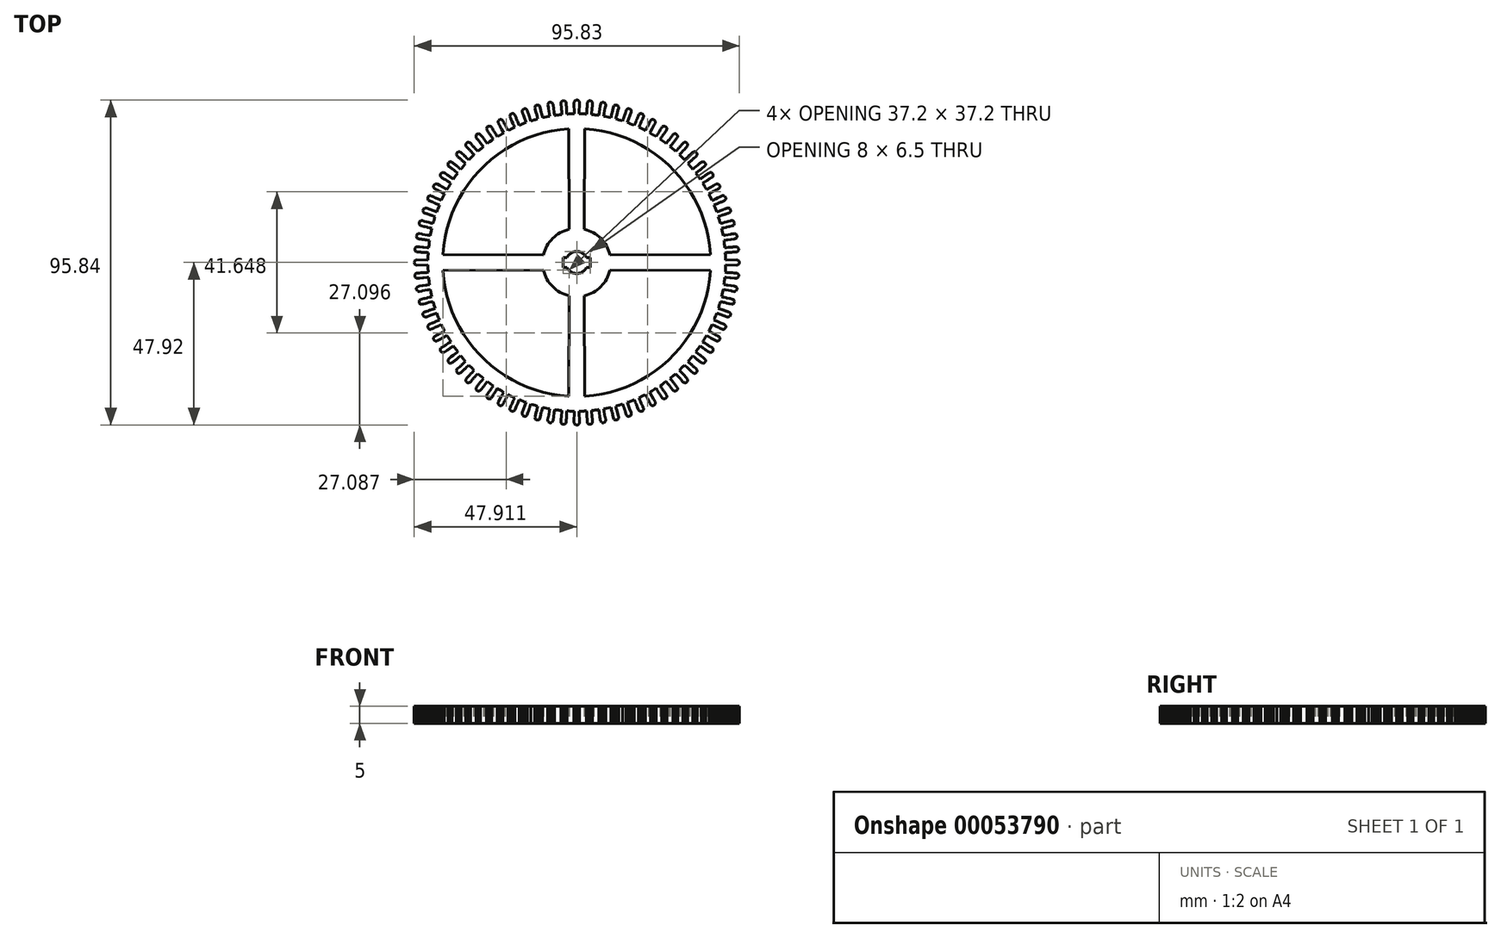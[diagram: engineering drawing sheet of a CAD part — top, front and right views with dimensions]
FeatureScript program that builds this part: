
annotation { "Feature Type Name" : "Feature", "Feature Type Description" : "" }
export const myFeature = defineFeature(function(context is Context, id is Id, definition is map)
    precondition{}
    {
        {
            var Q0;
            Q0=qCreatedBy(makeId("Top.planeOp"),FACE);
            var sketch = newSketch(context, id + "F0", { "sketchPlane" : qUnion([Q0])});
            skLineSegment(sketch, "E0", {"start": v(42.95, -0.72) * mm, "end": v(43.17, -0.73) * mm});
            skLineSegment(sketch, "E1", {"start": v(43.17, -0.73) * mm, "end": v(43.39, -0.73) * mm});
            skLineSegment(sketch, "E2", {"start": v(43.39, -0.73) * mm, "end": v(43.6, -0.73) * mm});
            skLineSegment(sketch, "E3", {"start": v(43.6, -0.73) * mm, "end": v(43.82, -0.74) * mm});
            skLineSegment(sketch, "E4", {"start": v(43.82, -0.74) * mm, "end": v(44.04, -0.74) * mm});
            skLineSegment(sketch, "E5", {"start": v(44.04, -0.74) * mm, "end": v(44.26, -0.74) * mm});
            skLineSegment(sketch, "E6", {"start": v(44.26, -0.74) * mm, "end": v(44.47, -0.75) * mm});
            skLineSegment(sketch, "E7", {"start": v(44.47, -0.75) * mm, "end": v(44.69, -0.75) * mm});
            skLineSegment(sketch, "E8", {"start": v(44.69, -0.75) * mm, "end": v(44.9, -0.75) * mm});
            skLineSegment(sketch, "E9", {"start": v(44.9, -0.75) * mm, "end": v(45.12, -0.76) * mm});
            skLineSegment(sketch, "E10", {"start": v(45.12, -0.76) * mm, "end": v(45.34, -0.76) * mm});
            skLineSegment(sketch, "E11", {"start": v(45.34, -0.76) * mm, "end": v(45.56, -0.76) * mm});
            skLineSegment(sketch, "E12", {"start": v(45.56, -0.76) * mm, "end": v(45.77, -0.77) * mm});
            skLineSegment(sketch, "E13", {"start": v(45.77, -0.77) * mm, "end": v(45.99, -0.77) * mm});
            skLineSegment(sketch, "E14", {"start": v(45.99, -0.77) * mm, "end": v(46.2, -0.78) * mm});
            skLineSegment(sketch, "E15", {"start": v(46.2, -0.78) * mm, "end": v(46.4, -0.75) * mm});
            skLineSegment(sketch, "E16", {"start": v(46.4, -0.75) * mm, "end": v(46.6, -0.67) * mm});
            skLineSegment(sketch, "E17", {"start": v(46.6, -0.67) * mm, "end": v(46.76, -0.55) * mm});
            skLineSegment(sketch, "E18", {"start": v(46.76, -0.55) * mm, "end": v(46.88, -0.39) * mm});
            skLineSegment(sketch, "E19", {"start": v(46.88, -0.39) * mm, "end": v(46.96, -0.2) * mm});
            skLineSegment(sketch, "E20", {"start": v(46.96, -0.2) * mm, "end": v(46.99, 0) * mm});
            skLineSegment(sketch, "E21", {"start": v(46.99, 0) * mm, "end": v(46.96, 0.2) * mm});
            skLineSegment(sketch, "E22", {"start": v(46.96, 0.2) * mm, "end": v(46.88, 0.39) * mm});
            skLineSegment(sketch, "E23", {"start": v(46.88, 0.39) * mm, "end": v(46.76, 0.55) * mm});
            skLineSegment(sketch, "E24", {"start": v(46.76, 0.55) * mm, "end": v(46.6, 0.67) * mm});
            skLineSegment(sketch, "E25", {"start": v(46.6, 0.67) * mm, "end": v(46.4, 0.75) * mm});
            skLineSegment(sketch, "E26", {"start": v(46.4, 0.75) * mm, "end": v(46.2, 0.78) * mm});
            skLineSegment(sketch, "E27", {"start": v(46.2, 0.78) * mm, "end": v(45.99, 0.77) * mm});
            skLineSegment(sketch, "E28", {"start": v(45.99, 0.77) * mm, "end": v(45.77, 0.77) * mm});
            skLineSegment(sketch, "E29", {"start": v(45.77, 0.77) * mm, "end": v(45.56, 0.76) * mm});
            skLineSegment(sketch, "E30", {"start": v(45.56, 0.76) * mm, "end": v(45.34, 0.76) * mm});
            skLineSegment(sketch, "E31", {"start": v(45.34, 0.76) * mm, "end": v(45.12, 0.76) * mm});
            skLineSegment(sketch, "E32", {"start": v(45.12, 0.76) * mm, "end": v(44.9, 0.75) * mm});
            skLineSegment(sketch, "E33", {"start": v(44.9, 0.75) * mm, "end": v(44.69, 0.75) * mm});
            skLineSegment(sketch, "E34", {"start": v(44.69, 0.75) * mm, "end": v(44.47, 0.75) * mm});
            skLineSegment(sketch, "E35", {"start": v(44.47, 0.75) * mm, "end": v(44.26, 0.74) * mm});
            skLineSegment(sketch, "E36", {"start": v(44.26, 0.74) * mm, "end": v(44.04, 0.74) * mm});
            skLineSegment(sketch, "E37", {"start": v(44.04, 0.74) * mm, "end": v(43.82, 0.74) * mm});
            skLineSegment(sketch, "E38", {"start": v(43.82, 0.74) * mm, "end": v(43.6, 0.73) * mm});
            skLineSegment(sketch, "E39", {"start": v(43.6, 0.73) * mm, "end": v(43.39, 0.73) * mm});
            skLineSegment(sketch, "E40", {"start": v(43.39, 0.73) * mm, "end": v(43.17, 0.73) * mm});
            skLineSegment(sketch, "E41", {"start": v(43.17, 0.73) * mm, "end": v(42.95, 0.72) * mm});
            skLineSegment(sketch, "E42", {"start": v(42.95, 0.72) * mm, "end": v(42.95, 0.94) * mm});
            skLineSegment(sketch, "E43", {"start": v(42.95, 0.94) * mm, "end": v(42.94, 1.17) * mm});
            skLineSegment(sketch, "E44", {"start": v(42.94, 1.17) * mm, "end": v(42.93, 1.39) * mm});
            skLineSegment(sketch, "E45", {"start": v(42.93, 1.39) * mm, "end": v(42.92, 1.61) * mm});
            skLineSegment(sketch, "E46", {"start": v(42.92, 1.61) * mm, "end": v(42.9, 1.83) * mm});
            skLineSegment(sketch, "E47", {"start": v(42.9, 1.83) * mm, "end": v(42.9, 2.06) * mm});
            skLineSegment(sketch, "E48", {"start": v(42.9, 2.06) * mm, "end": v(42.9, 2.28) * mm});
            skLineSegment(sketch, "E49", {"start": v(42.9, 2.28) * mm, "end": v(42.88, 2.5) * mm});
            skLineSegment(sketch, "E50", {"start": v(42.88, 2.5) * mm, "end": v(42.87, 2.72) * mm});
            skLineSegment(sketch, "E51", {"start": v(42.87, 2.72) * mm, "end": v(42.86, 2.9) * mm});
            skLineSegment(sketch, "E52", {"start": v(42.86, 2.9) * mm, "end": v(43.08, 2.92) * mm});
            skLineSegment(sketch, "E53", {"start": v(43.08, 2.92) * mm, "end": v(43.3, 2.93) * mm});
            skLineSegment(sketch, "E54", {"start": v(43.3, 2.93) * mm, "end": v(43.51, 2.95) * mm});
            skLineSegment(sketch, "E55", {"start": v(43.51, 2.95) * mm, "end": v(43.73, 2.96) * mm});
            skLineSegment(sketch, "E56", {"start": v(43.73, 2.96) * mm, "end": v(43.95, 2.98) * mm});
            skLineSegment(sketch, "E57", {"start": v(43.95, 2.98) * mm, "end": v(44.16, 3) * mm});
            skLineSegment(sketch, "E58", {"start": v(44.16, 3) * mm, "end": v(44.38, 3) * mm});
            skLineSegment(sketch, "E59", {"start": v(44.38, 3) * mm, "end": v(44.6, 3.02) * mm});
            skLineSegment(sketch, "E60", {"start": v(44.6, 3.02) * mm, "end": v(44.81, 3.03) * mm});
            skLineSegment(sketch, "E61", {"start": v(44.81, 3.03) * mm, "end": v(45.03, 3.05) * mm});
            skLineSegment(sketch, "E62", {"start": v(45.03, 3.05) * mm, "end": v(45.24, 3.06) * mm});
            skLineSegment(sketch, "E63", {"start": v(45.24, 3.06) * mm, "end": v(45.46, 3.08) * mm});
            skLineSegment(sketch, "E64", {"start": v(45.46, 3.08) * mm, "end": v(45.68, 3.1) * mm});
            skLineSegment(sketch, "E65", {"start": v(45.68, 3.1) * mm, "end": v(45.9, 3.1) * mm});
            skLineSegment(sketch, "E66", {"start": v(45.9, 3.1) * mm, "end": v(46.1, 3.12) * mm});
            skLineSegment(sketch, "E67", {"start": v(46.1, 3.12) * mm, "end": v(46.3, 3.16) * mm});
            skLineSegment(sketch, "E68", {"start": v(46.3, 3.16) * mm, "end": v(46.49, 3.25) * mm});
            skLineSegment(sketch, "E69", {"start": v(46.49, 3.25) * mm, "end": v(46.64, 3.39) * mm});
            skLineSegment(sketch, "E70", {"start": v(46.64, 3.39) * mm, "end": v(46.75, 3.56) * mm});
            skLineSegment(sketch, "E71", {"start": v(46.75, 3.56) * mm, "end": v(46.81, 3.75) * mm});
            skLineSegment(sketch, "E72", {"start": v(46.81, 3.75) * mm, "end": v(46.82, 3.96) * mm});
            skLineSegment(sketch, "E73", {"start": v(46.82, 3.96) * mm, "end": v(46.78, 4.16) * mm});
            skLineSegment(sketch, "E74", {"start": v(46.78, 4.16) * mm, "end": v(46.69, 4.34) * mm});
            skLineSegment(sketch, "E75", {"start": v(46.69, 4.34) * mm, "end": v(46.55, 4.49) * mm});
            skLineSegment(sketch, "E76", {"start": v(46.55, 4.49) * mm, "end": v(46.38, 4.6) * mm});
            skLineSegment(sketch, "E77", {"start": v(46.38, 4.6) * mm, "end": v(46.18, 4.66) * mm});
            skLineSegment(sketch, "E78", {"start": v(46.18, 4.66) * mm, "end": v(46.06, 4.67) * mm});
            skLineSegment(sketch, "E79", {"start": v(46.06, 4.67) * mm, "end": v(45.84, 4.65) * mm});
            skLineSegment(sketch, "E80", {"start": v(45.84, 4.65) * mm, "end": v(45.62, 4.63) * mm});
            skLineSegment(sketch, "E81", {"start": v(45.62, 4.63) * mm, "end": v(45.4, 4.6) * mm});
            skLineSegment(sketch, "E82", {"start": v(45.4, 4.6) * mm, "end": v(45.17, 4.59) * mm});
            skLineSegment(sketch, "E83", {"start": v(45.17, 4.59) * mm, "end": v(44.95, 4.56) * mm});
            skLineSegment(sketch, "E84", {"start": v(44.95, 4.56) * mm, "end": v(44.73, 4.54) * mm});
            skLineSegment(sketch, "E85", {"start": v(44.73, 4.54) * mm, "end": v(44.51, 4.52) * mm});
            skLineSegment(sketch, "E86", {"start": v(44.51, 4.52) * mm, "end": v(44.29, 4.5) * mm});
            skLineSegment(sketch, "E87", {"start": v(44.29, 4.5) * mm, "end": v(44.07, 4.48) * mm});
            skLineSegment(sketch, "E88", {"start": v(44.07, 4.48) * mm, "end": v(43.82, 4.45) * mm});
            skLineSegment(sketch, "E89", {"start": v(43.82, 4.45) * mm, "end": v(43.6, 4.43) * mm});
            skLineSegment(sketch, "E90", {"start": v(43.6, 4.43) * mm, "end": v(43.4, 4.4) * mm});
            skLineSegment(sketch, "E91", {"start": v(43.4, 4.4) * mm, "end": v(43.18, 4.39) * mm});
            skLineSegment(sketch, "E92", {"start": v(43.18, 4.39) * mm, "end": v(42.96, 4.37) * mm});
            skLineSegment(sketch, "E93", {"start": v(42.96, 4.37) * mm, "end": v(42.75, 4.34) * mm});
            skLineSegment(sketch, "E94", {"start": v(42.75, 4.34) * mm, "end": v(42.72, 4.56) * mm});
            skLineSegment(sketch, "E95", {"start": v(42.72, 4.56) * mm, "end": v(42.7, 4.79) * mm});
            skLineSegment(sketch, "E96", {"start": v(42.7, 4.79) * mm, "end": v(42.66, 5) * mm});
            skLineSegment(sketch, "E97", {"start": v(42.66, 5) * mm, "end": v(42.64, 5.23) * mm});
            skLineSegment(sketch, "E98", {"start": v(42.64, 5.23) * mm, "end": v(42.6, 5.45) * mm});
            skLineSegment(sketch, "E99", {"start": v(42.6, 5.45) * mm, "end": v(42.58, 5.67) * mm});
            skLineSegment(sketch, "E100", {"start": v(42.58, 5.67) * mm, "end": v(42.55, 5.9) * mm});
            skLineSegment(sketch, "E101", {"start": v(42.55, 5.9) * mm, "end": v(42.53, 6.11) * mm});
            skLineSegment(sketch, "E102", {"start": v(42.53, 6.11) * mm, "end": v(42.5, 6.33) * mm});
            skLineSegment(sketch, "E103", {"start": v(42.5, 6.33) * mm, "end": v(42.48, 6.51) * mm});
            skLineSegment(sketch, "E104", {"start": v(42.48, 6.51) * mm, "end": v(42.69, 6.54) * mm});
            skLineSegment(sketch, "E105", {"start": v(42.69, 6.54) * mm, "end": v(42.9, 6.57) * mm});
            skLineSegment(sketch, "E106", {"start": v(42.9, 6.57) * mm, "end": v(43.12, 6.6) * mm});
            skLineSegment(sketch, "E107", {"start": v(43.12, 6.6) * mm, "end": v(43.33, 6.64) * mm});
            skLineSegment(sketch, "E108", {"start": v(43.33, 6.64) * mm, "end": v(43.55, 6.67) * mm});
            skLineSegment(sketch, "E109", {"start": v(43.55, 6.67) * mm, "end": v(43.76, 6.7) * mm});
            skLineSegment(sketch, "E110", {"start": v(43.76, 6.7) * mm, "end": v(43.98, 6.74) * mm});
            skLineSegment(sketch, "E111", {"start": v(43.98, 6.74) * mm, "end": v(44.19, 6.77) * mm});
            skLineSegment(sketch, "E112", {"start": v(44.19, 6.77) * mm, "end": v(44.4, 6.8) * mm});
            skLineSegment(sketch, "E113", {"start": v(44.4, 6.8) * mm, "end": v(44.62, 6.83) * mm});
            skLineSegment(sketch, "E114", {"start": v(44.62, 6.83) * mm, "end": v(44.83, 6.86) * mm});
            skLineSegment(sketch, "E115", {"start": v(44.83, 6.86) * mm, "end": v(45.05, 6.9) * mm});
            skLineSegment(sketch, "E116", {"start": v(45.05, 6.9) * mm, "end": v(45.26, 6.93) * mm});
            skLineSegment(sketch, "E117", {"start": v(45.26, 6.93) * mm, "end": v(45.48, 6.96) * mm});
            skLineSegment(sketch, "E118", {"start": v(45.48, 6.96) * mm, "end": v(45.69, 7) * mm});
            skLineSegment(sketch, "E119", {"start": v(45.69, 7) * mm, "end": v(45.89, 7.05) * mm});
            skLineSegment(sketch, "E120", {"start": v(45.89, 7.05) * mm, "end": v(46.06, 7.16) * mm});
            skLineSegment(sketch, "E121", {"start": v(46.06, 7.16) * mm, "end": v(46.2, 7.3) * mm});
            skLineSegment(sketch, "E122", {"start": v(46.2, 7.3) * mm, "end": v(46.3, 7.49) * mm});
            skLineSegment(sketch, "E123", {"start": v(46.3, 7.49) * mm, "end": v(46.34, 7.68) * mm});
            skLineSegment(sketch, "E124", {"start": v(46.34, 7.68) * mm, "end": v(46.33, 7.89) * mm});
            skLineSegment(sketch, "E125", {"start": v(46.33, 7.89) * mm, "end": v(46.27, 8.08) * mm});
            skLineSegment(sketch, "E126", {"start": v(46.27, 8.08) * mm, "end": v(46.17, 8.25) * mm});
            skLineSegment(sketch, "E127", {"start": v(46.17, 8.25) * mm, "end": v(46.02, 8.4) * mm});
            skLineSegment(sketch, "E128", {"start": v(46.02, 8.4) * mm, "end": v(45.84, 8.49) * mm});
            skLineSegment(sketch, "E129", {"start": v(45.84, 8.49) * mm, "end": v(45.64, 8.53) * mm});
            skLineSegment(sketch, "E130", {"start": v(45.64, 8.53) * mm, "end": v(45.56, 8.53) * mm});
            skLineSegment(sketch, "E131", {"start": v(45.56, 8.53) * mm, "end": v(45.33, 8.5) * mm});
            skLineSegment(sketch, "E132", {"start": v(45.33, 8.5) * mm, "end": v(45.11, 8.46) * mm});
            skLineSegment(sketch, "E133", {"start": v(45.11, 8.46) * mm, "end": v(44.9, 8.43) * mm});
            skLineSegment(sketch, "E134", {"start": v(44.9, 8.43) * mm, "end": v(44.69, 8.39) * mm});
            skLineSegment(sketch, "E135", {"start": v(44.69, 8.39) * mm, "end": v(44.48, 8.35) * mm});
            skLineSegment(sketch, "E136", {"start": v(44.48, 8.35) * mm, "end": v(44.26, 8.3) * mm});
            skLineSegment(sketch, "E137", {"start": v(44.26, 8.3) * mm, "end": v(44.05, 8.27) * mm});
            skLineSegment(sketch, "E138", {"start": v(44.05, 8.27) * mm, "end": v(43.84, 8.23) * mm});
            skLineSegment(sketch, "E139", {"start": v(43.84, 8.23) * mm, "end": v(43.62, 8.2) * mm});
            skLineSegment(sketch, "E140", {"start": v(43.62, 8.2) * mm, "end": v(43.4, 8.15) * mm});
            skLineSegment(sketch, "E141", {"start": v(43.4, 8.15) * mm, "end": v(43.2, 8.11) * mm});
            skLineSegment(sketch, "E142", {"start": v(43.2, 8.11) * mm, "end": v(42.98, 8.07) * mm});
            skLineSegment(sketch, "E143", {"start": v(42.98, 8.07) * mm, "end": v(42.77, 8.03) * mm});
            skLineSegment(sketch, "E144", {"start": v(42.77, 8.03) * mm, "end": v(42.56, 8) * mm});
            skLineSegment(sketch, "E145", {"start": v(42.56, 8) * mm, "end": v(42.34, 7.95) * mm});
            skLineSegment(sketch, "E146", {"start": v(42.34, 7.95) * mm, "end": v(42.24, 7.94) * mm});
            skLineSegment(sketch, "E147", {"start": v(42.24, 7.94) * mm, "end": v(42.2, 8.15) * mm});
            skLineSegment(sketch, "E148", {"start": v(42.2, 8.15) * mm, "end": v(42.15, 8.37) * mm});
            skLineSegment(sketch, "E149", {"start": v(42.15, 8.37) * mm, "end": v(42.1, 8.59) * mm});
            skLineSegment(sketch, "E150", {"start": v(42.1, 8.59) * mm, "end": v(42.05, 8.8) * mm});
            skLineSegment(sketch, "E151", {"start": v(42.05, 8.8) * mm, "end": v(42, 9.03) * mm});
            skLineSegment(sketch, "E152", {"start": v(42, 9.03) * mm, "end": v(41.96, 9.24) * mm});
            skLineSegment(sketch, "E153", {"start": v(41.96, 9.24) * mm, "end": v(41.92, 9.46) * mm});
            skLineSegment(sketch, "E154", {"start": v(41.92, 9.46) * mm, "end": v(41.87, 9.68) * mm});
            skLineSegment(sketch, "E155", {"start": v(41.87, 9.68) * mm, "end": v(41.83, 9.9) * mm});
            skLineSegment(sketch, "E156", {"start": v(41.83, 9.9) * mm, "end": v(41.79, 10.07) * mm});
            skLineSegment(sketch, "E157", {"start": v(41.79, 10.07) * mm, "end": v(42, 10.12) * mm});
            skLineSegment(sketch, "E158", {"start": v(42, 10.12) * mm, "end": v(42.21, 10.17) * mm});
            skLineSegment(sketch, "E159", {"start": v(42.21, 10.17) * mm, "end": v(42.42, 10.22) * mm});
            skLineSegment(sketch, "E160", {"start": v(42.42, 10.22) * mm, "end": v(42.63, 10.27) * mm});
            skLineSegment(sketch, "E161", {"start": v(42.63, 10.27) * mm, "end": v(42.84, 10.32) * mm});
            skLineSegment(sketch, "E162", {"start": v(42.84, 10.32) * mm, "end": v(43.05, 10.37) * mm});
            skLineSegment(sketch, "E163", {"start": v(43.05, 10.37) * mm, "end": v(43.27, 10.42) * mm});
            skLineSegment(sketch, "E164", {"start": v(43.27, 10.42) * mm, "end": v(43.48, 10.47) * mm});
            skLineSegment(sketch, "E165", {"start": v(43.48, 10.47) * mm, "end": v(43.69, 10.52) * mm});
            skLineSegment(sketch, "E166", {"start": v(43.69, 10.52) * mm, "end": v(43.9, 10.57) * mm});
            skLineSegment(sketch, "E167", {"start": v(43.9, 10.57) * mm, "end": v(44.1, 10.62) * mm});
            skLineSegment(sketch, "E168", {"start": v(44.1, 10.62) * mm, "end": v(44.32, 10.67) * mm});
            skLineSegment(sketch, "E169", {"start": v(44.32, 10.67) * mm, "end": v(44.53, 10.72) * mm});
            skLineSegment(sketch, "E170", {"start": v(44.53, 10.72) * mm, "end": v(44.74, 10.77) * mm});
            skLineSegment(sketch, "E171", {"start": v(44.74, 10.77) * mm, "end": v(44.95, 10.82) * mm});
            skLineSegment(sketch, "E172", {"start": v(44.95, 10.82) * mm, "end": v(45.14, 10.9) * mm});
            skLineSegment(sketch, "E173", {"start": v(45.14, 10.9) * mm, "end": v(45.3, 11.01) * mm});
            skLineSegment(sketch, "E174", {"start": v(45.3, 11.01) * mm, "end": v(45.43, 11.17) * mm});
            skLineSegment(sketch, "E175", {"start": v(45.43, 11.17) * mm, "end": v(45.51, 11.36) * mm});
            skLineSegment(sketch, "E176", {"start": v(45.51, 11.36) * mm, "end": v(45.54, 11.56) * mm});
            skLineSegment(sketch, "E177", {"start": v(45.54, 11.56) * mm, "end": v(45.52, 11.76) * mm});
            skLineSegment(sketch, "E178", {"start": v(45.52, 11.76) * mm, "end": v(45.45, 11.95) * mm});
            skLineSegment(sketch, "E179", {"start": v(45.45, 11.95) * mm, "end": v(45.32, 12.11) * mm});
            skLineSegment(sketch, "E180", {"start": v(45.32, 12.11) * mm, "end": v(45.16, 12.24) * mm});
            skLineSegment(sketch, "E181", {"start": v(45.16, 12.24) * mm, "end": v(44.98, 12.32) * mm});
            skLineSegment(sketch, "E182", {"start": v(44.98, 12.32) * mm, "end": v(44.77, 12.35) * mm});
            skLineSegment(sketch, "E183", {"start": v(44.77, 12.35) * mm, "end": v(44.57, 12.32) * mm});
            skLineSegment(sketch, "E184", {"start": v(44.57, 12.32) * mm, "end": v(44.36, 12.27) * mm});
            skLineSegment(sketch, "E185", {"start": v(44.36, 12.27) * mm, "end": v(44.15, 12.2) * mm});
            skLineSegment(sketch, "E186", {"start": v(44.15, 12.2) * mm, "end": v(43.94, 12.15) * mm});
            skLineSegment(sketch, "E187", {"start": v(43.94, 12.15) * mm, "end": v(43.74, 12.1) * mm});
            skLineSegment(sketch, "E188", {"start": v(43.74, 12.1) * mm, "end": v(43.53, 12.04) * mm});
            skLineSegment(sketch, "E189", {"start": v(43.53, 12.04) * mm, "end": v(43.32, 11.98) * mm});
            skLineSegment(sketch, "E190", {"start": v(43.32, 11.98) * mm, "end": v(43.1, 11.93) * mm});
            skLineSegment(sketch, "E191", {"start": v(43.1, 11.93) * mm, "end": v(42.9, 11.87) * mm});
            skLineSegment(sketch, "E192", {"start": v(42.9, 11.87) * mm, "end": v(42.69, 11.81) * mm});
            skLineSegment(sketch, "E193", {"start": v(42.69, 11.81) * mm, "end": v(42.48, 11.76) * mm});
            skLineSegment(sketch, "E194", {"start": v(42.48, 11.76) * mm, "end": v(42.27, 11.7) * mm});
            skLineSegment(sketch, "E195", {"start": v(42.27, 11.7) * mm, "end": v(42.06, 11.64) * mm});
            skLineSegment(sketch, "E196", {"start": v(42.06, 11.64) * mm, "end": v(41.85, 11.59) * mm});
            skLineSegment(sketch, "E197", {"start": v(41.85, 11.59) * mm, "end": v(41.64, 11.53) * mm});
            skLineSegment(sketch, "E198", {"start": v(41.64, 11.53) * mm, "end": v(41.43, 11.47) * mm});
            skLineSegment(sketch, "E199", {"start": v(41.43, 11.47) * mm, "end": v(41.37, 11.69) * mm});
            skLineSegment(sketch, "E200", {"start": v(41.37, 11.69) * mm, "end": v(41.3, 11.9) * mm});
            skLineSegment(sketch, "E201", {"start": v(41.3, 11.9) * mm, "end": v(41.24, 12.11) * mm});
            skLineSegment(sketch, "E202", {"start": v(41.24, 12.11) * mm, "end": v(41.18, 12.33) * mm});
            skLineSegment(sketch, "E203", {"start": v(41.18, 12.33) * mm, "end": v(41.12, 12.54) * mm});
            skLineSegment(sketch, "E204", {"start": v(41.12, 12.54) * mm, "end": v(41.05, 12.75) * mm});
            skLineSegment(sketch, "E205", {"start": v(41.05, 12.75) * mm, "end": v(41, 12.97) * mm});
            skLineSegment(sketch, "E206", {"start": v(41, 12.97) * mm, "end": v(40.93, 13.18) * mm});
            skLineSegment(sketch, "E207", {"start": v(40.93, 13.18) * mm, "end": v(40.86, 13.4) * mm});
            skLineSegment(sketch, "E208", {"start": v(40.86, 13.4) * mm, "end": v(40.81, 13.57) * mm});
            skLineSegment(sketch, "E209", {"start": v(40.81, 13.57) * mm, "end": v(41.02, 13.63) * mm});
            skLineSegment(sketch, "E210", {"start": v(41.02, 13.63) * mm, "end": v(41.22, 13.7) * mm});
            skLineSegment(sketch, "E211", {"start": v(41.22, 13.7) * mm, "end": v(41.43, 13.77) * mm});
            skLineSegment(sketch, "E212", {"start": v(41.43, 13.77) * mm, "end": v(41.64, 13.83) * mm});
            skLineSegment(sketch, "E213", {"start": v(41.64, 13.83) * mm, "end": v(41.84, 13.9) * mm});
            skLineSegment(sketch, "E214", {"start": v(41.84, 13.9) * mm, "end": v(42.05, 13.97) * mm});
            skLineSegment(sketch, "E215", {"start": v(42.05, 13.97) * mm, "end": v(42.25, 14.03) * mm});
            skLineSegment(sketch, "E216", {"start": v(42.25, 14.03) * mm, "end": v(42.46, 14.1) * mm});
            skLineSegment(sketch, "E217", {"start": v(42.46, 14.1) * mm, "end": v(42.67, 14.17) * mm});
            skLineSegment(sketch, "E218", {"start": v(42.67, 14.17) * mm, "end": v(42.87, 14.24) * mm});
            skLineSegment(sketch, "E219", {"start": v(42.87, 14.24) * mm, "end": v(43.08, 14.3) * mm});
            skLineSegment(sketch, "E220", {"start": v(43.08, 14.3) * mm, "end": v(43.28, 14.37) * mm});
            skLineSegment(sketch, "E221", {"start": v(43.28, 14.37) * mm, "end": v(43.5, 14.44) * mm});
            skLineSegment(sketch, "E222", {"start": v(43.5, 14.44) * mm, "end": v(43.7, 14.5) * mm});
            skLineSegment(sketch, "E223", {"start": v(43.7, 14.5) * mm, "end": v(43.9, 14.57) * mm});
            skLineSegment(sketch, "E224", {"start": v(43.9, 14.57) * mm, "end": v(44.09, 14.66) * mm});
            skLineSegment(sketch, "E225", {"start": v(44.09, 14.66) * mm, "end": v(44.24, 14.8) * mm});
            skLineSegment(sketch, "E226", {"start": v(44.24, 14.8) * mm, "end": v(44.35, 14.96) * mm});
            skLineSegment(sketch, "E227", {"start": v(44.35, 14.96) * mm, "end": v(44.42, 15.16) * mm});
            skLineSegment(sketch, "E228", {"start": v(44.42, 15.16) * mm, "end": v(44.43, 15.36) * mm});
            skLineSegment(sketch, "E229", {"start": v(44.43, 15.36) * mm, "end": v(44.4, 15.56) * mm});
            skLineSegment(sketch, "E230", {"start": v(44.4, 15.56) * mm, "end": v(44.3, 15.74) * mm});
            skLineSegment(sketch, "E231", {"start": v(44.3, 15.74) * mm, "end": v(44.16, 15.9) * mm});
            skLineSegment(sketch, "E232", {"start": v(44.16, 15.9) * mm, "end": v(44, 16) * mm});
            skLineSegment(sketch, "E233", {"start": v(44, 16) * mm, "end": v(43.8, 16.07) * mm});
            skLineSegment(sketch, "E234", {"start": v(43.8, 16.07) * mm, "end": v(43.64, 16.08) * mm});
            skLineSegment(sketch, "E235", {"start": v(43.64, 16.08) * mm, "end": v(43.44, 16.05) * mm});
            skLineSegment(sketch, "E236", {"start": v(43.44, 16.05) * mm, "end": v(43.23, 15.98) * mm});
            skLineSegment(sketch, "E237", {"start": v(43.23, 15.98) * mm, "end": v(43.02, 15.9) * mm});
            skLineSegment(sketch, "E238", {"start": v(43.02, 15.9) * mm, "end": v(42.8, 15.82) * mm});
            skLineSegment(sketch, "E239", {"start": v(42.8, 15.82) * mm, "end": v(42.58, 15.74) * mm});
            skLineSegment(sketch, "E240", {"start": v(42.58, 15.74) * mm, "end": v(42.38, 15.67) * mm});
            skLineSegment(sketch, "E241", {"start": v(42.38, 15.67) * mm, "end": v(42.18, 15.6) * mm});
            skLineSegment(sketch, "E242", {"start": v(42.18, 15.6) * mm, "end": v(41.97, 15.52) * mm});
            skLineSegment(sketch, "E243", {"start": v(41.97, 15.52) * mm, "end": v(41.77, 15.45) * mm});
            skLineSegment(sketch, "E244", {"start": v(41.77, 15.45) * mm, "end": v(41.57, 15.37) * mm});
            skLineSegment(sketch, "E245", {"start": v(41.57, 15.37) * mm, "end": v(41.36, 15.3) * mm});
            skLineSegment(sketch, "E246", {"start": v(41.36, 15.3) * mm, "end": v(41.16, 15.23) * mm});
            skLineSegment(sketch, "E247", {"start": v(41.16, 15.23) * mm, "end": v(40.95, 15.15) * mm});
            skLineSegment(sketch, "E248", {"start": v(40.95, 15.15) * mm, "end": v(40.75, 15.08) * mm});
            skLineSegment(sketch, "E249", {"start": v(40.75, 15.08) * mm, "end": v(40.55, 15) * mm});
            skLineSegment(sketch, "E250", {"start": v(40.55, 15) * mm, "end": v(40.34, 14.93) * mm});
            skLineSegment(sketch, "E251", {"start": v(40.34, 14.93) * mm, "end": v(40.26, 15.14) * mm});
            skLineSegment(sketch, "E252", {"start": v(40.26, 15.14) * mm, "end": v(40.18, 15.35) * mm});
            skLineSegment(sketch, "E253", {"start": v(40.18, 15.35) * mm, "end": v(40.1, 15.55) * mm});
            skLineSegment(sketch, "E254", {"start": v(40.1, 15.55) * mm, "end": v(40.02, 15.76) * mm});
            skLineSegment(sketch, "E255", {"start": v(40.02, 15.76) * mm, "end": v(39.94, 15.97) * mm});
            skLineSegment(sketch, "E256", {"start": v(39.94, 15.97) * mm, "end": v(39.86, 16.18) * mm});
            skLineSegment(sketch, "E257", {"start": v(39.86, 16.18) * mm, "end": v(39.78, 16.38) * mm});
            skLineSegment(sketch, "E258", {"start": v(39.78, 16.38) * mm, "end": v(39.7, 16.6) * mm});
            skLineSegment(sketch, "E259", {"start": v(39.7, 16.6) * mm, "end": v(39.61, 16.8) * mm});
            skLineSegment(sketch, "E260", {"start": v(39.61, 16.8) * mm, "end": v(39.55, 16.97) * mm});
            skLineSegment(sketch, "E261", {"start": v(39.55, 16.97) * mm, "end": v(39.75, 17.05) * mm});
            skLineSegment(sketch, "E262", {"start": v(39.75, 17.05) * mm, "end": v(39.95, 17.13) * mm});
            skLineSegment(sketch, "E263", {"start": v(39.95, 17.13) * mm, "end": v(40.15, 17.22) * mm});
            skLineSegment(sketch, "E264", {"start": v(40.15, 17.22) * mm, "end": v(40.35, 17.3) * mm});
            skLineSegment(sketch, "E265", {"start": v(40.35, 17.3) * mm, "end": v(40.55, 17.39) * mm});
            skLineSegment(sketch, "E266", {"start": v(40.55, 17.39) * mm, "end": v(40.75, 17.47) * mm});
            skLineSegment(sketch, "E267", {"start": v(40.75, 17.47) * mm, "end": v(40.95, 17.55) * mm});
            skLineSegment(sketch, "E268", {"start": v(40.95, 17.55) * mm, "end": v(41.15, 17.64) * mm});
            skLineSegment(sketch, "E269", {"start": v(41.15, 17.64) * mm, "end": v(41.35, 17.72) * mm});
            skLineSegment(sketch, "E270", {"start": v(41.35, 17.72) * mm, "end": v(41.55, 17.8) * mm});
            skLineSegment(sketch, "E271", {"start": v(41.55, 17.8) * mm, "end": v(41.75, 17.89) * mm});
            skLineSegment(sketch, "E272", {"start": v(41.75, 17.89) * mm, "end": v(41.95, 17.97) * mm});
            skLineSegment(sketch, "E273", {"start": v(41.95, 17.97) * mm, "end": v(42.15, 18.06) * mm});
            skLineSegment(sketch, "E274", {"start": v(42.15, 18.06) * mm, "end": v(42.35, 18.14) * mm});
            skLineSegment(sketch, "E275", {"start": v(42.35, 18.14) * mm, "end": v(42.55, 18.22) * mm});
            skLineSegment(sketch, "E276", {"start": v(42.55, 18.22) * mm, "end": v(42.72, 18.33) * mm});
            skLineSegment(sketch, "E277", {"start": v(42.72, 18.33) * mm, "end": v(42.86, 18.47) * mm});
            skLineSegment(sketch, "E278", {"start": v(42.86, 18.47) * mm, "end": v(42.96, 18.65) * mm});
            skLineSegment(sketch, "E279", {"start": v(42.96, 18.65) * mm, "end": v(43.01, 18.85) * mm});
            skLineSegment(sketch, "E280", {"start": v(43.01, 18.85) * mm, "end": v(43, 19.05) * mm});
            skLineSegment(sketch, "E281", {"start": v(43, 19.05) * mm, "end": v(42.95, 19.25) * mm});
            skLineSegment(sketch, "E282", {"start": v(42.95, 19.25) * mm, "end": v(42.85, 19.42) * mm});
            skLineSegment(sketch, "E283", {"start": v(42.85, 19.42) * mm, "end": v(42.7, 19.56) * mm});
            skLineSegment(sketch, "E284", {"start": v(42.7, 19.56) * mm, "end": v(42.52, 19.66) * mm});
            skLineSegment(sketch, "E285", {"start": v(42.52, 19.66) * mm, "end": v(42.32, 19.7) * mm});
            skLineSegment(sketch, "E286", {"start": v(42.32, 19.7) * mm, "end": v(42.24, 19.71) * mm});
            skLineSegment(sketch, "E287", {"start": v(42.24, 19.71) * mm, "end": v(42.04, 19.69) * mm});
            skLineSegment(sketch, "E288", {"start": v(42.04, 19.69) * mm, "end": v(41.83, 19.6) * mm});
            skLineSegment(sketch, "E289", {"start": v(41.83, 19.6) * mm, "end": v(41.63, 19.5) * mm});
            skLineSegment(sketch, "E290", {"start": v(41.63, 19.5) * mm, "end": v(41.43, 19.42) * mm});
            skLineSegment(sketch, "E291", {"start": v(41.43, 19.42) * mm, "end": v(41.23, 19.33) * mm});
            skLineSegment(sketch, "E292", {"start": v(41.23, 19.33) * mm, "end": v(41.04, 19.24) * mm});
            skLineSegment(sketch, "E293", {"start": v(41.04, 19.24) * mm, "end": v(40.84, 19.15) * mm});
            skLineSegment(sketch, "E294", {"start": v(40.84, 19.15) * mm, "end": v(40.64, 19.06) * mm});
            skLineSegment(sketch, "E295", {"start": v(40.64, 19.06) * mm, "end": v(40.45, 18.97) * mm});
            skLineSegment(sketch, "E296", {"start": v(40.45, 18.97) * mm, "end": v(40.25, 18.88) * mm});
            skLineSegment(sketch, "E297", {"start": v(40.25, 18.88) * mm, "end": v(40.05, 18.79) * mm});
            skLineSegment(sketch, "E298", {"start": v(40.05, 18.79) * mm, "end": v(39.86, 18.7) * mm});
            skLineSegment(sketch, "E299", {"start": v(39.86, 18.7) * mm, "end": v(39.66, 18.6) * mm});
            skLineSegment(sketch, "E300", {"start": v(39.66, 18.6) * mm, "end": v(39.46, 18.52) * mm});
            skLineSegment(sketch, "E301", {"start": v(39.46, 18.52) * mm, "end": v(39.26, 18.42) * mm});
            skLineSegment(sketch, "E302", {"start": v(39.26, 18.42) * mm, "end": v(39.07, 18.33) * mm});
            skLineSegment(sketch, "E303", {"start": v(39.07, 18.33) * mm, "end": v(38.97, 18.29) * mm});
            skLineSegment(sketch, "E304", {"start": v(38.97, 18.29) * mm, "end": v(38.87, 18.49) * mm});
            skLineSegment(sketch, "E305", {"start": v(38.87, 18.49) * mm, "end": v(38.77, 18.69) * mm});
            skLineSegment(sketch, "E306", {"start": v(38.77, 18.69) * mm, "end": v(38.68, 18.89) * mm});
            skLineSegment(sketch, "E307", {"start": v(38.68, 18.89) * mm, "end": v(38.58, 19.09) * mm});
            skLineSegment(sketch, "E308", {"start": v(38.58, 19.09) * mm, "end": v(38.48, 19.29) * mm});
            skLineSegment(sketch, "E309", {"start": v(38.48, 19.29) * mm, "end": v(38.38, 19.49) * mm});
            skLineSegment(sketch, "E310", {"start": v(38.38, 19.49) * mm, "end": v(38.28, 19.69) * mm});
            skLineSegment(sketch, "E311", {"start": v(38.28, 19.69) * mm, "end": v(38.19, 19.89) * mm});
            skLineSegment(sketch, "E312", {"start": v(38.19, 19.89) * mm, "end": v(38.09, 20.09) * mm});
            skLineSegment(sketch, "E313", {"start": v(38.09, 20.09) * mm, "end": v(38, 20.25) * mm});
            skLineSegment(sketch, "E314", {"start": v(38, 20.25) * mm, "end": v(38.2, 20.35) * mm});
            skLineSegment(sketch, "E315", {"start": v(38.2, 20.35) * mm, "end": v(38.4, 20.45) * mm});
            skLineSegment(sketch, "E316", {"start": v(38.4, 20.45) * mm, "end": v(38.59, 20.55) * mm});
            skLineSegment(sketch, "E317", {"start": v(38.59, 20.55) * mm, "end": v(38.78, 20.65) * mm});
            skLineSegment(sketch, "E318", {"start": v(38.78, 20.65) * mm, "end": v(38.97, 20.75) * mm});
            skLineSegment(sketch, "E319", {"start": v(38.97, 20.75) * mm, "end": v(39.16, 20.85) * mm});
            skLineSegment(sketch, "E320", {"start": v(39.16, 20.85) * mm, "end": v(39.36, 20.95) * mm});
            skLineSegment(sketch, "E321", {"start": v(39.36, 20.95) * mm, "end": v(39.55, 21.05) * mm});
            skLineSegment(sketch, "E322", {"start": v(39.55, 21.05) * mm, "end": v(39.74, 21.15) * mm});
            skLineSegment(sketch, "E323", {"start": v(39.74, 21.15) * mm, "end": v(39.93, 21.25) * mm});
            skLineSegment(sketch, "E324", {"start": v(39.93, 21.25) * mm, "end": v(40.12, 21.35) * mm});
            skLineSegment(sketch, "E325", {"start": v(40.12, 21.35) * mm, "end": v(40.32, 21.45) * mm});
            skLineSegment(sketch, "E326", {"start": v(40.32, 21.45) * mm, "end": v(40.5, 21.55) * mm});
            skLineSegment(sketch, "E327", {"start": v(40.5, 21.55) * mm, "end": v(40.7, 21.65) * mm});
            skLineSegment(sketch, "E328", {"start": v(40.7, 21.65) * mm, "end": v(40.9, 21.75) * mm});
            skLineSegment(sketch, "E329", {"start": v(40.9, 21.75) * mm, "end": v(41.06, 21.87) * mm});
            skLineSegment(sketch, "E330", {"start": v(41.06, 21.87) * mm, "end": v(41.19, 22.03) * mm});
            skLineSegment(sketch, "E331", {"start": v(41.19, 22.03) * mm, "end": v(41.27, 22.21) * mm});
            skLineSegment(sketch, "E332", {"start": v(41.27, 22.21) * mm, "end": v(41.3, 22.41) * mm});
            skLineSegment(sketch, "E333", {"start": v(41.3, 22.41) * mm, "end": v(41.28, 22.62) * mm});
            skLineSegment(sketch, "E334", {"start": v(41.28, 22.62) * mm, "end": v(41.21, 22.8) * mm});
            skLineSegment(sketch, "E335", {"start": v(41.21, 22.8) * mm, "end": v(41.1, 22.97) * mm});
            skLineSegment(sketch, "E336", {"start": v(41.1, 22.97) * mm, "end": v(40.93, 23.1) * mm});
            skLineSegment(sketch, "E337", {"start": v(40.93, 23.1) * mm, "end": v(40.75, 23.18) * mm});
            skLineSegment(sketch, "E338", {"start": v(40.75, 23.18) * mm, "end": v(40.55, 23.21) * mm});
            skLineSegment(sketch, "E339", {"start": v(40.55, 23.21) * mm, "end": v(40.34, 23.19) * mm});
            skLineSegment(sketch, "E340", {"start": v(40.34, 23.19) * mm, "end": v(40.16, 23.12) * mm});
            skLineSegment(sketch, "E341", {"start": v(40.16, 23.12) * mm, "end": v(39.97, 23) * mm});
            skLineSegment(sketch, "E342", {"start": v(39.97, 23) * mm, "end": v(39.78, 22.9) * mm});
            skLineSegment(sketch, "E343", {"start": v(39.78, 22.9) * mm, "end": v(39.59, 22.8) * mm});
            skLineSegment(sketch, "E344", {"start": v(39.59, 22.8) * mm, "end": v(39.4, 22.7) * mm});
            skLineSegment(sketch, "E345", {"start": v(39.4, 22.7) * mm, "end": v(39.21, 22.58) * mm});
            skLineSegment(sketch, "E346", {"start": v(39.21, 22.58) * mm, "end": v(39.02, 22.48) * mm});
            skLineSegment(sketch, "E347", {"start": v(39.02, 22.48) * mm, "end": v(38.83, 22.37) * mm});
            skLineSegment(sketch, "E348", {"start": v(38.83, 22.37) * mm, "end": v(38.64, 22.27) * mm});
            skLineSegment(sketch, "E349", {"start": v(38.64, 22.27) * mm, "end": v(38.46, 22.16) * mm});
            skLineSegment(sketch, "E350", {"start": v(38.46, 22.16) * mm, "end": v(38.27, 22.05) * mm});
            skLineSegment(sketch, "E351", {"start": v(38.27, 22.05) * mm, "end": v(38.08, 21.95) * mm});
            skLineSegment(sketch, "E352", {"start": v(38.08, 21.95) * mm, "end": v(37.89, 21.84) * mm});
            skLineSegment(sketch, "E353", {"start": v(37.89, 21.84) * mm, "end": v(37.7, 21.73) * mm});
            skLineSegment(sketch, "E354", {"start": v(37.7, 21.73) * mm, "end": v(37.51, 21.63) * mm});
            skLineSegment(sketch, "E355", {"start": v(37.51, 21.63) * mm, "end": v(37.32, 21.52) * mm});
            skLineSegment(sketch, "E356", {"start": v(37.32, 21.52) * mm, "end": v(37.2, 21.71) * mm});
            skLineSegment(sketch, "E357", {"start": v(37.2, 21.71) * mm, "end": v(37.1, 21.9) * mm});
            skLineSegment(sketch, "E358", {"start": v(37.1, 21.9) * mm, "end": v(36.98, 22.1) * mm});
            skLineSegment(sketch, "E359", {"start": v(36.98, 22.1) * mm, "end": v(36.87, 22.29) * mm});
            skLineSegment(sketch, "E360", {"start": v(36.87, 22.29) * mm, "end": v(36.75, 22.48) * mm});
            skLineSegment(sketch, "E361", {"start": v(36.75, 22.48) * mm, "end": v(36.64, 22.67) * mm});
            skLineSegment(sketch, "E362", {"start": v(36.64, 22.67) * mm, "end": v(36.52, 22.86) * mm});
            skLineSegment(sketch, "E363", {"start": v(36.52, 22.86) * mm, "end": v(36.41, 23.05) * mm});
            skLineSegment(sketch, "E364", {"start": v(36.41, 23.05) * mm, "end": v(36.3, 23.24) * mm});
            skLineSegment(sketch, "E365", {"start": v(36.3, 23.24) * mm, "end": v(36.2, 23.4) * mm});
            skLineSegment(sketch, "E366", {"start": v(36.2, 23.4) * mm, "end": v(36.39, 23.51) * mm});
            skLineSegment(sketch, "E367", {"start": v(36.39, 23.51) * mm, "end": v(36.57, 23.63) * mm});
            skLineSegment(sketch, "E368", {"start": v(36.57, 23.63) * mm, "end": v(36.75, 23.74) * mm});
            skLineSegment(sketch, "E369", {"start": v(36.75, 23.74) * mm, "end": v(36.94, 23.86) * mm});
            skLineSegment(sketch, "E370", {"start": v(36.94, 23.86) * mm, "end": v(37.12, 23.98) * mm});
            skLineSegment(sketch, "E371", {"start": v(37.12, 23.98) * mm, "end": v(37.3, 24.1) * mm});
            skLineSegment(sketch, "E372", {"start": v(37.3, 24.1) * mm, "end": v(37.49, 24.2) * mm});
            skLineSegment(sketch, "E373", {"start": v(37.49, 24.2) * mm, "end": v(37.67, 24.32) * mm});
            skLineSegment(sketch, "E374", {"start": v(37.67, 24.32) * mm, "end": v(37.85, 24.44) * mm});
            skLineSegment(sketch, "E375", {"start": v(37.85, 24.44) * mm, "end": v(38.04, 24.55) * mm});
            skLineSegment(sketch, "E376", {"start": v(38.04, 24.55) * mm, "end": v(38.22, 24.67) * mm});
            skLineSegment(sketch, "E377", {"start": v(38.22, 24.67) * mm, "end": v(38.4, 24.78) * mm});
            skLineSegment(sketch, "E378", {"start": v(38.4, 24.78) * mm, "end": v(38.59, 24.9) * mm});
            skLineSegment(sketch, "E379", {"start": v(38.59, 24.9) * mm, "end": v(38.77, 25.01) * mm});
            skLineSegment(sketch, "E380", {"start": v(38.77, 25.01) * mm, "end": v(38.95, 25.13) * mm});
            skLineSegment(sketch, "E381", {"start": v(38.95, 25.13) * mm, "end": v(39.1, 25.26) * mm});
            skLineSegment(sketch, "E382", {"start": v(39.1, 25.26) * mm, "end": v(39.23, 25.43) * mm});
            skLineSegment(sketch, "E383", {"start": v(39.23, 25.43) * mm, "end": v(39.3, 25.62) * mm});
            skLineSegment(sketch, "E384", {"start": v(39.3, 25.62) * mm, "end": v(39.3, 25.82) * mm});
            skLineSegment(sketch, "E385", {"start": v(39.3, 25.82) * mm, "end": v(39.27, 26.02) * mm});
            skLineSegment(sketch, "E386", {"start": v(39.27, 26.02) * mm, "end": v(39.18, 26.2) * mm});
            skLineSegment(sketch, "E387", {"start": v(39.18, 26.2) * mm, "end": v(39.05, 26.36) * mm});
            skLineSegment(sketch, "E388", {"start": v(39.05, 26.36) * mm, "end": v(38.88, 26.48) * mm});
            skLineSegment(sketch, "E389", {"start": v(38.88, 26.48) * mm, "end": v(38.7, 26.54) * mm});
            skLineSegment(sketch, "E390", {"start": v(38.7, 26.54) * mm, "end": v(38.53, 26.56) * mm});
            skLineSegment(sketch, "E391", {"start": v(38.53, 26.56) * mm, "end": v(38.33, 26.53) * mm});
            skLineSegment(sketch, "E392", {"start": v(38.33, 26.53) * mm, "end": v(38.14, 26.45) * mm});
            skLineSegment(sketch, "E393", {"start": v(38.14, 26.45) * mm, "end": v(37.96, 26.33) * mm});
            skLineSegment(sketch, "E394", {"start": v(37.96, 26.33) * mm, "end": v(37.77, 26.2) * mm});
            skLineSegment(sketch, "E395", {"start": v(37.77, 26.2) * mm, "end": v(37.59, 26.08) * mm});
            skLineSegment(sketch, "E396", {"start": v(37.59, 26.08) * mm, "end": v(37.39, 25.94) * mm});
            skLineSegment(sketch, "E397", {"start": v(37.39, 25.94) * mm, "end": v(37.2, 25.82) * mm});
            skLineSegment(sketch, "E398", {"start": v(37.2, 25.82) * mm, "end": v(37.03, 25.7) * mm});
            skLineSegment(sketch, "E399", {"start": v(37.03, 25.7) * mm, "end": v(36.85, 25.58) * mm});
            skLineSegment(sketch, "E400", {"start": v(36.85, 25.58) * mm, "end": v(36.67, 25.46) * mm});
            skLineSegment(sketch, "E401", {"start": v(36.67, 25.46) * mm, "end": v(36.5, 25.34) * mm});
            skLineSegment(sketch, "E402", {"start": v(36.5, 25.34) * mm, "end": v(36.31, 25.21) * mm});
            skLineSegment(sketch, "E403", {"start": v(36.31, 25.21) * mm, "end": v(36.13, 25.1) * mm});
            skLineSegment(sketch, "E404", {"start": v(36.13, 25.1) * mm, "end": v(35.95, 24.97) * mm});
            skLineSegment(sketch, "E405", {"start": v(35.95, 24.97) * mm, "end": v(35.77, 24.85) * mm});
            skLineSegment(sketch, "E406", {"start": v(35.77, 24.85) * mm, "end": v(35.6, 24.73) * mm});
            skLineSegment(sketch, "E407", {"start": v(35.6, 24.73) * mm, "end": v(35.41, 24.6) * mm});
            skLineSegment(sketch, "E408", {"start": v(35.41, 24.6) * mm, "end": v(35.28, 24.79) * mm});
            skLineSegment(sketch, "E409", {"start": v(35.28, 24.79) * mm, "end": v(35.16, 24.97) * mm});
            skLineSegment(sketch, "E410", {"start": v(35.16, 24.97) * mm, "end": v(35.03, 25.15) * mm});
            skLineSegment(sketch, "E411", {"start": v(35.03, 25.15) * mm, "end": v(34.9, 25.33) * mm});
            skLineSegment(sketch, "E412", {"start": v(34.9, 25.33) * mm, "end": v(34.77, 25.51) * mm});
            skLineSegment(sketch, "E413", {"start": v(34.77, 25.51) * mm, "end": v(34.64, 25.7) * mm});
            skLineSegment(sketch, "E414", {"start": v(34.64, 25.7) * mm, "end": v(34.5, 25.88) * mm});
            skLineSegment(sketch, "E415", {"start": v(34.5, 25.88) * mm, "end": v(34.38, 26.06) * mm});
            skLineSegment(sketch, "E416", {"start": v(34.38, 26.06) * mm, "end": v(34.25, 26.24) * mm});
            skLineSegment(sketch, "E417", {"start": v(34.25, 26.24) * mm, "end": v(34.15, 26.38) * mm});
            skLineSegment(sketch, "E418", {"start": v(34.15, 26.38) * mm, "end": v(34.32, 26.51) * mm});
            skLineSegment(sketch, "E419", {"start": v(34.32, 26.51) * mm, "end": v(34.5, 26.64) * mm});
            skLineSegment(sketch, "E420", {"start": v(34.5, 26.64) * mm, "end": v(34.66, 26.77) * mm});
            skLineSegment(sketch, "E421", {"start": v(34.66, 26.77) * mm, "end": v(34.84, 26.9) * mm});
            skLineSegment(sketch, "E422", {"start": v(34.84, 26.9) * mm, "end": v(35.01, 27.04) * mm});
            skLineSegment(sketch, "E423", {"start": v(35.01, 27.04) * mm, "end": v(35.18, 27.17) * mm});
            skLineSegment(sketch, "E424", {"start": v(35.18, 27.17) * mm, "end": v(35.36, 27.3) * mm});
            skLineSegment(sketch, "E425", {"start": v(35.36, 27.3) * mm, "end": v(35.53, 27.43) * mm});
            skLineSegment(sketch, "E426", {"start": v(35.53, 27.43) * mm, "end": v(35.7, 27.56) * mm});
            skLineSegment(sketch, "E427", {"start": v(35.7, 27.56) * mm, "end": v(35.88, 27.69) * mm});
            skLineSegment(sketch, "E428", {"start": v(35.88, 27.69) * mm, "end": v(36.05, 27.82) * mm});
            skLineSegment(sketch, "E429", {"start": v(36.05, 27.82) * mm, "end": v(36.22, 27.95) * mm});
            skLineSegment(sketch, "E430", {"start": v(36.22, 27.95) * mm, "end": v(36.4, 28.08) * mm});
            skLineSegment(sketch, "E431", {"start": v(36.4, 28.08) * mm, "end": v(36.57, 28.2) * mm});
            skLineSegment(sketch, "E432", {"start": v(36.57, 28.2) * mm, "end": v(36.74, 28.34) * mm});
            skLineSegment(sketch, "E433", {"start": v(36.74, 28.34) * mm, "end": v(36.89, 28.48) * mm});
            skLineSegment(sketch, "E434", {"start": v(36.89, 28.48) * mm, "end": v(36.99, 28.66) * mm});
            skLineSegment(sketch, "E435", {"start": v(36.99, 28.66) * mm, "end": v(37.04, 28.86) * mm});
            skLineSegment(sketch, "E436", {"start": v(37.04, 28.86) * mm, "end": v(37.04, 29.06) * mm});
            skLineSegment(sketch, "E437", {"start": v(37.04, 29.06) * mm, "end": v(36.99, 29.25) * mm});
            skLineSegment(sketch, "E438", {"start": v(36.99, 29.25) * mm, "end": v(36.88, 29.43) * mm});
            skLineSegment(sketch, "E439", {"start": v(36.88, 29.43) * mm, "end": v(36.74, 29.57) * mm});
            skLineSegment(sketch, "E440", {"start": v(36.74, 29.57) * mm, "end": v(36.56, 29.67) * mm});
            skLineSegment(sketch, "E441", {"start": v(36.56, 29.67) * mm, "end": v(36.36, 29.72) * mm});
            skLineSegment(sketch, "E442", {"start": v(36.36, 29.72) * mm, "end": v(36.28, 29.73) * mm});
            skLineSegment(sketch, "E443", {"start": v(36.28, 29.73) * mm, "end": v(36.08, 29.7) * mm});
            skLineSegment(sketch, "E444", {"start": v(36.08, 29.7) * mm, "end": v(35.9, 29.63) * mm});
            skLineSegment(sketch, "E445", {"start": v(35.9, 29.63) * mm, "end": v(35.7, 29.5) * mm});
            skLineSegment(sketch, "E446", {"start": v(35.7, 29.5) * mm, "end": v(35.54, 29.36) * mm});
            skLineSegment(sketch, "E447", {"start": v(35.54, 29.36) * mm, "end": v(35.37, 29.22) * mm});
            skLineSegment(sketch, "E448", {"start": v(35.37, 29.22) * mm, "end": v(35.2, 29.09) * mm});
            skLineSegment(sketch, "E449", {"start": v(35.2, 29.09) * mm, "end": v(35.03, 28.95) * mm});
            skLineSegment(sketch, "E450", {"start": v(35.03, 28.95) * mm, "end": v(34.86, 28.82) * mm});
            skLineSegment(sketch, "E451", {"start": v(34.86, 28.82) * mm, "end": v(34.7, 28.68) * mm});
            skLineSegment(sketch, "E452", {"start": v(34.7, 28.68) * mm, "end": v(34.52, 28.54) * mm});
            skLineSegment(sketch, "E453", {"start": v(34.52, 28.54) * mm, "end": v(34.36, 28.4) * mm});
            skLineSegment(sketch, "E454", {"start": v(34.36, 28.4) * mm, "end": v(34.19, 28.27) * mm});
            skLineSegment(sketch, "E455", {"start": v(34.19, 28.27) * mm, "end": v(34.02, 28.14) * mm});
            skLineSegment(sketch, "E456", {"start": v(34.02, 28.14) * mm, "end": v(33.85, 28) * mm});
            skLineSegment(sketch, "E457", {"start": v(33.85, 28) * mm, "end": v(33.68, 27.86) * mm});
            skLineSegment(sketch, "E458", {"start": v(33.68, 27.86) * mm, "end": v(33.51, 27.73) * mm});
            skLineSegment(sketch, "E459", {"start": v(33.51, 27.73) * mm, "end": v(33.34, 27.6) * mm});
            skLineSegment(sketch, "E460", {"start": v(33.34, 27.6) * mm, "end": v(33.26, 27.52) * mm});
            skLineSegment(sketch, "E461", {"start": v(33.26, 27.52) * mm, "end": v(33.11, 27.7) * mm});
            skLineSegment(sketch, "E462", {"start": v(33.11, 27.7) * mm, "end": v(32.97, 27.86) * mm});
            skLineSegment(sketch, "E463", {"start": v(32.97, 27.86) * mm, "end": v(32.83, 28.03) * mm});
            skLineSegment(sketch, "E464", {"start": v(32.83, 28.03) * mm, "end": v(32.68, 28.2) * mm});
            skLineSegment(sketch, "E465", {"start": v(32.68, 28.2) * mm, "end": v(32.54, 28.37) * mm});
            skLineSegment(sketch, "E466", {"start": v(32.54, 28.37) * mm, "end": v(32.4, 28.54) * mm});
            skLineSegment(sketch, "E467", {"start": v(32.4, 28.54) * mm, "end": v(32.25, 28.71) * mm});
            skLineSegment(sketch, "E468", {"start": v(32.25, 28.71) * mm, "end": v(32.1, 28.88) * mm});
            skLineSegment(sketch, "E469", {"start": v(32.1, 28.88) * mm, "end": v(31.96, 29.05) * mm});
            skLineSegment(sketch, "E470", {"start": v(31.96, 29.05) * mm, "end": v(31.85, 29.2) * mm});
            skLineSegment(sketch, "E471", {"start": v(31.85, 29.2) * mm, "end": v(32, 29.33) * mm});
            skLineSegment(sketch, "E472", {"start": v(32, 29.33) * mm, "end": v(32.17, 29.48) * mm});
            skLineSegment(sketch, "E473", {"start": v(32.17, 29.48) * mm, "end": v(32.33, 29.62) * mm});
            skLineSegment(sketch, "E474", {"start": v(32.33, 29.62) * mm, "end": v(32.5, 29.77) * mm});
            skLineSegment(sketch, "E475", {"start": v(32.5, 29.77) * mm, "end": v(32.66, 29.91) * mm});
            skLineSegment(sketch, "E476", {"start": v(32.66, 29.91) * mm, "end": v(32.82, 30.06) * mm});
            skLineSegment(sketch, "E477", {"start": v(32.82, 30.06) * mm, "end": v(32.98, 30.2) * mm});
            skLineSegment(sketch, "E478", {"start": v(32.98, 30.2) * mm, "end": v(33.14, 30.34) * mm});
            skLineSegment(sketch, "E479", {"start": v(33.14, 30.34) * mm, "end": v(33.3, 30.49) * mm});
            skLineSegment(sketch, "E480", {"start": v(33.3, 30.49) * mm, "end": v(33.46, 30.63) * mm});
            skLineSegment(sketch, "E481", {"start": v(33.46, 30.63) * mm, "end": v(33.63, 30.78) * mm});
            skLineSegment(sketch, "E482", {"start": v(33.63, 30.78) * mm, "end": v(33.79, 30.92) * mm});
            skLineSegment(sketch, "E483", {"start": v(33.79, 30.92) * mm, "end": v(33.95, 31.06) * mm});
            skLineSegment(sketch, "E484", {"start": v(33.95, 31.06) * mm, "end": v(34.11, 31.2) * mm});
            skLineSegment(sketch, "E485", {"start": v(34.11, 31.2) * mm, "end": v(34.27, 31.35) * mm});
            skLineSegment(sketch, "E486", {"start": v(34.27, 31.35) * mm, "end": v(34.4, 31.5) * mm});
            skLineSegment(sketch, "E487", {"start": v(34.4, 31.5) * mm, "end": v(34.5, 31.7) * mm});
            skLineSegment(sketch, "E488", {"start": v(34.5, 31.7) * mm, "end": v(34.53, 31.9) * mm});
            skLineSegment(sketch, "E489", {"start": v(34.53, 31.9) * mm, "end": v(34.51, 32.1) * mm});
            skLineSegment(sketch, "E490", {"start": v(34.51, 32.1) * mm, "end": v(34.44, 32.29) * mm});
            skLineSegment(sketch, "E491", {"start": v(34.44, 32.29) * mm, "end": v(34.32, 32.45) * mm});
            skLineSegment(sketch, "E492", {"start": v(34.32, 32.45) * mm, "end": v(34.17, 32.58) * mm});
            skLineSegment(sketch, "E493", {"start": v(34.17, 32.58) * mm, "end": v(33.98, 32.67) * mm});
            skLineSegment(sketch, "E494", {"start": v(33.98, 32.67) * mm, "end": v(33.78, 32.7) * mm});
            skLineSegment(sketch, "E495", {"start": v(33.78, 32.7) * mm, "end": v(33.74, 32.7) * mm});
            skLineSegment(sketch, "E496", {"start": v(33.74, 32.7) * mm, "end": v(33.54, 32.67) * mm});
            skLineSegment(sketch, "E497", {"start": v(33.54, 32.67) * mm, "end": v(33.35, 32.6) * mm});
            skLineSegment(sketch, "E498", {"start": v(33.35, 32.6) * mm, "end": v(33.18, 32.45) * mm});
            skLineSegment(sketch, "E499", {"start": v(33.18, 32.45) * mm, "end": v(33.02, 32.3) * mm});
            skLineSegment(sketch, "E500", {"start": v(33.02, 32.3) * mm, "end": v(32.86, 32.15) * mm});
            skLineSegment(sketch, "E501", {"start": v(32.86, 32.15) * mm, "end": v(32.7, 32) * mm});
            skLineSegment(sketch, "E502", {"start": v(32.7, 32) * mm, "end": v(32.53, 31.84) * mm});
            skLineSegment(sketch, "E503", {"start": v(32.53, 31.84) * mm, "end": v(32.36, 31.67) * mm});
            skLineSegment(sketch, "E504", {"start": v(32.36, 31.67) * mm, "end": v(32.2, 31.52) * mm});
            skLineSegment(sketch, "E505", {"start": v(32.2, 31.52) * mm, "end": v(32.05, 31.37) * mm});
            skLineSegment(sketch, "E506", {"start": v(32.05, 31.37) * mm, "end": v(31.89, 31.22) * mm});
            skLineSegment(sketch, "E507", {"start": v(31.89, 31.22) * mm, "end": v(31.73, 31.07) * mm});
            skLineSegment(sketch, "E508", {"start": v(31.73, 31.07) * mm, "end": v(31.57, 30.93) * mm});
            skLineSegment(sketch, "E509", {"start": v(31.57, 30.93) * mm, "end": v(31.42, 30.78) * mm});
            skLineSegment(sketch, "E510", {"start": v(31.42, 30.78) * mm, "end": v(31.26, 30.63) * mm});
            skLineSegment(sketch, "E511", {"start": v(31.26, 30.63) * mm, "end": v(31.1, 30.48) * mm});
            skLineSegment(sketch, "E512", {"start": v(31.1, 30.48) * mm, "end": v(30.95, 30.33) * mm});
            skLineSegment(sketch, "E513", {"start": v(30.95, 30.33) * mm, "end": v(30.87, 30.25) * mm});
            skLineSegment(sketch, "E514", {"start": v(30.87, 30.25) * mm, "end": v(30.71, 30.41) * mm});
            skLineSegment(sketch, "E515", {"start": v(30.71, 30.41) * mm, "end": v(30.55, 30.57) * mm});
            skLineSegment(sketch, "E516", {"start": v(30.55, 30.57) * mm, "end": v(30.4, 30.73) * mm});
            skLineSegment(sketch, "E517", {"start": v(30.4, 30.73) * mm, "end": v(30.24, 30.88) * mm});
            skLineSegment(sketch, "E518", {"start": v(30.24, 30.88) * mm, "end": v(30.08, 31.04) * mm});
            skLineSegment(sketch, "E519", {"start": v(30.08, 31.04) * mm, "end": v(29.92, 31.2) * mm});
            skLineSegment(sketch, "E520", {"start": v(29.92, 31.2) * mm, "end": v(29.77, 31.36) * mm});
            skLineSegment(sketch, "E521", {"start": v(29.77, 31.36) * mm, "end": v(29.6, 31.51) * mm});
            skLineSegment(sketch, "E522", {"start": v(29.6, 31.51) * mm, "end": v(29.45, 31.67) * mm});
            skLineSegment(sketch, "E523", {"start": v(29.45, 31.67) * mm, "end": v(29.32, 31.8) * mm});
            skLineSegment(sketch, "E524", {"start": v(29.32, 31.8) * mm, "end": v(29.47, 31.95) * mm});
            skLineSegment(sketch, "E525", {"start": v(29.47, 31.95) * mm, "end": v(29.62, 32.11) * mm});
            skLineSegment(sketch, "E526", {"start": v(29.62, 32.11) * mm, "end": v(29.77, 32.27) * mm});
            skLineSegment(sketch, "E527", {"start": v(29.77, 32.27) * mm, "end": v(29.92, 32.43) * mm});
            skLineSegment(sketch, "E528", {"start": v(29.92, 32.43) * mm, "end": v(30.07, 32.58) * mm});
            skLineSegment(sketch, "E529", {"start": v(30.07, 32.58) * mm, "end": v(30.22, 32.74) * mm});
            skLineSegment(sketch, "E530", {"start": v(30.22, 32.74) * mm, "end": v(30.37, 32.9) * mm});
            skLineSegment(sketch, "E531", {"start": v(30.37, 32.9) * mm, "end": v(30.52, 33.05) * mm});
            skLineSegment(sketch, "E532", {"start": v(30.52, 33.05) * mm, "end": v(30.67, 33.21) * mm});
            skLineSegment(sketch, "E533", {"start": v(30.67, 33.21) * mm, "end": v(30.82, 33.37) * mm});
            skLineSegment(sketch, "E534", {"start": v(30.82, 33.37) * mm, "end": v(30.97, 33.52) * mm});
            skLineSegment(sketch, "E535", {"start": v(30.97, 33.52) * mm, "end": v(31.12, 33.68) * mm});
            skLineSegment(sketch, "E536", {"start": v(31.12, 33.68) * mm, "end": v(31.27, 33.84) * mm});
            skLineSegment(sketch, "E537", {"start": v(31.27, 33.84) * mm, "end": v(31.42, 34) * mm});
            skLineSegment(sketch, "E538", {"start": v(31.42, 34) * mm, "end": v(31.56, 34.15) * mm});
            skLineSegment(sketch, "E539", {"start": v(31.56, 34.15) * mm, "end": v(31.68, 34.32) * mm});
            skLineSegment(sketch, "E540", {"start": v(31.68, 34.32) * mm, "end": v(31.75, 34.5) * mm});
            skLineSegment(sketch, "E541", {"start": v(31.75, 34.5) * mm, "end": v(31.77, 34.71) * mm});
            skLineSegment(sketch, "E542", {"start": v(31.77, 34.71) * mm, "end": v(31.74, 34.91) * mm});
            skLineSegment(sketch, "E543", {"start": v(31.74, 34.91) * mm, "end": v(31.65, 35.1) * mm});
            skLineSegment(sketch, "E544", {"start": v(31.65, 35.1) * mm, "end": v(31.52, 35.25) * mm});
            skLineSegment(sketch, "E545", {"start": v(31.52, 35.25) * mm, "end": v(31.36, 35.37) * mm});
            skLineSegment(sketch, "E546", {"start": v(31.36, 35.37) * mm, "end": v(31.17, 35.44) * mm});
            skLineSegment(sketch, "E547", {"start": v(31.17, 35.44) * mm, "end": v(31, 35.46) * mm});
            skLineSegment(sketch, "E548", {"start": v(31, 35.46) * mm, "end": v(30.8, 35.43) * mm});
            skLineSegment(sketch, "E549", {"start": v(30.8, 35.43) * mm, "end": v(30.61, 35.36) * mm});
            skLineSegment(sketch, "E550", {"start": v(30.61, 35.36) * mm, "end": v(30.45, 35.23) * mm});
            skLineSegment(sketch, "E551", {"start": v(30.45, 35.23) * mm, "end": v(30.3, 35.07) * mm});
            skLineSegment(sketch, "E552", {"start": v(30.3, 35.07) * mm, "end": v(30.15, 34.9) * mm});
            skLineSegment(sketch, "E553", {"start": v(30.15, 34.9) * mm, "end": v(30, 34.73) * mm});
            skLineSegment(sketch, "E554", {"start": v(30, 34.73) * mm, "end": v(29.85, 34.56) * mm});
            skLineSegment(sketch, "E555", {"start": v(29.85, 34.56) * mm, "end": v(29.7, 34.4) * mm});
            skLineSegment(sketch, "E556", {"start": v(29.7, 34.4) * mm, "end": v(29.56, 34.23) * mm});
            skLineSegment(sketch, "E557", {"start": v(29.56, 34.23) * mm, "end": v(29.41, 34.07) * mm});
            skLineSegment(sketch, "E558", {"start": v(29.41, 34.07) * mm, "end": v(29.27, 33.9) * mm});
            skLineSegment(sketch, "E559", {"start": v(29.27, 33.9) * mm, "end": v(29.13, 33.75) * mm});
            skLineSegment(sketch, "E560", {"start": v(29.13, 33.75) * mm, "end": v(28.98, 33.58) * mm});
            skLineSegment(sketch, "E561", {"start": v(28.98, 33.58) * mm, "end": v(28.84, 33.42) * mm});
            skLineSegment(sketch, "E562", {"start": v(28.84, 33.42) * mm, "end": v(28.7, 33.26) * mm});
            skLineSegment(sketch, "E563", {"start": v(28.7, 33.26) * mm, "end": v(28.55, 33.1) * mm});
            skLineSegment(sketch, "E564", {"start": v(28.55, 33.1) * mm, "end": v(28.4, 32.94) * mm});
            skLineSegment(sketch, "E565", {"start": v(28.4, 32.94) * mm, "end": v(28.26, 32.78) * mm});
            skLineSegment(sketch, "E566", {"start": v(28.26, 32.78) * mm, "end": v(28.1, 32.92) * mm});
            skLineSegment(sketch, "E567", {"start": v(28.1, 32.92) * mm, "end": v(27.92, 33.06) * mm});
            skLineSegment(sketch, "E568", {"start": v(27.92, 33.06) * mm, "end": v(27.75, 33.2) * mm});
            skLineSegment(sketch, "E569", {"start": v(27.75, 33.2) * mm, "end": v(27.58, 33.35) * mm});
            skLineSegment(sketch, "E570", {"start": v(27.58, 33.35) * mm, "end": v(27.41, 33.5) * mm});
            skLineSegment(sketch, "E571", {"start": v(27.41, 33.5) * mm, "end": v(27.24, 33.64) * mm});
            skLineSegment(sketch, "E572", {"start": v(27.24, 33.64) * mm, "end": v(27.07, 33.78) * mm});
            skLineSegment(sketch, "E573", {"start": v(27.07, 33.78) * mm, "end": v(26.9, 33.93) * mm});
            skLineSegment(sketch, "E574", {"start": v(26.9, 33.93) * mm, "end": v(26.73, 34.07) * mm});
            skLineSegment(sketch, "E575", {"start": v(26.73, 34.07) * mm, "end": v(26.6, 34.19) * mm});
            skLineSegment(sketch, "E576", {"start": v(26.6, 34.19) * mm, "end": v(26.73, 34.36) * mm});
            skLineSegment(sketch, "E577", {"start": v(26.73, 34.36) * mm, "end": v(26.87, 34.52) * mm});
            skLineSegment(sketch, "E578", {"start": v(26.87, 34.52) * mm, "end": v(27, 34.7) * mm});
            skLineSegment(sketch, "E579", {"start": v(27, 34.7) * mm, "end": v(27.14, 34.86) * mm});
            skLineSegment(sketch, "E580", {"start": v(27.14, 34.86) * mm, "end": v(27.27, 35.03) * mm});
            skLineSegment(sketch, "E581", {"start": v(27.27, 35.03) * mm, "end": v(27.41, 35.2) * mm});
            skLineSegment(sketch, "E582", {"start": v(27.41, 35.2) * mm, "end": v(27.55, 35.37) * mm});
            skLineSegment(sketch, "E583", {"start": v(27.55, 35.37) * mm, "end": v(27.68, 35.54) * mm});
            skLineSegment(sketch, "E584", {"start": v(27.68, 35.54) * mm, "end": v(27.82, 35.7) * mm});
            skLineSegment(sketch, "E585", {"start": v(27.82, 35.7) * mm, "end": v(27.95, 35.87) * mm});
            skLineSegment(sketch, "E586", {"start": v(27.95, 35.87) * mm, "end": v(28.09, 36.04) * mm});
            skLineSegment(sketch, "E587", {"start": v(28.09, 36.04) * mm, "end": v(28.23, 36.21) * mm});
            skLineSegment(sketch, "E588", {"start": v(28.23, 36.21) * mm, "end": v(28.36, 36.38) * mm});
            skLineSegment(sketch, "E589", {"start": v(28.36, 36.38) * mm, "end": v(28.5, 36.55) * mm});
            skLineSegment(sketch, "E590", {"start": v(28.5, 36.55) * mm, "end": v(28.63, 36.72) * mm});
            skLineSegment(sketch, "E591", {"start": v(28.63, 36.72) * mm, "end": v(28.74, 36.9) * mm});
            skLineSegment(sketch, "E592", {"start": v(28.74, 36.9) * mm, "end": v(28.8, 37.09) * mm});
            skLineSegment(sketch, "E593", {"start": v(28.8, 37.09) * mm, "end": v(28.8, 37.3) * mm});
            skLineSegment(sketch, "E594", {"start": v(28.8, 37.3) * mm, "end": v(28.74, 37.5) * mm});
            skLineSegment(sketch, "E595", {"start": v(28.74, 37.5) * mm, "end": v(28.64, 37.67) * mm});
            skLineSegment(sketch, "E596", {"start": v(28.64, 37.67) * mm, "end": v(28.5, 37.81) * mm});
            skLineSegment(sketch, "E597", {"start": v(28.5, 37.81) * mm, "end": v(28.33, 37.92) * mm});
            skLineSegment(sketch, "E598", {"start": v(28.33, 37.92) * mm, "end": v(28.13, 37.97) * mm});
            skLineSegment(sketch, "E599", {"start": v(28.13, 37.97) * mm, "end": v(28, 37.98) * mm});
            skLineSegment(sketch, "E600", {"start": v(28, 37.98) * mm, "end": v(27.8, 37.94) * mm});
            skLineSegment(sketch, "E601", {"start": v(27.8, 37.94) * mm, "end": v(27.62, 37.86) * mm});
            skLineSegment(sketch, "E602", {"start": v(27.62, 37.86) * mm, "end": v(27.46, 37.73) * mm});
            skLineSegment(sketch, "E603", {"start": v(27.46, 37.73) * mm, "end": v(27.33, 37.56) * mm});
            skLineSegment(sketch, "E604", {"start": v(27.33, 37.56) * mm, "end": v(27.2, 37.38) * mm});
            skLineSegment(sketch, "E605", {"start": v(27.2, 37.38) * mm, "end": v(27.06, 37.2) * mm});
            skLineSegment(sketch, "E606", {"start": v(27.06, 37.2) * mm, "end": v(26.92, 37.03) * mm});
            skLineSegment(sketch, "E607", {"start": v(26.92, 37.03) * mm, "end": v(26.79, 36.85) * mm});
            skLineSegment(sketch, "E608", {"start": v(26.79, 36.85) * mm, "end": v(26.66, 36.67) * mm});
            skLineSegment(sketch, "E609", {"start": v(26.66, 36.67) * mm, "end": v(26.52, 36.5) * mm});
            skLineSegment(sketch, "E610", {"start": v(26.52, 36.5) * mm, "end": v(26.39, 36.31) * mm});
            skLineSegment(sketch, "E611", {"start": v(26.39, 36.31) * mm, "end": v(26.25, 36.14) * mm});
            skLineSegment(sketch, "E612", {"start": v(26.25, 36.14) * mm, "end": v(26.1, 35.94) * mm});
            skLineSegment(sketch, "E613", {"start": v(26.1, 35.94) * mm, "end": v(25.98, 35.77) * mm});
            skLineSegment(sketch, "E614", {"start": v(25.98, 35.77) * mm, "end": v(25.85, 35.6) * mm});
            skLineSegment(sketch, "E615", {"start": v(25.85, 35.6) * mm, "end": v(25.72, 35.42) * mm});
            skLineSegment(sketch, "E616", {"start": v(25.72, 35.42) * mm, "end": v(25.59, 35.25) * mm});
            skLineSegment(sketch, "E617", {"start": v(25.59, 35.25) * mm, "end": v(25.46, 35.07) * mm});
            skLineSegment(sketch, "E618", {"start": v(25.46, 35.07) * mm, "end": v(25.27, 35.2) * mm});
            skLineSegment(sketch, "E619", {"start": v(25.27, 35.2) * mm, "end": v(25.1, 35.33) * mm});
            skLineSegment(sketch, "E620", {"start": v(25.1, 35.33) * mm, "end": v(24.91, 35.46) * mm});
            skLineSegment(sketch, "E621", {"start": v(24.91, 35.46) * mm, "end": v(24.73, 35.6) * mm});
            skLineSegment(sketch, "E622", {"start": v(24.73, 35.6) * mm, "end": v(24.55, 35.72) * mm});
            skLineSegment(sketch, "E623", {"start": v(24.55, 35.72) * mm, "end": v(24.37, 35.85) * mm});
            skLineSegment(sketch, "E624", {"start": v(24.37, 35.85) * mm, "end": v(24.19, 35.98) * mm});
            skLineSegment(sketch, "E625", {"start": v(24.19, 35.98) * mm, "end": v(24, 36.1) * mm});
            skLineSegment(sketch, "E626", {"start": v(24, 36.1) * mm, "end": v(23.82, 36.24) * mm});
            skLineSegment(sketch, "E627", {"start": v(23.82, 36.24) * mm, "end": v(23.68, 36.34) * mm});
            skLineSegment(sketch, "E628", {"start": v(23.68, 36.34) * mm, "end": v(23.8, 36.52) * mm});
            skLineSegment(sketch, "E629", {"start": v(23.8, 36.52) * mm, "end": v(23.92, 36.7) * mm});
            skLineSegment(sketch, "E630", {"start": v(23.92, 36.7) * mm, "end": v(24.04, 36.88) * mm});
            skLineSegment(sketch, "E631", {"start": v(24.04, 36.88) * mm, "end": v(24.16, 37.06) * mm});
            skLineSegment(sketch, "E632", {"start": v(24.16, 37.06) * mm, "end": v(24.29, 37.24) * mm});
            skLineSegment(sketch, "E633", {"start": v(24.29, 37.24) * mm, "end": v(24.4, 37.42) * mm});
            skLineSegment(sketch, "E634", {"start": v(24.4, 37.42) * mm, "end": v(24.53, 37.6) * mm});
            skLineSegment(sketch, "E635", {"start": v(24.53, 37.6) * mm, "end": v(24.65, 37.78) * mm});
            skLineSegment(sketch, "E636", {"start": v(24.65, 37.78) * mm, "end": v(24.77, 37.96) * mm});
            skLineSegment(sketch, "E637", {"start": v(24.77, 37.96) * mm, "end": v(24.9, 38.14) * mm});
            skLineSegment(sketch, "E638", {"start": v(24.9, 38.14) * mm, "end": v(25.01, 38.32) * mm});
            skLineSegment(sketch, "E639", {"start": v(25.01, 38.32) * mm, "end": v(25.14, 38.5) * mm});
            skLineSegment(sketch, "E640", {"start": v(25.14, 38.5) * mm, "end": v(25.26, 38.68) * mm});
            skLineSegment(sketch, "E641", {"start": v(25.26, 38.68) * mm, "end": v(25.38, 38.86) * mm});
            skLineSegment(sketch, "E642", {"start": v(25.38, 38.86) * mm, "end": v(25.5, 39.03) * mm});
            skLineSegment(sketch, "E643", {"start": v(25.5, 39.03) * mm, "end": v(25.59, 39.22) * mm});
            skLineSegment(sketch, "E644", {"start": v(25.59, 39.22) * mm, "end": v(25.63, 39.42) * mm});
            skLineSegment(sketch, "E645", {"start": v(25.63, 39.42) * mm, "end": v(25.61, 39.62) * mm});
            skLineSegment(sketch, "E646", {"start": v(25.61, 39.62) * mm, "end": v(25.55, 39.81) * mm});
            skLineSegment(sketch, "E647", {"start": v(25.55, 39.81) * mm, "end": v(25.43, 39.98) * mm});
            skLineSegment(sketch, "E648", {"start": v(25.43, 39.98) * mm, "end": v(25.28, 40.11) * mm});
            skLineSegment(sketch, "E649", {"start": v(25.28, 40.11) * mm, "end": v(25.1, 40.2) * mm});
            skLineSegment(sketch, "E650", {"start": v(25.1, 40.2) * mm, "end": v(24.9, 40.24) * mm});
            skLineSegment(sketch, "E651", {"start": v(24.9, 40.24) * mm, "end": v(24.85, 40.24) * mm});
            skLineSegment(sketch, "E652", {"start": v(24.85, 40.24) * mm, "end": v(24.65, 40.21) * mm});
            skLineSegment(sketch, "E653", {"start": v(24.65, 40.21) * mm, "end": v(24.46, 40.13) * mm});
            skLineSegment(sketch, "E654", {"start": v(24.46, 40.13) * mm, "end": v(24.3, 40.01) * mm});
            skLineSegment(sketch, "E655", {"start": v(24.3, 40.01) * mm, "end": v(24.17, 39.83) * mm});
            skLineSegment(sketch, "E656", {"start": v(24.17, 39.83) * mm, "end": v(24.05, 39.64) * mm});
            skLineSegment(sketch, "E657", {"start": v(24.05, 39.64) * mm, "end": v(23.93, 39.46) * mm});
            skLineSegment(sketch, "E658", {"start": v(23.93, 39.46) * mm, "end": v(23.81, 39.27) * mm});
            skLineSegment(sketch, "E659", {"start": v(23.81, 39.27) * mm, "end": v(23.7, 39.08) * mm});
            skLineSegment(sketch, "E660", {"start": v(23.7, 39.08) * mm, "end": v(23.57, 38.87) * mm});
            skLineSegment(sketch, "E661", {"start": v(23.57, 38.87) * mm, "end": v(23.45, 38.7) * mm});
            skLineSegment(sketch, "E662", {"start": v(23.45, 38.7) * mm, "end": v(23.34, 38.5) * mm});
            skLineSegment(sketch, "E663", {"start": v(23.34, 38.5) * mm, "end": v(23.22, 38.32) * mm});
            skLineSegment(sketch, "E664", {"start": v(23.22, 38.32) * mm, "end": v(23.1, 38.14) * mm});
            skLineSegment(sketch, "E665", {"start": v(23.1, 38.14) * mm, "end": v(22.99, 37.96) * mm});
            skLineSegment(sketch, "E666", {"start": v(22.99, 37.96) * mm, "end": v(22.87, 37.77) * mm});
            skLineSegment(sketch, "E667", {"start": v(22.87, 37.77) * mm, "end": v(22.76, 37.6) * mm});
            skLineSegment(sketch, "E668", {"start": v(22.76, 37.6) * mm, "end": v(22.64, 37.4) * mm});
            skLineSegment(sketch, "E669", {"start": v(22.64, 37.4) * mm, "end": v(22.53, 37.22) * mm});
            skLineSegment(sketch, "E670", {"start": v(22.53, 37.22) * mm, "end": v(22.47, 37.13) * mm});
            skLineSegment(sketch, "E671", {"start": v(22.47, 37.13) * mm, "end": v(22.28, 37.25) * mm});
            skLineSegment(sketch, "E672", {"start": v(22.28, 37.25) * mm, "end": v(22.09, 37.36) * mm});
            skLineSegment(sketch, "E673", {"start": v(22.09, 37.36) * mm, "end": v(21.9, 37.48) * mm});
            skLineSegment(sketch, "E674", {"start": v(21.9, 37.48) * mm, "end": v(21.7, 37.59) * mm});
            skLineSegment(sketch, "E675", {"start": v(21.7, 37.59) * mm, "end": v(21.51, 37.7) * mm});
            skLineSegment(sketch, "E676", {"start": v(21.51, 37.7) * mm, "end": v(21.32, 37.82) * mm});
            skLineSegment(sketch, "E677", {"start": v(21.32, 37.82) * mm, "end": v(21.13, 37.93) * mm});
            skLineSegment(sketch, "E678", {"start": v(21.13, 37.93) * mm, "end": v(20.94, 38.05) * mm});
            skLineSegment(sketch, "E679", {"start": v(20.94, 38.05) * mm, "end": v(20.75, 38.16) * mm});
            skLineSegment(sketch, "E680", {"start": v(20.75, 38.16) * mm, "end": v(20.6, 38.25) * mm});
            skLineSegment(sketch, "E681", {"start": v(20.6, 38.25) * mm, "end": v(20.7, 38.44) * mm});
            skLineSegment(sketch, "E682", {"start": v(20.7, 38.44) * mm, "end": v(20.8, 38.63) * mm});
            skLineSegment(sketch, "E683", {"start": v(20.8, 38.63) * mm, "end": v(20.91, 38.82) * mm});
            skLineSegment(sketch, "E684", {"start": v(20.91, 38.82) * mm, "end": v(21.02, 39) * mm});
            skLineSegment(sketch, "E685", {"start": v(21.02, 39) * mm, "end": v(21.12, 39.2) * mm});
            skLineSegment(sketch, "E686", {"start": v(21.12, 39.2) * mm, "end": v(21.23, 39.38) * mm});
            skLineSegment(sketch, "E687", {"start": v(21.23, 39.38) * mm, "end": v(21.34, 39.57) * mm});
            skLineSegment(sketch, "E688", {"start": v(21.34, 39.57) * mm, "end": v(21.44, 39.76) * mm});
            skLineSegment(sketch, "E689", {"start": v(21.44, 39.76) * mm, "end": v(21.55, 39.95) * mm});
            skLineSegment(sketch, "E690", {"start": v(21.55, 39.95) * mm, "end": v(21.66, 40.14) * mm});
            skLineSegment(sketch, "E691", {"start": v(21.66, 40.14) * mm, "end": v(21.76, 40.33) * mm});
            skLineSegment(sketch, "E692", {"start": v(21.76, 40.33) * mm, "end": v(21.87, 40.52) * mm});
            skLineSegment(sketch, "E693", {"start": v(21.87, 40.52) * mm, "end": v(21.97, 40.7) * mm});
            skLineSegment(sketch, "E694", {"start": v(21.97, 40.7) * mm, "end": v(22.08, 40.9) * mm});
            skLineSegment(sketch, "E695", {"start": v(22.08, 40.9) * mm, "end": v(22.19, 41.08) * mm});
            skLineSegment(sketch, "E696", {"start": v(22.19, 41.08) * mm, "end": v(22.26, 41.27) * mm});
            skLineSegment(sketch, "E697", {"start": v(22.26, 41.27) * mm, "end": v(22.28, 41.48) * mm});
            skLineSegment(sketch, "E698", {"start": v(22.28, 41.48) * mm, "end": v(22.25, 41.68) * mm});
            skLineSegment(sketch, "E699", {"start": v(22.25, 41.68) * mm, "end": v(22.17, 41.86) * mm});
            skLineSegment(sketch, "E700", {"start": v(22.17, 41.86) * mm, "end": v(22.04, 42.02) * mm});
            skLineSegment(sketch, "E701", {"start": v(22.04, 42.02) * mm, "end": v(21.88, 42.14) * mm});
            skLineSegment(sketch, "E702", {"start": v(21.88, 42.14) * mm, "end": v(21.69, 42.21) * mm});
            skLineSegment(sketch, "E703", {"start": v(21.69, 42.21) * mm, "end": v(21.52, 42.23) * mm});
            skLineSegment(sketch, "E704", {"start": v(21.52, 42.23) * mm, "end": v(21.32, 42.21) * mm});
            skLineSegment(sketch, "E705", {"start": v(21.32, 42.21) * mm, "end": v(21.13, 42.14) * mm});
            skLineSegment(sketch, "E706", {"start": v(21.13, 42.14) * mm, "end": v(20.97, 42.02) * mm});
            skLineSegment(sketch, "E707", {"start": v(20.97, 42.02) * mm, "end": v(20.84, 41.86) * mm});
            skLineSegment(sketch, "E708", {"start": v(20.84, 41.86) * mm, "end": v(20.74, 41.66) * mm});
            skLineSegment(sketch, "E709", {"start": v(20.74, 41.66) * mm, "end": v(20.64, 41.46) * mm});
            skLineSegment(sketch, "E710", {"start": v(20.64, 41.46) * mm, "end": v(20.53, 41.27) * mm});
            skLineSegment(sketch, "E711", {"start": v(20.53, 41.27) * mm, "end": v(20.42, 41.05) * mm});
            skLineSegment(sketch, "E712", {"start": v(20.42, 41.05) * mm, "end": v(20.32, 40.86) * mm});
            skLineSegment(sketch, "E713", {"start": v(20.32, 40.86) * mm, "end": v(20.22, 40.67) * mm});
            skLineSegment(sketch, "E714", {"start": v(20.22, 40.67) * mm, "end": v(20.12, 40.48) * mm});
            skLineSegment(sketch, "E715", {"start": v(20.12, 40.48) * mm, "end": v(20.02, 40.28) * mm});
            skLineSegment(sketch, "E716", {"start": v(20.02, 40.28) * mm, "end": v(19.92, 40.1) * mm});
            skLineSegment(sketch, "E717", {"start": v(19.92, 40.1) * mm, "end": v(19.82, 39.9) * mm});
            skLineSegment(sketch, "E718", {"start": v(19.82, 39.9) * mm, "end": v(19.72, 39.7) * mm});
            skLineSegment(sketch, "E719", {"start": v(19.72, 39.7) * mm, "end": v(19.62, 39.52) * mm});
            skLineSegment(sketch, "E720", {"start": v(19.62, 39.52) * mm, "end": v(19.52, 39.32) * mm});
            skLineSegment(sketch, "E721", {"start": v(19.52, 39.32) * mm, "end": v(19.42, 39.13) * mm});
            skLineSegment(sketch, "E722", {"start": v(19.42, 39.13) * mm, "end": v(19.32, 38.94) * mm});
            skLineSegment(sketch, "E723", {"start": v(19.32, 38.94) * mm, "end": v(19.12, 39.04) * mm});
            skLineSegment(sketch, "E724", {"start": v(19.12, 39.04) * mm, "end": v(18.92, 39.13) * mm});
            skLineSegment(sketch, "E725", {"start": v(18.92, 39.13) * mm, "end": v(18.72, 39.23) * mm});
            skLineSegment(sketch, "E726", {"start": v(18.72, 39.23) * mm, "end": v(18.52, 39.33) * mm});
            skLineSegment(sketch, "E727", {"start": v(18.52, 39.33) * mm, "end": v(18.32, 39.43) * mm});
            skLineSegment(sketch, "E728", {"start": v(18.32, 39.43) * mm, "end": v(18.12, 39.53) * mm});
            skLineSegment(sketch, "E729", {"start": v(18.12, 39.53) * mm, "end": v(17.92, 39.62) * mm});
            skLineSegment(sketch, "E730", {"start": v(17.92, 39.62) * mm, "end": v(17.72, 39.72) * mm});
            skLineSegment(sketch, "E731", {"start": v(17.72, 39.72) * mm, "end": v(17.52, 39.82) * mm});
            skLineSegment(sketch, "E732", {"start": v(17.52, 39.82) * mm, "end": v(17.36, 39.9) * mm});
            skLineSegment(sketch, "E733", {"start": v(17.36, 39.9) * mm, "end": v(17.45, 40.1) * mm});
            skLineSegment(sketch, "E734", {"start": v(17.45, 40.1) * mm, "end": v(17.54, 40.3) * mm});
            skLineSegment(sketch, "E735", {"start": v(17.54, 40.3) * mm, "end": v(17.63, 40.49) * mm});
            skLineSegment(sketch, "E736", {"start": v(17.63, 40.49) * mm, "end": v(17.72, 40.69) * mm});
            skLineSegment(sketch, "E737", {"start": v(17.72, 40.69) * mm, "end": v(17.81, 40.88) * mm});
            skLineSegment(sketch, "E738", {"start": v(17.81, 40.88) * mm, "end": v(17.9, 41.08) * mm});
            skLineSegment(sketch, "E739", {"start": v(17.9, 41.08) * mm, "end": v(18, 41.28) * mm});
            skLineSegment(sketch, "E740", {"start": v(18, 41.28) * mm, "end": v(18.08, 41.47) * mm});
            skLineSegment(sketch, "E741", {"start": v(18.08, 41.47) * mm, "end": v(18.17, 41.67) * mm});
            skLineSegment(sketch, "E742", {"start": v(18.17, 41.67) * mm, "end": v(18.26, 41.87) * mm});
            skLineSegment(sketch, "E743", {"start": v(18.26, 41.87) * mm, "end": v(18.35, 42.06) * mm});
            skLineSegment(sketch, "E744", {"start": v(18.35, 42.06) * mm, "end": v(18.44, 42.26) * mm});
            skLineSegment(sketch, "E745", {"start": v(18.44, 42.26) * mm, "end": v(18.53, 42.46) * mm});
            skLineSegment(sketch, "E746", {"start": v(18.53, 42.46) * mm, "end": v(18.62, 42.66) * mm});
            skLineSegment(sketch, "E747", {"start": v(18.62, 42.66) * mm, "end": v(18.71, 42.85) * mm});
            skLineSegment(sketch, "E748", {"start": v(18.71, 42.85) * mm, "end": v(18.77, 43.05) * mm});
            skLineSegment(sketch, "E749", {"start": v(18.77, 43.05) * mm, "end": v(18.78, 43.25) * mm});
            skLineSegment(sketch, "E750", {"start": v(18.78, 43.25) * mm, "end": v(18.73, 43.45) * mm});
            skLineSegment(sketch, "E751", {"start": v(18.73, 43.45) * mm, "end": v(18.63, 43.63) * mm});
            skLineSegment(sketch, "E752", {"start": v(18.63, 43.63) * mm, "end": v(18.5, 43.77) * mm});
            skLineSegment(sketch, "E753", {"start": v(18.5, 43.77) * mm, "end": v(18.32, 43.88) * mm});
            skLineSegment(sketch, "E754", {"start": v(18.32, 43.88) * mm, "end": v(18.12, 43.94) * mm});
            skLineSegment(sketch, "E755", {"start": v(18.12, 43.94) * mm, "end": v(18, 43.95) * mm});
            skLineSegment(sketch, "E756", {"start": v(18, 43.95) * mm, "end": v(17.8, 43.92) * mm});
            skLineSegment(sketch, "E757", {"start": v(17.8, 43.92) * mm, "end": v(17.61, 43.84) * mm});
            skLineSegment(sketch, "E758", {"start": v(17.61, 43.84) * mm, "end": v(17.45, 43.71) * mm});
            skLineSegment(sketch, "E759", {"start": v(17.45, 43.71) * mm, "end": v(17.33, 43.55) * mm});
            skLineSegment(sketch, "E760", {"start": v(17.33, 43.55) * mm, "end": v(17.24, 43.35) * mm});
            skLineSegment(sketch, "E761", {"start": v(17.24, 43.35) * mm, "end": v(17.15, 43.14) * mm});
            skLineSegment(sketch, "E762", {"start": v(17.15, 43.14) * mm, "end": v(17.07, 42.93) * mm});
            skLineSegment(sketch, "E763", {"start": v(17.07, 42.93) * mm, "end": v(16.98, 42.73) * mm});
            skLineSegment(sketch, "E764", {"start": v(16.98, 42.73) * mm, "end": v(16.9, 42.52) * mm});
            skLineSegment(sketch, "E765", {"start": v(16.9, 42.52) * mm, "end": v(16.8, 42.32) * mm});
            skLineSegment(sketch, "E766", {"start": v(16.8, 42.32) * mm, "end": v(16.72, 42.11) * mm});
            skLineSegment(sketch, "E767", {"start": v(16.72, 42.11) * mm, "end": v(16.64, 41.9) * mm});
            skLineSegment(sketch, "E768", {"start": v(16.64, 41.9) * mm, "end": v(16.55, 41.7) * mm});
            skLineSegment(sketch, "E769", {"start": v(16.55, 41.7) * mm, "end": v(16.46, 41.48) * mm});
            skLineSegment(sketch, "E770", {"start": v(16.46, 41.48) * mm, "end": v(16.37, 41.28) * mm});
            skLineSegment(sketch, "E771", {"start": v(16.37, 41.28) * mm, "end": v(16.29, 41.08) * mm});
            skLineSegment(sketch, "E772", {"start": v(16.29, 41.08) * mm, "end": v(16.2, 40.88) * mm});
            skLineSegment(sketch, "E773", {"start": v(16.2, 40.88) * mm, "end": v(16.12, 40.68) * mm});
            skLineSegment(sketch, "E774", {"start": v(16.12, 40.68) * mm, "end": v(16.04, 40.48) * mm});
            skLineSegment(sketch, "E775", {"start": v(16.04, 40.48) * mm, "end": v(15.83, 40.56) * mm});
            skLineSegment(sketch, "E776", {"start": v(15.83, 40.56) * mm, "end": v(15.62, 40.64) * mm});
            skLineSegment(sketch, "E777", {"start": v(15.62, 40.64) * mm, "end": v(15.42, 40.72) * mm});
            skLineSegment(sketch, "E778", {"start": v(15.42, 40.72) * mm, "end": v(15.2, 40.8) * mm});
            skLineSegment(sketch, "E779", {"start": v(15.2, 40.8) * mm, "end": v(15, 40.88) * mm});
            skLineSegment(sketch, "E780", {"start": v(15, 40.88) * mm, "end": v(14.8, 40.96) * mm});
            skLineSegment(sketch, "E781", {"start": v(14.8, 40.96) * mm, "end": v(14.59, 41.04) * mm});
            skLineSegment(sketch, "E782", {"start": v(14.59, 41.04) * mm, "end": v(14.38, 41.13) * mm});
            skLineSegment(sketch, "E783", {"start": v(14.38, 41.13) * mm, "end": v(14.17, 41.2) * mm});
            skLineSegment(sketch, "E784", {"start": v(14.17, 41.2) * mm, "end": v(14, 41.27) * mm});
            skLineSegment(sketch, "E785", {"start": v(14, 41.27) * mm, "end": v(14.08, 41.48) * mm});
            skLineSegment(sketch, "E786", {"start": v(14.08, 41.48) * mm, "end": v(14.15, 41.68) * mm});
            skLineSegment(sketch, "E787", {"start": v(14.15, 41.68) * mm, "end": v(14.22, 41.88) * mm});
            skLineSegment(sketch, "E788", {"start": v(14.22, 41.88) * mm, "end": v(14.3, 42.09) * mm});
            skLineSegment(sketch, "E789", {"start": v(14.3, 42.09) * mm, "end": v(14.37, 42.3) * mm});
            skLineSegment(sketch, "E790", {"start": v(14.37, 42.3) * mm, "end": v(14.45, 42.5) * mm});
            skLineSegment(sketch, "E791", {"start": v(14.45, 42.5) * mm, "end": v(14.52, 42.7) * mm});
            skLineSegment(sketch, "E792", {"start": v(14.52, 42.7) * mm, "end": v(14.6, 42.9) * mm});
            skLineSegment(sketch, "E793", {"start": v(14.6, 42.9) * mm, "end": v(14.67, 43.1) * mm});
            skLineSegment(sketch, "E794", {"start": v(14.67, 43.1) * mm, "end": v(14.74, 43.3) * mm});
            skLineSegment(sketch, "E795", {"start": v(14.74, 43.3) * mm, "end": v(14.81, 43.51) * mm});
            skLineSegment(sketch, "E796", {"start": v(14.81, 43.51) * mm, "end": v(14.89, 43.72) * mm});
            skLineSegment(sketch, "E797", {"start": v(14.89, 43.72) * mm, "end": v(14.96, 43.92) * mm});
            skLineSegment(sketch, "E798", {"start": v(14.96, 43.92) * mm, "end": v(15.04, 44.12) * mm});
            skLineSegment(sketch, "E799", {"start": v(15.04, 44.12) * mm, "end": v(15.1, 44.33) * mm});
            skLineSegment(sketch, "E800", {"start": v(15.1, 44.33) * mm, "end": v(15.15, 44.53) * mm});
            skLineSegment(sketch, "E801", {"start": v(15.15, 44.53) * mm, "end": v(15.14, 44.73) * mm});
            skLineSegment(sketch, "E802", {"start": v(15.14, 44.73) * mm, "end": v(15.08, 44.92) * mm});
            skLineSegment(sketch, "E803", {"start": v(15.08, 44.92) * mm, "end": v(14.96, 45.1) * mm});
            skLineSegment(sketch, "E804", {"start": v(14.96, 45.1) * mm, "end": v(14.81, 45.23) * mm});
            skLineSegment(sketch, "E805", {"start": v(14.81, 45.23) * mm, "end": v(14.63, 45.32) * mm});
            skLineSegment(sketch, "E806", {"start": v(14.63, 45.32) * mm, "end": v(14.43, 45.36) * mm});
            skLineSegment(sketch, "E807", {"start": v(14.43, 45.36) * mm, "end": v(14.39, 45.36) * mm});
            skLineSegment(sketch, "E808", {"start": v(14.39, 45.36) * mm, "end": v(14.19, 45.34) * mm});
            skLineSegment(sketch, "E809", {"start": v(14.19, 45.34) * mm, "end": v(14, 45.26) * mm});
            skLineSegment(sketch, "E810", {"start": v(14, 45.26) * mm, "end": v(13.83, 45.14) * mm});
            skLineSegment(sketch, "E811", {"start": v(13.83, 45.14) * mm, "end": v(13.7, 44.98) * mm});
            skLineSegment(sketch, "E812", {"start": v(13.7, 44.98) * mm, "end": v(13.63, 44.77) * mm});
            skLineSegment(sketch, "E813", {"start": v(13.63, 44.77) * mm, "end": v(13.55, 44.56) * mm});
            skLineSegment(sketch, "E814", {"start": v(13.55, 44.56) * mm, "end": v(13.49, 44.35) * mm});
            skLineSegment(sketch, "E815", {"start": v(13.49, 44.35) * mm, "end": v(13.42, 44.14) * mm});
            skLineSegment(sketch, "E816", {"start": v(13.42, 44.14) * mm, "end": v(13.35, 43.93) * mm});
            skLineSegment(sketch, "E817", {"start": v(13.35, 43.93) * mm, "end": v(13.27, 43.7) * mm});
            skLineSegment(sketch, "E818", {"start": v(13.27, 43.7) * mm, "end": v(13.2, 43.5) * mm});
            skLineSegment(sketch, "E819", {"start": v(13.2, 43.5) * mm, "end": v(13.14, 43.29) * mm});
            skLineSegment(sketch, "E820", {"start": v(13.14, 43.29) * mm, "end": v(13.07, 43.08) * mm});
            skLineSegment(sketch, "E821", {"start": v(13.07, 43.08) * mm, "end": v(13, 42.87) * mm});
            skLineSegment(sketch, "E822", {"start": v(13, 42.87) * mm, "end": v(12.94, 42.67) * mm});
            skLineSegment(sketch, "E823", {"start": v(12.94, 42.67) * mm, "end": v(12.87, 42.46) * mm});
            skLineSegment(sketch, "E824", {"start": v(12.87, 42.46) * mm, "end": v(12.8, 42.26) * mm});
            skLineSegment(sketch, "E825", {"start": v(12.8, 42.26) * mm, "end": v(12.74, 42.05) * mm});
            skLineSegment(sketch, "E826", {"start": v(12.74, 42.05) * mm, "end": v(12.67, 41.84) * mm});
            skLineSegment(sketch, "E827", {"start": v(12.67, 41.84) * mm, "end": v(12.64, 41.74) * mm});
            skLineSegment(sketch, "E828", {"start": v(12.64, 41.74) * mm, "end": v(12.42, 41.8) * mm});
            skLineSegment(sketch, "E829", {"start": v(12.42, 41.8) * mm, "end": v(12.21, 41.87) * mm});
            skLineSegment(sketch, "E830", {"start": v(12.21, 41.87) * mm, "end": v(12, 41.93) * mm});
            skLineSegment(sketch, "E831", {"start": v(12, 41.93) * mm, "end": v(11.78, 42) * mm});
            skLineSegment(sketch, "E832", {"start": v(11.78, 42) * mm, "end": v(11.57, 42.06) * mm});
            skLineSegment(sketch, "E833", {"start": v(11.57, 42.06) * mm, "end": v(11.36, 42.12) * mm});
            skLineSegment(sketch, "E834", {"start": v(11.36, 42.12) * mm, "end": v(11.14, 42.19) * mm});
            skLineSegment(sketch, "E835", {"start": v(11.14, 42.19) * mm, "end": v(10.93, 42.25) * mm});
            skLineSegment(sketch, "E836", {"start": v(10.93, 42.25) * mm, "end": v(10.72, 42.31) * mm});
            skLineSegment(sketch, "E837", {"start": v(10.72, 42.31) * mm, "end": v(10.54, 42.36) * mm});
            skLineSegment(sketch, "E838", {"start": v(10.54, 42.36) * mm, "end": v(10.6, 42.57) * mm});
            skLineSegment(sketch, "E839", {"start": v(10.6, 42.57) * mm, "end": v(10.66, 42.78) * mm});
            skLineSegment(sketch, "E840", {"start": v(10.66, 42.78) * mm, "end": v(10.71, 43) * mm});
            skLineSegment(sketch, "E841", {"start": v(10.71, 43) * mm, "end": v(10.77, 43.2) * mm});
            skLineSegment(sketch, "E842", {"start": v(10.77, 43.2) * mm, "end": v(10.83, 43.4) * mm});
            skLineSegment(sketch, "E843", {"start": v(10.83, 43.4) * mm, "end": v(10.88, 43.62) * mm});
            skLineSegment(sketch, "E844", {"start": v(10.88, 43.62) * mm, "end": v(10.94, 43.83) * mm});
            skLineSegment(sketch, "E845", {"start": v(10.94, 43.83) * mm, "end": v(11, 44.04) * mm});
            skLineSegment(sketch, "E846", {"start": v(11, 44.04) * mm, "end": v(11.05, 44.25) * mm});
            skLineSegment(sketch, "E847", {"start": v(11.05, 44.25) * mm, "end": v(11.11, 44.46) * mm});
            skLineSegment(sketch, "E848", {"start": v(11.11, 44.46) * mm, "end": v(11.17, 44.66) * mm});
            skLineSegment(sketch, "E849", {"start": v(11.17, 44.66) * mm, "end": v(11.22, 44.87) * mm});
            skLineSegment(sketch, "E850", {"start": v(11.22, 44.87) * mm, "end": v(11.28, 45.08) * mm});
            skLineSegment(sketch, "E851", {"start": v(11.28, 45.08) * mm, "end": v(11.34, 45.3) * mm});
            skLineSegment(sketch, "E852", {"start": v(11.34, 45.3) * mm, "end": v(11.4, 45.5) * mm});
            skLineSegment(sketch, "E853", {"start": v(11.4, 45.5) * mm, "end": v(11.42, 45.7) * mm});
            skLineSegment(sketch, "E854", {"start": v(11.42, 45.7) * mm, "end": v(11.4, 45.9) * mm});
            skLineSegment(sketch, "E855", {"start": v(11.4, 45.9) * mm, "end": v(11.31, 46.1) * mm});
            skLineSegment(sketch, "E856", {"start": v(11.31, 46.1) * mm, "end": v(11.19, 46.25) * mm});
            skLineSegment(sketch, "E857", {"start": v(11.19, 46.25) * mm, "end": v(11.02, 46.37) * mm});
            skLineSegment(sketch, "E858", {"start": v(11.02, 46.37) * mm, "end": v(10.83, 46.45) * mm});
            skLineSegment(sketch, "E859", {"start": v(10.83, 46.45) * mm, "end": v(10.63, 46.47) * mm});
            skLineSegment(sketch, "E860", {"start": v(10.63, 46.47) * mm, "end": v(10.43, 46.44) * mm});
            skLineSegment(sketch, "E861", {"start": v(10.43, 46.44) * mm, "end": v(10.24, 46.36) * mm});
            skLineSegment(sketch, "E862", {"start": v(10.24, 46.36) * mm, "end": v(10.08, 46.24) * mm});
            skLineSegment(sketch, "E863", {"start": v(10.08, 46.24) * mm, "end": v(9.96, 46.07) * mm});
            skLineSegment(sketch, "E864", {"start": v(9.96, 46.07) * mm, "end": v(9.89, 45.88) * mm});
            skLineSegment(sketch, "E865", {"start": v(9.89, 45.88) * mm, "end": v(9.84, 45.67) * mm});
            skLineSegment(sketch, "E866", {"start": v(9.84, 45.67) * mm, "end": v(9.8, 45.46) * mm});
            skLineSegment(sketch, "E867", {"start": v(9.8, 45.46) * mm, "end": v(9.74, 45.25) * mm});
            skLineSegment(sketch, "E868", {"start": v(9.74, 45.25) * mm, "end": v(9.7, 45.04) * mm});
            skLineSegment(sketch, "E869", {"start": v(9.7, 45.04) * mm, "end": v(9.64, 44.83) * mm});
            skLineSegment(sketch, "E870", {"start": v(9.64, 44.83) * mm, "end": v(9.6, 44.62) * mm});
            skLineSegment(sketch, "E871", {"start": v(9.6, 44.62) * mm, "end": v(9.54, 44.4) * mm});
            skLineSegment(sketch, "E872", {"start": v(9.54, 44.4) * mm, "end": v(9.5, 44.2) * mm});
            skLineSegment(sketch, "E873", {"start": v(9.5, 44.2) * mm, "end": v(9.44, 43.98) * mm});
            skLineSegment(sketch, "E874", {"start": v(9.44, 43.98) * mm, "end": v(9.4, 43.77) * mm});
            skLineSegment(sketch, "E875", {"start": v(9.4, 43.77) * mm, "end": v(9.34, 43.56) * mm});
            skLineSegment(sketch, "E876", {"start": v(9.34, 43.56) * mm, "end": v(9.3, 43.35) * mm});
            skLineSegment(sketch, "E877", {"start": v(9.3, 43.35) * mm, "end": v(9.24, 43.14) * mm});
            skLineSegment(sketch, "E878", {"start": v(9.24, 43.14) * mm, "end": v(9.2, 42.93) * mm});
            skLineSegment(sketch, "E879", {"start": v(9.2, 42.93) * mm, "end": v(9.14, 42.72) * mm});
            skLineSegment(sketch, "E880", {"start": v(9.14, 42.72) * mm, "end": v(8.93, 42.76) * mm});
            skLineSegment(sketch, "E881", {"start": v(8.93, 42.76) * mm, "end": v(8.7, 42.8) * mm});
            skLineSegment(sketch, "E882", {"start": v(8.7, 42.8) * mm, "end": v(8.49, 42.86) * mm});
            skLineSegment(sketch, "E883", {"start": v(8.49, 42.86) * mm, "end": v(8.27, 42.9) * mm});
            skLineSegment(sketch, "E884", {"start": v(8.27, 42.9) * mm, "end": v(8.05, 42.95) * mm});
            skLineSegment(sketch, "E885", {"start": v(8.05, 42.95) * mm, "end": v(7.84, 43) * mm});
            skLineSegment(sketch, "E886", {"start": v(7.84, 43) * mm, "end": v(7.62, 43.04) * mm});
            skLineSegment(sketch, "E887", {"start": v(7.62, 43.04) * mm, "end": v(7.4, 43.08) * mm});
            skLineSegment(sketch, "E888", {"start": v(7.4, 43.08) * mm, "end": v(7.18, 43.13) * mm});
            skLineSegment(sketch, "E889", {"start": v(7.18, 43.13) * mm, "end": v(7, 43.17) * mm});
            skLineSegment(sketch, "E890", {"start": v(7, 43.17) * mm, "end": v(7.05, 43.38) * mm});
            skLineSegment(sketch, "E891", {"start": v(7.05, 43.38) * mm, "end": v(7.08, 43.6) * mm});
            skLineSegment(sketch, "E892", {"start": v(7.08, 43.6) * mm, "end": v(7.12, 43.8) * mm});
            skLineSegment(sketch, "E893", {"start": v(7.12, 43.8) * mm, "end": v(7.16, 44.02) * mm});
            skLineSegment(sketch, "E894", {"start": v(7.16, 44.02) * mm, "end": v(7.2, 44.23) * mm});
            skLineSegment(sketch, "E895", {"start": v(7.2, 44.23) * mm, "end": v(7.24, 44.45) * mm});
            skLineSegment(sketch, "E896", {"start": v(7.24, 44.45) * mm, "end": v(7.28, 44.66) * mm});
            skLineSegment(sketch, "E897", {"start": v(7.28, 44.66) * mm, "end": v(7.32, 44.87) * mm});
            skLineSegment(sketch, "E898", {"start": v(7.32, 44.87) * mm, "end": v(7.36, 45.08) * mm});
            skLineSegment(sketch, "E899", {"start": v(7.36, 45.08) * mm, "end": v(7.4, 45.3) * mm});
            skLineSegment(sketch, "E900", {"start": v(7.4, 45.3) * mm, "end": v(7.44, 45.51) * mm});
            skLineSegment(sketch, "E901", {"start": v(7.44, 45.51) * mm, "end": v(7.48, 45.72) * mm});
            skLineSegment(sketch, "E902", {"start": v(7.48, 45.72) * mm, "end": v(7.52, 45.94) * mm});
            skLineSegment(sketch, "E903", {"start": v(7.52, 45.94) * mm, "end": v(7.56, 46.15) * mm});
            skLineSegment(sketch, "E904", {"start": v(7.56, 46.15) * mm, "end": v(7.6, 46.36) * mm});
            skLineSegment(sketch, "E905", {"start": v(7.6, 46.36) * mm, "end": v(7.6, 46.57) * mm});
            skLineSegment(sketch, "E906", {"start": v(7.6, 46.57) * mm, "end": v(7.56, 46.77) * mm});
            skLineSegment(sketch, "E907", {"start": v(7.56, 46.77) * mm, "end": v(7.46, 46.95) * mm});
            skLineSegment(sketch, "E908", {"start": v(7.46, 46.95) * mm, "end": v(7.32, 47.1) * mm});
            skLineSegment(sketch, "E909", {"start": v(7.32, 47.1) * mm, "end": v(7.15, 47.2) * mm});
            skLineSegment(sketch, "E910", {"start": v(7.15, 47.2) * mm, "end": v(6.96, 47.26) * mm});
            skLineSegment(sketch, "E911", {"start": v(6.96, 47.26) * mm, "end": v(6.84, 47.27) * mm});
            skLineSegment(sketch, "E912", {"start": v(6.84, 47.27) * mm, "end": v(6.63, 47.25) * mm});
            skLineSegment(sketch, "E913", {"start": v(6.63, 47.25) * mm, "end": v(6.45, 47.17) * mm});
            skLineSegment(sketch, "E914", {"start": v(6.45, 47.17) * mm, "end": v(6.28, 47.05) * mm});
            skLineSegment(sketch, "E915", {"start": v(6.28, 47.05) * mm, "end": v(6.16, 46.89) * mm});
            skLineSegment(sketch, "E916", {"start": v(6.16, 46.89) * mm, "end": v(6.08, 46.7) * mm});
            skLineSegment(sketch, "E917", {"start": v(6.08, 46.7) * mm, "end": v(6.04, 46.48) * mm});
            skLineSegment(sketch, "E918", {"start": v(6.04, 46.48) * mm, "end": v(6.01, 46.26) * mm});
            skLineSegment(sketch, "E919", {"start": v(6.01, 46.26) * mm, "end": v(5.98, 46.04) * mm});
            skLineSegment(sketch, "E920", {"start": v(5.98, 46.04) * mm, "end": v(5.94, 45.82) * mm});
            skLineSegment(sketch, "E921", {"start": v(5.94, 45.82) * mm, "end": v(5.91, 45.6) * mm});
            skLineSegment(sketch, "E922", {"start": v(5.91, 45.6) * mm, "end": v(5.88, 45.38) * mm});
            skLineSegment(sketch, "E923", {"start": v(5.88, 45.38) * mm, "end": v(5.84, 45.16) * mm});
            skLineSegment(sketch, "E924", {"start": v(5.84, 45.16) * mm, "end": v(5.81, 44.94) * mm});
            skLineSegment(sketch, "E925", {"start": v(5.81, 44.94) * mm, "end": v(5.78, 44.72) * mm});
            skLineSegment(sketch, "E926", {"start": v(5.78, 44.72) * mm, "end": v(5.74, 44.48) * mm});
            skLineSegment(sketch, "E927", {"start": v(5.74, 44.48) * mm, "end": v(5.71, 44.26) * mm});
            skLineSegment(sketch, "E928", {"start": v(5.71, 44.26) * mm, "end": v(5.68, 44.05) * mm});
            skLineSegment(sketch, "E929", {"start": v(5.68, 44.05) * mm, "end": v(5.65, 43.83) * mm});
            skLineSegment(sketch, "E930", {"start": v(5.65, 43.83) * mm, "end": v(5.61, 43.62) * mm});
            skLineSegment(sketch, "E931", {"start": v(5.61, 43.62) * mm, "end": v(5.58, 43.4) * mm});
            skLineSegment(sketch, "E932", {"start": v(5.58, 43.4) * mm, "end": v(5.36, 43.43) * mm});
            skLineSegment(sketch, "E933", {"start": v(5.36, 43.43) * mm, "end": v(5.14, 43.46) * mm});
            skLineSegment(sketch, "E934", {"start": v(5.14, 43.46) * mm, "end": v(4.92, 43.49) * mm});
            skLineSegment(sketch, "E935", {"start": v(4.92, 43.49) * mm, "end": v(4.7, 43.51) * mm});
            skLineSegment(sketch, "E936", {"start": v(4.7, 43.51) * mm, "end": v(4.48, 43.54) * mm});
            skLineSegment(sketch, "E937", {"start": v(4.48, 43.54) * mm, "end": v(4.26, 43.57) * mm});
            skLineSegment(sketch, "E938", {"start": v(4.26, 43.57) * mm, "end": v(4.03, 43.6) * mm});
            skLineSegment(sketch, "E939", {"start": v(4.03, 43.6) * mm, "end": v(3.81, 43.62) * mm});
            skLineSegment(sketch, "E940", {"start": v(3.81, 43.62) * mm, "end": v(3.6, 43.65) * mm});
            skLineSegment(sketch, "E941", {"start": v(3.6, 43.65) * mm, "end": v(3.41, 43.67) * mm});
            skLineSegment(sketch, "E942", {"start": v(3.41, 43.67) * mm, "end": v(3.44, 43.89) * mm});
            skLineSegment(sketch, "E943", {"start": v(3.44, 43.89) * mm, "end": v(3.46, 44.1) * mm});
            skLineSegment(sketch, "E944", {"start": v(3.46, 44.1) * mm, "end": v(3.48, 44.32) * mm});
            skLineSegment(sketch, "E945", {"start": v(3.48, 44.32) * mm, "end": v(3.5, 44.54) * mm});
            skLineSegment(sketch, "E946", {"start": v(3.5, 44.54) * mm, "end": v(3.52, 44.75) * mm});
            skLineSegment(sketch, "E947", {"start": v(3.52, 44.75) * mm, "end": v(3.54, 44.97) * mm});
            skLineSegment(sketch, "E948", {"start": v(3.54, 44.97) * mm, "end": v(3.56, 45.18) * mm});
            skLineSegment(sketch, "E949", {"start": v(3.56, 45.18) * mm, "end": v(3.59, 45.4) * mm});
            skLineSegment(sketch, "E950", {"start": v(3.59, 45.4) * mm, "end": v(3.6, 45.62) * mm});
            skLineSegment(sketch, "E951", {"start": v(3.6, 45.62) * mm, "end": v(3.63, 45.83) * mm});
            skLineSegment(sketch, "E952", {"start": v(3.63, 45.83) * mm, "end": v(3.65, 46.05) * mm});
            skLineSegment(sketch, "E953", {"start": v(3.65, 46.05) * mm, "end": v(3.67, 46.26) * mm});
            skLineSegment(sketch, "E954", {"start": v(3.67, 46.26) * mm, "end": v(3.7, 46.48) * mm});
            skLineSegment(sketch, "E955", {"start": v(3.7, 46.48) * mm, "end": v(3.71, 46.7) * mm});
            skLineSegment(sketch, "E956", {"start": v(3.71, 46.7) * mm, "end": v(3.74, 46.9) * mm});
            skLineSegment(sketch, "E957", {"start": v(3.74, 46.9) * mm, "end": v(3.73, 47.11) * mm});
            skLineSegment(sketch, "E958", {"start": v(3.73, 47.11) * mm, "end": v(3.67, 47.3) * mm});
            skLineSegment(sketch, "E959", {"start": v(3.67, 47.3) * mm, "end": v(3.56, 47.48) * mm});
            skLineSegment(sketch, "E960", {"start": v(3.56, 47.48) * mm, "end": v(3.4, 47.62) * mm});
            skLineSegment(sketch, "E961", {"start": v(3.4, 47.62) * mm, "end": v(3.23, 47.7) * mm});
            skLineSegment(sketch, "E962", {"start": v(3.23, 47.7) * mm, "end": v(3.03, 47.75) * mm});
            skLineSegment(sketch, "E963", {"start": v(3.03, 47.75) * mm, "end": v(2.95, 47.75) * mm});
            skLineSegment(sketch, "E964", {"start": v(2.95, 47.75) * mm, "end": v(2.75, 47.72) * mm});
            skLineSegment(sketch, "E965", {"start": v(2.75, 47.72) * mm, "end": v(2.56, 47.64) * mm});
            skLineSegment(sketch, "E966", {"start": v(2.56, 47.64) * mm, "end": v(2.4, 47.51) * mm});
            skLineSegment(sketch, "E967", {"start": v(2.4, 47.51) * mm, "end": v(2.28, 47.35) * mm});
            skLineSegment(sketch, "E968", {"start": v(2.28, 47.35) * mm, "end": v(2.2, 47.16) * mm});
            skLineSegment(sketch, "E969", {"start": v(2.2, 47.16) * mm, "end": v(2.18, 46.93) * mm});
            skLineSegment(sketch, "E970", {"start": v(2.18, 46.93) * mm, "end": v(2.17, 46.71) * mm});
            skLineSegment(sketch, "E971", {"start": v(2.17, 46.71) * mm, "end": v(2.15, 46.5) * mm});
            skLineSegment(sketch, "E972", {"start": v(2.15, 46.5) * mm, "end": v(2.14, 46.28) * mm});
            skLineSegment(sketch, "E973", {"start": v(2.14, 46.28) * mm, "end": v(2.13, 46.06) * mm});
            skLineSegment(sketch, "E974", {"start": v(2.13, 46.06) * mm, "end": v(2.11, 45.85) * mm});
            skLineSegment(sketch, "E975", {"start": v(2.11, 45.85) * mm, "end": v(2.1, 45.63) * mm});
            skLineSegment(sketch, "E976", {"start": v(2.1, 45.63) * mm, "end": v(2.08, 45.42) * mm});
            skLineSegment(sketch, "E977", {"start": v(2.08, 45.42) * mm, "end": v(2.07, 45.2) * mm});
            skLineSegment(sketch, "E978", {"start": v(2.07, 45.2) * mm, "end": v(2.05, 44.98) * mm});
            skLineSegment(sketch, "E979", {"start": v(2.05, 44.98) * mm, "end": v(2.04, 44.77) * mm});
            skLineSegment(sketch, "E980", {"start": v(2.04, 44.77) * mm, "end": v(2.03, 44.55) * mm});
            skLineSegment(sketch, "E981", {"start": v(2.03, 44.55) * mm, "end": v(2.01, 44.33) * mm});
            skLineSegment(sketch, "E982", {"start": v(2.01, 44.33) * mm, "end": v(2, 44.12) * mm});
            skLineSegment(sketch, "E983", {"start": v(2, 44.12) * mm, "end": v(1.98, 43.9) * mm});
            skLineSegment(sketch, "E984", {"start": v(1.98, 43.9) * mm, "end": v(1.98, 43.8) * mm});
            skLineSegment(sketch, "E985", {"start": v(1.98, 43.8) * mm, "end": v(1.75, 43.8) * mm});
            skLineSegment(sketch, "E986", {"start": v(1.75, 43.8) * mm, "end": v(1.53, 43.81) * mm});
            skLineSegment(sketch, "E987", {"start": v(1.53, 43.81) * mm, "end": v(1.3, 43.82) * mm});
            skLineSegment(sketch, "E988", {"start": v(1.3, 43.82) * mm, "end": v(1.09, 43.83) * mm});
            skLineSegment(sketch, "E989", {"start": v(1.09, 43.83) * mm, "end": v(0.86, 43.84) * mm});
            skLineSegment(sketch, "E990", {"start": v(0.86, 43.84) * mm, "end": v(0.64, 43.85) * mm});
            skLineSegment(sketch, "E991", {"start": v(0.64, 43.85) * mm, "end": v(0.42, 43.86) * mm});
            skLineSegment(sketch, "E992", {"start": v(0.42, 43.86) * mm, "end": v(0.2, 43.87) * mm});
            skLineSegment(sketch, "E993", {"start": v(0.2, 43.87) * mm, "end": v(-0.03, 43.88) * mm});
            skLineSegment(sketch, "E994", {"start": v(-0.03, 43.88) * mm, "end": v(-0.2, 43.88) * mm});
            skLineSegment(sketch, "E995", {"start": v(-0.2, 43.88) * mm, "end": v(-0.2, 44.1) * mm});
            skLineSegment(sketch, "E996", {"start": v(-0.2, 44.1) * mm, "end": v(-0.2, 44.32) * mm});
            skLineSegment(sketch, "E997", {"start": v(-0.2, 44.32) * mm, "end": v(-0.2, 44.53) * mm});
            skLineSegment(sketch, "E998", {"start": v(-0.2, 44.53) * mm, "end": v(-0.2, 44.75) * mm});
            skLineSegment(sketch, "E999", {"start": v(-0.2, 44.75) * mm, "end": v(-0.19, 44.97) * mm});
            skLineSegment(sketch, "E1000", {"start": v(-0.19, 44.97) * mm, "end": v(-0.19, 45.18) * mm});
            skLineSegment(sketch, "E1001", {"start": v(-0.19, 45.18) * mm, "end": v(-0.18, 45.4) * mm});
            skLineSegment(sketch, "E1002", {"start": v(-0.18, 45.4) * mm, "end": v(-0.18, 45.62) * mm});
            skLineSegment(sketch, "E1003", {"start": v(-0.18, 45.62) * mm, "end": v(-0.17, 45.83) * mm});
            skLineSegment(sketch, "E1004", {"start": v(-0.17, 45.83) * mm, "end": v(-0.17, 46.05) * mm});
            skLineSegment(sketch, "E1005", {"start": v(-0.17, 46.05) * mm, "end": v(-0.17, 46.27) * mm});
            skLineSegment(sketch, "E1006", {"start": v(-0.17, 46.27) * mm, "end": v(-0.16, 46.48) * mm});
            skLineSegment(sketch, "E1007", {"start": v(-0.16, 46.48) * mm, "end": v(-0.16, 46.7) * mm});
            skLineSegment(sketch, "E1008", {"start": v(-0.16, 46.7) * mm, "end": v(-0.16, 46.92) * mm});
            skLineSegment(sketch, "E1009", {"start": v(-0.16, 46.92) * mm, "end": v(-0.15, 47.13) * mm});
            skLineSegment(sketch, "E1010", {"start": v(-0.15, 47.13) * mm, "end": v(-0.18, 47.34) * mm});
            skLineSegment(sketch, "E1011", {"start": v(-0.18, 47.34) * mm, "end": v(-0.26, 47.52) * mm});
            skLineSegment(sketch, "E1012", {"start": v(-0.26, 47.52) * mm, "end": v(-0.38, 47.69) * mm});
            skLineSegment(sketch, "E1013", {"start": v(-0.38, 47.69) * mm, "end": v(-0.54, 47.81) * mm});
            skLineSegment(sketch, "E1014", {"start": v(-0.54, 47.81) * mm, "end": v(-0.73, 47.89) * mm});
            skLineSegment(sketch, "E1015", {"start": v(-0.73, 47.89) * mm, "end": v(-0.93, 47.92) * mm});
            skLineSegment(sketch, "E1016", {"start": v(-0.93, 47.92) * mm, "end": v(-1.13, 47.89) * mm});
            skLineSegment(sketch, "E1017", {"start": v(-1.13, 47.89) * mm, "end": v(-1.32, 47.81) * mm});
            skLineSegment(sketch, "E1018", {"start": v(-1.32, 47.81) * mm, "end": v(-1.48, 47.69) * mm});
            skLineSegment(sketch, "E1019", {"start": v(-1.48, 47.69) * mm, "end": v(-1.6, 47.52) * mm});
            skLineSegment(sketch, "E1020", {"start": v(-1.6, 47.52) * mm, "end": v(-1.68, 47.34) * mm});
            skLineSegment(sketch, "E1021", {"start": v(-1.68, 47.34) * mm, "end": v(-1.7, 47.13) * mm});
            skLineSegment(sketch, "E1022", {"start": v(-1.7, 47.13) * mm, "end": v(-1.7, 46.92) * mm});
            skLineSegment(sketch, "E1023", {"start": v(-1.7, 46.92) * mm, "end": v(-1.7, 46.7) * mm});
            skLineSegment(sketch, "E1024", {"start": v(-1.7, 46.7) * mm, "end": v(-1.7, 46.48) * mm});
            skLineSegment(sketch, "E1025", {"start": v(-1.7, 46.48) * mm, "end": v(-1.7, 46.27) * mm});
            skLineSegment(sketch, "E1026", {"start": v(-1.7, 46.27) * mm, "end": v(-1.69, 46.05) * mm});
            skLineSegment(sketch, "E1027", {"start": v(-1.69, 46.05) * mm, "end": v(-1.68, 45.83) * mm});
            skLineSegment(sketch, "E1028", {"start": v(-1.68, 45.83) * mm, "end": v(-1.68, 45.62) * mm});
            skLineSegment(sketch, "E1029", {"start": v(-1.68, 45.62) * mm, "end": v(-1.68, 45.4) * mm});
            skLineSegment(sketch, "E1030", {"start": v(-1.68, 45.4) * mm, "end": v(-1.67, 45.18) * mm});
            skLineSegment(sketch, "E1031", {"start": v(-1.67, 45.18) * mm, "end": v(-1.67, 44.97) * mm});
            skLineSegment(sketch, "E1032", {"start": v(-1.67, 44.97) * mm, "end": v(-1.67, 44.75) * mm});
            skLineSegment(sketch, "E1033", {"start": v(-1.67, 44.75) * mm, "end": v(-1.66, 44.53) * mm});
            skLineSegment(sketch, "E1034", {"start": v(-1.66, 44.53) * mm, "end": v(-1.66, 44.32) * mm});
            skLineSegment(sketch, "E1035", {"start": v(-1.66, 44.32) * mm, "end": v(-1.65, 44.1) * mm});
            skLineSegment(sketch, "E1036", {"start": v(-1.65, 44.1) * mm, "end": v(-1.65, 43.88) * mm});
            skLineSegment(sketch, "E1037", {"start": v(-1.65, 43.88) * mm, "end": v(-1.87, 43.87) * mm});
            skLineSegment(sketch, "E1038", {"start": v(-1.87, 43.87) * mm, "end": v(-2.1, 43.87) * mm});
            skLineSegment(sketch, "E1039", {"start": v(-2.1, 43.87) * mm, "end": v(-2.32, 43.86) * mm});
            skLineSegment(sketch, "E1040", {"start": v(-2.32, 43.86) * mm, "end": v(-2.54, 43.85) * mm});
            skLineSegment(sketch, "E1041", {"start": v(-2.54, 43.85) * mm, "end": v(-2.76, 43.84) * mm});
            skLineSegment(sketch, "E1042", {"start": v(-2.76, 43.84) * mm, "end": v(-2.99, 43.83) * mm});
            skLineSegment(sketch, "E1043", {"start": v(-2.99, 43.83) * mm, "end": v(-3.2, 43.82) * mm});
            skLineSegment(sketch, "E1044", {"start": v(-3.2, 43.82) * mm, "end": v(-3.43, 43.81) * mm});
            skLineSegment(sketch, "E1045", {"start": v(-3.43, 43.81) * mm, "end": v(-3.65, 43.8) * mm});
            skLineSegment(sketch, "E1046", {"start": v(-3.65, 43.8) * mm, "end": v(-3.83, 43.8) * mm});
            skLineSegment(sketch, "E1047", {"start": v(-3.83, 43.8) * mm, "end": v(-3.85, 44) * mm});
            skLineSegment(sketch, "E1048", {"start": v(-3.85, 44) * mm, "end": v(-3.86, 44.23) * mm});
            skLineSegment(sketch, "E1049", {"start": v(-3.86, 44.23) * mm, "end": v(-3.88, 44.44) * mm});
            skLineSegment(sketch, "E1050", {"start": v(-3.88, 44.44) * mm, "end": v(-3.9, 44.66) * mm});
            skLineSegment(sketch, "E1051", {"start": v(-3.9, 44.66) * mm, "end": v(-3.9, 44.87) * mm});
            skLineSegment(sketch, "E1052", {"start": v(-3.9, 44.87) * mm, "end": v(-3.92, 45.1) * mm});
            skLineSegment(sketch, "E1053", {"start": v(-3.92, 45.1) * mm, "end": v(-3.93, 45.3) * mm});
            skLineSegment(sketch, "E1054", {"start": v(-3.93, 45.3) * mm, "end": v(-3.95, 45.52) * mm});
            skLineSegment(sketch, "E1055", {"start": v(-3.95, 45.52) * mm, "end": v(-3.96, 45.74) * mm});
            skLineSegment(sketch, "E1056", {"start": v(-3.96, 45.74) * mm, "end": v(-3.98, 45.96) * mm});
            skLineSegment(sketch, "E1057", {"start": v(-3.98, 45.96) * mm, "end": v(-4, 46.17) * mm});
            skLineSegment(sketch, "E1058", {"start": v(-4, 46.17) * mm, "end": v(-4, 46.39) * mm});
            skLineSegment(sketch, "E1059", {"start": v(-4, 46.39) * mm, "end": v(-4.02, 46.6) * mm});
            skLineSegment(sketch, "E1060", {"start": v(-4.02, 46.6) * mm, "end": v(-4.03, 46.82) * mm});
            skLineSegment(sketch, "E1061", {"start": v(-4.03, 46.82) * mm, "end": v(-4.05, 47.04) * mm});
            skLineSegment(sketch, "E1062", {"start": v(-4.05, 47.04) * mm, "end": v(-4.09, 47.24) * mm});
            skLineSegment(sketch, "E1063", {"start": v(-4.09, 47.24) * mm, "end": v(-4.18, 47.42) * mm});
            skLineSegment(sketch, "E1064", {"start": v(-4.18, 47.42) * mm, "end": v(-4.32, 47.57) * mm});
            skLineSegment(sketch, "E1065", {"start": v(-4.32, 47.57) * mm, "end": v(-4.49, 47.68) * mm});
            skLineSegment(sketch, "E1066", {"start": v(-4.49, 47.68) * mm, "end": v(-4.68, 47.74) * mm});
            skLineSegment(sketch, "E1067", {"start": v(-4.68, 47.74) * mm, "end": v(-4.8, 47.75) * mm});
            skLineSegment(sketch, "E1068", {"start": v(-4.8, 47.75) * mm, "end": v(-5, 47.73) * mm});
            skLineSegment(sketch, "E1069", {"start": v(-5, 47.73) * mm, "end": v(-5.2, 47.66) * mm});
            skLineSegment(sketch, "E1070", {"start": v(-5.2, 47.66) * mm, "end": v(-5.36, 47.54) * mm});
            skLineSegment(sketch, "E1071", {"start": v(-5.36, 47.54) * mm, "end": v(-5.49, 47.38) * mm});
            skLineSegment(sketch, "E1072", {"start": v(-5.49, 47.38) * mm, "end": v(-5.57, 47.2) * mm});
            skLineSegment(sketch, "E1073", {"start": v(-5.57, 47.2) * mm, "end": v(-5.6, 47) * mm});
            skLineSegment(sketch, "E1074", {"start": v(-5.6, 47) * mm, "end": v(-5.58, 46.77) * mm});
            skLineSegment(sketch, "E1075", {"start": v(-5.58, 46.77) * mm, "end": v(-5.56, 46.55) * mm});
            skLineSegment(sketch, "E1076", {"start": v(-5.56, 46.55) * mm, "end": v(-5.54, 46.33) * mm});
            skLineSegment(sketch, "E1077", {"start": v(-5.54, 46.33) * mm, "end": v(-5.51, 46.1) * mm});
            skLineSegment(sketch, "E1078", {"start": v(-5.51, 46.1) * mm, "end": v(-5.5, 45.88) * mm});
            skLineSegment(sketch, "E1079", {"start": v(-5.5, 45.88) * mm, "end": v(-5.47, 45.66) * mm});
            skLineSegment(sketch, "E1080", {"start": v(-5.47, 45.66) * mm, "end": v(-5.45, 45.44) * mm});
            skLineSegment(sketch, "E1081", {"start": v(-5.45, 45.44) * mm, "end": v(-5.43, 45.22) * mm});
            skLineSegment(sketch, "E1082", {"start": v(-5.43, 45.22) * mm, "end": v(-5.4, 45) * mm});
            skLineSegment(sketch, "E1083", {"start": v(-5.4, 45) * mm, "end": v(-5.38, 44.75) * mm});
            skLineSegment(sketch, "E1084", {"start": v(-5.38, 44.75) * mm, "end": v(-5.36, 44.54) * mm});
            skLineSegment(sketch, "E1085", {"start": v(-5.36, 44.54) * mm, "end": v(-5.34, 44.32) * mm});
            skLineSegment(sketch, "E1086", {"start": v(-5.34, 44.32) * mm, "end": v(-5.32, 44.1) * mm});
            skLineSegment(sketch, "E1087", {"start": v(-5.32, 44.1) * mm, "end": v(-5.3, 43.89) * mm});
            skLineSegment(sketch, "E1088", {"start": v(-5.3, 43.89) * mm, "end": v(-5.27, 43.67) * mm});
            skLineSegment(sketch, "E1089", {"start": v(-5.27, 43.67) * mm, "end": v(-5.5, 43.65) * mm});
            skLineSegment(sketch, "E1090", {"start": v(-5.5, 43.65) * mm, "end": v(-5.71, 43.62) * mm});
            skLineSegment(sketch, "E1091", {"start": v(-5.71, 43.62) * mm, "end": v(-5.94, 43.6) * mm});
            skLineSegment(sketch, "E1092", {"start": v(-5.94, 43.6) * mm, "end": v(-6.16, 43.56) * mm});
            skLineSegment(sketch, "E1093", {"start": v(-6.16, 43.56) * mm, "end": v(-6.38, 43.54) * mm});
            skLineSegment(sketch, "E1094", {"start": v(-6.38, 43.54) * mm, "end": v(-6.6, 43.5) * mm});
            skLineSegment(sketch, "E1095", {"start": v(-6.6, 43.5) * mm, "end": v(-6.82, 43.48) * mm});
            skLineSegment(sketch, "E1096", {"start": v(-6.82, 43.48) * mm, "end": v(-7.04, 43.45) * mm});
            skLineSegment(sketch, "E1097", {"start": v(-7.04, 43.45) * mm, "end": v(-7.26, 43.43) * mm});
            skLineSegment(sketch, "E1098", {"start": v(-7.26, 43.43) * mm, "end": v(-7.44, 43.4) * mm});
            skLineSegment(sketch, "E1099", {"start": v(-7.44, 43.4) * mm, "end": v(-7.47, 43.62) * mm});
            skLineSegment(sketch, "E1100", {"start": v(-7.47, 43.62) * mm, "end": v(-7.5, 43.83) * mm});
            skLineSegment(sketch, "E1101", {"start": v(-7.5, 43.83) * mm, "end": v(-7.54, 44.05) * mm});
            skLineSegment(sketch, "E1102", {"start": v(-7.54, 44.05) * mm, "end": v(-7.57, 44.26) * mm});
            skLineSegment(sketch, "E1103", {"start": v(-7.57, 44.26) * mm, "end": v(-7.6, 44.48) * mm});
            skLineSegment(sketch, "E1104", {"start": v(-7.6, 44.48) * mm, "end": v(-7.63, 44.7) * mm});
            skLineSegment(sketch, "E1105", {"start": v(-7.63, 44.7) * mm, "end": v(-7.66, 44.9) * mm});
            skLineSegment(sketch, "E1106", {"start": v(-7.66, 44.9) * mm, "end": v(-7.7, 45.12) * mm});
            skLineSegment(sketch, "E1107", {"start": v(-7.7, 45.12) * mm, "end": v(-7.73, 45.33) * mm});
            skLineSegment(sketch, "E1108", {"start": v(-7.73, 45.33) * mm, "end": v(-7.76, 45.55) * mm});
            skLineSegment(sketch, "E1109", {"start": v(-7.76, 45.55) * mm, "end": v(-7.8, 45.76) * mm});
            skLineSegment(sketch, "E1110", {"start": v(-7.8, 45.76) * mm, "end": v(-7.83, 45.98) * mm});
            skLineSegment(sketch, "E1111", {"start": v(-7.83, 45.98) * mm, "end": v(-7.86, 46.2) * mm});
            skLineSegment(sketch, "E1112", {"start": v(-7.86, 46.2) * mm, "end": v(-7.89, 46.4) * mm});
            skLineSegment(sketch, "E1113", {"start": v(-7.89, 46.4) * mm, "end": v(-7.92, 46.62) * mm});
            skLineSegment(sketch, "E1114", {"start": v(-7.92, 46.62) * mm, "end": v(-7.98, 46.81) * mm});
            skLineSegment(sketch, "E1115", {"start": v(-7.98, 46.81) * mm, "end": v(-8.09, 46.99) * mm});
            skLineSegment(sketch, "E1116", {"start": v(-8.09, 46.99) * mm, "end": v(-8.23, 47.13) * mm});
            skLineSegment(sketch, "E1117", {"start": v(-8.23, 47.13) * mm, "end": v(-8.41, 47.22) * mm});
            skLineSegment(sketch, "E1118", {"start": v(-8.41, 47.22) * mm, "end": v(-8.61, 47.27) * mm});
            skLineSegment(sketch, "E1119", {"start": v(-8.61, 47.27) * mm, "end": v(-8.7, 47.27) * mm});
            skLineSegment(sketch, "E1120", {"start": v(-8.7, 47.27) * mm, "end": v(-8.9, 47.24) * mm});
            skLineSegment(sketch, "E1121", {"start": v(-8.9, 47.24) * mm, "end": v(-9.08, 47.17) * mm});
            skLineSegment(sketch, "E1122", {"start": v(-9.08, 47.17) * mm, "end": v(-9.24, 47.04) * mm});
            skLineSegment(sketch, "E1123", {"start": v(-9.24, 47.04) * mm, "end": v(-9.36, 46.88) * mm});
            skLineSegment(sketch, "E1124", {"start": v(-9.36, 46.88) * mm, "end": v(-9.44, 46.69) * mm});
            skLineSegment(sketch, "E1125", {"start": v(-9.44, 46.69) * mm, "end": v(-9.46, 46.49) * mm});
            skLineSegment(sketch, "E1126", {"start": v(-9.46, 46.49) * mm, "end": v(-9.43, 46.26) * mm});
            skLineSegment(sketch, "E1127", {"start": v(-9.43, 46.26) * mm, "end": v(-9.4, 46.04) * mm});
            skLineSegment(sketch, "E1128", {"start": v(-9.4, 46.04) * mm, "end": v(-9.35, 45.83) * mm});
            skLineSegment(sketch, "E1129", {"start": v(-9.35, 45.83) * mm, "end": v(-9.31, 45.62) * mm});
            skLineSegment(sketch, "E1130", {"start": v(-9.31, 45.62) * mm, "end": v(-9.28, 45.4) * mm});
            skLineSegment(sketch, "E1131", {"start": v(-9.28, 45.4) * mm, "end": v(-9.24, 45.2) * mm});
            skLineSegment(sketch, "E1132", {"start": v(-9.24, 45.2) * mm, "end": v(-9.2, 44.98) * mm});
            skLineSegment(sketch, "E1133", {"start": v(-9.2, 44.98) * mm, "end": v(-9.16, 44.77) * mm});
            skLineSegment(sketch, "E1134", {"start": v(-9.16, 44.77) * mm, "end": v(-9.12, 44.55) * mm});
            skLineSegment(sketch, "E1135", {"start": v(-9.12, 44.55) * mm, "end": v(-9.08, 44.34) * mm});
            skLineSegment(sketch, "E1136", {"start": v(-9.08, 44.34) * mm, "end": v(-9.04, 44.13) * mm});
            skLineSegment(sketch, "E1137", {"start": v(-9.04, 44.13) * mm, "end": v(-9, 43.91) * mm});
            skLineSegment(sketch, "E1138", {"start": v(-9, 43.91) * mm, "end": v(-8.96, 43.7) * mm});
            skLineSegment(sketch, "E1139", {"start": v(-8.96, 43.7) * mm, "end": v(-8.92, 43.49) * mm});
            skLineSegment(sketch, "E1140", {"start": v(-8.92, 43.49) * mm, "end": v(-8.88, 43.27) * mm});
            skLineSegment(sketch, "E1141", {"start": v(-8.88, 43.27) * mm, "end": v(-8.86, 43.17) * mm});
            skLineSegment(sketch, "E1142", {"start": v(-8.86, 43.17) * mm, "end": v(-9.08, 43.12) * mm});
            skLineSegment(sketch, "E1143", {"start": v(-9.08, 43.12) * mm, "end": v(-9.3, 43.08) * mm});
            skLineSegment(sketch, "E1144", {"start": v(-9.3, 43.08) * mm, "end": v(-9.52, 43.03) * mm});
            skLineSegment(sketch, "E1145", {"start": v(-9.52, 43.03) * mm, "end": v(-9.74, 42.98) * mm});
            skLineSegment(sketch, "E1146", {"start": v(-9.74, 42.98) * mm, "end": v(-9.95, 42.94) * mm});
            skLineSegment(sketch, "E1147", {"start": v(-9.95, 42.94) * mm, "end": v(-10.17, 42.9) * mm});
            skLineSegment(sketch, "E1148", {"start": v(-10.17, 42.9) * mm, "end": v(-10.39, 42.85) * mm});
            skLineSegment(sketch, "E1149", {"start": v(-10.39, 42.85) * mm, "end": v(-10.6, 42.8) * mm});
            skLineSegment(sketch, "E1150", {"start": v(-10.6, 42.8) * mm, "end": v(-10.83, 42.76) * mm});
            skLineSegment(sketch, "E1151", {"start": v(-10.83, 42.76) * mm, "end": v(-11, 42.72) * mm});
            skLineSegment(sketch, "E1152", {"start": v(-11, 42.72) * mm, "end": v(-11.05, 42.93) * mm});
            skLineSegment(sketch, "E1153", {"start": v(-11.05, 42.93) * mm, "end": v(-11.1, 43.14) * mm});
            skLineSegment(sketch, "E1154", {"start": v(-11.1, 43.14) * mm, "end": v(-11.15, 43.35) * mm});
            skLineSegment(sketch, "E1155", {"start": v(-11.15, 43.35) * mm, "end": v(-11.2, 43.56) * mm});
            skLineSegment(sketch, "E1156", {"start": v(-11.2, 43.56) * mm, "end": v(-11.25, 43.77) * mm});
            skLineSegment(sketch, "E1157", {"start": v(-11.25, 43.77) * mm, "end": v(-11.3, 43.98) * mm});
            skLineSegment(sketch, "E1158", {"start": v(-11.3, 43.98) * mm, "end": v(-11.35, 44.2) * mm});
            skLineSegment(sketch, "E1159", {"start": v(-11.35, 44.2) * mm, "end": v(-11.4, 44.4) * mm});
            skLineSegment(sketch, "E1160", {"start": v(-11.4, 44.4) * mm, "end": v(-11.45, 44.62) * mm});
            skLineSegment(sketch, "E1161", {"start": v(-11.45, 44.62) * mm, "end": v(-11.5, 44.83) * mm});
            skLineSegment(sketch, "E1162", {"start": v(-11.5, 44.83) * mm, "end": v(-11.55, 45.04) * mm});
            skLineSegment(sketch, "E1163", {"start": v(-11.55, 45.04) * mm, "end": v(-11.6, 45.25) * mm});
            skLineSegment(sketch, "E1164", {"start": v(-11.6, 45.25) * mm, "end": v(-11.65, 45.46) * mm});
            skLineSegment(sketch, "E1165", {"start": v(-11.65, 45.46) * mm, "end": v(-11.7, 45.67) * mm});
            skLineSegment(sketch, "E1166", {"start": v(-11.7, 45.67) * mm, "end": v(-11.75, 45.88) * mm});
            skLineSegment(sketch, "E1167", {"start": v(-11.75, 45.88) * mm, "end": v(-11.82, 46.07) * mm});
            skLineSegment(sketch, "E1168", {"start": v(-11.82, 46.07) * mm, "end": v(-11.94, 46.24) * mm});
            skLineSegment(sketch, "E1169", {"start": v(-11.94, 46.24) * mm, "end": v(-12.1, 46.36) * mm});
            skLineSegment(sketch, "E1170", {"start": v(-12.1, 46.36) * mm, "end": v(-12.29, 46.44) * mm});
            skLineSegment(sketch, "E1171", {"start": v(-12.29, 46.44) * mm, "end": v(-12.49, 46.47) * mm});
            skLineSegment(sketch, "E1172", {"start": v(-12.49, 46.47) * mm, "end": v(-12.7, 46.45) * mm});
            skLineSegment(sketch, "E1173", {"start": v(-12.7, 46.45) * mm, "end": v(-12.88, 46.37) * mm});
            skLineSegment(sketch, "E1174", {"start": v(-12.88, 46.37) * mm, "end": v(-13.04, 46.25) * mm});
            skLineSegment(sketch, "E1175", {"start": v(-13.04, 46.25) * mm, "end": v(-13.17, 46.1) * mm});
            skLineSegment(sketch, "E1176", {"start": v(-13.17, 46.1) * mm, "end": v(-13.25, 45.9) * mm});
            skLineSegment(sketch, "E1177", {"start": v(-13.25, 45.9) * mm, "end": v(-13.28, 45.7) * mm});
            skLineSegment(sketch, "E1178", {"start": v(-13.28, 45.7) * mm, "end": v(-13.25, 45.5) * mm});
            skLineSegment(sketch, "E1179", {"start": v(-13.25, 45.5) * mm, "end": v(-13.2, 45.3) * mm});
            skLineSegment(sketch, "E1180", {"start": v(-13.2, 45.3) * mm, "end": v(-13.14, 45.08) * mm});
            skLineSegment(sketch, "E1181", {"start": v(-13.14, 45.08) * mm, "end": v(-13.08, 44.87) * mm});
            skLineSegment(sketch, "E1182", {"start": v(-13.08, 44.87) * mm, "end": v(-13.03, 44.66) * mm});
            skLineSegment(sketch, "E1183", {"start": v(-13.03, 44.66) * mm, "end": v(-12.97, 44.46) * mm});
            skLineSegment(sketch, "E1184", {"start": v(-12.97, 44.46) * mm, "end": v(-12.91, 44.25) * mm});
            skLineSegment(sketch, "E1185", {"start": v(-12.91, 44.25) * mm, "end": v(-12.86, 44.04) * mm});
            skLineSegment(sketch, "E1186", {"start": v(-12.86, 44.04) * mm, "end": v(-12.8, 43.83) * mm});
            skLineSegment(sketch, "E1187", {"start": v(-12.8, 43.83) * mm, "end": v(-12.74, 43.62) * mm});
            skLineSegment(sketch, "E1188", {"start": v(-12.74, 43.62) * mm, "end": v(-12.69, 43.4) * mm});
            skLineSegment(sketch, "E1189", {"start": v(-12.69, 43.4) * mm, "end": v(-12.63, 43.2) * mm});
            skLineSegment(sketch, "E1190", {"start": v(-12.63, 43.2) * mm, "end": v(-12.57, 43) * mm});
            skLineSegment(sketch, "E1191", {"start": v(-12.57, 43) * mm, "end": v(-12.52, 42.78) * mm});
            skLineSegment(sketch, "E1192", {"start": v(-12.52, 42.78) * mm, "end": v(-12.46, 42.57) * mm});
            skLineSegment(sketch, "E1193", {"start": v(-12.46, 42.57) * mm, "end": v(-12.4, 42.36) * mm});
            skLineSegment(sketch, "E1194", {"start": v(-12.4, 42.36) * mm, "end": v(-12.62, 42.3) * mm});
            skLineSegment(sketch, "E1195", {"start": v(-12.62, 42.3) * mm, "end": v(-12.83, 42.24) * mm});
            skLineSegment(sketch, "E1196", {"start": v(-12.83, 42.24) * mm, "end": v(-13.04, 42.17) * mm});
            skLineSegment(sketch, "E1197", {"start": v(-13.04, 42.17) * mm, "end": v(-13.26, 42.1) * mm});
            skLineSegment(sketch, "E1198", {"start": v(-13.26, 42.1) * mm, "end": v(-13.47, 42.05) * mm});
            skLineSegment(sketch, "E1199", {"start": v(-13.47, 42.05) * mm, "end": v(-13.68, 41.98) * mm});
            skLineSegment(sketch, "E1200", {"start": v(-13.68, 41.98) * mm, "end": v(-13.9, 41.92) * mm});
            skLineSegment(sketch, "E1201", {"start": v(-13.9, 41.92) * mm, "end": v(-14.1, 41.86) * mm});
            skLineSegment(sketch, "E1202", {"start": v(-14.1, 41.86) * mm, "end": v(-14.32, 41.8) * mm});
            skLineSegment(sketch, "E1203", {"start": v(-14.32, 41.8) * mm, "end": v(-14.5, 41.74) * mm});
            skLineSegment(sketch, "E1204", {"start": v(-14.5, 41.74) * mm, "end": v(-14.56, 41.95) * mm});
            skLineSegment(sketch, "E1205", {"start": v(-14.56, 41.95) * mm, "end": v(-14.63, 42.15) * mm});
            skLineSegment(sketch, "E1206", {"start": v(-14.63, 42.15) * mm, "end": v(-14.7, 42.36) * mm});
            skLineSegment(sketch, "E1207", {"start": v(-14.7, 42.36) * mm, "end": v(-14.76, 42.56) * mm});
            skLineSegment(sketch, "E1208", {"start": v(-14.76, 42.56) * mm, "end": v(-14.83, 42.77) * mm});
            skLineSegment(sketch, "E1209", {"start": v(-14.83, 42.77) * mm, "end": v(-14.9, 42.98) * mm});
            skLineSegment(sketch, "E1210", {"start": v(-14.9, 42.98) * mm, "end": v(-14.96, 43.18) * mm});
            skLineSegment(sketch, "E1211", {"start": v(-14.96, 43.18) * mm, "end": v(-15.03, 43.39) * mm});
            skLineSegment(sketch, "E1212", {"start": v(-15.03, 43.39) * mm, "end": v(-15.1, 43.6) * mm});
            skLineSegment(sketch, "E1213", {"start": v(-15.1, 43.6) * mm, "end": v(-15.16, 43.8) * mm});
            skLineSegment(sketch, "E1214", {"start": v(-15.16, 43.8) * mm, "end": v(-15.23, 44) * mm});
            skLineSegment(sketch, "E1215", {"start": v(-15.23, 44) * mm, "end": v(-15.3, 44.21) * mm});
            skLineSegment(sketch, "E1216", {"start": v(-15.3, 44.21) * mm, "end": v(-15.37, 44.42) * mm});
            skLineSegment(sketch, "E1217", {"start": v(-15.37, 44.42) * mm, "end": v(-15.43, 44.63) * mm});
            skLineSegment(sketch, "E1218", {"start": v(-15.43, 44.63) * mm, "end": v(-15.5, 44.83) * mm});
            skLineSegment(sketch, "E1219", {"start": v(-15.5, 44.83) * mm, "end": v(-15.59, 45.01) * mm});
            skLineSegment(sketch, "E1220", {"start": v(-15.59, 45.01) * mm, "end": v(-15.72, 45.17) * mm});
            skLineSegment(sketch, "E1221", {"start": v(-15.72, 45.17) * mm, "end": v(-15.9, 45.28) * mm});
            skLineSegment(sketch, "E1222", {"start": v(-15.9, 45.28) * mm, "end": v(-16.08, 45.35) * mm});
            skLineSegment(sketch, "E1223", {"start": v(-16.08, 45.35) * mm, "end": v(-16.25, 45.36) * mm});
            skLineSegment(sketch, "E1224", {"start": v(-16.25, 45.36) * mm, "end": v(-16.45, 45.33) * mm});
            skLineSegment(sketch, "E1225", {"start": v(-16.45, 45.33) * mm, "end": v(-16.63, 45.25) * mm});
            skLineSegment(sketch, "E1226", {"start": v(-16.63, 45.25) * mm, "end": v(-16.8, 45.12) * mm});
            skLineSegment(sketch, "E1227", {"start": v(-16.8, 45.12) * mm, "end": v(-16.91, 44.96) * mm});
            skLineSegment(sketch, "E1228", {"start": v(-16.91, 44.96) * mm, "end": v(-16.99, 44.77) * mm});
            skLineSegment(sketch, "E1229", {"start": v(-16.99, 44.77) * mm, "end": v(-17.01, 44.57) * mm});
            skLineSegment(sketch, "E1230", {"start": v(-17.01, 44.57) * mm, "end": v(-16.98, 44.37) * mm});
            skLineSegment(sketch, "E1231", {"start": v(-16.98, 44.37) * mm, "end": v(-16.9, 44.16) * mm});
            skLineSegment(sketch, "E1232", {"start": v(-16.9, 44.16) * mm, "end": v(-16.83, 43.95) * mm});
            skLineSegment(sketch, "E1233", {"start": v(-16.83, 43.95) * mm, "end": v(-16.75, 43.74) * mm});
            skLineSegment(sketch, "E1234", {"start": v(-16.75, 43.74) * mm, "end": v(-16.67, 43.51) * mm});
            skLineSegment(sketch, "E1235", {"start": v(-16.67, 43.51) * mm, "end": v(-16.6, 43.3) * mm});
            skLineSegment(sketch, "E1236", {"start": v(-16.6, 43.3) * mm, "end": v(-16.52, 43.1) * mm});
            skLineSegment(sketch, "E1237", {"start": v(-16.52, 43.1) * mm, "end": v(-16.45, 42.9) * mm});
            skLineSegment(sketch, "E1238", {"start": v(-16.45, 42.9) * mm, "end": v(-16.38, 42.7) * mm});
            skLineSegment(sketch, "E1239", {"start": v(-16.38, 42.7) * mm, "end": v(-16.3, 42.5) * mm});
            skLineSegment(sketch, "E1240", {"start": v(-16.3, 42.5) * mm, "end": v(-16.23, 42.3) * mm});
            skLineSegment(sketch, "E1241", {"start": v(-16.23, 42.3) * mm, "end": v(-16.16, 42.09) * mm});
            skLineSegment(sketch, "E1242", {"start": v(-16.16, 42.09) * mm, "end": v(-16.08, 41.88) * mm});
            skLineSegment(sketch, "E1243", {"start": v(-16.08, 41.88) * mm, "end": v(-16, 41.68) * mm});
            skLineSegment(sketch, "E1244", {"start": v(-16, 41.68) * mm, "end": v(-15.93, 41.48) * mm});
            skLineSegment(sketch, "E1245", {"start": v(-15.93, 41.48) * mm, "end": v(-15.86, 41.27) * mm});
            skLineSegment(sketch, "E1246", {"start": v(-15.86, 41.27) * mm, "end": v(-16.07, 41.2) * mm});
            skLineSegment(sketch, "E1247", {"start": v(-16.07, 41.2) * mm, "end": v(-16.28, 41.1) * mm});
            skLineSegment(sketch, "E1248", {"start": v(-16.28, 41.1) * mm, "end": v(-16.48, 41.03) * mm});
            skLineSegment(sketch, "E1249", {"start": v(-16.48, 41.03) * mm, "end": v(-16.7, 40.95) * mm});
            skLineSegment(sketch, "E1250", {"start": v(-16.7, 40.95) * mm, "end": v(-16.9, 40.87) * mm});
            skLineSegment(sketch, "E1251", {"start": v(-16.9, 40.87) * mm, "end": v(-17.1, 40.79) * mm});
            skLineSegment(sketch, "E1252", {"start": v(-17.1, 40.79) * mm, "end": v(-17.31, 40.7) * mm});
            skLineSegment(sketch, "E1253", {"start": v(-17.31, 40.7) * mm, "end": v(-17.52, 40.62) * mm});
            skLineSegment(sketch, "E1254", {"start": v(-17.52, 40.62) * mm, "end": v(-17.73, 40.54) * mm});
            skLineSegment(sketch, "E1255", {"start": v(-17.73, 40.54) * mm, "end": v(-17.9, 40.48) * mm});
            skLineSegment(sketch, "E1256", {"start": v(-17.9, 40.48) * mm, "end": v(-17.98, 40.68) * mm});
            skLineSegment(sketch, "E1257", {"start": v(-17.98, 40.68) * mm, "end": v(-18.06, 40.88) * mm});
            skLineSegment(sketch, "E1258", {"start": v(-18.06, 40.88) * mm, "end": v(-18.15, 41.08) * mm});
            skLineSegment(sketch, "E1259", {"start": v(-18.15, 41.08) * mm, "end": v(-18.23, 41.28) * mm});
            skLineSegment(sketch, "E1260", {"start": v(-18.23, 41.28) * mm, "end": v(-18.31, 41.48) * mm});
            skLineSegment(sketch, "E1261", {"start": v(-18.31, 41.48) * mm, "end": v(-18.4, 41.68) * mm});
            skLineSegment(sketch, "E1262", {"start": v(-18.4, 41.68) * mm, "end": v(-18.48, 41.88) * mm});
            skLineSegment(sketch, "E1263", {"start": v(-18.48, 41.88) * mm, "end": v(-18.57, 42.08) * mm});
            skLineSegment(sketch, "E1264", {"start": v(-18.57, 42.08) * mm, "end": v(-18.65, 42.28) * mm});
            skLineSegment(sketch, "E1265", {"start": v(-18.65, 42.28) * mm, "end": v(-18.73, 42.48) * mm});
            skLineSegment(sketch, "E1266", {"start": v(-18.73, 42.48) * mm, "end": v(-18.82, 42.68) * mm});
            skLineSegment(sketch, "E1267", {"start": v(-18.82, 42.68) * mm, "end": v(-18.9, 42.88) * mm});
            skLineSegment(sketch, "E1268", {"start": v(-18.9, 42.88) * mm, "end": v(-18.98, 43.08) * mm});
            skLineSegment(sketch, "E1269", {"start": v(-18.98, 43.08) * mm, "end": v(-19.07, 43.28) * mm});
            skLineSegment(sketch, "E1270", {"start": v(-19.07, 43.28) * mm, "end": v(-19.15, 43.48) * mm});
            skLineSegment(sketch, "E1271", {"start": v(-19.15, 43.48) * mm, "end": v(-19.26, 43.65) * mm});
            skLineSegment(sketch, "E1272", {"start": v(-19.26, 43.65) * mm, "end": v(-19.4, 43.8) * mm});
            skLineSegment(sketch, "E1273", {"start": v(-19.4, 43.8) * mm, "end": v(-19.58, 43.9) * mm});
            skLineSegment(sketch, "E1274", {"start": v(-19.58, 43.9) * mm, "end": v(-19.78, 43.94) * mm});
            skLineSegment(sketch, "E1275", {"start": v(-19.78, 43.94) * mm, "end": v(-19.86, 43.95) * mm});
            skLineSegment(sketch, "E1276", {"start": v(-19.86, 43.95) * mm, "end": v(-20.06, 43.92) * mm});
            skLineSegment(sketch, "E1277", {"start": v(-20.06, 43.92) * mm, "end": v(-20.25, 43.84) * mm});
            skLineSegment(sketch, "E1278", {"start": v(-20.25, 43.84) * mm, "end": v(-20.41, 43.72) * mm});
            skLineSegment(sketch, "E1279", {"start": v(-20.41, 43.72) * mm, "end": v(-20.54, 43.56) * mm});
            skLineSegment(sketch, "E1280", {"start": v(-20.54, 43.56) * mm, "end": v(-20.61, 43.37) * mm});
            skLineSegment(sketch, "E1281", {"start": v(-20.61, 43.37) * mm, "end": v(-20.64, 43.17) * mm});
            skLineSegment(sketch, "E1282", {"start": v(-20.64, 43.17) * mm, "end": v(-20.61, 42.97) * mm});
            skLineSegment(sketch, "E1283", {"start": v(-20.61, 42.97) * mm, "end": v(-20.53, 42.75) * mm});
            skLineSegment(sketch, "E1284", {"start": v(-20.53, 42.75) * mm, "end": v(-20.44, 42.56) * mm});
            skLineSegment(sketch, "E1285", {"start": v(-20.44, 42.56) * mm, "end": v(-20.35, 42.36) * mm});
            skLineSegment(sketch, "E1286", {"start": v(-20.35, 42.36) * mm, "end": v(-20.26, 42.16) * mm});
            skLineSegment(sketch, "E1287", {"start": v(-20.26, 42.16) * mm, "end": v(-20.17, 41.97) * mm});
            skLineSegment(sketch, "E1288", {"start": v(-20.17, 41.97) * mm, "end": v(-20.08, 41.77) * mm});
            skLineSegment(sketch, "E1289", {"start": v(-20.08, 41.77) * mm, "end": v(-19.99, 41.57) * mm});
            skLineSegment(sketch, "E1290", {"start": v(-19.99, 41.57) * mm, "end": v(-19.9, 41.38) * mm});
            skLineSegment(sketch, "E1291", {"start": v(-19.9, 41.38) * mm, "end": v(-19.8, 41.18) * mm});
            skLineSegment(sketch, "E1292", {"start": v(-19.8, 41.18) * mm, "end": v(-19.71, 40.98) * mm});
            skLineSegment(sketch, "E1293", {"start": v(-19.71, 40.98) * mm, "end": v(-19.62, 40.78) * mm});
            skLineSegment(sketch, "E1294", {"start": v(-19.62, 40.78) * mm, "end": v(-19.53, 40.59) * mm});
            skLineSegment(sketch, "E1295", {"start": v(-19.53, 40.59) * mm, "end": v(-19.44, 40.4) * mm});
            skLineSegment(sketch, "E1296", {"start": v(-19.44, 40.4) * mm, "end": v(-19.35, 40.2) * mm});
            skLineSegment(sketch, "E1297", {"start": v(-19.35, 40.2) * mm, "end": v(-19.26, 40) * mm});
            skLineSegment(sketch, "E1298", {"start": v(-19.26, 40) * mm, "end": v(-19.22, 39.9) * mm});
            skLineSegment(sketch, "E1299", {"start": v(-19.22, 39.9) * mm, "end": v(-19.42, 39.8) * mm});
            skLineSegment(sketch, "E1300", {"start": v(-19.42, 39.8) * mm, "end": v(-19.62, 39.7) * mm});
            skLineSegment(sketch, "E1301", {"start": v(-19.62, 39.7) * mm, "end": v(-19.82, 39.6) * mm});
            skLineSegment(sketch, "E1302", {"start": v(-19.82, 39.6) * mm, "end": v(-20.02, 39.5) * mm});
            skLineSegment(sketch, "E1303", {"start": v(-20.02, 39.5) * mm, "end": v(-20.22, 39.4) * mm});
            skLineSegment(sketch, "E1304", {"start": v(-20.22, 39.4) * mm, "end": v(-20.42, 39.31) * mm});
            skLineSegment(sketch, "E1305", {"start": v(-20.42, 39.31) * mm, "end": v(-20.62, 39.21) * mm});
            skLineSegment(sketch, "E1306", {"start": v(-20.62, 39.21) * mm, "end": v(-20.82, 39.12) * mm});
            skLineSegment(sketch, "E1307", {"start": v(-20.82, 39.12) * mm, "end": v(-21.02, 39.02) * mm});
            skLineSegment(sketch, "E1308", {"start": v(-21.02, 39.02) * mm, "end": v(-21.18, 38.94) * mm});
            skLineSegment(sketch, "E1309", {"start": v(-21.18, 38.94) * mm, "end": v(-21.28, 39.13) * mm});
            skLineSegment(sketch, "E1310", {"start": v(-21.28, 39.13) * mm, "end": v(-21.38, 39.32) * mm});
            skLineSegment(sketch, "E1311", {"start": v(-21.38, 39.32) * mm, "end": v(-21.48, 39.52) * mm});
            skLineSegment(sketch, "E1312", {"start": v(-21.48, 39.52) * mm, "end": v(-21.58, 39.7) * mm});
            skLineSegment(sketch, "E1313", {"start": v(-21.58, 39.7) * mm, "end": v(-21.68, 39.9) * mm});
            skLineSegment(sketch, "E1314", {"start": v(-21.68, 39.9) * mm, "end": v(-21.78, 40.1) * mm});
            skLineSegment(sketch, "E1315", {"start": v(-21.78, 40.1) * mm, "end": v(-21.88, 40.28) * mm});
            skLineSegment(sketch, "E1316", {"start": v(-21.88, 40.28) * mm, "end": v(-21.98, 40.48) * mm});
            skLineSegment(sketch, "E1317", {"start": v(-21.98, 40.48) * mm, "end": v(-22.08, 40.67) * mm});
            skLineSegment(sketch, "E1318", {"start": v(-22.08, 40.67) * mm, "end": v(-22.18, 40.86) * mm});
            skLineSegment(sketch, "E1319", {"start": v(-22.18, 40.86) * mm, "end": v(-22.28, 41.05) * mm});
            skLineSegment(sketch, "E1320", {"start": v(-22.28, 41.05) * mm, "end": v(-22.38, 41.25) * mm});
            skLineSegment(sketch, "E1321", {"start": v(-22.38, 41.25) * mm, "end": v(-22.48, 41.44) * mm});
            skLineSegment(sketch, "E1322", {"start": v(-22.48, 41.44) * mm, "end": v(-22.58, 41.63) * mm});
            skLineSegment(sketch, "E1323", {"start": v(-22.58, 41.63) * mm, "end": v(-22.68, 41.82) * mm});
            skLineSegment(sketch, "E1324", {"start": v(-22.68, 41.82) * mm, "end": v(-22.8, 41.99) * mm});
            skLineSegment(sketch, "E1325", {"start": v(-22.8, 41.99) * mm, "end": v(-22.96, 42.12) * mm});
            skLineSegment(sketch, "E1326", {"start": v(-22.96, 42.12) * mm, "end": v(-23.14, 42.2) * mm});
            skLineSegment(sketch, "E1327", {"start": v(-23.14, 42.2) * mm, "end": v(-23.34, 42.23) * mm});
            skLineSegment(sketch, "E1328", {"start": v(-23.34, 42.23) * mm, "end": v(-23.38, 42.23) * mm});
            skLineSegment(sketch, "E1329", {"start": v(-23.38, 42.23) * mm, "end": v(-23.58, 42.2) * mm});
            skLineSegment(sketch, "E1330", {"start": v(-23.58, 42.2) * mm, "end": v(-23.77, 42.12) * mm});
            skLineSegment(sketch, "E1331", {"start": v(-23.77, 42.12) * mm, "end": v(-23.93, 42) * mm});
            skLineSegment(sketch, "E1332", {"start": v(-23.93, 42) * mm, "end": v(-24.05, 41.83) * mm});
            skLineSegment(sketch, "E1333", {"start": v(-24.05, 41.83) * mm, "end": v(-24.12, 41.64) * mm});
            skLineSegment(sketch, "E1334", {"start": v(-24.12, 41.64) * mm, "end": v(-24.14, 41.44) * mm});
            skLineSegment(sketch, "E1335", {"start": v(-24.14, 41.44) * mm, "end": v(-24.1, 41.23) * mm});
            skLineSegment(sketch, "E1336", {"start": v(-24.1, 41.23) * mm, "end": v(-24.01, 41.03) * mm});
            skLineSegment(sketch, "E1337", {"start": v(-24.01, 41.03) * mm, "end": v(-23.9, 40.84) * mm});
            skLineSegment(sketch, "E1338", {"start": v(-23.9, 40.84) * mm, "end": v(-23.8, 40.64) * mm});
            skLineSegment(sketch, "E1339", {"start": v(-23.8, 40.64) * mm, "end": v(-23.69, 40.45) * mm});
            skLineSegment(sketch, "E1340", {"start": v(-23.69, 40.45) * mm, "end": v(-23.58, 40.26) * mm});
            skLineSegment(sketch, "E1341", {"start": v(-23.58, 40.26) * mm, "end": v(-23.46, 40.05) * mm});
            skLineSegment(sketch, "E1342", {"start": v(-23.46, 40.05) * mm, "end": v(-23.35, 39.86) * mm});
            skLineSegment(sketch, "E1343", {"start": v(-23.35, 39.86) * mm, "end": v(-23.25, 39.67) * mm});
            skLineSegment(sketch, "E1344", {"start": v(-23.25, 39.67) * mm, "end": v(-23.14, 39.48) * mm});
            skLineSegment(sketch, "E1345", {"start": v(-23.14, 39.48) * mm, "end": v(-23.03, 39.29) * mm});
            skLineSegment(sketch, "E1346", {"start": v(-23.03, 39.29) * mm, "end": v(-22.93, 39.1) * mm});
            skLineSegment(sketch, "E1347", {"start": v(-22.93, 39.1) * mm, "end": v(-22.82, 38.91) * mm});
            skLineSegment(sketch, "E1348", {"start": v(-22.82, 38.91) * mm, "end": v(-22.72, 38.72) * mm});
            skLineSegment(sketch, "E1349", {"start": v(-22.72, 38.72) * mm, "end": v(-22.6, 38.53) * mm});
            skLineSegment(sketch, "E1350", {"start": v(-22.6, 38.53) * mm, "end": v(-22.5, 38.35) * mm});
            skLineSegment(sketch, "E1351", {"start": v(-22.5, 38.35) * mm, "end": v(-22.45, 38.25) * mm});
            skLineSegment(sketch, "E1352", {"start": v(-22.45, 38.25) * mm, "end": v(-22.64, 38.14) * mm});
            skLineSegment(sketch, "E1353", {"start": v(-22.64, 38.14) * mm, "end": v(-22.83, 38.02) * mm});
            skLineSegment(sketch, "E1354", {"start": v(-22.83, 38.02) * mm, "end": v(-23.02, 37.9) * mm});
            skLineSegment(sketch, "E1355", {"start": v(-23.02, 37.9) * mm, "end": v(-23.22, 37.8) * mm});
            skLineSegment(sketch, "E1356", {"start": v(-23.22, 37.8) * mm, "end": v(-23.4, 37.68) * mm});
            skLineSegment(sketch, "E1357", {"start": v(-23.4, 37.68) * mm, "end": v(-23.6, 37.57) * mm});
            skLineSegment(sketch, "E1358", {"start": v(-23.6, 37.57) * mm, "end": v(-23.79, 37.45) * mm});
            skLineSegment(sketch, "E1359", {"start": v(-23.79, 37.45) * mm, "end": v(-23.98, 37.34) * mm});
            skLineSegment(sketch, "E1360", {"start": v(-23.98, 37.34) * mm, "end": v(-24.17, 37.23) * mm});
            skLineSegment(sketch, "E1361", {"start": v(-24.17, 37.23) * mm, "end": v(-24.33, 37.13) * mm});
            skLineSegment(sketch, "E1362", {"start": v(-24.33, 37.13) * mm, "end": v(-24.44, 37.32) * mm});
            skLineSegment(sketch, "E1363", {"start": v(-24.44, 37.32) * mm, "end": v(-24.56, 37.5) * mm});
            skLineSegment(sketch, "E1364", {"start": v(-24.56, 37.5) * mm, "end": v(-24.67, 37.68) * mm});
            skLineSegment(sketch, "E1365", {"start": v(-24.67, 37.68) * mm, "end": v(-24.79, 37.87) * mm});
            skLineSegment(sketch, "E1366", {"start": v(-24.79, 37.87) * mm, "end": v(-24.9, 38.05) * mm});
            skLineSegment(sketch, "E1367", {"start": v(-24.9, 38.05) * mm, "end": v(-25.02, 38.23) * mm});
            skLineSegment(sketch, "E1368", {"start": v(-25.02, 38.23) * mm, "end": v(-25.14, 38.42) * mm});
            skLineSegment(sketch, "E1369", {"start": v(-25.14, 38.42) * mm, "end": v(-25.25, 38.6) * mm});
            skLineSegment(sketch, "E1370", {"start": v(-25.25, 38.6) * mm, "end": v(-25.37, 38.78) * mm});
            skLineSegment(sketch, "E1371", {"start": v(-25.37, 38.78) * mm, "end": v(-25.48, 38.97) * mm});
            skLineSegment(sketch, "E1372", {"start": v(-25.48, 38.97) * mm, "end": v(-25.6, 39.15) * mm});
            skLineSegment(sketch, "E1373", {"start": v(-25.6, 39.15) * mm, "end": v(-25.71, 39.33) * mm});
            skLineSegment(sketch, "E1374", {"start": v(-25.71, 39.33) * mm, "end": v(-25.83, 39.52) * mm});
            skLineSegment(sketch, "E1375", {"start": v(-25.83, 39.52) * mm, "end": v(-25.94, 39.7) * mm});
            skLineSegment(sketch, "E1376", {"start": v(-25.94, 39.7) * mm, "end": v(-26.06, 39.88) * mm});
            skLineSegment(sketch, "E1377", {"start": v(-26.06, 39.88) * mm, "end": v(-26.2, 40.04) * mm});
            skLineSegment(sketch, "E1378", {"start": v(-26.2, 40.04) * mm, "end": v(-26.36, 40.15) * mm});
            skLineSegment(sketch, "E1379", {"start": v(-26.36, 40.15) * mm, "end": v(-26.55, 40.22) * mm});
            skLineSegment(sketch, "E1380", {"start": v(-26.55, 40.22) * mm, "end": v(-26.71, 40.24) * mm});
            skLineSegment(sketch, "E1381", {"start": v(-26.71, 40.24) * mm, "end": v(-26.91, 40.21) * mm});
            skLineSegment(sketch, "E1382", {"start": v(-26.91, 40.21) * mm, "end": v(-27.1, 40.13) * mm});
            skLineSegment(sketch, "E1383", {"start": v(-27.1, 40.13) * mm, "end": v(-27.26, 40.01) * mm});
            skLineSegment(sketch, "E1384", {"start": v(-27.26, 40.01) * mm, "end": v(-27.39, 39.85) * mm});
            skLineSegment(sketch, "E1385", {"start": v(-27.39, 39.85) * mm, "end": v(-27.46, 39.66) * mm});
            skLineSegment(sketch, "E1386", {"start": v(-27.46, 39.66) * mm, "end": v(-27.49, 39.46) * mm});
            skLineSegment(sketch, "E1387", {"start": v(-27.49, 39.46) * mm, "end": v(-27.46, 39.26) * mm});
            skLineSegment(sketch, "E1388", {"start": v(-27.46, 39.26) * mm, "end": v(-27.38, 39.07) * mm});
            skLineSegment(sketch, "E1389", {"start": v(-27.38, 39.07) * mm, "end": v(-27.26, 38.88) * mm});
            skLineSegment(sketch, "E1390", {"start": v(-27.26, 38.88) * mm, "end": v(-27.13, 38.7) * mm});
            skLineSegment(sketch, "E1391", {"start": v(-27.13, 38.7) * mm, "end": v(-27, 38.52) * mm});
            skLineSegment(sketch, "E1392", {"start": v(-27, 38.52) * mm, "end": v(-26.87, 38.32) * mm});
            skLineSegment(sketch, "E1393", {"start": v(-26.87, 38.32) * mm, "end": v(-26.75, 38.14) * mm});
            skLineSegment(sketch, "E1394", {"start": v(-26.75, 38.14) * mm, "end": v(-26.63, 37.96) * mm});
            skLineSegment(sketch, "E1395", {"start": v(-26.63, 37.96) * mm, "end": v(-26.5, 37.78) * mm});
            skLineSegment(sketch, "E1396", {"start": v(-26.5, 37.78) * mm, "end": v(-26.39, 37.6) * mm});
            skLineSegment(sketch, "E1397", {"start": v(-26.39, 37.6) * mm, "end": v(-26.26, 37.42) * mm});
            skLineSegment(sketch, "E1398", {"start": v(-26.26, 37.42) * mm, "end": v(-26.14, 37.24) * mm});
            skLineSegment(sketch, "E1399", {"start": v(-26.14, 37.24) * mm, "end": v(-26.02, 37.06) * mm});
            skLineSegment(sketch, "E1400", {"start": v(-26.02, 37.06) * mm, "end": v(-25.9, 36.88) * mm});
            skLineSegment(sketch, "E1401", {"start": v(-25.9, 36.88) * mm, "end": v(-25.78, 36.7) * mm});
            skLineSegment(sketch, "E1402", {"start": v(-25.78, 36.7) * mm, "end": v(-25.66, 36.52) * mm});
            skLineSegment(sketch, "E1403", {"start": v(-25.66, 36.52) * mm, "end": v(-25.54, 36.34) * mm});
            skLineSegment(sketch, "E1404", {"start": v(-25.54, 36.34) * mm, "end": v(-25.72, 36.21) * mm});
            skLineSegment(sketch, "E1405", {"start": v(-25.72, 36.21) * mm, "end": v(-25.9, 36.08) * mm});
            skLineSegment(sketch, "E1406", {"start": v(-25.9, 36.08) * mm, "end": v(-26.08, 35.95) * mm});
            skLineSegment(sketch, "E1407", {"start": v(-26.08, 35.95) * mm, "end": v(-26.26, 35.83) * mm});
            skLineSegment(sketch, "E1408", {"start": v(-26.26, 35.83) * mm, "end": v(-26.44, 35.7) * mm});
            skLineSegment(sketch, "E1409", {"start": v(-26.44, 35.7) * mm, "end": v(-26.62, 35.57) * mm});
            skLineSegment(sketch, "E1410", {"start": v(-26.62, 35.57) * mm, "end": v(-26.8, 35.44) * mm});
            skLineSegment(sketch, "E1411", {"start": v(-26.8, 35.44) * mm, "end": v(-26.99, 35.3) * mm});
            skLineSegment(sketch, "E1412", {"start": v(-26.99, 35.3) * mm, "end": v(-27.17, 35.18) * mm});
            skLineSegment(sketch, "E1413", {"start": v(-27.17, 35.18) * mm, "end": v(-27.31, 35.07) * mm});
            skLineSegment(sketch, "E1414", {"start": v(-27.31, 35.07) * mm, "end": v(-27.44, 35.25) * mm});
            skLineSegment(sketch, "E1415", {"start": v(-27.44, 35.25) * mm, "end": v(-27.57, 35.42) * mm});
            skLineSegment(sketch, "E1416", {"start": v(-27.57, 35.42) * mm, "end": v(-27.7, 35.6) * mm});
            skLineSegment(sketch, "E1417", {"start": v(-27.7, 35.6) * mm, "end": v(-27.83, 35.77) * mm});
            skLineSegment(sketch, "E1418", {"start": v(-27.83, 35.77) * mm, "end": v(-27.96, 35.94) * mm});
            skLineSegment(sketch, "E1419", {"start": v(-27.96, 35.94) * mm, "end": v(-28.1, 36.11) * mm});
            skLineSegment(sketch, "E1420", {"start": v(-28.1, 36.11) * mm, "end": v(-28.22, 36.29) * mm});
            skLineSegment(sketch, "E1421", {"start": v(-28.22, 36.29) * mm, "end": v(-28.36, 36.46) * mm});
            skLineSegment(sketch, "E1422", {"start": v(-28.36, 36.46) * mm, "end": v(-28.49, 36.63) * mm});
            skLineSegment(sketch, "E1423", {"start": v(-28.49, 36.63) * mm, "end": v(-28.62, 36.8) * mm});
            skLineSegment(sketch, "E1424", {"start": v(-28.62, 36.8) * mm, "end": v(-28.75, 36.98) * mm});
            skLineSegment(sketch, "E1425", {"start": v(-28.75, 36.98) * mm, "end": v(-28.88, 37.15) * mm});
            skLineSegment(sketch, "E1426", {"start": v(-28.88, 37.15) * mm, "end": v(-29, 37.33) * mm});
            skLineSegment(sketch, "E1427", {"start": v(-29, 37.33) * mm, "end": v(-29.14, 37.5) * mm});
            skLineSegment(sketch, "E1428", {"start": v(-29.14, 37.5) * mm, "end": v(-29.27, 37.67) * mm});
            skLineSegment(sketch, "E1429", {"start": v(-29.27, 37.67) * mm, "end": v(-29.41, 37.82) * mm});
            skLineSegment(sketch, "E1430", {"start": v(-29.41, 37.82) * mm, "end": v(-29.59, 37.92) * mm});
            skLineSegment(sketch, "E1431", {"start": v(-29.59, 37.92) * mm, "end": v(-29.78, 37.97) * mm});
            skLineSegment(sketch, "E1432", {"start": v(-29.78, 37.97) * mm, "end": v(-29.87, 37.98) * mm});
            skLineSegment(sketch, "E1433", {"start": v(-29.87, 37.98) * mm, "end": v(-30.07, 37.95) * mm});
            skLineSegment(sketch, "E1434", {"start": v(-30.07, 37.95) * mm, "end": v(-30.26, 37.88) * mm});
            skLineSegment(sketch, "E1435", {"start": v(-30.26, 37.88) * mm, "end": v(-30.42, 37.76) * mm});
            skLineSegment(sketch, "E1436", {"start": v(-30.42, 37.76) * mm, "end": v(-30.55, 37.6) * mm});
            skLineSegment(sketch, "E1437", {"start": v(-30.55, 37.6) * mm, "end": v(-30.63, 37.41) * mm});
            skLineSegment(sketch, "E1438", {"start": v(-30.63, 37.41) * mm, "end": v(-30.66, 37.21) * mm});
            skLineSegment(sketch, "E1439", {"start": v(-30.66, 37.21) * mm, "end": v(-30.64, 37) * mm});
            skLineSegment(sketch, "E1440", {"start": v(-30.64, 37) * mm, "end": v(-30.56, 36.82) * mm});
            skLineSegment(sketch, "E1441", {"start": v(-30.56, 36.82) * mm, "end": v(-30.42, 36.63) * mm});
            skLineSegment(sketch, "E1442", {"start": v(-30.42, 36.63) * mm, "end": v(-30.29, 36.47) * mm});
            skLineSegment(sketch, "E1443", {"start": v(-30.29, 36.47) * mm, "end": v(-30.15, 36.3) * mm});
            skLineSegment(sketch, "E1444", {"start": v(-30.15, 36.3) * mm, "end": v(-30.02, 36.13) * mm});
            skLineSegment(sketch, "E1445", {"start": v(-30.02, 36.13) * mm, "end": v(-29.88, 35.96) * mm});
            skLineSegment(sketch, "E1446", {"start": v(-29.88, 35.96) * mm, "end": v(-29.74, 35.8) * mm});
            skLineSegment(sketch, "E1447", {"start": v(-29.74, 35.8) * mm, "end": v(-29.6, 35.62) * mm});
            skLineSegment(sketch, "E1448", {"start": v(-29.6, 35.62) * mm, "end": v(-29.47, 35.45) * mm});
            skLineSegment(sketch, "E1449", {"start": v(-29.47, 35.45) * mm, "end": v(-29.34, 35.28) * mm});
            skLineSegment(sketch, "E1450", {"start": v(-29.34, 35.28) * mm, "end": v(-29.2, 35.12) * mm});
            skLineSegment(sketch, "E1451", {"start": v(-29.2, 35.12) * mm, "end": v(-29.06, 34.95) * mm});
            skLineSegment(sketch, "E1452", {"start": v(-29.06, 34.95) * mm, "end": v(-28.93, 34.78) * mm});
            skLineSegment(sketch, "E1453", {"start": v(-28.93, 34.78) * mm, "end": v(-28.8, 34.6) * mm});
            skLineSegment(sketch, "E1454", {"start": v(-28.8, 34.6) * mm, "end": v(-28.66, 34.44) * mm});
            skLineSegment(sketch, "E1455", {"start": v(-28.66, 34.44) * mm, "end": v(-28.52, 34.27) * mm});
            skLineSegment(sketch, "E1456", {"start": v(-28.52, 34.27) * mm, "end": v(-28.45, 34.19) * mm});
            skLineSegment(sketch, "E1457", {"start": v(-28.45, 34.19) * mm, "end": v(-28.62, 34.04) * mm});
            skLineSegment(sketch, "E1458", {"start": v(-28.62, 34.04) * mm, "end": v(-28.8, 33.9) * mm});
            skLineSegment(sketch, "E1459", {"start": v(-28.8, 33.9) * mm, "end": v(-28.96, 33.76) * mm});
            skLineSegment(sketch, "E1460", {"start": v(-28.96, 33.76) * mm, "end": v(-29.13, 33.61) * mm});
            skLineSegment(sketch, "E1461", {"start": v(-29.13, 33.61) * mm, "end": v(-29.3, 33.47) * mm});
            skLineSegment(sketch, "E1462", {"start": v(-29.3, 33.47) * mm, "end": v(-29.47, 33.32) * mm});
            skLineSegment(sketch, "E1463", {"start": v(-29.47, 33.32) * mm, "end": v(-29.64, 33.18) * mm});
            skLineSegment(sketch, "E1464", {"start": v(-29.64, 33.18) * mm, "end": v(-29.81, 33.04) * mm});
            skLineSegment(sketch, "E1465", {"start": v(-29.81, 33.04) * mm, "end": v(-29.98, 32.9) * mm});
            skLineSegment(sketch, "E1466", {"start": v(-29.98, 32.9) * mm, "end": v(-30.12, 32.78) * mm});
            skLineSegment(sketch, "E1467", {"start": v(-30.12, 32.78) * mm, "end": v(-30.26, 32.94) * mm});
            skLineSegment(sketch, "E1468", {"start": v(-30.26, 32.94) * mm, "end": v(-30.4, 33.1) * mm});
            skLineSegment(sketch, "E1469", {"start": v(-30.4, 33.1) * mm, "end": v(-30.55, 33.26) * mm});
            skLineSegment(sketch, "E1470", {"start": v(-30.55, 33.26) * mm, "end": v(-30.7, 33.42) * mm});
            skLineSegment(sketch, "E1471", {"start": v(-30.7, 33.42) * mm, "end": v(-30.84, 33.58) * mm});
            skLineSegment(sketch, "E1472", {"start": v(-30.84, 33.58) * mm, "end": v(-30.98, 33.75) * mm});
            skLineSegment(sketch, "E1473", {"start": v(-30.98, 33.75) * mm, "end": v(-31.13, 33.9) * mm});
            skLineSegment(sketch, "E1474", {"start": v(-31.13, 33.9) * mm, "end": v(-31.27, 34.07) * mm});
            skLineSegment(sketch, "E1475", {"start": v(-31.27, 34.07) * mm, "end": v(-31.42, 34.23) * mm});
            skLineSegment(sketch, "E1476", {"start": v(-31.42, 34.23) * mm, "end": v(-31.56, 34.4) * mm});
            skLineSegment(sketch, "E1477", {"start": v(-31.56, 34.4) * mm, "end": v(-31.7, 34.56) * mm});
            skLineSegment(sketch, "E1478", {"start": v(-31.7, 34.56) * mm, "end": v(-31.85, 34.72) * mm});
            skLineSegment(sketch, "E1479", {"start": v(-31.85, 34.72) * mm, "end": v(-32, 34.88) * mm});
            skLineSegment(sketch, "E1480", {"start": v(-32, 34.88) * mm, "end": v(-32.14, 35.04) * mm});
            skLineSegment(sketch, "E1481", {"start": v(-32.14, 35.04) * mm, "end": v(-32.28, 35.2) * mm});
            skLineSegment(sketch, "E1482", {"start": v(-32.28, 35.2) * mm, "end": v(-32.44, 35.33) * mm});
            skLineSegment(sketch, "E1483", {"start": v(-32.44, 35.33) * mm, "end": v(-32.62, 35.42) * mm});
            skLineSegment(sketch, "E1484", {"start": v(-32.62, 35.42) * mm, "end": v(-32.82, 35.46) * mm});
            skLineSegment(sketch, "E1485", {"start": v(-32.82, 35.46) * mm, "end": v(-32.86, 35.46) * mm});
            skLineSegment(sketch, "E1486", {"start": v(-32.86, 35.46) * mm, "end": v(-33.06, 35.43) * mm});
            skLineSegment(sketch, "E1487", {"start": v(-33.06, 35.43) * mm, "end": v(-33.25, 35.35) * mm});
            skLineSegment(sketch, "E1488", {"start": v(-33.25, 35.35) * mm, "end": v(-33.41, 35.22) * mm});
            skLineSegment(sketch, "E1489", {"start": v(-33.41, 35.22) * mm, "end": v(-33.53, 35.06) * mm});
            skLineSegment(sketch, "E1490", {"start": v(-33.53, 35.06) * mm, "end": v(-33.6, 34.87) * mm});
            skLineSegment(sketch, "E1491", {"start": v(-33.6, 34.87) * mm, "end": v(-33.63, 34.67) * mm});
            skLineSegment(sketch, "E1492", {"start": v(-33.63, 34.67) * mm, "end": v(-33.6, 34.47) * mm});
            skLineSegment(sketch, "E1493", {"start": v(-33.6, 34.47) * mm, "end": v(-33.52, 34.28) * mm});
            skLineSegment(sketch, "E1494", {"start": v(-33.52, 34.28) * mm, "end": v(-33.38, 34.11) * mm});
            skLineSegment(sketch, "E1495", {"start": v(-33.38, 34.11) * mm, "end": v(-33.23, 33.95) * mm});
            skLineSegment(sketch, "E1496", {"start": v(-33.23, 33.95) * mm, "end": v(-33.07, 33.79) * mm});
            skLineSegment(sketch, "E1497", {"start": v(-33.07, 33.79) * mm, "end": v(-32.92, 33.62) * mm});
            skLineSegment(sketch, "E1498", {"start": v(-32.92, 33.62) * mm, "end": v(-32.77, 33.46) * mm});
            skLineSegment(sketch, "E1499", {"start": v(-32.77, 33.46) * mm, "end": v(-32.6, 33.29) * mm});
            skLineSegment(sketch, "E1500", {"start": v(-32.6, 33.29) * mm, "end": v(-32.45, 33.13) * mm});
            skLineSegment(sketch, "E1501", {"start": v(-32.45, 33.13) * mm, "end": v(-32.3, 32.97) * mm});
            skLineSegment(sketch, "E1502", {"start": v(-32.3, 32.97) * mm, "end": v(-32.15, 32.82) * mm});
            skLineSegment(sketch, "E1503", {"start": v(-32.15, 32.82) * mm, "end": v(-32, 32.66) * mm});
            skLineSegment(sketch, "E1504", {"start": v(-32, 32.66) * mm, "end": v(-31.85, 32.5) * mm});
            skLineSegment(sketch, "E1505", {"start": v(-31.85, 32.5) * mm, "end": v(-31.7, 32.35) * mm});
            skLineSegment(sketch, "E1506", {"start": v(-31.7, 32.35) * mm, "end": v(-31.56, 32.19) * mm});
            skLineSegment(sketch, "E1507", {"start": v(-31.56, 32.19) * mm, "end": v(-31.4, 32.03) * mm});
            skLineSegment(sketch, "E1508", {"start": v(-31.4, 32.03) * mm, "end": v(-31.26, 31.88) * mm});
            skLineSegment(sketch, "E1509", {"start": v(-31.26, 31.88) * mm, "end": v(-31.18, 31.8) * mm});
            skLineSegment(sketch, "E1510", {"start": v(-31.18, 31.8) * mm, "end": v(-31.34, 31.64) * mm});
            skLineSegment(sketch, "E1511", {"start": v(-31.34, 31.64) * mm, "end": v(-31.5, 31.48) * mm});
            skLineSegment(sketch, "E1512", {"start": v(-31.5, 31.48) * mm, "end": v(-31.65, 31.32) * mm});
            skLineSegment(sketch, "E1513", {"start": v(-31.65, 31.32) * mm, "end": v(-31.81, 31.17) * mm});
            skLineSegment(sketch, "E1514", {"start": v(-31.81, 31.17) * mm, "end": v(-31.97, 31) * mm});
            skLineSegment(sketch, "E1515", {"start": v(-31.97, 31) * mm, "end": v(-32.13, 30.85) * mm});
            skLineSegment(sketch, "E1516", {"start": v(-32.13, 30.85) * mm, "end": v(-32.28, 30.7) * mm});
            skLineSegment(sketch, "E1517", {"start": v(-32.28, 30.7) * mm, "end": v(-32.44, 30.54) * mm});
            skLineSegment(sketch, "E1518", {"start": v(-32.44, 30.54) * mm, "end": v(-32.6, 30.38) * mm});
            skLineSegment(sketch, "E1519", {"start": v(-32.6, 30.38) * mm, "end": v(-32.73, 30.25) * mm});
            skLineSegment(sketch, "E1520", {"start": v(-32.73, 30.25) * mm, "end": v(-32.88, 30.4) * mm});
            skLineSegment(sketch, "E1521", {"start": v(-32.88, 30.4) * mm, "end": v(-33.04, 30.55) * mm});
            skLineSegment(sketch, "E1522", {"start": v(-33.04, 30.55) * mm, "end": v(-33.2, 30.7) * mm});
            skLineSegment(sketch, "E1523", {"start": v(-33.2, 30.7) * mm, "end": v(-33.35, 30.85) * mm});
            skLineSegment(sketch, "E1524", {"start": v(-33.35, 30.85) * mm, "end": v(-33.51, 31) * mm});
            skLineSegment(sketch, "E1525", {"start": v(-33.51, 31) * mm, "end": v(-33.67, 31.15) * mm});
            skLineSegment(sketch, "E1526", {"start": v(-33.67, 31.15) * mm, "end": v(-33.83, 31.3) * mm});
            skLineSegment(sketch, "E1527", {"start": v(-33.83, 31.3) * mm, "end": v(-33.98, 31.45) * mm});
            skLineSegment(sketch, "E1528", {"start": v(-33.98, 31.45) * mm, "end": v(-34.14, 31.6) * mm});
            skLineSegment(sketch, "E1529", {"start": v(-34.14, 31.6) * mm, "end": v(-34.3, 31.75) * mm});
            skLineSegment(sketch, "E1530", {"start": v(-34.3, 31.75) * mm, "end": v(-34.45, 31.9) * mm});
            skLineSegment(sketch, "E1531", {"start": v(-34.45, 31.9) * mm, "end": v(-34.61, 32.05) * mm});
            skLineSegment(sketch, "E1532", {"start": v(-34.61, 32.05) * mm, "end": v(-34.77, 32.2) * mm});
            skLineSegment(sketch, "E1533", {"start": v(-34.77, 32.2) * mm, "end": v(-34.92, 32.34) * mm});
            skLineSegment(sketch, "E1534", {"start": v(-34.92, 32.34) * mm, "end": v(-35.08, 32.5) * mm});
            skLineSegment(sketch, "E1535", {"start": v(-35.08, 32.5) * mm, "end": v(-35.25, 32.61) * mm});
            skLineSegment(sketch, "E1536", {"start": v(-35.25, 32.61) * mm, "end": v(-35.44, 32.68) * mm});
            skLineSegment(sketch, "E1537", {"start": v(-35.44, 32.68) * mm, "end": v(-35.6, 32.7) * mm});
            skLineSegment(sketch, "E1538", {"start": v(-35.6, 32.7) * mm, "end": v(-35.8, 32.68) * mm});
            skLineSegment(sketch, "E1539", {"start": v(-35.8, 32.68) * mm, "end": v(-36, 32.6) * mm});
            skLineSegment(sketch, "E1540", {"start": v(-36, 32.6) * mm, "end": v(-36.15, 32.48) * mm});
            skLineSegment(sketch, "E1541", {"start": v(-36.15, 32.48) * mm, "end": v(-36.28, 32.32) * mm});
            skLineSegment(sketch, "E1542", {"start": v(-36.28, 32.32) * mm, "end": v(-36.36, 32.13) * mm});
            skLineSegment(sketch, "E1543", {"start": v(-36.36, 32.13) * mm, "end": v(-36.39, 31.93) * mm});
            skLineSegment(sketch, "E1544", {"start": v(-36.39, 31.93) * mm, "end": v(-36.36, 31.73) * mm});
            skLineSegment(sketch, "E1545", {"start": v(-36.36, 31.73) * mm, "end": v(-36.28, 31.54) * mm});
            skLineSegment(sketch, "E1546", {"start": v(-36.28, 31.54) * mm, "end": v(-36.16, 31.38) * mm});
            skLineSegment(sketch, "E1547", {"start": v(-36.16, 31.38) * mm, "end": v(-36, 31.23) * mm});
            skLineSegment(sketch, "E1548", {"start": v(-36, 31.23) * mm, "end": v(-35.83, 31.08) * mm});
            skLineSegment(sketch, "E1549", {"start": v(-35.83, 31.08) * mm, "end": v(-35.66, 30.94) * mm});
            skLineSegment(sketch, "E1550", {"start": v(-35.66, 30.94) * mm, "end": v(-35.48, 30.78) * mm});
            skLineSegment(sketch, "E1551", {"start": v(-35.48, 30.78) * mm, "end": v(-35.32, 30.63) * mm});
            skLineSegment(sketch, "E1552", {"start": v(-35.32, 30.63) * mm, "end": v(-35.16, 30.49) * mm});
            skLineSegment(sketch, "E1553", {"start": v(-35.16, 30.49) * mm, "end": v(-35, 30.34) * mm});
            skLineSegment(sketch, "E1554", {"start": v(-35, 30.34) * mm, "end": v(-34.84, 30.2) * mm});
            skLineSegment(sketch, "E1555", {"start": v(-34.84, 30.2) * mm, "end": v(-34.68, 30.06) * mm});
            skLineSegment(sketch, "E1556", {"start": v(-34.68, 30.06) * mm, "end": v(-34.51, 29.91) * mm});
            skLineSegment(sketch, "E1557", {"start": v(-34.51, 29.91) * mm, "end": v(-34.35, 29.77) * mm});
            skLineSegment(sketch, "E1558", {"start": v(-34.35, 29.77) * mm, "end": v(-34.19, 29.62) * mm});
            skLineSegment(sketch, "E1559", {"start": v(-34.19, 29.62) * mm, "end": v(-34.03, 29.48) * mm});
            skLineSegment(sketch, "E1560", {"start": v(-34.03, 29.48) * mm, "end": v(-33.87, 29.33) * mm});
            skLineSegment(sketch, "E1561", {"start": v(-33.87, 29.33) * mm, "end": v(-33.7, 29.2) * mm});
            skLineSegment(sketch, "E1562", {"start": v(-33.7, 29.2) * mm, "end": v(-33.85, 29.02) * mm});
            skLineSegment(sketch, "E1563", {"start": v(-33.85, 29.02) * mm, "end": v(-34, 28.85) * mm});
            skLineSegment(sketch, "E1564", {"start": v(-34, 28.85) * mm, "end": v(-34.14, 28.68) * mm});
            skLineSegment(sketch, "E1565", {"start": v(-34.14, 28.68) * mm, "end": v(-34.28, 28.51) * mm});
            skLineSegment(sketch, "E1566", {"start": v(-34.28, 28.51) * mm, "end": v(-34.42, 28.34) * mm});
            skLineSegment(sketch, "E1567", {"start": v(-34.42, 28.34) * mm, "end": v(-34.57, 28.17) * mm});
            skLineSegment(sketch, "E1568", {"start": v(-34.57, 28.17) * mm, "end": v(-34.71, 28) * mm});
            skLineSegment(sketch, "E1569", {"start": v(-34.71, 28) * mm, "end": v(-34.86, 27.83) * mm});
            skLineSegment(sketch, "E1570", {"start": v(-34.86, 27.83) * mm, "end": v(-35, 27.66) * mm});
            skLineSegment(sketch, "E1571", {"start": v(-35, 27.66) * mm, "end": v(-35.12, 27.52) * mm});
            skLineSegment(sketch, "E1572", {"start": v(-35.12, 27.52) * mm, "end": v(-35.28, 27.66) * mm});
            skLineSegment(sketch, "E1573", {"start": v(-35.28, 27.66) * mm, "end": v(-35.45, 27.8) * mm});
            skLineSegment(sketch, "E1574", {"start": v(-35.45, 27.8) * mm, "end": v(-35.62, 27.93) * mm});
            skLineSegment(sketch, "E1575", {"start": v(-35.62, 27.93) * mm, "end": v(-35.8, 28.07) * mm});
            skLineSegment(sketch, "E1576", {"start": v(-35.8, 28.07) * mm, "end": v(-35.96, 28.2) * mm});
            skLineSegment(sketch, "E1577", {"start": v(-35.96, 28.2) * mm, "end": v(-36.13, 28.34) * mm});
            skLineSegment(sketch, "E1578", {"start": v(-36.13, 28.34) * mm, "end": v(-36.3, 28.48) * mm});
            skLineSegment(sketch, "E1579", {"start": v(-36.3, 28.48) * mm, "end": v(-36.47, 28.61) * mm});
            skLineSegment(sketch, "E1580", {"start": v(-36.47, 28.61) * mm, "end": v(-36.64, 28.75) * mm});
            skLineSegment(sketch, "E1581", {"start": v(-36.64, 28.75) * mm, "end": v(-36.8, 28.88) * mm});
            skLineSegment(sketch, "E1582", {"start": v(-36.8, 28.88) * mm, "end": v(-36.97, 29.02) * mm});
            skLineSegment(sketch, "E1583", {"start": v(-36.97, 29.02) * mm, "end": v(-37.14, 29.15) * mm});
            skLineSegment(sketch, "E1584", {"start": v(-37.14, 29.15) * mm, "end": v(-37.31, 29.3) * mm});
            skLineSegment(sketch, "E1585", {"start": v(-37.31, 29.3) * mm, "end": v(-37.48, 29.43) * mm});
            skLineSegment(sketch, "E1586", {"start": v(-37.48, 29.43) * mm, "end": v(-37.65, 29.56) * mm});
            skLineSegment(sketch, "E1587", {"start": v(-37.65, 29.56) * mm, "end": v(-37.82, 29.67) * mm});
            skLineSegment(sketch, "E1588", {"start": v(-37.82, 29.67) * mm, "end": v(-38.02, 29.72) * mm});
            skLineSegment(sketch, "E1589", {"start": v(-38.02, 29.72) * mm, "end": v(-38.14, 29.73) * mm});
            skLineSegment(sketch, "E1590", {"start": v(-38.14, 29.73) * mm, "end": v(-38.34, 29.7) * mm});
            skLineSegment(sketch, "E1591", {"start": v(-38.34, 29.7) * mm, "end": v(-38.53, 29.62) * mm});
            skLineSegment(sketch, "E1592", {"start": v(-38.53, 29.62) * mm, "end": v(-38.69, 29.5) * mm});
            skLineSegment(sketch, "E1593", {"start": v(-38.69, 29.5) * mm, "end": v(-38.8, 29.33) * mm});
            skLineSegment(sketch, "E1594", {"start": v(-38.8, 29.33) * mm, "end": v(-38.88, 29.14) * mm});
            skLineSegment(sketch, "E1595", {"start": v(-38.88, 29.14) * mm, "end": v(-38.9, 28.94) * mm});
            skLineSegment(sketch, "E1596", {"start": v(-38.9, 28.94) * mm, "end": v(-38.87, 28.74) * mm});
            skLineSegment(sketch, "E1597", {"start": v(-38.87, 28.74) * mm, "end": v(-38.8, 28.55) * mm});
            skLineSegment(sketch, "E1598", {"start": v(-38.8, 28.55) * mm, "end": v(-38.66, 28.4) * mm});
            skLineSegment(sketch, "E1599", {"start": v(-38.66, 28.4) * mm, "end": v(-38.49, 28.25) * mm});
            skLineSegment(sketch, "E1600", {"start": v(-38.49, 28.25) * mm, "end": v(-38.3, 28.12) * mm});
            skLineSegment(sketch, "E1601", {"start": v(-38.3, 28.12) * mm, "end": v(-38.13, 27.99) * mm});
            skLineSegment(sketch, "E1602", {"start": v(-38.13, 27.99) * mm, "end": v(-37.95, 27.85) * mm});
            skLineSegment(sketch, "E1603", {"start": v(-37.95, 27.85) * mm, "end": v(-37.78, 27.72) * mm});
            skLineSegment(sketch, "E1604", {"start": v(-37.78, 27.72) * mm, "end": v(-37.6, 27.58) * mm});
            skLineSegment(sketch, "E1605", {"start": v(-37.6, 27.58) * mm, "end": v(-37.42, 27.45) * mm});
            skLineSegment(sketch, "E1606", {"start": v(-37.42, 27.45) * mm, "end": v(-37.24, 27.32) * mm});
            skLineSegment(sketch, "E1607", {"start": v(-37.24, 27.32) * mm, "end": v(-37.06, 27.18) * mm});
            skLineSegment(sketch, "E1608", {"start": v(-37.06, 27.18) * mm, "end": v(-36.87, 27.04) * mm});
            skLineSegment(sketch, "E1609", {"start": v(-36.87, 27.04) * mm, "end": v(-36.7, 26.9) * mm});
            skLineSegment(sketch, "E1610", {"start": v(-36.7, 26.9) * mm, "end": v(-36.52, 26.77) * mm});
            skLineSegment(sketch, "E1611", {"start": v(-36.52, 26.77) * mm, "end": v(-36.35, 26.64) * mm});
            skLineSegment(sketch, "E1612", {"start": v(-36.35, 26.64) * mm, "end": v(-36.18, 26.51) * mm});
            skLineSegment(sketch, "E1613", {"start": v(-36.18, 26.51) * mm, "end": v(-36, 26.38) * mm});
            skLineSegment(sketch, "E1614", {"start": v(-36, 26.38) * mm, "end": v(-36.13, 26.2) * mm});
            skLineSegment(sketch, "E1615", {"start": v(-36.13, 26.2) * mm, "end": v(-36.26, 26.02) * mm});
            skLineSegment(sketch, "E1616", {"start": v(-36.26, 26.02) * mm, "end": v(-36.4, 25.84) * mm});
            skLineSegment(sketch, "E1617", {"start": v(-36.4, 25.84) * mm, "end": v(-36.52, 25.66) * mm});
            skLineSegment(sketch, "E1618", {"start": v(-36.52, 25.66) * mm, "end": v(-36.65, 25.48) * mm});
            skLineSegment(sketch, "E1619", {"start": v(-36.65, 25.48) * mm, "end": v(-36.78, 25.3) * mm});
            skLineSegment(sketch, "E1620", {"start": v(-36.78, 25.3) * mm, "end": v(-36.9, 25.12) * mm});
            skLineSegment(sketch, "E1621", {"start": v(-36.9, 25.12) * mm, "end": v(-37.04, 24.93) * mm});
            skLineSegment(sketch, "E1622", {"start": v(-37.04, 24.93) * mm, "end": v(-37.17, 24.75) * mm});
            skLineSegment(sketch, "E1623", {"start": v(-37.17, 24.75) * mm, "end": v(-37.27, 24.6) * mm});
            skLineSegment(sketch, "E1624", {"start": v(-37.27, 24.6) * mm, "end": v(-37.45, 24.73) * mm});
            skLineSegment(sketch, "E1625", {"start": v(-37.45, 24.73) * mm, "end": v(-37.63, 24.85) * mm});
            skLineSegment(sketch, "E1626", {"start": v(-37.63, 24.85) * mm, "end": v(-37.81, 24.97) * mm});
            skLineSegment(sketch, "E1627", {"start": v(-37.81, 24.97) * mm, "end": v(-37.99, 25.1) * mm});
            skLineSegment(sketch, "E1628", {"start": v(-37.99, 25.1) * mm, "end": v(-38.17, 25.21) * mm});
            skLineSegment(sketch, "E1629", {"start": v(-38.17, 25.21) * mm, "end": v(-38.35, 25.34) * mm});
            skLineSegment(sketch, "E1630", {"start": v(-38.35, 25.34) * mm, "end": v(-38.53, 25.46) * mm});
            skLineSegment(sketch, "E1631", {"start": v(-38.53, 25.46) * mm, "end": v(-38.7, 25.58) * mm});
            skLineSegment(sketch, "E1632", {"start": v(-38.7, 25.58) * mm, "end": v(-38.89, 25.7) * mm});
            skLineSegment(sketch, "E1633", {"start": v(-38.89, 25.7) * mm, "end": v(-39.07, 25.82) * mm});
            skLineSegment(sketch, "E1634", {"start": v(-39.07, 25.82) * mm, "end": v(-39.25, 25.94) * mm});
            skLineSegment(sketch, "E1635", {"start": v(-39.25, 25.94) * mm, "end": v(-39.43, 26.06) * mm});
            skLineSegment(sketch, "E1636", {"start": v(-39.43, 26.06) * mm, "end": v(-39.6, 26.19) * mm});
            skLineSegment(sketch, "E1637", {"start": v(-39.6, 26.19) * mm, "end": v(-39.78, 26.3) * mm});
            skLineSegment(sketch, "E1638", {"start": v(-39.78, 26.3) * mm, "end": v(-39.96, 26.43) * mm});
            skLineSegment(sketch, "E1639", {"start": v(-39.96, 26.43) * mm, "end": v(-40.15, 26.52) * mm});
            skLineSegment(sketch, "E1640", {"start": v(-40.15, 26.52) * mm, "end": v(-40.35, 26.56) * mm});
            skLineSegment(sketch, "E1641", {"start": v(-40.35, 26.56) * mm, "end": v(-40.39, 26.56) * mm});
            skLineSegment(sketch, "E1642", {"start": v(-40.39, 26.56) * mm, "end": v(-40.59, 26.53) * mm});
            skLineSegment(sketch, "E1643", {"start": v(-40.59, 26.53) * mm, "end": v(-40.78, 26.46) * mm});
            skLineSegment(sketch, "E1644", {"start": v(-40.78, 26.46) * mm, "end": v(-40.94, 26.33) * mm});
            skLineSegment(sketch, "E1645", {"start": v(-40.94, 26.33) * mm, "end": v(-41.06, 26.17) * mm});
            skLineSegment(sketch, "E1646", {"start": v(-41.06, 26.17) * mm, "end": v(-41.14, 25.98) * mm});
            skLineSegment(sketch, "E1647", {"start": v(-41.14, 25.98) * mm, "end": v(-41.17, 25.78) * mm});
            skLineSegment(sketch, "E1648", {"start": v(-41.17, 25.78) * mm, "end": v(-41.14, 25.58) * mm});
            skLineSegment(sketch, "E1649", {"start": v(-41.14, 25.58) * mm, "end": v(-41.06, 25.4) * mm});
            skLineSegment(sketch, "E1650", {"start": v(-41.06, 25.4) * mm, "end": v(-40.94, 25.23) * mm});
            skLineSegment(sketch, "E1651", {"start": v(-40.94, 25.23) * mm, "end": v(-40.76, 25.1) * mm});
            skLineSegment(sketch, "E1652", {"start": v(-40.76, 25.1) * mm, "end": v(-40.57, 24.98) * mm});
            skLineSegment(sketch, "E1653", {"start": v(-40.57, 24.98) * mm, "end": v(-40.38, 24.86) * mm});
            skLineSegment(sketch, "E1654", {"start": v(-40.38, 24.86) * mm, "end": v(-40.2, 24.74) * mm});
            skLineSegment(sketch, "E1655", {"start": v(-40.2, 24.74) * mm, "end": v(-40, 24.62) * mm});
            skLineSegment(sketch, "E1656", {"start": v(-40, 24.62) * mm, "end": v(-39.8, 24.5) * mm});
            skLineSegment(sketch, "E1657", {"start": v(-39.8, 24.5) * mm, "end": v(-39.62, 24.38) * mm});
            skLineSegment(sketch, "E1658", {"start": v(-39.62, 24.38) * mm, "end": v(-39.44, 24.26) * mm});
            skLineSegment(sketch, "E1659", {"start": v(-39.44, 24.26) * mm, "end": v(-39.25, 24.15) * mm});
            skLineSegment(sketch, "E1660", {"start": v(-39.25, 24.15) * mm, "end": v(-39.07, 24.03) * mm});
            skLineSegment(sketch, "E1661", {"start": v(-39.07, 24.03) * mm, "end": v(-38.89, 23.92) * mm});
            skLineSegment(sketch, "E1662", {"start": v(-38.89, 23.92) * mm, "end": v(-38.7, 23.8) * mm});
            skLineSegment(sketch, "E1663", {"start": v(-38.7, 23.8) * mm, "end": v(-38.52, 23.69) * mm});
            skLineSegment(sketch, "E1664", {"start": v(-38.52, 23.69) * mm, "end": v(-38.34, 23.57) * mm});
            skLineSegment(sketch, "E1665", {"start": v(-38.34, 23.57) * mm, "end": v(-38.15, 23.46) * mm});
            skLineSegment(sketch, "E1666", {"start": v(-38.15, 23.46) * mm, "end": v(-38.06, 23.4) * mm});
            skLineSegment(sketch, "E1667", {"start": v(-38.06, 23.4) * mm, "end": v(-38.18, 23.2) * mm});
            skLineSegment(sketch, "E1668", {"start": v(-38.18, 23.2) * mm, "end": v(-38.3, 23.01) * mm});
            skLineSegment(sketch, "E1669", {"start": v(-38.3, 23.01) * mm, "end": v(-38.4, 22.82) * mm});
            skLineSegment(sketch, "E1670", {"start": v(-38.4, 22.82) * mm, "end": v(-38.52, 22.63) * mm});
            skLineSegment(sketch, "E1671", {"start": v(-38.52, 22.63) * mm, "end": v(-38.63, 22.44) * mm});
            skLineSegment(sketch, "E1672", {"start": v(-38.63, 22.44) * mm, "end": v(-38.75, 22.25) * mm});
            skLineSegment(sketch, "E1673", {"start": v(-38.75, 22.25) * mm, "end": v(-38.86, 22.06) * mm});
            skLineSegment(sketch, "E1674", {"start": v(-38.86, 22.06) * mm, "end": v(-38.97, 21.87) * mm});
            skLineSegment(sketch, "E1675", {"start": v(-38.97, 21.87) * mm, "end": v(-39.09, 21.68) * mm});
            skLineSegment(sketch, "E1676", {"start": v(-39.09, 21.68) * mm, "end": v(-39.18, 21.52) * mm});
            skLineSegment(sketch, "E1677", {"start": v(-39.18, 21.52) * mm, "end": v(-39.37, 21.63) * mm});
            skLineSegment(sketch, "E1678", {"start": v(-39.37, 21.63) * mm, "end": v(-39.56, 21.73) * mm});
            skLineSegment(sketch, "E1679", {"start": v(-39.56, 21.73) * mm, "end": v(-39.75, 21.84) * mm});
            skLineSegment(sketch, "E1680", {"start": v(-39.75, 21.84) * mm, "end": v(-39.94, 21.95) * mm});
            skLineSegment(sketch, "E1681", {"start": v(-39.94, 21.95) * mm, "end": v(-40.12, 22.05) * mm});
            skLineSegment(sketch, "E1682", {"start": v(-40.12, 22.05) * mm, "end": v(-40.31, 22.16) * mm});
            skLineSegment(sketch, "E1683", {"start": v(-40.31, 22.16) * mm, "end": v(-40.5, 22.27) * mm});
            skLineSegment(sketch, "E1684", {"start": v(-40.5, 22.27) * mm, "end": v(-40.7, 22.37) * mm});
            skLineSegment(sketch, "E1685", {"start": v(-40.7, 22.37) * mm, "end": v(-40.88, 22.48) * mm});
            skLineSegment(sketch, "E1686", {"start": v(-40.88, 22.48) * mm, "end": v(-41.07, 22.58) * mm});
            skLineSegment(sketch, "E1687", {"start": v(-41.07, 22.58) * mm, "end": v(-41.26, 22.7) * mm});
            skLineSegment(sketch, "E1688", {"start": v(-41.26, 22.7) * mm, "end": v(-41.45, 22.8) * mm});
            skLineSegment(sketch, "E1689", {"start": v(-41.45, 22.8) * mm, "end": v(-41.64, 22.9) * mm});
            skLineSegment(sketch, "E1690", {"start": v(-41.64, 22.9) * mm, "end": v(-41.82, 23) * mm});
            skLineSegment(sketch, "E1691", {"start": v(-41.82, 23) * mm, "end": v(-42.01, 23.12) * mm});
            skLineSegment(sketch, "E1692", {"start": v(-42.01, 23.12) * mm, "end": v(-42.2, 23.19) * mm});
            skLineSegment(sketch, "E1693", {"start": v(-42.2, 23.19) * mm, "end": v(-42.4, 23.21) * mm});
            skLineSegment(sketch, "E1694", {"start": v(-42.4, 23.21) * mm, "end": v(-42.6, 23.18) * mm});
            skLineSegment(sketch, "E1695", {"start": v(-42.6, 23.18) * mm, "end": v(-42.8, 23.1) * mm});
            skLineSegment(sketch, "E1696", {"start": v(-42.8, 23.1) * mm, "end": v(-42.95, 22.97) * mm});
            skLineSegment(sketch, "E1697", {"start": v(-42.95, 22.97) * mm, "end": v(-43.07, 22.8) * mm});
            skLineSegment(sketch, "E1698", {"start": v(-43.07, 22.8) * mm, "end": v(-43.14, 22.62) * mm});
            skLineSegment(sketch, "E1699", {"start": v(-43.14, 22.62) * mm, "end": v(-43.16, 22.41) * mm});
            skLineSegment(sketch, "E1700", {"start": v(-43.16, 22.41) * mm, "end": v(-43.13, 22.21) * mm});
            skLineSegment(sketch, "E1701", {"start": v(-43.13, 22.21) * mm, "end": v(-43.05, 22.03) * mm});
            skLineSegment(sketch, "E1702", {"start": v(-43.05, 22.03) * mm, "end": v(-42.92, 21.87) * mm});
            skLineSegment(sketch, "E1703", {"start": v(-42.92, 21.87) * mm, "end": v(-42.75, 21.75) * mm});
            skLineSegment(sketch, "E1704", {"start": v(-42.75, 21.75) * mm, "end": v(-42.56, 21.65) * mm});
            skLineSegment(sketch, "E1705", {"start": v(-42.56, 21.65) * mm, "end": v(-42.37, 21.55) * mm});
            skLineSegment(sketch, "E1706", {"start": v(-42.37, 21.55) * mm, "end": v(-42.17, 21.45) * mm});
            skLineSegment(sketch, "E1707", {"start": v(-42.17, 21.45) * mm, "end": v(-41.98, 21.35) * mm});
            skLineSegment(sketch, "E1708", {"start": v(-41.98, 21.35) * mm, "end": v(-41.79, 21.25) * mm});
            skLineSegment(sketch, "E1709", {"start": v(-41.79, 21.25) * mm, "end": v(-41.6, 21.15) * mm});
            skLineSegment(sketch, "E1710", {"start": v(-41.6, 21.15) * mm, "end": v(-41.4, 21.05) * mm});
            skLineSegment(sketch, "E1711", {"start": v(-41.4, 21.05) * mm, "end": v(-41.21, 20.95) * mm});
            skLineSegment(sketch, "E1712", {"start": v(-41.21, 20.95) * mm, "end": v(-41.02, 20.85) * mm});
            skLineSegment(sketch, "E1713", {"start": v(-41.02, 20.85) * mm, "end": v(-40.83, 20.75) * mm});
            skLineSegment(sketch, "E1714", {"start": v(-40.83, 20.75) * mm, "end": v(-40.64, 20.65) * mm});
            skLineSegment(sketch, "E1715", {"start": v(-40.64, 20.65) * mm, "end": v(-40.44, 20.55) * mm});
            skLineSegment(sketch, "E1716", {"start": v(-40.44, 20.55) * mm, "end": v(-40.25, 20.45) * mm});
            skLineSegment(sketch, "E1717", {"start": v(-40.25, 20.45) * mm, "end": v(-40.06, 20.35) * mm});
            skLineSegment(sketch, "E1718", {"start": v(-40.06, 20.35) * mm, "end": v(-39.87, 20.25) * mm});
            skLineSegment(sketch, "E1719", {"start": v(-39.87, 20.25) * mm, "end": v(-39.97, 20.05) * mm});
            skLineSegment(sketch, "E1720", {"start": v(-39.97, 20.05) * mm, "end": v(-40.06, 19.85) * mm});
            skLineSegment(sketch, "E1721", {"start": v(-40.06, 19.85) * mm, "end": v(-40.16, 19.65) * mm});
            skLineSegment(sketch, "E1722", {"start": v(-40.16, 19.65) * mm, "end": v(-40.26, 19.45) * mm});
            skLineSegment(sketch, "E1723", {"start": v(-40.26, 19.45) * mm, "end": v(-40.36, 19.25) * mm});
            skLineSegment(sketch, "E1724", {"start": v(-40.36, 19.25) * mm, "end": v(-40.45, 19.05) * mm});
            skLineSegment(sketch, "E1725", {"start": v(-40.45, 19.05) * mm, "end": v(-40.55, 18.85) * mm});
            skLineSegment(sketch, "E1726", {"start": v(-40.55, 18.85) * mm, "end": v(-40.65, 18.65) * mm});
            skLineSegment(sketch, "E1727", {"start": v(-40.65, 18.65) * mm, "end": v(-40.75, 18.45) * mm});
            skLineSegment(sketch, "E1728", {"start": v(-40.75, 18.45) * mm, "end": v(-40.83, 18.29) * mm});
            skLineSegment(sketch, "E1729", {"start": v(-40.83, 18.29) * mm, "end": v(-41.02, 18.38) * mm});
            skLineSegment(sketch, "E1730", {"start": v(-41.02, 18.38) * mm, "end": v(-41.22, 18.47) * mm});
            skLineSegment(sketch, "E1731", {"start": v(-41.22, 18.47) * mm, "end": v(-41.42, 18.56) * mm});
            skLineSegment(sketch, "E1732", {"start": v(-41.42, 18.56) * mm, "end": v(-41.61, 18.65) * mm});
            skLineSegment(sketch, "E1733", {"start": v(-41.61, 18.65) * mm, "end": v(-41.81, 18.74) * mm});
            skLineSegment(sketch, "E1734", {"start": v(-41.81, 18.74) * mm, "end": v(-42, 18.83) * mm});
            skLineSegment(sketch, "E1735", {"start": v(-42, 18.83) * mm, "end": v(-42.2, 18.92) * mm});
            skLineSegment(sketch, "E1736", {"start": v(-42.2, 18.92) * mm, "end": v(-42.4, 19.01) * mm});
            skLineSegment(sketch, "E1737", {"start": v(-42.4, 19.01) * mm, "end": v(-42.6, 19.1) * mm});
            skLineSegment(sketch, "E1738", {"start": v(-42.6, 19.1) * mm, "end": v(-42.8, 19.2) * mm});
            skLineSegment(sketch, "E1739", {"start": v(-42.8, 19.2) * mm, "end": v(-43, 19.28) * mm});
            skLineSegment(sketch, "E1740", {"start": v(-43, 19.28) * mm, "end": v(-43.2, 19.37) * mm});
            skLineSegment(sketch, "E1741", {"start": v(-43.2, 19.37) * mm, "end": v(-43.39, 19.46) * mm});
            skLineSegment(sketch, "E1742", {"start": v(-43.39, 19.46) * mm, "end": v(-43.58, 19.55) * mm});
            skLineSegment(sketch, "E1743", {"start": v(-43.58, 19.55) * mm, "end": v(-43.78, 19.64) * mm});
            skLineSegment(sketch, "E1744", {"start": v(-43.78, 19.64) * mm, "end": v(-43.98, 19.7) * mm});
            skLineSegment(sketch, "E1745", {"start": v(-43.98, 19.7) * mm, "end": v(-44.1, 19.71) * mm});
            skLineSegment(sketch, "E1746", {"start": v(-44.1, 19.71) * mm, "end": v(-44.3, 19.69) * mm});
            skLineSegment(sketch, "E1747", {"start": v(-44.3, 19.69) * mm, "end": v(-44.49, 19.6) * mm});
            skLineSegment(sketch, "E1748", {"start": v(-44.49, 19.6) * mm, "end": v(-44.65, 19.48) * mm});
            skLineSegment(sketch, "E1749", {"start": v(-44.65, 19.48) * mm, "end": v(-44.77, 19.32) * mm});
            skLineSegment(sketch, "E1750", {"start": v(-44.77, 19.32) * mm, "end": v(-44.85, 19.13) * mm});
            skLineSegment(sketch, "E1751", {"start": v(-44.85, 19.13) * mm, "end": v(-44.87, 18.93) * mm});
            skLineSegment(sketch, "E1752", {"start": v(-44.87, 18.93) * mm, "end": v(-44.85, 18.73) * mm});
            skLineSegment(sketch, "E1753", {"start": v(-44.85, 18.73) * mm, "end": v(-44.77, 18.54) * mm});
            skLineSegment(sketch, "E1754", {"start": v(-44.77, 18.54) * mm, "end": v(-44.64, 18.38) * mm});
            skLineSegment(sketch, "E1755", {"start": v(-44.64, 18.38) * mm, "end": v(-44.48, 18.26) * mm});
            skLineSegment(sketch, "E1756", {"start": v(-44.48, 18.26) * mm, "end": v(-44.27, 18.17) * mm});
            skLineSegment(sketch, "E1757", {"start": v(-44.27, 18.17) * mm, "end": v(-44.07, 18.08) * mm});
            skLineSegment(sketch, "E1758", {"start": v(-44.07, 18.08) * mm, "end": v(-43.86, 18) * mm});
            skLineSegment(sketch, "E1759", {"start": v(-43.86, 18) * mm, "end": v(-43.66, 17.91) * mm});
            skLineSegment(sketch, "E1760", {"start": v(-43.66, 17.91) * mm, "end": v(-43.45, 17.82) * mm});
            skLineSegment(sketch, "E1761", {"start": v(-43.45, 17.82) * mm, "end": v(-43.25, 17.74) * mm});
            skLineSegment(sketch, "E1762", {"start": v(-43.25, 17.74) * mm, "end": v(-43.04, 17.65) * mm});
            skLineSegment(sketch, "E1763", {"start": v(-43.04, 17.65) * mm, "end": v(-42.84, 17.57) * mm});
            skLineSegment(sketch, "E1764", {"start": v(-42.84, 17.57) * mm, "end": v(-42.63, 17.48) * mm});
            skLineSegment(sketch, "E1765", {"start": v(-42.63, 17.48) * mm, "end": v(-42.4, 17.39) * mm});
            skLineSegment(sketch, "E1766", {"start": v(-42.4, 17.39) * mm, "end": v(-42.2, 17.3) * mm});
            skLineSegment(sketch, "E1767", {"start": v(-42.2, 17.3) * mm, "end": v(-42, 17.22) * mm});
            skLineSegment(sketch, "E1768", {"start": v(-42, 17.22) * mm, "end": v(-41.8, 17.13) * mm});
            skLineSegment(sketch, "E1769", {"start": v(-41.8, 17.13) * mm, "end": v(-41.6, 17.05) * mm});
            skLineSegment(sketch, "E1770", {"start": v(-41.6, 17.05) * mm, "end": v(-41.4, 16.97) * mm});
            skLineSegment(sketch, "E1771", {"start": v(-41.4, 16.97) * mm, "end": v(-41.49, 16.76) * mm});
            skLineSegment(sketch, "E1772", {"start": v(-41.49, 16.76) * mm, "end": v(-41.57, 16.55) * mm});
            skLineSegment(sketch, "E1773", {"start": v(-41.57, 16.55) * mm, "end": v(-41.65, 16.34) * mm});
            skLineSegment(sketch, "E1774", {"start": v(-41.65, 16.34) * mm, "end": v(-41.73, 16.14) * mm});
            skLineSegment(sketch, "E1775", {"start": v(-41.73, 16.14) * mm, "end": v(-41.81, 15.93) * mm});
            skLineSegment(sketch, "E1776", {"start": v(-41.81, 15.93) * mm, "end": v(-41.9, 15.72) * mm});
            skLineSegment(sketch, "E1777", {"start": v(-41.9, 15.72) * mm, "end": v(-41.97, 15.51) * mm});
            skLineSegment(sketch, "E1778", {"start": v(-41.97, 15.51) * mm, "end": v(-42.05, 15.3) * mm});
            skLineSegment(sketch, "E1779", {"start": v(-42.05, 15.3) * mm, "end": v(-42.14, 15.1) * mm});
            skLineSegment(sketch, "E1780", {"start": v(-42.14, 15.1) * mm, "end": v(-42.2, 14.93) * mm});
            skLineSegment(sketch, "E1781", {"start": v(-42.2, 14.93) * mm, "end": v(-42.4, 15) * mm});
            skLineSegment(sketch, "E1782", {"start": v(-42.4, 15) * mm, "end": v(-42.6, 15.08) * mm});
            skLineSegment(sketch, "E1783", {"start": v(-42.6, 15.08) * mm, "end": v(-42.81, 15.15) * mm});
            skLineSegment(sketch, "E1784", {"start": v(-42.81, 15.15) * mm, "end": v(-43.02, 15.23) * mm});
            skLineSegment(sketch, "E1785", {"start": v(-43.02, 15.23) * mm, "end": v(-43.22, 15.3) * mm});
            skLineSegment(sketch, "E1786", {"start": v(-43.22, 15.3) * mm, "end": v(-43.42, 15.37) * mm});
            skLineSegment(sketch, "E1787", {"start": v(-43.42, 15.37) * mm, "end": v(-43.63, 15.45) * mm});
            skLineSegment(sketch, "E1788", {"start": v(-43.63, 15.45) * mm, "end": v(-43.83, 15.52) * mm});
            skLineSegment(sketch, "E1789", {"start": v(-43.83, 15.52) * mm, "end": v(-44.03, 15.6) * mm});
            skLineSegment(sketch, "E1790", {"start": v(-44.03, 15.6) * mm, "end": v(-44.24, 15.67) * mm});
            skLineSegment(sketch, "E1791", {"start": v(-44.24, 15.67) * mm, "end": v(-44.44, 15.74) * mm});
            skLineSegment(sketch, "E1792", {"start": v(-44.44, 15.74) * mm, "end": v(-44.65, 15.82) * mm});
            skLineSegment(sketch, "E1793", {"start": v(-44.65, 15.82) * mm, "end": v(-44.85, 15.9) * mm});
            skLineSegment(sketch, "E1794", {"start": v(-44.85, 15.9) * mm, "end": v(-45.05, 15.96) * mm});
            skLineSegment(sketch, "E1795", {"start": v(-45.05, 15.96) * mm, "end": v(-45.26, 16.04) * mm});
            skLineSegment(sketch, "E1796", {"start": v(-45.26, 16.04) * mm, "end": v(-45.46, 16.08) * mm});
            skLineSegment(sketch, "E1797", {"start": v(-45.46, 16.08) * mm, "end": v(-45.5, 16.08) * mm});
            skLineSegment(sketch, "E1798", {"start": v(-45.5, 16.08) * mm, "end": v(-45.7, 16.06) * mm});
            skLineSegment(sketch, "E1799", {"start": v(-45.7, 16.06) * mm, "end": v(-45.89, 15.99) * mm});
            skLineSegment(sketch, "E1800", {"start": v(-45.89, 15.99) * mm, "end": v(-46.05, 15.87) * mm});
            skLineSegment(sketch, "E1801", {"start": v(-46.05, 15.87) * mm, "end": v(-46.18, 15.7) * mm});
            skLineSegment(sketch, "E1802", {"start": v(-46.18, 15.7) * mm, "end": v(-46.26, 15.52) * mm});
            skLineSegment(sketch, "E1803", {"start": v(-46.26, 15.52) * mm, "end": v(-46.3, 15.32) * mm});
            skLineSegment(sketch, "E1804", {"start": v(-46.3, 15.32) * mm, "end": v(-46.27, 15.12) * mm});
            skLineSegment(sketch, "E1805", {"start": v(-46.27, 15.12) * mm, "end": v(-46.2, 14.93) * mm});
            skLineSegment(sketch, "E1806", {"start": v(-46.2, 14.93) * mm, "end": v(-46.07, 14.76) * mm});
            skLineSegment(sketch, "E1807", {"start": v(-46.07, 14.76) * mm, "end": v(-45.9, 14.64) * mm});
            skLineSegment(sketch, "E1808", {"start": v(-45.9, 14.64) * mm, "end": v(-45.7, 14.56) * mm});
            skLineSegment(sketch, "E1809", {"start": v(-45.7, 14.56) * mm, "end": v(-45.5, 14.48) * mm});
            skLineSegment(sketch, "E1810", {"start": v(-45.5, 14.48) * mm, "end": v(-45.28, 14.41) * mm});
            skLineSegment(sketch, "E1811", {"start": v(-45.28, 14.41) * mm, "end": v(-45.07, 14.35) * mm});
            skLineSegment(sketch, "E1812", {"start": v(-45.07, 14.35) * mm, "end": v(-44.86, 14.28) * mm});
            skLineSegment(sketch, "E1813", {"start": v(-44.86, 14.28) * mm, "end": v(-44.63, 14.2) * mm});
            skLineSegment(sketch, "E1814", {"start": v(-44.63, 14.2) * mm, "end": v(-44.42, 14.14) * mm});
            skLineSegment(sketch, "E1815", {"start": v(-44.42, 14.14) * mm, "end": v(-44.22, 14.07) * mm});
            skLineSegment(sketch, "E1816", {"start": v(-44.22, 14.07) * mm, "end": v(-44, 14) * mm});
            skLineSegment(sketch, "E1817", {"start": v(-44, 14) * mm, "end": v(-43.8, 13.93) * mm});
            skLineSegment(sketch, "E1818", {"start": v(-43.8, 13.93) * mm, "end": v(-43.6, 13.87) * mm});
            skLineSegment(sketch, "E1819", {"start": v(-43.6, 13.87) * mm, "end": v(-43.4, 13.8) * mm});
            skLineSegment(sketch, "E1820", {"start": v(-43.4, 13.8) * mm, "end": v(-43.18, 13.73) * mm});
            skLineSegment(sketch, "E1821", {"start": v(-43.18, 13.73) * mm, "end": v(-42.98, 13.67) * mm});
            skLineSegment(sketch, "E1822", {"start": v(-42.98, 13.67) * mm, "end": v(-42.77, 13.6) * mm});
            skLineSegment(sketch, "E1823", {"start": v(-42.77, 13.6) * mm, "end": v(-42.67, 13.57) * mm});
            skLineSegment(sketch, "E1824", {"start": v(-42.67, 13.57) * mm, "end": v(-42.73, 13.35) * mm});
            skLineSegment(sketch, "E1825", {"start": v(-42.73, 13.35) * mm, "end": v(-42.8, 13.14) * mm});
            skLineSegment(sketch, "E1826", {"start": v(-42.8, 13.14) * mm, "end": v(-42.86, 12.93) * mm});
            skLineSegment(sketch, "E1827", {"start": v(-42.86, 12.93) * mm, "end": v(-42.92, 12.71) * mm});
            skLineSegment(sketch, "E1828", {"start": v(-42.92, 12.71) * mm, "end": v(-42.99, 12.5) * mm});
            skLineSegment(sketch, "E1829", {"start": v(-42.99, 12.5) * mm, "end": v(-43.05, 12.29) * mm});
            skLineSegment(sketch, "E1830", {"start": v(-43.05, 12.29) * mm, "end": v(-43.11, 12.07) * mm});
            skLineSegment(sketch, "E1831", {"start": v(-43.11, 12.07) * mm, "end": v(-43.18, 11.86) * mm});
            skLineSegment(sketch, "E1832", {"start": v(-43.18, 11.86) * mm, "end": v(-43.24, 11.65) * mm});
            skLineSegment(sketch, "E1833", {"start": v(-43.24, 11.65) * mm, "end": v(-43.3, 11.47) * mm});
            skLineSegment(sketch, "E1834", {"start": v(-43.3, 11.47) * mm, "end": v(-43.5, 11.53) * mm});
            skLineSegment(sketch, "E1835", {"start": v(-43.5, 11.53) * mm, "end": v(-43.71, 11.59) * mm});
            skLineSegment(sketch, "E1836", {"start": v(-43.71, 11.59) * mm, "end": v(-43.92, 11.64) * mm});
            skLineSegment(sketch, "E1837", {"start": v(-43.92, 11.64) * mm, "end": v(-44.13, 11.7) * mm});
            skLineSegment(sketch, "E1838", {"start": v(-44.13, 11.7) * mm, "end": v(-44.34, 11.76) * mm});
            skLineSegment(sketch, "E1839", {"start": v(-44.34, 11.76) * mm, "end": v(-44.55, 11.81) * mm});
            skLineSegment(sketch, "E1840", {"start": v(-44.55, 11.81) * mm, "end": v(-44.76, 11.87) * mm});
            skLineSegment(sketch, "E1841", {"start": v(-44.76, 11.87) * mm, "end": v(-44.97, 11.93) * mm});
            skLineSegment(sketch, "E1842", {"start": v(-44.97, 11.93) * mm, "end": v(-45.18, 11.98) * mm});
            skLineSegment(sketch, "E1843", {"start": v(-45.18, 11.98) * mm, "end": v(-45.38, 12.04) * mm});
            skLineSegment(sketch, "E1844", {"start": v(-45.38, 12.04) * mm, "end": v(-45.6, 12.1) * mm});
            skLineSegment(sketch, "E1845", {"start": v(-45.6, 12.1) * mm, "end": v(-45.8, 12.15) * mm});
            skLineSegment(sketch, "E1846", {"start": v(-45.8, 12.15) * mm, "end": v(-46.01, 12.2) * mm});
            skLineSegment(sketch, "E1847", {"start": v(-46.01, 12.2) * mm, "end": v(-46.22, 12.27) * mm});
            skLineSegment(sketch, "E1848", {"start": v(-46.22, 12.27) * mm, "end": v(-46.43, 12.32) * mm});
            skLineSegment(sketch, "E1849", {"start": v(-46.43, 12.32) * mm, "end": v(-46.63, 12.35) * mm});
            skLineSegment(sketch, "E1850", {"start": v(-46.63, 12.35) * mm, "end": v(-46.83, 12.32) * mm});
            skLineSegment(sketch, "E1851", {"start": v(-46.83, 12.32) * mm, "end": v(-47.02, 12.24) * mm});
            skLineSegment(sketch, "E1852", {"start": v(-47.02, 12.24) * mm, "end": v(-47.18, 12.11) * mm});
            skLineSegment(sketch, "E1853", {"start": v(-47.18, 12.11) * mm, "end": v(-47.3, 11.95) * mm});
            skLineSegment(sketch, "E1854", {"start": v(-47.3, 11.95) * mm, "end": v(-47.38, 11.76) * mm});
            skLineSegment(sketch, "E1855", {"start": v(-47.38, 11.76) * mm, "end": v(-47.4, 11.56) * mm});
            skLineSegment(sketch, "E1856", {"start": v(-47.4, 11.56) * mm, "end": v(-47.37, 11.36) * mm});
            skLineSegment(sketch, "E1857", {"start": v(-47.37, 11.36) * mm, "end": v(-47.3, 11.17) * mm});
            skLineSegment(sketch, "E1858", {"start": v(-47.3, 11.17) * mm, "end": v(-47.16, 11.01) * mm});
            skLineSegment(sketch, "E1859", {"start": v(-47.16, 11.01) * mm, "end": v(-47, 10.9) * mm});
            skLineSegment(sketch, "E1860", {"start": v(-47, 10.9) * mm, "end": v(-46.81, 10.82) * mm});
            skLineSegment(sketch, "E1861", {"start": v(-46.81, 10.82) * mm, "end": v(-46.6, 10.77) * mm});
            skLineSegment(sketch, "E1862", {"start": v(-46.6, 10.77) * mm, "end": v(-46.39, 10.72) * mm});
            skLineSegment(sketch, "E1863", {"start": v(-46.39, 10.72) * mm, "end": v(-46.18, 10.67) * mm});
            skLineSegment(sketch, "E1864", {"start": v(-46.18, 10.67) * mm, "end": v(-45.97, 10.62) * mm});
            skLineSegment(sketch, "E1865", {"start": v(-45.97, 10.62) * mm, "end": v(-45.76, 10.57) * mm});
            skLineSegment(sketch, "E1866", {"start": v(-45.76, 10.57) * mm, "end": v(-45.55, 10.52) * mm});
            skLineSegment(sketch, "E1867", {"start": v(-45.55, 10.52) * mm, "end": v(-45.33, 10.47) * mm});
            skLineSegment(sketch, "E1868", {"start": v(-45.33, 10.47) * mm, "end": v(-45.12, 10.42) * mm});
            skLineSegment(sketch, "E1869", {"start": v(-45.12, 10.42) * mm, "end": v(-44.91, 10.37) * mm});
            skLineSegment(sketch, "E1870", {"start": v(-44.91, 10.37) * mm, "end": v(-44.7, 10.32) * mm});
            skLineSegment(sketch, "E1871", {"start": v(-44.7, 10.32) * mm, "end": v(-44.5, 10.27) * mm});
            skLineSegment(sketch, "E1872", {"start": v(-44.5, 10.27) * mm, "end": v(-44.28, 10.22) * mm});
            skLineSegment(sketch, "E1873", {"start": v(-44.28, 10.22) * mm, "end": v(-44.07, 10.17) * mm});
            skLineSegment(sketch, "E1874", {"start": v(-44.07, 10.17) * mm, "end": v(-43.86, 10.12) * mm});
            skLineSegment(sketch, "E1875", {"start": v(-43.86, 10.12) * mm, "end": v(-43.65, 10.07) * mm});
            skLineSegment(sketch, "E1876", {"start": v(-43.65, 10.07) * mm, "end": v(-43.7, 9.85) * mm});
            skLineSegment(sketch, "E1877", {"start": v(-43.7, 9.85) * mm, "end": v(-43.74, 9.64) * mm});
            skLineSegment(sketch, "E1878", {"start": v(-43.74, 9.64) * mm, "end": v(-43.78, 9.42) * mm});
            skLineSegment(sketch, "E1879", {"start": v(-43.78, 9.42) * mm, "end": v(-43.83, 9.2) * mm});
            skLineSegment(sketch, "E1880", {"start": v(-43.83, 9.2) * mm, "end": v(-43.88, 8.98) * mm});
            skLineSegment(sketch, "E1881", {"start": v(-43.88, 8.98) * mm, "end": v(-43.92, 8.77) * mm});
            skLineSegment(sketch, "E1882", {"start": v(-43.92, 8.77) * mm, "end": v(-43.97, 8.55) * mm});
            skLineSegment(sketch, "E1883", {"start": v(-43.97, 8.55) * mm, "end": v(-44.01, 8.33) * mm});
            skLineSegment(sketch, "E1884", {"start": v(-44.01, 8.33) * mm, "end": v(-44.06, 8.11) * mm});
            skLineSegment(sketch, "E1885", {"start": v(-44.06, 8.11) * mm, "end": v(-44.1, 7.94) * mm});
            skLineSegment(sketch, "E1886", {"start": v(-44.1, 7.94) * mm, "end": v(-44.3, 7.97) * mm});
            skLineSegment(sketch, "E1887", {"start": v(-44.3, 7.97) * mm, "end": v(-44.52, 8.01) * mm});
            skLineSegment(sketch, "E1888", {"start": v(-44.52, 8.01) * mm, "end": v(-44.73, 8.05) * mm});
            skLineSegment(sketch, "E1889", {"start": v(-44.73, 8.05) * mm, "end": v(-44.95, 8.1) * mm});
            skLineSegment(sketch, "E1890", {"start": v(-44.95, 8.1) * mm, "end": v(-45.16, 8.13) * mm});
            skLineSegment(sketch, "E1891", {"start": v(-45.16, 8.13) * mm, "end": v(-45.37, 8.17) * mm});
            skLineSegment(sketch, "E1892", {"start": v(-45.37, 8.17) * mm, "end": v(-45.59, 8.2) * mm});
            skLineSegment(sketch, "E1893", {"start": v(-45.59, 8.2) * mm, "end": v(-45.8, 8.25) * mm});
            skLineSegment(sketch, "E1894", {"start": v(-45.8, 8.25) * mm, "end": v(-46.01, 8.29) * mm});
            skLineSegment(sketch, "E1895", {"start": v(-46.01, 8.29) * mm, "end": v(-46.23, 8.33) * mm});
            skLineSegment(sketch, "E1896", {"start": v(-46.23, 8.33) * mm, "end": v(-46.44, 8.37) * mm});
            skLineSegment(sketch, "E1897", {"start": v(-46.44, 8.37) * mm, "end": v(-46.65, 8.4) * mm});
            skLineSegment(sketch, "E1898", {"start": v(-46.65, 8.4) * mm, "end": v(-46.87, 8.44) * mm});
            skLineSegment(sketch, "E1899", {"start": v(-46.87, 8.44) * mm, "end": v(-47.08, 8.48) * mm});
            skLineSegment(sketch, "E1900", {"start": v(-47.08, 8.48) * mm, "end": v(-47.3, 8.52) * mm});
            skLineSegment(sketch, "E1901", {"start": v(-47.3, 8.52) * mm, "end": v(-47.41, 8.53) * mm});
            skLineSegment(sketch, "E1902", {"start": v(-47.41, 8.53) * mm, "end": v(-47.62, 8.51) * mm});
            skLineSegment(sketch, "E1903", {"start": v(-47.62, 8.51) * mm, "end": v(-47.8, 8.44) * mm});
            skLineSegment(sketch, "E1904", {"start": v(-47.8, 8.44) * mm, "end": v(-47.97, 8.31) * mm});
            skLineSegment(sketch, "E1905", {"start": v(-47.97, 8.31) * mm, "end": v(-48.1, 8.15) * mm});
            skLineSegment(sketch, "E1906", {"start": v(-48.1, 8.15) * mm, "end": v(-48.17, 7.97) * mm});
            skLineSegment(sketch, "E1907", {"start": v(-48.17, 7.97) * mm, "end": v(-48.2, 7.76) * mm});
            skLineSegment(sketch, "E1908", {"start": v(-48.2, 7.76) * mm, "end": v(-48.18, 7.56) * mm});
            skLineSegment(sketch, "E1909", {"start": v(-48.18, 7.56) * mm, "end": v(-48.1, 7.37) * mm});
            skLineSegment(sketch, "E1910", {"start": v(-48.1, 7.37) * mm, "end": v(-47.98, 7.21) * mm});
            skLineSegment(sketch, "E1911", {"start": v(-47.98, 7.21) * mm, "end": v(-47.82, 7.09) * mm});
            skLineSegment(sketch, "E1912", {"start": v(-47.82, 7.09) * mm, "end": v(-47.63, 7) * mm});
            skLineSegment(sketch, "E1913", {"start": v(-47.63, 7) * mm, "end": v(-47.4, 6.97) * mm});
            skLineSegment(sketch, "E1914", {"start": v(-47.4, 6.97) * mm, "end": v(-47.19, 6.94) * mm});
            skLineSegment(sketch, "E1915", {"start": v(-47.19, 6.94) * mm, "end": v(-46.97, 6.9) * mm});
            skLineSegment(sketch, "E1916", {"start": v(-46.97, 6.9) * mm, "end": v(-46.75, 6.87) * mm});
            skLineSegment(sketch, "E1917", {"start": v(-46.75, 6.87) * mm, "end": v(-46.53, 6.84) * mm});
            skLineSegment(sketch, "E1918", {"start": v(-46.53, 6.84) * mm, "end": v(-46.3, 6.8) * mm});
            skLineSegment(sketch, "E1919", {"start": v(-46.3, 6.8) * mm, "end": v(-46.09, 6.77) * mm});
            skLineSegment(sketch, "E1920", {"start": v(-46.09, 6.77) * mm, "end": v(-45.87, 6.74) * mm});
            skLineSegment(sketch, "E1921", {"start": v(-45.87, 6.74) * mm, "end": v(-45.65, 6.7) * mm});
            skLineSegment(sketch, "E1922", {"start": v(-45.65, 6.7) * mm, "end": v(-45.4, 6.67) * mm});
            skLineSegment(sketch, "E1923", {"start": v(-45.4, 6.67) * mm, "end": v(-45.2, 6.64) * mm});
            skLineSegment(sketch, "E1924", {"start": v(-45.2, 6.64) * mm, "end": v(-44.98, 6.6) * mm});
            skLineSegment(sketch, "E1925", {"start": v(-44.98, 6.6) * mm, "end": v(-44.76, 6.57) * mm});
            skLineSegment(sketch, "E1926", {"start": v(-44.76, 6.57) * mm, "end": v(-44.55, 6.54) * mm});
            skLineSegment(sketch, "E1927", {"start": v(-44.55, 6.54) * mm, "end": v(-44.33, 6.51) * mm});
            skLineSegment(sketch, "E1928", {"start": v(-44.33, 6.51) * mm, "end": v(-44.36, 6.29) * mm});
            skLineSegment(sketch, "E1929", {"start": v(-44.36, 6.29) * mm, "end": v(-44.39, 6.07) * mm});
            skLineSegment(sketch, "E1930", {"start": v(-44.39, 6.07) * mm, "end": v(-44.42, 5.85) * mm});
            skLineSegment(sketch, "E1931", {"start": v(-44.42, 5.85) * mm, "end": v(-44.44, 5.63) * mm});
            skLineSegment(sketch, "E1932", {"start": v(-44.44, 5.63) * mm, "end": v(-44.47, 5.4) * mm});
            skLineSegment(sketch, "E1933", {"start": v(-44.47, 5.4) * mm, "end": v(-44.5, 5.18) * mm});
            skLineSegment(sketch, "E1934", {"start": v(-44.5, 5.18) * mm, "end": v(-44.53, 4.96) * mm});
            skLineSegment(sketch, "E1935", {"start": v(-44.53, 4.96) * mm, "end": v(-44.55, 4.74) * mm});
            skLineSegment(sketch, "E1936", {"start": v(-44.55, 4.74) * mm, "end": v(-44.58, 4.52) * mm});
            skLineSegment(sketch, "E1937", {"start": v(-44.58, 4.52) * mm, "end": v(-44.6, 4.34) * mm});
            skLineSegment(sketch, "E1938", {"start": v(-44.6, 4.34) * mm, "end": v(-44.82, 4.37) * mm});
            skLineSegment(sketch, "E1939", {"start": v(-44.82, 4.37) * mm, "end": v(-45.03, 4.39) * mm});
            skLineSegment(sketch, "E1940", {"start": v(-45.03, 4.39) * mm, "end": v(-45.25, 4.4) * mm});
            skLineSegment(sketch, "E1941", {"start": v(-45.25, 4.4) * mm, "end": v(-45.47, 4.43) * mm});
            skLineSegment(sketch, "E1942", {"start": v(-45.47, 4.43) * mm, "end": v(-45.68, 4.45) * mm});
            skLineSegment(sketch, "E1943", {"start": v(-45.68, 4.45) * mm, "end": v(-45.9, 4.47) * mm});
            skLineSegment(sketch, "E1944", {"start": v(-45.9, 4.47) * mm, "end": v(-46.11, 4.5) * mm});
            skLineSegment(sketch, "E1945", {"start": v(-46.11, 4.5) * mm, "end": v(-46.33, 4.52) * mm});
            skLineSegment(sketch, "E1946", {"start": v(-46.33, 4.52) * mm, "end": v(-46.54, 4.54) * mm});
            skLineSegment(sketch, "E1947", {"start": v(-46.54, 4.54) * mm, "end": v(-46.76, 4.56) * mm});
            skLineSegment(sketch, "E1948", {"start": v(-46.76, 4.56) * mm, "end": v(-46.98, 4.58) * mm});
            skLineSegment(sketch, "E1949", {"start": v(-46.98, 4.58) * mm, "end": v(-47.2, 4.6) * mm});
            skLineSegment(sketch, "E1950", {"start": v(-47.2, 4.6) * mm, "end": v(-47.4, 4.62) * mm});
            skLineSegment(sketch, "E1951", {"start": v(-47.4, 4.62) * mm, "end": v(-47.62, 4.64) * mm});
            skLineSegment(sketch, "E1952", {"start": v(-47.62, 4.64) * mm, "end": v(-47.84, 4.67) * mm});
            skLineSegment(sketch, "E1953", {"start": v(-47.84, 4.67) * mm, "end": v(-47.92, 4.67) * mm});
            skLineSegment(sketch, "E1954", {"start": v(-47.92, 4.67) * mm, "end": v(-48.12, 4.64) * mm});
            skLineSegment(sketch, "E1955", {"start": v(-48.12, 4.64) * mm, "end": v(-48.3, 4.56) * mm});
            skLineSegment(sketch, "E1956", {"start": v(-48.3, 4.56) * mm, "end": v(-48.47, 4.43) * mm});
            skLineSegment(sketch, "E1957", {"start": v(-48.47, 4.43) * mm, "end": v(-48.59, 4.27) * mm});
            skLineSegment(sketch, "E1958", {"start": v(-48.59, 4.27) * mm, "end": v(-48.66, 4.08) * mm});
            skLineSegment(sketch, "E1959", {"start": v(-48.66, 4.08) * mm, "end": v(-48.68, 3.88) * mm});
            skLineSegment(sketch, "E1960", {"start": v(-48.68, 3.88) * mm, "end": v(-48.65, 3.67) * mm});
            skLineSegment(sketch, "E1961", {"start": v(-48.65, 3.67) * mm, "end": v(-48.57, 3.49) * mm});
            skLineSegment(sketch, "E1962", {"start": v(-48.57, 3.49) * mm, "end": v(-48.44, 3.33) * mm});
            skLineSegment(sketch, "E1963", {"start": v(-48.44, 3.33) * mm, "end": v(-48.28, 3.21) * mm});
            skLineSegment(sketch, "E1964", {"start": v(-48.28, 3.21) * mm, "end": v(-48.09, 3.14) * mm});
            skLineSegment(sketch, "E1965", {"start": v(-48.09, 3.14) * mm, "end": v(-47.86, 3.11) * mm});
            skLineSegment(sketch, "E1966", {"start": v(-47.86, 3.11) * mm, "end": v(-47.64, 3.1) * mm});
            skLineSegment(sketch, "E1967", {"start": v(-47.64, 3.1) * mm, "end": v(-47.43, 3.08) * mm});
            skLineSegment(sketch, "E1968", {"start": v(-47.43, 3.08) * mm, "end": v(-47.2, 3.07) * mm});
            skLineSegment(sketch, "E1969", {"start": v(-47.2, 3.07) * mm, "end": v(-47, 3.05) * mm});
            skLineSegment(sketch, "E1970", {"start": v(-47, 3.05) * mm, "end": v(-46.78, 3.04) * mm});
            skLineSegment(sketch, "E1971", {"start": v(-46.78, 3.04) * mm, "end": v(-46.56, 3.03) * mm});
            skLineSegment(sketch, "E1972", {"start": v(-46.56, 3.03) * mm, "end": v(-46.34, 3.01) * mm});
            skLineSegment(sketch, "E1973", {"start": v(-46.34, 3.01) * mm, "end": v(-46.13, 3) * mm});
            skLineSegment(sketch, "E1974", {"start": v(-46.13, 3) * mm, "end": v(-45.91, 2.98) * mm});
            skLineSegment(sketch, "E1975", {"start": v(-45.91, 2.98) * mm, "end": v(-45.7, 2.97) * mm});
            skLineSegment(sketch, "E1976", {"start": v(-45.7, 2.97) * mm, "end": v(-45.48, 2.95) * mm});
            skLineSegment(sketch, "E1977", {"start": v(-45.48, 2.95) * mm, "end": v(-45.26, 2.94) * mm});
            skLineSegment(sketch, "E1978", {"start": v(-45.26, 2.94) * mm, "end": v(-45.05, 2.93) * mm});
            skLineSegment(sketch, "E1979", {"start": v(-45.05, 2.93) * mm, "end": v(-44.83, 2.91) * mm});
            skLineSegment(sketch, "E1980", {"start": v(-44.83, 2.91) * mm, "end": v(-44.72, 2.9) * mm});
            skLineSegment(sketch, "E1981", {"start": v(-44.72, 2.9) * mm, "end": v(-44.73, 2.68) * mm});
            skLineSegment(sketch, "E1982", {"start": v(-44.73, 2.68) * mm, "end": v(-44.74, 2.46) * mm});
            skLineSegment(sketch, "E1983", {"start": v(-44.74, 2.46) * mm, "end": v(-44.75, 2.24) * mm});
            skLineSegment(sketch, "E1984", {"start": v(-44.75, 2.24) * mm, "end": v(-44.76, 2.01) * mm});
            skLineSegment(sketch, "E1985", {"start": v(-44.76, 2.01) * mm, "end": v(-44.77, 1.8) * mm});
            skLineSegment(sketch, "E1986", {"start": v(-44.77, 1.8) * mm, "end": v(-44.78, 1.57) * mm});
            skLineSegment(sketch, "E1987", {"start": v(-44.78, 1.57) * mm, "end": v(-44.79, 1.35) * mm});
            skLineSegment(sketch, "E1988", {"start": v(-44.79, 1.35) * mm, "end": v(-44.8, 1.12) * mm});
            skLineSegment(sketch, "E1989", {"start": v(-44.8, 1.12) * mm, "end": v(-44.8, 0.9) * mm});
            skLineSegment(sketch, "E1990", {"start": v(-44.8, 0.9) * mm, "end": v(-44.81, 0.72) * mm});
            skLineSegment(sketch, "E1991", {"start": v(-44.81, 0.72) * mm, "end": v(-45.03, 0.73) * mm});
            skLineSegment(sketch, "E1992", {"start": v(-45.03, 0.73) * mm, "end": v(-45.25, 0.73) * mm});
            skLineSegment(sketch, "E1993", {"start": v(-45.25, 0.73) * mm, "end": v(-45.46, 0.73) * mm});
            skLineSegment(sketch, "E1994", {"start": v(-45.46, 0.73) * mm, "end": v(-45.68, 0.74) * mm});
            skLineSegment(sketch, "E1995", {"start": v(-45.68, 0.74) * mm, "end": v(-45.9, 0.74) * mm});
            skLineSegment(sketch, "E1996", {"start": v(-45.9, 0.74) * mm, "end": v(-46.11, 0.74) * mm});
            skLineSegment(sketch, "E1997", {"start": v(-46.11, 0.74) * mm, "end": v(-46.33, 0.75) * mm});
            skLineSegment(sketch, "E1998", {"start": v(-46.33, 0.75) * mm, "end": v(-46.55, 0.75) * mm});
            skLineSegment(sketch, "E1999", {"start": v(-46.55, 0.75) * mm, "end": v(-46.76, 0.75) * mm});
            skLineSegment(sketch, "E2000", {"start": v(-46.76, 0.75) * mm, "end": v(-46.98, 0.76) * mm});
            skLineSegment(sketch, "E2001", {"start": v(-46.98, 0.76) * mm, "end": v(-47.2, 0.76) * mm});
            skLineSegment(sketch, "E2002", {"start": v(-47.2, 0.76) * mm, "end": v(-47.41, 0.76) * mm});
            skLineSegment(sketch, "E2003", {"start": v(-47.41, 0.76) * mm, "end": v(-47.63, 0.77) * mm});
            skLineSegment(sketch, "E2004", {"start": v(-47.63, 0.77) * mm, "end": v(-47.85, 0.77) * mm});
            skLineSegment(sketch, "E2005", {"start": v(-47.85, 0.77) * mm, "end": v(-48.06, 0.78) * mm});
            skLineSegment(sketch, "E2006", {"start": v(-48.06, 0.78) * mm, "end": v(-48.26, 0.75) * mm});
            skLineSegment(sketch, "E2007", {"start": v(-48.26, 0.75) * mm, "end": v(-48.45, 0.67) * mm});
            skLineSegment(sketch, "E2008", {"start": v(-48.45, 0.67) * mm, "end": v(-48.62, 0.55) * mm});
            skLineSegment(sketch, "E2009", {"start": v(-48.62, 0.55) * mm, "end": v(-48.74, 0.39) * mm});
            skLineSegment(sketch, "E2010", {"start": v(-48.74, 0.39) * mm, "end": v(-48.82, 0.2) * mm});
            skLineSegment(sketch, "E2011", {"start": v(-48.82, 0.2) * mm, "end": v(-48.84, 0) * mm});
            skLineSegment(sketch, "E2012", {"start": v(-48.84, 0) * mm, "end": v(-48.82, -0.2) * mm});
            skLineSegment(sketch, "E2013", {"start": v(-48.82, -0.2) * mm, "end": v(-48.74, -0.39) * mm});
            skLineSegment(sketch, "E2014", {"start": v(-48.74, -0.39) * mm, "end": v(-48.62, -0.55) * mm});
            skLineSegment(sketch, "E2015", {"start": v(-48.62, -0.55) * mm, "end": v(-48.45, -0.67) * mm});
            skLineSegment(sketch, "E2016", {"start": v(-48.45, -0.67) * mm, "end": v(-48.26, -0.75) * mm});
            skLineSegment(sketch, "E2017", {"start": v(-48.26, -0.75) * mm, "end": v(-48.06, -0.78) * mm});
            skLineSegment(sketch, "E2018", {"start": v(-48.06, -0.78) * mm, "end": v(-47.85, -0.77) * mm});
            skLineSegment(sketch, "E2019", {"start": v(-47.85, -0.77) * mm, "end": v(-47.63, -0.77) * mm});
            skLineSegment(sketch, "E2020", {"start": v(-47.63, -0.77) * mm, "end": v(-47.41, -0.76) * mm});
            skLineSegment(sketch, "E2021", {"start": v(-47.41, -0.76) * mm, "end": v(-47.2, -0.76) * mm});
            skLineSegment(sketch, "E2022", {"start": v(-47.2, -0.76) * mm, "end": v(-46.98, -0.76) * mm});
            skLineSegment(sketch, "E2023", {"start": v(-46.98, -0.76) * mm, "end": v(-46.76, -0.75) * mm});
            skLineSegment(sketch, "E2024", {"start": v(-46.76, -0.75) * mm, "end": v(-46.55, -0.75) * mm});
            skLineSegment(sketch, "E2025", {"start": v(-46.55, -0.75) * mm, "end": v(-46.33, -0.75) * mm});
            skLineSegment(sketch, "E2026", {"start": v(-46.33, -0.75) * mm, "end": v(-46.11, -0.74) * mm});
            skLineSegment(sketch, "E2027", {"start": v(-46.11, -0.74) * mm, "end": v(-45.9, -0.74) * mm});
            skLineSegment(sketch, "E2028", {"start": v(-45.9, -0.74) * mm, "end": v(-45.68, -0.74) * mm});
            skLineSegment(sketch, "E2029", {"start": v(-45.68, -0.74) * mm, "end": v(-45.46, -0.73) * mm});
            skLineSegment(sketch, "E2030", {"start": v(-45.46, -0.73) * mm, "end": v(-45.25, -0.73) * mm});
            skLineSegment(sketch, "E2031", {"start": v(-45.25, -0.73) * mm, "end": v(-45.03, -0.73) * mm});
            skLineSegment(sketch, "E2032", {"start": v(-45.03, -0.73) * mm, "end": v(-44.81, -0.72) * mm});
            skLineSegment(sketch, "E2033", {"start": v(-44.81, -0.72) * mm, "end": v(-44.8, -0.94) * mm});
            skLineSegment(sketch, "E2034", {"start": v(-44.8, -0.94) * mm, "end": v(-44.8, -1.17) * mm});
            skLineSegment(sketch, "E2035", {"start": v(-44.8, -1.17) * mm, "end": v(-44.79, -1.39) * mm});
            skLineSegment(sketch, "E2036", {"start": v(-44.79, -1.39) * mm, "end": v(-44.78, -1.61) * mm});
            skLineSegment(sketch, "E2037", {"start": v(-44.78, -1.61) * mm, "end": v(-44.77, -1.83) * mm});
            skLineSegment(sketch, "E2038", {"start": v(-44.77, -1.83) * mm, "end": v(-44.76, -2.06) * mm});
            skLineSegment(sketch, "E2039", {"start": v(-44.76, -2.06) * mm, "end": v(-44.75, -2.28) * mm});
            skLineSegment(sketch, "E2040", {"start": v(-44.75, -2.28) * mm, "end": v(-44.74, -2.5) * mm});
            skLineSegment(sketch, "E2041", {"start": v(-44.74, -2.5) * mm, "end": v(-44.73, -2.72) * mm});
            skLineSegment(sketch, "E2042", {"start": v(-44.73, -2.72) * mm, "end": v(-44.72, -2.9) * mm});
            skLineSegment(sketch, "E2043", {"start": v(-44.72, -2.9) * mm, "end": v(-44.94, -2.92) * mm});
            skLineSegment(sketch, "E2044", {"start": v(-44.94, -2.92) * mm, "end": v(-45.16, -2.93) * mm});
            skLineSegment(sketch, "E2045", {"start": v(-45.16, -2.93) * mm, "end": v(-45.37, -2.95) * mm});
            skLineSegment(sketch, "E2046", {"start": v(-45.37, -2.95) * mm, "end": v(-45.59, -2.96) * mm});
            skLineSegment(sketch, "E2047", {"start": v(-45.59, -2.96) * mm, "end": v(-45.8, -2.98) * mm});
            skLineSegment(sketch, "E2048", {"start": v(-45.8, -2.98) * mm, "end": v(-46.02, -3) * mm});
            skLineSegment(sketch, "E2049", {"start": v(-46.02, -3) * mm, "end": v(-46.24, -3) * mm});
            skLineSegment(sketch, "E2050", {"start": v(-46.24, -3) * mm, "end": v(-46.45, -3.02) * mm});
            skLineSegment(sketch, "E2051", {"start": v(-46.45, -3.02) * mm, "end": v(-46.67, -3.03) * mm});
            skLineSegment(sketch, "E2052", {"start": v(-46.67, -3.03) * mm, "end": v(-46.88, -3.05) * mm});
            skLineSegment(sketch, "E2053", {"start": v(-46.88, -3.05) * mm, "end": v(-47.1, -3.06) * mm});
            skLineSegment(sketch, "E2054", {"start": v(-47.1, -3.06) * mm, "end": v(-47.32, -3.08) * mm});
            skLineSegment(sketch, "E2055", {"start": v(-47.32, -3.08) * mm, "end": v(-47.53, -3.1) * mm});
            skLineSegment(sketch, "E2056", {"start": v(-47.53, -3.1) * mm, "end": v(-47.75, -3.1) * mm});
            skLineSegment(sketch, "E2057", {"start": v(-47.75, -3.1) * mm, "end": v(-47.97, -3.12) * mm});
            skLineSegment(sketch, "E2058", {"start": v(-47.97, -3.12) * mm, "end": v(-48.17, -3.16) * mm});
            skLineSegment(sketch, "E2059", {"start": v(-48.17, -3.16) * mm, "end": v(-48.35, -3.25) * mm});
            skLineSegment(sketch, "E2060", {"start": v(-48.35, -3.25) * mm, "end": v(-48.5, -3.39) * mm});
            skLineSegment(sketch, "E2061", {"start": v(-48.5, -3.39) * mm, "end": v(-48.6, -3.56) * mm});
            skLineSegment(sketch, "E2062", {"start": v(-48.6, -3.56) * mm, "end": v(-48.67, -3.75) * mm});
            skLineSegment(sketch, "E2063", {"start": v(-48.67, -3.75) * mm, "end": v(-48.68, -3.96) * mm});
            skLineSegment(sketch, "E2064", {"start": v(-48.68, -3.96) * mm, "end": v(-48.64, -4.16) * mm});
            skLineSegment(sketch, "E2065", {"start": v(-48.64, -4.16) * mm, "end": v(-48.54, -4.34) * mm});
            skLineSegment(sketch, "E2066", {"start": v(-48.54, -4.34) * mm, "end": v(-48.4, -4.49) * mm});
            skLineSegment(sketch, "E2067", {"start": v(-48.4, -4.49) * mm, "end": v(-48.24, -4.6) * mm});
            skLineSegment(sketch, "E2068", {"start": v(-48.24, -4.6) * mm, "end": v(-48.04, -4.66) * mm});
            skLineSegment(sketch, "E2069", {"start": v(-48.04, -4.66) * mm, "end": v(-47.84, -4.67) * mm});
            skLineSegment(sketch, "E2070", {"start": v(-47.84, -4.67) * mm, "end": v(-47.62, -4.64) * mm});
            skLineSegment(sketch, "E2071", {"start": v(-47.62, -4.64) * mm, "end": v(-47.4, -4.62) * mm});
            skLineSegment(sketch, "E2072", {"start": v(-47.4, -4.62) * mm, "end": v(-47.2, -4.6) * mm});
            skLineSegment(sketch, "E2073", {"start": v(-47.2, -4.6) * mm, "end": v(-46.98, -4.58) * mm});
            skLineSegment(sketch, "E2074", {"start": v(-46.98, -4.58) * mm, "end": v(-46.76, -4.56) * mm});
            skLineSegment(sketch, "E2075", {"start": v(-46.76, -4.56) * mm, "end": v(-46.54, -4.54) * mm});
            skLineSegment(sketch, "E2076", {"start": v(-46.54, -4.54) * mm, "end": v(-46.33, -4.52) * mm});
            skLineSegment(sketch, "E2077", {"start": v(-46.33, -4.52) * mm, "end": v(-46.11, -4.5) * mm});
            skLineSegment(sketch, "E2078", {"start": v(-46.11, -4.5) * mm, "end": v(-45.9, -4.47) * mm});
            skLineSegment(sketch, "E2079", {"start": v(-45.9, -4.47) * mm, "end": v(-45.68, -4.45) * mm});
            skLineSegment(sketch, "E2080", {"start": v(-45.68, -4.45) * mm, "end": v(-45.47, -4.43) * mm});
            skLineSegment(sketch, "E2081", {"start": v(-45.47, -4.43) * mm, "end": v(-45.25, -4.4) * mm});
            skLineSegment(sketch, "E2082", {"start": v(-45.25, -4.4) * mm, "end": v(-45.03, -4.39) * mm});
            skLineSegment(sketch, "E2083", {"start": v(-45.03, -4.39) * mm, "end": v(-44.82, -4.37) * mm});
            skLineSegment(sketch, "E2084", {"start": v(-44.82, -4.37) * mm, "end": v(-44.6, -4.34) * mm});
            skLineSegment(sketch, "E2085", {"start": v(-44.6, -4.34) * mm, "end": v(-44.58, -4.56) * mm});
            skLineSegment(sketch, "E2086", {"start": v(-44.58, -4.56) * mm, "end": v(-44.55, -4.79) * mm});
            skLineSegment(sketch, "E2087", {"start": v(-44.55, -4.79) * mm, "end": v(-44.52, -5) * mm});
            skLineSegment(sketch, "E2088", {"start": v(-44.52, -5) * mm, "end": v(-44.5, -5.23) * mm});
            skLineSegment(sketch, "E2089", {"start": v(-44.5, -5.23) * mm, "end": v(-44.47, -5.45) * mm});
            skLineSegment(sketch, "E2090", {"start": v(-44.47, -5.45) * mm, "end": v(-44.44, -5.67) * mm});
            skLineSegment(sketch, "E2091", {"start": v(-44.44, -5.67) * mm, "end": v(-44.41, -5.9) * mm});
            skLineSegment(sketch, "E2092", {"start": v(-44.41, -5.9) * mm, "end": v(-44.38, -6.11) * mm});
            skLineSegment(sketch, "E2093", {"start": v(-44.38, -6.11) * mm, "end": v(-44.36, -6.33) * mm});
            skLineSegment(sketch, "E2094", {"start": v(-44.36, -6.33) * mm, "end": v(-44.33, -6.51) * mm});
            skLineSegment(sketch, "E2095", {"start": v(-44.33, -6.51) * mm, "end": v(-44.55, -6.54) * mm});
            skLineSegment(sketch, "E2096", {"start": v(-44.55, -6.54) * mm, "end": v(-44.76, -6.57) * mm});
            skLineSegment(sketch, "E2097", {"start": v(-44.76, -6.57) * mm, "end": v(-44.98, -6.6) * mm});
            skLineSegment(sketch, "E2098", {"start": v(-44.98, -6.6) * mm, "end": v(-45.2, -6.64) * mm});
            skLineSegment(sketch, "E2099", {"start": v(-45.2, -6.64) * mm, "end": v(-45.4, -6.67) * mm});
            skLineSegment(sketch, "E2100", {"start": v(-45.4, -6.67) * mm, "end": v(-45.62, -6.7) * mm});
            skLineSegment(sketch, "E2101", {"start": v(-45.62, -6.7) * mm, "end": v(-45.83, -6.74) * mm});
            skLineSegment(sketch, "E2102", {"start": v(-45.83, -6.74) * mm, "end": v(-46.05, -6.77) * mm});
            skLineSegment(sketch, "E2103", {"start": v(-46.05, -6.77) * mm, "end": v(-46.26, -6.8) * mm});
            skLineSegment(sketch, "E2104", {"start": v(-46.26, -6.8) * mm, "end": v(-46.48, -6.83) * mm});
            skLineSegment(sketch, "E2105", {"start": v(-46.48, -6.83) * mm, "end": v(-46.7, -6.86) * mm});
            skLineSegment(sketch, "E2106", {"start": v(-46.7, -6.86) * mm, "end": v(-46.9, -6.9) * mm});
            skLineSegment(sketch, "E2107", {"start": v(-46.9, -6.9) * mm, "end": v(-47.12, -6.93) * mm});
            skLineSegment(sketch, "E2108", {"start": v(-47.12, -6.93) * mm, "end": v(-47.33, -6.96) * mm});
            skLineSegment(sketch, "E2109", {"start": v(-47.33, -6.96) * mm, "end": v(-47.55, -7) * mm});
            skLineSegment(sketch, "E2110", {"start": v(-47.55, -7) * mm, "end": v(-47.74, -7.05) * mm});
            skLineSegment(sketch, "E2111", {"start": v(-47.74, -7.05) * mm, "end": v(-47.92, -7.16) * mm});
            skLineSegment(sketch, "E2112", {"start": v(-47.92, -7.16) * mm, "end": v(-48.06, -7.3) * mm});
            skLineSegment(sketch, "E2113", {"start": v(-48.06, -7.3) * mm, "end": v(-48.15, -7.49) * mm});
            skLineSegment(sketch, "E2114", {"start": v(-48.15, -7.49) * mm, "end": v(-48.2, -7.68) * mm});
            skLineSegment(sketch, "E2115", {"start": v(-48.2, -7.68) * mm, "end": v(-48.2, -7.89) * mm});
            skLineSegment(sketch, "E2116", {"start": v(-48.2, -7.89) * mm, "end": v(-48.13, -8.08) * mm});
            skLineSegment(sketch, "E2117", {"start": v(-48.13, -8.08) * mm, "end": v(-48.02, -8.25) * mm});
            skLineSegment(sketch, "E2118", {"start": v(-48.02, -8.25) * mm, "end": v(-47.87, -8.4) * mm});
            skLineSegment(sketch, "E2119", {"start": v(-47.87, -8.4) * mm, "end": v(-47.7, -8.49) * mm});
            skLineSegment(sketch, "E2120", {"start": v(-47.7, -8.49) * mm, "end": v(-47.5, -8.53) * mm});
            skLineSegment(sketch, "E2121", {"start": v(-47.5, -8.53) * mm, "end": v(-47.3, -8.52) * mm});
            skLineSegment(sketch, "E2122", {"start": v(-47.3, -8.52) * mm, "end": v(-47.08, -8.48) * mm});
            skLineSegment(sketch, "E2123", {"start": v(-47.08, -8.48) * mm, "end": v(-46.87, -8.44) * mm});
            skLineSegment(sketch, "E2124", {"start": v(-46.87, -8.44) * mm, "end": v(-46.65, -8.4) * mm});
            skLineSegment(sketch, "E2125", {"start": v(-46.65, -8.4) * mm, "end": v(-46.44, -8.37) * mm});
            skLineSegment(sketch, "E2126", {"start": v(-46.44, -8.37) * mm, "end": v(-46.23, -8.33) * mm});
            skLineSegment(sketch, "E2127", {"start": v(-46.23, -8.33) * mm, "end": v(-46.01, -8.29) * mm});
            skLineSegment(sketch, "E2128", {"start": v(-46.01, -8.29) * mm, "end": v(-45.8, -8.25) * mm});
            skLineSegment(sketch, "E2129", {"start": v(-45.8, -8.25) * mm, "end": v(-45.59, -8.2) * mm});
            skLineSegment(sketch, "E2130", {"start": v(-45.59, -8.2) * mm, "end": v(-45.37, -8.17) * mm});
            skLineSegment(sketch, "E2131", {"start": v(-45.37, -8.17) * mm, "end": v(-45.16, -8.13) * mm});
            skLineSegment(sketch, "E2132", {"start": v(-45.16, -8.13) * mm, "end": v(-44.95, -8.1) * mm});
            skLineSegment(sketch, "E2133", {"start": v(-44.95, -8.1) * mm, "end": v(-44.73, -8.05) * mm});
            skLineSegment(sketch, "E2134", {"start": v(-44.73, -8.05) * mm, "end": v(-44.52, -8.01) * mm});
            skLineSegment(sketch, "E2135", {"start": v(-44.52, -8.01) * mm, "end": v(-44.3, -7.97) * mm});
            skLineSegment(sketch, "E2136", {"start": v(-44.3, -7.97) * mm, "end": v(-44.1, -7.94) * mm});
            skLineSegment(sketch, "E2137", {"start": v(-44.1, -7.94) * mm, "end": v(-44.05, -8.15) * mm});
            skLineSegment(sketch, "E2138", {"start": v(-44.05, -8.15) * mm, "end": v(-44, -8.37) * mm});
            skLineSegment(sketch, "E2139", {"start": v(-44, -8.37) * mm, "end": v(-43.96, -8.59) * mm});
            skLineSegment(sketch, "E2140", {"start": v(-43.96, -8.59) * mm, "end": v(-43.91, -8.8) * mm});
            skLineSegment(sketch, "E2141", {"start": v(-43.91, -8.8) * mm, "end": v(-43.87, -9.03) * mm});
            skLineSegment(sketch, "E2142", {"start": v(-43.87, -9.03) * mm, "end": v(-43.82, -9.24) * mm});
            skLineSegment(sketch, "E2143", {"start": v(-43.82, -9.24) * mm, "end": v(-43.78, -9.46) * mm});
            skLineSegment(sketch, "E2144", {"start": v(-43.78, -9.46) * mm, "end": v(-43.73, -9.68) * mm});
            skLineSegment(sketch, "E2145", {"start": v(-43.73, -9.68) * mm, "end": v(-43.68, -9.9) * mm});
            skLineSegment(sketch, "E2146", {"start": v(-43.68, -9.9) * mm, "end": v(-43.65, -10.07) * mm});
            skLineSegment(sketch, "E2147", {"start": v(-43.65, -10.07) * mm, "end": v(-43.86, -10.12) * mm});
            skLineSegment(sketch, "E2148", {"start": v(-43.86, -10.12) * mm, "end": v(-44.07, -10.17) * mm});
            skLineSegment(sketch, "E2149", {"start": v(-44.07, -10.17) * mm, "end": v(-44.28, -10.22) * mm});
            skLineSegment(sketch, "E2150", {"start": v(-44.28, -10.22) * mm, "end": v(-44.5, -10.27) * mm});
            skLineSegment(sketch, "E2151", {"start": v(-44.5, -10.27) * mm, "end": v(-44.7, -10.32) * mm});
            skLineSegment(sketch, "E2152", {"start": v(-44.7, -10.32) * mm, "end": v(-44.91, -10.37) * mm});
            skLineSegment(sketch, "E2153", {"start": v(-44.91, -10.37) * mm, "end": v(-45.12, -10.42) * mm});
            skLineSegment(sketch, "E2154", {"start": v(-45.12, -10.42) * mm, "end": v(-45.33, -10.47) * mm});
            skLineSegment(sketch, "E2155", {"start": v(-45.33, -10.47) * mm, "end": v(-45.55, -10.52) * mm});
            skLineSegment(sketch, "E2156", {"start": v(-45.55, -10.52) * mm, "end": v(-45.76, -10.57) * mm});
            skLineSegment(sketch, "E2157", {"start": v(-45.76, -10.57) * mm, "end": v(-45.97, -10.62) * mm});
            skLineSegment(sketch, "E2158", {"start": v(-45.97, -10.62) * mm, "end": v(-46.18, -10.67) * mm});
            skLineSegment(sketch, "E2159", {"start": v(-46.18, -10.67) * mm, "end": v(-46.39, -10.72) * mm});
            skLineSegment(sketch, "E2160", {"start": v(-46.39, -10.72) * mm, "end": v(-46.6, -10.77) * mm});
            skLineSegment(sketch, "E2161", {"start": v(-46.6, -10.77) * mm, "end": v(-46.81, -10.82) * mm});
            skLineSegment(sketch, "E2162", {"start": v(-46.81, -10.82) * mm, "end": v(-47, -10.9) * mm});
            skLineSegment(sketch, "E2163", {"start": v(-47, -10.9) * mm, "end": v(-47.16, -11.01) * mm});
            skLineSegment(sketch, "E2164", {"start": v(-47.16, -11.01) * mm, "end": v(-47.3, -11.17) * mm});
            skLineSegment(sketch, "E2165", {"start": v(-47.3, -11.17) * mm, "end": v(-47.37, -11.36) * mm});
            skLineSegment(sketch, "E2166", {"start": v(-47.37, -11.36) * mm, "end": v(-47.4, -11.56) * mm});
            skLineSegment(sketch, "E2167", {"start": v(-47.4, -11.56) * mm, "end": v(-47.38, -11.76) * mm});
            skLineSegment(sketch, "E2168", {"start": v(-47.38, -11.76) * mm, "end": v(-47.3, -11.95) * mm});
            skLineSegment(sketch, "E2169", {"start": v(-47.3, -11.95) * mm, "end": v(-47.18, -12.11) * mm});
            skLineSegment(sketch, "E2170", {"start": v(-47.18, -12.11) * mm, "end": v(-47.02, -12.24) * mm});
            skLineSegment(sketch, "E2171", {"start": v(-47.02, -12.24) * mm, "end": v(-46.83, -12.32) * mm});
            skLineSegment(sketch, "E2172", {"start": v(-46.83, -12.32) * mm, "end": v(-46.63, -12.35) * mm});
            skLineSegment(sketch, "E2173", {"start": v(-46.63, -12.35) * mm, "end": v(-46.43, -12.32) * mm});
            skLineSegment(sketch, "E2174", {"start": v(-46.43, -12.32) * mm, "end": v(-46.22, -12.27) * mm});
            skLineSegment(sketch, "E2175", {"start": v(-46.22, -12.27) * mm, "end": v(-46.01, -12.2) * mm});
            skLineSegment(sketch, "E2176", {"start": v(-46.01, -12.2) * mm, "end": v(-45.8, -12.15) * mm});
            skLineSegment(sketch, "E2177", {"start": v(-45.8, -12.15) * mm, "end": v(-45.6, -12.1) * mm});
            skLineSegment(sketch, "E2178", {"start": v(-45.6, -12.1) * mm, "end": v(-45.38, -12.04) * mm});
            skLineSegment(sketch, "E2179", {"start": v(-45.38, -12.04) * mm, "end": v(-45.18, -11.98) * mm});
            skLineSegment(sketch, "E2180", {"start": v(-45.18, -11.98) * mm, "end": v(-44.97, -11.93) * mm});
            skLineSegment(sketch, "E2181", {"start": v(-44.97, -11.93) * mm, "end": v(-44.76, -11.87) * mm});
            skLineSegment(sketch, "E2182", {"start": v(-44.76, -11.87) * mm, "end": v(-44.55, -11.81) * mm});
            skLineSegment(sketch, "E2183", {"start": v(-44.55, -11.81) * mm, "end": v(-44.34, -11.76) * mm});
            skLineSegment(sketch, "E2184", {"start": v(-44.34, -11.76) * mm, "end": v(-44.13, -11.7) * mm});
            skLineSegment(sketch, "E2185", {"start": v(-44.13, -11.7) * mm, "end": v(-43.92, -11.64) * mm});
            skLineSegment(sketch, "E2186", {"start": v(-43.92, -11.64) * mm, "end": v(-43.71, -11.59) * mm});
            skLineSegment(sketch, "E2187", {"start": v(-43.71, -11.59) * mm, "end": v(-43.5, -11.53) * mm});
            skLineSegment(sketch, "E2188", {"start": v(-43.5, -11.53) * mm, "end": v(-43.3, -11.47) * mm});
            skLineSegment(sketch, "E2189", {"start": v(-43.3, -11.47) * mm, "end": v(-43.23, -11.69) * mm});
            skLineSegment(sketch, "E2190", {"start": v(-43.23, -11.69) * mm, "end": v(-43.17, -11.9) * mm});
            skLineSegment(sketch, "E2191", {"start": v(-43.17, -11.9) * mm, "end": v(-43.1, -12.11) * mm});
            skLineSegment(sketch, "E2192", {"start": v(-43.1, -12.11) * mm, "end": v(-43.04, -12.33) * mm});
            skLineSegment(sketch, "E2193", {"start": v(-43.04, -12.33) * mm, "end": v(-42.97, -12.54) * mm});
            skLineSegment(sketch, "E2194", {"start": v(-42.97, -12.54) * mm, "end": v(-42.91, -12.75) * mm});
            skLineSegment(sketch, "E2195", {"start": v(-42.91, -12.75) * mm, "end": v(-42.85, -12.97) * mm});
            skLineSegment(sketch, "E2196", {"start": v(-42.85, -12.97) * mm, "end": v(-42.78, -13.18) * mm});
            skLineSegment(sketch, "E2197", {"start": v(-42.78, -13.18) * mm, "end": v(-42.72, -13.4) * mm});
            skLineSegment(sketch, "E2198", {"start": v(-42.72, -13.4) * mm, "end": v(-42.67, -13.57) * mm});
            skLineSegment(sketch, "E2199", {"start": v(-42.67, -13.57) * mm, "end": v(-42.88, -13.63) * mm});
            skLineSegment(sketch, "E2200", {"start": v(-42.88, -13.63) * mm, "end": v(-43.08, -13.7) * mm});
            skLineSegment(sketch, "E2201", {"start": v(-43.08, -13.7) * mm, "end": v(-43.29, -13.77) * mm});
            skLineSegment(sketch, "E2202", {"start": v(-43.29, -13.77) * mm, "end": v(-43.5, -13.83) * mm});
            skLineSegment(sketch, "E2203", {"start": v(-43.5, -13.83) * mm, "end": v(-43.7, -13.9) * mm});
            skLineSegment(sketch, "E2204", {"start": v(-43.7, -13.9) * mm, "end": v(-43.9, -13.97) * mm});
            skLineSegment(sketch, "E2205", {"start": v(-43.9, -13.97) * mm, "end": v(-44.11, -14.03) * mm});
            skLineSegment(sketch, "E2206", {"start": v(-44.11, -14.03) * mm, "end": v(-44.32, -14.1) * mm});
            skLineSegment(sketch, "E2207", {"start": v(-44.32, -14.1) * mm, "end": v(-44.52, -14.17) * mm});
            skLineSegment(sketch, "E2208", {"start": v(-44.52, -14.17) * mm, "end": v(-44.73, -14.24) * mm});
            skLineSegment(sketch, "E2209", {"start": v(-44.73, -14.24) * mm, "end": v(-44.94, -14.3) * mm});
            skLineSegment(sketch, "E2210", {"start": v(-44.94, -14.3) * mm, "end": v(-45.14, -14.37) * mm});
            skLineSegment(sketch, "E2211", {"start": v(-45.14, -14.37) * mm, "end": v(-45.35, -14.44) * mm});
            skLineSegment(sketch, "E2212", {"start": v(-45.35, -14.44) * mm, "end": v(-45.55, -14.5) * mm});
            skLineSegment(sketch, "E2213", {"start": v(-45.55, -14.5) * mm, "end": v(-45.76, -14.57) * mm});
            skLineSegment(sketch, "E2214", {"start": v(-45.76, -14.57) * mm, "end": v(-45.94, -14.66) * mm});
            skLineSegment(sketch, "E2215", {"start": v(-45.94, -14.66) * mm, "end": v(-46.1, -14.8) * mm});
            skLineSegment(sketch, "E2216", {"start": v(-46.1, -14.8) * mm, "end": v(-46.21, -14.96) * mm});
            skLineSegment(sketch, "E2217", {"start": v(-46.21, -14.96) * mm, "end": v(-46.28, -15.16) * mm});
            skLineSegment(sketch, "E2218", {"start": v(-46.28, -15.16) * mm, "end": v(-46.29, -15.36) * mm});
            skLineSegment(sketch, "E2219", {"start": v(-46.29, -15.36) * mm, "end": v(-46.25, -15.56) * mm});
            skLineSegment(sketch, "E2220", {"start": v(-46.25, -15.56) * mm, "end": v(-46.16, -15.74) * mm});
            skLineSegment(sketch, "E2221", {"start": v(-46.16, -15.74) * mm, "end": v(-46.02, -15.9) * mm});
            skLineSegment(sketch, "E2222", {"start": v(-46.02, -15.9) * mm, "end": v(-45.85, -16) * mm});
            skLineSegment(sketch, "E2223", {"start": v(-45.85, -16) * mm, "end": v(-45.66, -16.07) * mm});
            skLineSegment(sketch, "E2224", {"start": v(-45.66, -16.07) * mm, "end": v(-45.46, -16.08) * mm});
            skLineSegment(sketch, "E2225", {"start": v(-45.46, -16.08) * mm, "end": v(-45.26, -16.04) * mm});
            skLineSegment(sketch, "E2226", {"start": v(-45.26, -16.04) * mm, "end": v(-45.05, -15.96) * mm});
            skLineSegment(sketch, "E2227", {"start": v(-45.05, -15.96) * mm, "end": v(-44.85, -15.9) * mm});
            skLineSegment(sketch, "E2228", {"start": v(-44.85, -15.9) * mm, "end": v(-44.65, -15.82) * mm});
            skLineSegment(sketch, "E2229", {"start": v(-44.65, -15.82) * mm, "end": v(-44.44, -15.74) * mm});
            skLineSegment(sketch, "E2230", {"start": v(-44.44, -15.74) * mm, "end": v(-44.24, -15.67) * mm});
            skLineSegment(sketch, "E2231", {"start": v(-44.24, -15.67) * mm, "end": v(-44.03, -15.6) * mm});
            skLineSegment(sketch, "E2232", {"start": v(-44.03, -15.6) * mm, "end": v(-43.83, -15.52) * mm});
            skLineSegment(sketch, "E2233", {"start": v(-43.83, -15.52) * mm, "end": v(-43.63, -15.45) * mm});
            skLineSegment(sketch, "E2234", {"start": v(-43.63, -15.45) * mm, "end": v(-43.42, -15.37) * mm});
            skLineSegment(sketch, "E2235", {"start": v(-43.42, -15.37) * mm, "end": v(-43.22, -15.3) * mm});
            skLineSegment(sketch, "E2236", {"start": v(-43.22, -15.3) * mm, "end": v(-43.02, -15.23) * mm});
            skLineSegment(sketch, "E2237", {"start": v(-43.02, -15.23) * mm, "end": v(-42.81, -15.15) * mm});
            skLineSegment(sketch, "E2238", {"start": v(-42.81, -15.15) * mm, "end": v(-42.6, -15.08) * mm});
            skLineSegment(sketch, "E2239", {"start": v(-42.6, -15.08) * mm, "end": v(-42.4, -15) * mm});
            skLineSegment(sketch, "E2240", {"start": v(-42.4, -15) * mm, "end": v(-42.2, -14.93) * mm});
            skLineSegment(sketch, "E2241", {"start": v(-42.2, -14.93) * mm, "end": v(-42.12, -15.14) * mm});
            skLineSegment(sketch, "E2242", {"start": v(-42.12, -15.14) * mm, "end": v(-42.04, -15.35) * mm});
            skLineSegment(sketch, "E2243", {"start": v(-42.04, -15.35) * mm, "end": v(-41.96, -15.55) * mm});
            skLineSegment(sketch, "E2244", {"start": v(-41.96, -15.55) * mm, "end": v(-41.88, -15.76) * mm});
            skLineSegment(sketch, "E2245", {"start": v(-41.88, -15.76) * mm, "end": v(-41.8, -15.97) * mm});
            skLineSegment(sketch, "E2246", {"start": v(-41.8, -15.97) * mm, "end": v(-41.71, -16.18) * mm});
            skLineSegment(sketch, "E2247", {"start": v(-41.71, -16.18) * mm, "end": v(-41.63, -16.38) * mm});
            skLineSegment(sketch, "E2248", {"start": v(-41.63, -16.38) * mm, "end": v(-41.55, -16.6) * mm});
            skLineSegment(sketch, "E2249", {"start": v(-41.55, -16.6) * mm, "end": v(-41.47, -16.8) * mm});
            skLineSegment(sketch, "E2250", {"start": v(-41.47, -16.8) * mm, "end": v(-41.4, -16.97) * mm});
            skLineSegment(sketch, "E2251", {"start": v(-41.4, -16.97) * mm, "end": v(-41.6, -17.05) * mm});
            skLineSegment(sketch, "E2252", {"start": v(-41.6, -17.05) * mm, "end": v(-41.8, -17.13) * mm});
            skLineSegment(sketch, "E2253", {"start": v(-41.8, -17.13) * mm, "end": v(-42, -17.22) * mm});
            skLineSegment(sketch, "E2254", {"start": v(-42, -17.22) * mm, "end": v(-42.2, -17.3) * mm});
            skLineSegment(sketch, "E2255", {"start": v(-42.2, -17.3) * mm, "end": v(-42.4, -17.39) * mm});
            skLineSegment(sketch, "E2256", {"start": v(-42.4, -17.39) * mm, "end": v(-42.6, -17.47) * mm});
            skLineSegment(sketch, "E2257", {"start": v(-42.6, -17.47) * mm, "end": v(-42.8, -17.55) * mm});
            skLineSegment(sketch, "E2258", {"start": v(-42.8, -17.55) * mm, "end": v(-43, -17.64) * mm});
            skLineSegment(sketch, "E2259", {"start": v(-43, -17.64) * mm, "end": v(-43.2, -17.72) * mm});
            skLineSegment(sketch, "E2260", {"start": v(-43.2, -17.72) * mm, "end": v(-43.4, -17.8) * mm});
            skLineSegment(sketch, "E2261", {"start": v(-43.4, -17.8) * mm, "end": v(-43.6, -17.89) * mm});
            skLineSegment(sketch, "E2262", {"start": v(-43.6, -17.89) * mm, "end": v(-43.8, -17.97) * mm});
            skLineSegment(sketch, "E2263", {"start": v(-43.8, -17.97) * mm, "end": v(-44, -18.06) * mm});
            skLineSegment(sketch, "E2264", {"start": v(-44, -18.06) * mm, "end": v(-44.2, -18.14) * mm});
            skLineSegment(sketch, "E2265", {"start": v(-44.2, -18.14) * mm, "end": v(-44.4, -18.22) * mm});
            skLineSegment(sketch, "E2266", {"start": v(-44.4, -18.22) * mm, "end": v(-44.58, -18.33) * mm});
            skLineSegment(sketch, "E2267", {"start": v(-44.58, -18.33) * mm, "end": v(-44.72, -18.47) * mm});
            skLineSegment(sketch, "E2268", {"start": v(-44.72, -18.47) * mm, "end": v(-44.82, -18.65) * mm});
            skLineSegment(sketch, "E2269", {"start": v(-44.82, -18.65) * mm, "end": v(-44.87, -18.85) * mm});
            skLineSegment(sketch, "E2270", {"start": v(-44.87, -18.85) * mm, "end": v(-44.87, -19.05) * mm});
            skLineSegment(sketch, "E2271", {"start": v(-44.87, -19.05) * mm, "end": v(-44.8, -19.25) * mm});
            skLineSegment(sketch, "E2272", {"start": v(-44.8, -19.25) * mm, "end": v(-44.7, -19.42) * mm});
            skLineSegment(sketch, "E2273", {"start": v(-44.7, -19.42) * mm, "end": v(-44.56, -19.56) * mm});
            skLineSegment(sketch, "E2274", {"start": v(-44.56, -19.56) * mm, "end": v(-44.38, -19.66) * mm});
            skLineSegment(sketch, "E2275", {"start": v(-44.38, -19.66) * mm, "end": v(-44.18, -19.7) * mm});
            skLineSegment(sketch, "E2276", {"start": v(-44.18, -19.7) * mm, "end": v(-43.98, -19.7) * mm});
            skLineSegment(sketch, "E2277", {"start": v(-43.98, -19.7) * mm, "end": v(-43.78, -19.64) * mm});
            skLineSegment(sketch, "E2278", {"start": v(-43.78, -19.64) * mm, "end": v(-43.58, -19.55) * mm});
            skLineSegment(sketch, "E2279", {"start": v(-43.58, -19.55) * mm, "end": v(-43.39, -19.46) * mm});
            skLineSegment(sketch, "E2280", {"start": v(-43.39, -19.46) * mm, "end": v(-43.2, -19.37) * mm});
            skLineSegment(sketch, "E2281", {"start": v(-43.2, -19.37) * mm, "end": v(-43, -19.28) * mm});
            skLineSegment(sketch, "E2282", {"start": v(-43, -19.28) * mm, "end": v(-42.8, -19.2) * mm});
            skLineSegment(sketch, "E2283", {"start": v(-42.8, -19.2) * mm, "end": v(-42.6, -19.1) * mm});
            skLineSegment(sketch, "E2284", {"start": v(-42.6, -19.1) * mm, "end": v(-42.4, -19.01) * mm});
            skLineSegment(sketch, "E2285", {"start": v(-42.4, -19.01) * mm, "end": v(-42.2, -18.92) * mm});
            skLineSegment(sketch, "E2286", {"start": v(-42.2, -18.92) * mm, "end": v(-42, -18.83) * mm});
            skLineSegment(sketch, "E2287", {"start": v(-42, -18.83) * mm, "end": v(-41.81, -18.74) * mm});
            skLineSegment(sketch, "E2288", {"start": v(-41.81, -18.74) * mm, "end": v(-41.61, -18.65) * mm});
            skLineSegment(sketch, "E2289", {"start": v(-41.61, -18.65) * mm, "end": v(-41.42, -18.56) * mm});
            skLineSegment(sketch, "E2290", {"start": v(-41.42, -18.56) * mm, "end": v(-41.22, -18.47) * mm});
            skLineSegment(sketch, "E2291", {"start": v(-41.22, -18.47) * mm, "end": v(-41.02, -18.38) * mm});
            skLineSegment(sketch, "E2292", {"start": v(-41.02, -18.38) * mm, "end": v(-40.83, -18.29) * mm});
            skLineSegment(sketch, "E2293", {"start": v(-40.83, -18.29) * mm, "end": v(-40.73, -18.49) * mm});
            skLineSegment(sketch, "E2294", {"start": v(-40.73, -18.49) * mm, "end": v(-40.63, -18.69) * mm});
            skLineSegment(sketch, "E2295", {"start": v(-40.63, -18.69) * mm, "end": v(-40.53, -18.89) * mm});
            skLineSegment(sketch, "E2296", {"start": v(-40.53, -18.89) * mm, "end": v(-40.44, -19.09) * mm});
            skLineSegment(sketch, "E2297", {"start": v(-40.44, -19.09) * mm, "end": v(-40.34, -19.29) * mm});
            skLineSegment(sketch, "E2298", {"start": v(-40.34, -19.29) * mm, "end": v(-40.24, -19.49) * mm});
            skLineSegment(sketch, "E2299", {"start": v(-40.24, -19.49) * mm, "end": v(-40.14, -19.69) * mm});
            skLineSegment(sketch, "E2300", {"start": v(-40.14, -19.69) * mm, "end": v(-40.04, -19.89) * mm});
            skLineSegment(sketch, "E2301", {"start": v(-40.04, -19.89) * mm, "end": v(-39.95, -20.09) * mm});
            skLineSegment(sketch, "E2302", {"start": v(-39.95, -20.09) * mm, "end": v(-39.87, -20.25) * mm});
            skLineSegment(sketch, "E2303", {"start": v(-39.87, -20.25) * mm, "end": v(-40.06, -20.35) * mm});
            skLineSegment(sketch, "E2304", {"start": v(-40.06, -20.35) * mm, "end": v(-40.25, -20.45) * mm});
            skLineSegment(sketch, "E2305", {"start": v(-40.25, -20.45) * mm, "end": v(-40.44, -20.55) * mm});
            skLineSegment(sketch, "E2306", {"start": v(-40.44, -20.55) * mm, "end": v(-40.64, -20.65) * mm});
            skLineSegment(sketch, "E2307", {"start": v(-40.64, -20.65) * mm, "end": v(-40.83, -20.75) * mm});
            skLineSegment(sketch, "E2308", {"start": v(-40.83, -20.75) * mm, "end": v(-41.02, -20.85) * mm});
            skLineSegment(sketch, "E2309", {"start": v(-41.02, -20.85) * mm, "end": v(-41.21, -20.95) * mm});
            skLineSegment(sketch, "E2310", {"start": v(-41.21, -20.95) * mm, "end": v(-41.4, -21.05) * mm});
            skLineSegment(sketch, "E2311", {"start": v(-41.4, -21.05) * mm, "end": v(-41.6, -21.15) * mm});
            skLineSegment(sketch, "E2312", {"start": v(-41.6, -21.15) * mm, "end": v(-41.79, -21.25) * mm});
            skLineSegment(sketch, "E2313", {"start": v(-41.79, -21.25) * mm, "end": v(-41.98, -21.35) * mm});
            skLineSegment(sketch, "E2314", {"start": v(-41.98, -21.35) * mm, "end": v(-42.17, -21.45) * mm});
            skLineSegment(sketch, "E2315", {"start": v(-42.17, -21.45) * mm, "end": v(-42.37, -21.55) * mm});
            skLineSegment(sketch, "E2316", {"start": v(-42.37, -21.55) * mm, "end": v(-42.56, -21.65) * mm});
            skLineSegment(sketch, "E2317", {"start": v(-42.56, -21.65) * mm, "end": v(-42.75, -21.75) * mm});
            skLineSegment(sketch, "E2318", {"start": v(-42.75, -21.75) * mm, "end": v(-42.92, -21.87) * mm});
            skLineSegment(sketch, "E2319", {"start": v(-42.92, -21.87) * mm, "end": v(-43.05, -22.03) * mm});
            skLineSegment(sketch, "E2320", {"start": v(-43.05, -22.03) * mm, "end": v(-43.13, -22.21) * mm});
            skLineSegment(sketch, "E2321", {"start": v(-43.13, -22.21) * mm, "end": v(-43.16, -22.41) * mm});
            skLineSegment(sketch, "E2322", {"start": v(-43.16, -22.41) * mm, "end": v(-43.14, -22.62) * mm});
            skLineSegment(sketch, "E2323", {"start": v(-43.14, -22.62) * mm, "end": v(-43.07, -22.8) * mm});
            skLineSegment(sketch, "E2324", {"start": v(-43.07, -22.8) * mm, "end": v(-42.95, -22.97) * mm});
            skLineSegment(sketch, "E2325", {"start": v(-42.95, -22.97) * mm, "end": v(-42.8, -23.1) * mm});
            skLineSegment(sketch, "E2326", {"start": v(-42.8, -23.1) * mm, "end": v(-42.6, -23.18) * mm});
            skLineSegment(sketch, "E2327", {"start": v(-42.6, -23.18) * mm, "end": v(-42.4, -23.21) * mm});
            skLineSegment(sketch, "E2328", {"start": v(-42.4, -23.21) * mm, "end": v(-42.2, -23.19) * mm});
            skLineSegment(sketch, "E2329", {"start": v(-42.2, -23.19) * mm, "end": v(-42.01, -23.12) * mm});
            skLineSegment(sketch, "E2330", {"start": v(-42.01, -23.12) * mm, "end": v(-41.82, -23) * mm});
            skLineSegment(sketch, "E2331", {"start": v(-41.82, -23) * mm, "end": v(-41.64, -22.9) * mm});
            skLineSegment(sketch, "E2332", {"start": v(-41.64, -22.9) * mm, "end": v(-41.45, -22.8) * mm});
            skLineSegment(sketch, "E2333", {"start": v(-41.45, -22.8) * mm, "end": v(-41.26, -22.7) * mm});
            skLineSegment(sketch, "E2334", {"start": v(-41.26, -22.7) * mm, "end": v(-41.07, -22.58) * mm});
            skLineSegment(sketch, "E2335", {"start": v(-41.07, -22.58) * mm, "end": v(-40.88, -22.48) * mm});
            skLineSegment(sketch, "E2336", {"start": v(-40.88, -22.48) * mm, "end": v(-40.7, -22.37) * mm});
            skLineSegment(sketch, "E2337", {"start": v(-40.7, -22.37) * mm, "end": v(-40.5, -22.27) * mm});
            skLineSegment(sketch, "E2338", {"start": v(-40.5, -22.27) * mm, "end": v(-40.31, -22.16) * mm});
            skLineSegment(sketch, "E2339", {"start": v(-40.31, -22.16) * mm, "end": v(-40.12, -22.05) * mm});
            skLineSegment(sketch, "E2340", {"start": v(-40.12, -22.05) * mm, "end": v(-39.94, -21.95) * mm});
            skLineSegment(sketch, "E2341", {"start": v(-39.94, -21.95) * mm, "end": v(-39.75, -21.84) * mm});
            skLineSegment(sketch, "E2342", {"start": v(-39.75, -21.84) * mm, "end": v(-39.56, -21.73) * mm});
            skLineSegment(sketch, "E2343", {"start": v(-39.56, -21.73) * mm, "end": v(-39.37, -21.63) * mm});
            skLineSegment(sketch, "E2344", {"start": v(-39.37, -21.63) * mm, "end": v(-39.18, -21.52) * mm});
            skLineSegment(sketch, "E2345", {"start": v(-39.18, -21.52) * mm, "end": v(-39.07, -21.71) * mm});
            skLineSegment(sketch, "E2346", {"start": v(-39.07, -21.71) * mm, "end": v(-38.95, -21.9) * mm});
            skLineSegment(sketch, "E2347", {"start": v(-38.95, -21.9) * mm, "end": v(-38.84, -22.1) * mm});
            skLineSegment(sketch, "E2348", {"start": v(-38.84, -22.1) * mm, "end": v(-38.72, -22.29) * mm});
            skLineSegment(sketch, "E2349", {"start": v(-38.72, -22.29) * mm, "end": v(-38.6, -22.48) * mm});
            skLineSegment(sketch, "E2350", {"start": v(-38.6, -22.48) * mm, "end": v(-38.5, -22.67) * mm});
            skLineSegment(sketch, "E2351", {"start": v(-38.5, -22.67) * mm, "end": v(-38.38, -22.86) * mm});
            skLineSegment(sketch, "E2352", {"start": v(-38.38, -22.86) * mm, "end": v(-38.27, -23.05) * mm});
            skLineSegment(sketch, "E2353", {"start": v(-38.27, -23.05) * mm, "end": v(-38.15, -23.24) * mm});
            skLineSegment(sketch, "E2354", {"start": v(-38.15, -23.24) * mm, "end": v(-38.06, -23.4) * mm});
            skLineSegment(sketch, "E2355", {"start": v(-38.06, -23.4) * mm, "end": v(-38.25, -23.51) * mm});
            skLineSegment(sketch, "E2356", {"start": v(-38.25, -23.51) * mm, "end": v(-38.43, -23.63) * mm});
            skLineSegment(sketch, "E2357", {"start": v(-38.43, -23.63) * mm, "end": v(-38.61, -23.74) * mm});
            skLineSegment(sketch, "E2358", {"start": v(-38.61, -23.74) * mm, "end": v(-38.8, -23.86) * mm});
            skLineSegment(sketch, "E2359", {"start": v(-38.8, -23.86) * mm, "end": v(-38.98, -23.98) * mm});
            skLineSegment(sketch, "E2360", {"start": v(-38.98, -23.98) * mm, "end": v(-39.16, -24.1) * mm});
            skLineSegment(sketch, "E2361", {"start": v(-39.16, -24.1) * mm, "end": v(-39.35, -24.2) * mm});
            skLineSegment(sketch, "E2362", {"start": v(-39.35, -24.2) * mm, "end": v(-39.53, -24.32) * mm});
            skLineSegment(sketch, "E2363", {"start": v(-39.53, -24.32) * mm, "end": v(-39.71, -24.44) * mm});
            skLineSegment(sketch, "E2364", {"start": v(-39.71, -24.44) * mm, "end": v(-39.9, -24.55) * mm});
            skLineSegment(sketch, "E2365", {"start": v(-39.9, -24.55) * mm, "end": v(-40.08, -24.67) * mm});
            skLineSegment(sketch, "E2366", {"start": v(-40.08, -24.67) * mm, "end": v(-40.26, -24.78) * mm});
            skLineSegment(sketch, "E2367", {"start": v(-40.26, -24.78) * mm, "end": v(-40.45, -24.9) * mm});
            skLineSegment(sketch, "E2368", {"start": v(-40.45, -24.9) * mm, "end": v(-40.63, -25.01) * mm});
            skLineSegment(sketch, "E2369", {"start": v(-40.63, -25.01) * mm, "end": v(-40.81, -25.13) * mm});
            skLineSegment(sketch, "E2370", {"start": v(-40.81, -25.13) * mm, "end": v(-40.97, -25.26) * mm});
            skLineSegment(sketch, "E2371", {"start": v(-40.97, -25.26) * mm, "end": v(-41.08, -25.43) * mm});
            skLineSegment(sketch, "E2372", {"start": v(-41.08, -25.43) * mm, "end": v(-41.15, -25.62) * mm});
            skLineSegment(sketch, "E2373", {"start": v(-41.15, -25.62) * mm, "end": v(-41.17, -25.82) * mm});
            skLineSegment(sketch, "E2374", {"start": v(-41.17, -25.82) * mm, "end": v(-41.13, -26.02) * mm});
            skLineSegment(sketch, "E2375", {"start": v(-41.13, -26.02) * mm, "end": v(-41.04, -26.2) * mm});
            skLineSegment(sketch, "E2376", {"start": v(-41.04, -26.2) * mm, "end": v(-40.9, -26.36) * mm});
            skLineSegment(sketch, "E2377", {"start": v(-40.9, -26.36) * mm, "end": v(-40.74, -26.48) * mm});
            skLineSegment(sketch, "E2378", {"start": v(-40.74, -26.48) * mm, "end": v(-40.55, -26.54) * mm});
            skLineSegment(sketch, "E2379", {"start": v(-40.55, -26.54) * mm, "end": v(-40.35, -26.56) * mm});
            skLineSegment(sketch, "E2380", {"start": v(-40.35, -26.56) * mm, "end": v(-40.15, -26.52) * mm});
            skLineSegment(sketch, "E2381", {"start": v(-40.15, -26.52) * mm, "end": v(-39.96, -26.43) * mm});
            skLineSegment(sketch, "E2382", {"start": v(-39.96, -26.43) * mm, "end": v(-39.78, -26.3) * mm});
            skLineSegment(sketch, "E2383", {"start": v(-39.78, -26.3) * mm, "end": v(-39.6, -26.19) * mm});
            skLineSegment(sketch, "E2384", {"start": v(-39.6, -26.19) * mm, "end": v(-39.43, -26.06) * mm});
            skLineSegment(sketch, "E2385", {"start": v(-39.43, -26.06) * mm, "end": v(-39.25, -25.94) * mm});
            skLineSegment(sketch, "E2386", {"start": v(-39.25, -25.94) * mm, "end": v(-39.07, -25.82) * mm});
            skLineSegment(sketch, "E2387", {"start": v(-39.07, -25.82) * mm, "end": v(-38.89, -25.7) * mm});
            skLineSegment(sketch, "E2388", {"start": v(-38.89, -25.7) * mm, "end": v(-38.7, -25.58) * mm});
            skLineSegment(sketch, "E2389", {"start": v(-38.7, -25.58) * mm, "end": v(-38.53, -25.46) * mm});
            skLineSegment(sketch, "E2390", {"start": v(-38.53, -25.46) * mm, "end": v(-38.35, -25.34) * mm});
            skLineSegment(sketch, "E2391", {"start": v(-38.35, -25.34) * mm, "end": v(-38.17, -25.21) * mm});
            skLineSegment(sketch, "E2392", {"start": v(-38.17, -25.21) * mm, "end": v(-37.99, -25.1) * mm});
            skLineSegment(sketch, "E2393", {"start": v(-37.99, -25.1) * mm, "end": v(-37.81, -24.97) * mm});
            skLineSegment(sketch, "E2394", {"start": v(-37.81, -24.97) * mm, "end": v(-37.63, -24.85) * mm});
            skLineSegment(sketch, "E2395", {"start": v(-37.63, -24.85) * mm, "end": v(-37.45, -24.73) * mm});
            skLineSegment(sketch, "E2396", {"start": v(-37.45, -24.73) * mm, "end": v(-37.27, -24.6) * mm});
            skLineSegment(sketch, "E2397", {"start": v(-37.27, -24.6) * mm, "end": v(-37.14, -24.79) * mm});
            skLineSegment(sketch, "E2398", {"start": v(-37.14, -24.79) * mm, "end": v(-37.01, -24.97) * mm});
            skLineSegment(sketch, "E2399", {"start": v(-37.01, -24.97) * mm, "end": v(-36.88, -25.15) * mm});
            skLineSegment(sketch, "E2400", {"start": v(-36.88, -25.15) * mm, "end": v(-36.75, -25.33) * mm});
            skLineSegment(sketch, "E2401", {"start": v(-36.75, -25.33) * mm, "end": v(-36.63, -25.51) * mm});
            skLineSegment(sketch, "E2402", {"start": v(-36.63, -25.51) * mm, "end": v(-36.5, -25.7) * mm});
            skLineSegment(sketch, "E2403", {"start": v(-36.5, -25.7) * mm, "end": v(-36.37, -25.88) * mm});
            skLineSegment(sketch, "E2404", {"start": v(-36.37, -25.88) * mm, "end": v(-36.24, -26.06) * mm});
            skLineSegment(sketch, "E2405", {"start": v(-36.24, -26.06) * mm, "end": v(-36.1, -26.24) * mm});
            skLineSegment(sketch, "E2406", {"start": v(-36.1, -26.24) * mm, "end": v(-36, -26.38) * mm});
            skLineSegment(sketch, "E2407", {"start": v(-36, -26.38) * mm, "end": v(-36.18, -26.51) * mm});
            skLineSegment(sketch, "E2408", {"start": v(-36.18, -26.51) * mm, "end": v(-36.35, -26.64) * mm});
            skLineSegment(sketch, "E2409", {"start": v(-36.35, -26.64) * mm, "end": v(-36.52, -26.77) * mm});
            skLineSegment(sketch, "E2410", {"start": v(-36.52, -26.77) * mm, "end": v(-36.7, -26.9) * mm});
            skLineSegment(sketch, "E2411", {"start": v(-36.7, -26.9) * mm, "end": v(-36.87, -27.04) * mm});
            skLineSegment(sketch, "E2412", {"start": v(-36.87, -27.04) * mm, "end": v(-37.04, -27.17) * mm});
            skLineSegment(sketch, "E2413", {"start": v(-37.04, -27.17) * mm, "end": v(-37.22, -27.3) * mm});
            skLineSegment(sketch, "E2414", {"start": v(-37.22, -27.3) * mm, "end": v(-37.39, -27.43) * mm});
            skLineSegment(sketch, "E2415", {"start": v(-37.39, -27.43) * mm, "end": v(-37.56, -27.56) * mm});
            skLineSegment(sketch, "E2416", {"start": v(-37.56, -27.56) * mm, "end": v(-37.73, -27.69) * mm});
            skLineSegment(sketch, "E2417", {"start": v(-37.73, -27.69) * mm, "end": v(-37.9, -27.82) * mm});
            skLineSegment(sketch, "E2418", {"start": v(-37.9, -27.82) * mm, "end": v(-38.08, -27.95) * mm});
            skLineSegment(sketch, "E2419", {"start": v(-38.08, -27.95) * mm, "end": v(-38.25, -28.08) * mm});
            skLineSegment(sketch, "E2420", {"start": v(-38.25, -28.08) * mm, "end": v(-38.43, -28.2) * mm});
            skLineSegment(sketch, "E2421", {"start": v(-38.43, -28.2) * mm, "end": v(-38.6, -28.34) * mm});
            skLineSegment(sketch, "E2422", {"start": v(-38.6, -28.34) * mm, "end": v(-38.74, -28.48) * mm});
            skLineSegment(sketch, "E2423", {"start": v(-38.74, -28.48) * mm, "end": v(-38.85, -28.66) * mm});
            skLineSegment(sketch, "E2424", {"start": v(-38.85, -28.66) * mm, "end": v(-38.9, -28.86) * mm});
            skLineSegment(sketch, "E2425", {"start": v(-38.9, -28.86) * mm, "end": v(-38.9, -29.06) * mm});
            skLineSegment(sketch, "E2426", {"start": v(-38.9, -29.06) * mm, "end": v(-38.84, -29.25) * mm});
            skLineSegment(sketch, "E2427", {"start": v(-38.84, -29.25) * mm, "end": v(-38.74, -29.43) * mm});
            skLineSegment(sketch, "E2428", {"start": v(-38.74, -29.43) * mm, "end": v(-38.6, -29.57) * mm});
            skLineSegment(sketch, "E2429", {"start": v(-38.6, -29.57) * mm, "end": v(-38.42, -29.67) * mm});
            skLineSegment(sketch, "E2430", {"start": v(-38.42, -29.67) * mm, "end": v(-38.22, -29.72) * mm});
            skLineSegment(sketch, "E2431", {"start": v(-38.22, -29.72) * mm, "end": v(-38.02, -29.72) * mm});
            skLineSegment(sketch, "E2432", {"start": v(-38.02, -29.72) * mm, "end": v(-37.82, -29.67) * mm});
            skLineSegment(sketch, "E2433", {"start": v(-37.82, -29.67) * mm, "end": v(-37.65, -29.56) * mm});
            skLineSegment(sketch, "E2434", {"start": v(-37.65, -29.56) * mm, "end": v(-37.48, -29.43) * mm});
            skLineSegment(sketch, "E2435", {"start": v(-37.48, -29.43) * mm, "end": v(-37.31, -29.3) * mm});
            skLineSegment(sketch, "E2436", {"start": v(-37.31, -29.3) * mm, "end": v(-37.14, -29.15) * mm});
            skLineSegment(sketch, "E2437", {"start": v(-37.14, -29.15) * mm, "end": v(-36.97, -29.02) * mm});
            skLineSegment(sketch, "E2438", {"start": v(-36.97, -29.02) * mm, "end": v(-36.8, -28.88) * mm});
            skLineSegment(sketch, "E2439", {"start": v(-36.8, -28.88) * mm, "end": v(-36.64, -28.75) * mm});
            skLineSegment(sketch, "E2440", {"start": v(-36.64, -28.75) * mm, "end": v(-36.47, -28.61) * mm});
            skLineSegment(sketch, "E2441", {"start": v(-36.47, -28.61) * mm, "end": v(-36.3, -28.48) * mm});
            skLineSegment(sketch, "E2442", {"start": v(-36.3, -28.48) * mm, "end": v(-36.13, -28.34) * mm});
            skLineSegment(sketch, "E2443", {"start": v(-36.13, -28.34) * mm, "end": v(-35.96, -28.2) * mm});
            skLineSegment(sketch, "E2444", {"start": v(-35.96, -28.2) * mm, "end": v(-35.8, -28.07) * mm});
            skLineSegment(sketch, "E2445", {"start": v(-35.8, -28.07) * mm, "end": v(-35.62, -27.93) * mm});
            skLineSegment(sketch, "E2446", {"start": v(-35.62, -27.93) * mm, "end": v(-35.45, -27.8) * mm});
            skLineSegment(sketch, "E2447", {"start": v(-35.45, -27.8) * mm, "end": v(-35.28, -27.66) * mm});
            skLineSegment(sketch, "E2448", {"start": v(-35.28, -27.66) * mm, "end": v(-35.12, -27.52) * mm});
            skLineSegment(sketch, "E2449", {"start": v(-35.12, -27.52) * mm, "end": v(-34.97, -27.7) * mm});
            skLineSegment(sketch, "E2450", {"start": v(-34.97, -27.7) * mm, "end": v(-34.83, -27.86) * mm});
            skLineSegment(sketch, "E2451", {"start": v(-34.83, -27.86) * mm, "end": v(-34.68, -28.03) * mm});
            skLineSegment(sketch, "E2452", {"start": v(-34.68, -28.03) * mm, "end": v(-34.54, -28.2) * mm});
            skLineSegment(sketch, "E2453", {"start": v(-34.54, -28.2) * mm, "end": v(-34.4, -28.37) * mm});
            skLineSegment(sketch, "E2454", {"start": v(-34.4, -28.37) * mm, "end": v(-34.25, -28.54) * mm});
            skLineSegment(sketch, "E2455", {"start": v(-34.25, -28.54) * mm, "end": v(-34.1, -28.71) * mm});
            skLineSegment(sketch, "E2456", {"start": v(-34.1, -28.71) * mm, "end": v(-33.96, -28.88) * mm});
            skLineSegment(sketch, "E2457", {"start": v(-33.96, -28.88) * mm, "end": v(-33.82, -29.05) * mm});
            skLineSegment(sketch, "E2458", {"start": v(-33.82, -29.05) * mm, "end": v(-33.7, -29.2) * mm});
            skLineSegment(sketch, "E2459", {"start": v(-33.7, -29.2) * mm, "end": v(-33.87, -29.33) * mm});
            skLineSegment(sketch, "E2460", {"start": v(-33.87, -29.33) * mm, "end": v(-34.03, -29.48) * mm});
            skLineSegment(sketch, "E2461", {"start": v(-34.03, -29.48) * mm, "end": v(-34.19, -29.62) * mm});
            skLineSegment(sketch, "E2462", {"start": v(-34.19, -29.62) * mm, "end": v(-34.35, -29.77) * mm});
            skLineSegment(sketch, "E2463", {"start": v(-34.35, -29.77) * mm, "end": v(-34.51, -29.91) * mm});
            skLineSegment(sketch, "E2464", {"start": v(-34.51, -29.91) * mm, "end": v(-34.68, -30.06) * mm});
            skLineSegment(sketch, "E2465", {"start": v(-34.68, -30.06) * mm, "end": v(-34.84, -30.2) * mm});
            skLineSegment(sketch, "E2466", {"start": v(-34.84, -30.2) * mm, "end": v(-35, -30.34) * mm});
            skLineSegment(sketch, "E2467", {"start": v(-35, -30.34) * mm, "end": v(-35.16, -30.49) * mm});
            skLineSegment(sketch, "E2468", {"start": v(-35.16, -30.49) * mm, "end": v(-35.32, -30.63) * mm});
            skLineSegment(sketch, "E2469", {"start": v(-35.32, -30.63) * mm, "end": v(-35.48, -30.78) * mm});
            skLineSegment(sketch, "E2470", {"start": v(-35.48, -30.78) * mm, "end": v(-35.65, -30.92) * mm});
            skLineSegment(sketch, "E2471", {"start": v(-35.65, -30.92) * mm, "end": v(-35.8, -31.06) * mm});
            skLineSegment(sketch, "E2472", {"start": v(-35.8, -31.06) * mm, "end": v(-35.97, -31.2) * mm});
            skLineSegment(sketch, "E2473", {"start": v(-35.97, -31.2) * mm, "end": v(-36.13, -31.35) * mm});
            skLineSegment(sketch, "E2474", {"start": v(-36.13, -31.35) * mm, "end": v(-36.26, -31.5) * mm});
            skLineSegment(sketch, "E2475", {"start": v(-36.26, -31.5) * mm, "end": v(-36.35, -31.7) * mm});
            skLineSegment(sketch, "E2476", {"start": v(-36.35, -31.7) * mm, "end": v(-36.39, -31.9) * mm});
            skLineSegment(sketch, "E2477", {"start": v(-36.39, -31.9) * mm, "end": v(-36.37, -32.1) * mm});
            skLineSegment(sketch, "E2478", {"start": v(-36.37, -32.1) * mm, "end": v(-36.3, -32.29) * mm});
            skLineSegment(sketch, "E2479", {"start": v(-36.3, -32.29) * mm, "end": v(-36.18, -32.45) * mm});
            skLineSegment(sketch, "E2480", {"start": v(-36.18, -32.45) * mm, "end": v(-36.03, -32.58) * mm});
            skLineSegment(sketch, "E2481", {"start": v(-36.03, -32.58) * mm, "end": v(-35.84, -32.67) * mm});
            skLineSegment(sketch, "E2482", {"start": v(-35.84, -32.67) * mm, "end": v(-35.64, -32.7) * mm});
            skLineSegment(sketch, "E2483", {"start": v(-35.64, -32.7) * mm, "end": v(-35.44, -32.68) * mm});
            skLineSegment(sketch, "E2484", {"start": v(-35.44, -32.68) * mm, "end": v(-35.25, -32.61) * mm});
            skLineSegment(sketch, "E2485", {"start": v(-35.25, -32.61) * mm, "end": v(-35.08, -32.5) * mm});
            skLineSegment(sketch, "E2486", {"start": v(-35.08, -32.5) * mm, "end": v(-34.92, -32.34) * mm});
            skLineSegment(sketch, "E2487", {"start": v(-34.92, -32.34) * mm, "end": v(-34.77, -32.2) * mm});
            skLineSegment(sketch, "E2488", {"start": v(-34.77, -32.2) * mm, "end": v(-34.61, -32.05) * mm});
            skLineSegment(sketch, "E2489", {"start": v(-34.61, -32.05) * mm, "end": v(-34.45, -31.9) * mm});
            skLineSegment(sketch, "E2490", {"start": v(-34.45, -31.9) * mm, "end": v(-34.3, -31.75) * mm});
            skLineSegment(sketch, "E2491", {"start": v(-34.3, -31.75) * mm, "end": v(-34.14, -31.6) * mm});
            skLineSegment(sketch, "E2492", {"start": v(-34.14, -31.6) * mm, "end": v(-33.98, -31.45) * mm});
            skLineSegment(sketch, "E2493", {"start": v(-33.98, -31.45) * mm, "end": v(-33.83, -31.3) * mm});
            skLineSegment(sketch, "E2494", {"start": v(-33.83, -31.3) * mm, "end": v(-33.67, -31.15) * mm});
            skLineSegment(sketch, "E2495", {"start": v(-33.67, -31.15) * mm, "end": v(-33.51, -31) * mm});
            skLineSegment(sketch, "E2496", {"start": v(-33.51, -31) * mm, "end": v(-33.35, -30.85) * mm});
            skLineSegment(sketch, "E2497", {"start": v(-33.35, -30.85) * mm, "end": v(-33.2, -30.7) * mm});
            skLineSegment(sketch, "E2498", {"start": v(-33.2, -30.7) * mm, "end": v(-33.04, -30.55) * mm});
            skLineSegment(sketch, "E2499", {"start": v(-33.04, -30.55) * mm, "end": v(-32.88, -30.4) * mm});
            skLineSegment(sketch, "E2500", {"start": v(-32.88, -30.4) * mm, "end": v(-32.73, -30.25) * mm});
            skLineSegment(sketch, "E2501", {"start": v(-32.73, -30.25) * mm, "end": v(-32.57, -30.41) * mm});
            skLineSegment(sketch, "E2502", {"start": v(-32.57, -30.41) * mm, "end": v(-32.41, -30.57) * mm});
            skLineSegment(sketch, "E2503", {"start": v(-32.41, -30.57) * mm, "end": v(-32.25, -30.73) * mm});
            skLineSegment(sketch, "E2504", {"start": v(-32.25, -30.73) * mm, "end": v(-32.1, -30.88) * mm});
            skLineSegment(sketch, "E2505", {"start": v(-32.1, -30.88) * mm, "end": v(-31.94, -31.04) * mm});
            skLineSegment(sketch, "E2506", {"start": v(-31.94, -31.04) * mm, "end": v(-31.78, -31.2) * mm});
            skLineSegment(sketch, "E2507", {"start": v(-31.78, -31.2) * mm, "end": v(-31.62, -31.36) * mm});
            skLineSegment(sketch, "E2508", {"start": v(-31.62, -31.36) * mm, "end": v(-31.47, -31.51) * mm});
            skLineSegment(sketch, "E2509", {"start": v(-31.47, -31.51) * mm, "end": v(-31.3, -31.67) * mm});
            skLineSegment(sketch, "E2510", {"start": v(-31.3, -31.67) * mm, "end": v(-31.18, -31.8) * mm});
            skLineSegment(sketch, "E2511", {"start": v(-31.18, -31.8) * mm, "end": v(-31.33, -31.95) * mm});
            skLineSegment(sketch, "E2512", {"start": v(-31.33, -31.95) * mm, "end": v(-31.48, -32.11) * mm});
            skLineSegment(sketch, "E2513", {"start": v(-31.48, -32.11) * mm, "end": v(-31.63, -32.27) * mm});
            skLineSegment(sketch, "E2514", {"start": v(-31.63, -32.27) * mm, "end": v(-31.78, -32.43) * mm});
            skLineSegment(sketch, "E2515", {"start": v(-31.78, -32.43) * mm, "end": v(-31.93, -32.58) * mm});
            skLineSegment(sketch, "E2516", {"start": v(-31.93, -32.58) * mm, "end": v(-32.08, -32.74) * mm});
            skLineSegment(sketch, "E2517", {"start": v(-32.08, -32.74) * mm, "end": v(-32.23, -32.9) * mm});
            skLineSegment(sketch, "E2518", {"start": v(-32.23, -32.9) * mm, "end": v(-32.38, -33.05) * mm});
            skLineSegment(sketch, "E2519", {"start": v(-32.38, -33.05) * mm, "end": v(-32.53, -33.21) * mm});
            skLineSegment(sketch, "E2520", {"start": v(-32.53, -33.21) * mm, "end": v(-32.68, -33.37) * mm});
            skLineSegment(sketch, "E2521", {"start": v(-32.68, -33.37) * mm, "end": v(-32.83, -33.52) * mm});
            skLineSegment(sketch, "E2522", {"start": v(-32.83, -33.52) * mm, "end": v(-32.97, -33.68) * mm});
            skLineSegment(sketch, "E2523", {"start": v(-32.97, -33.68) * mm, "end": v(-33.12, -33.84) * mm});
            skLineSegment(sketch, "E2524", {"start": v(-33.12, -33.84) * mm, "end": v(-33.27, -34) * mm});
            skLineSegment(sketch, "E2525", {"start": v(-33.27, -34) * mm, "end": v(-33.42, -34.15) * mm});
            skLineSegment(sketch, "E2526", {"start": v(-33.42, -34.15) * mm, "end": v(-33.54, -34.32) * mm});
            skLineSegment(sketch, "E2527", {"start": v(-33.54, -34.32) * mm, "end": v(-33.61, -34.5) * mm});
            skLineSegment(sketch, "E2528", {"start": v(-33.61, -34.5) * mm, "end": v(-33.63, -34.71) * mm});
            skLineSegment(sketch, "E2529", {"start": v(-33.63, -34.71) * mm, "end": v(-33.6, -34.91) * mm});
            skLineSegment(sketch, "E2530", {"start": v(-33.6, -34.91) * mm, "end": v(-33.51, -35.1) * mm});
            skLineSegment(sketch, "E2531", {"start": v(-33.51, -35.1) * mm, "end": v(-33.38, -35.25) * mm});
            skLineSegment(sketch, "E2532", {"start": v(-33.38, -35.25) * mm, "end": v(-33.21, -35.37) * mm});
            skLineSegment(sketch, "E2533", {"start": v(-33.21, -35.37) * mm, "end": v(-33.02, -35.44) * mm});
            skLineSegment(sketch, "E2534", {"start": v(-33.02, -35.44) * mm, "end": v(-32.82, -35.46) * mm});
            skLineSegment(sketch, "E2535", {"start": v(-32.82, -35.46) * mm, "end": v(-32.62, -35.42) * mm});
            skLineSegment(sketch, "E2536", {"start": v(-32.62, -35.42) * mm, "end": v(-32.44, -35.33) * mm});
            skLineSegment(sketch, "E2537", {"start": v(-32.44, -35.33) * mm, "end": v(-32.28, -35.2) * mm});
            skLineSegment(sketch, "E2538", {"start": v(-32.28, -35.2) * mm, "end": v(-32.14, -35.04) * mm});
            skLineSegment(sketch, "E2539", {"start": v(-32.14, -35.04) * mm, "end": v(-32, -34.88) * mm});
            skLineSegment(sketch, "E2540", {"start": v(-32, -34.88) * mm, "end": v(-31.85, -34.72) * mm});
            skLineSegment(sketch, "E2541", {"start": v(-31.85, -34.72) * mm, "end": v(-31.7, -34.56) * mm});
            skLineSegment(sketch, "E2542", {"start": v(-31.7, -34.56) * mm, "end": v(-31.56, -34.4) * mm});
            skLineSegment(sketch, "E2543", {"start": v(-31.56, -34.4) * mm, "end": v(-31.42, -34.23) * mm});
            skLineSegment(sketch, "E2544", {"start": v(-31.42, -34.23) * mm, "end": v(-31.27, -34.07) * mm});
            skLineSegment(sketch, "E2545", {"start": v(-31.27, -34.07) * mm, "end": v(-31.13, -33.9) * mm});
            skLineSegment(sketch, "E2546", {"start": v(-31.13, -33.9) * mm, "end": v(-30.98, -33.75) * mm});
            skLineSegment(sketch, "E2547", {"start": v(-30.98, -33.75) * mm, "end": v(-30.84, -33.58) * mm});
            skLineSegment(sketch, "E2548", {"start": v(-30.84, -33.58) * mm, "end": v(-30.7, -33.42) * mm});
            skLineSegment(sketch, "E2549", {"start": v(-30.7, -33.42) * mm, "end": v(-30.55, -33.26) * mm});
            skLineSegment(sketch, "E2550", {"start": v(-30.55, -33.26) * mm, "end": v(-30.4, -33.1) * mm});
            skLineSegment(sketch, "E2551", {"start": v(-30.4, -33.1) * mm, "end": v(-30.26, -32.94) * mm});
            skLineSegment(sketch, "E2552", {"start": v(-30.26, -32.94) * mm, "end": v(-30.12, -32.78) * mm});
            skLineSegment(sketch, "E2553", {"start": v(-30.12, -32.78) * mm, "end": v(-29.95, -32.92) * mm});
            skLineSegment(sketch, "E2554", {"start": v(-29.95, -32.92) * mm, "end": v(-29.78, -33.06) * mm});
            skLineSegment(sketch, "E2555", {"start": v(-29.78, -33.06) * mm, "end": v(-29.6, -33.2) * mm});
            skLineSegment(sketch, "E2556", {"start": v(-29.6, -33.2) * mm, "end": v(-29.44, -33.35) * mm});
            skLineSegment(sketch, "E2557", {"start": v(-29.44, -33.35) * mm, "end": v(-29.27, -33.5) * mm});
            skLineSegment(sketch, "E2558", {"start": v(-29.27, -33.5) * mm, "end": v(-29.1, -33.64) * mm});
            skLineSegment(sketch, "E2559", {"start": v(-29.1, -33.64) * mm, "end": v(-28.93, -33.78) * mm});
            skLineSegment(sketch, "E2560", {"start": v(-28.93, -33.78) * mm, "end": v(-28.76, -33.93) * mm});
            skLineSegment(sketch, "E2561", {"start": v(-28.76, -33.93) * mm, "end": v(-28.59, -34.07) * mm});
            skLineSegment(sketch, "E2562", {"start": v(-28.59, -34.07) * mm, "end": v(-28.45, -34.19) * mm});
            skLineSegment(sketch, "E2563", {"start": v(-28.45, -34.19) * mm, "end": v(-28.59, -34.36) * mm});
            skLineSegment(sketch, "E2564", {"start": v(-28.59, -34.36) * mm, "end": v(-28.72, -34.52) * mm});
            skLineSegment(sketch, "E2565", {"start": v(-28.72, -34.52) * mm, "end": v(-28.86, -34.7) * mm});
            skLineSegment(sketch, "E2566", {"start": v(-28.86, -34.7) * mm, "end": v(-29, -34.86) * mm});
            skLineSegment(sketch, "E2567", {"start": v(-29, -34.86) * mm, "end": v(-29.13, -35.03) * mm});
            skLineSegment(sketch, "E2568", {"start": v(-29.13, -35.03) * mm, "end": v(-29.27, -35.2) * mm});
            skLineSegment(sketch, "E2569", {"start": v(-29.27, -35.2) * mm, "end": v(-29.4, -35.37) * mm});
            skLineSegment(sketch, "E2570", {"start": v(-29.4, -35.37) * mm, "end": v(-29.54, -35.54) * mm});
            skLineSegment(sketch, "E2571", {"start": v(-29.54, -35.54) * mm, "end": v(-29.68, -35.7) * mm});
            skLineSegment(sketch, "E2572", {"start": v(-29.68, -35.7) * mm, "end": v(-29.81, -35.87) * mm});
            skLineSegment(sketch, "E2573", {"start": v(-29.81, -35.87) * mm, "end": v(-29.95, -36.04) * mm});
            skLineSegment(sketch, "E2574", {"start": v(-29.95, -36.04) * mm, "end": v(-30.08, -36.21) * mm});
            skLineSegment(sketch, "E2575", {"start": v(-30.08, -36.21) * mm, "end": v(-30.22, -36.38) * mm});
            skLineSegment(sketch, "E2576", {"start": v(-30.22, -36.38) * mm, "end": v(-30.36, -36.55) * mm});
            skLineSegment(sketch, "E2577", {"start": v(-30.36, -36.55) * mm, "end": v(-30.5, -36.72) * mm});
            skLineSegment(sketch, "E2578", {"start": v(-30.5, -36.72) * mm, "end": v(-30.6, -36.9) * mm});
            skLineSegment(sketch, "E2579", {"start": v(-30.6, -36.9) * mm, "end": v(-30.65, -37.09) * mm});
            skLineSegment(sketch, "E2580", {"start": v(-30.65, -37.09) * mm, "end": v(-30.65, -37.3) * mm});
            skLineSegment(sketch, "E2581", {"start": v(-30.65, -37.3) * mm, "end": v(-30.6, -37.5) * mm});
            skLineSegment(sketch, "E2582", {"start": v(-30.6, -37.5) * mm, "end": v(-30.5, -37.67) * mm});
            skLineSegment(sketch, "E2583", {"start": v(-30.5, -37.67) * mm, "end": v(-30.36, -37.81) * mm});
            skLineSegment(sketch, "E2584", {"start": v(-30.36, -37.81) * mm, "end": v(-30.18, -37.92) * mm});
            skLineSegment(sketch, "E2585", {"start": v(-30.18, -37.92) * mm, "end": v(-29.99, -37.97) * mm});
            skLineSegment(sketch, "E2586", {"start": v(-29.99, -37.97) * mm, "end": v(-29.78, -37.97) * mm});
            skLineSegment(sketch, "E2587", {"start": v(-29.78, -37.97) * mm, "end": v(-29.59, -37.92) * mm});
            skLineSegment(sketch, "E2588", {"start": v(-29.59, -37.92) * mm, "end": v(-29.41, -37.82) * mm});
            skLineSegment(sketch, "E2589", {"start": v(-29.41, -37.82) * mm, "end": v(-29.27, -37.67) * mm});
            skLineSegment(sketch, "E2590", {"start": v(-29.27, -37.67) * mm, "end": v(-29.14, -37.5) * mm});
            skLineSegment(sketch, "E2591", {"start": v(-29.14, -37.5) * mm, "end": v(-29, -37.33) * mm});
            skLineSegment(sketch, "E2592", {"start": v(-29, -37.33) * mm, "end": v(-28.88, -37.15) * mm});
            skLineSegment(sketch, "E2593", {"start": v(-28.88, -37.15) * mm, "end": v(-28.75, -36.98) * mm});
            skLineSegment(sketch, "E2594", {"start": v(-28.75, -36.98) * mm, "end": v(-28.62, -36.8) * mm});
            skLineSegment(sketch, "E2595", {"start": v(-28.62, -36.8) * mm, "end": v(-28.49, -36.63) * mm});
            skLineSegment(sketch, "E2596", {"start": v(-28.49, -36.63) * mm, "end": v(-28.36, -36.46) * mm});
            skLineSegment(sketch, "E2597", {"start": v(-28.36, -36.46) * mm, "end": v(-28.22, -36.29) * mm});
            skLineSegment(sketch, "E2598", {"start": v(-28.22, -36.29) * mm, "end": v(-28.1, -36.11) * mm});
            skLineSegment(sketch, "E2599", {"start": v(-28.1, -36.11) * mm, "end": v(-27.96, -35.94) * mm});
            skLineSegment(sketch, "E2600", {"start": v(-27.96, -35.94) * mm, "end": v(-27.83, -35.77) * mm});
            skLineSegment(sketch, "E2601", {"start": v(-27.83, -35.77) * mm, "end": v(-27.7, -35.6) * mm});
            skLineSegment(sketch, "E2602", {"start": v(-27.7, -35.6) * mm, "end": v(-27.57, -35.42) * mm});
            skLineSegment(sketch, "E2603", {"start": v(-27.57, -35.42) * mm, "end": v(-27.44, -35.25) * mm});
            skLineSegment(sketch, "E2604", {"start": v(-27.44, -35.25) * mm, "end": v(-27.31, -35.07) * mm});
            skLineSegment(sketch, "E2605", {"start": v(-27.31, -35.07) * mm, "end": v(-27.13, -35.2) * mm});
            skLineSegment(sketch, "E2606", {"start": v(-27.13, -35.2) * mm, "end": v(-26.95, -35.33) * mm});
            skLineSegment(sketch, "E2607", {"start": v(-26.95, -35.33) * mm, "end": v(-26.77, -35.46) * mm});
            skLineSegment(sketch, "E2608", {"start": v(-26.77, -35.46) * mm, "end": v(-26.59, -35.6) * mm});
            skLineSegment(sketch, "E2609", {"start": v(-26.59, -35.6) * mm, "end": v(-26.4, -35.72) * mm});
            skLineSegment(sketch, "E2610", {"start": v(-26.4, -35.72) * mm, "end": v(-26.23, -35.85) * mm});
            skLineSegment(sketch, "E2611", {"start": v(-26.23, -35.85) * mm, "end": v(-26.04, -35.98) * mm});
            skLineSegment(sketch, "E2612", {"start": v(-26.04, -35.98) * mm, "end": v(-25.86, -36.1) * mm});
            skLineSegment(sketch, "E2613", {"start": v(-25.86, -36.1) * mm, "end": v(-25.68, -36.24) * mm});
            skLineSegment(sketch, "E2614", {"start": v(-25.68, -36.24) * mm, "end": v(-25.54, -36.34) * mm});
            skLineSegment(sketch, "E2615", {"start": v(-25.54, -36.34) * mm, "end": v(-25.66, -36.52) * mm});
            skLineSegment(sketch, "E2616", {"start": v(-25.66, -36.52) * mm, "end": v(-25.78, -36.7) * mm});
            skLineSegment(sketch, "E2617", {"start": v(-25.78, -36.7) * mm, "end": v(-25.9, -36.88) * mm});
            skLineSegment(sketch, "E2618", {"start": v(-25.9, -36.88) * mm, "end": v(-26.02, -37.06) * mm});
            skLineSegment(sketch, "E2619", {"start": v(-26.02, -37.06) * mm, "end": v(-26.14, -37.24) * mm});
            skLineSegment(sketch, "E2620", {"start": v(-26.14, -37.24) * mm, "end": v(-26.26, -37.42) * mm});
            skLineSegment(sketch, "E2621", {"start": v(-26.26, -37.42) * mm, "end": v(-26.39, -37.6) * mm});
            skLineSegment(sketch, "E2622", {"start": v(-26.39, -37.6) * mm, "end": v(-26.5, -37.78) * mm});
            skLineSegment(sketch, "E2623", {"start": v(-26.5, -37.78) * mm, "end": v(-26.63, -37.96) * mm});
            skLineSegment(sketch, "E2624", {"start": v(-26.63, -37.96) * mm, "end": v(-26.75, -38.14) * mm});
            skLineSegment(sketch, "E2625", {"start": v(-26.75, -38.14) * mm, "end": v(-26.87, -38.32) * mm});
            skLineSegment(sketch, "E2626", {"start": v(-26.87, -38.32) * mm, "end": v(-27, -38.5) * mm});
            skLineSegment(sketch, "E2627", {"start": v(-27, -38.5) * mm, "end": v(-27.12, -38.68) * mm});
            skLineSegment(sketch, "E2628", {"start": v(-27.12, -38.68) * mm, "end": v(-27.24, -38.86) * mm});
            skLineSegment(sketch, "E2629", {"start": v(-27.24, -38.86) * mm, "end": v(-27.36, -39.03) * mm});
            skLineSegment(sketch, "E2630", {"start": v(-27.36, -39.03) * mm, "end": v(-27.45, -39.22) * mm});
            skLineSegment(sketch, "E2631", {"start": v(-27.45, -39.22) * mm, "end": v(-27.49, -39.42) * mm});
            skLineSegment(sketch, "E2632", {"start": v(-27.49, -39.42) * mm, "end": v(-27.47, -39.62) * mm});
            skLineSegment(sketch, "E2633", {"start": v(-27.47, -39.62) * mm, "end": v(-27.4, -39.81) * mm});
            skLineSegment(sketch, "E2634", {"start": v(-27.4, -39.81) * mm, "end": v(-27.3, -39.98) * mm});
            skLineSegment(sketch, "E2635", {"start": v(-27.3, -39.98) * mm, "end": v(-27.14, -40.11) * mm});
            skLineSegment(sketch, "E2636", {"start": v(-27.14, -40.11) * mm, "end": v(-26.95, -40.2) * mm});
            skLineSegment(sketch, "E2637", {"start": v(-26.95, -40.2) * mm, "end": v(-26.75, -40.24) * mm});
            skLineSegment(sketch, "E2638", {"start": v(-26.75, -40.24) * mm, "end": v(-26.55, -40.22) * mm});
            skLineSegment(sketch, "E2639", {"start": v(-26.55, -40.22) * mm, "end": v(-26.36, -40.15) * mm});
            skLineSegment(sketch, "E2640", {"start": v(-26.36, -40.15) * mm, "end": v(-26.2, -40.04) * mm});
            skLineSegment(sketch, "E2641", {"start": v(-26.2, -40.04) * mm, "end": v(-26.06, -39.88) * mm});
            skLineSegment(sketch, "E2642", {"start": v(-26.06, -39.88) * mm, "end": v(-25.94, -39.7) * mm});
            skLineSegment(sketch, "E2643", {"start": v(-25.94, -39.7) * mm, "end": v(-25.83, -39.52) * mm});
            skLineSegment(sketch, "E2644", {"start": v(-25.83, -39.52) * mm, "end": v(-25.71, -39.33) * mm});
            skLineSegment(sketch, "E2645", {"start": v(-25.71, -39.33) * mm, "end": v(-25.6, -39.15) * mm});
            skLineSegment(sketch, "E2646", {"start": v(-25.6, -39.15) * mm, "end": v(-25.48, -38.97) * mm});
            skLineSegment(sketch, "E2647", {"start": v(-25.48, -38.97) * mm, "end": v(-25.37, -38.78) * mm});
            skLineSegment(sketch, "E2648", {"start": v(-25.37, -38.78) * mm, "end": v(-25.25, -38.6) * mm});
            skLineSegment(sketch, "E2649", {"start": v(-25.25, -38.6) * mm, "end": v(-25.14, -38.42) * mm});
            skLineSegment(sketch, "E2650", {"start": v(-25.14, -38.42) * mm, "end": v(-25.02, -38.23) * mm});
            skLineSegment(sketch, "E2651", {"start": v(-25.02, -38.23) * mm, "end": v(-24.9, -38.05) * mm});
            skLineSegment(sketch, "E2652", {"start": v(-24.9, -38.05) * mm, "end": v(-24.79, -37.87) * mm});
            skLineSegment(sketch, "E2653", {"start": v(-24.79, -37.87) * mm, "end": v(-24.67, -37.68) * mm});
            skLineSegment(sketch, "E2654", {"start": v(-24.67, -37.68) * mm, "end": v(-24.56, -37.5) * mm});
            skLineSegment(sketch, "E2655", {"start": v(-24.56, -37.5) * mm, "end": v(-24.44, -37.32) * mm});
            skLineSegment(sketch, "E2656", {"start": v(-24.44, -37.32) * mm, "end": v(-24.33, -37.13) * mm});
            skLineSegment(sketch, "E2657", {"start": v(-24.33, -37.13) * mm, "end": v(-24.14, -37.25) * mm});
            skLineSegment(sketch, "E2658", {"start": v(-24.14, -37.25) * mm, "end": v(-23.94, -37.36) * mm});
            skLineSegment(sketch, "E2659", {"start": v(-23.94, -37.36) * mm, "end": v(-23.75, -37.48) * mm});
            skLineSegment(sketch, "E2660", {"start": v(-23.75, -37.48) * mm, "end": v(-23.56, -37.59) * mm});
            skLineSegment(sketch, "E2661", {"start": v(-23.56, -37.59) * mm, "end": v(-23.37, -37.7) * mm});
            skLineSegment(sketch, "E2662", {"start": v(-23.37, -37.7) * mm, "end": v(-23.18, -37.82) * mm});
            skLineSegment(sketch, "E2663", {"start": v(-23.18, -37.82) * mm, "end": v(-22.99, -37.93) * mm});
            skLineSegment(sketch, "E2664", {"start": v(-22.99, -37.93) * mm, "end": v(-22.8, -38.05) * mm});
            skLineSegment(sketch, "E2665", {"start": v(-22.8, -38.05) * mm, "end": v(-22.6, -38.16) * mm});
            skLineSegment(sketch, "E2666", {"start": v(-22.6, -38.16) * mm, "end": v(-22.45, -38.25) * mm});
            skLineSegment(sketch, "E2667", {"start": v(-22.45, -38.25) * mm, "end": v(-22.56, -38.44) * mm});
            skLineSegment(sketch, "E2668", {"start": v(-22.56, -38.44) * mm, "end": v(-22.66, -38.63) * mm});
            skLineSegment(sketch, "E2669", {"start": v(-22.66, -38.63) * mm, "end": v(-22.77, -38.82) * mm});
            skLineSegment(sketch, "E2670", {"start": v(-22.77, -38.82) * mm, "end": v(-22.88, -39) * mm});
            skLineSegment(sketch, "E2671", {"start": v(-22.88, -39) * mm, "end": v(-22.98, -39.2) * mm});
            skLineSegment(sketch, "E2672", {"start": v(-22.98, -39.2) * mm, "end": v(-23.09, -39.38) * mm});
            skLineSegment(sketch, "E2673", {"start": v(-23.09, -39.38) * mm, "end": v(-23.2, -39.57) * mm});
            skLineSegment(sketch, "E2674", {"start": v(-23.2, -39.57) * mm, "end": v(-23.3, -39.76) * mm});
            skLineSegment(sketch, "E2675", {"start": v(-23.3, -39.76) * mm, "end": v(-23.4, -39.95) * mm});
            skLineSegment(sketch, "E2676", {"start": v(-23.4, -39.95) * mm, "end": v(-23.51, -40.14) * mm});
            skLineSegment(sketch, "E2677", {"start": v(-23.51, -40.14) * mm, "end": v(-23.62, -40.33) * mm});
            skLineSegment(sketch, "E2678", {"start": v(-23.62, -40.33) * mm, "end": v(-23.73, -40.52) * mm});
            skLineSegment(sketch, "E2679", {"start": v(-23.73, -40.52) * mm, "end": v(-23.83, -40.7) * mm});
            skLineSegment(sketch, "E2680", {"start": v(-23.83, -40.7) * mm, "end": v(-23.94, -40.9) * mm});
            skLineSegment(sketch, "E2681", {"start": v(-23.94, -40.9) * mm, "end": v(-24.04, -41.08) * mm});
            skLineSegment(sketch, "E2682", {"start": v(-24.04, -41.08) * mm, "end": v(-24.12, -41.27) * mm});
            skLineSegment(sketch, "E2683", {"start": v(-24.12, -41.27) * mm, "end": v(-24.14, -41.48) * mm});
            skLineSegment(sketch, "E2684", {"start": v(-24.14, -41.48) * mm, "end": v(-24.1, -41.68) * mm});
            skLineSegment(sketch, "E2685", {"start": v(-24.1, -41.68) * mm, "end": v(-24.03, -41.86) * mm});
            skLineSegment(sketch, "E2686", {"start": v(-24.03, -41.86) * mm, "end": v(-23.9, -42.02) * mm});
            skLineSegment(sketch, "E2687", {"start": v(-23.9, -42.02) * mm, "end": v(-23.73, -42.14) * mm});
            skLineSegment(sketch, "E2688", {"start": v(-23.73, -42.14) * mm, "end": v(-23.54, -42.21) * mm});
            skLineSegment(sketch, "E2689", {"start": v(-23.54, -42.21) * mm, "end": v(-23.34, -42.23) * mm});
            skLineSegment(sketch, "E2690", {"start": v(-23.34, -42.23) * mm, "end": v(-23.14, -42.2) * mm});
            skLineSegment(sketch, "E2691", {"start": v(-23.14, -42.2) * mm, "end": v(-22.96, -42.12) * mm});
            skLineSegment(sketch, "E2692", {"start": v(-22.96, -42.12) * mm, "end": v(-22.8, -41.99) * mm});
            skLineSegment(sketch, "E2693", {"start": v(-22.8, -41.99) * mm, "end": v(-22.68, -41.82) * mm});
            skLineSegment(sketch, "E2694", {"start": v(-22.68, -41.82) * mm, "end": v(-22.58, -41.63) * mm});
            skLineSegment(sketch, "E2695", {"start": v(-22.58, -41.63) * mm, "end": v(-22.48, -41.44) * mm});
            skLineSegment(sketch, "E2696", {"start": v(-22.48, -41.44) * mm, "end": v(-22.38, -41.25) * mm});
            skLineSegment(sketch, "E2697", {"start": v(-22.38, -41.25) * mm, "end": v(-22.28, -41.05) * mm});
            skLineSegment(sketch, "E2698", {"start": v(-22.28, -41.05) * mm, "end": v(-22.18, -40.86) * mm});
            skLineSegment(sketch, "E2699", {"start": v(-22.18, -40.86) * mm, "end": v(-22.08, -40.67) * mm});
            skLineSegment(sketch, "E2700", {"start": v(-22.08, -40.67) * mm, "end": v(-21.98, -40.48) * mm});
            skLineSegment(sketch, "E2701", {"start": v(-21.98, -40.48) * mm, "end": v(-21.88, -40.28) * mm});
            skLineSegment(sketch, "E2702", {"start": v(-21.88, -40.28) * mm, "end": v(-21.78, -40.1) * mm});
            skLineSegment(sketch, "E2703", {"start": v(-21.78, -40.1) * mm, "end": v(-21.68, -39.9) * mm});
            skLineSegment(sketch, "E2704", {"start": v(-21.68, -39.9) * mm, "end": v(-21.58, -39.7) * mm});
            skLineSegment(sketch, "E2705", {"start": v(-21.58, -39.7) * mm, "end": v(-21.48, -39.52) * mm});
            skLineSegment(sketch, "E2706", {"start": v(-21.48, -39.52) * mm, "end": v(-21.38, -39.32) * mm});
            skLineSegment(sketch, "E2707", {"start": v(-21.38, -39.32) * mm, "end": v(-21.28, -39.13) * mm});
            skLineSegment(sketch, "E2708", {"start": v(-21.28, -39.13) * mm, "end": v(-21.18, -38.94) * mm});
            skLineSegment(sketch, "E2709", {"start": v(-21.18, -38.94) * mm, "end": v(-20.98, -39.04) * mm});
            skLineSegment(sketch, "E2710", {"start": v(-20.98, -39.04) * mm, "end": v(-20.78, -39.13) * mm});
            skLineSegment(sketch, "E2711", {"start": v(-20.78, -39.13) * mm, "end": v(-20.58, -39.23) * mm});
            skLineSegment(sketch, "E2712", {"start": v(-20.58, -39.23) * mm, "end": v(-20.38, -39.33) * mm});
            skLineSegment(sketch, "E2713", {"start": v(-20.38, -39.33) * mm, "end": v(-20.18, -39.43) * mm});
            skLineSegment(sketch, "E2714", {"start": v(-20.18, -39.43) * mm, "end": v(-19.98, -39.53) * mm});
            skLineSegment(sketch, "E2715", {"start": v(-19.98, -39.53) * mm, "end": v(-19.78, -39.62) * mm});
            skLineSegment(sketch, "E2716", {"start": v(-19.78, -39.62) * mm, "end": v(-19.58, -39.72) * mm});
            skLineSegment(sketch, "E2717", {"start": v(-19.58, -39.72) * mm, "end": v(-19.38, -39.82) * mm});
            skLineSegment(sketch, "E2718", {"start": v(-19.38, -39.82) * mm, "end": v(-19.22, -39.9) * mm});
            skLineSegment(sketch, "E2719", {"start": v(-19.22, -39.9) * mm, "end": v(-19.3, -40.1) * mm});
            skLineSegment(sketch, "E2720", {"start": v(-19.3, -40.1) * mm, "end": v(-19.4, -40.3) * mm});
            skLineSegment(sketch, "E2721", {"start": v(-19.4, -40.3) * mm, "end": v(-19.49, -40.49) * mm});
            skLineSegment(sketch, "E2722", {"start": v(-19.49, -40.49) * mm, "end": v(-19.58, -40.69) * mm});
            skLineSegment(sketch, "E2723", {"start": v(-19.58, -40.69) * mm, "end": v(-19.67, -40.88) * mm});
            skLineSegment(sketch, "E2724", {"start": v(-19.67, -40.88) * mm, "end": v(-19.76, -41.08) * mm});
            skLineSegment(sketch, "E2725", {"start": v(-19.76, -41.08) * mm, "end": v(-19.85, -41.28) * mm});
            skLineSegment(sketch, "E2726", {"start": v(-19.85, -41.28) * mm, "end": v(-19.94, -41.47) * mm});
            skLineSegment(sketch, "E2727", {"start": v(-19.94, -41.47) * mm, "end": v(-20.03, -41.67) * mm});
            skLineSegment(sketch, "E2728", {"start": v(-20.03, -41.67) * mm, "end": v(-20.12, -41.87) * mm});
            skLineSegment(sketch, "E2729", {"start": v(-20.12, -41.87) * mm, "end": v(-20.21, -42.06) * mm});
            skLineSegment(sketch, "E2730", {"start": v(-20.21, -42.06) * mm, "end": v(-20.3, -42.26) * mm});
            skLineSegment(sketch, "E2731", {"start": v(-20.3, -42.26) * mm, "end": v(-20.4, -42.46) * mm});
            skLineSegment(sketch, "E2732", {"start": v(-20.4, -42.46) * mm, "end": v(-20.48, -42.66) * mm});
            skLineSegment(sketch, "E2733", {"start": v(-20.48, -42.66) * mm, "end": v(-20.57, -42.85) * mm});
            skLineSegment(sketch, "E2734", {"start": v(-20.57, -42.85) * mm, "end": v(-20.63, -43.05) * mm});
            skLineSegment(sketch, "E2735", {"start": v(-20.63, -43.05) * mm, "end": v(-20.64, -43.25) * mm});
            skLineSegment(sketch, "E2736", {"start": v(-20.64, -43.25) * mm, "end": v(-20.59, -43.45) * mm});
            skLineSegment(sketch, "E2737", {"start": v(-20.59, -43.45) * mm, "end": v(-20.5, -43.63) * mm});
            skLineSegment(sketch, "E2738", {"start": v(-20.5, -43.63) * mm, "end": v(-20.35, -43.77) * mm});
            skLineSegment(sketch, "E2739", {"start": v(-20.35, -43.77) * mm, "end": v(-20.18, -43.88) * mm});
            skLineSegment(sketch, "E2740", {"start": v(-20.18, -43.88) * mm, "end": v(-19.98, -43.94) * mm});
            skLineSegment(sketch, "E2741", {"start": v(-19.98, -43.94) * mm, "end": v(-19.78, -43.94) * mm});
            skLineSegment(sketch, "E2742", {"start": v(-19.78, -43.94) * mm, "end": v(-19.58, -43.9) * mm});
            skLineSegment(sketch, "E2743", {"start": v(-19.58, -43.9) * mm, "end": v(-19.4, -43.8) * mm});
            skLineSegment(sketch, "E2744", {"start": v(-19.4, -43.8) * mm, "end": v(-19.26, -43.65) * mm});
            skLineSegment(sketch, "E2745", {"start": v(-19.26, -43.65) * mm, "end": v(-19.15, -43.48) * mm});
            skLineSegment(sketch, "E2746", {"start": v(-19.15, -43.48) * mm, "end": v(-19.07, -43.28) * mm});
            skLineSegment(sketch, "E2747", {"start": v(-19.07, -43.28) * mm, "end": v(-18.98, -43.08) * mm});
            skLineSegment(sketch, "E2748", {"start": v(-18.98, -43.08) * mm, "end": v(-18.9, -42.88) * mm});
            skLineSegment(sketch, "E2749", {"start": v(-18.9, -42.88) * mm, "end": v(-18.82, -42.68) * mm});
            skLineSegment(sketch, "E2750", {"start": v(-18.82, -42.68) * mm, "end": v(-18.73, -42.48) * mm});
            skLineSegment(sketch, "E2751", {"start": v(-18.73, -42.48) * mm, "end": v(-18.65, -42.28) * mm});
            skLineSegment(sketch, "E2752", {"start": v(-18.65, -42.28) * mm, "end": v(-18.57, -42.08) * mm});
            skLineSegment(sketch, "E2753", {"start": v(-18.57, -42.08) * mm, "end": v(-18.48, -41.88) * mm});
            skLineSegment(sketch, "E2754", {"start": v(-18.48, -41.88) * mm, "end": v(-18.4, -41.68) * mm});
            skLineSegment(sketch, "E2755", {"start": v(-18.4, -41.68) * mm, "end": v(-18.31, -41.48) * mm});
            skLineSegment(sketch, "E2756", {"start": v(-18.31, -41.48) * mm, "end": v(-18.23, -41.28) * mm});
            skLineSegment(sketch, "E2757", {"start": v(-18.23, -41.28) * mm, "end": v(-18.15, -41.08) * mm});
            skLineSegment(sketch, "E2758", {"start": v(-18.15, -41.08) * mm, "end": v(-18.06, -40.88) * mm});
            skLineSegment(sketch, "E2759", {"start": v(-18.06, -40.88) * mm, "end": v(-17.98, -40.68) * mm});
            skLineSegment(sketch, "E2760", {"start": v(-17.98, -40.68) * mm, "end": v(-17.9, -40.48) * mm});
            skLineSegment(sketch, "E2761", {"start": v(-17.9, -40.48) * mm, "end": v(-17.69, -40.56) * mm});
            skLineSegment(sketch, "E2762", {"start": v(-17.69, -40.56) * mm, "end": v(-17.48, -40.64) * mm});
            skLineSegment(sketch, "E2763", {"start": v(-17.48, -40.64) * mm, "end": v(-17.27, -40.72) * mm});
            skLineSegment(sketch, "E2764", {"start": v(-17.27, -40.72) * mm, "end": v(-17.07, -40.8) * mm});
            skLineSegment(sketch, "E2765", {"start": v(-17.07, -40.8) * mm, "end": v(-16.86, -40.88) * mm});
            skLineSegment(sketch, "E2766", {"start": v(-16.86, -40.88) * mm, "end": v(-16.65, -40.96) * mm});
            skLineSegment(sketch, "E2767", {"start": v(-16.65, -40.96) * mm, "end": v(-16.44, -41.04) * mm});
            skLineSegment(sketch, "E2768", {"start": v(-16.44, -41.04) * mm, "end": v(-16.24, -41.13) * mm});
            skLineSegment(sketch, "E2769", {"start": v(-16.24, -41.13) * mm, "end": v(-16.03, -41.2) * mm});
            skLineSegment(sketch, "E2770", {"start": v(-16.03, -41.2) * mm, "end": v(-15.86, -41.27) * mm});
            skLineSegment(sketch, "E2771", {"start": v(-15.86, -41.27) * mm, "end": v(-15.93, -41.48) * mm});
            skLineSegment(sketch, "E2772", {"start": v(-15.93, -41.48) * mm, "end": v(-16, -41.68) * mm});
            skLineSegment(sketch, "E2773", {"start": v(-16, -41.68) * mm, "end": v(-16.08, -41.88) * mm});
            skLineSegment(sketch, "E2774", {"start": v(-16.08, -41.88) * mm, "end": v(-16.16, -42.09) * mm});
            skLineSegment(sketch, "E2775", {"start": v(-16.16, -42.09) * mm, "end": v(-16.23, -42.3) * mm});
            skLineSegment(sketch, "E2776", {"start": v(-16.23, -42.3) * mm, "end": v(-16.3, -42.5) * mm});
            skLineSegment(sketch, "E2777", {"start": v(-16.3, -42.5) * mm, "end": v(-16.38, -42.7) * mm});
            skLineSegment(sketch, "E2778", {"start": v(-16.38, -42.7) * mm, "end": v(-16.45, -42.9) * mm});
            skLineSegment(sketch, "E2779", {"start": v(-16.45, -42.9) * mm, "end": v(-16.52, -43.1) * mm});
            skLineSegment(sketch, "E2780", {"start": v(-16.52, -43.1) * mm, "end": v(-16.6, -43.3) * mm});
            skLineSegment(sketch, "E2781", {"start": v(-16.6, -43.3) * mm, "end": v(-16.67, -43.51) * mm});
            skLineSegment(sketch, "E2782", {"start": v(-16.67, -43.51) * mm, "end": v(-16.75, -43.72) * mm});
            skLineSegment(sketch, "E2783", {"start": v(-16.75, -43.72) * mm, "end": v(-16.82, -43.92) * mm});
            skLineSegment(sketch, "E2784", {"start": v(-16.82, -43.92) * mm, "end": v(-16.9, -44.12) * mm});
            skLineSegment(sketch, "E2785", {"start": v(-16.9, -44.12) * mm, "end": v(-16.97, -44.33) * mm});
            skLineSegment(sketch, "E2786", {"start": v(-16.97, -44.33) * mm, "end": v(-17, -44.53) * mm});
            skLineSegment(sketch, "E2787", {"start": v(-17, -44.53) * mm, "end": v(-17, -44.73) * mm});
            skLineSegment(sketch, "E2788", {"start": v(-17, -44.73) * mm, "end": v(-16.93, -44.92) * mm});
            skLineSegment(sketch, "E2789", {"start": v(-16.93, -44.92) * mm, "end": v(-16.82, -45.1) * mm});
            skLineSegment(sketch, "E2790", {"start": v(-16.82, -45.1) * mm, "end": v(-16.67, -45.23) * mm});
            skLineSegment(sketch, "E2791", {"start": v(-16.67, -45.23) * mm, "end": v(-16.49, -45.32) * mm});
            skLineSegment(sketch, "E2792", {"start": v(-16.49, -45.32) * mm, "end": v(-16.29, -45.36) * mm});
            skLineSegment(sketch, "E2793", {"start": v(-16.29, -45.36) * mm, "end": v(-16.08, -45.35) * mm});
            skLineSegment(sketch, "E2794", {"start": v(-16.08, -45.35) * mm, "end": v(-15.9, -45.28) * mm});
            skLineSegment(sketch, "E2795", {"start": v(-15.9, -45.28) * mm, "end": v(-15.72, -45.17) * mm});
            skLineSegment(sketch, "E2796", {"start": v(-15.72, -45.17) * mm, "end": v(-15.59, -45.01) * mm});
            skLineSegment(sketch, "E2797", {"start": v(-15.59, -45.01) * mm, "end": v(-15.5, -44.83) * mm});
            skLineSegment(sketch, "E2798", {"start": v(-15.5, -44.83) * mm, "end": v(-15.43, -44.63) * mm});
            skLineSegment(sketch, "E2799", {"start": v(-15.43, -44.63) * mm, "end": v(-15.37, -44.42) * mm});
            skLineSegment(sketch, "E2800", {"start": v(-15.37, -44.42) * mm, "end": v(-15.3, -44.21) * mm});
            skLineSegment(sketch, "E2801", {"start": v(-15.3, -44.21) * mm, "end": v(-15.23, -44) * mm});
            skLineSegment(sketch, "E2802", {"start": v(-15.23, -44) * mm, "end": v(-15.16, -43.8) * mm});
            skLineSegment(sketch, "E2803", {"start": v(-15.16, -43.8) * mm, "end": v(-15.1, -43.6) * mm});
            skLineSegment(sketch, "E2804", {"start": v(-15.1, -43.6) * mm, "end": v(-15.03, -43.39) * mm});
            skLineSegment(sketch, "E2805", {"start": v(-15.03, -43.39) * mm, "end": v(-14.96, -43.18) * mm});
            skLineSegment(sketch, "E2806", {"start": v(-14.96, -43.18) * mm, "end": v(-14.9, -42.98) * mm});
            skLineSegment(sketch, "E2807", {"start": v(-14.9, -42.98) * mm, "end": v(-14.83, -42.77) * mm});
            skLineSegment(sketch, "E2808", {"start": v(-14.83, -42.77) * mm, "end": v(-14.76, -42.56) * mm});
            skLineSegment(sketch, "E2809", {"start": v(-14.76, -42.56) * mm, "end": v(-14.7, -42.36) * mm});
            skLineSegment(sketch, "E2810", {"start": v(-14.7, -42.36) * mm, "end": v(-14.63, -42.15) * mm});
            skLineSegment(sketch, "E2811", {"start": v(-14.63, -42.15) * mm, "end": v(-14.56, -41.95) * mm});
            skLineSegment(sketch, "E2812", {"start": v(-14.56, -41.95) * mm, "end": v(-14.5, -41.74) * mm});
            skLineSegment(sketch, "E2813", {"start": v(-14.5, -41.74) * mm, "end": v(-14.28, -41.8) * mm});
            skLineSegment(sketch, "E2814", {"start": v(-14.28, -41.8) * mm, "end": v(-14.07, -41.87) * mm});
            skLineSegment(sketch, "E2815", {"start": v(-14.07, -41.87) * mm, "end": v(-13.85, -41.93) * mm});
            skLineSegment(sketch, "E2816", {"start": v(-13.85, -41.93) * mm, "end": v(-13.64, -42) * mm});
            skLineSegment(sketch, "E2817", {"start": v(-13.64, -42) * mm, "end": v(-13.43, -42.06) * mm});
            skLineSegment(sketch, "E2818", {"start": v(-13.43, -42.06) * mm, "end": v(-13.21, -42.12) * mm});
            skLineSegment(sketch, "E2819", {"start": v(-13.21, -42.12) * mm, "end": v(-13, -42.19) * mm});
            skLineSegment(sketch, "E2820", {"start": v(-13, -42.19) * mm, "end": v(-12.79, -42.25) * mm});
            skLineSegment(sketch, "E2821", {"start": v(-12.79, -42.25) * mm, "end": v(-12.57, -42.31) * mm});
            skLineSegment(sketch, "E2822", {"start": v(-12.57, -42.31) * mm, "end": v(-12.4, -42.36) * mm});
            skLineSegment(sketch, "E2823", {"start": v(-12.4, -42.36) * mm, "end": v(-12.46, -42.57) * mm});
            skLineSegment(sketch, "E2824", {"start": v(-12.46, -42.57) * mm, "end": v(-12.52, -42.78) * mm});
            skLineSegment(sketch, "E2825", {"start": v(-12.52, -42.78) * mm, "end": v(-12.57, -43) * mm});
            skLineSegment(sketch, "E2826", {"start": v(-12.57, -43) * mm, "end": v(-12.63, -43.2) * mm});
            skLineSegment(sketch, "E2827", {"start": v(-12.63, -43.2) * mm, "end": v(-12.69, -43.4) * mm});
            skLineSegment(sketch, "E2828", {"start": v(-12.69, -43.4) * mm, "end": v(-12.74, -43.62) * mm});
            skLineSegment(sketch, "E2829", {"start": v(-12.74, -43.62) * mm, "end": v(-12.8, -43.83) * mm});
            skLineSegment(sketch, "E2830", {"start": v(-12.8, -43.83) * mm, "end": v(-12.86, -44.04) * mm});
            skLineSegment(sketch, "E2831", {"start": v(-12.86, -44.04) * mm, "end": v(-12.91, -44.25) * mm});
            skLineSegment(sketch, "E2832", {"start": v(-12.91, -44.25) * mm, "end": v(-12.97, -44.46) * mm});
            skLineSegment(sketch, "E2833", {"start": v(-12.97, -44.46) * mm, "end": v(-13.03, -44.66) * mm});
            skLineSegment(sketch, "E2834", {"start": v(-13.03, -44.66) * mm, "end": v(-13.08, -44.87) * mm});
            skLineSegment(sketch, "E2835", {"start": v(-13.08, -44.87) * mm, "end": v(-13.14, -45.08) * mm});
            skLineSegment(sketch, "E2836", {"start": v(-13.14, -45.08) * mm, "end": v(-13.2, -45.3) * mm});
            skLineSegment(sketch, "E2837", {"start": v(-13.2, -45.3) * mm, "end": v(-13.25, -45.5) * mm});
            skLineSegment(sketch, "E2838", {"start": v(-13.25, -45.5) * mm, "end": v(-13.28, -45.7) * mm});
            skLineSegment(sketch, "E2839", {"start": v(-13.28, -45.7) * mm, "end": v(-13.25, -45.9) * mm});
            skLineSegment(sketch, "E2840", {"start": v(-13.25, -45.9) * mm, "end": v(-13.17, -46.1) * mm});
            skLineSegment(sketch, "E2841", {"start": v(-13.17, -46.1) * mm, "end": v(-13.04, -46.25) * mm});
            skLineSegment(sketch, "E2842", {"start": v(-13.04, -46.25) * mm, "end": v(-12.88, -46.37) * mm});
            skLineSegment(sketch, "E2843", {"start": v(-12.88, -46.37) * mm, "end": v(-12.7, -46.45) * mm});
            skLineSegment(sketch, "E2844", {"start": v(-12.7, -46.45) * mm, "end": v(-12.49, -46.47) * mm});
            skLineSegment(sketch, "E2845", {"start": v(-12.49, -46.47) * mm, "end": v(-12.29, -46.44) * mm});
            skLineSegment(sketch, "E2846", {"start": v(-12.29, -46.44) * mm, "end": v(-12.1, -46.36) * mm});
            skLineSegment(sketch, "E2847", {"start": v(-12.1, -46.36) * mm, "end": v(-11.94, -46.24) * mm});
            skLineSegment(sketch, "E2848", {"start": v(-11.94, -46.24) * mm, "end": v(-11.82, -46.07) * mm});
            skLineSegment(sketch, "E2849", {"start": v(-11.82, -46.07) * mm, "end": v(-11.75, -45.88) * mm});
            skLineSegment(sketch, "E2850", {"start": v(-11.75, -45.88) * mm, "end": v(-11.7, -45.67) * mm});
            skLineSegment(sketch, "E2851", {"start": v(-11.7, -45.67) * mm, "end": v(-11.65, -45.46) * mm});
            skLineSegment(sketch, "E2852", {"start": v(-11.65, -45.46) * mm, "end": v(-11.6, -45.25) * mm});
            skLineSegment(sketch, "E2853", {"start": v(-11.6, -45.25) * mm, "end": v(-11.55, -45.04) * mm});
            skLineSegment(sketch, "E2854", {"start": v(-11.55, -45.04) * mm, "end": v(-11.5, -44.83) * mm});
            skLineSegment(sketch, "E2855", {"start": v(-11.5, -44.83) * mm, "end": v(-11.45, -44.62) * mm});
            skLineSegment(sketch, "E2856", {"start": v(-11.45, -44.62) * mm, "end": v(-11.4, -44.4) * mm});
            skLineSegment(sketch, "E2857", {"start": v(-11.4, -44.4) * mm, "end": v(-11.35, -44.2) * mm});
            skLineSegment(sketch, "E2858", {"start": v(-11.35, -44.2) * mm, "end": v(-11.3, -43.98) * mm});
            skLineSegment(sketch, "E2859", {"start": v(-11.3, -43.98) * mm, "end": v(-11.25, -43.77) * mm});
            skLineSegment(sketch, "E2860", {"start": v(-11.25, -43.77) * mm, "end": v(-11.2, -43.56) * mm});
            skLineSegment(sketch, "E2861", {"start": v(-11.2, -43.56) * mm, "end": v(-11.15, -43.35) * mm});
            skLineSegment(sketch, "E2862", {"start": v(-11.15, -43.35) * mm, "end": v(-11.1, -43.14) * mm});
            skLineSegment(sketch, "E2863", {"start": v(-11.1, -43.14) * mm, "end": v(-11.05, -42.93) * mm});
            skLineSegment(sketch, "E2864", {"start": v(-11.05, -42.93) * mm, "end": v(-11, -42.72) * mm});
            skLineSegment(sketch, "E2865", {"start": v(-11, -42.72) * mm, "end": v(-10.78, -42.76) * mm});
            skLineSegment(sketch, "E2866", {"start": v(-10.78, -42.76) * mm, "end": v(-10.57, -42.8) * mm});
            skLineSegment(sketch, "E2867", {"start": v(-10.57, -42.8) * mm, "end": v(-10.35, -42.86) * mm});
            skLineSegment(sketch, "E2868", {"start": v(-10.35, -42.86) * mm, "end": v(-10.13, -42.9) * mm});
            skLineSegment(sketch, "E2869", {"start": v(-10.13, -42.9) * mm, "end": v(-9.91, -42.95) * mm});
            skLineSegment(sketch, "E2870", {"start": v(-9.91, -42.95) * mm, "end": v(-9.7, -43) * mm});
            skLineSegment(sketch, "E2871", {"start": v(-9.7, -43) * mm, "end": v(-9.48, -43.04) * mm});
            skLineSegment(sketch, "E2872", {"start": v(-9.48, -43.04) * mm, "end": v(-9.26, -43.08) * mm});
            skLineSegment(sketch, "E2873", {"start": v(-9.26, -43.08) * mm, "end": v(-9.04, -43.13) * mm});
            skLineSegment(sketch, "E2874", {"start": v(-9.04, -43.13) * mm, "end": v(-8.86, -43.17) * mm});
            skLineSegment(sketch, "E2875", {"start": v(-8.86, -43.17) * mm, "end": v(-8.9, -43.38) * mm});
            skLineSegment(sketch, "E2876", {"start": v(-8.9, -43.38) * mm, "end": v(-8.94, -43.6) * mm});
            skLineSegment(sketch, "E2877", {"start": v(-8.94, -43.6) * mm, "end": v(-8.98, -43.8) * mm});
            skLineSegment(sketch, "E2878", {"start": v(-8.98, -43.8) * mm, "end": v(-9.02, -44.02) * mm});
            skLineSegment(sketch, "E2879", {"start": v(-9.02, -44.02) * mm, "end": v(-9.06, -44.23) * mm});
            skLineSegment(sketch, "E2880", {"start": v(-9.06, -44.23) * mm, "end": v(-9.1, -44.45) * mm});
            skLineSegment(sketch, "E2881", {"start": v(-9.1, -44.45) * mm, "end": v(-9.14, -44.66) * mm});
            skLineSegment(sketch, "E2882", {"start": v(-9.14, -44.66) * mm, "end": v(-9.18, -44.87) * mm});
            skLineSegment(sketch, "E2883", {"start": v(-9.18, -44.87) * mm, "end": v(-9.22, -45.08) * mm});
            skLineSegment(sketch, "E2884", {"start": v(-9.22, -45.08) * mm, "end": v(-9.26, -45.3) * mm});
            skLineSegment(sketch, "E2885", {"start": v(-9.26, -45.3) * mm, "end": v(-9.3, -45.51) * mm});
            skLineSegment(sketch, "E2886", {"start": v(-9.3, -45.51) * mm, "end": v(-9.33, -45.72) * mm});
            skLineSegment(sketch, "E2887", {"start": v(-9.33, -45.72) * mm, "end": v(-9.37, -45.94) * mm});
            skLineSegment(sketch, "E2888", {"start": v(-9.37, -45.94) * mm, "end": v(-9.41, -46.15) * mm});
            skLineSegment(sketch, "E2889", {"start": v(-9.41, -46.15) * mm, "end": v(-9.45, -46.36) * mm});
            skLineSegment(sketch, "E2890", {"start": v(-9.45, -46.36) * mm, "end": v(-9.46, -46.57) * mm});
            skLineSegment(sketch, "E2891", {"start": v(-9.46, -46.57) * mm, "end": v(-9.42, -46.77) * mm});
            skLineSegment(sketch, "E2892", {"start": v(-9.42, -46.77) * mm, "end": v(-9.32, -46.95) * mm});
            skLineSegment(sketch, "E2893", {"start": v(-9.32, -46.95) * mm, "end": v(-9.18, -47.1) * mm});
            skLineSegment(sketch, "E2894", {"start": v(-9.18, -47.1) * mm, "end": v(-9.01, -47.2) * mm});
            skLineSegment(sketch, "E2895", {"start": v(-9.01, -47.2) * mm, "end": v(-8.82, -47.26) * mm});
            skLineSegment(sketch, "E2896", {"start": v(-8.82, -47.26) * mm, "end": v(-8.61, -47.27) * mm});
            skLineSegment(sketch, "E2897", {"start": v(-8.61, -47.27) * mm, "end": v(-8.41, -47.22) * mm});
            skLineSegment(sketch, "E2898", {"start": v(-8.41, -47.22) * mm, "end": v(-8.23, -47.13) * mm});
            skLineSegment(sketch, "E2899", {"start": v(-8.23, -47.13) * mm, "end": v(-8.09, -46.99) * mm});
            skLineSegment(sketch, "E2900", {"start": v(-8.09, -46.99) * mm, "end": v(-7.98, -46.81) * mm});
            skLineSegment(sketch, "E2901", {"start": v(-7.98, -46.81) * mm, "end": v(-7.92, -46.62) * mm});
            skLineSegment(sketch, "E2902", {"start": v(-7.92, -46.62) * mm, "end": v(-7.89, -46.4) * mm});
            skLineSegment(sketch, "E2903", {"start": v(-7.89, -46.4) * mm, "end": v(-7.86, -46.2) * mm});
            skLineSegment(sketch, "E2904", {"start": v(-7.86, -46.2) * mm, "end": v(-7.83, -45.98) * mm});
            skLineSegment(sketch, "E2905", {"start": v(-7.83, -45.98) * mm, "end": v(-7.8, -45.76) * mm});
            skLineSegment(sketch, "E2906", {"start": v(-7.8, -45.76) * mm, "end": v(-7.76, -45.55) * mm});
            skLineSegment(sketch, "E2907", {"start": v(-7.76, -45.55) * mm, "end": v(-7.73, -45.33) * mm});
            skLineSegment(sketch, "E2908", {"start": v(-7.73, -45.33) * mm, "end": v(-7.7, -45.12) * mm});
            skLineSegment(sketch, "E2909", {"start": v(-7.7, -45.12) * mm, "end": v(-7.66, -44.9) * mm});
            skLineSegment(sketch, "E2910", {"start": v(-7.66, -44.9) * mm, "end": v(-7.63, -44.7) * mm});
            skLineSegment(sketch, "E2911", {"start": v(-7.63, -44.7) * mm, "end": v(-7.6, -44.48) * mm});
            skLineSegment(sketch, "E2912", {"start": v(-7.6, -44.48) * mm, "end": v(-7.57, -44.26) * mm});
            skLineSegment(sketch, "E2913", {"start": v(-7.57, -44.26) * mm, "end": v(-7.54, -44.05) * mm});
            skLineSegment(sketch, "E2914", {"start": v(-7.54, -44.05) * mm, "end": v(-7.5, -43.83) * mm});
            skLineSegment(sketch, "E2915", {"start": v(-7.5, -43.83) * mm, "end": v(-7.47, -43.62) * mm});
            skLineSegment(sketch, "E2916", {"start": v(-7.47, -43.62) * mm, "end": v(-7.44, -43.4) * mm});
            skLineSegment(sketch, "E2917", {"start": v(-7.44, -43.4) * mm, "end": v(-7.22, -43.43) * mm});
            skLineSegment(sketch, "E2918", {"start": v(-7.22, -43.43) * mm, "end": v(-7, -43.46) * mm});
            skLineSegment(sketch, "E2919", {"start": v(-7, -43.46) * mm, "end": v(-6.78, -43.49) * mm});
            skLineSegment(sketch, "E2920", {"start": v(-6.78, -43.49) * mm, "end": v(-6.56, -43.51) * mm});
            skLineSegment(sketch, "E2921", {"start": v(-6.56, -43.51) * mm, "end": v(-6.33, -43.54) * mm});
            skLineSegment(sketch, "E2922", {"start": v(-6.33, -43.54) * mm, "end": v(-6.11, -43.57) * mm});
            skLineSegment(sketch, "E2923", {"start": v(-6.11, -43.57) * mm, "end": v(-5.9, -43.6) * mm});
            skLineSegment(sketch, "E2924", {"start": v(-5.9, -43.6) * mm, "end": v(-5.67, -43.62) * mm});
            skLineSegment(sketch, "E2925", {"start": v(-5.67, -43.62) * mm, "end": v(-5.45, -43.65) * mm});
            skLineSegment(sketch, "E2926", {"start": v(-5.45, -43.65) * mm, "end": v(-5.27, -43.67) * mm});
            skLineSegment(sketch, "E2927", {"start": v(-5.27, -43.67) * mm, "end": v(-5.3, -43.89) * mm});
            skLineSegment(sketch, "E2928", {"start": v(-5.3, -43.89) * mm, "end": v(-5.32, -44.1) * mm});
            skLineSegment(sketch, "E2929", {"start": v(-5.32, -44.1) * mm, "end": v(-5.34, -44.32) * mm});
            skLineSegment(sketch, "E2930", {"start": v(-5.34, -44.32) * mm, "end": v(-5.36, -44.54) * mm});
            skLineSegment(sketch, "E2931", {"start": v(-5.36, -44.54) * mm, "end": v(-5.38, -44.75) * mm});
            skLineSegment(sketch, "E2932", {"start": v(-5.38, -44.75) * mm, "end": v(-5.4, -44.97) * mm});
            skLineSegment(sketch, "E2933", {"start": v(-5.4, -44.97) * mm, "end": v(-5.42, -45.18) * mm});
            skLineSegment(sketch, "E2934", {"start": v(-5.42, -45.18) * mm, "end": v(-5.44, -45.4) * mm});
            skLineSegment(sketch, "E2935", {"start": v(-5.44, -45.4) * mm, "end": v(-5.47, -45.62) * mm});
            skLineSegment(sketch, "E2936", {"start": v(-5.47, -45.62) * mm, "end": v(-5.49, -45.83) * mm});
            skLineSegment(sketch, "E2937", {"start": v(-5.49, -45.83) * mm, "end": v(-5.5, -46.05) * mm});
            skLineSegment(sketch, "E2938", {"start": v(-5.5, -46.05) * mm, "end": v(-5.53, -46.26) * mm});
            skLineSegment(sketch, "E2939", {"start": v(-5.53, -46.26) * mm, "end": v(-5.55, -46.48) * mm});
            skLineSegment(sketch, "E2940", {"start": v(-5.55, -46.48) * mm, "end": v(-5.57, -46.7) * mm});
            skLineSegment(sketch, "E2941", {"start": v(-5.57, -46.7) * mm, "end": v(-5.6, -46.9) * mm});
            skLineSegment(sketch, "E2942", {"start": v(-5.6, -46.9) * mm, "end": v(-5.59, -47.11) * mm});
            skLineSegment(sketch, "E2943", {"start": v(-5.59, -47.11) * mm, "end": v(-5.53, -47.3) * mm});
            skLineSegment(sketch, "E2944", {"start": v(-5.53, -47.3) * mm, "end": v(-5.42, -47.48) * mm});
            skLineSegment(sketch, "E2945", {"start": v(-5.42, -47.48) * mm, "end": v(-5.27, -47.62) * mm});
            skLineSegment(sketch, "E2946", {"start": v(-5.27, -47.62) * mm, "end": v(-5.08, -47.7) * mm});
            skLineSegment(sketch, "E2947", {"start": v(-5.08, -47.7) * mm, "end": v(-4.89, -47.75) * mm});
            skLineSegment(sketch, "E2948", {"start": v(-4.89, -47.75) * mm, "end": v(-4.68, -47.74) * mm});
            skLineSegment(sketch, "E2949", {"start": v(-4.68, -47.74) * mm, "end": v(-4.49, -47.68) * mm});
            skLineSegment(sketch, "E2950", {"start": v(-4.49, -47.68) * mm, "end": v(-4.32, -47.57) * mm});
            skLineSegment(sketch, "E2951", {"start": v(-4.32, -47.57) * mm, "end": v(-4.18, -47.42) * mm});
            skLineSegment(sketch, "E2952", {"start": v(-4.18, -47.42) * mm, "end": v(-4.09, -47.24) * mm});
            skLineSegment(sketch, "E2953", {"start": v(-4.09, -47.24) * mm, "end": v(-4.05, -47.04) * mm});
            skLineSegment(sketch, "E2954", {"start": v(-4.05, -47.04) * mm, "end": v(-4.03, -46.82) * mm});
            skLineSegment(sketch, "E2955", {"start": v(-4.03, -46.82) * mm, "end": v(-4.02, -46.6) * mm});
            skLineSegment(sketch, "E2956", {"start": v(-4.02, -46.6) * mm, "end": v(-4, -46.39) * mm});
            skLineSegment(sketch, "E2957", {"start": v(-4, -46.39) * mm, "end": v(-4, -46.17) * mm});
            skLineSegment(sketch, "E2958", {"start": v(-4, -46.17) * mm, "end": v(-3.98, -45.96) * mm});
            skLineSegment(sketch, "E2959", {"start": v(-3.98, -45.96) * mm, "end": v(-3.96, -45.74) * mm});
            skLineSegment(sketch, "E2960", {"start": v(-3.96, -45.74) * mm, "end": v(-3.95, -45.52) * mm});
            skLineSegment(sketch, "E2961", {"start": v(-3.95, -45.52) * mm, "end": v(-3.93, -45.3) * mm});
            skLineSegment(sketch, "E2962", {"start": v(-3.93, -45.3) * mm, "end": v(-3.92, -45.1) * mm});
            skLineSegment(sketch, "E2963", {"start": v(-3.92, -45.1) * mm, "end": v(-3.9, -44.87) * mm});
            skLineSegment(sketch, "E2964", {"start": v(-3.9, -44.87) * mm, "end": v(-3.9, -44.66) * mm});
            skLineSegment(sketch, "E2965", {"start": v(-3.9, -44.66) * mm, "end": v(-3.88, -44.44) * mm});
            skLineSegment(sketch, "E2966", {"start": v(-3.88, -44.44) * mm, "end": v(-3.86, -44.23) * mm});
            skLineSegment(sketch, "E2967", {"start": v(-3.86, -44.23) * mm, "end": v(-3.85, -44) * mm});
            skLineSegment(sketch, "E2968", {"start": v(-3.85, -44) * mm, "end": v(-3.83, -43.8) * mm});
            skLineSegment(sketch, "E2969", {"start": v(-3.83, -43.8) * mm, "end": v(-3.61, -43.8) * mm});
            skLineSegment(sketch, "E2970", {"start": v(-3.61, -43.8) * mm, "end": v(-3.39, -43.81) * mm});
            skLineSegment(sketch, "E2971", {"start": v(-3.39, -43.81) * mm, "end": v(-3.17, -43.82) * mm});
            skLineSegment(sketch, "E2972", {"start": v(-3.17, -43.82) * mm, "end": v(-2.94, -43.83) * mm});
            skLineSegment(sketch, "E2973", {"start": v(-2.94, -43.83) * mm, "end": v(-2.72, -43.84) * mm});
            skLineSegment(sketch, "E2974", {"start": v(-2.72, -43.84) * mm, "end": v(-2.5, -43.85) * mm});
            skLineSegment(sketch, "E2975", {"start": v(-2.5, -43.85) * mm, "end": v(-2.28, -43.86) * mm});
            skLineSegment(sketch, "E2976", {"start": v(-2.28, -43.86) * mm, "end": v(-2.05, -43.87) * mm});
            skLineSegment(sketch, "E2977", {"start": v(-2.05, -43.87) * mm, "end": v(-1.83, -43.88) * mm});
            skLineSegment(sketch, "E2978", {"start": v(-1.83, -43.88) * mm, "end": v(-1.65, -43.88) * mm});
            skLineSegment(sketch, "E2979", {"start": v(-1.65, -43.88) * mm, "end": v(-1.65, -44.1) * mm});
            skLineSegment(sketch, "E2980", {"start": v(-1.65, -44.1) * mm, "end": v(-1.66, -44.32) * mm});
            skLineSegment(sketch, "E2981", {"start": v(-1.66, -44.32) * mm, "end": v(-1.66, -44.53) * mm});
            skLineSegment(sketch, "E2982", {"start": v(-1.66, -44.53) * mm, "end": v(-1.67, -44.75) * mm});
            skLineSegment(sketch, "E2983", {"start": v(-1.67, -44.75) * mm, "end": v(-1.67, -44.97) * mm});
            skLineSegment(sketch, "E2984", {"start": v(-1.67, -44.97) * mm, "end": v(-1.67, -45.18) * mm});
            skLineSegment(sketch, "E2985", {"start": v(-1.67, -45.18) * mm, "end": v(-1.68, -45.4) * mm});
            skLineSegment(sketch, "E2986", {"start": v(-1.68, -45.4) * mm, "end": v(-1.68, -45.62) * mm});
            skLineSegment(sketch, "E2987", {"start": v(-1.68, -45.62) * mm, "end": v(-1.68, -45.83) * mm});
            skLineSegment(sketch, "E2988", {"start": v(-1.68, -45.83) * mm, "end": v(-1.69, -46.05) * mm});
            skLineSegment(sketch, "E2989", {"start": v(-1.69, -46.05) * mm, "end": v(-1.7, -46.27) * mm});
            skLineSegment(sketch, "E2990", {"start": v(-1.7, -46.27) * mm, "end": v(-1.7, -46.48) * mm});
            skLineSegment(sketch, "E2991", {"start": v(-1.7, -46.48) * mm, "end": v(-1.7, -46.7) * mm});
            skLineSegment(sketch, "E2992", {"start": v(-1.7, -46.7) * mm, "end": v(-1.7, -46.92) * mm});
            skLineSegment(sketch, "E2993", {"start": v(-1.7, -46.92) * mm, "end": v(-1.7, -47.13) * mm});
            skLineSegment(sketch, "E2994", {"start": v(-1.7, -47.13) * mm, "end": v(-1.68, -47.34) * mm});
            skLineSegment(sketch, "E2995", {"start": v(-1.68, -47.34) * mm, "end": v(-1.6, -47.52) * mm});
            skLineSegment(sketch, "E2996", {"start": v(-1.6, -47.52) * mm, "end": v(-1.48, -47.69) * mm});
            skLineSegment(sketch, "E2997", {"start": v(-1.48, -47.69) * mm, "end": v(-1.32, -47.81) * mm});
            skLineSegment(sketch, "E2998", {"start": v(-1.32, -47.81) * mm, "end": v(-1.13, -47.89) * mm});
            skLineSegment(sketch, "E2999", {"start": v(-1.13, -47.89) * mm, "end": v(-0.93, -47.92) * mm});
            skLineSegment(sketch, "E3000", {"start": v(-0.93, -47.92) * mm, "end": v(-0.73, -47.89) * mm});
            skLineSegment(sketch, "E3001", {"start": v(-0.73, -47.89) * mm, "end": v(-0.54, -47.81) * mm});
            skLineSegment(sketch, "E3002", {"start": v(-0.54, -47.81) * mm, "end": v(-0.38, -47.69) * mm});
            skLineSegment(sketch, "E3003", {"start": v(-0.38, -47.69) * mm, "end": v(-0.26, -47.52) * mm});
            skLineSegment(sketch, "E3004", {"start": v(-0.26, -47.52) * mm, "end": v(-0.18, -47.34) * mm});
            skLineSegment(sketch, "E3005", {"start": v(-0.18, -47.34) * mm, "end": v(-0.15, -47.13) * mm});
            skLineSegment(sketch, "E3006", {"start": v(-0.15, -47.13) * mm, "end": v(-0.16, -46.92) * mm});
            skLineSegment(sketch, "E3007", {"start": v(-0.16, -46.92) * mm, "end": v(-0.16, -46.7) * mm});
            skLineSegment(sketch, "E3008", {"start": v(-0.16, -46.7) * mm, "end": v(-0.16, -46.48) * mm});
            skLineSegment(sketch, "E3009", {"start": v(-0.16, -46.48) * mm, "end": v(-0.17, -46.27) * mm});
            skLineSegment(sketch, "E3010", {"start": v(-0.17, -46.27) * mm, "end": v(-0.17, -46.05) * mm});
            skLineSegment(sketch, "E3011", {"start": v(-0.17, -46.05) * mm, "end": v(-0.17, -45.83) * mm});
            skLineSegment(sketch, "E3012", {"start": v(-0.17, -45.83) * mm, "end": v(-0.18, -45.62) * mm});
            skLineSegment(sketch, "E3013", {"start": v(-0.18, -45.62) * mm, "end": v(-0.18, -45.4) * mm});
            skLineSegment(sketch, "E3014", {"start": v(-0.18, -45.4) * mm, "end": v(-0.19, -45.18) * mm});
            skLineSegment(sketch, "E3015", {"start": v(-0.19, -45.18) * mm, "end": v(-0.19, -44.97) * mm});
            skLineSegment(sketch, "E3016", {"start": v(-0.19, -44.97) * mm, "end": v(-0.2, -44.75) * mm});
            skLineSegment(sketch, "E3017", {"start": v(-0.2, -44.75) * mm, "end": v(-0.2, -44.53) * mm});
            skLineSegment(sketch, "E3018", {"start": v(-0.2, -44.53) * mm, "end": v(-0.2, -44.32) * mm});
            skLineSegment(sketch, "E3019", {"start": v(-0.2, -44.32) * mm, "end": v(-0.2, -44.1) * mm});
            skLineSegment(sketch, "E3020", {"start": v(-0.2, -44.1) * mm, "end": v(-0.2, -43.88) * mm});
            skLineSegment(sketch, "E3021", {"start": v(-0.2, -43.88) * mm, "end": v(0.02, -43.87) * mm});
            skLineSegment(sketch, "E3022", {"start": v(0.02, -43.87) * mm, "end": v(0.24, -43.87) * mm});
            skLineSegment(sketch, "E3023", {"start": v(0.24, -43.87) * mm, "end": v(0.46, -43.86) * mm});
            skLineSegment(sketch, "E3024", {"start": v(0.46, -43.86) * mm, "end": v(0.68, -43.85) * mm});
            skLineSegment(sketch, "E3025", {"start": v(0.68, -43.85) * mm, "end": v(0.9, -43.84) * mm});
            skLineSegment(sketch, "E3026", {"start": v(0.9, -43.84) * mm, "end": v(1.13, -43.83) * mm});
            skLineSegment(sketch, "E3027", {"start": v(1.13, -43.83) * mm, "end": v(1.35, -43.82) * mm});
            skLineSegment(sketch, "E3028", {"start": v(1.35, -43.82) * mm, "end": v(1.57, -43.81) * mm});
            skLineSegment(sketch, "E3029", {"start": v(1.57, -43.81) * mm, "end": v(1.8, -43.8) * mm});
            skLineSegment(sketch, "E3030", {"start": v(1.8, -43.8) * mm, "end": v(1.98, -43.8) * mm});
            skLineSegment(sketch, "E3031", {"start": v(1.98, -43.8) * mm, "end": v(1.99, -44) * mm});
            skLineSegment(sketch, "E3032", {"start": v(1.99, -44) * mm, "end": v(2, -44.23) * mm});
            skLineSegment(sketch, "E3033", {"start": v(2, -44.23) * mm, "end": v(2.02, -44.44) * mm});
            skLineSegment(sketch, "E3034", {"start": v(2.02, -44.44) * mm, "end": v(2.03, -44.66) * mm});
            skLineSegment(sketch, "E3035", {"start": v(2.03, -44.66) * mm, "end": v(2.05, -44.87) * mm});
            skLineSegment(sketch, "E3036", {"start": v(2.05, -44.87) * mm, "end": v(2.06, -45.1) * mm});
            skLineSegment(sketch, "E3037", {"start": v(2.06, -45.1) * mm, "end": v(2.08, -45.3) * mm});
            skLineSegment(sketch, "E3038", {"start": v(2.08, -45.3) * mm, "end": v(2.09, -45.52) * mm});
            skLineSegment(sketch, "E3039", {"start": v(2.09, -45.52) * mm, "end": v(2.1, -45.74) * mm});
            skLineSegment(sketch, "E3040", {"start": v(2.1, -45.74) * mm, "end": v(2.12, -45.96) * mm});
            skLineSegment(sketch, "E3041", {"start": v(2.12, -45.96) * mm, "end": v(2.13, -46.17) * mm});
            skLineSegment(sketch, "E3042", {"start": v(2.13, -46.17) * mm, "end": v(2.15, -46.39) * mm});
            skLineSegment(sketch, "E3043", {"start": v(2.15, -46.39) * mm, "end": v(2.16, -46.6) * mm});
            skLineSegment(sketch, "E3044", {"start": v(2.16, -46.6) * mm, "end": v(2.18, -46.82) * mm});
            skLineSegment(sketch, "E3045", {"start": v(2.18, -46.82) * mm, "end": v(2.2, -47.04) * mm});
            skLineSegment(sketch, "E3046", {"start": v(2.2, -47.04) * mm, "end": v(2.23, -47.24) * mm});
            skLineSegment(sketch, "E3047", {"start": v(2.23, -47.24) * mm, "end": v(2.32, -47.42) * mm});
            skLineSegment(sketch, "E3048", {"start": v(2.32, -47.42) * mm, "end": v(2.46, -47.57) * mm});
            skLineSegment(sketch, "E3049", {"start": v(2.46, -47.57) * mm, "end": v(2.63, -47.68) * mm});
            skLineSegment(sketch, "E3050", {"start": v(2.63, -47.68) * mm, "end": v(2.82, -47.74) * mm});
            skLineSegment(sketch, "E3051", {"start": v(2.82, -47.74) * mm, "end": v(3.03, -47.75) * mm});
            skLineSegment(sketch, "E3052", {"start": v(3.03, -47.75) * mm, "end": v(3.23, -47.7) * mm});
            skLineSegment(sketch, "E3053", {"start": v(3.23, -47.7) * mm, "end": v(3.4, -47.62) * mm});
            skLineSegment(sketch, "E3054", {"start": v(3.4, -47.62) * mm, "end": v(3.56, -47.48) * mm});
            skLineSegment(sketch, "E3055", {"start": v(3.56, -47.48) * mm, "end": v(3.67, -47.3) * mm});
            skLineSegment(sketch, "E3056", {"start": v(3.67, -47.3) * mm, "end": v(3.73, -47.11) * mm});
            skLineSegment(sketch, "E3057", {"start": v(3.73, -47.11) * mm, "end": v(3.74, -46.9) * mm});
            skLineSegment(sketch, "E3058", {"start": v(3.74, -46.9) * mm, "end": v(3.71, -46.7) * mm});
            skLineSegment(sketch, "E3059", {"start": v(3.71, -46.7) * mm, "end": v(3.7, -46.48) * mm});
            skLineSegment(sketch, "E3060", {"start": v(3.7, -46.48) * mm, "end": v(3.67, -46.26) * mm});
            skLineSegment(sketch, "E3061", {"start": v(3.67, -46.26) * mm, "end": v(3.65, -46.05) * mm});
            skLineSegment(sketch, "E3062", {"start": v(3.65, -46.05) * mm, "end": v(3.63, -45.83) * mm});
            skLineSegment(sketch, "E3063", {"start": v(3.63, -45.83) * mm, "end": v(3.6, -45.62) * mm});
            skLineSegment(sketch, "E3064", {"start": v(3.6, -45.62) * mm, "end": v(3.59, -45.4) * mm});
            skLineSegment(sketch, "E3065", {"start": v(3.59, -45.4) * mm, "end": v(3.56, -45.18) * mm});
            skLineSegment(sketch, "E3066", {"start": v(3.56, -45.18) * mm, "end": v(3.54, -44.97) * mm});
            skLineSegment(sketch, "E3067", {"start": v(3.54, -44.97) * mm, "end": v(3.52, -44.75) * mm});
            skLineSegment(sketch, "E3068", {"start": v(3.52, -44.75) * mm, "end": v(3.5, -44.54) * mm});
            skLineSegment(sketch, "E3069", {"start": v(3.5, -44.54) * mm, "end": v(3.48, -44.32) * mm});
            skLineSegment(sketch, "E3070", {"start": v(3.48, -44.32) * mm, "end": v(3.46, -44.1) * mm});
            skLineSegment(sketch, "E3071", {"start": v(3.46, -44.1) * mm, "end": v(3.44, -43.89) * mm});
            skLineSegment(sketch, "E3072", {"start": v(3.44, -43.89) * mm, "end": v(3.41, -43.67) * mm});
            skLineSegment(sketch, "E3073", {"start": v(3.41, -43.67) * mm, "end": v(3.64, -43.65) * mm});
            skLineSegment(sketch, "E3074", {"start": v(3.64, -43.65) * mm, "end": v(3.86, -43.62) * mm});
            skLineSegment(sketch, "E3075", {"start": v(3.86, -43.62) * mm, "end": v(4.08, -43.6) * mm});
            skLineSegment(sketch, "E3076", {"start": v(4.08, -43.6) * mm, "end": v(4.3, -43.56) * mm});
            skLineSegment(sketch, "E3077", {"start": v(4.3, -43.56) * mm, "end": v(4.52, -43.54) * mm});
            skLineSegment(sketch, "E3078", {"start": v(4.52, -43.54) * mm, "end": v(4.74, -43.5) * mm});
            skLineSegment(sketch, "E3079", {"start": v(4.74, -43.5) * mm, "end": v(4.96, -43.48) * mm});
            skLineSegment(sketch, "E3080", {"start": v(4.96, -43.48) * mm, "end": v(5.18, -43.45) * mm});
            skLineSegment(sketch, "E3081", {"start": v(5.18, -43.45) * mm, "end": v(5.4, -43.43) * mm});
            skLineSegment(sketch, "E3082", {"start": v(5.4, -43.43) * mm, "end": v(5.58, -43.4) * mm});
            skLineSegment(sketch, "E3083", {"start": v(5.58, -43.4) * mm, "end": v(5.61, -43.62) * mm});
            skLineSegment(sketch, "E3084", {"start": v(5.61, -43.62) * mm, "end": v(5.65, -43.83) * mm});
            skLineSegment(sketch, "E3085", {"start": v(5.65, -43.83) * mm, "end": v(5.68, -44.05) * mm});
            skLineSegment(sketch, "E3086", {"start": v(5.68, -44.05) * mm, "end": v(5.71, -44.26) * mm});
            skLineSegment(sketch, "E3087", {"start": v(5.71, -44.26) * mm, "end": v(5.74, -44.48) * mm});
            skLineSegment(sketch, "E3088", {"start": v(5.74, -44.48) * mm, "end": v(5.77, -44.7) * mm});
            skLineSegment(sketch, "E3089", {"start": v(5.77, -44.7) * mm, "end": v(5.8, -44.9) * mm});
            skLineSegment(sketch, "E3090", {"start": v(5.8, -44.9) * mm, "end": v(5.84, -45.12) * mm});
            skLineSegment(sketch, "E3091", {"start": v(5.84, -45.12) * mm, "end": v(5.87, -45.33) * mm});
            skLineSegment(sketch, "E3092", {"start": v(5.87, -45.33) * mm, "end": v(5.9, -45.55) * mm});
            skLineSegment(sketch, "E3093", {"start": v(5.9, -45.55) * mm, "end": v(5.94, -45.76) * mm});
            skLineSegment(sketch, "E3094", {"start": v(5.94, -45.76) * mm, "end": v(5.97, -45.98) * mm});
            skLineSegment(sketch, "E3095", {"start": v(5.97, -45.98) * mm, "end": v(6, -46.2) * mm});
            skLineSegment(sketch, "E3096", {"start": v(6, -46.2) * mm, "end": v(6.03, -46.4) * mm});
            skLineSegment(sketch, "E3097", {"start": v(6.03, -46.4) * mm, "end": v(6.06, -46.62) * mm});
            skLineSegment(sketch, "E3098", {"start": v(6.06, -46.62) * mm, "end": v(6.12, -46.81) * mm});
            skLineSegment(sketch, "E3099", {"start": v(6.12, -46.81) * mm, "end": v(6.23, -46.99) * mm});
            skLineSegment(sketch, "E3100", {"start": v(6.23, -46.99) * mm, "end": v(6.38, -47.13) * mm});
            skLineSegment(sketch, "E3101", {"start": v(6.38, -47.13) * mm, "end": v(6.56, -47.22) * mm});
            skLineSegment(sketch, "E3102", {"start": v(6.56, -47.22) * mm, "end": v(6.75, -47.27) * mm});
            skLineSegment(sketch, "E3103", {"start": v(6.75, -47.27) * mm, "end": v(6.96, -47.26) * mm});
            skLineSegment(sketch, "E3104", {"start": v(6.96, -47.26) * mm, "end": v(7.15, -47.2) * mm});
            skLineSegment(sketch, "E3105", {"start": v(7.15, -47.2) * mm, "end": v(7.32, -47.1) * mm});
            skLineSegment(sketch, "E3106", {"start": v(7.32, -47.1) * mm, "end": v(7.46, -46.95) * mm});
            skLineSegment(sketch, "E3107", {"start": v(7.46, -46.95) * mm, "end": v(7.56, -46.77) * mm});
            skLineSegment(sketch, "E3108", {"start": v(7.56, -46.77) * mm, "end": v(7.6, -46.57) * mm});
            skLineSegment(sketch, "E3109", {"start": v(7.6, -46.57) * mm, "end": v(7.6, -46.36) * mm});
            skLineSegment(sketch, "E3110", {"start": v(7.6, -46.36) * mm, "end": v(7.56, -46.15) * mm});
            skLineSegment(sketch, "E3111", {"start": v(7.56, -46.15) * mm, "end": v(7.52, -45.94) * mm});
            skLineSegment(sketch, "E3112", {"start": v(7.52, -45.94) * mm, "end": v(7.48, -45.72) * mm});
            skLineSegment(sketch, "E3113", {"start": v(7.48, -45.72) * mm, "end": v(7.44, -45.51) * mm});
            skLineSegment(sketch, "E3114", {"start": v(7.44, -45.51) * mm, "end": v(7.4, -45.3) * mm});
            skLineSegment(sketch, "E3115", {"start": v(7.4, -45.3) * mm, "end": v(7.36, -45.08) * mm});
            skLineSegment(sketch, "E3116", {"start": v(7.36, -45.08) * mm, "end": v(7.32, -44.87) * mm});
            skLineSegment(sketch, "E3117", {"start": v(7.32, -44.87) * mm, "end": v(7.28, -44.66) * mm});
            skLineSegment(sketch, "E3118", {"start": v(7.28, -44.66) * mm, "end": v(7.24, -44.45) * mm});
            skLineSegment(sketch, "E3119", {"start": v(7.24, -44.45) * mm, "end": v(7.2, -44.23) * mm});
            skLineSegment(sketch, "E3120", {"start": v(7.2, -44.23) * mm, "end": v(7.16, -44.02) * mm});
            skLineSegment(sketch, "E3121", {"start": v(7.16, -44.02) * mm, "end": v(7.12, -43.8) * mm});
            skLineSegment(sketch, "E3122", {"start": v(7.12, -43.8) * mm, "end": v(7.08, -43.6) * mm});
            skLineSegment(sketch, "E3123", {"start": v(7.08, -43.6) * mm, "end": v(7.05, -43.38) * mm});
            skLineSegment(sketch, "E3124", {"start": v(7.05, -43.38) * mm, "end": v(7, -43.17) * mm});
            skLineSegment(sketch, "E3125", {"start": v(7, -43.17) * mm, "end": v(7.22, -43.12) * mm});
            skLineSegment(sketch, "E3126", {"start": v(7.22, -43.12) * mm, "end": v(7.44, -43.08) * mm});
            skLineSegment(sketch, "E3127", {"start": v(7.44, -43.08) * mm, "end": v(7.66, -43.03) * mm});
            skLineSegment(sketch, "E3128", {"start": v(7.66, -43.03) * mm, "end": v(7.88, -42.98) * mm});
            skLineSegment(sketch, "E3129", {"start": v(7.88, -42.98) * mm, "end": v(8.1, -42.94) * mm});
            skLineSegment(sketch, "E3130", {"start": v(8.1, -42.94) * mm, "end": v(8.31, -42.9) * mm});
            skLineSegment(sketch, "E3131", {"start": v(8.31, -42.9) * mm, "end": v(8.53, -42.85) * mm});
            skLineSegment(sketch, "E3132", {"start": v(8.53, -42.85) * mm, "end": v(8.75, -42.8) * mm});
            skLineSegment(sketch, "E3133", {"start": v(8.75, -42.8) * mm, "end": v(8.97, -42.76) * mm});
            skLineSegment(sketch, "E3134", {"start": v(8.97, -42.76) * mm, "end": v(9.14, -42.72) * mm});
            skLineSegment(sketch, "E3135", {"start": v(9.14, -42.72) * mm, "end": v(9.2, -42.93) * mm});
            skLineSegment(sketch, "E3136", {"start": v(9.2, -42.93) * mm, "end": v(9.24, -43.14) * mm});
            skLineSegment(sketch, "E3137", {"start": v(9.24, -43.14) * mm, "end": v(9.3, -43.35) * mm});
            skLineSegment(sketch, "E3138", {"start": v(9.3, -43.35) * mm, "end": v(9.34, -43.56) * mm});
            skLineSegment(sketch, "E3139", {"start": v(9.34, -43.56) * mm, "end": v(9.4, -43.77) * mm});
            skLineSegment(sketch, "E3140", {"start": v(9.4, -43.77) * mm, "end": v(9.44, -43.98) * mm});
            skLineSegment(sketch, "E3141", {"start": v(9.44, -43.98) * mm, "end": v(9.5, -44.2) * mm});
            skLineSegment(sketch, "E3142", {"start": v(9.5, -44.2) * mm, "end": v(9.54, -44.4) * mm});
            skLineSegment(sketch, "E3143", {"start": v(9.54, -44.4) * mm, "end": v(9.6, -44.62) * mm});
            skLineSegment(sketch, "E3144", {"start": v(9.6, -44.62) * mm, "end": v(9.64, -44.83) * mm});
            skLineSegment(sketch, "E3145", {"start": v(9.64, -44.83) * mm, "end": v(9.7, -45.04) * mm});
            skLineSegment(sketch, "E3146", {"start": v(9.7, -45.04) * mm, "end": v(9.74, -45.25) * mm});
            skLineSegment(sketch, "E3147", {"start": v(9.74, -45.25) * mm, "end": v(9.8, -45.46) * mm});
            skLineSegment(sketch, "E3148", {"start": v(9.8, -45.46) * mm, "end": v(9.84, -45.67) * mm});
            skLineSegment(sketch, "E3149", {"start": v(9.84, -45.67) * mm, "end": v(9.89, -45.88) * mm});
            skLineSegment(sketch, "E3150", {"start": v(9.89, -45.88) * mm, "end": v(9.96, -46.07) * mm});
            skLineSegment(sketch, "E3151", {"start": v(9.96, -46.07) * mm, "end": v(10.08, -46.24) * mm});
            skLineSegment(sketch, "E3152", {"start": v(10.08, -46.24) * mm, "end": v(10.24, -46.36) * mm});
            skLineSegment(sketch, "E3153", {"start": v(10.24, -46.36) * mm, "end": v(10.43, -46.44) * mm});
            skLineSegment(sketch, "E3154", {"start": v(10.43, -46.44) * mm, "end": v(10.63, -46.47) * mm});
            skLineSegment(sketch, "E3155", {"start": v(10.63, -46.47) * mm, "end": v(10.83, -46.45) * mm});
            skLineSegment(sketch, "E3156", {"start": v(10.83, -46.45) * mm, "end": v(11.02, -46.37) * mm});
            skLineSegment(sketch, "E3157", {"start": v(11.02, -46.37) * mm, "end": v(11.19, -46.25) * mm});
            skLineSegment(sketch, "E3158", {"start": v(11.19, -46.25) * mm, "end": v(11.31, -46.1) * mm});
            skLineSegment(sketch, "E3159", {"start": v(11.31, -46.1) * mm, "end": v(11.4, -45.9) * mm});
            skLineSegment(sketch, "E3160", {"start": v(11.4, -45.9) * mm, "end": v(11.42, -45.7) * mm});
            skLineSegment(sketch, "E3161", {"start": v(11.42, -45.7) * mm, "end": v(11.4, -45.5) * mm});
            skLineSegment(sketch, "E3162", {"start": v(11.4, -45.5) * mm, "end": v(11.34, -45.3) * mm});
            skLineSegment(sketch, "E3163", {"start": v(11.34, -45.3) * mm, "end": v(11.28, -45.08) * mm});
            skLineSegment(sketch, "E3164", {"start": v(11.28, -45.08) * mm, "end": v(11.22, -44.87) * mm});
            skLineSegment(sketch, "E3165", {"start": v(11.22, -44.87) * mm, "end": v(11.17, -44.66) * mm});
            skLineSegment(sketch, "E3166", {"start": v(11.17, -44.66) * mm, "end": v(11.11, -44.46) * mm});
            skLineSegment(sketch, "E3167", {"start": v(11.11, -44.46) * mm, "end": v(11.05, -44.25) * mm});
            skLineSegment(sketch, "E3168", {"start": v(11.05, -44.25) * mm, "end": v(11, -44.04) * mm});
            skLineSegment(sketch, "E3169", {"start": v(11, -44.04) * mm, "end": v(10.94, -43.83) * mm});
            skLineSegment(sketch, "E3170", {"start": v(10.94, -43.83) * mm, "end": v(10.88, -43.62) * mm});
            skLineSegment(sketch, "E3171", {"start": v(10.88, -43.62) * mm, "end": v(10.83, -43.4) * mm});
            skLineSegment(sketch, "E3172", {"start": v(10.83, -43.4) * mm, "end": v(10.77, -43.2) * mm});
            skLineSegment(sketch, "E3173", {"start": v(10.77, -43.2) * mm, "end": v(10.71, -43) * mm});
            skLineSegment(sketch, "E3174", {"start": v(10.71, -43) * mm, "end": v(10.66, -42.78) * mm});
            skLineSegment(sketch, "E3175", {"start": v(10.66, -42.78) * mm, "end": v(10.6, -42.57) * mm});
            skLineSegment(sketch, "E3176", {"start": v(10.6, -42.57) * mm, "end": v(10.54, -42.36) * mm});
            skLineSegment(sketch, "E3177", {"start": v(10.54, -42.36) * mm, "end": v(10.76, -42.3) * mm});
            skLineSegment(sketch, "E3178", {"start": v(10.76, -42.3) * mm, "end": v(10.97, -42.24) * mm});
            skLineSegment(sketch, "E3179", {"start": v(10.97, -42.24) * mm, "end": v(11.18, -42.17) * mm});
            skLineSegment(sketch, "E3180", {"start": v(11.18, -42.17) * mm, "end": v(11.4, -42.1) * mm});
            skLineSegment(sketch, "E3181", {"start": v(11.4, -42.1) * mm, "end": v(11.61, -42.05) * mm});
            skLineSegment(sketch, "E3182", {"start": v(11.61, -42.05) * mm, "end": v(11.82, -41.98) * mm});
            skLineSegment(sketch, "E3183", {"start": v(11.82, -41.98) * mm, "end": v(12.04, -41.92) * mm});
            skLineSegment(sketch, "E3184", {"start": v(12.04, -41.92) * mm, "end": v(12.25, -41.86) * mm});
            skLineSegment(sketch, "E3185", {"start": v(12.25, -41.86) * mm, "end": v(12.46, -41.8) * mm});
            skLineSegment(sketch, "E3186", {"start": v(12.46, -41.8) * mm, "end": v(12.64, -41.74) * mm});
            skLineSegment(sketch, "E3187", {"start": v(12.64, -41.74) * mm, "end": v(12.7, -41.95) * mm});
            skLineSegment(sketch, "E3188", {"start": v(12.7, -41.95) * mm, "end": v(12.77, -42.15) * mm});
            skLineSegment(sketch, "E3189", {"start": v(12.77, -42.15) * mm, "end": v(12.84, -42.36) * mm});
            skLineSegment(sketch, "E3190", {"start": v(12.84, -42.36) * mm, "end": v(12.9, -42.56) * mm});
            skLineSegment(sketch, "E3191", {"start": v(12.9, -42.56) * mm, "end": v(12.97, -42.77) * mm});
            skLineSegment(sketch, "E3192", {"start": v(12.97, -42.77) * mm, "end": v(13.04, -42.98) * mm});
            skLineSegment(sketch, "E3193", {"start": v(13.04, -42.98) * mm, "end": v(13.1, -43.18) * mm});
            skLineSegment(sketch, "E3194", {"start": v(13.1, -43.18) * mm, "end": v(13.17, -43.39) * mm});
            skLineSegment(sketch, "E3195", {"start": v(13.17, -43.39) * mm, "end": v(13.24, -43.6) * mm});
            skLineSegment(sketch, "E3196", {"start": v(13.24, -43.6) * mm, "end": v(13.3, -43.8) * mm});
            skLineSegment(sketch, "E3197", {"start": v(13.3, -43.8) * mm, "end": v(13.37, -44) * mm});
            skLineSegment(sketch, "E3198", {"start": v(13.37, -44) * mm, "end": v(13.44, -44.21) * mm});
            skLineSegment(sketch, "E3199", {"start": v(13.44, -44.21) * mm, "end": v(13.5, -44.42) * mm});
            skLineSegment(sketch, "E3200", {"start": v(13.5, -44.42) * mm, "end": v(13.57, -44.63) * mm});
            skLineSegment(sketch, "E3201", {"start": v(13.57, -44.63) * mm, "end": v(13.64, -44.83) * mm});
            skLineSegment(sketch, "E3202", {"start": v(13.64, -44.83) * mm, "end": v(13.73, -45.01) * mm});
            skLineSegment(sketch, "E3203", {"start": v(13.73, -45.01) * mm, "end": v(13.86, -45.17) * mm});
            skLineSegment(sketch, "E3204", {"start": v(13.86, -45.17) * mm, "end": v(14.03, -45.28) * mm});
            skLineSegment(sketch, "E3205", {"start": v(14.03, -45.28) * mm, "end": v(14.23, -45.35) * mm});
            skLineSegment(sketch, "E3206", {"start": v(14.23, -45.35) * mm, "end": v(14.43, -45.36) * mm});
            skLineSegment(sketch, "E3207", {"start": v(14.43, -45.36) * mm, "end": v(14.63, -45.32) * mm});
            skLineSegment(sketch, "E3208", {"start": v(14.63, -45.32) * mm, "end": v(14.81, -45.23) * mm});
            skLineSegment(sketch, "E3209", {"start": v(14.81, -45.23) * mm, "end": v(14.96, -45.1) * mm});
            skLineSegment(sketch, "E3210", {"start": v(14.96, -45.1) * mm, "end": v(15.08, -44.92) * mm});
            skLineSegment(sketch, "E3211", {"start": v(15.08, -44.92) * mm, "end": v(15.14, -44.73) * mm});
            skLineSegment(sketch, "E3212", {"start": v(15.14, -44.73) * mm, "end": v(15.15, -44.53) * mm});
            skLineSegment(sketch, "E3213", {"start": v(15.15, -44.53) * mm, "end": v(15.1, -44.33) * mm});
            skLineSegment(sketch, "E3214", {"start": v(15.1, -44.33) * mm, "end": v(15.04, -44.12) * mm});
            skLineSegment(sketch, "E3215", {"start": v(15.04, -44.12) * mm, "end": v(14.96, -43.92) * mm});
            skLineSegment(sketch, "E3216", {"start": v(14.96, -43.92) * mm, "end": v(14.89, -43.72) * mm});
            skLineSegment(sketch, "E3217", {"start": v(14.89, -43.72) * mm, "end": v(14.81, -43.51) * mm});
            skLineSegment(sketch, "E3218", {"start": v(14.81, -43.51) * mm, "end": v(14.74, -43.3) * mm});
            skLineSegment(sketch, "E3219", {"start": v(14.74, -43.3) * mm, "end": v(14.67, -43.1) * mm});
            skLineSegment(sketch, "E3220", {"start": v(14.67, -43.1) * mm, "end": v(14.6, -42.9) * mm});
            skLineSegment(sketch, "E3221", {"start": v(14.6, -42.9) * mm, "end": v(14.52, -42.7) * mm});
            skLineSegment(sketch, "E3222", {"start": v(14.52, -42.7) * mm, "end": v(14.45, -42.5) * mm});
            skLineSegment(sketch, "E3223", {"start": v(14.45, -42.5) * mm, "end": v(14.37, -42.3) * mm});
            skLineSegment(sketch, "E3224", {"start": v(14.37, -42.3) * mm, "end": v(14.3, -42.09) * mm});
            skLineSegment(sketch, "E3225", {"start": v(14.3, -42.09) * mm, "end": v(14.22, -41.88) * mm});
            skLineSegment(sketch, "E3226", {"start": v(14.22, -41.88) * mm, "end": v(14.15, -41.68) * mm});
            skLineSegment(sketch, "E3227", {"start": v(14.15, -41.68) * mm, "end": v(14.08, -41.48) * mm});
            skLineSegment(sketch, "E3228", {"start": v(14.08, -41.48) * mm, "end": v(14, -41.27) * mm});
            skLineSegment(sketch, "E3229", {"start": v(14, -41.27) * mm, "end": v(14.21, -41.2) * mm});
            skLineSegment(sketch, "E3230", {"start": v(14.21, -41.2) * mm, "end": v(14.42, -41.1) * mm});
            skLineSegment(sketch, "E3231", {"start": v(14.42, -41.1) * mm, "end": v(14.63, -41.03) * mm});
            skLineSegment(sketch, "E3232", {"start": v(14.63, -41.03) * mm, "end": v(14.83, -40.95) * mm});
            skLineSegment(sketch, "E3233", {"start": v(14.83, -40.95) * mm, "end": v(15.04, -40.87) * mm});
            skLineSegment(sketch, "E3234", {"start": v(15.04, -40.87) * mm, "end": v(15.25, -40.79) * mm});
            skLineSegment(sketch, "E3235", {"start": v(15.25, -40.79) * mm, "end": v(15.46, -40.7) * mm});
            skLineSegment(sketch, "E3236", {"start": v(15.46, -40.7) * mm, "end": v(15.66, -40.62) * mm});
            skLineSegment(sketch, "E3237", {"start": v(15.66, -40.62) * mm, "end": v(15.87, -40.54) * mm});
            skLineSegment(sketch, "E3238", {"start": v(15.87, -40.54) * mm, "end": v(16.04, -40.48) * mm});
            skLineSegment(sketch, "E3239", {"start": v(16.04, -40.48) * mm, "end": v(16.12, -40.68) * mm});
            skLineSegment(sketch, "E3240", {"start": v(16.12, -40.68) * mm, "end": v(16.2, -40.88) * mm});
            skLineSegment(sketch, "E3241", {"start": v(16.2, -40.88) * mm, "end": v(16.29, -41.08) * mm});
            skLineSegment(sketch, "E3242", {"start": v(16.29, -41.08) * mm, "end": v(16.37, -41.28) * mm});
            skLineSegment(sketch, "E3243", {"start": v(16.37, -41.28) * mm, "end": v(16.46, -41.48) * mm});
            skLineSegment(sketch, "E3244", {"start": v(16.46, -41.48) * mm, "end": v(16.54, -41.68) * mm});
            skLineSegment(sketch, "E3245", {"start": v(16.54, -41.68) * mm, "end": v(16.62, -41.88) * mm});
            skLineSegment(sketch, "E3246", {"start": v(16.62, -41.88) * mm, "end": v(16.7, -42.08) * mm});
            skLineSegment(sketch, "E3247", {"start": v(16.7, -42.08) * mm, "end": v(16.8, -42.28) * mm});
            skLineSegment(sketch, "E3248", {"start": v(16.8, -42.28) * mm, "end": v(16.88, -42.48) * mm});
            skLineSegment(sketch, "E3249", {"start": v(16.88, -42.48) * mm, "end": v(16.96, -42.68) * mm});
            skLineSegment(sketch, "E3250", {"start": v(16.96, -42.68) * mm, "end": v(17.04, -42.88) * mm});
            skLineSegment(sketch, "E3251", {"start": v(17.04, -42.88) * mm, "end": v(17.13, -43.08) * mm});
            skLineSegment(sketch, "E3252", {"start": v(17.13, -43.08) * mm, "end": v(17.21, -43.28) * mm});
            skLineSegment(sketch, "E3253", {"start": v(17.21, -43.28) * mm, "end": v(17.3, -43.48) * mm});
            skLineSegment(sketch, "E3254", {"start": v(17.3, -43.48) * mm, "end": v(17.4, -43.65) * mm});
            skLineSegment(sketch, "E3255", {"start": v(17.4, -43.65) * mm, "end": v(17.54, -43.8) * mm});
            skLineSegment(sketch, "E3256", {"start": v(17.54, -43.8) * mm, "end": v(17.72, -43.9) * mm});
            skLineSegment(sketch, "E3257", {"start": v(17.72, -43.9) * mm, "end": v(17.92, -43.94) * mm});
            skLineSegment(sketch, "E3258", {"start": v(17.92, -43.94) * mm, "end": v(18.12, -43.94) * mm});
            skLineSegment(sketch, "E3259", {"start": v(18.12, -43.94) * mm, "end": v(18.32, -43.88) * mm});
            skLineSegment(sketch, "E3260", {"start": v(18.32, -43.88) * mm, "end": v(18.5, -43.77) * mm});
            skLineSegment(sketch, "E3261", {"start": v(18.5, -43.77) * mm, "end": v(18.63, -43.63) * mm});
            skLineSegment(sketch, "E3262", {"start": v(18.63, -43.63) * mm, "end": v(18.73, -43.45) * mm});
            skLineSegment(sketch, "E3263", {"start": v(18.73, -43.45) * mm, "end": v(18.78, -43.25) * mm});
            skLineSegment(sketch, "E3264", {"start": v(18.78, -43.25) * mm, "end": v(18.77, -43.05) * mm});
            skLineSegment(sketch, "E3265", {"start": v(18.77, -43.05) * mm, "end": v(18.71, -42.85) * mm});
            skLineSegment(sketch, "E3266", {"start": v(18.71, -42.85) * mm, "end": v(18.62, -42.66) * mm});
            skLineSegment(sketch, "E3267", {"start": v(18.62, -42.66) * mm, "end": v(18.53, -42.46) * mm});
            skLineSegment(sketch, "E3268", {"start": v(18.53, -42.46) * mm, "end": v(18.44, -42.26) * mm});
            skLineSegment(sketch, "E3269", {"start": v(18.44, -42.26) * mm, "end": v(18.35, -42.06) * mm});
            skLineSegment(sketch, "E3270", {"start": v(18.35, -42.06) * mm, "end": v(18.26, -41.87) * mm});
            skLineSegment(sketch, "E3271", {"start": v(18.26, -41.87) * mm, "end": v(18.17, -41.67) * mm});
            skLineSegment(sketch, "E3272", {"start": v(18.17, -41.67) * mm, "end": v(18.08, -41.47) * mm});
            skLineSegment(sketch, "E3273", {"start": v(18.08, -41.47) * mm, "end": v(18, -41.28) * mm});
            skLineSegment(sketch, "E3274", {"start": v(18, -41.28) * mm, "end": v(17.9, -41.08) * mm});
            skLineSegment(sketch, "E3275", {"start": v(17.9, -41.08) * mm, "end": v(17.81, -40.88) * mm});
            skLineSegment(sketch, "E3276", {"start": v(17.81, -40.88) * mm, "end": v(17.72, -40.69) * mm});
            skLineSegment(sketch, "E3277", {"start": v(17.72, -40.69) * mm, "end": v(17.63, -40.49) * mm});
            skLineSegment(sketch, "E3278", {"start": v(17.63, -40.49) * mm, "end": v(17.54, -40.3) * mm});
            skLineSegment(sketch, "E3279", {"start": v(17.54, -40.3) * mm, "end": v(17.45, -40.1) * mm});
            skLineSegment(sketch, "E3280", {"start": v(17.45, -40.1) * mm, "end": v(17.36, -39.9) * mm});
            skLineSegment(sketch, "E3281", {"start": v(17.36, -39.9) * mm, "end": v(17.56, -39.8) * mm});
            skLineSegment(sketch, "E3282", {"start": v(17.56, -39.8) * mm, "end": v(17.76, -39.7) * mm});
            skLineSegment(sketch, "E3283", {"start": v(17.76, -39.7) * mm, "end": v(17.96, -39.6) * mm});
            skLineSegment(sketch, "E3284", {"start": v(17.96, -39.6) * mm, "end": v(18.16, -39.5) * mm});
            skLineSegment(sketch, "E3285", {"start": v(18.16, -39.5) * mm, "end": v(18.36, -39.4) * mm});
            skLineSegment(sketch, "E3286", {"start": v(18.36, -39.4) * mm, "end": v(18.56, -39.31) * mm});
            skLineSegment(sketch, "E3287", {"start": v(18.56, -39.31) * mm, "end": v(18.76, -39.21) * mm});
            skLineSegment(sketch, "E3288", {"start": v(18.76, -39.21) * mm, "end": v(18.96, -39.12) * mm});
            skLineSegment(sketch, "E3289", {"start": v(18.96, -39.12) * mm, "end": v(19.16, -39.02) * mm});
            skLineSegment(sketch, "E3290", {"start": v(19.16, -39.02) * mm, "end": v(19.32, -38.94) * mm});
            skLineSegment(sketch, "E3291", {"start": v(19.32, -38.94) * mm, "end": v(19.42, -39.13) * mm});
            skLineSegment(sketch, "E3292", {"start": v(19.42, -39.13) * mm, "end": v(19.52, -39.32) * mm});
            skLineSegment(sketch, "E3293", {"start": v(19.52, -39.32) * mm, "end": v(19.62, -39.52) * mm});
            skLineSegment(sketch, "E3294", {"start": v(19.62, -39.52) * mm, "end": v(19.72, -39.7) * mm});
            skLineSegment(sketch, "E3295", {"start": v(19.72, -39.7) * mm, "end": v(19.82, -39.9) * mm});
            skLineSegment(sketch, "E3296", {"start": v(19.82, -39.9) * mm, "end": v(19.92, -40.1) * mm});
            skLineSegment(sketch, "E3297", {"start": v(19.92, -40.1) * mm, "end": v(20.02, -40.28) * mm});
            skLineSegment(sketch, "E3298", {"start": v(20.02, -40.28) * mm, "end": v(20.12, -40.48) * mm});
            skLineSegment(sketch, "E3299", {"start": v(20.12, -40.48) * mm, "end": v(20.22, -40.67) * mm});
            skLineSegment(sketch, "E3300", {"start": v(20.22, -40.67) * mm, "end": v(20.32, -40.86) * mm});
            skLineSegment(sketch, "E3301", {"start": v(20.32, -40.86) * mm, "end": v(20.42, -41.05) * mm});
            skLineSegment(sketch, "E3302", {"start": v(20.42, -41.05) * mm, "end": v(20.52, -41.25) * mm});
            skLineSegment(sketch, "E3303", {"start": v(20.52, -41.25) * mm, "end": v(20.62, -41.44) * mm});
            skLineSegment(sketch, "E3304", {"start": v(20.62, -41.44) * mm, "end": v(20.72, -41.63) * mm});
            skLineSegment(sketch, "E3305", {"start": v(20.72, -41.63) * mm, "end": v(20.82, -41.82) * mm});
            skLineSegment(sketch, "E3306", {"start": v(20.82, -41.82) * mm, "end": v(20.94, -41.99) * mm});
            skLineSegment(sketch, "E3307", {"start": v(20.94, -41.99) * mm, "end": v(21.1, -42.12) * mm});
            skLineSegment(sketch, "E3308", {"start": v(21.1, -42.12) * mm, "end": v(21.28, -42.2) * mm});
            skLineSegment(sketch, "E3309", {"start": v(21.28, -42.2) * mm, "end": v(21.48, -42.23) * mm});
            skLineSegment(sketch, "E3310", {"start": v(21.48, -42.23) * mm, "end": v(21.69, -42.21) * mm});
            skLineSegment(sketch, "E3311", {"start": v(21.69, -42.21) * mm, "end": v(21.88, -42.14) * mm});
            skLineSegment(sketch, "E3312", {"start": v(21.88, -42.14) * mm, "end": v(22.04, -42.02) * mm});
            skLineSegment(sketch, "E3313", {"start": v(22.04, -42.02) * mm, "end": v(22.17, -41.86) * mm});
            skLineSegment(sketch, "E3314", {"start": v(22.17, -41.86) * mm, "end": v(22.25, -41.68) * mm});
            skLineSegment(sketch, "E3315", {"start": v(22.25, -41.68) * mm, "end": v(22.28, -41.48) * mm});
            skLineSegment(sketch, "E3316", {"start": v(22.28, -41.48) * mm, "end": v(22.26, -41.27) * mm});
            skLineSegment(sketch, "E3317", {"start": v(22.26, -41.27) * mm, "end": v(22.19, -41.08) * mm});
            skLineSegment(sketch, "E3318", {"start": v(22.19, -41.08) * mm, "end": v(22.08, -40.9) * mm});
            skLineSegment(sketch, "E3319", {"start": v(22.08, -40.9) * mm, "end": v(21.97, -40.7) * mm});
            skLineSegment(sketch, "E3320", {"start": v(21.97, -40.7) * mm, "end": v(21.87, -40.52) * mm});
            skLineSegment(sketch, "E3321", {"start": v(21.87, -40.52) * mm, "end": v(21.76, -40.33) * mm});
            skLineSegment(sketch, "E3322", {"start": v(21.76, -40.33) * mm, "end": v(21.66, -40.14) * mm});
            skLineSegment(sketch, "E3323", {"start": v(21.66, -40.14) * mm, "end": v(21.55, -39.95) * mm});
            skLineSegment(sketch, "E3324", {"start": v(21.55, -39.95) * mm, "end": v(21.44, -39.76) * mm});
            skLineSegment(sketch, "E3325", {"start": v(21.44, -39.76) * mm, "end": v(21.34, -39.57) * mm});
            skLineSegment(sketch, "E3326", {"start": v(21.34, -39.57) * mm, "end": v(21.23, -39.38) * mm});
            skLineSegment(sketch, "E3327", {"start": v(21.23, -39.38) * mm, "end": v(21.12, -39.2) * mm});
            skLineSegment(sketch, "E3328", {"start": v(21.12, -39.2) * mm, "end": v(21.02, -39) * mm});
            skLineSegment(sketch, "E3329", {"start": v(21.02, -39) * mm, "end": v(20.91, -38.82) * mm});
            skLineSegment(sketch, "E3330", {"start": v(20.91, -38.82) * mm, "end": v(20.8, -38.63) * mm});
            skLineSegment(sketch, "E3331", {"start": v(20.8, -38.63) * mm, "end": v(20.7, -38.44) * mm});
            skLineSegment(sketch, "E3332", {"start": v(20.7, -38.44) * mm, "end": v(20.6, -38.25) * mm});
            skLineSegment(sketch, "E3333", {"start": v(20.6, -38.25) * mm, "end": v(20.78, -38.14) * mm});
            skLineSegment(sketch, "E3334", {"start": v(20.78, -38.14) * mm, "end": v(20.98, -38.02) * mm});
            skLineSegment(sketch, "E3335", {"start": v(20.98, -38.02) * mm, "end": v(21.17, -37.9) * mm});
            skLineSegment(sketch, "E3336", {"start": v(21.17, -37.9) * mm, "end": v(21.36, -37.8) * mm});
            skLineSegment(sketch, "E3337", {"start": v(21.36, -37.8) * mm, "end": v(21.55, -37.68) * mm});
            skLineSegment(sketch, "E3338", {"start": v(21.55, -37.68) * mm, "end": v(21.74, -37.57) * mm});
            skLineSegment(sketch, "E3339", {"start": v(21.74, -37.57) * mm, "end": v(21.93, -37.45) * mm});
            skLineSegment(sketch, "E3340", {"start": v(21.93, -37.45) * mm, "end": v(22.12, -37.34) * mm});
            skLineSegment(sketch, "E3341", {"start": v(22.12, -37.34) * mm, "end": v(22.31, -37.23) * mm});
            skLineSegment(sketch, "E3342", {"start": v(22.31, -37.23) * mm, "end": v(22.47, -37.13) * mm});
            skLineSegment(sketch, "E3343", {"start": v(22.47, -37.13) * mm, "end": v(22.58, -37.32) * mm});
            skLineSegment(sketch, "E3344", {"start": v(22.58, -37.32) * mm, "end": v(22.7, -37.5) * mm});
            skLineSegment(sketch, "E3345", {"start": v(22.7, -37.5) * mm, "end": v(22.82, -37.68) * mm});
            skLineSegment(sketch, "E3346", {"start": v(22.82, -37.68) * mm, "end": v(22.93, -37.87) * mm});
            skLineSegment(sketch, "E3347", {"start": v(22.93, -37.87) * mm, "end": v(23.05, -38.05) * mm});
            skLineSegment(sketch, "E3348", {"start": v(23.05, -38.05) * mm, "end": v(23.16, -38.23) * mm});
            skLineSegment(sketch, "E3349", {"start": v(23.16, -38.23) * mm, "end": v(23.28, -38.42) * mm});
            skLineSegment(sketch, "E3350", {"start": v(23.28, -38.42) * mm, "end": v(23.4, -38.6) * mm});
            skLineSegment(sketch, "E3351", {"start": v(23.4, -38.6) * mm, "end": v(23.5, -38.78) * mm});
            skLineSegment(sketch, "E3352", {"start": v(23.5, -38.78) * mm, "end": v(23.62, -38.97) * mm});
            skLineSegment(sketch, "E3353", {"start": v(23.62, -38.97) * mm, "end": v(23.74, -39.15) * mm});
            skLineSegment(sketch, "E3354", {"start": v(23.74, -39.15) * mm, "end": v(23.85, -39.33) * mm});
            skLineSegment(sketch, "E3355", {"start": v(23.85, -39.33) * mm, "end": v(23.97, -39.52) * mm});
            skLineSegment(sketch, "E3356", {"start": v(23.97, -39.52) * mm, "end": v(24.09, -39.7) * mm});
            skLineSegment(sketch, "E3357", {"start": v(24.09, -39.7) * mm, "end": v(24.2, -39.88) * mm});
            skLineSegment(sketch, "E3358", {"start": v(24.2, -39.88) * mm, "end": v(24.33, -40.04) * mm});
            skLineSegment(sketch, "E3359", {"start": v(24.33, -40.04) * mm, "end": v(24.5, -40.15) * mm});
            skLineSegment(sketch, "E3360", {"start": v(24.5, -40.15) * mm, "end": v(24.7, -40.22) * mm});
            skLineSegment(sketch, "E3361", {"start": v(24.7, -40.22) * mm, "end": v(24.9, -40.24) * mm});
            skLineSegment(sketch, "E3362", {"start": v(24.9, -40.24) * mm, "end": v(25.1, -40.2) * mm});
            skLineSegment(sketch, "E3363", {"start": v(25.1, -40.2) * mm, "end": v(25.28, -40.11) * mm});
            skLineSegment(sketch, "E3364", {"start": v(25.28, -40.11) * mm, "end": v(25.43, -39.98) * mm});
            skLineSegment(sketch, "E3365", {"start": v(25.43, -39.98) * mm, "end": v(25.55, -39.81) * mm});
            skLineSegment(sketch, "E3366", {"start": v(25.55, -39.81) * mm, "end": v(25.61, -39.62) * mm});
            skLineSegment(sketch, "E3367", {"start": v(25.61, -39.62) * mm, "end": v(25.63, -39.42) * mm});
            skLineSegment(sketch, "E3368", {"start": v(25.63, -39.42) * mm, "end": v(25.59, -39.22) * mm});
            skLineSegment(sketch, "E3369", {"start": v(25.59, -39.22) * mm, "end": v(25.5, -39.03) * mm});
            skLineSegment(sketch, "E3370", {"start": v(25.5, -39.03) * mm, "end": v(25.38, -38.86) * mm});
            skLineSegment(sketch, "E3371", {"start": v(25.38, -38.86) * mm, "end": v(25.26, -38.68) * mm});
            skLineSegment(sketch, "E3372", {"start": v(25.26, -38.68) * mm, "end": v(25.14, -38.5) * mm});
            skLineSegment(sketch, "E3373", {"start": v(25.14, -38.5) * mm, "end": v(25.01, -38.32) * mm});
            skLineSegment(sketch, "E3374", {"start": v(25.01, -38.32) * mm, "end": v(24.9, -38.14) * mm});
            skLineSegment(sketch, "E3375", {"start": v(24.9, -38.14) * mm, "end": v(24.77, -37.96) * mm});
            skLineSegment(sketch, "E3376", {"start": v(24.77, -37.96) * mm, "end": v(24.65, -37.78) * mm});
            skLineSegment(sketch, "E3377", {"start": v(24.65, -37.78) * mm, "end": v(24.53, -37.6) * mm});
            skLineSegment(sketch, "E3378", {"start": v(24.53, -37.6) * mm, "end": v(24.4, -37.42) * mm});
            skLineSegment(sketch, "E3379", {"start": v(24.4, -37.42) * mm, "end": v(24.29, -37.24) * mm});
            skLineSegment(sketch, "E3380", {"start": v(24.29, -37.24) * mm, "end": v(24.16, -37.06) * mm});
            skLineSegment(sketch, "E3381", {"start": v(24.16, -37.06) * mm, "end": v(24.04, -36.88) * mm});
            skLineSegment(sketch, "E3382", {"start": v(24.04, -36.88) * mm, "end": v(23.92, -36.7) * mm});
            skLineSegment(sketch, "E3383", {"start": v(23.92, -36.7) * mm, "end": v(23.8, -36.52) * mm});
            skLineSegment(sketch, "E3384", {"start": v(23.8, -36.52) * mm, "end": v(23.68, -36.34) * mm});
            skLineSegment(sketch, "E3385", {"start": v(23.68, -36.34) * mm, "end": v(23.86, -36.21) * mm});
            skLineSegment(sketch, "E3386", {"start": v(23.86, -36.21) * mm, "end": v(24.04, -36.08) * mm});
            skLineSegment(sketch, "E3387", {"start": v(24.04, -36.08) * mm, "end": v(24.22, -35.95) * mm});
            skLineSegment(sketch, "E3388", {"start": v(24.22, -35.95) * mm, "end": v(24.4, -35.83) * mm});
            skLineSegment(sketch, "E3389", {"start": v(24.4, -35.83) * mm, "end": v(24.58, -35.7) * mm});
            skLineSegment(sketch, "E3390", {"start": v(24.58, -35.7) * mm, "end": v(24.77, -35.57) * mm});
            skLineSegment(sketch, "E3391", {"start": v(24.77, -35.57) * mm, "end": v(24.95, -35.44) * mm});
            skLineSegment(sketch, "E3392", {"start": v(24.95, -35.44) * mm, "end": v(25.13, -35.3) * mm});
            skLineSegment(sketch, "E3393", {"start": v(25.13, -35.3) * mm, "end": v(25.3, -35.18) * mm});
            skLineSegment(sketch, "E3394", {"start": v(25.3, -35.18) * mm, "end": v(25.46, -35.07) * mm});
            skLineSegment(sketch, "E3395", {"start": v(25.46, -35.07) * mm, "end": v(25.59, -35.25) * mm});
            skLineSegment(sketch, "E3396", {"start": v(25.59, -35.25) * mm, "end": v(25.72, -35.42) * mm});
            skLineSegment(sketch, "E3397", {"start": v(25.72, -35.42) * mm, "end": v(25.85, -35.6) * mm});
            skLineSegment(sketch, "E3398", {"start": v(25.85, -35.6) * mm, "end": v(25.98, -35.77) * mm});
            skLineSegment(sketch, "E3399", {"start": v(25.98, -35.77) * mm, "end": v(26.1, -35.94) * mm});
            skLineSegment(sketch, "E3400", {"start": v(26.1, -35.94) * mm, "end": v(26.24, -36.11) * mm});
            skLineSegment(sketch, "E3401", {"start": v(26.24, -36.11) * mm, "end": v(26.37, -36.29) * mm});
            skLineSegment(sketch, "E3402", {"start": v(26.37, -36.29) * mm, "end": v(26.5, -36.46) * mm});
            skLineSegment(sketch, "E3403", {"start": v(26.5, -36.46) * mm, "end": v(26.63, -36.63) * mm});
            skLineSegment(sketch, "E3404", {"start": v(26.63, -36.63) * mm, "end": v(26.76, -36.8) * mm});
            skLineSegment(sketch, "E3405", {"start": v(26.76, -36.8) * mm, "end": v(26.89, -36.98) * mm});
            skLineSegment(sketch, "E3406", {"start": v(26.89, -36.98) * mm, "end": v(27.02, -37.15) * mm});
            skLineSegment(sketch, "E3407", {"start": v(27.02, -37.15) * mm, "end": v(27.15, -37.33) * mm});
            skLineSegment(sketch, "E3408", {"start": v(27.15, -37.33) * mm, "end": v(27.28, -37.5) * mm});
            skLineSegment(sketch, "E3409", {"start": v(27.28, -37.5) * mm, "end": v(27.4, -37.67) * mm});
            skLineSegment(sketch, "E3410", {"start": v(27.4, -37.67) * mm, "end": v(27.55, -37.82) * mm});
            skLineSegment(sketch, "E3411", {"start": v(27.55, -37.82) * mm, "end": v(27.73, -37.92) * mm});
            skLineSegment(sketch, "E3412", {"start": v(27.73, -37.92) * mm, "end": v(27.93, -37.97) * mm});
            skLineSegment(sketch, "E3413", {"start": v(27.93, -37.97) * mm, "end": v(28.13, -37.97) * mm});
            skLineSegment(sketch, "E3414", {"start": v(28.13, -37.97) * mm, "end": v(28.33, -37.92) * mm});
            skLineSegment(sketch, "E3415", {"start": v(28.33, -37.92) * mm, "end": v(28.5, -37.81) * mm});
            skLineSegment(sketch, "E3416", {"start": v(28.5, -37.81) * mm, "end": v(28.64, -37.67) * mm});
            skLineSegment(sketch, "E3417", {"start": v(28.64, -37.67) * mm, "end": v(28.74, -37.5) * mm});
            skLineSegment(sketch, "E3418", {"start": v(28.74, -37.5) * mm, "end": v(28.8, -37.3) * mm});
            skLineSegment(sketch, "E3419", {"start": v(28.8, -37.3) * mm, "end": v(28.8, -37.09) * mm});
            skLineSegment(sketch, "E3420", {"start": v(28.8, -37.09) * mm, "end": v(28.74, -36.9) * mm});
            skLineSegment(sketch, "E3421", {"start": v(28.74, -36.9) * mm, "end": v(28.63, -36.72) * mm});
            skLineSegment(sketch, "E3422", {"start": v(28.63, -36.72) * mm, "end": v(28.5, -36.55) * mm});
            skLineSegment(sketch, "E3423", {"start": v(28.5, -36.55) * mm, "end": v(28.36, -36.38) * mm});
            skLineSegment(sketch, "E3424", {"start": v(28.36, -36.38) * mm, "end": v(28.23, -36.21) * mm});
            skLineSegment(sketch, "E3425", {"start": v(28.23, -36.21) * mm, "end": v(28.09, -36.04) * mm});
            skLineSegment(sketch, "E3426", {"start": v(28.09, -36.04) * mm, "end": v(27.95, -35.87) * mm});
            skLineSegment(sketch, "E3427", {"start": v(27.95, -35.87) * mm, "end": v(27.82, -35.7) * mm});
            skLineSegment(sketch, "E3428", {"start": v(27.82, -35.7) * mm, "end": v(27.68, -35.54) * mm});
            skLineSegment(sketch, "E3429", {"start": v(27.68, -35.54) * mm, "end": v(27.55, -35.37) * mm});
            skLineSegment(sketch, "E3430", {"start": v(27.55, -35.37) * mm, "end": v(27.41, -35.2) * mm});
            skLineSegment(sketch, "E3431", {"start": v(27.41, -35.2) * mm, "end": v(27.27, -35.03) * mm});
            skLineSegment(sketch, "E3432", {"start": v(27.27, -35.03) * mm, "end": v(27.14, -34.86) * mm});
            skLineSegment(sketch, "E3433", {"start": v(27.14, -34.86) * mm, "end": v(27, -34.7) * mm});
            skLineSegment(sketch, "E3434", {"start": v(27, -34.7) * mm, "end": v(26.87, -34.52) * mm});
            skLineSegment(sketch, "E3435", {"start": v(26.87, -34.52) * mm, "end": v(26.73, -34.36) * mm});
            skLineSegment(sketch, "E3436", {"start": v(26.73, -34.36) * mm, "end": v(26.6, -34.19) * mm});
            skLineSegment(sketch, "E3437", {"start": v(26.6, -34.19) * mm, "end": v(26.76, -34.04) * mm});
            skLineSegment(sketch, "E3438", {"start": v(26.76, -34.04) * mm, "end": v(26.93, -33.9) * mm});
            skLineSegment(sketch, "E3439", {"start": v(26.93, -33.9) * mm, "end": v(27.1, -33.76) * mm});
            skLineSegment(sketch, "E3440", {"start": v(27.1, -33.76) * mm, "end": v(27.27, -33.61) * mm});
            skLineSegment(sketch, "E3441", {"start": v(27.27, -33.61) * mm, "end": v(27.44, -33.47) * mm});
            skLineSegment(sketch, "E3442", {"start": v(27.44, -33.47) * mm, "end": v(27.61, -33.32) * mm});
            skLineSegment(sketch, "E3443", {"start": v(27.61, -33.32) * mm, "end": v(27.78, -33.18) * mm});
            skLineSegment(sketch, "E3444", {"start": v(27.78, -33.18) * mm, "end": v(27.95, -33.04) * mm});
            skLineSegment(sketch, "E3445", {"start": v(27.95, -33.04) * mm, "end": v(28.12, -32.9) * mm});
            skLineSegment(sketch, "E3446", {"start": v(28.12, -32.9) * mm, "end": v(28.26, -32.78) * mm});
            skLineSegment(sketch, "E3447", {"start": v(28.26, -32.78) * mm, "end": v(28.4, -32.94) * mm});
            skLineSegment(sketch, "E3448", {"start": v(28.4, -32.94) * mm, "end": v(28.55, -33.1) * mm});
            skLineSegment(sketch, "E3449", {"start": v(28.55, -33.1) * mm, "end": v(28.7, -33.26) * mm});
            skLineSegment(sketch, "E3450", {"start": v(28.7, -33.26) * mm, "end": v(28.84, -33.42) * mm});
            skLineSegment(sketch, "E3451", {"start": v(28.84, -33.42) * mm, "end": v(28.98, -33.58) * mm});
            skLineSegment(sketch, "E3452", {"start": v(28.98, -33.58) * mm, "end": v(29.13, -33.75) * mm});
            skLineSegment(sketch, "E3453", {"start": v(29.13, -33.75) * mm, "end": v(29.27, -33.9) * mm});
            skLineSegment(sketch, "E3454", {"start": v(29.27, -33.9) * mm, "end": v(29.41, -34.07) * mm});
            skLineSegment(sketch, "E3455", {"start": v(29.41, -34.07) * mm, "end": v(29.56, -34.23) * mm});
            skLineSegment(sketch, "E3456", {"start": v(29.56, -34.23) * mm, "end": v(29.7, -34.4) * mm});
            skLineSegment(sketch, "E3457", {"start": v(29.7, -34.4) * mm, "end": v(29.85, -34.56) * mm});
            skLineSegment(sketch, "E3458", {"start": v(29.85, -34.56) * mm, "end": v(30, -34.72) * mm});
            skLineSegment(sketch, "E3459", {"start": v(30, -34.72) * mm, "end": v(30.14, -34.88) * mm});
            skLineSegment(sketch, "E3460", {"start": v(30.14, -34.88) * mm, "end": v(30.28, -35.04) * mm});
            skLineSegment(sketch, "E3461", {"start": v(30.28, -35.04) * mm, "end": v(30.42, -35.2) * mm});
            skLineSegment(sketch, "E3462", {"start": v(30.42, -35.2) * mm, "end": v(30.58, -35.33) * mm});
            skLineSegment(sketch, "E3463", {"start": v(30.58, -35.33) * mm, "end": v(30.76, -35.42) * mm});
            skLineSegment(sketch, "E3464", {"start": v(30.76, -35.42) * mm, "end": v(30.96, -35.46) * mm});
            skLineSegment(sketch, "E3465", {"start": v(30.96, -35.46) * mm, "end": v(31.17, -35.44) * mm});
            skLineSegment(sketch, "E3466", {"start": v(31.17, -35.44) * mm, "end": v(31.36, -35.37) * mm});
            skLineSegment(sketch, "E3467", {"start": v(31.36, -35.37) * mm, "end": v(31.52, -35.25) * mm});
            skLineSegment(sketch, "E3468", {"start": v(31.52, -35.25) * mm, "end": v(31.65, -35.1) * mm});
            skLineSegment(sketch, "E3469", {"start": v(31.65, -35.1) * mm, "end": v(31.74, -34.91) * mm});
            skLineSegment(sketch, "E3470", {"start": v(31.74, -34.91) * mm, "end": v(31.77, -34.71) * mm});
            skLineSegment(sketch, "E3471", {"start": v(31.77, -34.71) * mm, "end": v(31.75, -34.5) * mm});
            skLineSegment(sketch, "E3472", {"start": v(31.75, -34.5) * mm, "end": v(31.68, -34.32) * mm});
            skLineSegment(sketch, "E3473", {"start": v(31.68, -34.32) * mm, "end": v(31.56, -34.15) * mm});
            skLineSegment(sketch, "E3474", {"start": v(31.56, -34.15) * mm, "end": v(31.42, -34) * mm});
            skLineSegment(sketch, "E3475", {"start": v(31.42, -34) * mm, "end": v(31.27, -33.84) * mm});
            skLineSegment(sketch, "E3476", {"start": v(31.27, -33.84) * mm, "end": v(31.12, -33.68) * mm});
            skLineSegment(sketch, "E3477", {"start": v(31.12, -33.68) * mm, "end": v(30.97, -33.52) * mm});
            skLineSegment(sketch, "E3478", {"start": v(30.97, -33.52) * mm, "end": v(30.82, -33.37) * mm});
            skLineSegment(sketch, "E3479", {"start": v(30.82, -33.37) * mm, "end": v(30.67, -33.21) * mm});
            skLineSegment(sketch, "E3480", {"start": v(30.67, -33.21) * mm, "end": v(30.52, -33.05) * mm});
            skLineSegment(sketch, "E3481", {"start": v(30.52, -33.05) * mm, "end": v(30.37, -32.9) * mm});
            skLineSegment(sketch, "E3482", {"start": v(30.37, -32.9) * mm, "end": v(30.22, -32.74) * mm});
            skLineSegment(sketch, "E3483", {"start": v(30.22, -32.74) * mm, "end": v(30.07, -32.58) * mm});
            skLineSegment(sketch, "E3484", {"start": v(30.07, -32.58) * mm, "end": v(29.92, -32.43) * mm});
            skLineSegment(sketch, "E3485", {"start": v(29.92, -32.43) * mm, "end": v(29.77, -32.27) * mm});
            skLineSegment(sketch, "E3486", {"start": v(29.77, -32.27) * mm, "end": v(29.62, -32.11) * mm});
            skLineSegment(sketch, "E3487", {"start": v(29.62, -32.11) * mm, "end": v(29.47, -31.95) * mm});
            skLineSegment(sketch, "E3488", {"start": v(29.47, -31.95) * mm, "end": v(29.32, -31.8) * mm});
            skLineSegment(sketch, "E3489", {"start": v(29.32, -31.8) * mm, "end": v(29.48, -31.64) * mm});
            skLineSegment(sketch, "E3490", {"start": v(29.48, -31.64) * mm, "end": v(29.64, -31.48) * mm});
            skLineSegment(sketch, "E3491", {"start": v(29.64, -31.48) * mm, "end": v(29.8, -31.32) * mm});
            skLineSegment(sketch, "E3492", {"start": v(29.8, -31.32) * mm, "end": v(29.95, -31.17) * mm});
            skLineSegment(sketch, "E3493", {"start": v(29.95, -31.17) * mm, "end": v(30.11, -31) * mm});
            skLineSegment(sketch, "E3494", {"start": v(30.11, -31) * mm, "end": v(30.27, -30.85) * mm});
            skLineSegment(sketch, "E3495", {"start": v(30.27, -30.85) * mm, "end": v(30.43, -30.7) * mm});
            skLineSegment(sketch, "E3496", {"start": v(30.43, -30.7) * mm, "end": v(30.58, -30.54) * mm});
            skLineSegment(sketch, "E3497", {"start": v(30.58, -30.54) * mm, "end": v(30.74, -30.38) * mm});
            skLineSegment(sketch, "E3498", {"start": v(30.74, -30.38) * mm, "end": v(30.87, -30.25) * mm});
            skLineSegment(sketch, "E3499", {"start": v(30.87, -30.25) * mm, "end": v(31.03, -30.4) * mm});
            skLineSegment(sketch, "E3500", {"start": v(31.03, -30.4) * mm, "end": v(31.18, -30.55) * mm});
            skLineSegment(sketch, "E3501", {"start": v(31.18, -30.55) * mm, "end": v(31.34, -30.7) * mm});
            skLineSegment(sketch, "E3502", {"start": v(31.34, -30.7) * mm, "end": v(31.5, -30.85) * mm});
            skLineSegment(sketch, "E3503", {"start": v(31.5, -30.85) * mm, "end": v(31.65, -31) * mm});
            skLineSegment(sketch, "E3504", {"start": v(31.65, -31) * mm, "end": v(31.81, -31.15) * mm});
            skLineSegment(sketch, "E3505", {"start": v(31.81, -31.15) * mm, "end": v(31.97, -31.3) * mm});
            skLineSegment(sketch, "E3506", {"start": v(31.97, -31.3) * mm, "end": v(32.12, -31.45) * mm});
            skLineSegment(sketch, "E3507", {"start": v(32.12, -31.45) * mm, "end": v(32.28, -31.6) * mm});
            skLineSegment(sketch, "E3508", {"start": v(32.28, -31.6) * mm, "end": v(32.44, -31.75) * mm});
            skLineSegment(sketch, "E3509", {"start": v(32.44, -31.75) * mm, "end": v(32.6, -31.9) * mm});
            skLineSegment(sketch, "E3510", {"start": v(32.6, -31.9) * mm, "end": v(32.75, -32.05) * mm});
            skLineSegment(sketch, "E3511", {"start": v(32.75, -32.05) * mm, "end": v(32.9, -32.2) * mm});
            skLineSegment(sketch, "E3512", {"start": v(32.9, -32.2) * mm, "end": v(33.07, -32.34) * mm});
            skLineSegment(sketch, "E3513", {"start": v(33.07, -32.34) * mm, "end": v(33.22, -32.5) * mm});
            skLineSegment(sketch, "E3514", {"start": v(33.22, -32.5) * mm, "end": v(33.39, -32.61) * mm});
            skLineSegment(sketch, "E3515", {"start": v(33.39, -32.61) * mm, "end": v(33.58, -32.68) * mm});
            skLineSegment(sketch, "E3516", {"start": v(33.58, -32.68) * mm, "end": v(33.78, -32.7) * mm});
            skLineSegment(sketch, "E3517", {"start": v(33.78, -32.7) * mm, "end": v(33.98, -32.67) * mm});
            skLineSegment(sketch, "E3518", {"start": v(33.98, -32.67) * mm, "end": v(34.17, -32.58) * mm});
            skLineSegment(sketch, "E3519", {"start": v(34.17, -32.58) * mm, "end": v(34.32, -32.45) * mm});
            skLineSegment(sketch, "E3520", {"start": v(34.32, -32.45) * mm, "end": v(34.44, -32.29) * mm});
            skLineSegment(sketch, "E3521", {"start": v(34.44, -32.29) * mm, "end": v(34.51, -32.1) * mm});
            skLineSegment(sketch, "E3522", {"start": v(34.51, -32.1) * mm, "end": v(34.53, -31.9) * mm});
            skLineSegment(sketch, "E3523", {"start": v(34.53, -31.9) * mm, "end": v(34.5, -31.7) * mm});
            skLineSegment(sketch, "E3524", {"start": v(34.5, -31.7) * mm, "end": v(34.4, -31.5) * mm});
            skLineSegment(sketch, "E3525", {"start": v(34.4, -31.5) * mm, "end": v(34.27, -31.35) * mm});
            skLineSegment(sketch, "E3526", {"start": v(34.27, -31.35) * mm, "end": v(34.11, -31.2) * mm});
            skLineSegment(sketch, "E3527", {"start": v(34.11, -31.2) * mm, "end": v(33.95, -31.06) * mm});
            skLineSegment(sketch, "E3528", {"start": v(33.95, -31.06) * mm, "end": v(33.79, -30.92) * mm});
            skLineSegment(sketch, "E3529", {"start": v(33.79, -30.92) * mm, "end": v(33.63, -30.78) * mm});
            skLineSegment(sketch, "E3530", {"start": v(33.63, -30.78) * mm, "end": v(33.46, -30.63) * mm});
            skLineSegment(sketch, "E3531", {"start": v(33.46, -30.63) * mm, "end": v(33.3, -30.49) * mm});
            skLineSegment(sketch, "E3532", {"start": v(33.3, -30.49) * mm, "end": v(33.14, -30.34) * mm});
            skLineSegment(sketch, "E3533", {"start": v(33.14, -30.34) * mm, "end": v(32.98, -30.2) * mm});
            skLineSegment(sketch, "E3534", {"start": v(32.98, -30.2) * mm, "end": v(32.82, -30.06) * mm});
            skLineSegment(sketch, "E3535", {"start": v(32.82, -30.06) * mm, "end": v(32.66, -29.91) * mm});
            skLineSegment(sketch, "E3536", {"start": v(32.66, -29.91) * mm, "end": v(32.5, -29.77) * mm});
            skLineSegment(sketch, "E3537", {"start": v(32.5, -29.77) * mm, "end": v(32.33, -29.62) * mm});
            skLineSegment(sketch, "E3538", {"start": v(32.33, -29.62) * mm, "end": v(32.17, -29.48) * mm});
            skLineSegment(sketch, "E3539", {"start": v(32.17, -29.48) * mm, "end": v(32, -29.33) * mm});
            skLineSegment(sketch, "E3540", {"start": v(32, -29.33) * mm, "end": v(31.85, -29.2) * mm});
            skLineSegment(sketch, "E3541", {"start": v(31.85, -29.2) * mm, "end": v(32, -29.02) * mm});
            skLineSegment(sketch, "E3542", {"start": v(32, -29.02) * mm, "end": v(32.13, -28.85) * mm});
            skLineSegment(sketch, "E3543", {"start": v(32.13, -28.85) * mm, "end": v(32.28, -28.68) * mm});
            skLineSegment(sketch, "E3544", {"start": v(32.28, -28.68) * mm, "end": v(32.42, -28.51) * mm});
            skLineSegment(sketch, "E3545", {"start": v(32.42, -28.51) * mm, "end": v(32.57, -28.34) * mm});
            skLineSegment(sketch, "E3546", {"start": v(32.57, -28.34) * mm, "end": v(32.71, -28.17) * mm});
            skLineSegment(sketch, "E3547", {"start": v(32.71, -28.17) * mm, "end": v(32.85, -28) * mm});
            skLineSegment(sketch, "E3548", {"start": v(32.85, -28) * mm, "end": v(33, -27.83) * mm});
            skLineSegment(sketch, "E3549", {"start": v(33, -27.83) * mm, "end": v(33.14, -27.66) * mm});
            skLineSegment(sketch, "E3550", {"start": v(33.14, -27.66) * mm, "end": v(33.26, -27.52) * mm});
            skLineSegment(sketch, "E3551", {"start": v(33.26, -27.52) * mm, "end": v(33.43, -27.66) * mm});
            skLineSegment(sketch, "E3552", {"start": v(33.43, -27.66) * mm, "end": v(33.6, -27.8) * mm});
            skLineSegment(sketch, "E3553", {"start": v(33.6, -27.8) * mm, "end": v(33.76, -27.93) * mm});
            skLineSegment(sketch, "E3554", {"start": v(33.76, -27.93) * mm, "end": v(33.93, -28.07) * mm});
            skLineSegment(sketch, "E3555", {"start": v(33.93, -28.07) * mm, "end": v(34.1, -28.2) * mm});
            skLineSegment(sketch, "E3556", {"start": v(34.1, -28.2) * mm, "end": v(34.27, -28.34) * mm});
            skLineSegment(sketch, "E3557", {"start": v(34.27, -28.34) * mm, "end": v(34.44, -28.48) * mm});
            skLineSegment(sketch, "E3558", {"start": v(34.44, -28.48) * mm, "end": v(34.6, -28.61) * mm});
            skLineSegment(sketch, "E3559", {"start": v(34.6, -28.61) * mm, "end": v(34.78, -28.75) * mm});
            skLineSegment(sketch, "E3560", {"start": v(34.78, -28.75) * mm, "end": v(34.95, -28.88) * mm});
            skLineSegment(sketch, "E3561", {"start": v(34.95, -28.88) * mm, "end": v(35.11, -29.02) * mm});
            skLineSegment(sketch, "E3562", {"start": v(35.11, -29.02) * mm, "end": v(35.28, -29.15) * mm});
            skLineSegment(sketch, "E3563", {"start": v(35.28, -29.15) * mm, "end": v(35.45, -29.3) * mm});
            skLineSegment(sketch, "E3564", {"start": v(35.45, -29.3) * mm, "end": v(35.62, -29.43) * mm});
            skLineSegment(sketch, "E3565", {"start": v(35.62, -29.43) * mm, "end": v(35.8, -29.56) * mm});
            skLineSegment(sketch, "E3566", {"start": v(35.8, -29.56) * mm, "end": v(35.96, -29.67) * mm});
            skLineSegment(sketch, "E3567", {"start": v(35.96, -29.67) * mm, "end": v(36.16, -29.72) * mm});
            skLineSegment(sketch, "E3568", {"start": v(36.16, -29.72) * mm, "end": v(36.36, -29.72) * mm});
            skLineSegment(sketch, "E3569", {"start": v(36.36, -29.72) * mm, "end": v(36.56, -29.67) * mm});
            skLineSegment(sketch, "E3570", {"start": v(36.56, -29.67) * mm, "end": v(36.74, -29.57) * mm});
            skLineSegment(sketch, "E3571", {"start": v(36.74, -29.57) * mm, "end": v(36.88, -29.43) * mm});
            skLineSegment(sketch, "E3572", {"start": v(36.88, -29.43) * mm, "end": v(36.99, -29.25) * mm});
            skLineSegment(sketch, "E3573", {"start": v(36.99, -29.25) * mm, "end": v(37.04, -29.06) * mm});
            skLineSegment(sketch, "E3574", {"start": v(37.04, -29.06) * mm, "end": v(37.04, -28.86) * mm});
            skLineSegment(sketch, "E3575", {"start": v(37.04, -28.86) * mm, "end": v(36.99, -28.66) * mm});
            skLineSegment(sketch, "E3576", {"start": v(36.99, -28.66) * mm, "end": v(36.89, -28.48) * mm});
            skLineSegment(sketch, "E3577", {"start": v(36.89, -28.48) * mm, "end": v(36.74, -28.34) * mm});
            skLineSegment(sketch, "E3578", {"start": v(36.74, -28.34) * mm, "end": v(36.57, -28.2) * mm});
            skLineSegment(sketch, "E3579", {"start": v(36.57, -28.2) * mm, "end": v(36.4, -28.08) * mm});
            skLineSegment(sketch, "E3580", {"start": v(36.4, -28.08) * mm, "end": v(36.22, -27.95) * mm});
            skLineSegment(sketch, "E3581", {"start": v(36.22, -27.95) * mm, "end": v(36.05, -27.82) * mm});
            skLineSegment(sketch, "E3582", {"start": v(36.05, -27.82) * mm, "end": v(35.88, -27.69) * mm});
            skLineSegment(sketch, "E3583", {"start": v(35.88, -27.69) * mm, "end": v(35.7, -27.56) * mm});
            skLineSegment(sketch, "E3584", {"start": v(35.7, -27.56) * mm, "end": v(35.53, -27.43) * mm});
            skLineSegment(sketch, "E3585", {"start": v(35.53, -27.43) * mm, "end": v(35.36, -27.3) * mm});
            skLineSegment(sketch, "E3586", {"start": v(35.36, -27.3) * mm, "end": v(35.18, -27.17) * mm});
            skLineSegment(sketch, "E3587", {"start": v(35.18, -27.17) * mm, "end": v(35.01, -27.04) * mm});
            skLineSegment(sketch, "E3588", {"start": v(35.01, -27.04) * mm, "end": v(34.84, -26.9) * mm});
            skLineSegment(sketch, "E3589", {"start": v(34.84, -26.9) * mm, "end": v(34.66, -26.77) * mm});
            skLineSegment(sketch, "E3590", {"start": v(34.66, -26.77) * mm, "end": v(34.5, -26.64) * mm});
            skLineSegment(sketch, "E3591", {"start": v(34.5, -26.64) * mm, "end": v(34.32, -26.51) * mm});
            skLineSegment(sketch, "E3592", {"start": v(34.32, -26.51) * mm, "end": v(34.15, -26.38) * mm});
            skLineSegment(sketch, "E3593", {"start": v(34.15, -26.38) * mm, "end": v(34.27, -26.2) * mm});
            skLineSegment(sketch, "E3594", {"start": v(34.27, -26.2) * mm, "end": v(34.4, -26.02) * mm});
            skLineSegment(sketch, "E3595", {"start": v(34.4, -26.02) * mm, "end": v(34.53, -25.84) * mm});
            skLineSegment(sketch, "E3596", {"start": v(34.53, -25.84) * mm, "end": v(34.66, -25.66) * mm});
            skLineSegment(sketch, "E3597", {"start": v(34.66, -25.66) * mm, "end": v(34.8, -25.48) * mm});
            skLineSegment(sketch, "E3598", {"start": v(34.8, -25.48) * mm, "end": v(34.92, -25.3) * mm});
            skLineSegment(sketch, "E3599", {"start": v(34.92, -25.3) * mm, "end": v(35.05, -25.12) * mm});
            skLineSegment(sketch, "E3600", {"start": v(35.05, -25.12) * mm, "end": v(35.18, -24.93) * mm});
            skLineSegment(sketch, "E3601", {"start": v(35.18, -24.93) * mm, "end": v(35.3, -24.75) * mm});
            skLineSegment(sketch, "E3602", {"start": v(35.3, -24.75) * mm, "end": v(35.41, -24.6) * mm});
            skLineSegment(sketch, "E3603", {"start": v(35.41, -24.6) * mm, "end": v(35.6, -24.73) * mm});
            skLineSegment(sketch, "E3604", {"start": v(35.6, -24.73) * mm, "end": v(35.77, -24.85) * mm});
            skLineSegment(sketch, "E3605", {"start": v(35.77, -24.85) * mm, "end": v(35.95, -24.97) * mm});
            skLineSegment(sketch, "E3606", {"start": v(35.95, -24.97) * mm, "end": v(36.13, -25.1) * mm});
            skLineSegment(sketch, "E3607", {"start": v(36.13, -25.1) * mm, "end": v(36.31, -25.21) * mm});
            skLineSegment(sketch, "E3608", {"start": v(36.31, -25.21) * mm, "end": v(36.5, -25.34) * mm});
            skLineSegment(sketch, "E3609", {"start": v(36.5, -25.34) * mm, "end": v(36.67, -25.46) * mm});
            skLineSegment(sketch, "E3610", {"start": v(36.67, -25.46) * mm, "end": v(36.85, -25.58) * mm});
            skLineSegment(sketch, "E3611", {"start": v(36.85, -25.58) * mm, "end": v(37.03, -25.7) * mm});
            skLineSegment(sketch, "E3612", {"start": v(37.03, -25.7) * mm, "end": v(37.2, -25.82) * mm});
            skLineSegment(sketch, "E3613", {"start": v(37.2, -25.82) * mm, "end": v(37.39, -25.94) * mm});
            skLineSegment(sketch, "E3614", {"start": v(37.39, -25.94) * mm, "end": v(37.57, -26.06) * mm});
            skLineSegment(sketch, "E3615", {"start": v(37.57, -26.06) * mm, "end": v(37.75, -26.19) * mm});
            skLineSegment(sketch, "E3616", {"start": v(37.75, -26.19) * mm, "end": v(37.93, -26.3) * mm});
            skLineSegment(sketch, "E3617", {"start": v(37.93, -26.3) * mm, "end": v(38.1, -26.43) * mm});
            skLineSegment(sketch, "E3618", {"start": v(38.1, -26.43) * mm, "end": v(38.29, -26.52) * mm});
            skLineSegment(sketch, "E3619", {"start": v(38.29, -26.52) * mm, "end": v(38.49, -26.56) * mm});
            skLineSegment(sketch, "E3620", {"start": v(38.49, -26.56) * mm, "end": v(38.7, -26.54) * mm});
            skLineSegment(sketch, "E3621", {"start": v(38.7, -26.54) * mm, "end": v(38.88, -26.48) * mm});
            skLineSegment(sketch, "E3622", {"start": v(38.88, -26.48) * mm, "end": v(39.05, -26.36) * mm});
            skLineSegment(sketch, "E3623", {"start": v(39.05, -26.36) * mm, "end": v(39.18, -26.2) * mm});
            skLineSegment(sketch, "E3624", {"start": v(39.18, -26.2) * mm, "end": v(39.27, -26.02) * mm});
            skLineSegment(sketch, "E3625", {"start": v(39.27, -26.02) * mm, "end": v(39.3, -25.82) * mm});
            skLineSegment(sketch, "E3626", {"start": v(39.3, -25.82) * mm, "end": v(39.3, -25.62) * mm});
            skLineSegment(sketch, "E3627", {"start": v(39.3, -25.62) * mm, "end": v(39.23, -25.43) * mm});
            skLineSegment(sketch, "E3628", {"start": v(39.23, -25.43) * mm, "end": v(39.1, -25.26) * mm});
            skLineSegment(sketch, "E3629", {"start": v(39.1, -25.26) * mm, "end": v(38.95, -25.13) * mm});
            skLineSegment(sketch, "E3630", {"start": v(38.95, -25.13) * mm, "end": v(38.77, -25.01) * mm});
            skLineSegment(sketch, "E3631", {"start": v(38.77, -25.01) * mm, "end": v(38.59, -24.9) * mm});
            skLineSegment(sketch, "E3632", {"start": v(38.59, -24.9) * mm, "end": v(38.4, -24.78) * mm});
            skLineSegment(sketch, "E3633", {"start": v(38.4, -24.78) * mm, "end": v(38.22, -24.67) * mm});
            skLineSegment(sketch, "E3634", {"start": v(38.22, -24.67) * mm, "end": v(38.04, -24.55) * mm});
            skLineSegment(sketch, "E3635", {"start": v(38.04, -24.55) * mm, "end": v(37.85, -24.44) * mm});
            skLineSegment(sketch, "E3636", {"start": v(37.85, -24.44) * mm, "end": v(37.67, -24.32) * mm});
            skLineSegment(sketch, "E3637", {"start": v(37.67, -24.32) * mm, "end": v(37.49, -24.2) * mm});
            skLineSegment(sketch, "E3638", {"start": v(37.49, -24.2) * mm, "end": v(37.3, -24.1) * mm});
            skLineSegment(sketch, "E3639", {"start": v(37.3, -24.1) * mm, "end": v(37.12, -23.98) * mm});
            skLineSegment(sketch, "E3640", {"start": v(37.12, -23.98) * mm, "end": v(36.94, -23.86) * mm});
            skLineSegment(sketch, "E3641", {"start": v(36.94, -23.86) * mm, "end": v(36.75, -23.74) * mm});
            skLineSegment(sketch, "E3642", {"start": v(36.75, -23.74) * mm, "end": v(36.57, -23.63) * mm});
            skLineSegment(sketch, "E3643", {"start": v(36.57, -23.63) * mm, "end": v(36.39, -23.51) * mm});
            skLineSegment(sketch, "E3644", {"start": v(36.39, -23.51) * mm, "end": v(36.2, -23.4) * mm});
            skLineSegment(sketch, "E3645", {"start": v(36.2, -23.4) * mm, "end": v(36.32, -23.2) * mm});
            skLineSegment(sketch, "E3646", {"start": v(36.32, -23.2) * mm, "end": v(36.43, -23.01) * mm});
            skLineSegment(sketch, "E3647", {"start": v(36.43, -23.01) * mm, "end": v(36.55, -22.82) * mm});
            skLineSegment(sketch, "E3648", {"start": v(36.55, -22.82) * mm, "end": v(36.66, -22.63) * mm});
            skLineSegment(sketch, "E3649", {"start": v(36.66, -22.63) * mm, "end": v(36.77, -22.44) * mm});
            skLineSegment(sketch, "E3650", {"start": v(36.77, -22.44) * mm, "end": v(36.89, -22.25) * mm});
            skLineSegment(sketch, "E3651", {"start": v(36.89, -22.25) * mm, "end": v(37, -22.06) * mm});
            skLineSegment(sketch, "E3652", {"start": v(37, -22.06) * mm, "end": v(37.12, -21.87) * mm});
            skLineSegment(sketch, "E3653", {"start": v(37.12, -21.87) * mm, "end": v(37.23, -21.68) * mm});
            skLineSegment(sketch, "E3654", {"start": v(37.23, -21.68) * mm, "end": v(37.32, -21.52) * mm});
            skLineSegment(sketch, "E3655", {"start": v(37.32, -21.52) * mm, "end": v(37.51, -21.63) * mm});
            skLineSegment(sketch, "E3656", {"start": v(37.51, -21.63) * mm, "end": v(37.7, -21.73) * mm});
            skLineSegment(sketch, "E3657", {"start": v(37.7, -21.73) * mm, "end": v(37.89, -21.84) * mm});
            skLineSegment(sketch, "E3658", {"start": v(37.89, -21.84) * mm, "end": v(38.08, -21.95) * mm});
            skLineSegment(sketch, "E3659", {"start": v(38.08, -21.95) * mm, "end": v(38.27, -22.05) * mm});
            skLineSegment(sketch, "E3660", {"start": v(38.27, -22.05) * mm, "end": v(38.46, -22.16) * mm});
            skLineSegment(sketch, "E3661", {"start": v(38.46, -22.16) * mm, "end": v(38.64, -22.27) * mm});
            skLineSegment(sketch, "E3662", {"start": v(38.64, -22.27) * mm, "end": v(38.83, -22.37) * mm});
            skLineSegment(sketch, "E3663", {"start": v(38.83, -22.37) * mm, "end": v(39.02, -22.48) * mm});
            skLineSegment(sketch, "E3664", {"start": v(39.02, -22.48) * mm, "end": v(39.21, -22.58) * mm});
            skLineSegment(sketch, "E3665", {"start": v(39.21, -22.58) * mm, "end": v(39.4, -22.7) * mm});
            skLineSegment(sketch, "E3666", {"start": v(39.4, -22.7) * mm, "end": v(39.59, -22.8) * mm});
            skLineSegment(sketch, "E3667", {"start": v(39.59, -22.8) * mm, "end": v(39.78, -22.9) * mm});
            skLineSegment(sketch, "E3668", {"start": v(39.78, -22.9) * mm, "end": v(39.97, -23) * mm});
            skLineSegment(sketch, "E3669", {"start": v(39.97, -23) * mm, "end": v(40.16, -23.12) * mm});
            skLineSegment(sketch, "E3670", {"start": v(40.16, -23.12) * mm, "end": v(40.34, -23.19) * mm});
            skLineSegment(sketch, "E3671", {"start": v(40.34, -23.19) * mm, "end": v(40.55, -23.21) * mm});
            skLineSegment(sketch, "E3672", {"start": v(40.55, -23.21) * mm, "end": v(40.75, -23.18) * mm});
            skLineSegment(sketch, "E3673", {"start": v(40.75, -23.18) * mm, "end": v(40.93, -23.1) * mm});
            skLineSegment(sketch, "E3674", {"start": v(40.93, -23.1) * mm, "end": v(41.1, -22.97) * mm});
            skLineSegment(sketch, "E3675", {"start": v(41.1, -22.97) * mm, "end": v(41.21, -22.8) * mm});
            skLineSegment(sketch, "E3676", {"start": v(41.21, -22.8) * mm, "end": v(41.28, -22.62) * mm});
            skLineSegment(sketch, "E3677", {"start": v(41.28, -22.62) * mm, "end": v(41.3, -22.41) * mm});
            skLineSegment(sketch, "E3678", {"start": v(41.3, -22.41) * mm, "end": v(41.27, -22.21) * mm});
            skLineSegment(sketch, "E3679", {"start": v(41.27, -22.21) * mm, "end": v(41.19, -22.03) * mm});
            skLineSegment(sketch, "E3680", {"start": v(41.19, -22.03) * mm, "end": v(41.06, -21.87) * mm});
            skLineSegment(sketch, "E3681", {"start": v(41.06, -21.87) * mm, "end": v(40.9, -21.75) * mm});
            skLineSegment(sketch, "E3682", {"start": v(40.9, -21.75) * mm, "end": v(40.7, -21.65) * mm});
            skLineSegment(sketch, "E3683", {"start": v(40.7, -21.65) * mm, "end": v(40.5, -21.55) * mm});
            skLineSegment(sketch, "E3684", {"start": v(40.5, -21.55) * mm, "end": v(40.32, -21.45) * mm});
            skLineSegment(sketch, "E3685", {"start": v(40.32, -21.45) * mm, "end": v(40.12, -21.35) * mm});
            skLineSegment(sketch, "E3686", {"start": v(40.12, -21.35) * mm, "end": v(39.93, -21.25) * mm});
            skLineSegment(sketch, "E3687", {"start": v(39.93, -21.25) * mm, "end": v(39.74, -21.15) * mm});
            skLineSegment(sketch, "E3688", {"start": v(39.74, -21.15) * mm, "end": v(39.55, -21.05) * mm});
            skLineSegment(sketch, "E3689", {"start": v(39.55, -21.05) * mm, "end": v(39.36, -20.95) * mm});
            skLineSegment(sketch, "E3690", {"start": v(39.36, -20.95) * mm, "end": v(39.16, -20.85) * mm});
            skLineSegment(sketch, "E3691", {"start": v(39.16, -20.85) * mm, "end": v(38.97, -20.75) * mm});
            skLineSegment(sketch, "E3692", {"start": v(38.97, -20.75) * mm, "end": v(38.78, -20.65) * mm});
            skLineSegment(sketch, "E3693", {"start": v(38.78, -20.65) * mm, "end": v(38.59, -20.55) * mm});
            skLineSegment(sketch, "E3694", {"start": v(38.59, -20.55) * mm, "end": v(38.4, -20.45) * mm});
            skLineSegment(sketch, "E3695", {"start": v(38.4, -20.45) * mm, "end": v(38.2, -20.35) * mm});
            skLineSegment(sketch, "E3696", {"start": v(38.2, -20.35) * mm, "end": v(38, -20.25) * mm});
            skLineSegment(sketch, "E3697", {"start": v(38, -20.25) * mm, "end": v(38.1, -20.05) * mm});
            skLineSegment(sketch, "E3698", {"start": v(38.1, -20.05) * mm, "end": v(38.2, -19.85) * mm});
            skLineSegment(sketch, "E3699", {"start": v(38.2, -19.85) * mm, "end": v(38.3, -19.65) * mm});
            skLineSegment(sketch, "E3700", {"start": v(38.3, -19.65) * mm, "end": v(38.4, -19.45) * mm});
            skLineSegment(sketch, "E3701", {"start": v(38.4, -19.45) * mm, "end": v(38.5, -19.25) * mm});
            skLineSegment(sketch, "E3702", {"start": v(38.5, -19.25) * mm, "end": v(38.6, -19.05) * mm});
            skLineSegment(sketch, "E3703", {"start": v(38.6, -19.05) * mm, "end": v(38.7, -18.85) * mm});
            skLineSegment(sketch, "E3704", {"start": v(38.7, -18.85) * mm, "end": v(38.8, -18.65) * mm});
            skLineSegment(sketch, "E3705", {"start": v(38.8, -18.65) * mm, "end": v(38.89, -18.45) * mm});
            skLineSegment(sketch, "E3706", {"start": v(38.89, -18.45) * mm, "end": v(38.97, -18.29) * mm});
            skLineSegment(sketch, "E3707", {"start": v(38.97, -18.29) * mm, "end": v(39.17, -18.38) * mm});
            skLineSegment(sketch, "E3708", {"start": v(39.17, -18.38) * mm, "end": v(39.36, -18.47) * mm});
            skLineSegment(sketch, "E3709", {"start": v(39.36, -18.47) * mm, "end": v(39.56, -18.56) * mm});
            skLineSegment(sketch, "E3710", {"start": v(39.56, -18.56) * mm, "end": v(39.76, -18.65) * mm});
            skLineSegment(sketch, "E3711", {"start": v(39.76, -18.65) * mm, "end": v(39.95, -18.74) * mm});
            skLineSegment(sketch, "E3712", {"start": v(39.95, -18.74) * mm, "end": v(40.15, -18.83) * mm});
            skLineSegment(sketch, "E3713", {"start": v(40.15, -18.83) * mm, "end": v(40.35, -18.92) * mm});
            skLineSegment(sketch, "E3714", {"start": v(40.35, -18.92) * mm, "end": v(40.54, -19.01) * mm});
            skLineSegment(sketch, "E3715", {"start": v(40.54, -19.01) * mm, "end": v(40.74, -19.1) * mm});
            skLineSegment(sketch, "E3716", {"start": v(40.74, -19.1) * mm, "end": v(40.94, -19.2) * mm});
            skLineSegment(sketch, "E3717", {"start": v(40.94, -19.2) * mm, "end": v(41.14, -19.28) * mm});
            skLineSegment(sketch, "E3718", {"start": v(41.14, -19.28) * mm, "end": v(41.33, -19.37) * mm});
            skLineSegment(sketch, "E3719", {"start": v(41.33, -19.37) * mm, "end": v(41.53, -19.46) * mm});
            skLineSegment(sketch, "E3720", {"start": v(41.53, -19.46) * mm, "end": v(41.73, -19.55) * mm});
            skLineSegment(sketch, "E3721", {"start": v(41.73, -19.55) * mm, "end": v(41.92, -19.64) * mm});
            skLineSegment(sketch, "E3722", {"start": v(41.92, -19.64) * mm, "end": v(42.12, -19.7) * mm});
            skLineSegment(sketch, "E3723", {"start": v(42.12, -19.7) * mm, "end": v(42.32, -19.7) * mm});
            skLineSegment(sketch, "E3724", {"start": v(42.32, -19.7) * mm, "end": v(42.52, -19.66) * mm});
            skLineSegment(sketch, "E3725", {"start": v(42.52, -19.66) * mm, "end": v(42.7, -19.56) * mm});
            skLineSegment(sketch, "E3726", {"start": v(42.7, -19.56) * mm, "end": v(42.85, -19.42) * mm});
            skLineSegment(sketch, "E3727", {"start": v(42.85, -19.42) * mm, "end": v(42.95, -19.25) * mm});
            skLineSegment(sketch, "E3728", {"start": v(42.95, -19.25) * mm, "end": v(43, -19.05) * mm});
            skLineSegment(sketch, "E3729", {"start": v(43, -19.05) * mm, "end": v(43.01, -18.85) * mm});
            skLineSegment(sketch, "E3730", {"start": v(43.01, -18.85) * mm, "end": v(42.96, -18.65) * mm});
            skLineSegment(sketch, "E3731", {"start": v(42.96, -18.65) * mm, "end": v(42.86, -18.47) * mm});
            skLineSegment(sketch, "E3732", {"start": v(42.86, -18.47) * mm, "end": v(42.72, -18.33) * mm});
            skLineSegment(sketch, "E3733", {"start": v(42.72, -18.33) * mm, "end": v(42.55, -18.22) * mm});
            skLineSegment(sketch, "E3734", {"start": v(42.55, -18.22) * mm, "end": v(42.35, -18.14) * mm});
            skLineSegment(sketch, "E3735", {"start": v(42.35, -18.14) * mm, "end": v(42.15, -18.06) * mm});
            skLineSegment(sketch, "E3736", {"start": v(42.15, -18.06) * mm, "end": v(41.95, -17.97) * mm});
            skLineSegment(sketch, "E3737", {"start": v(41.95, -17.97) * mm, "end": v(41.75, -17.89) * mm});
            skLineSegment(sketch, "E3738", {"start": v(41.75, -17.89) * mm, "end": v(41.55, -17.8) * mm});
            skLineSegment(sketch, "E3739", {"start": v(41.55, -17.8) * mm, "end": v(41.35, -17.72) * mm});
            skLineSegment(sketch, "E3740", {"start": v(41.35, -17.72) * mm, "end": v(41.15, -17.64) * mm});
            skLineSegment(sketch, "E3741", {"start": v(41.15, -17.64) * mm, "end": v(40.95, -17.55) * mm});
            skLineSegment(sketch, "E3742", {"start": v(40.95, -17.55) * mm, "end": v(40.75, -17.47) * mm});
            skLineSegment(sketch, "E3743", {"start": v(40.75, -17.47) * mm, "end": v(40.55, -17.39) * mm});
            skLineSegment(sketch, "E3744", {"start": v(40.55, -17.39) * mm, "end": v(40.35, -17.3) * mm});
            skLineSegment(sketch, "E3745", {"start": v(40.35, -17.3) * mm, "end": v(40.15, -17.22) * mm});
            skLineSegment(sketch, "E3746", {"start": v(40.15, -17.22) * mm, "end": v(39.95, -17.13) * mm});
            skLineSegment(sketch, "E3747", {"start": v(39.95, -17.13) * mm, "end": v(39.75, -17.05) * mm});
            skLineSegment(sketch, "E3748", {"start": v(39.75, -17.05) * mm, "end": v(39.55, -16.97) * mm});
            skLineSegment(sketch, "E3749", {"start": v(39.55, -16.97) * mm, "end": v(39.63, -16.76) * mm});
            skLineSegment(sketch, "E3750", {"start": v(39.63, -16.76) * mm, "end": v(39.71, -16.55) * mm});
            skLineSegment(sketch, "E3751", {"start": v(39.71, -16.55) * mm, "end": v(39.8, -16.34) * mm});
            skLineSegment(sketch, "E3752", {"start": v(39.8, -16.34) * mm, "end": v(39.87, -16.14) * mm});
            skLineSegment(sketch, "E3753", {"start": v(39.87, -16.14) * mm, "end": v(39.95, -15.93) * mm});
            skLineSegment(sketch, "E3754", {"start": v(39.95, -15.93) * mm, "end": v(40.03, -15.72) * mm});
            skLineSegment(sketch, "E3755", {"start": v(40.03, -15.72) * mm, "end": v(40.12, -15.51) * mm});
            skLineSegment(sketch, "E3756", {"start": v(40.12, -15.51) * mm, "end": v(40.2, -15.3) * mm});
            skLineSegment(sketch, "E3757", {"start": v(40.2, -15.3) * mm, "end": v(40.28, -15.1) * mm});
            skLineSegment(sketch, "E3758", {"start": v(40.28, -15.1) * mm, "end": v(40.34, -14.93) * mm});
            skLineSegment(sketch, "E3759", {"start": v(40.34, -14.93) * mm, "end": v(40.55, -15) * mm});
            skLineSegment(sketch, "E3760", {"start": v(40.55, -15) * mm, "end": v(40.75, -15.08) * mm});
            skLineSegment(sketch, "E3761", {"start": v(40.75, -15.08) * mm, "end": v(40.95, -15.15) * mm});
            skLineSegment(sketch, "E3762", {"start": v(40.95, -15.15) * mm, "end": v(41.16, -15.23) * mm});
            skLineSegment(sketch, "E3763", {"start": v(41.16, -15.23) * mm, "end": v(41.36, -15.3) * mm});
            skLineSegment(sketch, "E3764", {"start": v(41.36, -15.3) * mm, "end": v(41.57, -15.37) * mm});
            skLineSegment(sketch, "E3765", {"start": v(41.57, -15.37) * mm, "end": v(41.77, -15.45) * mm});
            skLineSegment(sketch, "E3766", {"start": v(41.77, -15.45) * mm, "end": v(41.97, -15.52) * mm});
            skLineSegment(sketch, "E3767", {"start": v(41.97, -15.52) * mm, "end": v(42.18, -15.6) * mm});
            skLineSegment(sketch, "E3768", {"start": v(42.18, -15.6) * mm, "end": v(42.38, -15.67) * mm});
            skLineSegment(sketch, "E3769", {"start": v(42.38, -15.67) * mm, "end": v(42.58, -15.74) * mm});
            skLineSegment(sketch, "E3770", {"start": v(42.58, -15.74) * mm, "end": v(42.79, -15.82) * mm});
            skLineSegment(sketch, "E3771", {"start": v(42.79, -15.82) * mm, "end": v(43, -15.9) * mm});
            skLineSegment(sketch, "E3772", {"start": v(43, -15.9) * mm, "end": v(43.2, -15.96) * mm});
            skLineSegment(sketch, "E3773", {"start": v(43.2, -15.96) * mm, "end": v(43.4, -16.04) * mm});
            skLineSegment(sketch, "E3774", {"start": v(43.4, -16.04) * mm, "end": v(43.6, -16.08) * mm});
            skLineSegment(sketch, "E3775", {"start": v(43.6, -16.08) * mm, "end": v(43.8, -16.07) * mm});
            skLineSegment(sketch, "E3776", {"start": v(43.8, -16.07) * mm, "end": v(44, -16) * mm});
            skLineSegment(sketch, "E3777", {"start": v(44, -16) * mm, "end": v(44.16, -15.9) * mm});
            skLineSegment(sketch, "E3778", {"start": v(44.16, -15.9) * mm, "end": v(44.3, -15.74) * mm});
            skLineSegment(sketch, "E3779", {"start": v(44.3, -15.74) * mm, "end": v(44.4, -15.56) * mm});
            skLineSegment(sketch, "E3780", {"start": v(44.4, -15.56) * mm, "end": v(44.43, -15.36) * mm});
            skLineSegment(sketch, "E3781", {"start": v(44.43, -15.36) * mm, "end": v(44.42, -15.16) * mm});
            skLineSegment(sketch, "E3782", {"start": v(44.42, -15.16) * mm, "end": v(44.35, -14.96) * mm});
            skLineSegment(sketch, "E3783", {"start": v(44.35, -14.96) * mm, "end": v(44.24, -14.8) * mm});
            skLineSegment(sketch, "E3784", {"start": v(44.24, -14.8) * mm, "end": v(44.09, -14.66) * mm});
            skLineSegment(sketch, "E3785", {"start": v(44.09, -14.66) * mm, "end": v(43.9, -14.57) * mm});
            skLineSegment(sketch, "E3786", {"start": v(43.9, -14.57) * mm, "end": v(43.7, -14.5) * mm});
            skLineSegment(sketch, "E3787", {"start": v(43.7, -14.5) * mm, "end": v(43.5, -14.44) * mm});
            skLineSegment(sketch, "E3788", {"start": v(43.5, -14.44) * mm, "end": v(43.28, -14.37) * mm});
            skLineSegment(sketch, "E3789", {"start": v(43.28, -14.37) * mm, "end": v(43.08, -14.3) * mm});
            skLineSegment(sketch, "E3790", {"start": v(43.08, -14.3) * mm, "end": v(42.87, -14.24) * mm});
            skLineSegment(sketch, "E3791", {"start": v(42.87, -14.24) * mm, "end": v(42.67, -14.17) * mm});
            skLineSegment(sketch, "E3792", {"start": v(42.67, -14.17) * mm, "end": v(42.46, -14.1) * mm});
            skLineSegment(sketch, "E3793", {"start": v(42.46, -14.1) * mm, "end": v(42.25, -14.03) * mm});
            skLineSegment(sketch, "E3794", {"start": v(42.25, -14.03) * mm, "end": v(42.05, -13.97) * mm});
            skLineSegment(sketch, "E3795", {"start": v(42.05, -13.97) * mm, "end": v(41.84, -13.9) * mm});
            skLineSegment(sketch, "E3796", {"start": v(41.84, -13.9) * mm, "end": v(41.64, -13.83) * mm});
            skLineSegment(sketch, "E3797", {"start": v(41.64, -13.83) * mm, "end": v(41.43, -13.77) * mm});
            skLineSegment(sketch, "E3798", {"start": v(41.43, -13.77) * mm, "end": v(41.22, -13.7) * mm});
            skLineSegment(sketch, "E3799", {"start": v(41.22, -13.7) * mm, "end": v(41.02, -13.63) * mm});
            skLineSegment(sketch, "E3800", {"start": v(41.02, -13.63) * mm, "end": v(40.81, -13.57) * mm});
            skLineSegment(sketch, "E3801", {"start": v(40.81, -13.57) * mm, "end": v(40.88, -13.35) * mm});
            skLineSegment(sketch, "E3802", {"start": v(40.88, -13.35) * mm, "end": v(40.94, -13.14) * mm});
            skLineSegment(sketch, "E3803", {"start": v(40.94, -13.14) * mm, "end": v(41, -12.93) * mm});
            skLineSegment(sketch, "E3804", {"start": v(41, -12.93) * mm, "end": v(41.07, -12.71) * mm});
            skLineSegment(sketch, "E3805", {"start": v(41.07, -12.71) * mm, "end": v(41.13, -12.5) * mm});
            skLineSegment(sketch, "E3806", {"start": v(41.13, -12.5) * mm, "end": v(41.2, -12.29) * mm});
            skLineSegment(sketch, "E3807", {"start": v(41.2, -12.29) * mm, "end": v(41.26, -12.07) * mm});
            skLineSegment(sketch, "E3808", {"start": v(41.26, -12.07) * mm, "end": v(41.32, -11.86) * mm});
            skLineSegment(sketch, "E3809", {"start": v(41.32, -11.86) * mm, "end": v(41.38, -11.65) * mm});
            skLineSegment(sketch, "E3810", {"start": v(41.38, -11.65) * mm, "end": v(41.43, -11.47) * mm});
            skLineSegment(sketch, "E3811", {"start": v(41.43, -11.47) * mm, "end": v(41.64, -11.53) * mm});
            skLineSegment(sketch, "E3812", {"start": v(41.64, -11.53) * mm, "end": v(41.85, -11.59) * mm});
            skLineSegment(sketch, "E3813", {"start": v(41.85, -11.59) * mm, "end": v(42.06, -11.64) * mm});
            skLineSegment(sketch, "E3814", {"start": v(42.06, -11.64) * mm, "end": v(42.27, -11.7) * mm});
            skLineSegment(sketch, "E3815", {"start": v(42.27, -11.7) * mm, "end": v(42.48, -11.76) * mm});
            skLineSegment(sketch, "E3816", {"start": v(42.48, -11.76) * mm, "end": v(42.69, -11.81) * mm});
            skLineSegment(sketch, "E3817", {"start": v(42.69, -11.81) * mm, "end": v(42.9, -11.87) * mm});
            skLineSegment(sketch, "E3818", {"start": v(42.9, -11.87) * mm, "end": v(43.1, -11.93) * mm});
            skLineSegment(sketch, "E3819", {"start": v(43.1, -11.93) * mm, "end": v(43.32, -11.98) * mm});
            skLineSegment(sketch, "E3820", {"start": v(43.32, -11.98) * mm, "end": v(43.53, -12.04) * mm});
            skLineSegment(sketch, "E3821", {"start": v(43.53, -12.04) * mm, "end": v(43.74, -12.1) * mm});
            skLineSegment(sketch, "E3822", {"start": v(43.74, -12.1) * mm, "end": v(43.94, -12.15) * mm});
            skLineSegment(sketch, "E3823", {"start": v(43.94, -12.15) * mm, "end": v(44.15, -12.2) * mm});
            skLineSegment(sketch, "E3824", {"start": v(44.15, -12.2) * mm, "end": v(44.36, -12.27) * mm});
            skLineSegment(sketch, "E3825", {"start": v(44.36, -12.27) * mm, "end": v(44.57, -12.32) * mm});
            skLineSegment(sketch, "E3826", {"start": v(44.57, -12.32) * mm, "end": v(44.77, -12.35) * mm});
            skLineSegment(sketch, "E3827", {"start": v(44.77, -12.35) * mm, "end": v(44.98, -12.32) * mm});
            skLineSegment(sketch, "E3828", {"start": v(44.98, -12.32) * mm, "end": v(45.16, -12.24) * mm});
            skLineSegment(sketch, "E3829", {"start": v(45.16, -12.24) * mm, "end": v(45.32, -12.11) * mm});
            skLineSegment(sketch, "E3830", {"start": v(45.32, -12.11) * mm, "end": v(45.45, -11.95) * mm});
            skLineSegment(sketch, "E3831", {"start": v(45.45, -11.95) * mm, "end": v(45.52, -11.76) * mm});
            skLineSegment(sketch, "E3832", {"start": v(45.52, -11.76) * mm, "end": v(45.54, -11.56) * mm});
            skLineSegment(sketch, "E3833", {"start": v(45.54, -11.56) * mm, "end": v(45.51, -11.36) * mm});
            skLineSegment(sketch, "E3834", {"start": v(45.51, -11.36) * mm, "end": v(45.43, -11.17) * mm});
            skLineSegment(sketch, "E3835", {"start": v(45.43, -11.17) * mm, "end": v(45.3, -11.01) * mm});
            skLineSegment(sketch, "E3836", {"start": v(45.3, -11.01) * mm, "end": v(45.14, -10.9) * mm});
            skLineSegment(sketch, "E3837", {"start": v(45.14, -10.9) * mm, "end": v(44.95, -10.82) * mm});
            skLineSegment(sketch, "E3838", {"start": v(44.95, -10.82) * mm, "end": v(44.74, -10.77) * mm});
            skLineSegment(sketch, "E3839", {"start": v(44.74, -10.77) * mm, "end": v(44.53, -10.72) * mm});
            skLineSegment(sketch, "E3840", {"start": v(44.53, -10.72) * mm, "end": v(44.32, -10.67) * mm});
            skLineSegment(sketch, "E3841", {"start": v(44.32, -10.67) * mm, "end": v(44.1, -10.62) * mm});
            skLineSegment(sketch, "E3842", {"start": v(44.1, -10.62) * mm, "end": v(43.9, -10.57) * mm});
            skLineSegment(sketch, "E3843", {"start": v(43.9, -10.57) * mm, "end": v(43.69, -10.52) * mm});
            skLineSegment(sketch, "E3844", {"start": v(43.69, -10.52) * mm, "end": v(43.48, -10.47) * mm});
            skLineSegment(sketch, "E3845", {"start": v(43.48, -10.47) * mm, "end": v(43.27, -10.42) * mm});
            skLineSegment(sketch, "E3846", {"start": v(43.27, -10.42) * mm, "end": v(43.05, -10.37) * mm});
            skLineSegment(sketch, "E3847", {"start": v(43.05, -10.37) * mm, "end": v(42.84, -10.32) * mm});
            skLineSegment(sketch, "E3848", {"start": v(42.84, -10.32) * mm, "end": v(42.63, -10.27) * mm});
            skLineSegment(sketch, "E3849", {"start": v(42.63, -10.27) * mm, "end": v(42.42, -10.22) * mm});
            skLineSegment(sketch, "E3850", {"start": v(42.42, -10.22) * mm, "end": v(42.21, -10.17) * mm});
            skLineSegment(sketch, "E3851", {"start": v(42.21, -10.17) * mm, "end": v(42, -10.12) * mm});
            skLineSegment(sketch, "E3852", {"start": v(42, -10.12) * mm, "end": v(41.79, -10.07) * mm});
            skLineSegment(sketch, "E3853", {"start": v(41.79, -10.07) * mm, "end": v(41.84, -9.85) * mm});
            skLineSegment(sketch, "E3854", {"start": v(41.84, -9.85) * mm, "end": v(41.88, -9.64) * mm});
            skLineSegment(sketch, "E3855", {"start": v(41.88, -9.64) * mm, "end": v(41.93, -9.42) * mm});
            skLineSegment(sketch, "E3856", {"start": v(41.93, -9.42) * mm, "end": v(41.97, -9.2) * mm});
            skLineSegment(sketch, "E3857", {"start": v(41.97, -9.2) * mm, "end": v(42.02, -8.98) * mm});
            skLineSegment(sketch, "E3858", {"start": v(42.02, -8.98) * mm, "end": v(42.06, -8.77) * mm});
            skLineSegment(sketch, "E3859", {"start": v(42.06, -8.77) * mm, "end": v(42.1, -8.55) * mm});
            skLineSegment(sketch, "E3860", {"start": v(42.1, -8.55) * mm, "end": v(42.15, -8.33) * mm});
            skLineSegment(sketch, "E3861", {"start": v(42.15, -8.33) * mm, "end": v(42.2, -8.11) * mm});
            skLineSegment(sketch, "E3862", {"start": v(42.2, -8.11) * mm, "end": v(42.24, -7.94) * mm});
            skLineSegment(sketch, "E3863", {"start": v(42.24, -7.94) * mm, "end": v(42.45, -7.97) * mm});
            skLineSegment(sketch, "E3864", {"start": v(42.45, -7.97) * mm, "end": v(42.66, -8.01) * mm});
            skLineSegment(sketch, "E3865", {"start": v(42.66, -8.01) * mm, "end": v(42.88, -8.05) * mm});
            skLineSegment(sketch, "E3866", {"start": v(42.88, -8.05) * mm, "end": v(43.1, -8.1) * mm});
            skLineSegment(sketch, "E3867", {"start": v(43.1, -8.1) * mm, "end": v(43.3, -8.13) * mm});
            skLineSegment(sketch, "E3868", {"start": v(43.3, -8.13) * mm, "end": v(43.52, -8.17) * mm});
            skLineSegment(sketch, "E3869", {"start": v(43.52, -8.17) * mm, "end": v(43.73, -8.2) * mm});
            skLineSegment(sketch, "E3870", {"start": v(43.73, -8.2) * mm, "end": v(43.94, -8.25) * mm});
            skLineSegment(sketch, "E3871", {"start": v(43.94, -8.25) * mm, "end": v(44.16, -8.29) * mm});
            skLineSegment(sketch, "E3872", {"start": v(44.16, -8.29) * mm, "end": v(44.37, -8.33) * mm});
            skLineSegment(sketch, "E3873", {"start": v(44.37, -8.33) * mm, "end": v(44.58, -8.37) * mm});
            skLineSegment(sketch, "E3874", {"start": v(44.58, -8.37) * mm, "end": v(44.8, -8.4) * mm});
            skLineSegment(sketch, "E3875", {"start": v(44.8, -8.4) * mm, "end": v(45, -8.44) * mm});
            skLineSegment(sketch, "E3876", {"start": v(45, -8.44) * mm, "end": v(45.22, -8.48) * mm});
            skLineSegment(sketch, "E3877", {"start": v(45.22, -8.48) * mm, "end": v(45.43, -8.52) * mm});
            skLineSegment(sketch, "E3878", {"start": v(45.43, -8.52) * mm, "end": v(45.64, -8.53) * mm});
            skLineSegment(sketch, "E3879", {"start": v(45.64, -8.53) * mm, "end": v(45.84, -8.49) * mm});
            skLineSegment(sketch, "E3880", {"start": v(45.84, -8.49) * mm, "end": v(46.02, -8.4) * mm});
            skLineSegment(sketch, "E3881", {"start": v(46.02, -8.4) * mm, "end": v(46.17, -8.25) * mm});
            skLineSegment(sketch, "E3882", {"start": v(46.17, -8.25) * mm, "end": v(46.27, -8.08) * mm});
            skLineSegment(sketch, "E3883", {"start": v(46.27, -8.08) * mm, "end": v(46.33, -7.89) * mm});
            skLineSegment(sketch, "E3884", {"start": v(46.33, -7.89) * mm, "end": v(46.34, -7.68) * mm});
            skLineSegment(sketch, "E3885", {"start": v(46.34, -7.68) * mm, "end": v(46.3, -7.49) * mm});
            skLineSegment(sketch, "E3886", {"start": v(46.3, -7.49) * mm, "end": v(46.2, -7.3) * mm});
            skLineSegment(sketch, "E3887", {"start": v(46.2, -7.3) * mm, "end": v(46.06, -7.16) * mm});
            skLineSegment(sketch, "E3888", {"start": v(46.06, -7.16) * mm, "end": v(45.89, -7.05) * mm});
            skLineSegment(sketch, "E3889", {"start": v(45.89, -7.05) * mm, "end": v(45.69, -7) * mm});
            skLineSegment(sketch, "E3890", {"start": v(45.69, -7) * mm, "end": v(45.48, -6.96) * mm});
            skLineSegment(sketch, "E3891", {"start": v(45.48, -6.96) * mm, "end": v(45.26, -6.93) * mm});
            skLineSegment(sketch, "E3892", {"start": v(45.26, -6.93) * mm, "end": v(45.05, -6.9) * mm});
            skLineSegment(sketch, "E3893", {"start": v(45.05, -6.9) * mm, "end": v(44.83, -6.86) * mm});
            skLineSegment(sketch, "E3894", {"start": v(44.83, -6.86) * mm, "end": v(44.62, -6.83) * mm});
            skLineSegment(sketch, "E3895", {"start": v(44.62, -6.83) * mm, "end": v(44.4, -6.8) * mm});
            skLineSegment(sketch, "E3896", {"start": v(44.4, -6.8) * mm, "end": v(44.19, -6.77) * mm});
            skLineSegment(sketch, "E3897", {"start": v(44.19, -6.77) * mm, "end": v(43.98, -6.74) * mm});
            skLineSegment(sketch, "E3898", {"start": v(43.98, -6.74) * mm, "end": v(43.76, -6.7) * mm});
            skLineSegment(sketch, "E3899", {"start": v(43.76, -6.7) * mm, "end": v(43.55, -6.67) * mm});
            skLineSegment(sketch, "E3900", {"start": v(43.55, -6.67) * mm, "end": v(43.33, -6.64) * mm});
            skLineSegment(sketch, "E3901", {"start": v(43.33, -6.64) * mm, "end": v(43.12, -6.6) * mm});
            skLineSegment(sketch, "E3902", {"start": v(43.12, -6.6) * mm, "end": v(42.9, -6.57) * mm});
            skLineSegment(sketch, "E3903", {"start": v(42.9, -6.57) * mm, "end": v(42.69, -6.54) * mm});
            skLineSegment(sketch, "E3904", {"start": v(42.69, -6.54) * mm, "end": v(42.48, -6.51) * mm});
            skLineSegment(sketch, "E3905", {"start": v(42.48, -6.51) * mm, "end": v(42.5, -6.29) * mm});
            skLineSegment(sketch, "E3906", {"start": v(42.5, -6.29) * mm, "end": v(42.53, -6.07) * mm});
            skLineSegment(sketch, "E3907", {"start": v(42.53, -6.07) * mm, "end": v(42.56, -5.85) * mm});
            skLineSegment(sketch, "E3908", {"start": v(42.56, -5.85) * mm, "end": v(42.59, -5.63) * mm});
            skLineSegment(sketch, "E3909", {"start": v(42.59, -5.63) * mm, "end": v(42.61, -5.4) * mm});
            skLineSegment(sketch, "E3910", {"start": v(42.61, -5.4) * mm, "end": v(42.64, -5.18) * mm});
            skLineSegment(sketch, "E3911", {"start": v(42.64, -5.18) * mm, "end": v(42.67, -4.96) * mm});
            skLineSegment(sketch, "E3912", {"start": v(42.67, -4.96) * mm, "end": v(42.7, -4.74) * mm});
            skLineSegment(sketch, "E3913", {"start": v(42.7, -4.74) * mm, "end": v(42.72, -4.52) * mm});
            skLineSegment(sketch, "E3914", {"start": v(42.72, -4.52) * mm, "end": v(42.75, -4.34) * mm});
            skLineSegment(sketch, "E3915", {"start": v(42.75, -4.34) * mm, "end": v(42.96, -4.37) * mm});
            skLineSegment(sketch, "E3916", {"start": v(42.96, -4.37) * mm, "end": v(43.18, -4.39) * mm});
            skLineSegment(sketch, "E3917", {"start": v(43.18, -4.39) * mm, "end": v(43.4, -4.4) * mm});
            skLineSegment(sketch, "E3918", {"start": v(43.4, -4.4) * mm, "end": v(43.6, -4.43) * mm});
            skLineSegment(sketch, "E3919", {"start": v(43.6, -4.43) * mm, "end": v(43.82, -4.45) * mm});
            skLineSegment(sketch, "E3920", {"start": v(43.82, -4.45) * mm, "end": v(44.04, -4.47) * mm});
            skLineSegment(sketch, "E3921", {"start": v(44.04, -4.47) * mm, "end": v(44.25, -4.5) * mm});
            skLineSegment(sketch, "E3922", {"start": v(44.25, -4.5) * mm, "end": v(44.47, -4.52) * mm});
            skLineSegment(sketch, "E3923", {"start": v(44.47, -4.52) * mm, "end": v(44.69, -4.54) * mm});
            skLineSegment(sketch, "E3924", {"start": v(44.69, -4.54) * mm, "end": v(44.9, -4.56) * mm});
            skLineSegment(sketch, "E3925", {"start": v(44.9, -4.56) * mm, "end": v(45.12, -4.58) * mm});
            skLineSegment(sketch, "E3926", {"start": v(45.12, -4.58) * mm, "end": v(45.33, -4.6) * mm});
            skLineSegment(sketch, "E3927", {"start": v(45.33, -4.6) * mm, "end": v(45.55, -4.62) * mm});
            skLineSegment(sketch, "E3928", {"start": v(45.55, -4.62) * mm, "end": v(45.76, -4.64) * mm});
            skLineSegment(sketch, "E3929", {"start": v(45.76, -4.64) * mm, "end": v(45.98, -4.67) * mm});
            skLineSegment(sketch, "E3930", {"start": v(45.98, -4.67) * mm, "end": v(46.18, -4.66) * mm});
            skLineSegment(sketch, "E3931", {"start": v(46.18, -4.66) * mm, "end": v(46.38, -4.6) * mm});
            skLineSegment(sketch, "E3932", {"start": v(46.38, -4.6) * mm, "end": v(46.55, -4.49) * mm});
            skLineSegment(sketch, "E3933", {"start": v(46.55, -4.49) * mm, "end": v(46.69, -4.34) * mm});
            skLineSegment(sketch, "E3934", {"start": v(46.69, -4.34) * mm, "end": v(46.78, -4.16) * mm});
            skLineSegment(sketch, "E3935", {"start": v(46.78, -4.16) * mm, "end": v(46.82, -3.96) * mm});
            skLineSegment(sketch, "E3936", {"start": v(46.82, -3.96) * mm, "end": v(46.81, -3.75) * mm});
            skLineSegment(sketch, "E3937", {"start": v(46.81, -3.75) * mm, "end": v(46.75, -3.56) * mm});
            skLineSegment(sketch, "E3938", {"start": v(46.75, -3.56) * mm, "end": v(46.64, -3.39) * mm});
            skLineSegment(sketch, "E3939", {"start": v(46.64, -3.39) * mm, "end": v(46.49, -3.25) * mm});
            skLineSegment(sketch, "E3940", {"start": v(46.49, -3.25) * mm, "end": v(46.3, -3.16) * mm});
            skLineSegment(sketch, "E3941", {"start": v(46.3, -3.16) * mm, "end": v(46.1, -3.12) * mm});
            skLineSegment(sketch, "E3942", {"start": v(46.1, -3.12) * mm, "end": v(45.9, -3.1) * mm});
            skLineSegment(sketch, "E3943", {"start": v(45.9, -3.1) * mm, "end": v(45.68, -3.1) * mm});
            skLineSegment(sketch, "E3944", {"start": v(45.68, -3.1) * mm, "end": v(45.46, -3.08) * mm});
            skLineSegment(sketch, "E3945", {"start": v(45.46, -3.08) * mm, "end": v(45.24, -3.06) * mm});
            skLineSegment(sketch, "E3946", {"start": v(45.24, -3.06) * mm, "end": v(45.03, -3.05) * mm});
            skLineSegment(sketch, "E3947", {"start": v(45.03, -3.05) * mm, "end": v(44.81, -3.03) * mm});
            skLineSegment(sketch, "E3948", {"start": v(44.81, -3.03) * mm, "end": v(44.6, -3.02) * mm});
            skLineSegment(sketch, "E3949", {"start": v(44.6, -3.02) * mm, "end": v(44.38, -3) * mm});
            skLineSegment(sketch, "E3950", {"start": v(44.38, -3) * mm, "end": v(44.16, -3) * mm});
            skLineSegment(sketch, "E3951", {"start": v(44.16, -3) * mm, "end": v(43.95, -2.98) * mm});
            skLineSegment(sketch, "E3952", {"start": v(43.95, -2.98) * mm, "end": v(43.73, -2.96) * mm});
            skLineSegment(sketch, "E3953", {"start": v(43.73, -2.96) * mm, "end": v(43.51, -2.95) * mm});
            skLineSegment(sketch, "E3954", {"start": v(43.51, -2.95) * mm, "end": v(43.3, -2.93) * mm});
            skLineSegment(sketch, "E3955", {"start": v(43.3, -2.93) * mm, "end": v(43.08, -2.92) * mm});
            skLineSegment(sketch, "E3956", {"start": v(43.08, -2.92) * mm, "end": v(42.86, -2.9) * mm});
            skLineSegment(sketch, "E3957", {"start": v(42.86, -2.9) * mm, "end": v(42.87, -2.68) * mm});
            skLineSegment(sketch, "E3958", {"start": v(42.87, -2.68) * mm, "end": v(42.88, -2.46) * mm});
            skLineSegment(sketch, "E3959", {"start": v(42.88, -2.46) * mm, "end": v(42.9, -2.24) * mm});
            skLineSegment(sketch, "E3960", {"start": v(42.9, -2.24) * mm, "end": v(42.9, -2.01) * mm});
            skLineSegment(sketch, "E3961", {"start": v(42.9, -2.01) * mm, "end": v(42.91, -1.8) * mm});
            skLineSegment(sketch, "E3962", {"start": v(42.91, -1.8) * mm, "end": v(42.92, -1.57) * mm});
            skLineSegment(sketch, "E3963", {"start": v(42.92, -1.57) * mm, "end": v(42.93, -1.35) * mm});
            skLineSegment(sketch, "E3964", {"start": v(42.93, -1.35) * mm, "end": v(42.94, -1.12) * mm});
            skLineSegment(sketch, "E3965", {"start": v(42.94, -1.12) * mm, "end": v(42.95, -0.9) * mm});
            skLineSegment(sketch, "E3966", {"start": v(42.95, -0.9) * mm, "end": v(42.95, -0.72) * mm});
            skLineSegment(sketch, "E3967", {"start": v(-6.68, 2.28) * mm, "end": v(-6.53, 2.64) * mm});
            skLineSegment(sketch, "E3968", {"start": v(-6.53, 2.64) * mm, "end": v(-6.35, 2.98) * mm});
            skLineSegment(sketch, "E3969", {"start": v(-6.35, 2.98) * mm, "end": v(-6.15, 3.32) * mm});
            skLineSegment(sketch, "E3970", {"start": v(-6.15, 3.32) * mm, "end": v(-5.94, 3.64) * mm});
            skLineSegment(sketch, "E3971", {"start": v(-5.94, 3.64) * mm, "end": v(-5.7, 3.94) * mm});
            skLineSegment(sketch, "E3972", {"start": v(-5.7, 3.94) * mm, "end": v(-5.44, 4.24) * mm});
            skLineSegment(sketch, "E3973", {"start": v(-5.44, 4.24) * mm, "end": v(-5.17, 4.51) * mm});
            skLineSegment(sketch, "E3974", {"start": v(-5.17, 4.51) * mm, "end": v(-4.87, 4.77) * mm});
            skLineSegment(sketch, "E3975", {"start": v(-4.87, 4.77) * mm, "end": v(-4.57, 5) * mm});
            skLineSegment(sketch, "E3976", {"start": v(-4.57, 5) * mm, "end": v(-4.25, 5.23) * mm});
            skLineSegment(sketch, "E3977", {"start": v(-4.25, 5.23) * mm, "end": v(-3.91, 5.42) * mm});
            skLineSegment(sketch, "E3978", {"start": v(-3.91, 5.42) * mm, "end": v(-3.56, 5.6) * mm});
            skLineSegment(sketch, "E3979", {"start": v(-3.56, 5.6) * mm, "end": v(-3.2, 5.75) * mm});
            skLineSegment(sketch, "E3980", {"start": v(-3.2, 5.75) * mm, "end": v(-3.14, 5.78) * mm});
            skLineSegment(sketch, "E3981", {"start": v(-3.14, 5.78) * mm, "end": v(-3.24, 39.43) * mm});
            skLineSegment(sketch, "E3982", {"start": v(-3.24, 39.43) * mm, "end": v(-3.4, 39.42) * mm});
            skLineSegment(sketch, "E3983", {"start": v(-3.4, 39.42) * mm, "end": v(-5.88, 39.19) * mm});
            skLineSegment(sketch, "E3984", {"start": v(-5.88, 39.19) * mm, "end": v(-8.33, 38.8) * mm});
            skLineSegment(sketch, "E3985", {"start": v(-8.33, 38.8) * mm, "end": v(-10.75, 38.26) * mm});
            skLineSegment(sketch, "E3986", {"start": v(-10.75, 38.26) * mm, "end": v(-13.13, 37.57) * mm});
            skLineSegment(sketch, "E3987", {"start": v(-13.13, 37.57) * mm, "end": v(-15.47, 36.72) * mm});
            skLineSegment(sketch, "E3988", {"start": v(-15.47, 36.72) * mm, "end": v(-17.75, 35.74) * mm});
            skLineSegment(sketch, "E3989", {"start": v(-17.75, 35.74) * mm, "end": v(-19.96, 34.61) * mm});
            skLineSegment(sketch, "E3990", {"start": v(-19.96, 34.61) * mm, "end": v(-22.1, 33.35) * mm});
            skLineSegment(sketch, "E3991", {"start": v(-22.1, 33.35) * mm, "end": v(-24.15, 31.96) * mm});
            skLineSegment(sketch, "E3992", {"start": v(-24.15, 31.96) * mm, "end": v(-26.1, 30.43) * mm});
            skLineSegment(sketch, "E3993", {"start": v(-26.1, 30.43) * mm, "end": v(-27.97, 28.8) * mm});
            skLineSegment(sketch, "E3994", {"start": v(-27.97, 28.8) * mm, "end": v(-29.72, 27.04) * mm});
            skLineSegment(sketch, "E3995", {"start": v(-29.72, 27.04) * mm, "end": v(-31.36, 25.18) * mm});
            skLineSegment(sketch, "E3996", {"start": v(-31.36, 25.18) * mm, "end": v(-32.88, 23.22) * mm});
            skLineSegment(sketch, "E3997", {"start": v(-32.88, 23.22) * mm, "end": v(-34.28, 21.16) * mm});
            skLineSegment(sketch, "E3998", {"start": v(-34.28, 21.16) * mm, "end": v(-35.54, 19.03) * mm});
            skLineSegment(sketch, "E3999", {"start": v(-35.54, 19.03) * mm, "end": v(-36.67, 16.82) * mm});
            skLineSegment(sketch, "E4000", {"start": v(-36.67, 16.82) * mm, "end": v(-37.65, 14.54) * mm});
            skLineSegment(sketch, "E4001", {"start": v(-37.65, 14.54) * mm, "end": v(-38.5, 12.2) * mm});
            skLineSegment(sketch, "E4002", {"start": v(-38.5, 12.2) * mm, "end": v(-39.19, 9.82) * mm});
            skLineSegment(sketch, "E4003", {"start": v(-39.19, 9.82) * mm, "end": v(-39.73, 7.4) * mm});
            skLineSegment(sketch, "E4004", {"start": v(-39.73, 7.4) * mm, "end": v(-40.12, 4.95) * mm});
            skLineSegment(sketch, "E4005", {"start": v(-40.12, 4.95) * mm, "end": v(-40.35, 2.48) * mm});
            skLineSegment(sketch, "E4006", {"start": v(-40.35, 2.48) * mm, "end": v(-40.36, 2.3) * mm});
            skLineSegment(sketch, "E4007", {"start": v(-40.36, 2.3) * mm, "end": v(-6.7, 2.21) * mm});
            skLineSegment(sketch, "E4008", {"start": v(-6.7, 2.21) * mm, "end": v(-6.68, 2.28) * mm});
            skLineSegment(sketch, "E4009", {"start": v(38.5, 2.3) * mm, "end": v(38.5, 2.48) * mm});
            skLineSegment(sketch, "E4010", {"start": v(38.5, 2.48) * mm, "end": v(38.26, 4.95) * mm});
            skLineSegment(sketch, "E4011", {"start": v(38.26, 4.95) * mm, "end": v(37.87, 7.4) * mm});
            skLineSegment(sketch, "E4012", {"start": v(37.87, 7.4) * mm, "end": v(37.33, 9.82) * mm});
            skLineSegment(sketch, "E4013", {"start": v(37.33, 9.82) * mm, "end": v(36.64, 12.2) * mm});
            skLineSegment(sketch, "E4014", {"start": v(36.64, 12.2) * mm, "end": v(35.8, 14.54) * mm});
            skLineSegment(sketch, "E4015", {"start": v(35.8, 14.54) * mm, "end": v(34.81, 16.82) * mm});
            skLineSegment(sketch, "E4016", {"start": v(34.81, 16.82) * mm, "end": v(33.68, 19.03) * mm});
            skLineSegment(sketch, "E4017", {"start": v(33.68, 19.03) * mm, "end": v(32.42, 21.16) * mm});
            skLineSegment(sketch, "E4018", {"start": v(32.42, 21.16) * mm, "end": v(31.03, 23.22) * mm});
            skLineSegment(sketch, "E4019", {"start": v(31.03, 23.22) * mm, "end": v(29.5, 25.18) * mm});
            skLineSegment(sketch, "E4020", {"start": v(29.5, 25.18) * mm, "end": v(27.86, 27.04) * mm});
            skLineSegment(sketch, "E4021", {"start": v(27.86, 27.04) * mm, "end": v(26.11, 28.8) * mm});
            skLineSegment(sketch, "E4022", {"start": v(26.11, 28.8) * mm, "end": v(24.25, 30.43) * mm});
            skLineSegment(sketch, "E4023", {"start": v(24.25, 30.43) * mm, "end": v(22.29, 31.96) * mm});
            skLineSegment(sketch, "E4024", {"start": v(22.29, 31.96) * mm, "end": v(20.24, 33.35) * mm});
            skLineSegment(sketch, "E4025", {"start": v(20.24, 33.35) * mm, "end": v(18.1, 34.61) * mm});
            skLineSegment(sketch, "E4026", {"start": v(18.1, 34.61) * mm, "end": v(15.89, 35.74) * mm});
            skLineSegment(sketch, "E4027", {"start": v(15.89, 35.74) * mm, "end": v(13.61, 36.72) * mm});
            skLineSegment(sketch, "E4028", {"start": v(13.61, 36.72) * mm, "end": v(11.28, 37.57) * mm});
            skLineSegment(sketch, "E4029", {"start": v(11.28, 37.57) * mm, "end": v(8.9, 38.26) * mm});
            skLineSegment(sketch, "E4030", {"start": v(8.9, 38.26) * mm, "end": v(6.47, 38.8) * mm});
            skLineSegment(sketch, "E4031", {"start": v(6.47, 38.8) * mm, "end": v(4.02, 39.19) * mm});
            skLineSegment(sketch, "E4032", {"start": v(4.02, 39.19) * mm, "end": v(1.55, 39.42) * mm});
            skLineSegment(sketch, "E4033", {"start": v(1.55, 39.42) * mm, "end": v(1.38, 39.43) * mm});
            skLineSegment(sketch, "E4034", {"start": v(1.38, 39.43) * mm, "end": v(1.28, 5.78) * mm});
            skLineSegment(sketch, "E4035", {"start": v(1.28, 5.78) * mm, "end": v(1.35, 5.75) * mm});
            skLineSegment(sketch, "E4036", {"start": v(1.35, 5.75) * mm, "end": v(1.7, 5.6) * mm});
            skLineSegment(sketch, "E4037", {"start": v(1.7, 5.6) * mm, "end": v(2.05, 5.42) * mm});
            skLineSegment(sketch, "E4038", {"start": v(2.05, 5.42) * mm, "end": v(2.39, 5.23) * mm});
            skLineSegment(sketch, "E4039", {"start": v(2.39, 5.23) * mm, "end": v(2.7, 5) * mm});
            skLineSegment(sketch, "E4040", {"start": v(2.7, 5) * mm, "end": v(3.02, 4.77) * mm});
            skLineSegment(sketch, "E4041", {"start": v(3.02, 4.77) * mm, "end": v(3.3, 4.51) * mm});
            skLineSegment(sketch, "E4042", {"start": v(3.3, 4.51) * mm, "end": v(3.58, 4.24) * mm});
            skLineSegment(sketch, "E4043", {"start": v(3.58, 4.24) * mm, "end": v(3.84, 3.94) * mm});
            skLineSegment(sketch, "E4044", {"start": v(3.84, 3.94) * mm, "end": v(4.08, 3.64) * mm});
            skLineSegment(sketch, "E4045", {"start": v(4.08, 3.64) * mm, "end": v(4.3, 3.32) * mm});
            skLineSegment(sketch, "E4046", {"start": v(4.3, 3.32) * mm, "end": v(4.5, 2.98) * mm});
            skLineSegment(sketch, "E4047", {"start": v(4.5, 2.98) * mm, "end": v(4.67, 2.64) * mm});
            skLineSegment(sketch, "E4048", {"start": v(4.67, 2.64) * mm, "end": v(4.83, 2.28) * mm});
            skLineSegment(sketch, "E4049", {"start": v(4.83, 2.28) * mm, "end": v(4.85, 2.21) * mm});
            skLineSegment(sketch, "E4050", {"start": v(4.85, 2.21) * mm, "end": v(38.5, 2.3) * mm});
            skLineSegment(sketch, "E4051", {"start": v(1.55, -39.42) * mm, "end": v(4.02, -39.19) * mm});
            skLineSegment(sketch, "E4052", {"start": v(4.02, -39.19) * mm, "end": v(6.47, -38.8) * mm});
            skLineSegment(sketch, "E4053", {"start": v(6.47, -38.8) * mm, "end": v(8.9, -38.26) * mm});
            skLineSegment(sketch, "E4054", {"start": v(8.9, -38.26) * mm, "end": v(11.28, -37.57) * mm});
            skLineSegment(sketch, "E4055", {"start": v(11.28, -37.57) * mm, "end": v(13.61, -36.72) * mm});
            skLineSegment(sketch, "E4056", {"start": v(13.61, -36.72) * mm, "end": v(15.89, -35.74) * mm});
            skLineSegment(sketch, "E4057", {"start": v(15.89, -35.74) * mm, "end": v(18.1, -34.61) * mm});
            skLineSegment(sketch, "E4058", {"start": v(18.1, -34.61) * mm, "end": v(20.24, -33.35) * mm});
            skLineSegment(sketch, "E4059", {"start": v(20.24, -33.35) * mm, "end": v(22.29, -31.96) * mm});
            skLineSegment(sketch, "E4060", {"start": v(22.29, -31.96) * mm, "end": v(24.25, -30.43) * mm});
            skLineSegment(sketch, "E4061", {"start": v(24.25, -30.43) * mm, "end": v(26.11, -28.8) * mm});
            skLineSegment(sketch, "E4062", {"start": v(26.11, -28.8) * mm, "end": v(27.86, -27.04) * mm});
            skLineSegment(sketch, "E4063", {"start": v(27.86, -27.04) * mm, "end": v(29.5, -25.18) * mm});
            skLineSegment(sketch, "E4064", {"start": v(29.5, -25.18) * mm, "end": v(31.03, -23.22) * mm});
            skLineSegment(sketch, "E4065", {"start": v(31.03, -23.22) * mm, "end": v(32.42, -21.16) * mm});
            skLineSegment(sketch, "E4066", {"start": v(32.42, -21.16) * mm, "end": v(33.68, -19.03) * mm});
            skLineSegment(sketch, "E4067", {"start": v(33.68, -19.03) * mm, "end": v(34.81, -16.82) * mm});
            skLineSegment(sketch, "E4068", {"start": v(34.81, -16.82) * mm, "end": v(35.8, -14.54) * mm});
            skLineSegment(sketch, "E4069", {"start": v(35.8, -14.54) * mm, "end": v(36.64, -12.2) * mm});
            skLineSegment(sketch, "E4070", {"start": v(36.64, -12.2) * mm, "end": v(37.33, -9.82) * mm});
            skLineSegment(sketch, "E4071", {"start": v(37.33, -9.82) * mm, "end": v(37.87, -7.4) * mm});
            skLineSegment(sketch, "E4072", {"start": v(37.87, -7.4) * mm, "end": v(38.26, -4.95) * mm});
            skLineSegment(sketch, "E4073", {"start": v(38.26, -4.95) * mm, "end": v(38.5, -2.48) * mm});
            skLineSegment(sketch, "E4074", {"start": v(38.5, -2.48) * mm, "end": v(38.5, -2.3) * mm});
            skLineSegment(sketch, "E4075", {"start": v(38.5, -2.3) * mm, "end": v(4.85, -2.21) * mm});
            skLineSegment(sketch, "E4076", {"start": v(4.85, -2.21) * mm, "end": v(4.83, -2.28) * mm});
            skLineSegment(sketch, "E4077", {"start": v(4.83, -2.28) * mm, "end": v(4.67, -2.64) * mm});
            skLineSegment(sketch, "E4078", {"start": v(4.67, -2.64) * mm, "end": v(4.5, -2.98) * mm});
            skLineSegment(sketch, "E4079", {"start": v(4.5, -2.98) * mm, "end": v(4.3, -3.32) * mm});
            skLineSegment(sketch, "E4080", {"start": v(4.3, -3.32) * mm, "end": v(4.08, -3.64) * mm});
            skLineSegment(sketch, "E4081", {"start": v(4.08, -3.64) * mm, "end": v(3.84, -3.94) * mm});
            skLineSegment(sketch, "E4082", {"start": v(3.84, -3.94) * mm, "end": v(3.58, -4.24) * mm});
            skLineSegment(sketch, "E4083", {"start": v(3.58, -4.24) * mm, "end": v(3.3, -4.51) * mm});
            skLineSegment(sketch, "E4084", {"start": v(3.3, -4.51) * mm, "end": v(3.02, -4.77) * mm});
            skLineSegment(sketch, "E4085", {"start": v(3.02, -4.77) * mm, "end": v(2.7, -5) * mm});
            skLineSegment(sketch, "E4086", {"start": v(2.7, -5) * mm, "end": v(2.39, -5.23) * mm});
            skLineSegment(sketch, "E4087", {"start": v(2.39, -5.23) * mm, "end": v(2.05, -5.42) * mm});
            skLineSegment(sketch, "E4088", {"start": v(2.05, -5.42) * mm, "end": v(1.7, -5.6) * mm});
            skLineSegment(sketch, "E4089", {"start": v(1.7, -5.6) * mm, "end": v(1.35, -5.75) * mm});
            skLineSegment(sketch, "E4090", {"start": v(1.35, -5.75) * mm, "end": v(1.28, -5.78) * mm});
            skLineSegment(sketch, "E4091", {"start": v(1.28, -5.78) * mm, "end": v(1.38, -39.43) * mm});
            skLineSegment(sketch, "E4092", {"start": v(1.38, -39.43) * mm, "end": v(1.55, -39.42) * mm});
            skLineSegment(sketch, "E4093", {"start": v(-3.14, -5.78) * mm, "end": v(-3.2, -5.75) * mm});
            skLineSegment(sketch, "E4094", {"start": v(-3.2, -5.75) * mm, "end": v(-3.56, -5.6) * mm});
            skLineSegment(sketch, "E4095", {"start": v(-3.56, -5.6) * mm, "end": v(-3.91, -5.42) * mm});
            skLineSegment(sketch, "E4096", {"start": v(-3.91, -5.42) * mm, "end": v(-4.25, -5.23) * mm});
            skLineSegment(sketch, "E4097", {"start": v(-4.25, -5.23) * mm, "end": v(-4.57, -5) * mm});
            skLineSegment(sketch, "E4098", {"start": v(-4.57, -5) * mm, "end": v(-4.87, -4.77) * mm});
            skLineSegment(sketch, "E4099", {"start": v(-4.87, -4.77) * mm, "end": v(-5.17, -4.51) * mm});
            skLineSegment(sketch, "E4100", {"start": v(-5.17, -4.51) * mm, "end": v(-5.44, -4.24) * mm});
            skLineSegment(sketch, "E4101", {"start": v(-5.44, -4.24) * mm, "end": v(-5.7, -3.94) * mm});
            skLineSegment(sketch, "E4102", {"start": v(-5.7, -3.94) * mm, "end": v(-5.94, -3.64) * mm});
            skLineSegment(sketch, "E4103", {"start": v(-5.94, -3.64) * mm, "end": v(-6.15, -3.32) * mm});
            skLineSegment(sketch, "E4104", {"start": v(-6.15, -3.32) * mm, "end": v(-6.35, -2.98) * mm});
            skLineSegment(sketch, "E4105", {"start": v(-6.35, -2.98) * mm, "end": v(-6.53, -2.64) * mm});
            skLineSegment(sketch, "E4106", {"start": v(-6.53, -2.64) * mm, "end": v(-6.68, -2.28) * mm});
            skLineSegment(sketch, "E4107", {"start": v(-6.68, -2.28) * mm, "end": v(-6.7, -2.21) * mm});
            skLineSegment(sketch, "E4108", {"start": v(-6.7, -2.21) * mm, "end": v(-40.36, -2.3) * mm});
            skLineSegment(sketch, "E4109", {"start": v(-40.36, -2.3) * mm, "end": v(-40.35, -2.48) * mm});
            skLineSegment(sketch, "E4110", {"start": v(-40.35, -2.48) * mm, "end": v(-40.12, -4.95) * mm});
            skLineSegment(sketch, "E4111", {"start": v(-40.12, -4.95) * mm, "end": v(-39.73, -7.4) * mm});
            skLineSegment(sketch, "E4112", {"start": v(-39.73, -7.4) * mm, "end": v(-39.19, -9.82) * mm});
            skLineSegment(sketch, "E4113", {"start": v(-39.19, -9.82) * mm, "end": v(-38.5, -12.2) * mm});
            skLineSegment(sketch, "E4114", {"start": v(-38.5, -12.2) * mm, "end": v(-37.65, -14.54) * mm});
            skLineSegment(sketch, "E4115", {"start": v(-37.65, -14.54) * mm, "end": v(-36.67, -16.82) * mm});
            skLineSegment(sketch, "E4116", {"start": v(-36.67, -16.82) * mm, "end": v(-35.54, -19.03) * mm});
            skLineSegment(sketch, "E4117", {"start": v(-35.54, -19.03) * mm, "end": v(-34.28, -21.16) * mm});
            skLineSegment(sketch, "E4118", {"start": v(-34.28, -21.16) * mm, "end": v(-32.88, -23.22) * mm});
            skLineSegment(sketch, "E4119", {"start": v(-32.88, -23.22) * mm, "end": v(-31.36, -25.18) * mm});
            skLineSegment(sketch, "E4120", {"start": v(-31.36, -25.18) * mm, "end": v(-29.72, -27.04) * mm});
            skLineSegment(sketch, "E4121", {"start": v(-29.72, -27.04) * mm, "end": v(-27.97, -28.8) * mm});
            skLineSegment(sketch, "E4122", {"start": v(-27.97, -28.8) * mm, "end": v(-26.1, -30.43) * mm});
            skLineSegment(sketch, "E4123", {"start": v(-26.1, -30.43) * mm, "end": v(-24.15, -31.96) * mm});
            skLineSegment(sketch, "E4124", {"start": v(-24.15, -31.96) * mm, "end": v(-22.1, -33.35) * mm});
            skLineSegment(sketch, "E4125", {"start": v(-22.1, -33.35) * mm, "end": v(-19.96, -34.61) * mm});
            skLineSegment(sketch, "E4126", {"start": v(-19.96, -34.61) * mm, "end": v(-17.75, -35.74) * mm});
            skLineSegment(sketch, "E4127", {"start": v(-17.75, -35.74) * mm, "end": v(-15.47, -36.72) * mm});
            skLineSegment(sketch, "E4128", {"start": v(-15.47, -36.72) * mm, "end": v(-13.13, -37.57) * mm});
            skLineSegment(sketch, "E4129", {"start": v(-13.13, -37.57) * mm, "end": v(-10.75, -38.26) * mm});
            skLineSegment(sketch, "E4130", {"start": v(-10.75, -38.26) * mm, "end": v(-8.33, -38.8) * mm});
            skLineSegment(sketch, "E4131", {"start": v(-8.33, -38.8) * mm, "end": v(-5.88, -39.19) * mm});
            skLineSegment(sketch, "E4132", {"start": v(-5.88, -39.19) * mm, "end": v(-3.4, -39.42) * mm});
            skLineSegment(sketch, "E4133", {"start": v(-3.4, -39.42) * mm, "end": v(-3.24, -39.43) * mm});
            skLineSegment(sketch, "E4134", {"start": v(-3.24, -39.43) * mm, "end": v(-3.14, -5.78) * mm});
            skCircle(sketch, "E4135", {"center": v(-0.93, 0) * mm, "radius": 10.05 * mm});
            skLineSegment(sketch, "E4136.right", {"start": v(3.07, 1.5) * mm, "end": v(3.07, -1.5) * mm});
            skLineSegment(sketch, "E4137", {"start": v(-0.93, 1.5) * mm, "end": v(-0.93, -1.5) * mm, "construction": true});
            skLineSegment(sketch, "E4136.bottom", {"start": v(-4.93, 1.5) * mm, "end": v(3.07, 1.5) * mm});
            skLineSegment(sketch, "E4136.top", {"start": v(-4.93, -1.5) * mm, "end": v(3.07, -1.5) * mm});
            skLineSegment(sketch, "E4136.left", {"start": v(-4.93, 1.5) * mm, "end": v(-4.93, -1.5) * mm});
            skCircle(sketch, "E4138", {"center": v(-0.93, 0) * mm, "radius": 3.25 * mm});
            skSolve(sketch);
        }
        {
            var Q0;
            Q0=makeQuery(id+"F0.imprint","IMPRINT",FACE,{"disambiguationData":[TD([[makeQuery(id+"F0.imprint","IMPRINT",EDGE,{"derivedFrom":sQuery(id+"F0.wireOp",EDGE,"E0")}),1.0]])]});
            var Q1;
            Q1=makeQuery(id+"F0.imprint","IMPRINT",FACE,{"disambiguationData":[TD([[makeQuery(id+"F0.imprint","IMPRINT",EDGE,{"derivedFrom":sQuery(id+"F0.wireOp",EDGE,"E3967")}),-1.0]])]});
            var Q2;
            {var subQ4=sQuery(id+"F0.wireOp",EDGE,"E4093");Q2=makeQuery(id+"F0.imprint","IMPRINT",FACE,{"disambiguationData":[TD([[makeQuery(id+"F0.imprint","IMPRINT",EDGE,{"derivedFrom":subQ4}),1.0]])]});}
            var Q3;
            {var subQ0=sQuery(id+"F0.wireOp",EDGE,"E4076");Q3=makeQuery(id+"F0.imprint","IMPRINT",FACE,{"disambiguationData":[TD([[makeQuery(id+"F0.imprint","IMPRINT",EDGE,{"derivedFrom":subQ0}),1.0]])]});}
            var Q4;
            {var subQ0=sQuery(id+"F0.wireOp",EDGE,"E4035");Q4=makeQuery(id+"F0.imprint","IMPRINT",FACE,{"disambiguationData":[TD([[makeQuery(id+"F0.imprint","IMPRINT",EDGE,{"derivedFrom":subQ0}),1.0]])]});}
            var Q5;
            Q5=makeQuery(id+"F0.imprint","IMPRINT",FACE,{"disambiguationData":[TD([[makeQuery(id+"F0.imprint","IMPRINT",EDGE,{"derivedFrom":sQuery(id+"F0.wireOp",EDGE,"E3967")}),1.0]])]});
            extrude(context, id + "F1", {"entities" : qUnion([Q0, Q1, Q2, Q3, Q4, Q5]), "depth" : 5 * mm});
        }
        {
            var Q0;
            Q0=makeQuery(id+"F1.opExtrude","CAP_FACE",FACE,{"disambiguationData":[OSD([sQuery(id+"F0.wireOp",EDGE,"E0"),sQuery(id+"F0.wireOp",EDGE,"E1"),sQuery(id+"F0.wireOp",EDGE,"E2"),sQuery(id+"F0.wireOp",EDGE,"E3"),sQuery(id+"F0.wireOp",EDGE,"E4"),sQuery(id+"F0.wireOp",EDGE,"E5"),sQuery(id+"F0.wireOp",EDGE,"E6"),sQuery(id+"F0.wireOp",EDGE,"E7"),sQuery(id+"F0.wireOp",EDGE,"E8"),sQuery(id+"F0.wireOp",EDGE,"E9"),sQuery(id+"F0.wireOp",EDGE,"E10"),sQuery(id+"F0.wireOp",EDGE,"E11"),sQuery(id+"F0.wireOp",EDGE,"E12"),sQuery(id+"F0.wireOp",EDGE,"E13"),sQuery(id+"F0.wireOp",EDGE,"E14"),sQuery(id+"F0.wireOp",EDGE,"E15"),sQuery(id+"F0.wireOp",EDGE,"E16"),sQuery(id+"F0.wireOp",EDGE,"E17"),sQuery(id+"F0.wireOp",EDGE,"E18"),sQuery(id+"F0.wireOp",EDGE,"E19"),sQuery(id+"F0.wireOp",EDGE,"E20"),sQuery(id+"F0.wireOp",EDGE,"E21"),sQuery(id+"F0.wireOp",EDGE,"E22"),sQuery(id+"F0.wireOp",EDGE,"E23"),sQuery(id+"F0.wireOp",EDGE,"E24"),sQuery(id+"F0.wireOp",EDGE,"E25"),sQuery(id+"F0.wireOp",EDGE,"E26"),sQuery(id+"F0.wireOp",EDGE,"E27"),sQuery(id+"F0.wireOp",EDGE,"E28"),sQuery(id+"F0.wireOp",EDGE,"E29"),sQuery(id+"F0.wireOp",EDGE,"E30"),sQuery(id+"F0.wireOp",EDGE,"E31"),sQuery(id+"F0.wireOp",EDGE,"E32"),sQuery(id+"F0.wireOp",EDGE,"E33"),sQuery(id+"F0.wireOp",EDGE,"E34"),sQuery(id+"F0.wireOp",EDGE,"E35"),sQuery(id+"F0.wireOp",EDGE,"E36"),sQuery(id+"F0.wireOp",EDGE,"E37"),sQuery(id+"F0.wireOp",EDGE,"E38"),sQuery(id+"F0.wireOp",EDGE,"E39"),sQuery(id+"F0.wireOp",EDGE,"E40"),sQuery(id+"F0.wireOp",EDGE,"E41"),sQuery(id+"F0.wireOp",EDGE,"E42"),sQuery(id+"F0.wireOp",EDGE,"E43"),sQuery(id+"F0.wireOp",EDGE,"E44"),sQuery(id+"F0.wireOp",EDGE,"E45"),sQuery(id+"F0.wireOp",EDGE,"E46"),sQuery(id+"F0.wireOp",EDGE,"E47"),sQuery(id+"F0.wireOp",EDGE,"E48"),sQuery(id+"F0.wireOp",EDGE,"E49"),sQuery(id+"F0.wireOp",EDGE,"E50"),sQuery(id+"F0.wireOp",EDGE,"E51"),sQuery(id+"F0.wireOp",EDGE,"E52"),sQuery(id+"F0.wireOp",EDGE,"E53"),sQuery(id+"F0.wireOp",EDGE,"E54"),sQuery(id+"F0.wireOp",EDGE,"E55"),sQuery(id+"F0.wireOp",EDGE,"E56"),sQuery(id+"F0.wireOp",EDGE,"E57"),sQuery(id+"F0.wireOp",EDGE,"E58"),sQuery(id+"F0.wireOp",EDGE,"E59"),sQuery(id+"F0.wireOp",EDGE,"E60"),sQuery(id+"F0.wireOp",EDGE,"E61"),sQuery(id+"F0.wireOp",EDGE,"E62"),sQuery(id+"F0.wireOp",EDGE,"E63"),sQuery(id+"F0.wireOp",EDGE,"E64"),sQuery(id+"F0.wireOp",EDGE,"E65"),sQuery(id+"F0.wireOp",EDGE,"E66"),sQuery(id+"F0.wireOp",EDGE,"E67"),sQuery(id+"F0.wireOp",EDGE,"E68"),sQuery(id+"F0.wireOp",EDGE,"E69"),sQuery(id+"F0.wireOp",EDGE,"E70"),sQuery(id+"F0.wireOp",EDGE,"E71"),sQuery(id+"F0.wireOp",EDGE,"E72"),sQuery(id+"F0.wireOp",EDGE,"E73"),sQuery(id+"F0.wireOp",EDGE,"E74"),sQuery(id+"F0.wireOp",EDGE,"E75"),sQuery(id+"F0.wireOp",EDGE,"E76"),sQuery(id+"F0.wireOp",EDGE,"E77"),sQuery(id+"F0.wireOp",EDGE,"E78"),sQuery(id+"F0.wireOp",EDGE,"E79"),sQuery(id+"F0.wireOp",EDGE,"E80"),sQuery(id+"F0.wireOp",EDGE,"E81"),sQuery(id+"F0.wireOp",EDGE,"E82"),sQuery(id+"F0.wireOp",EDGE,"E83"),sQuery(id+"F0.wireOp",EDGE,"E84"),sQuery(id+"F0.wireOp",EDGE,"E85"),sQuery(id+"F0.wireOp",EDGE,"E86"),sQuery(id+"F0.wireOp",EDGE,"E87"),sQuery(id+"F0.wireOp",EDGE,"E88"),sQuery(id+"F0.wireOp",EDGE,"E89"),sQuery(id+"F0.wireOp",EDGE,"E90"),sQuery(id+"F0.wireOp",EDGE,"E91"),sQuery(id+"F0.wireOp",EDGE,"E92"),sQuery(id+"F0.wireOp",EDGE,"E93"),sQuery(id+"F0.wireOp",EDGE,"E94"),sQuery(id+"F0.wireOp",EDGE,"E95"),sQuery(id+"F0.wireOp",EDGE,"E96"),sQuery(id+"F0.wireOp",EDGE,"E97"),sQuery(id+"F0.wireOp",EDGE,"E98"),sQuery(id+"F0.wireOp",EDGE,"E99"),sQuery(id+"F0.wireOp",EDGE,"E100"),sQuery(id+"F0.wireOp",EDGE,"E101"),sQuery(id+"F0.wireOp",EDGE,"E102"),sQuery(id+"F0.wireOp",EDGE,"E103"),sQuery(id+"F0.wireOp",EDGE,"E104"),sQuery(id+"F0.wireOp",EDGE,"E105"),sQuery(id+"F0.wireOp",EDGE,"E106"),sQuery(id+"F0.wireOp",EDGE,"E107"),sQuery(id+"F0.wireOp",EDGE,"E108"),sQuery(id+"F0.wireOp",EDGE,"E109"),sQuery(id+"F0.wireOp",EDGE,"E110"),sQuery(id+"F0.wireOp",EDGE,"E111"),sQuery(id+"F0.wireOp",EDGE,"E112"),sQuery(id+"F0.wireOp",EDGE,"E113"),sQuery(id+"F0.wireOp",EDGE,"E114"),sQuery(id+"F0.wireOp",EDGE,"E115"),sQuery(id+"F0.wireOp",EDGE,"E116"),sQuery(id+"F0.wireOp",EDGE,"E117"),sQuery(id+"F0.wireOp",EDGE,"E118"),sQuery(id+"F0.wireOp",EDGE,"E119"),sQuery(id+"F0.wireOp",EDGE,"E120"),sQuery(id+"F0.wireOp",EDGE,"E121"),sQuery(id+"F0.wireOp",EDGE,"E122"),sQuery(id+"F0.wireOp",EDGE,"E123"),sQuery(id+"F0.wireOp",EDGE,"E124"),sQuery(id+"F0.wireOp",EDGE,"E125"),sQuery(id+"F0.wireOp",EDGE,"E126"),sQuery(id+"F0.wireOp",EDGE,"E127"),sQuery(id+"F0.wireOp",EDGE,"E128"),sQuery(id+"F0.wireOp",EDGE,"E129"),sQuery(id+"F0.wireOp",EDGE,"E130"),sQuery(id+"F0.wireOp",EDGE,"E131"),sQuery(id+"F0.wireOp",EDGE,"E132"),sQuery(id+"F0.wireOp",EDGE,"E133"),sQuery(id+"F0.wireOp",EDGE,"E134"),sQuery(id+"F0.wireOp",EDGE,"E135"),sQuery(id+"F0.wireOp",EDGE,"E136"),sQuery(id+"F0.wireOp",EDGE,"E137"),sQuery(id+"F0.wireOp",EDGE,"E138"),sQuery(id+"F0.wireOp",EDGE,"E139"),sQuery(id+"F0.wireOp",EDGE,"E140"),sQuery(id+"F0.wireOp",EDGE,"E141"),sQuery(id+"F0.wireOp",EDGE,"E142"),sQuery(id+"F0.wireOp",EDGE,"E143"),sQuery(id+"F0.wireOp",EDGE,"E144"),sQuery(id+"F0.wireOp",EDGE,"E145"),sQuery(id+"F0.wireOp",EDGE,"E146"),sQuery(id+"F0.wireOp",EDGE,"E147"),sQuery(id+"F0.wireOp",EDGE,"E148"),sQuery(id+"F0.wireOp",EDGE,"E149"),sQuery(id+"F0.wireOp",EDGE,"E150"),sQuery(id+"F0.wireOp",EDGE,"E151"),sQuery(id+"F0.wireOp",EDGE,"E152"),sQuery(id+"F0.wireOp",EDGE,"E153"),sQuery(id+"F0.wireOp",EDGE,"E154"),sQuery(id+"F0.wireOp",EDGE,"E155"),sQuery(id+"F0.wireOp",EDGE,"E156"),sQuery(id+"F0.wireOp",EDGE,"E157"),sQuery(id+"F0.wireOp",EDGE,"E158"),sQuery(id+"F0.wireOp",EDGE,"E159"),sQuery(id+"F0.wireOp",EDGE,"E160"),sQuery(id+"F0.wireOp",EDGE,"E161"),sQuery(id+"F0.wireOp",EDGE,"E162"),sQuery(id+"F0.wireOp",EDGE,"E163"),sQuery(id+"F0.wireOp",EDGE,"E164"),sQuery(id+"F0.wireOp",EDGE,"E165"),sQuery(id+"F0.wireOp",EDGE,"E166"),sQuery(id+"F0.wireOp",EDGE,"E167"),sQuery(id+"F0.wireOp",EDGE,"E168"),sQuery(id+"F0.wireOp",EDGE,"E169"),sQuery(id+"F0.wireOp",EDGE,"E170"),sQuery(id+"F0.wireOp",EDGE,"E171"),sQuery(id+"F0.wireOp",EDGE,"E172"),sQuery(id+"F0.wireOp",EDGE,"E173"),sQuery(id+"F0.wireOp",EDGE,"E174"),sQuery(id+"F0.wireOp",EDGE,"E175"),sQuery(id+"F0.wireOp",EDGE,"E176"),sQuery(id+"F0.wireOp",EDGE,"E177"),sQuery(id+"F0.wireOp",EDGE,"E178"),sQuery(id+"F0.wireOp",EDGE,"E179"),sQuery(id+"F0.wireOp",EDGE,"E180"),sQuery(id+"F0.wireOp",EDGE,"E181"),sQuery(id+"F0.wireOp",EDGE,"E182"),sQuery(id+"F0.wireOp",EDGE,"E183"),sQuery(id+"F0.wireOp",EDGE,"E184"),sQuery(id+"F0.wireOp",EDGE,"E185"),sQuery(id+"F0.wireOp",EDGE,"E186"),sQuery(id+"F0.wireOp",EDGE,"E187"),sQuery(id+"F0.wireOp",EDGE,"E188"),sQuery(id+"F0.wireOp",EDGE,"E189"),sQuery(id+"F0.wireOp",EDGE,"E190"),sQuery(id+"F0.wireOp",EDGE,"E191"),sQuery(id+"F0.wireOp",EDGE,"E192"),sQuery(id+"F0.wireOp",EDGE,"E193"),sQuery(id+"F0.wireOp",EDGE,"E194"),sQuery(id+"F0.wireOp",EDGE,"E195"),sQuery(id+"F0.wireOp",EDGE,"E196"),sQuery(id+"F0.wireOp",EDGE,"E197"),sQuery(id+"F0.wireOp",EDGE,"E198"),sQuery(id+"F0.wireOp",EDGE,"E199"),sQuery(id+"F0.wireOp",EDGE,"E200"),sQuery(id+"F0.wireOp",EDGE,"E201"),sQuery(id+"F0.wireOp",EDGE,"E202"),sQuery(id+"F0.wireOp",EDGE,"E203"),sQuery(id+"F0.wireOp",EDGE,"E204"),sQuery(id+"F0.wireOp",EDGE,"E205"),sQuery(id+"F0.wireOp",EDGE,"E206"),sQuery(id+"F0.wireOp",EDGE,"E207"),sQuery(id+"F0.wireOp",EDGE,"E208"),sQuery(id+"F0.wireOp",EDGE,"E209"),sQuery(id+"F0.wireOp",EDGE,"E210"),sQuery(id+"F0.wireOp",EDGE,"E211"),sQuery(id+"F0.wireOp",EDGE,"E212"),sQuery(id+"F0.wireOp",EDGE,"E213"),sQuery(id+"F0.wireOp",EDGE,"E214"),sQuery(id+"F0.wireOp",EDGE,"E215"),sQuery(id+"F0.wireOp",EDGE,"E216"),sQuery(id+"F0.wireOp",EDGE,"E217"),sQuery(id+"F0.wireOp",EDGE,"E218"),sQuery(id+"F0.wireOp",EDGE,"E219"),sQuery(id+"F0.wireOp",EDGE,"E220"),sQuery(id+"F0.wireOp",EDGE,"E221"),sQuery(id+"F0.wireOp",EDGE,"E222"),sQuery(id+"F0.wireOp",EDGE,"E223"),sQuery(id+"F0.wireOp",EDGE,"E224"),sQuery(id+"F0.wireOp",EDGE,"E225"),sQuery(id+"F0.wireOp",EDGE,"E226"),sQuery(id+"F0.wireOp",EDGE,"E227"),sQuery(id+"F0.wireOp",EDGE,"E228"),sQuery(id+"F0.wireOp",EDGE,"E229"),sQuery(id+"F0.wireOp",EDGE,"E230"),sQuery(id+"F0.wireOp",EDGE,"E231"),sQuery(id+"F0.wireOp",EDGE,"E232"),sQuery(id+"F0.wireOp",EDGE,"E233"),sQuery(id+"F0.wireOp",EDGE,"E234"),sQuery(id+"F0.wireOp",EDGE,"E235"),sQuery(id+"F0.wireOp",EDGE,"E236"),sQuery(id+"F0.wireOp",EDGE,"E237"),sQuery(id+"F0.wireOp",EDGE,"E238"),sQuery(id+"F0.wireOp",EDGE,"E239"),sQuery(id+"F0.wireOp",EDGE,"E240"),sQuery(id+"F0.wireOp",EDGE,"E241"),sQuery(id+"F0.wireOp",EDGE,"E242"),sQuery(id+"F0.wireOp",EDGE,"E243"),sQuery(id+"F0.wireOp",EDGE,"E244"),sQuery(id+"F0.wireOp",EDGE,"E245"),sQuery(id+"F0.wireOp",EDGE,"E246"),sQuery(id+"F0.wireOp",EDGE,"E247"),sQuery(id+"F0.wireOp",EDGE,"E248"),sQuery(id+"F0.wireOp",EDGE,"E249"),sQuery(id+"F0.wireOp",EDGE,"E250"),sQuery(id+"F0.wireOp",EDGE,"E251"),sQuery(id+"F0.wireOp",EDGE,"E252"),sQuery(id+"F0.wireOp",EDGE,"E253"),sQuery(id+"F0.wireOp",EDGE,"E254"),sQuery(id+"F0.wireOp",EDGE,"E255"),sQuery(id+"F0.wireOp",EDGE,"E256"),sQuery(id+"F0.wireOp",EDGE,"E257"),sQuery(id+"F0.wireOp",EDGE,"E258"),sQuery(id+"F0.wireOp",EDGE,"E259"),sQuery(id+"F0.wireOp",EDGE,"E260"),sQuery(id+"F0.wireOp",EDGE,"E261"),sQuery(id+"F0.wireOp",EDGE,"E262"),sQuery(id+"F0.wireOp",EDGE,"E263"),sQuery(id+"F0.wireOp",EDGE,"E264"),sQuery(id+"F0.wireOp",EDGE,"E265"),sQuery(id+"F0.wireOp",EDGE,"E266"),sQuery(id+"F0.wireOp",EDGE,"E267"),sQuery(id+"F0.wireOp",EDGE,"E268"),sQuery(id+"F0.wireOp",EDGE,"E269"),sQuery(id+"F0.wireOp",EDGE,"E270"),sQuery(id+"F0.wireOp",EDGE,"E271"),sQuery(id+"F0.wireOp",EDGE,"E272"),sQuery(id+"F0.wireOp",EDGE,"E273"),sQuery(id+"F0.wireOp",EDGE,"E274"),sQuery(id+"F0.wireOp",EDGE,"E275"),sQuery(id+"F0.wireOp",EDGE,"E276"),sQuery(id+"F0.wireOp",EDGE,"E277"),sQuery(id+"F0.wireOp",EDGE,"E278"),sQuery(id+"F0.wireOp",EDGE,"E279"),sQuery(id+"F0.wireOp",EDGE,"E280"),sQuery(id+"F0.wireOp",EDGE,"E281"),sQuery(id+"F0.wireOp",EDGE,"E282"),sQuery(id+"F0.wireOp",EDGE,"E283"),sQuery(id+"F0.wireOp",EDGE,"E284"),sQuery(id+"F0.wireOp",EDGE,"E285"),sQuery(id+"F0.wireOp",EDGE,"E286"),sQuery(id+"F0.wireOp",EDGE,"E287"),sQuery(id+"F0.wireOp",EDGE,"E288"),sQuery(id+"F0.wireOp",EDGE,"E289"),sQuery(id+"F0.wireOp",EDGE,"E290"),sQuery(id+"F0.wireOp",EDGE,"E291"),sQuery(id+"F0.wireOp",EDGE,"E292"),sQuery(id+"F0.wireOp",EDGE,"E293"),sQuery(id+"F0.wireOp",EDGE,"E294"),sQuery(id+"F0.wireOp",EDGE,"E295"),sQuery(id+"F0.wireOp",EDGE,"E296"),sQuery(id+"F0.wireOp",EDGE,"E297"),sQuery(id+"F0.wireOp",EDGE,"E298"),sQuery(id+"F0.wireOp",EDGE,"E299"),sQuery(id+"F0.wireOp",EDGE,"E300"),sQuery(id+"F0.wireOp",EDGE,"E301"),sQuery(id+"F0.wireOp",EDGE,"E302"),sQuery(id+"F0.wireOp",EDGE,"E303"),sQuery(id+"F0.wireOp",EDGE,"E304"),sQuery(id+"F0.wireOp",EDGE,"E305"),sQuery(id+"F0.wireOp",EDGE,"E306"),sQuery(id+"F0.wireOp",EDGE,"E307"),sQuery(id+"F0.wireOp",EDGE,"E308"),sQuery(id+"F0.wireOp",EDGE,"E309"),sQuery(id+"F0.wireOp",EDGE,"E310"),sQuery(id+"F0.wireOp",EDGE,"E311"),sQuery(id+"F0.wireOp",EDGE,"E312"),sQuery(id+"F0.wireOp",EDGE,"E313"),sQuery(id+"F0.wireOp",EDGE,"E314"),sQuery(id+"F0.wireOp",EDGE,"E315"),sQuery(id+"F0.wireOp",EDGE,"E316"),sQuery(id+"F0.wireOp",EDGE,"E317"),sQuery(id+"F0.wireOp",EDGE,"E318"),sQuery(id+"F0.wireOp",EDGE,"E319"),sQuery(id+"F0.wireOp",EDGE,"E320"),sQuery(id+"F0.wireOp",EDGE,"E321"),sQuery(id+"F0.wireOp",EDGE,"E322"),sQuery(id+"F0.wireOp",EDGE,"E323"),sQuery(id+"F0.wireOp",EDGE,"E324"),sQuery(id+"F0.wireOp",EDGE,"E325"),sQuery(id+"F0.wireOp",EDGE,"E326"),sQuery(id+"F0.wireOp",EDGE,"E327"),sQuery(id+"F0.wireOp",EDGE,"E328"),sQuery(id+"F0.wireOp",EDGE,"E329"),sQuery(id+"F0.wireOp",EDGE,"E330"),sQuery(id+"F0.wireOp",EDGE,"E331"),sQuery(id+"F0.wireOp",EDGE,"E332"),sQuery(id+"F0.wireOp",EDGE,"E333"),sQuery(id+"F0.wireOp",EDGE,"E334"),sQuery(id+"F0.wireOp",EDGE,"E335"),sQuery(id+"F0.wireOp",EDGE,"E336"),sQuery(id+"F0.wireOp",EDGE,"E337"),sQuery(id+"F0.wireOp",EDGE,"E338"),sQuery(id+"F0.wireOp",EDGE,"E339"),sQuery(id+"F0.wireOp",EDGE,"E340"),sQuery(id+"F0.wireOp",EDGE,"E341"),sQuery(id+"F0.wireOp",EDGE,"E342"),sQuery(id+"F0.wireOp",EDGE,"E343"),sQuery(id+"F0.wireOp",EDGE,"E344"),sQuery(id+"F0.wireOp",EDGE,"E345"),sQuery(id+"F0.wireOp",EDGE,"E346"),sQuery(id+"F0.wireOp",EDGE,"E347"),sQuery(id+"F0.wireOp",EDGE,"E348"),sQuery(id+"F0.wireOp",EDGE,"E349"),sQuery(id+"F0.wireOp",EDGE,"E350"),sQuery(id+"F0.wireOp",EDGE,"E351"),sQuery(id+"F0.wireOp",EDGE,"E352"),sQuery(id+"F0.wireOp",EDGE,"E353"),sQuery(id+"F0.wireOp",EDGE,"E354"),sQuery(id+"F0.wireOp",EDGE,"E355"),sQuery(id+"F0.wireOp",EDGE,"E356"),sQuery(id+"F0.wireOp",EDGE,"E357"),sQuery(id+"F0.wireOp",EDGE,"E358"),sQuery(id+"F0.wireOp",EDGE,"E359"),sQuery(id+"F0.wireOp",EDGE,"E360"),sQuery(id+"F0.wireOp",EDGE,"E361"),sQuery(id+"F0.wireOp",EDGE,"E362"),sQuery(id+"F0.wireOp",EDGE,"E363"),sQuery(id+"F0.wireOp",EDGE,"E364"),sQuery(id+"F0.wireOp",EDGE,"E365"),sQuery(id+"F0.wireOp",EDGE,"E366"),sQuery(id+"F0.wireOp",EDGE,"E367"),sQuery(id+"F0.wireOp",EDGE,"E368"),sQuery(id+"F0.wireOp",EDGE,"E369"),sQuery(id+"F0.wireOp",EDGE,"E370"),sQuery(id+"F0.wireOp",EDGE,"E371"),sQuery(id+"F0.wireOp",EDGE,"E372"),sQuery(id+"F0.wireOp",EDGE,"E373"),sQuery(id+"F0.wireOp",EDGE,"E374"),sQuery(id+"F0.wireOp",EDGE,"E375"),sQuery(id+"F0.wireOp",EDGE,"E376"),sQuery(id+"F0.wireOp",EDGE,"E377"),sQuery(id+"F0.wireOp",EDGE,"E378"),sQuery(id+"F0.wireOp",EDGE,"E379"),sQuery(id+"F0.wireOp",EDGE,"E380"),sQuery(id+"F0.wireOp",EDGE,"E381"),sQuery(id+"F0.wireOp",EDGE,"E382"),sQuery(id+"F0.wireOp",EDGE,"E383"),sQuery(id+"F0.wireOp",EDGE,"E384"),sQuery(id+"F0.wireOp",EDGE,"E385"),sQuery(id+"F0.wireOp",EDGE,"E386"),sQuery(id+"F0.wireOp",EDGE,"E387"),sQuery(id+"F0.wireOp",EDGE,"E388"),sQuery(id+"F0.wireOp",EDGE,"E389"),sQuery(id+"F0.wireOp",EDGE,"E390"),sQuery(id+"F0.wireOp",EDGE,"E391"),sQuery(id+"F0.wireOp",EDGE,"E392"),sQuery(id+"F0.wireOp",EDGE,"E393"),sQuery(id+"F0.wireOp",EDGE,"E394"),sQuery(id+"F0.wireOp",EDGE,"E395"),sQuery(id+"F0.wireOp",EDGE,"E396"),sQuery(id+"F0.wireOp",EDGE,"E397"),sQuery(id+"F0.wireOp",EDGE,"E398"),sQuery(id+"F0.wireOp",EDGE,"E399"),sQuery(id+"F0.wireOp",EDGE,"E400"),sQuery(id+"F0.wireOp",EDGE,"E401"),sQuery(id+"F0.wireOp",EDGE,"E402"),sQuery(id+"F0.wireOp",EDGE,"E403"),sQuery(id+"F0.wireOp",EDGE,"E404"),sQuery(id+"F0.wireOp",EDGE,"E405"),sQuery(id+"F0.wireOp",EDGE,"E406"),sQuery(id+"F0.wireOp",EDGE,"E407"),sQuery(id+"F0.wireOp",EDGE,"E408"),sQuery(id+"F0.wireOp",EDGE,"E409"),sQuery(id+"F0.wireOp",EDGE,"E410"),sQuery(id+"F0.wireOp",EDGE,"E411"),sQuery(id+"F0.wireOp",EDGE,"E412"),sQuery(id+"F0.wireOp",EDGE,"E413"),sQuery(id+"F0.wireOp",EDGE,"E414"),sQuery(id+"F0.wireOp",EDGE,"E415"),sQuery(id+"F0.wireOp",EDGE,"E416"),sQuery(id+"F0.wireOp",EDGE,"E417"),sQuery(id+"F0.wireOp",EDGE,"E418"),sQuery(id+"F0.wireOp",EDGE,"E419"),sQuery(id+"F0.wireOp",EDGE,"E420"),sQuery(id+"F0.wireOp",EDGE,"E421"),sQuery(id+"F0.wireOp",EDGE,"E422"),sQuery(id+"F0.wireOp",EDGE,"E423"),sQuery(id+"F0.wireOp",EDGE,"E424"),sQuery(id+"F0.wireOp",EDGE,"E425"),sQuery(id+"F0.wireOp",EDGE,"E426"),sQuery(id+"F0.wireOp",EDGE,"E427"),sQuery(id+"F0.wireOp",EDGE,"E428"),sQuery(id+"F0.wireOp",EDGE,"E429"),sQuery(id+"F0.wireOp",EDGE,"E430"),sQuery(id+"F0.wireOp",EDGE,"E431"),sQuery(id+"F0.wireOp",EDGE,"E432"),sQuery(id+"F0.wireOp",EDGE,"E433"),sQuery(id+"F0.wireOp",EDGE,"E434"),sQuery(id+"F0.wireOp",EDGE,"E435"),sQuery(id+"F0.wireOp",EDGE,"E436"),sQuery(id+"F0.wireOp",EDGE,"E437"),sQuery(id+"F0.wireOp",EDGE,"E438"),sQuery(id+"F0.wireOp",EDGE,"E439"),sQuery(id+"F0.wireOp",EDGE,"E440"),sQuery(id+"F0.wireOp",EDGE,"E441"),sQuery(id+"F0.wireOp",EDGE,"E442"),sQuery(id+"F0.wireOp",EDGE,"E443"),sQuery(id+"F0.wireOp",EDGE,"E444"),sQuery(id+"F0.wireOp",EDGE,"E445"),sQuery(id+"F0.wireOp",EDGE,"E446"),sQuery(id+"F0.wireOp",EDGE,"E447"),sQuery(id+"F0.wireOp",EDGE,"E448"),sQuery(id+"F0.wireOp",EDGE,"E449"),sQuery(id+"F0.wireOp",EDGE,"E450"),sQuery(id+"F0.wireOp",EDGE,"E451"),sQuery(id+"F0.wireOp",EDGE,"E452"),sQuery(id+"F0.wireOp",EDGE,"E453"),sQuery(id+"F0.wireOp",EDGE,"E454"),sQuery(id+"F0.wireOp",EDGE,"E455"),sQuery(id+"F0.wireOp",EDGE,"E456"),sQuery(id+"F0.wireOp",EDGE,"E457"),sQuery(id+"F0.wireOp",EDGE,"E458"),sQuery(id+"F0.wireOp",EDGE,"E459"),sQuery(id+"F0.wireOp",EDGE,"E460"),sQuery(id+"F0.wireOp",EDGE,"E461"),sQuery(id+"F0.wireOp",EDGE,"E462"),sQuery(id+"F0.wireOp",EDGE,"E463"),sQuery(id+"F0.wireOp",EDGE,"E464"),sQuery(id+"F0.wireOp",EDGE,"E465"),sQuery(id+"F0.wireOp",EDGE,"E466"),sQuery(id+"F0.wireOp",EDGE,"E467"),sQuery(id+"F0.wireOp",EDGE,"E468"),sQuery(id+"F0.wireOp",EDGE,"E469"),sQuery(id+"F0.wireOp",EDGE,"E470"),sQuery(id+"F0.wireOp",EDGE,"E471"),sQuery(id+"F0.wireOp",EDGE,"E472"),sQuery(id+"F0.wireOp",EDGE,"E473"),sQuery(id+"F0.wireOp",EDGE,"E474"),sQuery(id+"F0.wireOp",EDGE,"E475"),sQuery(id+"F0.wireOp",EDGE,"E476"),sQuery(id+"F0.wireOp",EDGE,"E477"),sQuery(id+"F0.wireOp",EDGE,"E478"),sQuery(id+"F0.wireOp",EDGE,"E479"),sQuery(id+"F0.wireOp",EDGE,"E480"),sQuery(id+"F0.wireOp",EDGE,"E481"),sQuery(id+"F0.wireOp",EDGE,"E482"),sQuery(id+"F0.wireOp",EDGE,"E483"),sQuery(id+"F0.wireOp",EDGE,"E484"),sQuery(id+"F0.wireOp",EDGE,"E485"),sQuery(id+"F0.wireOp",EDGE,"E486"),sQuery(id+"F0.wireOp",EDGE,"E487"),sQuery(id+"F0.wireOp",EDGE,"E488"),sQuery(id+"F0.wireOp",EDGE,"E489"),sQuery(id+"F0.wireOp",EDGE,"E490"),sQuery(id+"F0.wireOp",EDGE,"E491"),sQuery(id+"F0.wireOp",EDGE,"E492"),sQuery(id+"F0.wireOp",EDGE,"E493"),sQuery(id+"F0.wireOp",EDGE,"E494"),sQuery(id+"F0.wireOp",EDGE,"E495"),sQuery(id+"F0.wireOp",EDGE,"E496"),sQuery(id+"F0.wireOp",EDGE,"E497"),sQuery(id+"F0.wireOp",EDGE,"E498"),sQuery(id+"F0.wireOp",EDGE,"E499"),sQuery(id+"F0.wireOp",EDGE,"E500"),sQuery(id+"F0.wireOp",EDGE,"E501"),sQuery(id+"F0.wireOp",EDGE,"E502"),sQuery(id+"F0.wireOp",EDGE,"E503"),sQuery(id+"F0.wireOp",EDGE,"E504"),sQuery(id+"F0.wireOp",EDGE,"E505"),sQuery(id+"F0.wireOp",EDGE,"E506"),sQuery(id+"F0.wireOp",EDGE,"E507"),sQuery(id+"F0.wireOp",EDGE,"E508"),sQuery(id+"F0.wireOp",EDGE,"E509"),sQuery(id+"F0.wireOp",EDGE,"E510"),sQuery(id+"F0.wireOp",EDGE,"E511"),sQuery(id+"F0.wireOp",EDGE,"E512"),sQuery(id+"F0.wireOp",EDGE,"E513"),sQuery(id+"F0.wireOp",EDGE,"E514"),sQuery(id+"F0.wireOp",EDGE,"E515"),sQuery(id+"F0.wireOp",EDGE,"E516"),sQuery(id+"F0.wireOp",EDGE,"E517"),sQuery(id+"F0.wireOp",EDGE,"E518"),sQuery(id+"F0.wireOp",EDGE,"E519"),sQuery(id+"F0.wireOp",EDGE,"E520"),sQuery(id+"F0.wireOp",EDGE,"E521"),sQuery(id+"F0.wireOp",EDGE,"E522"),sQuery(id+"F0.wireOp",EDGE,"E523"),sQuery(id+"F0.wireOp",EDGE,"E524"),sQuery(id+"F0.wireOp",EDGE,"E525"),sQuery(id+"F0.wireOp",EDGE,"E526"),sQuery(id+"F0.wireOp",EDGE,"E527"),sQuery(id+"F0.wireOp",EDGE,"E528"),sQuery(id+"F0.wireOp",EDGE,"E529"),sQuery(id+"F0.wireOp",EDGE,"E530"),sQuery(id+"F0.wireOp",EDGE,"E531"),sQuery(id+"F0.wireOp",EDGE,"E532"),sQuery(id+"F0.wireOp",EDGE,"E533"),sQuery(id+"F0.wireOp",EDGE,"E534"),sQuery(id+"F0.wireOp",EDGE,"E535"),sQuery(id+"F0.wireOp",EDGE,"E536"),sQuery(id+"F0.wireOp",EDGE,"E537"),sQuery(id+"F0.wireOp",EDGE,"E538"),sQuery(id+"F0.wireOp",EDGE,"E539"),sQuery(id+"F0.wireOp",EDGE,"E540"),sQuery(id+"F0.wireOp",EDGE,"E541"),sQuery(id+"F0.wireOp",EDGE,"E542"),sQuery(id+"F0.wireOp",EDGE,"E543"),sQuery(id+"F0.wireOp",EDGE,"E544"),sQuery(id+"F0.wireOp",EDGE,"E545"),sQuery(id+"F0.wireOp",EDGE,"E546"),sQuery(id+"F0.wireOp",EDGE,"E547"),sQuery(id+"F0.wireOp",EDGE,"E548"),sQuery(id+"F0.wireOp",EDGE,"E549"),sQuery(id+"F0.wireOp",EDGE,"E550"),sQuery(id+"F0.wireOp",EDGE,"E551"),sQuery(id+"F0.wireOp",EDGE,"E552"),sQuery(id+"F0.wireOp",EDGE,"E553"),sQuery(id+"F0.wireOp",EDGE,"E554"),sQuery(id+"F0.wireOp",EDGE,"E555"),sQuery(id+"F0.wireOp",EDGE,"E556"),sQuery(id+"F0.wireOp",EDGE,"E557"),sQuery(id+"F0.wireOp",EDGE,"E558"),sQuery(id+"F0.wireOp",EDGE,"E559"),sQuery(id+"F0.wireOp",EDGE,"E560"),sQuery(id+"F0.wireOp",EDGE,"E561"),sQuery(id+"F0.wireOp",EDGE,"E562"),sQuery(id+"F0.wireOp",EDGE,"E563"),sQuery(id+"F0.wireOp",EDGE,"E564"),sQuery(id+"F0.wireOp",EDGE,"E565"),sQuery(id+"F0.wireOp",EDGE,"E566"),sQuery(id+"F0.wireOp",EDGE,"E567"),sQuery(id+"F0.wireOp",EDGE,"E568"),sQuery(id+"F0.wireOp",EDGE,"E569"),sQuery(id+"F0.wireOp",EDGE,"E570"),sQuery(id+"F0.wireOp",EDGE,"E571"),sQuery(id+"F0.wireOp",EDGE,"E572"),sQuery(id+"F0.wireOp",EDGE,"E573"),sQuery(id+"F0.wireOp",EDGE,"E574"),sQuery(id+"F0.wireOp",EDGE,"E575"),sQuery(id+"F0.wireOp",EDGE,"E576"),sQuery(id+"F0.wireOp",EDGE,"E577"),sQuery(id+"F0.wireOp",EDGE,"E578"),sQuery(id+"F0.wireOp",EDGE,"E579"),sQuery(id+"F0.wireOp",EDGE,"E580"),sQuery(id+"F0.wireOp",EDGE,"E581"),sQuery(id+"F0.wireOp",EDGE,"E582"),sQuery(id+"F0.wireOp",EDGE,"E583"),sQuery(id+"F0.wireOp",EDGE,"E584"),sQuery(id+"F0.wireOp",EDGE,"E585"),sQuery(id+"F0.wireOp",EDGE,"E586"),sQuery(id+"F0.wireOp",EDGE,"E587"),sQuery(id+"F0.wireOp",EDGE,"E588"),sQuery(id+"F0.wireOp",EDGE,"E589"),sQuery(id+"F0.wireOp",EDGE,"E590"),sQuery(id+"F0.wireOp",EDGE,"E591"),sQuery(id+"F0.wireOp",EDGE,"E592"),sQuery(id+"F0.wireOp",EDGE,"E593"),sQuery(id+"F0.wireOp",EDGE,"E594"),sQuery(id+"F0.wireOp",EDGE,"E595"),sQuery(id+"F0.wireOp",EDGE,"E596"),sQuery(id+"F0.wireOp",EDGE,"E597"),sQuery(id+"F0.wireOp",EDGE,"E598"),sQuery(id+"F0.wireOp",EDGE,"E599"),sQuery(id+"F0.wireOp",EDGE,"E600"),sQuery(id+"F0.wireOp",EDGE,"E601"),sQuery(id+"F0.wireOp",EDGE,"E602"),sQuery(id+"F0.wireOp",EDGE,"E603"),sQuery(id+"F0.wireOp",EDGE,"E604"),sQuery(id+"F0.wireOp",EDGE,"E605"),sQuery(id+"F0.wireOp",EDGE,"E606"),sQuery(id+"F0.wireOp",EDGE,"E607"),sQuery(id+"F0.wireOp",EDGE,"E608"),sQuery(id+"F0.wireOp",EDGE,"E609"),sQuery(id+"F0.wireOp",EDGE,"E610"),sQuery(id+"F0.wireOp",EDGE,"E611"),sQuery(id+"F0.wireOp",EDGE,"E612"),sQuery(id+"F0.wireOp",EDGE,"E613"),sQuery(id+"F0.wireOp",EDGE,"E614"),sQuery(id+"F0.wireOp",EDGE,"E615"),sQuery(id+"F0.wireOp",EDGE,"E616"),sQuery(id+"F0.wireOp",EDGE,"E617"),sQuery(id+"F0.wireOp",EDGE,"E618"),sQuery(id+"F0.wireOp",EDGE,"E619"),sQuery(id+"F0.wireOp",EDGE,"E620"),sQuery(id+"F0.wireOp",EDGE,"E621"),sQuery(id+"F0.wireOp",EDGE,"E622"),sQuery(id+"F0.wireOp",EDGE,"E623"),sQuery(id+"F0.wireOp",EDGE,"E624"),sQuery(id+"F0.wireOp",EDGE,"E625"),sQuery(id+"F0.wireOp",EDGE,"E626"),sQuery(id+"F0.wireOp",EDGE,"E627"),sQuery(id+"F0.wireOp",EDGE,"E628"),sQuery(id+"F0.wireOp",EDGE,"E629"),sQuery(id+"F0.wireOp",EDGE,"E630"),sQuery(id+"F0.wireOp",EDGE,"E631"),sQuery(id+"F0.wireOp",EDGE,"E632"),sQuery(id+"F0.wireOp",EDGE,"E633"),sQuery(id+"F0.wireOp",EDGE,"E634"),sQuery(id+"F0.wireOp",EDGE,"E635"),sQuery(id+"F0.wireOp",EDGE,"E636"),sQuery(id+"F0.wireOp",EDGE,"E637"),sQuery(id+"F0.wireOp",EDGE,"E638"),sQuery(id+"F0.wireOp",EDGE,"E639"),sQuery(id+"F0.wireOp",EDGE,"E640"),sQuery(id+"F0.wireOp",EDGE,"E641"),sQuery(id+"F0.wireOp",EDGE,"E642"),sQuery(id+"F0.wireOp",EDGE,"E643"),sQuery(id+"F0.wireOp",EDGE,"E644"),sQuery(id+"F0.wireOp",EDGE,"E645"),sQuery(id+"F0.wireOp",EDGE,"E646"),sQuery(id+"F0.wireOp",EDGE,"E647"),sQuery(id+"F0.wireOp",EDGE,"E648"),sQuery(id+"F0.wireOp",EDGE,"E649"),sQuery(id+"F0.wireOp",EDGE,"E650"),sQuery(id+"F0.wireOp",EDGE,"E651"),sQuery(id+"F0.wireOp",EDGE,"E652"),sQuery(id+"F0.wireOp",EDGE,"E653"),sQuery(id+"F0.wireOp",EDGE,"E654"),sQuery(id+"F0.wireOp",EDGE,"E655"),sQuery(id+"F0.wireOp",EDGE,"E656"),sQuery(id+"F0.wireOp",EDGE,"E657"),sQuery(id+"F0.wireOp",EDGE,"E658"),sQuery(id+"F0.wireOp",EDGE,"E659"),sQuery(id+"F0.wireOp",EDGE,"E660"),sQuery(id+"F0.wireOp",EDGE,"E661"),sQuery(id+"F0.wireOp",EDGE,"E662"),sQuery(id+"F0.wireOp",EDGE,"E663"),sQuery(id+"F0.wireOp",EDGE,"E664"),sQuery(id+"F0.wireOp",EDGE,"E665"),sQuery(id+"F0.wireOp",EDGE,"E666"),sQuery(id+"F0.wireOp",EDGE,"E667"),sQuery(id+"F0.wireOp",EDGE,"E668"),sQuery(id+"F0.wireOp",EDGE,"E669"),sQuery(id+"F0.wireOp",EDGE,"E670"),sQuery(id+"F0.wireOp",EDGE,"E671"),sQuery(id+"F0.wireOp",EDGE,"E672"),sQuery(id+"F0.wireOp",EDGE,"E673"),sQuery(id+"F0.wireOp",EDGE,"E674"),sQuery(id+"F0.wireOp",EDGE,"E675"),sQuery(id+"F0.wireOp",EDGE,"E676"),sQuery(id+"F0.wireOp",EDGE,"E677"),sQuery(id+"F0.wireOp",EDGE,"E678"),sQuery(id+"F0.wireOp",EDGE,"E679"),sQuery(id+"F0.wireOp",EDGE,"E680"),sQuery(id+"F0.wireOp",EDGE,"E681"),sQuery(id+"F0.wireOp",EDGE,"E682"),sQuery(id+"F0.wireOp",EDGE,"E683"),sQuery(id+"F0.wireOp",EDGE,"E684"),sQuery(id+"F0.wireOp",EDGE,"E685"),sQuery(id+"F0.wireOp",EDGE,"E686"),sQuery(id+"F0.wireOp",EDGE,"E687"),sQuery(id+"F0.wireOp",EDGE,"E688"),sQuery(id+"F0.wireOp",EDGE,"E689"),sQuery(id+"F0.wireOp",EDGE,"E690"),sQuery(id+"F0.wireOp",EDGE,"E691"),sQuery(id+"F0.wireOp",EDGE,"E692"),sQuery(id+"F0.wireOp",EDGE,"E693"),sQuery(id+"F0.wireOp",EDGE,"E694"),sQuery(id+"F0.wireOp",EDGE,"E695"),sQuery(id+"F0.wireOp",EDGE,"E696"),sQuery(id+"F0.wireOp",EDGE,"E697"),sQuery(id+"F0.wireOp",EDGE,"E698"),sQuery(id+"F0.wireOp",EDGE,"E699"),sQuery(id+"F0.wireOp",EDGE,"E700"),sQuery(id+"F0.wireOp",EDGE,"E701"),sQuery(id+"F0.wireOp",EDGE,"E702"),sQuery(id+"F0.wireOp",EDGE,"E703"),sQuery(id+"F0.wireOp",EDGE,"E704"),sQuery(id+"F0.wireOp",EDGE,"E705"),sQuery(id+"F0.wireOp",EDGE,"E706"),sQuery(id+"F0.wireOp",EDGE,"E707"),sQuery(id+"F0.wireOp",EDGE,"E708"),sQuery(id+"F0.wireOp",EDGE,"E709"),sQuery(id+"F0.wireOp",EDGE,"E710"),sQuery(id+"F0.wireOp",EDGE,"E711"),sQuery(id+"F0.wireOp",EDGE,"E712"),sQuery(id+"F0.wireOp",EDGE,"E713"),sQuery(id+"F0.wireOp",EDGE,"E714"),sQuery(id+"F0.wireOp",EDGE,"E715"),sQuery(id+"F0.wireOp",EDGE,"E716"),sQuery(id+"F0.wireOp",EDGE,"E717"),sQuery(id+"F0.wireOp",EDGE,"E718"),sQuery(id+"F0.wireOp",EDGE,"E719"),sQuery(id+"F0.wireOp",EDGE,"E720"),sQuery(id+"F0.wireOp",EDGE,"E721"),sQuery(id+"F0.wireOp",EDGE,"E722"),sQuery(id+"F0.wireOp",EDGE,"E723"),sQuery(id+"F0.wireOp",EDGE,"E724"),sQuery(id+"F0.wireOp",EDGE,"E725"),sQuery(id+"F0.wireOp",EDGE,"E726"),sQuery(id+"F0.wireOp",EDGE,"E727"),sQuery(id+"F0.wireOp",EDGE,"E728"),sQuery(id+"F0.wireOp",EDGE,"E729"),sQuery(id+"F0.wireOp",EDGE,"E730"),sQuery(id+"F0.wireOp",EDGE,"E731"),sQuery(id+"F0.wireOp",EDGE,"E732"),sQuery(id+"F0.wireOp",EDGE,"E733"),sQuery(id+"F0.wireOp",EDGE,"E734"),sQuery(id+"F0.wireOp",EDGE,"E735"),sQuery(id+"F0.wireOp",EDGE,"E736"),sQuery(id+"F0.wireOp",EDGE,"E737"),sQuery(id+"F0.wireOp",EDGE,"E738"),sQuery(id+"F0.wireOp",EDGE,"E739"),sQuery(id+"F0.wireOp",EDGE,"E740"),sQuery(id+"F0.wireOp",EDGE,"E741"),sQuery(id+"F0.wireOp",EDGE,"E742"),sQuery(id+"F0.wireOp",EDGE,"E743"),sQuery(id+"F0.wireOp",EDGE,"E744"),sQuery(id+"F0.wireOp",EDGE,"E745"),sQuery(id+"F0.wireOp",EDGE,"E746"),sQuery(id+"F0.wireOp",EDGE,"E747"),sQuery(id+"F0.wireOp",EDGE,"E748"),sQuery(id+"F0.wireOp",EDGE,"E749"),sQuery(id+"F0.wireOp",EDGE,"E750"),sQuery(id+"F0.wireOp",EDGE,"E751"),sQuery(id+"F0.wireOp",EDGE,"E752"),sQuery(id+"F0.wireOp",EDGE,"E753"),sQuery(id+"F0.wireOp",EDGE,"E754"),sQuery(id+"F0.wireOp",EDGE,"E755"),sQuery(id+"F0.wireOp",EDGE,"E756"),sQuery(id+"F0.wireOp",EDGE,"E757"),sQuery(id+"F0.wireOp",EDGE,"E758"),sQuery(id+"F0.wireOp",EDGE,"E759"),sQuery(id+"F0.wireOp",EDGE,"E760"),sQuery(id+"F0.wireOp",EDGE,"E761"),sQuery(id+"F0.wireOp",EDGE,"E762"),sQuery(id+"F0.wireOp",EDGE,"E763"),sQuery(id+"F0.wireOp",EDGE,"E764"),sQuery(id+"F0.wireOp",EDGE,"E765"),sQuery(id+"F0.wireOp",EDGE,"E766"),sQuery(id+"F0.wireOp",EDGE,"E767"),sQuery(id+"F0.wireOp",EDGE,"E768"),sQuery(id+"F0.wireOp",EDGE,"E769"),sQuery(id+"F0.wireOp",EDGE,"E770"),sQuery(id+"F0.wireOp",EDGE,"E771"),sQuery(id+"F0.wireOp",EDGE,"E772"),sQuery(id+"F0.wireOp",EDGE,"E773"),sQuery(id+"F0.wireOp",EDGE,"E774"),sQuery(id+"F0.wireOp",EDGE,"E775"),sQuery(id+"F0.wireOp",EDGE,"E776"),sQuery(id+"F0.wireOp",EDGE,"E777"),sQuery(id+"F0.wireOp",EDGE,"E778"),sQuery(id+"F0.wireOp",EDGE,"E779"),sQuery(id+"F0.wireOp",EDGE,"E780"),sQuery(id+"F0.wireOp",EDGE,"E781"),sQuery(id+"F0.wireOp",EDGE,"E782"),sQuery(id+"F0.wireOp",EDGE,"E783"),sQuery(id+"F0.wireOp",EDGE,"E784"),sQuery(id+"F0.wireOp",EDGE,"E785"),sQuery(id+"F0.wireOp",EDGE,"E786"),sQuery(id+"F0.wireOp",EDGE,"E787"),sQuery(id+"F0.wireOp",EDGE,"E788"),sQuery(id+"F0.wireOp",EDGE,"E789"),sQuery(id+"F0.wireOp",EDGE,"E790"),sQuery(id+"F0.wireOp",EDGE,"E791"),sQuery(id+"F0.wireOp",EDGE,"E792"),sQuery(id+"F0.wireOp",EDGE,"E793"),sQuery(id+"F0.wireOp",EDGE,"E794"),sQuery(id+"F0.wireOp",EDGE,"E795"),sQuery(id+"F0.wireOp",EDGE,"E796"),sQuery(id+"F0.wireOp",EDGE,"E797"),sQuery(id+"F0.wireOp",EDGE,"E798"),sQuery(id+"F0.wireOp",EDGE,"E799"),sQuery(id+"F0.wireOp",EDGE,"E800"),sQuery(id+"F0.wireOp",EDGE,"E801"),sQuery(id+"F0.wireOp",EDGE,"E802"),sQuery(id+"F0.wireOp",EDGE,"E803"),sQuery(id+"F0.wireOp",EDGE,"E804"),sQuery(id+"F0.wireOp",EDGE,"E805"),sQuery(id+"F0.wireOp",EDGE,"E806"),sQuery(id+"F0.wireOp",EDGE,"E807"),sQuery(id+"F0.wireOp",EDGE,"E808"),sQuery(id+"F0.wireOp",EDGE,"E809"),sQuery(id+"F0.wireOp",EDGE,"E810"),sQuery(id+"F0.wireOp",EDGE,"E811"),sQuery(id+"F0.wireOp",EDGE,"E812"),sQuery(id+"F0.wireOp",EDGE,"E813"),sQuery(id+"F0.wireOp",EDGE,"E814"),sQuery(id+"F0.wireOp",EDGE,"E815"),sQuery(id+"F0.wireOp",EDGE,"E816"),sQuery(id+"F0.wireOp",EDGE,"E817"),sQuery(id+"F0.wireOp",EDGE,"E818"),sQuery(id+"F0.wireOp",EDGE,"E819"),sQuery(id+"F0.wireOp",EDGE,"E820"),sQuery(id+"F0.wireOp",EDGE,"E821"),sQuery(id+"F0.wireOp",EDGE,"E822"),sQuery(id+"F0.wireOp",EDGE,"E823"),sQuery(id+"F0.wireOp",EDGE,"E824"),sQuery(id+"F0.wireOp",EDGE,"E825"),sQuery(id+"F0.wireOp",EDGE,"E826"),sQuery(id+"F0.wireOp",EDGE,"E827"),sQuery(id+"F0.wireOp",EDGE,"E828"),sQuery(id+"F0.wireOp",EDGE,"E829"),sQuery(id+"F0.wireOp",EDGE,"E830"),sQuery(id+"F0.wireOp",EDGE,"E831"),sQuery(id+"F0.wireOp",EDGE,"E832"),sQuery(id+"F0.wireOp",EDGE,"E833"),sQuery(id+"F0.wireOp",EDGE,"E834"),sQuery(id+"F0.wireOp",EDGE,"E835"),sQuery(id+"F0.wireOp",EDGE,"E836"),sQuery(id+"F0.wireOp",EDGE,"E837"),sQuery(id+"F0.wireOp",EDGE,"E838"),sQuery(id+"F0.wireOp",EDGE,"E839"),sQuery(id+"F0.wireOp",EDGE,"E840"),sQuery(id+"F0.wireOp",EDGE,"E841"),sQuery(id+"F0.wireOp",EDGE,"E842"),sQuery(id+"F0.wireOp",EDGE,"E843"),sQuery(id+"F0.wireOp",EDGE,"E844"),sQuery(id+"F0.wireOp",EDGE,"E845"),sQuery(id+"F0.wireOp",EDGE,"E846"),sQuery(id+"F0.wireOp",EDGE,"E847"),sQuery(id+"F0.wireOp",EDGE,"E848"),sQuery(id+"F0.wireOp",EDGE,"E849"),sQuery(id+"F0.wireOp",EDGE,"E850"),sQuery(id+"F0.wireOp",EDGE,"E851"),sQuery(id+"F0.wireOp",EDGE,"E852"),sQuery(id+"F0.wireOp",EDGE,"E853"),sQuery(id+"F0.wireOp",EDGE,"E854"),sQuery(id+"F0.wireOp",EDGE,"E855"),sQuery(id+"F0.wireOp",EDGE,"E856"),sQuery(id+"F0.wireOp",EDGE,"E857"),sQuery(id+"F0.wireOp",EDGE,"E858"),sQuery(id+"F0.wireOp",EDGE,"E859"),sQuery(id+"F0.wireOp",EDGE,"E860"),sQuery(id+"F0.wireOp",EDGE,"E861"),sQuery(id+"F0.wireOp",EDGE,"E862"),sQuery(id+"F0.wireOp",EDGE,"E863"),sQuery(id+"F0.wireOp",EDGE,"E864"),sQuery(id+"F0.wireOp",EDGE,"E865"),sQuery(id+"F0.wireOp",EDGE,"E866"),sQuery(id+"F0.wireOp",EDGE,"E867"),sQuery(id+"F0.wireOp",EDGE,"E868"),sQuery(id+"F0.wireOp",EDGE,"E869"),sQuery(id+"F0.wireOp",EDGE,"E870"),sQuery(id+"F0.wireOp",EDGE,"E871"),sQuery(id+"F0.wireOp",EDGE,"E872"),sQuery(id+"F0.wireOp",EDGE,"E873"),sQuery(id+"F0.wireOp",EDGE,"E874"),sQuery(id+"F0.wireOp",EDGE,"E875"),sQuery(id+"F0.wireOp",EDGE,"E876"),sQuery(id+"F0.wireOp",EDGE,"E877"),sQuery(id+"F0.wireOp",EDGE,"E878"),sQuery(id+"F0.wireOp",EDGE,"E879"),sQuery(id+"F0.wireOp",EDGE,"E880"),sQuery(id+"F0.wireOp",EDGE,"E881"),sQuery(id+"F0.wireOp",EDGE,"E882"),sQuery(id+"F0.wireOp",EDGE,"E883"),sQuery(id+"F0.wireOp",EDGE,"E884"),sQuery(id+"F0.wireOp",EDGE,"E885"),sQuery(id+"F0.wireOp",EDGE,"E886"),sQuery(id+"F0.wireOp",EDGE,"E887"),sQuery(id+"F0.wireOp",EDGE,"E888"),sQuery(id+"F0.wireOp",EDGE,"E889"),sQuery(id+"F0.wireOp",EDGE,"E890"),sQuery(id+"F0.wireOp",EDGE,"E891"),sQuery(id+"F0.wireOp",EDGE,"E892"),sQuery(id+"F0.wireOp",EDGE,"E893"),sQuery(id+"F0.wireOp",EDGE,"E894"),sQuery(id+"F0.wireOp",EDGE,"E895"),sQuery(id+"F0.wireOp",EDGE,"E896"),sQuery(id+"F0.wireOp",EDGE,"E897"),sQuery(id+"F0.wireOp",EDGE,"E898"),sQuery(id+"F0.wireOp",EDGE,"E899"),sQuery(id+"F0.wireOp",EDGE,"E900"),sQuery(id+"F0.wireOp",EDGE,"E901"),sQuery(id+"F0.wireOp",EDGE,"E902"),sQuery(id+"F0.wireOp",EDGE,"E903"),sQuery(id+"F0.wireOp",EDGE,"E904"),sQuery(id+"F0.wireOp",EDGE,"E905"),sQuery(id+"F0.wireOp",EDGE,"E906"),sQuery(id+"F0.wireOp",EDGE,"E907"),sQuery(id+"F0.wireOp",EDGE,"E908"),sQuery(id+"F0.wireOp",EDGE,"E909"),sQuery(id+"F0.wireOp",EDGE,"E910"),sQuery(id+"F0.wireOp",EDGE,"E911"),sQuery(id+"F0.wireOp",EDGE,"E912"),sQuery(id+"F0.wireOp",EDGE,"E913"),sQuery(id+"F0.wireOp",EDGE,"E914"),sQuery(id+"F0.wireOp",EDGE,"E915"),sQuery(id+"F0.wireOp",EDGE,"E916"),sQuery(id+"F0.wireOp",EDGE,"E917"),sQuery(id+"F0.wireOp",EDGE,"E918"),sQuery(id+"F0.wireOp",EDGE,"E919"),sQuery(id+"F0.wireOp",EDGE,"E920"),sQuery(id+"F0.wireOp",EDGE,"E921"),sQuery(id+"F0.wireOp",EDGE,"E922"),sQuery(id+"F0.wireOp",EDGE,"E923"),sQuery(id+"F0.wireOp",EDGE,"E924"),sQuery(id+"F0.wireOp",EDGE,"E925"),sQuery(id+"F0.wireOp",EDGE,"E926"),sQuery(id+"F0.wireOp",EDGE,"E927"),sQuery(id+"F0.wireOp",EDGE,"E928"),sQuery(id+"F0.wireOp",EDGE,"E929"),sQuery(id+"F0.wireOp",EDGE,"E930"),sQuery(id+"F0.wireOp",EDGE,"E931"),sQuery(id+"F0.wireOp",EDGE,"E932"),sQuery(id+"F0.wireOp",EDGE,"E933"),sQuery(id+"F0.wireOp",EDGE,"E934"),sQuery(id+"F0.wireOp",EDGE,"E935"),sQuery(id+"F0.wireOp",EDGE,"E936"),sQuery(id+"F0.wireOp",EDGE,"E937"),sQuery(id+"F0.wireOp",EDGE,"E938"),sQuery(id+"F0.wireOp",EDGE,"E939"),sQuery(id+"F0.wireOp",EDGE,"E940"),sQuery(id+"F0.wireOp",EDGE,"E941"),sQuery(id+"F0.wireOp",EDGE,"E942"),sQuery(id+"F0.wireOp",EDGE,"E943"),sQuery(id+"F0.wireOp",EDGE,"E944"),sQuery(id+"F0.wireOp",EDGE,"E945"),sQuery(id+"F0.wireOp",EDGE,"E946"),sQuery(id+"F0.wireOp",EDGE,"E947"),sQuery(id+"F0.wireOp",EDGE,"E948"),sQuery(id+"F0.wireOp",EDGE,"E949"),sQuery(id+"F0.wireOp",EDGE,"E950"),sQuery(id+"F0.wireOp",EDGE,"E951"),sQuery(id+"F0.wireOp",EDGE,"E952"),sQuery(id+"F0.wireOp",EDGE,"E953"),sQuery(id+"F0.wireOp",EDGE,"E954"),sQuery(id+"F0.wireOp",EDGE,"E955"),sQuery(id+"F0.wireOp",EDGE,"E956"),sQuery(id+"F0.wireOp",EDGE,"E957"),sQuery(id+"F0.wireOp",EDGE,"E958"),sQuery(id+"F0.wireOp",EDGE,"E959"),sQuery(id+"F0.wireOp",EDGE,"E960"),sQuery(id+"F0.wireOp",EDGE,"E961"),sQuery(id+"F0.wireOp",EDGE,"E962"),sQuery(id+"F0.wireOp",EDGE,"E963"),sQuery(id+"F0.wireOp",EDGE,"E964"),sQuery(id+"F0.wireOp",EDGE,"E965"),sQuery(id+"F0.wireOp",EDGE,"E966"),sQuery(id+"F0.wireOp",EDGE,"E967"),sQuery(id+"F0.wireOp",EDGE,"E968"),sQuery(id+"F0.wireOp",EDGE,"E969"),sQuery(id+"F0.wireOp",EDGE,"E970"),sQuery(id+"F0.wireOp",EDGE,"E971"),sQuery(id+"F0.wireOp",EDGE,"E972"),sQuery(id+"F0.wireOp",EDGE,"E973"),sQuery(id+"F0.wireOp",EDGE,"E974"),sQuery(id+"F0.wireOp",EDGE,"E975"),sQuery(id+"F0.wireOp",EDGE,"E976"),sQuery(id+"F0.wireOp",EDGE,"E977"),sQuery(id+"F0.wireOp",EDGE,"E978"),sQuery(id+"F0.wireOp",EDGE,"E979"),sQuery(id+"F0.wireOp",EDGE,"E980"),sQuery(id+"F0.wireOp",EDGE,"E981"),sQuery(id+"F0.wireOp",EDGE,"E982"),sQuery(id+"F0.wireOp",EDGE,"E983"),sQuery(id+"F0.wireOp",EDGE,"E984"),sQuery(id+"F0.wireOp",EDGE,"E985"),sQuery(id+"F0.wireOp",EDGE,"E986"),sQuery(id+"F0.wireOp",EDGE,"E987"),sQuery(id+"F0.wireOp",EDGE,"E988"),sQuery(id+"F0.wireOp",EDGE,"E989"),sQuery(id+"F0.wireOp",EDGE,"E990"),sQuery(id+"F0.wireOp",EDGE,"E991"),sQuery(id+"F0.wireOp",EDGE,"E992"),sQuery(id+"F0.wireOp",EDGE,"E993"),sQuery(id+"F0.wireOp",EDGE,"E994"),sQuery(id+"F0.wireOp",EDGE,"E995"),sQuery(id+"F0.wireOp",EDGE,"E996"),sQuery(id+"F0.wireOp",EDGE,"E997"),sQuery(id+"F0.wireOp",EDGE,"E998"),sQuery(id+"F0.wireOp",EDGE,"E999"),sQuery(id+"F0.wireOp",EDGE,"E1000"),sQuery(id+"F0.wireOp",EDGE,"E1001"),sQuery(id+"F0.wireOp",EDGE,"E1002"),sQuery(id+"F0.wireOp",EDGE,"E1003"),sQuery(id+"F0.wireOp",EDGE,"E1004"),sQuery(id+"F0.wireOp",EDGE,"E1005"),sQuery(id+"F0.wireOp",EDGE,"E1006"),sQuery(id+"F0.wireOp",EDGE,"E1007"),sQuery(id+"F0.wireOp",EDGE,"E1008"),sQuery(id+"F0.wireOp",EDGE,"E1009"),sQuery(id+"F0.wireOp",EDGE,"E1010"),sQuery(id+"F0.wireOp",EDGE,"E1011"),sQuery(id+"F0.wireOp",EDGE,"E1012"),sQuery(id+"F0.wireOp",EDGE,"E1013"),sQuery(id+"F0.wireOp",EDGE,"E1014"),sQuery(id+"F0.wireOp",EDGE,"E1015"),sQuery(id+"F0.wireOp",EDGE,"E1016"),sQuery(id+"F0.wireOp",EDGE,"E1017"),sQuery(id+"F0.wireOp",EDGE,"E1018"),sQuery(id+"F0.wireOp",EDGE,"E1019"),sQuery(id+"F0.wireOp",EDGE,"E1020"),sQuery(id+"F0.wireOp",EDGE,"E1021"),sQuery(id+"F0.wireOp",EDGE,"E1022"),sQuery(id+"F0.wireOp",EDGE,"E1023"),sQuery(id+"F0.wireOp",EDGE,"E1024"),sQuery(id+"F0.wireOp",EDGE,"E1025"),sQuery(id+"F0.wireOp",EDGE,"E1026"),sQuery(id+"F0.wireOp",EDGE,"E1027"),sQuery(id+"F0.wireOp",EDGE,"E1028"),sQuery(id+"F0.wireOp",EDGE,"E1029"),sQuery(id+"F0.wireOp",EDGE,"E1030"),sQuery(id+"F0.wireOp",EDGE,"E1031"),sQuery(id+"F0.wireOp",EDGE,"E1032"),sQuery(id+"F0.wireOp",EDGE,"E1033"),sQuery(id+"F0.wireOp",EDGE,"E1034"),sQuery(id+"F0.wireOp",EDGE,"E1035"),sQuery(id+"F0.wireOp",EDGE,"E1036"),sQuery(id+"F0.wireOp",EDGE,"E1037"),sQuery(id+"F0.wireOp",EDGE,"E1038"),sQuery(id+"F0.wireOp",EDGE,"E1039"),sQuery(id+"F0.wireOp",EDGE,"E1040"),sQuery(id+"F0.wireOp",EDGE,"E1041"),sQuery(id+"F0.wireOp",EDGE,"E1042"),sQuery(id+"F0.wireOp",EDGE,"E1043"),sQuery(id+"F0.wireOp",EDGE,"E1044"),sQuery(id+"F0.wireOp",EDGE,"E1045"),sQuery(id+"F0.wireOp",EDGE,"E1046"),sQuery(id+"F0.wireOp",EDGE,"E1047"),sQuery(id+"F0.wireOp",EDGE,"E1048"),sQuery(id+"F0.wireOp",EDGE,"E1049"),sQuery(id+"F0.wireOp",EDGE,"E1050"),sQuery(id+"F0.wireOp",EDGE,"E1051"),sQuery(id+"F0.wireOp",EDGE,"E1052"),sQuery(id+"F0.wireOp",EDGE,"E1053"),sQuery(id+"F0.wireOp",EDGE,"E1054"),sQuery(id+"F0.wireOp",EDGE,"E1055"),sQuery(id+"F0.wireOp",EDGE,"E1056"),sQuery(id+"F0.wireOp",EDGE,"E1057"),sQuery(id+"F0.wireOp",EDGE,"E1058"),sQuery(id+"F0.wireOp",EDGE,"E1059"),sQuery(id+"F0.wireOp",EDGE,"E1060"),sQuery(id+"F0.wireOp",EDGE,"E1061"),sQuery(id+"F0.wireOp",EDGE,"E1062"),sQuery(id+"F0.wireOp",EDGE,"E1063"),sQuery(id+"F0.wireOp",EDGE,"E1064"),sQuery(id+"F0.wireOp",EDGE,"E1065"),sQuery(id+"F0.wireOp",EDGE,"E1066"),sQuery(id+"F0.wireOp",EDGE,"E1067"),sQuery(id+"F0.wireOp",EDGE,"E1068"),sQuery(id+"F0.wireOp",EDGE,"E1069"),sQuery(id+"F0.wireOp",EDGE,"E1070"),sQuery(id+"F0.wireOp",EDGE,"E1071"),sQuery(id+"F0.wireOp",EDGE,"E1072"),sQuery(id+"F0.wireOp",EDGE,"E1073"),sQuery(id+"F0.wireOp",EDGE,"E1074"),sQuery(id+"F0.wireOp",EDGE,"E1075"),sQuery(id+"F0.wireOp",EDGE,"E1076"),sQuery(id+"F0.wireOp",EDGE,"E1077"),sQuery(id+"F0.wireOp",EDGE,"E1078"),sQuery(id+"F0.wireOp",EDGE,"E1079"),sQuery(id+"F0.wireOp",EDGE,"E1080"),sQuery(id+"F0.wireOp",EDGE,"E1081"),sQuery(id+"F0.wireOp",EDGE,"E1082"),sQuery(id+"F0.wireOp",EDGE,"E1083"),sQuery(id+"F0.wireOp",EDGE,"E1084"),sQuery(id+"F0.wireOp",EDGE,"E1085"),sQuery(id+"F0.wireOp",EDGE,"E1086"),sQuery(id+"F0.wireOp",EDGE,"E1087"),sQuery(id+"F0.wireOp",EDGE,"E1088"),sQuery(id+"F0.wireOp",EDGE,"E1089"),sQuery(id+"F0.wireOp",EDGE,"E1090"),sQuery(id+"F0.wireOp",EDGE,"E1091"),sQuery(id+"F0.wireOp",EDGE,"E1092"),sQuery(id+"F0.wireOp",EDGE,"E1093"),sQuery(id+"F0.wireOp",EDGE,"E1094"),sQuery(id+"F0.wireOp",EDGE,"E1095"),sQuery(id+"F0.wireOp",EDGE,"E1096"),sQuery(id+"F0.wireOp",EDGE,"E1097"),sQuery(id+"F0.wireOp",EDGE,"E1098"),sQuery(id+"F0.wireOp",EDGE,"E1099"),sQuery(id+"F0.wireOp",EDGE,"E1100"),sQuery(id+"F0.wireOp",EDGE,"E1101"),sQuery(id+"F0.wireOp",EDGE,"E1102"),sQuery(id+"F0.wireOp",EDGE,"E1103"),sQuery(id+"F0.wireOp",EDGE,"E1104"),sQuery(id+"F0.wireOp",EDGE,"E1105"),sQuery(id+"F0.wireOp",EDGE,"E1106"),sQuery(id+"F0.wireOp",EDGE,"E1107"),sQuery(id+"F0.wireOp",EDGE,"E1108"),sQuery(id+"F0.wireOp",EDGE,"E1109"),sQuery(id+"F0.wireOp",EDGE,"E1110"),sQuery(id+"F0.wireOp",EDGE,"E1111"),sQuery(id+"F0.wireOp",EDGE,"E1112"),sQuery(id+"F0.wireOp",EDGE,"E1113"),sQuery(id+"F0.wireOp",EDGE,"E1114"),sQuery(id+"F0.wireOp",EDGE,"E1115"),sQuery(id+"F0.wireOp",EDGE,"E1116"),sQuery(id+"F0.wireOp",EDGE,"E1117"),sQuery(id+"F0.wireOp",EDGE,"E1118"),sQuery(id+"F0.wireOp",EDGE,"E1119"),sQuery(id+"F0.wireOp",EDGE,"E1120"),sQuery(id+"F0.wireOp",EDGE,"E1121"),sQuery(id+"F0.wireOp",EDGE,"E1122"),sQuery(id+"F0.wireOp",EDGE,"E1123"),sQuery(id+"F0.wireOp",EDGE,"E1124"),sQuery(id+"F0.wireOp",EDGE,"E1125"),sQuery(id+"F0.wireOp",EDGE,"E1126"),sQuery(id+"F0.wireOp",EDGE,"E1127"),sQuery(id+"F0.wireOp",EDGE,"E1128"),sQuery(id+"F0.wireOp",EDGE,"E1129"),sQuery(id+"F0.wireOp",EDGE,"E1130"),sQuery(id+"F0.wireOp",EDGE,"E1131"),sQuery(id+"F0.wireOp",EDGE,"E1132"),sQuery(id+"F0.wireOp",EDGE,"E1133"),sQuery(id+"F0.wireOp",EDGE,"E1134"),sQuery(id+"F0.wireOp",EDGE,"E1135"),sQuery(id+"F0.wireOp",EDGE,"E1136"),sQuery(id+"F0.wireOp",EDGE,"E1137"),sQuery(id+"F0.wireOp",EDGE,"E1138"),sQuery(id+"F0.wireOp",EDGE,"E1139"),sQuery(id+"F0.wireOp",EDGE,"E1140"),sQuery(id+"F0.wireOp",EDGE,"E1141"),sQuery(id+"F0.wireOp",EDGE,"E1142"),sQuery(id+"F0.wireOp",EDGE,"E1143"),sQuery(id+"F0.wireOp",EDGE,"E1144"),sQuery(id+"F0.wireOp",EDGE,"E1145"),sQuery(id+"F0.wireOp",EDGE,"E1146"),sQuery(id+"F0.wireOp",EDGE,"E1147"),sQuery(id+"F0.wireOp",EDGE,"E1148"),sQuery(id+"F0.wireOp",EDGE,"E1149"),sQuery(id+"F0.wireOp",EDGE,"E1150"),sQuery(id+"F0.wireOp",EDGE,"E1151"),sQuery(id+"F0.wireOp",EDGE,"E1152"),sQuery(id+"F0.wireOp",EDGE,"E1153"),sQuery(id+"F0.wireOp",EDGE,"E1154"),sQuery(id+"F0.wireOp",EDGE,"E1155"),sQuery(id+"F0.wireOp",EDGE,"E1156"),sQuery(id+"F0.wireOp",EDGE,"E1157"),sQuery(id+"F0.wireOp",EDGE,"E1158"),sQuery(id+"F0.wireOp",EDGE,"E1159"),sQuery(id+"F0.wireOp",EDGE,"E1160"),sQuery(id+"F0.wireOp",EDGE,"E1161"),sQuery(id+"F0.wireOp",EDGE,"E1162"),sQuery(id+"F0.wireOp",EDGE,"E1163"),sQuery(id+"F0.wireOp",EDGE,"E1164"),sQuery(id+"F0.wireOp",EDGE,"E1165"),sQuery(id+"F0.wireOp",EDGE,"E1166"),sQuery(id+"F0.wireOp",EDGE,"E1167"),sQuery(id+"F0.wireOp",EDGE,"E1168"),sQuery(id+"F0.wireOp",EDGE,"E1169"),sQuery(id+"F0.wireOp",EDGE,"E1170"),sQuery(id+"F0.wireOp",EDGE,"E1171"),sQuery(id+"F0.wireOp",EDGE,"E1172"),sQuery(id+"F0.wireOp",EDGE,"E1173"),sQuery(id+"F0.wireOp",EDGE,"E1174"),sQuery(id+"F0.wireOp",EDGE,"E1175"),sQuery(id+"F0.wireOp",EDGE,"E1176"),sQuery(id+"F0.wireOp",EDGE,"E1177"),sQuery(id+"F0.wireOp",EDGE,"E1178"),sQuery(id+"F0.wireOp",EDGE,"E1179"),sQuery(id+"F0.wireOp",EDGE,"E1180"),sQuery(id+"F0.wireOp",EDGE,"E1181"),sQuery(id+"F0.wireOp",EDGE,"E1182"),sQuery(id+"F0.wireOp",EDGE,"E1183"),sQuery(id+"F0.wireOp",EDGE,"E1184"),sQuery(id+"F0.wireOp",EDGE,"E1185"),sQuery(id+"F0.wireOp",EDGE,"E1186"),sQuery(id+"F0.wireOp",EDGE,"E1187"),sQuery(id+"F0.wireOp",EDGE,"E1188"),sQuery(id+"F0.wireOp",EDGE,"E1189"),sQuery(id+"F0.wireOp",EDGE,"E1190"),sQuery(id+"F0.wireOp",EDGE,"E1191"),sQuery(id+"F0.wireOp",EDGE,"E1192"),sQuery(id+"F0.wireOp",EDGE,"E1193"),sQuery(id+"F0.wireOp",EDGE,"E1194"),sQuery(id+"F0.wireOp",EDGE,"E1195"),sQuery(id+"F0.wireOp",EDGE,"E1196"),sQuery(id+"F0.wireOp",EDGE,"E1197"),sQuery(id+"F0.wireOp",EDGE,"E1198"),sQuery(id+"F0.wireOp",EDGE,"E1199"),sQuery(id+"F0.wireOp",EDGE,"E1200"),sQuery(id+"F0.wireOp",EDGE,"E1201"),sQuery(id+"F0.wireOp",EDGE,"E1202"),sQuery(id+"F0.wireOp",EDGE,"E1203"),sQuery(id+"F0.wireOp",EDGE,"E1204"),sQuery(id+"F0.wireOp",EDGE,"E1205"),sQuery(id+"F0.wireOp",EDGE,"E1206"),sQuery(id+"F0.wireOp",EDGE,"E1207"),sQuery(id+"F0.wireOp",EDGE,"E1208"),sQuery(id+"F0.wireOp",EDGE,"E1209"),sQuery(id+"F0.wireOp",EDGE,"E1210"),sQuery(id+"F0.wireOp",EDGE,"E1211"),sQuery(id+"F0.wireOp",EDGE,"E1212"),sQuery(id+"F0.wireOp",EDGE,"E1213"),sQuery(id+"F0.wireOp",EDGE,"E1214"),sQuery(id+"F0.wireOp",EDGE,"E1215"),sQuery(id+"F0.wireOp",EDGE,"E1216"),sQuery(id+"F0.wireOp",EDGE,"E1217"),sQuery(id+"F0.wireOp",EDGE,"E1218"),sQuery(id+"F0.wireOp",EDGE,"E1219"),sQuery(id+"F0.wireOp",EDGE,"E1220"),sQuery(id+"F0.wireOp",EDGE,"E1221"),sQuery(id+"F0.wireOp",EDGE,"E1222"),sQuery(id+"F0.wireOp",EDGE,"E1223"),sQuery(id+"F0.wireOp",EDGE,"E1224"),sQuery(id+"F0.wireOp",EDGE,"E1225"),sQuery(id+"F0.wireOp",EDGE,"E1226"),sQuery(id+"F0.wireOp",EDGE,"E1227"),sQuery(id+"F0.wireOp",EDGE,"E1228"),sQuery(id+"F0.wireOp",EDGE,"E1229"),sQuery(id+"F0.wireOp",EDGE,"E1230"),sQuery(id+"F0.wireOp",EDGE,"E1231"),sQuery(id+"F0.wireOp",EDGE,"E1232"),sQuery(id+"F0.wireOp",EDGE,"E1233"),sQuery(id+"F0.wireOp",EDGE,"E1234"),sQuery(id+"F0.wireOp",EDGE,"E1235"),sQuery(id+"F0.wireOp",EDGE,"E1236"),sQuery(id+"F0.wireOp",EDGE,"E1237"),sQuery(id+"F0.wireOp",EDGE,"E1238"),sQuery(id+"F0.wireOp",EDGE,"E1239"),sQuery(id+"F0.wireOp",EDGE,"E1240"),sQuery(id+"F0.wireOp",EDGE,"E1241"),sQuery(id+"F0.wireOp",EDGE,"E1242"),sQuery(id+"F0.wireOp",EDGE,"E1243"),sQuery(id+"F0.wireOp",EDGE,"E1244"),sQuery(id+"F0.wireOp",EDGE,"E1245"),sQuery(id+"F0.wireOp",EDGE,"E1246"),sQuery(id+"F0.wireOp",EDGE,"E1247"),sQuery(id+"F0.wireOp",EDGE,"E1248"),sQuery(id+"F0.wireOp",EDGE,"E1249"),sQuery(id+"F0.wireOp",EDGE,"E1250"),sQuery(id+"F0.wireOp",EDGE,"E1251"),sQuery(id+"F0.wireOp",EDGE,"E1252"),sQuery(id+"F0.wireOp",EDGE,"E1253"),sQuery(id+"F0.wireOp",EDGE,"E1254"),sQuery(id+"F0.wireOp",EDGE,"E1255"),sQuery(id+"F0.wireOp",EDGE,"E1256"),sQuery(id+"F0.wireOp",EDGE,"E1257"),sQuery(id+"F0.wireOp",EDGE,"E1258"),sQuery(id+"F0.wireOp",EDGE,"E1259"),sQuery(id+"F0.wireOp",EDGE,"E1260"),sQuery(id+"F0.wireOp",EDGE,"E1261"),sQuery(id+"F0.wireOp",EDGE,"E1262"),sQuery(id+"F0.wireOp",EDGE,"E1263"),sQuery(id+"F0.wireOp",EDGE,"E1264"),sQuery(id+"F0.wireOp",EDGE,"E1265"),sQuery(id+"F0.wireOp",EDGE,"E1266"),sQuery(id+"F0.wireOp",EDGE,"E1267"),sQuery(id+"F0.wireOp",EDGE,"E1268"),sQuery(id+"F0.wireOp",EDGE,"E1269"),sQuery(id+"F0.wireOp",EDGE,"E1270"),sQuery(id+"F0.wireOp",EDGE,"E1271"),sQuery(id+"F0.wireOp",EDGE,"E1272"),sQuery(id+"F0.wireOp",EDGE,"E1273"),sQuery(id+"F0.wireOp",EDGE,"E1274"),sQuery(id+"F0.wireOp",EDGE,"E1275"),sQuery(id+"F0.wireOp",EDGE,"E1276"),sQuery(id+"F0.wireOp",EDGE,"E1277"),sQuery(id+"F0.wireOp",EDGE,"E1278"),sQuery(id+"F0.wireOp",EDGE,"E1279"),sQuery(id+"F0.wireOp",EDGE,"E1280"),sQuery(id+"F0.wireOp",EDGE,"E1281"),sQuery(id+"F0.wireOp",EDGE,"E1282"),sQuery(id+"F0.wireOp",EDGE,"E1283"),sQuery(id+"F0.wireOp",EDGE,"E1284"),sQuery(id+"F0.wireOp",EDGE,"E1285"),sQuery(id+"F0.wireOp",EDGE,"E1286"),sQuery(id+"F0.wireOp",EDGE,"E1287"),sQuery(id+"F0.wireOp",EDGE,"E1288"),sQuery(id+"F0.wireOp",EDGE,"E1289"),sQuery(id+"F0.wireOp",EDGE,"E1290"),sQuery(id+"F0.wireOp",EDGE,"E1291"),sQuery(id+"F0.wireOp",EDGE,"E1292"),sQuery(id+"F0.wireOp",EDGE,"E1293"),sQuery(id+"F0.wireOp",EDGE,"E1294"),sQuery(id+"F0.wireOp",EDGE,"E1295"),sQuery(id+"F0.wireOp",EDGE,"E1296"),sQuery(id+"F0.wireOp",EDGE,"E1297"),sQuery(id+"F0.wireOp",EDGE,"E1298"),sQuery(id+"F0.wireOp",EDGE,"E1299"),sQuery(id+"F0.wireOp",EDGE,"E1300"),sQuery(id+"F0.wireOp",EDGE,"E1301"),sQuery(id+"F0.wireOp",EDGE,"E1302"),sQuery(id+"F0.wireOp",EDGE,"E1303"),sQuery(id+"F0.wireOp",EDGE,"E1304"),sQuery(id+"F0.wireOp",EDGE,"E1305"),sQuery(id+"F0.wireOp",EDGE,"E1306"),sQuery(id+"F0.wireOp",EDGE,"E1307"),sQuery(id+"F0.wireOp",EDGE,"E1308"),sQuery(id+"F0.wireOp",EDGE,"E1309"),sQuery(id+"F0.wireOp",EDGE,"E1310"),sQuery(id+"F0.wireOp",EDGE,"E1311"),sQuery(id+"F0.wireOp",EDGE,"E1312"),sQuery(id+"F0.wireOp",EDGE,"E1313"),sQuery(id+"F0.wireOp",EDGE,"E1314"),sQuery(id+"F0.wireOp",EDGE,"E1315"),sQuery(id+"F0.wireOp",EDGE,"E1316"),sQuery(id+"F0.wireOp",EDGE,"E1317"),sQuery(id+"F0.wireOp",EDGE,"E1318"),sQuery(id+"F0.wireOp",EDGE,"E1319"),sQuery(id+"F0.wireOp",EDGE,"E1320"),sQuery(id+"F0.wireOp",EDGE,"E1321"),sQuery(id+"F0.wireOp",EDGE,"E1322"),sQuery(id+"F0.wireOp",EDGE,"E1323"),sQuery(id+"F0.wireOp",EDGE,"E1324"),sQuery(id+"F0.wireOp",EDGE,"E1325"),sQuery(id+"F0.wireOp",EDGE,"E1326"),sQuery(id+"F0.wireOp",EDGE,"E1327"),sQuery(id+"F0.wireOp",EDGE,"E1328"),sQuery(id+"F0.wireOp",EDGE,"E1329"),sQuery(id+"F0.wireOp",EDGE,"E1330"),sQuery(id+"F0.wireOp",EDGE,"E1331"),sQuery(id+"F0.wireOp",EDGE,"E1332"),sQuery(id+"F0.wireOp",EDGE,"E1333"),sQuery(id+"F0.wireOp",EDGE,"E1334"),sQuery(id+"F0.wireOp",EDGE,"E1335"),sQuery(id+"F0.wireOp",EDGE,"E1336"),sQuery(id+"F0.wireOp",EDGE,"E1337"),sQuery(id+"F0.wireOp",EDGE,"E1338"),sQuery(id+"F0.wireOp",EDGE,"E1339"),sQuery(id+"F0.wireOp",EDGE,"E1340"),sQuery(id+"F0.wireOp",EDGE,"E1341"),sQuery(id+"F0.wireOp",EDGE,"E1342"),sQuery(id+"F0.wireOp",EDGE,"E1343"),sQuery(id+"F0.wireOp",EDGE,"E1344"),sQuery(id+"F0.wireOp",EDGE,"E1345"),sQuery(id+"F0.wireOp",EDGE,"E1346"),sQuery(id+"F0.wireOp",EDGE,"E1347"),sQuery(id+"F0.wireOp",EDGE,"E1348"),sQuery(id+"F0.wireOp",EDGE,"E1349"),sQuery(id+"F0.wireOp",EDGE,"E1350"),sQuery(id+"F0.wireOp",EDGE,"E1351"),sQuery(id+"F0.wireOp",EDGE,"E1352"),sQuery(id+"F0.wireOp",EDGE,"E1353"),sQuery(id+"F0.wireOp",EDGE,"E1354"),sQuery(id+"F0.wireOp",EDGE,"E1355"),sQuery(id+"F0.wireOp",EDGE,"E1356"),sQuery(id+"F0.wireOp",EDGE,"E1357"),sQuery(id+"F0.wireOp",EDGE,"E1358"),sQuery(id+"F0.wireOp",EDGE,"E1359"),sQuery(id+"F0.wireOp",EDGE,"E1360"),sQuery(id+"F0.wireOp",EDGE,"E1361"),sQuery(id+"F0.wireOp",EDGE,"E1362"),sQuery(id+"F0.wireOp",EDGE,"E1363"),sQuery(id+"F0.wireOp",EDGE,"E1364"),sQuery(id+"F0.wireOp",EDGE,"E1365"),sQuery(id+"F0.wireOp",EDGE,"E1366"),sQuery(id+"F0.wireOp",EDGE,"E1367"),sQuery(id+"F0.wireOp",EDGE,"E1368"),sQuery(id+"F0.wireOp",EDGE,"E1369"),sQuery(id+"F0.wireOp",EDGE,"E1370"),sQuery(id+"F0.wireOp",EDGE,"E1371"),sQuery(id+"F0.wireOp",EDGE,"E1372"),sQuery(id+"F0.wireOp",EDGE,"E1373"),sQuery(id+"F0.wireOp",EDGE,"E1374"),sQuery(id+"F0.wireOp",EDGE,"E1375"),sQuery(id+"F0.wireOp",EDGE,"E1376"),sQuery(id+"F0.wireOp",EDGE,"E1377"),sQuery(id+"F0.wireOp",EDGE,"E1378"),sQuery(id+"F0.wireOp",EDGE,"E1379"),sQuery(id+"F0.wireOp",EDGE,"E1380"),sQuery(id+"F0.wireOp",EDGE,"E1381"),sQuery(id+"F0.wireOp",EDGE,"E1382"),sQuery(id+"F0.wireOp",EDGE,"E1383"),sQuery(id+"F0.wireOp",EDGE,"E1384"),sQuery(id+"F0.wireOp",EDGE,"E1385"),sQuery(id+"F0.wireOp",EDGE,"E1386"),sQuery(id+"F0.wireOp",EDGE,"E1387"),sQuery(id+"F0.wireOp",EDGE,"E1388"),sQuery(id+"F0.wireOp",EDGE,"E1389"),sQuery(id+"F0.wireOp",EDGE,"E1390"),sQuery(id+"F0.wireOp",EDGE,"E1391"),sQuery(id+"F0.wireOp",EDGE,"E1392"),sQuery(id+"F0.wireOp",EDGE,"E1393"),sQuery(id+"F0.wireOp",EDGE,"E1394"),sQuery(id+"F0.wireOp",EDGE,"E1395"),sQuery(id+"F0.wireOp",EDGE,"E1396"),sQuery(id+"F0.wireOp",EDGE,"E1397"),sQuery(id+"F0.wireOp",EDGE,"E1398"),sQuery(id+"F0.wireOp",EDGE,"E1399"),sQuery(id+"F0.wireOp",EDGE,"E1400"),sQuery(id+"F0.wireOp",EDGE,"E1401"),sQuery(id+"F0.wireOp",EDGE,"E1402"),sQuery(id+"F0.wireOp",EDGE,"E1403"),sQuery(id+"F0.wireOp",EDGE,"E1404"),sQuery(id+"F0.wireOp",EDGE,"E1405"),sQuery(id+"F0.wireOp",EDGE,"E1406"),sQuery(id+"F0.wireOp",EDGE,"E1407"),sQuery(id+"F0.wireOp",EDGE,"E1408"),sQuery(id+"F0.wireOp",EDGE,"E1409"),sQuery(id+"F0.wireOp",EDGE,"E1410"),sQuery(id+"F0.wireOp",EDGE,"E1411"),sQuery(id+"F0.wireOp",EDGE,"E1412"),sQuery(id+"F0.wireOp",EDGE,"E1413"),sQuery(id+"F0.wireOp",EDGE,"E1414"),sQuery(id+"F0.wireOp",EDGE,"E1415"),sQuery(id+"F0.wireOp",EDGE,"E1416"),sQuery(id+"F0.wireOp",EDGE,"E1417"),sQuery(id+"F0.wireOp",EDGE,"E1418"),sQuery(id+"F0.wireOp",EDGE,"E1419"),sQuery(id+"F0.wireOp",EDGE,"E1420"),sQuery(id+"F0.wireOp",EDGE,"E1421"),sQuery(id+"F0.wireOp",EDGE,"E1422"),sQuery(id+"F0.wireOp",EDGE,"E1423"),sQuery(id+"F0.wireOp",EDGE,"E1424"),sQuery(id+"F0.wireOp",EDGE,"E1425"),sQuery(id+"F0.wireOp",EDGE,"E1426"),sQuery(id+"F0.wireOp",EDGE,"E1427"),sQuery(id+"F0.wireOp",EDGE,"E1428"),sQuery(id+"F0.wireOp",EDGE,"E1429"),sQuery(id+"F0.wireOp",EDGE,"E1430"),sQuery(id+"F0.wireOp",EDGE,"E1431"),sQuery(id+"F0.wireOp",EDGE,"E1432"),sQuery(id+"F0.wireOp",EDGE,"E1433"),sQuery(id+"F0.wireOp",EDGE,"E1434"),sQuery(id+"F0.wireOp",EDGE,"E1435"),sQuery(id+"F0.wireOp",EDGE,"E1436"),sQuery(id+"F0.wireOp",EDGE,"E1437"),sQuery(id+"F0.wireOp",EDGE,"E1438"),sQuery(id+"F0.wireOp",EDGE,"E1439"),sQuery(id+"F0.wireOp",EDGE,"E1440"),sQuery(id+"F0.wireOp",EDGE,"E1441"),sQuery(id+"F0.wireOp",EDGE,"E1442"),sQuery(id+"F0.wireOp",EDGE,"E1443"),sQuery(id+"F0.wireOp",EDGE,"E1444"),sQuery(id+"F0.wireOp",EDGE,"E1445"),sQuery(id+"F0.wireOp",EDGE,"E1446"),sQuery(id+"F0.wireOp",EDGE,"E1447"),sQuery(id+"F0.wireOp",EDGE,"E1448"),sQuery(id+"F0.wireOp",EDGE,"E1449"),sQuery(id+"F0.wireOp",EDGE,"E1450"),sQuery(id+"F0.wireOp",EDGE,"E1451"),sQuery(id+"F0.wireOp",EDGE,"E1452"),sQuery(id+"F0.wireOp",EDGE,"E1453"),sQuery(id+"F0.wireOp",EDGE,"E1454"),sQuery(id+"F0.wireOp",EDGE,"E1455"),sQuery(id+"F0.wireOp",EDGE,"E1456"),sQuery(id+"F0.wireOp",EDGE,"E1457"),sQuery(id+"F0.wireOp",EDGE,"E1458"),sQuery(id+"F0.wireOp",EDGE,"E1459"),sQuery(id+"F0.wireOp",EDGE,"E1460"),sQuery(id+"F0.wireOp",EDGE,"E1461"),sQuery(id+"F0.wireOp",EDGE,"E1462"),sQuery(id+"F0.wireOp",EDGE,"E1463"),sQuery(id+"F0.wireOp",EDGE,"E1464"),sQuery(id+"F0.wireOp",EDGE,"E1465"),sQuery(id+"F0.wireOp",EDGE,"E1466"),sQuery(id+"F0.wireOp",EDGE,"E1467"),sQuery(id+"F0.wireOp",EDGE,"E1468"),sQuery(id+"F0.wireOp",EDGE,"E1469"),sQuery(id+"F0.wireOp",EDGE,"E1470"),sQuery(id+"F0.wireOp",EDGE,"E1471"),sQuery(id+"F0.wireOp",EDGE,"E1472"),sQuery(id+"F0.wireOp",EDGE,"E1473"),sQuery(id+"F0.wireOp",EDGE,"E1474"),sQuery(id+"F0.wireOp",EDGE,"E1475"),sQuery(id+"F0.wireOp",EDGE,"E1476"),sQuery(id+"F0.wireOp",EDGE,"E1477"),sQuery(id+"F0.wireOp",EDGE,"E1478"),sQuery(id+"F0.wireOp",EDGE,"E1479"),sQuery(id+"F0.wireOp",EDGE,"E1480"),sQuery(id+"F0.wireOp",EDGE,"E1481"),sQuery(id+"F0.wireOp",EDGE,"E1482"),sQuery(id+"F0.wireOp",EDGE,"E1483"),sQuery(id+"F0.wireOp",EDGE,"E1484"),sQuery(id+"F0.wireOp",EDGE,"E1485"),sQuery(id+"F0.wireOp",EDGE,"E1486"),sQuery(id+"F0.wireOp",EDGE,"E1487"),sQuery(id+"F0.wireOp",EDGE,"E1488"),sQuery(id+"F0.wireOp",EDGE,"E1489"),sQuery(id+"F0.wireOp",EDGE,"E1490"),sQuery(id+"F0.wireOp",EDGE,"E1491"),sQuery(id+"F0.wireOp",EDGE,"E1492"),sQuery(id+"F0.wireOp",EDGE,"E1493"),sQuery(id+"F0.wireOp",EDGE,"E1494"),sQuery(id+"F0.wireOp",EDGE,"E1495"),sQuery(id+"F0.wireOp",EDGE,"E1496"),sQuery(id+"F0.wireOp",EDGE,"E1497"),sQuery(id+"F0.wireOp",EDGE,"E1498"),sQuery(id+"F0.wireOp",EDGE,"E1499"),sQuery(id+"F0.wireOp",EDGE,"E1500"),sQuery(id+"F0.wireOp",EDGE,"E1501"),sQuery(id+"F0.wireOp",EDGE,"E1502"),sQuery(id+"F0.wireOp",EDGE,"E1503"),sQuery(id+"F0.wireOp",EDGE,"E1504"),sQuery(id+"F0.wireOp",EDGE,"E1505"),sQuery(id+"F0.wireOp",EDGE,"E1506"),sQuery(id+"F0.wireOp",EDGE,"E1507"),sQuery(id+"F0.wireOp",EDGE,"E1508"),sQuery(id+"F0.wireOp",EDGE,"E1509"),sQuery(id+"F0.wireOp",EDGE,"E1510"),sQuery(id+"F0.wireOp",EDGE,"E1511"),sQuery(id+"F0.wireOp",EDGE,"E1512"),sQuery(id+"F0.wireOp",EDGE,"E1513"),sQuery(id+"F0.wireOp",EDGE,"E1514"),sQuery(id+"F0.wireOp",EDGE,"E1515"),sQuery(id+"F0.wireOp",EDGE,"E1516"),sQuery(id+"F0.wireOp",EDGE,"E1517"),sQuery(id+"F0.wireOp",EDGE,"E1518"),sQuery(id+"F0.wireOp",EDGE,"E1519"),sQuery(id+"F0.wireOp",EDGE,"E1520"),sQuery(id+"F0.wireOp",EDGE,"E1521"),sQuery(id+"F0.wireOp",EDGE,"E1522"),sQuery(id+"F0.wireOp",EDGE,"E1523"),sQuery(id+"F0.wireOp",EDGE,"E1524"),sQuery(id+"F0.wireOp",EDGE,"E1525"),sQuery(id+"F0.wireOp",EDGE,"E1526"),sQuery(id+"F0.wireOp",EDGE,"E1527"),sQuery(id+"F0.wireOp",EDGE,"E1528"),sQuery(id+"F0.wireOp",EDGE,"E1529"),sQuery(id+"F0.wireOp",EDGE,"E1530"),sQuery(id+"F0.wireOp",EDGE,"E1531"),sQuery(id+"F0.wireOp",EDGE,"E1532"),sQuery(id+"F0.wireOp",EDGE,"E1533"),sQuery(id+"F0.wireOp",EDGE,"E1534"),sQuery(id+"F0.wireOp",EDGE,"E1535"),sQuery(id+"F0.wireOp",EDGE,"E1536"),sQuery(id+"F0.wireOp",EDGE,"E1537"),sQuery(id+"F0.wireOp",EDGE,"E1538"),sQuery(id+"F0.wireOp",EDGE,"E1539"),sQuery(id+"F0.wireOp",EDGE,"E1540"),sQuery(id+"F0.wireOp",EDGE,"E1541"),sQuery(id+"F0.wireOp",EDGE,"E1542"),sQuery(id+"F0.wireOp",EDGE,"E1543"),sQuery(id+"F0.wireOp",EDGE,"E1544"),sQuery(id+"F0.wireOp",EDGE,"E1545"),sQuery(id+"F0.wireOp",EDGE,"E1546"),sQuery(id+"F0.wireOp",EDGE,"E1547"),sQuery(id+"F0.wireOp",EDGE,"E1548"),sQuery(id+"F0.wireOp",EDGE,"E1549"),sQuery(id+"F0.wireOp",EDGE,"E1550"),sQuery(id+"F0.wireOp",EDGE,"E1551"),sQuery(id+"F0.wireOp",EDGE,"E1552"),sQuery(id+"F0.wireOp",EDGE,"E1553"),sQuery(id+"F0.wireOp",EDGE,"E1554"),sQuery(id+"F0.wireOp",EDGE,"E1555"),sQuery(id+"F0.wireOp",EDGE,"E1556"),sQuery(id+"F0.wireOp",EDGE,"E1557"),sQuery(id+"F0.wireOp",EDGE,"E1558"),sQuery(id+"F0.wireOp",EDGE,"E1559"),sQuery(id+"F0.wireOp",EDGE,"E1560"),sQuery(id+"F0.wireOp",EDGE,"E1561"),sQuery(id+"F0.wireOp",EDGE,"E1562"),sQuery(id+"F0.wireOp",EDGE,"E1563"),sQuery(id+"F0.wireOp",EDGE,"E1564"),sQuery(id+"F0.wireOp",EDGE,"E1565"),sQuery(id+"F0.wireOp",EDGE,"E1566"),sQuery(id+"F0.wireOp",EDGE,"E1567"),sQuery(id+"F0.wireOp",EDGE,"E1568"),sQuery(id+"F0.wireOp",EDGE,"E1569"),sQuery(id+"F0.wireOp",EDGE,"E1570"),sQuery(id+"F0.wireOp",EDGE,"E1571"),sQuery(id+"F0.wireOp",EDGE,"E1572"),sQuery(id+"F0.wireOp",EDGE,"E1573"),sQuery(id+"F0.wireOp",EDGE,"E1574"),sQuery(id+"F0.wireOp",EDGE,"E1575"),sQuery(id+"F0.wireOp",EDGE,"E1576"),sQuery(id+"F0.wireOp",EDGE,"E1577"),sQuery(id+"F0.wireOp",EDGE,"E1578"),sQuery(id+"F0.wireOp",EDGE,"E1579"),sQuery(id+"F0.wireOp",EDGE,"E1580"),sQuery(id+"F0.wireOp",EDGE,"E1581"),sQuery(id+"F0.wireOp",EDGE,"E1582"),sQuery(id+"F0.wireOp",EDGE,"E1583"),sQuery(id+"F0.wireOp",EDGE,"E1584"),sQuery(id+"F0.wireOp",EDGE,"E1585"),sQuery(id+"F0.wireOp",EDGE,"E1586"),sQuery(id+"F0.wireOp",EDGE,"E1587"),sQuery(id+"F0.wireOp",EDGE,"E1588"),sQuery(id+"F0.wireOp",EDGE,"E1589"),sQuery(id+"F0.wireOp",EDGE,"E1590"),sQuery(id+"F0.wireOp",EDGE,"E1591"),sQuery(id+"F0.wireOp",EDGE,"E1592"),sQuery(id+"F0.wireOp",EDGE,"E1593"),sQuery(id+"F0.wireOp",EDGE,"E1594"),sQuery(id+"F0.wireOp",EDGE,"E1595"),sQuery(id+"F0.wireOp",EDGE,"E1596"),sQuery(id+"F0.wireOp",EDGE,"E1597"),sQuery(id+"F0.wireOp",EDGE,"E1598"),sQuery(id+"F0.wireOp",EDGE,"E1599"),sQuery(id+"F0.wireOp",EDGE,"E1600"),sQuery(id+"F0.wireOp",EDGE,"E1601"),sQuery(id+"F0.wireOp",EDGE,"E1602"),sQuery(id+"F0.wireOp",EDGE,"E1603"),sQuery(id+"F0.wireOp",EDGE,"E1604"),sQuery(id+"F0.wireOp",EDGE,"E1605"),sQuery(id+"F0.wireOp",EDGE,"E1606"),sQuery(id+"F0.wireOp",EDGE,"E1607"),sQuery(id+"F0.wireOp",EDGE,"E1608"),sQuery(id+"F0.wireOp",EDGE,"E1609"),sQuery(id+"F0.wireOp",EDGE,"E1610"),sQuery(id+"F0.wireOp",EDGE,"E1611"),sQuery(id+"F0.wireOp",EDGE,"E1612"),sQuery(id+"F0.wireOp",EDGE,"E1613"),sQuery(id+"F0.wireOp",EDGE,"E1614"),sQuery(id+"F0.wireOp",EDGE,"E1615"),sQuery(id+"F0.wireOp",EDGE,"E1616"),sQuery(id+"F0.wireOp",EDGE,"E1617"),sQuery(id+"F0.wireOp",EDGE,"E1618"),sQuery(id+"F0.wireOp",EDGE,"E1619"),sQuery(id+"F0.wireOp",EDGE,"E1620"),sQuery(id+"F0.wireOp",EDGE,"E1621"),sQuery(id+"F0.wireOp",EDGE,"E1622"),sQuery(id+"F0.wireOp",EDGE,"E1623"),sQuery(id+"F0.wireOp",EDGE,"E1624"),sQuery(id+"F0.wireOp",EDGE,"E1625"),sQuery(id+"F0.wireOp",EDGE,"E1626"),sQuery(id+"F0.wireOp",EDGE,"E1627"),sQuery(id+"F0.wireOp",EDGE,"E1628"),sQuery(id+"F0.wireOp",EDGE,"E1629"),sQuery(id+"F0.wireOp",EDGE,"E1630"),sQuery(id+"F0.wireOp",EDGE,"E1631"),sQuery(id+"F0.wireOp",EDGE,"E1632"),sQuery(id+"F0.wireOp",EDGE,"E1633"),sQuery(id+"F0.wireOp",EDGE,"E1634"),sQuery(id+"F0.wireOp",EDGE,"E1635"),sQuery(id+"F0.wireOp",EDGE,"E1636"),sQuery(id+"F0.wireOp",EDGE,"E1637"),sQuery(id+"F0.wireOp",EDGE,"E1638"),sQuery(id+"F0.wireOp",EDGE,"E1639"),sQuery(id+"F0.wireOp",EDGE,"E1640"),sQuery(id+"F0.wireOp",EDGE,"E1641"),sQuery(id+"F0.wireOp",EDGE,"E1642"),sQuery(id+"F0.wireOp",EDGE,"E1643"),sQuery(id+"F0.wireOp",EDGE,"E1644"),sQuery(id+"F0.wireOp",EDGE,"E1645"),sQuery(id+"F0.wireOp",EDGE,"E1646"),sQuery(id+"F0.wireOp",EDGE,"E1647"),sQuery(id+"F0.wireOp",EDGE,"E1648"),sQuery(id+"F0.wireOp",EDGE,"E1649"),sQuery(id+"F0.wireOp",EDGE,"E1650"),sQuery(id+"F0.wireOp",EDGE,"E1651"),sQuery(id+"F0.wireOp",EDGE,"E1652"),sQuery(id+"F0.wireOp",EDGE,"E1653"),sQuery(id+"F0.wireOp",EDGE,"E1654"),sQuery(id+"F0.wireOp",EDGE,"E1655"),sQuery(id+"F0.wireOp",EDGE,"E1656"),sQuery(id+"F0.wireOp",EDGE,"E1657"),sQuery(id+"F0.wireOp",EDGE,"E1658"),sQuery(id+"F0.wireOp",EDGE,"E1659"),sQuery(id+"F0.wireOp",EDGE,"E1660"),sQuery(id+"F0.wireOp",EDGE,"E1661"),sQuery(id+"F0.wireOp",EDGE,"E1662"),sQuery(id+"F0.wireOp",EDGE,"E1663"),sQuery(id+"F0.wireOp",EDGE,"E1664"),sQuery(id+"F0.wireOp",EDGE,"E1665"),sQuery(id+"F0.wireOp",EDGE,"E1666"),sQuery(id+"F0.wireOp",EDGE,"E1667"),sQuery(id+"F0.wireOp",EDGE,"E1668"),sQuery(id+"F0.wireOp",EDGE,"E1669"),sQuery(id+"F0.wireOp",EDGE,"E1670"),sQuery(id+"F0.wireOp",EDGE,"E1671"),sQuery(id+"F0.wireOp",EDGE,"E1672"),sQuery(id+"F0.wireOp",EDGE,"E1673"),sQuery(id+"F0.wireOp",EDGE,"E1674"),sQuery(id+"F0.wireOp",EDGE,"E1675"),sQuery(id+"F0.wireOp",EDGE,"E1676"),sQuery(id+"F0.wireOp",EDGE,"E1677"),sQuery(id+"F0.wireOp",EDGE,"E1678"),sQuery(id+"F0.wireOp",EDGE,"E1679"),sQuery(id+"F0.wireOp",EDGE,"E1680"),sQuery(id+"F0.wireOp",EDGE,"E1681"),sQuery(id+"F0.wireOp",EDGE,"E1682"),sQuery(id+"F0.wireOp",EDGE,"E1683"),sQuery(id+"F0.wireOp",EDGE,"E1684"),sQuery(id+"F0.wireOp",EDGE,"E1685"),sQuery(id+"F0.wireOp",EDGE,"E1686"),sQuery(id+"F0.wireOp",EDGE,"E1687"),sQuery(id+"F0.wireOp",EDGE,"E1688"),sQuery(id+"F0.wireOp",EDGE,"E1689"),sQuery(id+"F0.wireOp",EDGE,"E1690"),sQuery(id+"F0.wireOp",EDGE,"E1691"),sQuery(id+"F0.wireOp",EDGE,"E1692"),sQuery(id+"F0.wireOp",EDGE,"E1693"),sQuery(id+"F0.wireOp",EDGE,"E1694"),sQuery(id+"F0.wireOp",EDGE,"E1695"),sQuery(id+"F0.wireOp",EDGE,"E1696"),sQuery(id+"F0.wireOp",EDGE,"E1697"),sQuery(id+"F0.wireOp",EDGE,"E1698"),sQuery(id+"F0.wireOp",EDGE,"E1699"),sQuery(id+"F0.wireOp",EDGE,"E1700"),sQuery(id+"F0.wireOp",EDGE,"E1701"),sQuery(id+"F0.wireOp",EDGE,"E1702"),sQuery(id+"F0.wireOp",EDGE,"E1703"),sQuery(id+"F0.wireOp",EDGE,"E1704"),sQuery(id+"F0.wireOp",EDGE,"E1705"),sQuery(id+"F0.wireOp",EDGE,"E1706"),sQuery(id+"F0.wireOp",EDGE,"E1707"),sQuery(id+"F0.wireOp",EDGE,"E1708"),sQuery(id+"F0.wireOp",EDGE,"E1709"),sQuery(id+"F0.wireOp",EDGE,"E1710"),sQuery(id+"F0.wireOp",EDGE,"E1711"),sQuery(id+"F0.wireOp",EDGE,"E1712"),sQuery(id+"F0.wireOp",EDGE,"E1713"),sQuery(id+"F0.wireOp",EDGE,"E1714"),sQuery(id+"F0.wireOp",EDGE,"E1715"),sQuery(id+"F0.wireOp",EDGE,"E1716"),sQuery(id+"F0.wireOp",EDGE,"E1717"),sQuery(id+"F0.wireOp",EDGE,"E1718"),sQuery(id+"F0.wireOp",EDGE,"E1719"),sQuery(id+"F0.wireOp",EDGE,"E1720"),sQuery(id+"F0.wireOp",EDGE,"E1721"),sQuery(id+"F0.wireOp",EDGE,"E1722"),sQuery(id+"F0.wireOp",EDGE,"E1723"),sQuery(id+"F0.wireOp",EDGE,"E1724"),sQuery(id+"F0.wireOp",EDGE,"E1725"),sQuery(id+"F0.wireOp",EDGE,"E1726"),sQuery(id+"F0.wireOp",EDGE,"E1727"),sQuery(id+"F0.wireOp",EDGE,"E1728"),sQuery(id+"F0.wireOp",EDGE,"E1729"),sQuery(id+"F0.wireOp",EDGE,"E1730"),sQuery(id+"F0.wireOp",EDGE,"E1731"),sQuery(id+"F0.wireOp",EDGE,"E1732"),sQuery(id+"F0.wireOp",EDGE,"E1733"),sQuery(id+"F0.wireOp",EDGE,"E1734"),sQuery(id+"F0.wireOp",EDGE,"E1735"),sQuery(id+"F0.wireOp",EDGE,"E1736"),sQuery(id+"F0.wireOp",EDGE,"E1737"),sQuery(id+"F0.wireOp",EDGE,"E1738"),sQuery(id+"F0.wireOp",EDGE,"E1739"),sQuery(id+"F0.wireOp",EDGE,"E1740"),sQuery(id+"F0.wireOp",EDGE,"E1741"),sQuery(id+"F0.wireOp",EDGE,"E1742"),sQuery(id+"F0.wireOp",EDGE,"E1743"),sQuery(id+"F0.wireOp",EDGE,"E1744"),sQuery(id+"F0.wireOp",EDGE,"E1745"),sQuery(id+"F0.wireOp",EDGE,"E1746"),sQuery(id+"F0.wireOp",EDGE,"E1747"),sQuery(id+"F0.wireOp",EDGE,"E1748"),sQuery(id+"F0.wireOp",EDGE,"E1749"),sQuery(id+"F0.wireOp",EDGE,"E1750"),sQuery(id+"F0.wireOp",EDGE,"E1751"),sQuery(id+"F0.wireOp",EDGE,"E1752"),sQuery(id+"F0.wireOp",EDGE,"E1753"),sQuery(id+"F0.wireOp",EDGE,"E1754"),sQuery(id+"F0.wireOp",EDGE,"E1755"),sQuery(id+"F0.wireOp",EDGE,"E1756"),sQuery(id+"F0.wireOp",EDGE,"E1757"),sQuery(id+"F0.wireOp",EDGE,"E1758"),sQuery(id+"F0.wireOp",EDGE,"E1759"),sQuery(id+"F0.wireOp",EDGE,"E1760"),sQuery(id+"F0.wireOp",EDGE,"E1761"),sQuery(id+"F0.wireOp",EDGE,"E1762"),sQuery(id+"F0.wireOp",EDGE,"E1763"),sQuery(id+"F0.wireOp",EDGE,"E1764"),sQuery(id+"F0.wireOp",EDGE,"E1765"),sQuery(id+"F0.wireOp",EDGE,"E1766"),sQuery(id+"F0.wireOp",EDGE,"E1767"),sQuery(id+"F0.wireOp",EDGE,"E1768"),sQuery(id+"F0.wireOp",EDGE,"E1769"),sQuery(id+"F0.wireOp",EDGE,"E1770"),sQuery(id+"F0.wireOp",EDGE,"E1771"),sQuery(id+"F0.wireOp",EDGE,"E1772"),sQuery(id+"F0.wireOp",EDGE,"E1773"),sQuery(id+"F0.wireOp",EDGE,"E1774"),sQuery(id+"F0.wireOp",EDGE,"E1775"),sQuery(id+"F0.wireOp",EDGE,"E1776"),sQuery(id+"F0.wireOp",EDGE,"E1777"),sQuery(id+"F0.wireOp",EDGE,"E1778"),sQuery(id+"F0.wireOp",EDGE,"E1779"),sQuery(id+"F0.wireOp",EDGE,"E1780"),sQuery(id+"F0.wireOp",EDGE,"E1781"),sQuery(id+"F0.wireOp",EDGE,"E1782"),sQuery(id+"F0.wireOp",EDGE,"E1783"),sQuery(id+"F0.wireOp",EDGE,"E1784"),sQuery(id+"F0.wireOp",EDGE,"E1785"),sQuery(id+"F0.wireOp",EDGE,"E1786"),sQuery(id+"F0.wireOp",EDGE,"E1787"),sQuery(id+"F0.wireOp",EDGE,"E1788"),sQuery(id+"F0.wireOp",EDGE,"E1789"),sQuery(id+"F0.wireOp",EDGE,"E1790"),sQuery(id+"F0.wireOp",EDGE,"E1791"),sQuery(id+"F0.wireOp",EDGE,"E1792"),sQuery(id+"F0.wireOp",EDGE,"E1793"),sQuery(id+"F0.wireOp",EDGE,"E1794"),sQuery(id+"F0.wireOp",EDGE,"E1795"),sQuery(id+"F0.wireOp",EDGE,"E1796"),sQuery(id+"F0.wireOp",EDGE,"E1797"),sQuery(id+"F0.wireOp",EDGE,"E1798"),sQuery(id+"F0.wireOp",EDGE,"E1799"),sQuery(id+"F0.wireOp",EDGE,"E1800"),sQuery(id+"F0.wireOp",EDGE,"E1801"),sQuery(id+"F0.wireOp",EDGE,"E1802"),sQuery(id+"F0.wireOp",EDGE,"E1803"),sQuery(id+"F0.wireOp",EDGE,"E1804"),sQuery(id+"F0.wireOp",EDGE,"E1805"),sQuery(id+"F0.wireOp",EDGE,"E1806"),sQuery(id+"F0.wireOp",EDGE,"E1807"),sQuery(id+"F0.wireOp",EDGE,"E1808"),sQuery(id+"F0.wireOp",EDGE,"E1809"),sQuery(id+"F0.wireOp",EDGE,"E1810"),sQuery(id+"F0.wireOp",EDGE,"E1811"),sQuery(id+"F0.wireOp",EDGE,"E1812"),sQuery(id+"F0.wireOp",EDGE,"E1813"),sQuery(id+"F0.wireOp",EDGE,"E1814"),sQuery(id+"F0.wireOp",EDGE,"E1815"),sQuery(id+"F0.wireOp",EDGE,"E1816"),sQuery(id+"F0.wireOp",EDGE,"E1817"),sQuery(id+"F0.wireOp",EDGE,"E1818"),sQuery(id+"F0.wireOp",EDGE,"E1819"),sQuery(id+"F0.wireOp",EDGE,"E1820"),sQuery(id+"F0.wireOp",EDGE,"E1821"),sQuery(id+"F0.wireOp",EDGE,"E1822"),sQuery(id+"F0.wireOp",EDGE,"E1823"),sQuery(id+"F0.wireOp",EDGE,"E1824"),sQuery(id+"F0.wireOp",EDGE,"E1825"),sQuery(id+"F0.wireOp",EDGE,"E1826"),sQuery(id+"F0.wireOp",EDGE,"E1827"),sQuery(id+"F0.wireOp",EDGE,"E1828"),sQuery(id+"F0.wireOp",EDGE,"E1829"),sQuery(id+"F0.wireOp",EDGE,"E1830"),sQuery(id+"F0.wireOp",EDGE,"E1831"),sQuery(id+"F0.wireOp",EDGE,"E1832"),sQuery(id+"F0.wireOp",EDGE,"E1833"),sQuery(id+"F0.wireOp",EDGE,"E1834"),sQuery(id+"F0.wireOp",EDGE,"E1835"),sQuery(id+"F0.wireOp",EDGE,"E1836"),sQuery(id+"F0.wireOp",EDGE,"E1837"),sQuery(id+"F0.wireOp",EDGE,"E1838"),sQuery(id+"F0.wireOp",EDGE,"E1839"),sQuery(id+"F0.wireOp",EDGE,"E1840"),sQuery(id+"F0.wireOp",EDGE,"E1841"),sQuery(id+"F0.wireOp",EDGE,"E1842"),sQuery(id+"F0.wireOp",EDGE,"E1843"),sQuery(id+"F0.wireOp",EDGE,"E1844"),sQuery(id+"F0.wireOp",EDGE,"E1845"),sQuery(id+"F0.wireOp",EDGE,"E1846"),sQuery(id+"F0.wireOp",EDGE,"E1847"),sQuery(id+"F0.wireOp",EDGE,"E1848"),sQuery(id+"F0.wireOp",EDGE,"E1849"),sQuery(id+"F0.wireOp",EDGE,"E1850"),sQuery(id+"F0.wireOp",EDGE,"E1851"),sQuery(id+"F0.wireOp",EDGE,"E1852"),sQuery(id+"F0.wireOp",EDGE,"E1853"),sQuery(id+"F0.wireOp",EDGE,"E1854"),sQuery(id+"F0.wireOp",EDGE,"E1855"),sQuery(id+"F0.wireOp",EDGE,"E1856"),sQuery(id+"F0.wireOp",EDGE,"E1857"),sQuery(id+"F0.wireOp",EDGE,"E1858"),sQuery(id+"F0.wireOp",EDGE,"E1859"),sQuery(id+"F0.wireOp",EDGE,"E1860"),sQuery(id+"F0.wireOp",EDGE,"E1861"),sQuery(id+"F0.wireOp",EDGE,"E1862"),sQuery(id+"F0.wireOp",EDGE,"E1863"),sQuery(id+"F0.wireOp",EDGE,"E1864"),sQuery(id+"F0.wireOp",EDGE,"E1865"),sQuery(id+"F0.wireOp",EDGE,"E1866"),sQuery(id+"F0.wireOp",EDGE,"E1867"),sQuery(id+"F0.wireOp",EDGE,"E1868"),sQuery(id+"F0.wireOp",EDGE,"E1869"),sQuery(id+"F0.wireOp",EDGE,"E1870"),sQuery(id+"F0.wireOp",EDGE,"E1871"),sQuery(id+"F0.wireOp",EDGE,"E1872"),sQuery(id+"F0.wireOp",EDGE,"E1873"),sQuery(id+"F0.wireOp",EDGE,"E1874"),sQuery(id+"F0.wireOp",EDGE,"E1875"),sQuery(id+"F0.wireOp",EDGE,"E1876"),sQuery(id+"F0.wireOp",EDGE,"E1877"),sQuery(id+"F0.wireOp",EDGE,"E1878"),sQuery(id+"F0.wireOp",EDGE,"E1879"),sQuery(id+"F0.wireOp",EDGE,"E1880"),sQuery(id+"F0.wireOp",EDGE,"E1881"),sQuery(id+"F0.wireOp",EDGE,"E1882"),sQuery(id+"F0.wireOp",EDGE,"E1883"),sQuery(id+"F0.wireOp",EDGE,"E1884"),sQuery(id+"F0.wireOp",EDGE,"E1885"),sQuery(id+"F0.wireOp",EDGE,"E1886"),sQuery(id+"F0.wireOp",EDGE,"E1887"),sQuery(id+"F0.wireOp",EDGE,"E1888"),sQuery(id+"F0.wireOp",EDGE,"E1889"),sQuery(id+"F0.wireOp",EDGE,"E1890"),sQuery(id+"F0.wireOp",EDGE,"E1891"),sQuery(id+"F0.wireOp",EDGE,"E1892"),sQuery(id+"F0.wireOp",EDGE,"E1893"),sQuery(id+"F0.wireOp",EDGE,"E1894"),sQuery(id+"F0.wireOp",EDGE,"E1895"),sQuery(id+"F0.wireOp",EDGE,"E1896"),sQuery(id+"F0.wireOp",EDGE,"E1897"),sQuery(id+"F0.wireOp",EDGE,"E1898"),sQuery(id+"F0.wireOp",EDGE,"E1899"),sQuery(id+"F0.wireOp",EDGE,"E1900"),sQuery(id+"F0.wireOp",EDGE,"E1901"),sQuery(id+"F0.wireOp",EDGE,"E1902"),sQuery(id+"F0.wireOp",EDGE,"E1903"),sQuery(id+"F0.wireOp",EDGE,"E1904"),sQuery(id+"F0.wireOp",EDGE,"E1905"),sQuery(id+"F0.wireOp",EDGE,"E1906"),sQuery(id+"F0.wireOp",EDGE,"E1907"),sQuery(id+"F0.wireOp",EDGE,"E1908"),sQuery(id+"F0.wireOp",EDGE,"E1909"),sQuery(id+"F0.wireOp",EDGE,"E1910"),sQuery(id+"F0.wireOp",EDGE,"E1911"),sQuery(id+"F0.wireOp",EDGE,"E1912"),sQuery(id+"F0.wireOp",EDGE,"E1913"),sQuery(id+"F0.wireOp",EDGE,"E1914"),sQuery(id+"F0.wireOp",EDGE,"E1915"),sQuery(id+"F0.wireOp",EDGE,"E1916"),sQuery(id+"F0.wireOp",EDGE,"E1917"),sQuery(id+"F0.wireOp",EDGE,"E1918"),sQuery(id+"F0.wireOp",EDGE,"E1919"),sQuery(id+"F0.wireOp",EDGE,"E1920"),sQuery(id+"F0.wireOp",EDGE,"E1921"),sQuery(id+"F0.wireOp",EDGE,"E1922"),sQuery(id+"F0.wireOp",EDGE,"E1923"),sQuery(id+"F0.wireOp",EDGE,"E1924"),sQuery(id+"F0.wireOp",EDGE,"E1925"),sQuery(id+"F0.wireOp",EDGE,"E1926"),sQuery(id+"F0.wireOp",EDGE,"E1927"),sQuery(id+"F0.wireOp",EDGE,"E1928"),sQuery(id+"F0.wireOp",EDGE,"E1929"),sQuery(id+"F0.wireOp",EDGE,"E1930"),sQuery(id+"F0.wireOp",EDGE,"E1931"),sQuery(id+"F0.wireOp",EDGE,"E1932"),sQuery(id+"F0.wireOp",EDGE,"E1933"),sQuery(id+"F0.wireOp",EDGE,"E1934"),sQuery(id+"F0.wireOp",EDGE,"E1935"),sQuery(id+"F0.wireOp",EDGE,"E1936"),sQuery(id+"F0.wireOp",EDGE,"E1937"),sQuery(id+"F0.wireOp",EDGE,"E1938"),sQuery(id+"F0.wireOp",EDGE,"E1939"),sQuery(id+"F0.wireOp",EDGE,"E1940"),sQuery(id+"F0.wireOp",EDGE,"E1941"),sQuery(id+"F0.wireOp",EDGE,"E1942"),sQuery(id+"F0.wireOp",EDGE,"E1943"),sQuery(id+"F0.wireOp",EDGE,"E1944"),sQuery(id+"F0.wireOp",EDGE,"E1945"),sQuery(id+"F0.wireOp",EDGE,"E1946"),sQuery(id+"F0.wireOp",EDGE,"E1947"),sQuery(id+"F0.wireOp",EDGE,"E1948"),sQuery(id+"F0.wireOp",EDGE,"E1949"),sQuery(id+"F0.wireOp",EDGE,"E1950"),sQuery(id+"F0.wireOp",EDGE,"E1951"),sQuery(id+"F0.wireOp",EDGE,"E1952"),sQuery(id+"F0.wireOp",EDGE,"E1953"),sQuery(id+"F0.wireOp",EDGE,"E1954"),sQuery(id+"F0.wireOp",EDGE,"E1955"),sQuery(id+"F0.wireOp",EDGE,"E1956"),sQuery(id+"F0.wireOp",EDGE,"E1957"),sQuery(id+"F0.wireOp",EDGE,"E1958"),sQuery(id+"F0.wireOp",EDGE,"E1959"),sQuery(id+"F0.wireOp",EDGE,"E1960"),sQuery(id+"F0.wireOp",EDGE,"E1961"),sQuery(id+"F0.wireOp",EDGE,"E1962"),sQuery(id+"F0.wireOp",EDGE,"E1963"),sQuery(id+"F0.wireOp",EDGE,"E1964"),sQuery(id+"F0.wireOp",EDGE,"E1965"),sQuery(id+"F0.wireOp",EDGE,"E1966"),sQuery(id+"F0.wireOp",EDGE,"E1967"),sQuery(id+"F0.wireOp",EDGE,"E1968"),sQuery(id+"F0.wireOp",EDGE,"E1969"),sQuery(id+"F0.wireOp",EDGE,"E1970"),sQuery(id+"F0.wireOp",EDGE,"E1971"),sQuery(id+"F0.wireOp",EDGE,"E1972"),sQuery(id+"F0.wireOp",EDGE,"E1973"),sQuery(id+"F0.wireOp",EDGE,"E1974"),sQuery(id+"F0.wireOp",EDGE,"E1975"),sQuery(id+"F0.wireOp",EDGE,"E1976"),sQuery(id+"F0.wireOp",EDGE,"E1977"),sQuery(id+"F0.wireOp",EDGE,"E1978"),sQuery(id+"F0.wireOp",EDGE,"E1979"),sQuery(id+"F0.wireOp",EDGE,"E1980"),sQuery(id+"F0.wireOp",EDGE,"E1981"),sQuery(id+"F0.wireOp",EDGE,"E1982"),sQuery(id+"F0.wireOp",EDGE,"E1983"),sQuery(id+"F0.wireOp",EDGE,"E1984"),sQuery(id+"F0.wireOp",EDGE,"E1985"),sQuery(id+"F0.wireOp",EDGE,"E1986"),sQuery(id+"F0.wireOp",EDGE,"E1987"),sQuery(id+"F0.wireOp",EDGE,"E1988"),sQuery(id+"F0.wireOp",EDGE,"E1989"),sQuery(id+"F0.wireOp",EDGE,"E1990"),sQuery(id+"F0.wireOp",EDGE,"E1991"),sQuery(id+"F0.wireOp",EDGE,"E1992"),sQuery(id+"F0.wireOp",EDGE,"E1993"),sQuery(id+"F0.wireOp",EDGE,"E1994"),sQuery(id+"F0.wireOp",EDGE,"E1995"),sQuery(id+"F0.wireOp",EDGE,"E1996"),sQuery(id+"F0.wireOp",EDGE,"E1997"),sQuery(id+"F0.wireOp",EDGE,"E1998"),sQuery(id+"F0.wireOp",EDGE,"E1999"),sQuery(id+"F0.wireOp",EDGE,"E2000"),sQuery(id+"F0.wireOp",EDGE,"E2001"),sQuery(id+"F0.wireOp",EDGE,"E2002"),sQuery(id+"F0.wireOp",EDGE,"E2003"),sQuery(id+"F0.wireOp",EDGE,"E2004"),sQuery(id+"F0.wireOp",EDGE,"E2005"),sQuery(id+"F0.wireOp",EDGE,"E2006"),sQuery(id+"F0.wireOp",EDGE,"E2007"),sQuery(id+"F0.wireOp",EDGE,"E2008"),sQuery(id+"F0.wireOp",EDGE,"E2009"),sQuery(id+"F0.wireOp",EDGE,"E2010"),sQuery(id+"F0.wireOp",EDGE,"E2011"),sQuery(id+"F0.wireOp",EDGE,"E2012"),sQuery(id+"F0.wireOp",EDGE,"E2013"),sQuery(id+"F0.wireOp",EDGE,"E2014"),sQuery(id+"F0.wireOp",EDGE,"E2015"),sQuery(id+"F0.wireOp",EDGE,"E2016"),sQuery(id+"F0.wireOp",EDGE,"E2017"),sQuery(id+"F0.wireOp",EDGE,"E2018"),sQuery(id+"F0.wireOp",EDGE,"E2019"),sQuery(id+"F0.wireOp",EDGE,"E2020"),sQuery(id+"F0.wireOp",EDGE,"E2021"),sQuery(id+"F0.wireOp",EDGE,"E2022"),sQuery(id+"F0.wireOp",EDGE,"E2023"),sQuery(id+"F0.wireOp",EDGE,"E2024"),sQuery(id+"F0.wireOp",EDGE,"E2025"),sQuery(id+"F0.wireOp",EDGE,"E2026"),sQuery(id+"F0.wireOp",EDGE,"E2027"),sQuery(id+"F0.wireOp",EDGE,"E2028"),sQuery(id+"F0.wireOp",EDGE,"E2029"),sQuery(id+"F0.wireOp",EDGE,"E2030"),sQuery(id+"F0.wireOp",EDGE,"E2031"),sQuery(id+"F0.wireOp",EDGE,"E2032"),sQuery(id+"F0.wireOp",EDGE,"E2033"),sQuery(id+"F0.wireOp",EDGE,"E2034"),sQuery(id+"F0.wireOp",EDGE,"E2035"),sQuery(id+"F0.wireOp",EDGE,"E2036"),sQuery(id+"F0.wireOp",EDGE,"E2037"),sQuery(id+"F0.wireOp",EDGE,"E2038"),sQuery(id+"F0.wireOp",EDGE,"E2039"),sQuery(id+"F0.wireOp",EDGE,"E2040"),sQuery(id+"F0.wireOp",EDGE,"E2041"),sQuery(id+"F0.wireOp",EDGE,"E2042"),sQuery(id+"F0.wireOp",EDGE,"E2043"),sQuery(id+"F0.wireOp",EDGE,"E2044"),sQuery(id+"F0.wireOp",EDGE,"E2045"),sQuery(id+"F0.wireOp",EDGE,"E2046"),sQuery(id+"F0.wireOp",EDGE,"E2047"),sQuery(id+"F0.wireOp",EDGE,"E2048"),sQuery(id+"F0.wireOp",EDGE,"E2049"),sQuery(id+"F0.wireOp",EDGE,"E2050"),sQuery(id+"F0.wireOp",EDGE,"E2051"),sQuery(id+"F0.wireOp",EDGE,"E2052"),sQuery(id+"F0.wireOp",EDGE,"E2053"),sQuery(id+"F0.wireOp",EDGE,"E2054"),sQuery(id+"F0.wireOp",EDGE,"E2055"),sQuery(id+"F0.wireOp",EDGE,"E2056"),sQuery(id+"F0.wireOp",EDGE,"E2057"),sQuery(id+"F0.wireOp",EDGE,"E2058"),sQuery(id+"F0.wireOp",EDGE,"E2059"),sQuery(id+"F0.wireOp",EDGE,"E2060"),sQuery(id+"F0.wireOp",EDGE,"E2061"),sQuery(id+"F0.wireOp",EDGE,"E2062"),sQuery(id+"F0.wireOp",EDGE,"E2063"),sQuery(id+"F0.wireOp",EDGE,"E2064"),sQuery(id+"F0.wireOp",EDGE,"E2065"),sQuery(id+"F0.wireOp",EDGE,"E2066"),sQuery(id+"F0.wireOp",EDGE,"E2067"),sQuery(id+"F0.wireOp",EDGE,"E2068"),sQuery(id+"F0.wireOp",EDGE,"E2069"),sQuery(id+"F0.wireOp",EDGE,"E2070"),sQuery(id+"F0.wireOp",EDGE,"E2071"),sQuery(id+"F0.wireOp",EDGE,"E2072"),sQuery(id+"F0.wireOp",EDGE,"E2073"),sQuery(id+"F0.wireOp",EDGE,"E2074"),sQuery(id+"F0.wireOp",EDGE,"E2075"),sQuery(id+"F0.wireOp",EDGE,"E2076"),sQuery(id+"F0.wireOp",EDGE,"E2077"),sQuery(id+"F0.wireOp",EDGE,"E2078"),sQuery(id+"F0.wireOp",EDGE,"E2079"),sQuery(id+"F0.wireOp",EDGE,"E2080"),sQuery(id+"F0.wireOp",EDGE,"E2081"),sQuery(id+"F0.wireOp",EDGE,"E2082"),sQuery(id+"F0.wireOp",EDGE,"E2083"),sQuery(id+"F0.wireOp",EDGE,"E2084"),sQuery(id+"F0.wireOp",EDGE,"E2085"),sQuery(id+"F0.wireOp",EDGE,"E2086"),sQuery(id+"F0.wireOp",EDGE,"E2087"),sQuery(id+"F0.wireOp",EDGE,"E2088"),sQuery(id+"F0.wireOp",EDGE,"E2089"),sQuery(id+"F0.wireOp",EDGE,"E2090"),sQuery(id+"F0.wireOp",EDGE,"E2091"),sQuery(id+"F0.wireOp",EDGE,"E2092"),sQuery(id+"F0.wireOp",EDGE,"E2093"),sQuery(id+"F0.wireOp",EDGE,"E2094"),sQuery(id+"F0.wireOp",EDGE,"E2095"),sQuery(id+"F0.wireOp",EDGE,"E2096"),sQuery(id+"F0.wireOp",EDGE,"E2097"),sQuery(id+"F0.wireOp",EDGE,"E2098"),sQuery(id+"F0.wireOp",EDGE,"E2099"),sQuery(id+"F0.wireOp",EDGE,"E2100"),sQuery(id+"F0.wireOp",EDGE,"E2101"),sQuery(id+"F0.wireOp",EDGE,"E2102"),sQuery(id+"F0.wireOp",EDGE,"E2103"),sQuery(id+"F0.wireOp",EDGE,"E2104"),sQuery(id+"F0.wireOp",EDGE,"E2105"),sQuery(id+"F0.wireOp",EDGE,"E2106"),sQuery(id+"F0.wireOp",EDGE,"E2107"),sQuery(id+"F0.wireOp",EDGE,"E2108"),sQuery(id+"F0.wireOp",EDGE,"E2109"),sQuery(id+"F0.wireOp",EDGE,"E2110"),sQuery(id+"F0.wireOp",EDGE,"E2111"),sQuery(id+"F0.wireOp",EDGE,"E2112"),sQuery(id+"F0.wireOp",EDGE,"E2113"),sQuery(id+"F0.wireOp",EDGE,"E2114"),sQuery(id+"F0.wireOp",EDGE,"E2115"),sQuery(id+"F0.wireOp",EDGE,"E2116"),sQuery(id+"F0.wireOp",EDGE,"E2117"),sQuery(id+"F0.wireOp",EDGE,"E2118"),sQuery(id+"F0.wireOp",EDGE,"E2119"),sQuery(id+"F0.wireOp",EDGE,"E2120"),sQuery(id+"F0.wireOp",EDGE,"E2121"),sQuery(id+"F0.wireOp",EDGE,"E2122"),sQuery(id+"F0.wireOp",EDGE,"E2123"),sQuery(id+"F0.wireOp",EDGE,"E2124"),sQuery(id+"F0.wireOp",EDGE,"E2125"),sQuery(id+"F0.wireOp",EDGE,"E2126"),sQuery(id+"F0.wireOp",EDGE,"E2127"),sQuery(id+"F0.wireOp",EDGE,"E2128"),sQuery(id+"F0.wireOp",EDGE,"E2129"),sQuery(id+"F0.wireOp",EDGE,"E2130"),sQuery(id+"F0.wireOp",EDGE,"E2131"),sQuery(id+"F0.wireOp",EDGE,"E2132"),sQuery(id+"F0.wireOp",EDGE,"E2133"),sQuery(id+"F0.wireOp",EDGE,"E2134"),sQuery(id+"F0.wireOp",EDGE,"E2135"),sQuery(id+"F0.wireOp",EDGE,"E2136"),sQuery(id+"F0.wireOp",EDGE,"E2137"),sQuery(id+"F0.wireOp",EDGE,"E2138"),sQuery(id+"F0.wireOp",EDGE,"E2139"),sQuery(id+"F0.wireOp",EDGE,"E2140"),sQuery(id+"F0.wireOp",EDGE,"E2141"),sQuery(id+"F0.wireOp",EDGE,"E2142"),sQuery(id+"F0.wireOp",EDGE,"E2143"),sQuery(id+"F0.wireOp",EDGE,"E2144"),sQuery(id+"F0.wireOp",EDGE,"E2145"),sQuery(id+"F0.wireOp",EDGE,"E2146"),sQuery(id+"F0.wireOp",EDGE,"E2147"),sQuery(id+"F0.wireOp",EDGE,"E2148"),sQuery(id+"F0.wireOp",EDGE,"E2149"),sQuery(id+"F0.wireOp",EDGE,"E2150"),sQuery(id+"F0.wireOp",EDGE,"E2151"),sQuery(id+"F0.wireOp",EDGE,"E2152"),sQuery(id+"F0.wireOp",EDGE,"E2153"),sQuery(id+"F0.wireOp",EDGE,"E2154"),sQuery(id+"F0.wireOp",EDGE,"E2155"),sQuery(id+"F0.wireOp",EDGE,"E2156"),sQuery(id+"F0.wireOp",EDGE,"E2157"),sQuery(id+"F0.wireOp",EDGE,"E2158"),sQuery(id+"F0.wireOp",EDGE,"E2159"),sQuery(id+"F0.wireOp",EDGE,"E2160"),sQuery(id+"F0.wireOp",EDGE,"E2161"),sQuery(id+"F0.wireOp",EDGE,"E2162"),sQuery(id+"F0.wireOp",EDGE,"E2163"),sQuery(id+"F0.wireOp",EDGE,"E2164"),sQuery(id+"F0.wireOp",EDGE,"E2165"),sQuery(id+"F0.wireOp",EDGE,"E2166"),sQuery(id+"F0.wireOp",EDGE,"E2167"),sQuery(id+"F0.wireOp",EDGE,"E2168"),sQuery(id+"F0.wireOp",EDGE,"E2169"),sQuery(id+"F0.wireOp",EDGE,"E2170"),sQuery(id+"F0.wireOp",EDGE,"E2171"),sQuery(id+"F0.wireOp",EDGE,"E2172"),sQuery(id+"F0.wireOp",EDGE,"E2173"),sQuery(id+"F0.wireOp",EDGE,"E2174"),sQuery(id+"F0.wireOp",EDGE,"E2175"),sQuery(id+"F0.wireOp",EDGE,"E2176"),sQuery(id+"F0.wireOp",EDGE,"E2177"),sQuery(id+"F0.wireOp",EDGE,"E2178"),sQuery(id+"F0.wireOp",EDGE,"E2179"),sQuery(id+"F0.wireOp",EDGE,"E2180"),sQuery(id+"F0.wireOp",EDGE,"E2181"),sQuery(id+"F0.wireOp",EDGE,"E2182"),sQuery(id+"F0.wireOp",EDGE,"E2183"),sQuery(id+"F0.wireOp",EDGE,"E2184"),sQuery(id+"F0.wireOp",EDGE,"E2185"),sQuery(id+"F0.wireOp",EDGE,"E2186"),sQuery(id+"F0.wireOp",EDGE,"E2187"),sQuery(id+"F0.wireOp",EDGE,"E2188"),sQuery(id+"F0.wireOp",EDGE,"E2189"),sQuery(id+"F0.wireOp",EDGE,"E2190"),sQuery(id+"F0.wireOp",EDGE,"E2191"),sQuery(id+"F0.wireOp",EDGE,"E2192"),sQuery(id+"F0.wireOp",EDGE,"E2193"),sQuery(id+"F0.wireOp",EDGE,"E2194"),sQuery(id+"F0.wireOp",EDGE,"E2195"),sQuery(id+"F0.wireOp",EDGE,"E2196"),sQuery(id+"F0.wireOp",EDGE,"E2197"),sQuery(id+"F0.wireOp",EDGE,"E2198"),sQuery(id+"F0.wireOp",EDGE,"E2199"),sQuery(id+"F0.wireOp",EDGE,"E2200"),sQuery(id+"F0.wireOp",EDGE,"E2201"),sQuery(id+"F0.wireOp",EDGE,"E2202"),sQuery(id+"F0.wireOp",EDGE,"E2203"),sQuery(id+"F0.wireOp",EDGE,"E2204"),sQuery(id+"F0.wireOp",EDGE,"E2205"),sQuery(id+"F0.wireOp",EDGE,"E2206"),sQuery(id+"F0.wireOp",EDGE,"E2207"),sQuery(id+"F0.wireOp",EDGE,"E2208"),sQuery(id+"F0.wireOp",EDGE,"E2209"),sQuery(id+"F0.wireOp",EDGE,"E2210"),sQuery(id+"F0.wireOp",EDGE,"E2211"),sQuery(id+"F0.wireOp",EDGE,"E2212"),sQuery(id+"F0.wireOp",EDGE,"E2213"),sQuery(id+"F0.wireOp",EDGE,"E2214"),sQuery(id+"F0.wireOp",EDGE,"E2215"),sQuery(id+"F0.wireOp",EDGE,"E2216"),sQuery(id+"F0.wireOp",EDGE,"E2217"),sQuery(id+"F0.wireOp",EDGE,"E2218"),sQuery(id+"F0.wireOp",EDGE,"E2219"),sQuery(id+"F0.wireOp",EDGE,"E2220"),sQuery(id+"F0.wireOp",EDGE,"E2221"),sQuery(id+"F0.wireOp",EDGE,"E2222"),sQuery(id+"F0.wireOp",EDGE,"E2223"),sQuery(id+"F0.wireOp",EDGE,"E2224"),sQuery(id+"F0.wireOp",EDGE,"E2225"),sQuery(id+"F0.wireOp",EDGE,"E2226"),sQuery(id+"F0.wireOp",EDGE,"E2227"),sQuery(id+"F0.wireOp",EDGE,"E2228"),sQuery(id+"F0.wireOp",EDGE,"E2229"),sQuery(id+"F0.wireOp",EDGE,"E2230"),sQuery(id+"F0.wireOp",EDGE,"E2231"),sQuery(id+"F0.wireOp",EDGE,"E2232"),sQuery(id+"F0.wireOp",EDGE,"E2233"),sQuery(id+"F0.wireOp",EDGE,"E2234"),sQuery(id+"F0.wireOp",EDGE,"E2235"),sQuery(id+"F0.wireOp",EDGE,"E2236"),sQuery(id+"F0.wireOp",EDGE,"E2237"),sQuery(id+"F0.wireOp",EDGE,"E2238"),sQuery(id+"F0.wireOp",EDGE,"E2239"),sQuery(id+"F0.wireOp",EDGE,"E2240"),sQuery(id+"F0.wireOp",EDGE,"E2241"),sQuery(id+"F0.wireOp",EDGE,"E2242"),sQuery(id+"F0.wireOp",EDGE,"E2243"),sQuery(id+"F0.wireOp",EDGE,"E2244"),sQuery(id+"F0.wireOp",EDGE,"E2245"),sQuery(id+"F0.wireOp",EDGE,"E2246"),sQuery(id+"F0.wireOp",EDGE,"E2247"),sQuery(id+"F0.wireOp",EDGE,"E2248"),sQuery(id+"F0.wireOp",EDGE,"E2249"),sQuery(id+"F0.wireOp",EDGE,"E2250"),sQuery(id+"F0.wireOp",EDGE,"E2251"),sQuery(id+"F0.wireOp",EDGE,"E2252"),sQuery(id+"F0.wireOp",EDGE,"E2253"),sQuery(id+"F0.wireOp",EDGE,"E2254"),sQuery(id+"F0.wireOp",EDGE,"E2255"),sQuery(id+"F0.wireOp",EDGE,"E2256"),sQuery(id+"F0.wireOp",EDGE,"E2257"),sQuery(id+"F0.wireOp",EDGE,"E2258"),sQuery(id+"F0.wireOp",EDGE,"E2259"),sQuery(id+"F0.wireOp",EDGE,"E2260"),sQuery(id+"F0.wireOp",EDGE,"E2261"),sQuery(id+"F0.wireOp",EDGE,"E2262"),sQuery(id+"F0.wireOp",EDGE,"E2263"),sQuery(id+"F0.wireOp",EDGE,"E2264"),sQuery(id+"F0.wireOp",EDGE,"E2265"),sQuery(id+"F0.wireOp",EDGE,"E2266"),sQuery(id+"F0.wireOp",EDGE,"E2267"),sQuery(id+"F0.wireOp",EDGE,"E2268"),sQuery(id+"F0.wireOp",EDGE,"E2269"),sQuery(id+"F0.wireOp",EDGE,"E2270"),sQuery(id+"F0.wireOp",EDGE,"E2271"),sQuery(id+"F0.wireOp",EDGE,"E2272"),sQuery(id+"F0.wireOp",EDGE,"E2273"),sQuery(id+"F0.wireOp",EDGE,"E2274"),sQuery(id+"F0.wireOp",EDGE,"E2275"),sQuery(id+"F0.wireOp",EDGE,"E2276"),sQuery(id+"F0.wireOp",EDGE,"E2277"),sQuery(id+"F0.wireOp",EDGE,"E2278"),sQuery(id+"F0.wireOp",EDGE,"E2279"),sQuery(id+"F0.wireOp",EDGE,"E2280"),sQuery(id+"F0.wireOp",EDGE,"E2281"),sQuery(id+"F0.wireOp",EDGE,"E2282"),sQuery(id+"F0.wireOp",EDGE,"E2283"),sQuery(id+"F0.wireOp",EDGE,"E2284"),sQuery(id+"F0.wireOp",EDGE,"E2285"),sQuery(id+"F0.wireOp",EDGE,"E2286"),sQuery(id+"F0.wireOp",EDGE,"E2287"),sQuery(id+"F0.wireOp",EDGE,"E2288"),sQuery(id+"F0.wireOp",EDGE,"E2289"),sQuery(id+"F0.wireOp",EDGE,"E2290"),sQuery(id+"F0.wireOp",EDGE,"E2291"),sQuery(id+"F0.wireOp",EDGE,"E2292"),sQuery(id+"F0.wireOp",EDGE,"E2293"),sQuery(id+"F0.wireOp",EDGE,"E2294"),sQuery(id+"F0.wireOp",EDGE,"E2295"),sQuery(id+"F0.wireOp",EDGE,"E2296"),sQuery(id+"F0.wireOp",EDGE,"E2297"),sQuery(id+"F0.wireOp",EDGE,"E2298"),sQuery(id+"F0.wireOp",EDGE,"E2299"),sQuery(id+"F0.wireOp",EDGE,"E2300"),sQuery(id+"F0.wireOp",EDGE,"E2301"),sQuery(id+"F0.wireOp",EDGE,"E2302"),sQuery(id+"F0.wireOp",EDGE,"E2303"),sQuery(id+"F0.wireOp",EDGE,"E2304"),sQuery(id+"F0.wireOp",EDGE,"E2305"),sQuery(id+"F0.wireOp",EDGE,"E2306"),sQuery(id+"F0.wireOp",EDGE,"E2307"),sQuery(id+"F0.wireOp",EDGE,"E2308"),sQuery(id+"F0.wireOp",EDGE,"E2309"),sQuery(id+"F0.wireOp",EDGE,"E2310"),sQuery(id+"F0.wireOp",EDGE,"E2311"),sQuery(id+"F0.wireOp",EDGE,"E2312"),sQuery(id+"F0.wireOp",EDGE,"E2313"),sQuery(id+"F0.wireOp",EDGE,"E2314"),sQuery(id+"F0.wireOp",EDGE,"E2315"),sQuery(id+"F0.wireOp",EDGE,"E2316"),sQuery(id+"F0.wireOp",EDGE,"E2317"),sQuery(id+"F0.wireOp",EDGE,"E2318"),sQuery(id+"F0.wireOp",EDGE,"E2319"),sQuery(id+"F0.wireOp",EDGE,"E2320"),sQuery(id+"F0.wireOp",EDGE,"E2321"),sQuery(id+"F0.wireOp",EDGE,"E2322"),sQuery(id+"F0.wireOp",EDGE,"E2323"),sQuery(id+"F0.wireOp",EDGE,"E2324"),sQuery(id+"F0.wireOp",EDGE,"E2325"),sQuery(id+"F0.wireOp",EDGE,"E2326"),sQuery(id+"F0.wireOp",EDGE,"E2327"),sQuery(id+"F0.wireOp",EDGE,"E2328"),sQuery(id+"F0.wireOp",EDGE,"E2329"),sQuery(id+"F0.wireOp",EDGE,"E2330"),sQuery(id+"F0.wireOp",EDGE,"E2331"),sQuery(id+"F0.wireOp",EDGE,"E2332"),sQuery(id+"F0.wireOp",EDGE,"E2333"),sQuery(id+"F0.wireOp",EDGE,"E2334"),sQuery(id+"F0.wireOp",EDGE,"E2335"),sQuery(id+"F0.wireOp",EDGE,"E2336"),sQuery(id+"F0.wireOp",EDGE,"E2337"),sQuery(id+"F0.wireOp",EDGE,"E2338"),sQuery(id+"F0.wireOp",EDGE,"E2339"),sQuery(id+"F0.wireOp",EDGE,"E2340"),sQuery(id+"F0.wireOp",EDGE,"E2341"),sQuery(id+"F0.wireOp",EDGE,"E2342"),sQuery(id+"F0.wireOp",EDGE,"E2343"),sQuery(id+"F0.wireOp",EDGE,"E2344"),sQuery(id+"F0.wireOp",EDGE,"E2345"),sQuery(id+"F0.wireOp",EDGE,"E2346"),sQuery(id+"F0.wireOp",EDGE,"E2347"),sQuery(id+"F0.wireOp",EDGE,"E2348"),sQuery(id+"F0.wireOp",EDGE,"E2349"),sQuery(id+"F0.wireOp",EDGE,"E2350"),sQuery(id+"F0.wireOp",EDGE,"E2351"),sQuery(id+"F0.wireOp",EDGE,"E2352"),sQuery(id+"F0.wireOp",EDGE,"E2353"),sQuery(id+"F0.wireOp",EDGE,"E2354"),sQuery(id+"F0.wireOp",EDGE,"E2355"),sQuery(id+"F0.wireOp",EDGE,"E2356"),sQuery(id+"F0.wireOp",EDGE,"E2357"),sQuery(id+"F0.wireOp",EDGE,"E2358"),sQuery(id+"F0.wireOp",EDGE,"E2359"),sQuery(id+"F0.wireOp",EDGE,"E2360"),sQuery(id+"F0.wireOp",EDGE,"E2361"),sQuery(id+"F0.wireOp",EDGE,"E2362"),sQuery(id+"F0.wireOp",EDGE,"E2363"),sQuery(id+"F0.wireOp",EDGE,"E2364"),sQuery(id+"F0.wireOp",EDGE,"E2365"),sQuery(id+"F0.wireOp",EDGE,"E2366"),sQuery(id+"F0.wireOp",EDGE,"E2367"),sQuery(id+"F0.wireOp",EDGE,"E2368"),sQuery(id+"F0.wireOp",EDGE,"E2369"),sQuery(id+"F0.wireOp",EDGE,"E2370"),sQuery(id+"F0.wireOp",EDGE,"E2371"),sQuery(id+"F0.wireOp",EDGE,"E2372"),sQuery(id+"F0.wireOp",EDGE,"E2373"),sQuery(id+"F0.wireOp",EDGE,"E2374"),sQuery(id+"F0.wireOp",EDGE,"E2375"),sQuery(id+"F0.wireOp",EDGE,"E2376"),sQuery(id+"F0.wireOp",EDGE,"E2377"),sQuery(id+"F0.wireOp",EDGE,"E2378"),sQuery(id+"F0.wireOp",EDGE,"E2379"),sQuery(id+"F0.wireOp",EDGE,"E2380"),sQuery(id+"F0.wireOp",EDGE,"E2381"),sQuery(id+"F0.wireOp",EDGE,"E2382"),sQuery(id+"F0.wireOp",EDGE,"E2383"),sQuery(id+"F0.wireOp",EDGE,"E2384"),sQuery(id+"F0.wireOp",EDGE,"E2385"),sQuery(id+"F0.wireOp",EDGE,"E2386"),sQuery(id+"F0.wireOp",EDGE,"E2387"),sQuery(id+"F0.wireOp",EDGE,"E2388"),sQuery(id+"F0.wireOp",EDGE,"E2389"),sQuery(id+"F0.wireOp",EDGE,"E2390"),sQuery(id+"F0.wireOp",EDGE,"E2391"),sQuery(id+"F0.wireOp",EDGE,"E2392"),sQuery(id+"F0.wireOp",EDGE,"E2393"),sQuery(id+"F0.wireOp",EDGE,"E2394"),sQuery(id+"F0.wireOp",EDGE,"E2395"),sQuery(id+"F0.wireOp",EDGE,"E2396"),sQuery(id+"F0.wireOp",EDGE,"E2397"),sQuery(id+"F0.wireOp",EDGE,"E2398"),sQuery(id+"F0.wireOp",EDGE,"E2399"),sQuery(id+"F0.wireOp",EDGE,"E2400"),sQuery(id+"F0.wireOp",EDGE,"E2401"),sQuery(id+"F0.wireOp",EDGE,"E2402"),sQuery(id+"F0.wireOp",EDGE,"E2403"),sQuery(id+"F0.wireOp",EDGE,"E2404"),sQuery(id+"F0.wireOp",EDGE,"E2405"),sQuery(id+"F0.wireOp",EDGE,"E2406"),sQuery(id+"F0.wireOp",EDGE,"E2407"),sQuery(id+"F0.wireOp",EDGE,"E2408"),sQuery(id+"F0.wireOp",EDGE,"E2409"),sQuery(id+"F0.wireOp",EDGE,"E2410"),sQuery(id+"F0.wireOp",EDGE,"E2411"),sQuery(id+"F0.wireOp",EDGE,"E2412"),sQuery(id+"F0.wireOp",EDGE,"E2413"),sQuery(id+"F0.wireOp",EDGE,"E2414"),sQuery(id+"F0.wireOp",EDGE,"E2415"),sQuery(id+"F0.wireOp",EDGE,"E2416"),sQuery(id+"F0.wireOp",EDGE,"E2417"),sQuery(id+"F0.wireOp",EDGE,"E2418"),sQuery(id+"F0.wireOp",EDGE,"E2419"),sQuery(id+"F0.wireOp",EDGE,"E2420"),sQuery(id+"F0.wireOp",EDGE,"E2421"),sQuery(id+"F0.wireOp",EDGE,"E2422"),sQuery(id+"F0.wireOp",EDGE,"E2423"),sQuery(id+"F0.wireOp",EDGE,"E2424"),sQuery(id+"F0.wireOp",EDGE,"E2425"),sQuery(id+"F0.wireOp",EDGE,"E2426"),sQuery(id+"F0.wireOp",EDGE,"E2427"),sQuery(id+"F0.wireOp",EDGE,"E2428"),sQuery(id+"F0.wireOp",EDGE,"E2429"),sQuery(id+"F0.wireOp",EDGE,"E2430"),sQuery(id+"F0.wireOp",EDGE,"E2431"),sQuery(id+"F0.wireOp",EDGE,"E2432"),sQuery(id+"F0.wireOp",EDGE,"E2433"),sQuery(id+"F0.wireOp",EDGE,"E2434"),sQuery(id+"F0.wireOp",EDGE,"E2435"),sQuery(id+"F0.wireOp",EDGE,"E2436"),sQuery(id+"F0.wireOp",EDGE,"E2437"),sQuery(id+"F0.wireOp",EDGE,"E2438"),sQuery(id+"F0.wireOp",EDGE,"E2439"),sQuery(id+"F0.wireOp",EDGE,"E2440"),sQuery(id+"F0.wireOp",EDGE,"E2441"),sQuery(id+"F0.wireOp",EDGE,"E2442"),sQuery(id+"F0.wireOp",EDGE,"E2443"),sQuery(id+"F0.wireOp",EDGE,"E2444"),sQuery(id+"F0.wireOp",EDGE,"E2445"),sQuery(id+"F0.wireOp",EDGE,"E2446"),sQuery(id+"F0.wireOp",EDGE,"E2447"),sQuery(id+"F0.wireOp",EDGE,"E2448"),sQuery(id+"F0.wireOp",EDGE,"E2449"),sQuery(id+"F0.wireOp",EDGE,"E2450"),sQuery(id+"F0.wireOp",EDGE,"E2451"),sQuery(id+"F0.wireOp",EDGE,"E2452"),sQuery(id+"F0.wireOp",EDGE,"E2453"),sQuery(id+"F0.wireOp",EDGE,"E2454"),sQuery(id+"F0.wireOp",EDGE,"E2455"),sQuery(id+"F0.wireOp",EDGE,"E2456"),sQuery(id+"F0.wireOp",EDGE,"E2457"),sQuery(id+"F0.wireOp",EDGE,"E2458"),sQuery(id+"F0.wireOp",EDGE,"E2459"),sQuery(id+"F0.wireOp",EDGE,"E2460"),sQuery(id+"F0.wireOp",EDGE,"E2461"),sQuery(id+"F0.wireOp",EDGE,"E2462"),sQuery(id+"F0.wireOp",EDGE,"E2463"),sQuery(id+"F0.wireOp",EDGE,"E2464"),sQuery(id+"F0.wireOp",EDGE,"E2465"),sQuery(id+"F0.wireOp",EDGE,"E2466"),sQuery(id+"F0.wireOp",EDGE,"E2467"),sQuery(id+"F0.wireOp",EDGE,"E2468"),sQuery(id+"F0.wireOp",EDGE,"E2469"),sQuery(id+"F0.wireOp",EDGE,"E2470"),sQuery(id+"F0.wireOp",EDGE,"E2471"),sQuery(id+"F0.wireOp",EDGE,"E2472"),sQuery(id+"F0.wireOp",EDGE,"E2473"),sQuery(id+"F0.wireOp",EDGE,"E2474"),sQuery(id+"F0.wireOp",EDGE,"E2475"),sQuery(id+"F0.wireOp",EDGE,"E2476"),sQuery(id+"F0.wireOp",EDGE,"E2477"),sQuery(id+"F0.wireOp",EDGE,"E2478"),sQuery(id+"F0.wireOp",EDGE,"E2479"),sQuery(id+"F0.wireOp",EDGE,"E2480"),sQuery(id+"F0.wireOp",EDGE,"E2481"),sQuery(id+"F0.wireOp",EDGE,"E2482"),sQuery(id+"F0.wireOp",EDGE,"E2483"),sQuery(id+"F0.wireOp",EDGE,"E2484"),sQuery(id+"F0.wireOp",EDGE,"E2485"),sQuery(id+"F0.wireOp",EDGE,"E2486"),sQuery(id+"F0.wireOp",EDGE,"E2487"),sQuery(id+"F0.wireOp",EDGE,"E2488"),sQuery(id+"F0.wireOp",EDGE,"E2489"),sQuery(id+"F0.wireOp",EDGE,"E2490"),sQuery(id+"F0.wireOp",EDGE,"E2491"),sQuery(id+"F0.wireOp",EDGE,"E2492"),sQuery(id+"F0.wireOp",EDGE,"E2493"),sQuery(id+"F0.wireOp",EDGE,"E2494"),sQuery(id+"F0.wireOp",EDGE,"E2495"),sQuery(id+"F0.wireOp",EDGE,"E2496"),sQuery(id+"F0.wireOp",EDGE,"E2497"),sQuery(id+"F0.wireOp",EDGE,"E2498"),sQuery(id+"F0.wireOp",EDGE,"E2499"),sQuery(id+"F0.wireOp",EDGE,"E2500"),sQuery(id+"F0.wireOp",EDGE,"E2501"),sQuery(id+"F0.wireOp",EDGE,"E2502"),sQuery(id+"F0.wireOp",EDGE,"E2503"),sQuery(id+"F0.wireOp",EDGE,"E2504"),sQuery(id+"F0.wireOp",EDGE,"E2505"),sQuery(id+"F0.wireOp",EDGE,"E2506"),sQuery(id+"F0.wireOp",EDGE,"E2507"),sQuery(id+"F0.wireOp",EDGE,"E2508"),sQuery(id+"F0.wireOp",EDGE,"E2509"),sQuery(id+"F0.wireOp",EDGE,"E2510"),sQuery(id+"F0.wireOp",EDGE,"E2511"),sQuery(id+"F0.wireOp",EDGE,"E2512"),sQuery(id+"F0.wireOp",EDGE,"E2513"),sQuery(id+"F0.wireOp",EDGE,"E2514"),sQuery(id+"F0.wireOp",EDGE,"E2515"),sQuery(id+"F0.wireOp",EDGE,"E2516"),sQuery(id+"F0.wireOp",EDGE,"E2517"),sQuery(id+"F0.wireOp",EDGE,"E2518"),sQuery(id+"F0.wireOp",EDGE,"E2519"),sQuery(id+"F0.wireOp",EDGE,"E2520"),sQuery(id+"F0.wireOp",EDGE,"E2521"),sQuery(id+"F0.wireOp",EDGE,"E2522"),sQuery(id+"F0.wireOp",EDGE,"E2523"),sQuery(id+"F0.wireOp",EDGE,"E2524"),sQuery(id+"F0.wireOp",EDGE,"E2525"),sQuery(id+"F0.wireOp",EDGE,"E2526"),sQuery(id+"F0.wireOp",EDGE,"E2527"),sQuery(id+"F0.wireOp",EDGE,"E2528"),sQuery(id+"F0.wireOp",EDGE,"E2529"),sQuery(id+"F0.wireOp",EDGE,"E2530"),sQuery(id+"F0.wireOp",EDGE,"E2531"),sQuery(id+"F0.wireOp",EDGE,"E2532"),sQuery(id+"F0.wireOp",EDGE,"E2533"),sQuery(id+"F0.wireOp",EDGE,"E2534"),sQuery(id+"F0.wireOp",EDGE,"E2535"),sQuery(id+"F0.wireOp",EDGE,"E2536"),sQuery(id+"F0.wireOp",EDGE,"E2537"),sQuery(id+"F0.wireOp",EDGE,"E2538"),sQuery(id+"F0.wireOp",EDGE,"E2539"),sQuery(id+"F0.wireOp",EDGE,"E2540"),sQuery(id+"F0.wireOp",EDGE,"E2541"),sQuery(id+"F0.wireOp",EDGE,"E2542"),sQuery(id+"F0.wireOp",EDGE,"E2543"),sQuery(id+"F0.wireOp",EDGE,"E2544"),sQuery(id+"F0.wireOp",EDGE,"E2545"),sQuery(id+"F0.wireOp",EDGE,"E2546"),sQuery(id+"F0.wireOp",EDGE,"E2547"),sQuery(id+"F0.wireOp",EDGE,"E2548"),sQuery(id+"F0.wireOp",EDGE,"E2549"),sQuery(id+"F0.wireOp",EDGE,"E2550"),sQuery(id+"F0.wireOp",EDGE,"E2551"),sQuery(id+"F0.wireOp",EDGE,"E2552"),sQuery(id+"F0.wireOp",EDGE,"E2553"),sQuery(id+"F0.wireOp",EDGE,"E2554"),sQuery(id+"F0.wireOp",EDGE,"E2555"),sQuery(id+"F0.wireOp",EDGE,"E2556"),sQuery(id+"F0.wireOp",EDGE,"E2557"),sQuery(id+"F0.wireOp",EDGE,"E2558"),sQuery(id+"F0.wireOp",EDGE,"E2559"),sQuery(id+"F0.wireOp",EDGE,"E2560"),sQuery(id+"F0.wireOp",EDGE,"E2561"),sQuery(id+"F0.wireOp",EDGE,"E2562"),sQuery(id+"F0.wireOp",EDGE,"E2563"),sQuery(id+"F0.wireOp",EDGE,"E2564"),sQuery(id+"F0.wireOp",EDGE,"E2565"),sQuery(id+"F0.wireOp",EDGE,"E2566"),sQuery(id+"F0.wireOp",EDGE,"E2567"),sQuery(id+"F0.wireOp",EDGE,"E2568"),sQuery(id+"F0.wireOp",EDGE,"E2569"),sQuery(id+"F0.wireOp",EDGE,"E2570"),sQuery(id+"F0.wireOp",EDGE,"E2571"),sQuery(id+"F0.wireOp",EDGE,"E2572"),sQuery(id+"F0.wireOp",EDGE,"E2573"),sQuery(id+"F0.wireOp",EDGE,"E2574"),sQuery(id+"F0.wireOp",EDGE,"E2575"),sQuery(id+"F0.wireOp",EDGE,"E2576"),sQuery(id+"F0.wireOp",EDGE,"E2577"),sQuery(id+"F0.wireOp",EDGE,"E2578"),sQuery(id+"F0.wireOp",EDGE,"E2579"),sQuery(id+"F0.wireOp",EDGE,"E2580"),sQuery(id+"F0.wireOp",EDGE,"E2581"),sQuery(id+"F0.wireOp",EDGE,"E2582"),sQuery(id+"F0.wireOp",EDGE,"E2583"),sQuery(id+"F0.wireOp",EDGE,"E2584"),sQuery(id+"F0.wireOp",EDGE,"E2585"),sQuery(id+"F0.wireOp",EDGE,"E2586"),sQuery(id+"F0.wireOp",EDGE,"E2587"),sQuery(id+"F0.wireOp",EDGE,"E2588"),sQuery(id+"F0.wireOp",EDGE,"E2589"),sQuery(id+"F0.wireOp",EDGE,"E2590"),sQuery(id+"F0.wireOp",EDGE,"E2591"),sQuery(id+"F0.wireOp",EDGE,"E2592"),sQuery(id+"F0.wireOp",EDGE,"E2593"),sQuery(id+"F0.wireOp",EDGE,"E2594"),sQuery(id+"F0.wireOp",EDGE,"E2595"),sQuery(id+"F0.wireOp",EDGE,"E2596"),sQuery(id+"F0.wireOp",EDGE,"E2597"),sQuery(id+"F0.wireOp",EDGE,"E2598"),sQuery(id+"F0.wireOp",EDGE,"E2599"),sQuery(id+"F0.wireOp",EDGE,"E2600"),sQuery(id+"F0.wireOp",EDGE,"E2601"),sQuery(id+"F0.wireOp",EDGE,"E2602"),sQuery(id+"F0.wireOp",EDGE,"E2603"),sQuery(id+"F0.wireOp",EDGE,"E2604"),sQuery(id+"F0.wireOp",EDGE,"E2605"),sQuery(id+"F0.wireOp",EDGE,"E2606"),sQuery(id+"F0.wireOp",EDGE,"E2607"),sQuery(id+"F0.wireOp",EDGE,"E2608"),sQuery(id+"F0.wireOp",EDGE,"E2609"),sQuery(id+"F0.wireOp",EDGE,"E2610"),sQuery(id+"F0.wireOp",EDGE,"E2611"),sQuery(id+"F0.wireOp",EDGE,"E2612"),sQuery(id+"F0.wireOp",EDGE,"E2613"),sQuery(id+"F0.wireOp",EDGE,"E2614"),sQuery(id+"F0.wireOp",EDGE,"E2615"),sQuery(id+"F0.wireOp",EDGE,"E2616"),sQuery(id+"F0.wireOp",EDGE,"E2617"),sQuery(id+"F0.wireOp",EDGE,"E2618"),sQuery(id+"F0.wireOp",EDGE,"E2619"),sQuery(id+"F0.wireOp",EDGE,"E2620"),sQuery(id+"F0.wireOp",EDGE,"E2621"),sQuery(id+"F0.wireOp",EDGE,"E2622"),sQuery(id+"F0.wireOp",EDGE,"E2623"),sQuery(id+"F0.wireOp",EDGE,"E2624"),sQuery(id+"F0.wireOp",EDGE,"E2625"),sQuery(id+"F0.wireOp",EDGE,"E2626"),sQuery(id+"F0.wireOp",EDGE,"E2627"),sQuery(id+"F0.wireOp",EDGE,"E2628"),sQuery(id+"F0.wireOp",EDGE,"E2629"),sQuery(id+"F0.wireOp",EDGE,"E2630"),sQuery(id+"F0.wireOp",EDGE,"E2631"),sQuery(id+"F0.wireOp",EDGE,"E2632"),sQuery(id+"F0.wireOp",EDGE,"E2633"),sQuery(id+"F0.wireOp",EDGE,"E2634"),sQuery(id+"F0.wireOp",EDGE,"E2635"),sQuery(id+"F0.wireOp",EDGE,"E2636"),sQuery(id+"F0.wireOp",EDGE,"E2637"),sQuery(id+"F0.wireOp",EDGE,"E2638"),sQuery(id+"F0.wireOp",EDGE,"E2639"),sQuery(id+"F0.wireOp",EDGE,"E2640"),sQuery(id+"F0.wireOp",EDGE,"E2641"),sQuery(id+"F0.wireOp",EDGE,"E2642"),sQuery(id+"F0.wireOp",EDGE,"E2643"),sQuery(id+"F0.wireOp",EDGE,"E2644"),sQuery(id+"F0.wireOp",EDGE,"E2645"),sQuery(id+"F0.wireOp",EDGE,"E2646"),sQuery(id+"F0.wireOp",EDGE,"E2647"),sQuery(id+"F0.wireOp",EDGE,"E2648"),sQuery(id+"F0.wireOp",EDGE,"E2649"),sQuery(id+"F0.wireOp",EDGE,"E2650"),sQuery(id+"F0.wireOp",EDGE,"E2651"),sQuery(id+"F0.wireOp",EDGE,"E2652"),sQuery(id+"F0.wireOp",EDGE,"E2653"),sQuery(id+"F0.wireOp",EDGE,"E2654"),sQuery(id+"F0.wireOp",EDGE,"E2655"),sQuery(id+"F0.wireOp",EDGE,"E2656"),sQuery(id+"F0.wireOp",EDGE,"E2657"),sQuery(id+"F0.wireOp",EDGE,"E2658"),sQuery(id+"F0.wireOp",EDGE,"E2659"),sQuery(id+"F0.wireOp",EDGE,"E2660"),sQuery(id+"F0.wireOp",EDGE,"E2661"),sQuery(id+"F0.wireOp",EDGE,"E2662"),sQuery(id+"F0.wireOp",EDGE,"E2663"),sQuery(id+"F0.wireOp",EDGE,"E2664"),sQuery(id+"F0.wireOp",EDGE,"E2665"),sQuery(id+"F0.wireOp",EDGE,"E2666"),sQuery(id+"F0.wireOp",EDGE,"E2667"),sQuery(id+"F0.wireOp",EDGE,"E2668"),sQuery(id+"F0.wireOp",EDGE,"E2669"),sQuery(id+"F0.wireOp",EDGE,"E2670"),sQuery(id+"F0.wireOp",EDGE,"E2671"),sQuery(id+"F0.wireOp",EDGE,"E2672"),sQuery(id+"F0.wireOp",EDGE,"E2673"),sQuery(id+"F0.wireOp",EDGE,"E2674"),sQuery(id+"F0.wireOp",EDGE,"E2675"),sQuery(id+"F0.wireOp",EDGE,"E2676"),sQuery(id+"F0.wireOp",EDGE,"E2677"),sQuery(id+"F0.wireOp",EDGE,"E2678"),sQuery(id+"F0.wireOp",EDGE,"E2679"),sQuery(id+"F0.wireOp",EDGE,"E2680"),sQuery(id+"F0.wireOp",EDGE,"E2681"),sQuery(id+"F0.wireOp",EDGE,"E2682"),sQuery(id+"F0.wireOp",EDGE,"E2683"),sQuery(id+"F0.wireOp",EDGE,"E2684"),sQuery(id+"F0.wireOp",EDGE,"E2685"),sQuery(id+"F0.wireOp",EDGE,"E2686"),sQuery(id+"F0.wireOp",EDGE,"E2687"),sQuery(id+"F0.wireOp",EDGE,"E2688"),sQuery(id+"F0.wireOp",EDGE,"E2689"),sQuery(id+"F0.wireOp",EDGE,"E2690"),sQuery(id+"F0.wireOp",EDGE,"E2691"),sQuery(id+"F0.wireOp",EDGE,"E2692"),sQuery(id+"F0.wireOp",EDGE,"E2693"),sQuery(id+"F0.wireOp",EDGE,"E2694"),sQuery(id+"F0.wireOp",EDGE,"E2695"),sQuery(id+"F0.wireOp",EDGE,"E2696"),sQuery(id+"F0.wireOp",EDGE,"E2697"),sQuery(id+"F0.wireOp",EDGE,"E2698"),sQuery(id+"F0.wireOp",EDGE,"E2699"),sQuery(id+"F0.wireOp",EDGE,"E2700"),sQuery(id+"F0.wireOp",EDGE,"E2701"),sQuery(id+"F0.wireOp",EDGE,"E2702"),sQuery(id+"F0.wireOp",EDGE,"E2703"),sQuery(id+"F0.wireOp",EDGE,"E2704"),sQuery(id+"F0.wireOp",EDGE,"E2705"),sQuery(id+"F0.wireOp",EDGE,"E2706"),sQuery(id+"F0.wireOp",EDGE,"E2707"),sQuery(id+"F0.wireOp",EDGE,"E2708"),sQuery(id+"F0.wireOp",EDGE,"E2709"),sQuery(id+"F0.wireOp",EDGE,"E2710"),sQuery(id+"F0.wireOp",EDGE,"E2711"),sQuery(id+"F0.wireOp",EDGE,"E2712"),sQuery(id+"F0.wireOp",EDGE,"E2713"),sQuery(id+"F0.wireOp",EDGE,"E2714"),sQuery(id+"F0.wireOp",EDGE,"E2715"),sQuery(id+"F0.wireOp",EDGE,"E2716"),sQuery(id+"F0.wireOp",EDGE,"E2717"),sQuery(id+"F0.wireOp",EDGE,"E2718"),sQuery(id+"F0.wireOp",EDGE,"E2719"),sQuery(id+"F0.wireOp",EDGE,"E2720"),sQuery(id+"F0.wireOp",EDGE,"E2721"),sQuery(id+"F0.wireOp",EDGE,"E2722"),sQuery(id+"F0.wireOp",EDGE,"E2723"),sQuery(id+"F0.wireOp",EDGE,"E2724"),sQuery(id+"F0.wireOp",EDGE,"E2725"),sQuery(id+"F0.wireOp",EDGE,"E2726"),sQuery(id+"F0.wireOp",EDGE,"E2727"),sQuery(id+"F0.wireOp",EDGE,"E2728"),sQuery(id+"F0.wireOp",EDGE,"E2729"),sQuery(id+"F0.wireOp",EDGE,"E2730"),sQuery(id+"F0.wireOp",EDGE,"E2731"),sQuery(id+"F0.wireOp",EDGE,"E2732"),sQuery(id+"F0.wireOp",EDGE,"E2733"),sQuery(id+"F0.wireOp",EDGE,"E2734"),sQuery(id+"F0.wireOp",EDGE,"E2735"),sQuery(id+"F0.wireOp",EDGE,"E2736"),sQuery(id+"F0.wireOp",EDGE,"E2737"),sQuery(id+"F0.wireOp",EDGE,"E2738"),sQuery(id+"F0.wireOp",EDGE,"E2739"),sQuery(id+"F0.wireOp",EDGE,"E2740"),sQuery(id+"F0.wireOp",EDGE,"E2741"),sQuery(id+"F0.wireOp",EDGE,"E2742"),sQuery(id+"F0.wireOp",EDGE,"E2743"),sQuery(id+"F0.wireOp",EDGE,"E2744"),sQuery(id+"F0.wireOp",EDGE,"E2745"),sQuery(id+"F0.wireOp",EDGE,"E2746"),sQuery(id+"F0.wireOp",EDGE,"E2747"),sQuery(id+"F0.wireOp",EDGE,"E2748"),sQuery(id+"F0.wireOp",EDGE,"E2749"),sQuery(id+"F0.wireOp",EDGE,"E2750"),sQuery(id+"F0.wireOp",EDGE,"E2751"),sQuery(id+"F0.wireOp",EDGE,"E2752"),sQuery(id+"F0.wireOp",EDGE,"E2753"),sQuery(id+"F0.wireOp",EDGE,"E2754"),sQuery(id+"F0.wireOp",EDGE,"E2755"),sQuery(id+"F0.wireOp",EDGE,"E2756"),sQuery(id+"F0.wireOp",EDGE,"E2757"),sQuery(id+"F0.wireOp",EDGE,"E2758"),sQuery(id+"F0.wireOp",EDGE,"E2759"),sQuery(id+"F0.wireOp",EDGE,"E2760"),sQuery(id+"F0.wireOp",EDGE,"E2761"),sQuery(id+"F0.wireOp",EDGE,"E2762"),sQuery(id+"F0.wireOp",EDGE,"E2763"),sQuery(id+"F0.wireOp",EDGE,"E2764"),sQuery(id+"F0.wireOp",EDGE,"E2765"),sQuery(id+"F0.wireOp",EDGE,"E2766"),sQuery(id+"F0.wireOp",EDGE,"E2767"),sQuery(id+"F0.wireOp",EDGE,"E2768"),sQuery(id+"F0.wireOp",EDGE,"E2769"),sQuery(id+"F0.wireOp",EDGE,"E2770"),sQuery(id+"F0.wireOp",EDGE,"E2771"),sQuery(id+"F0.wireOp",EDGE,"E2772"),sQuery(id+"F0.wireOp",EDGE,"E2773"),sQuery(id+"F0.wireOp",EDGE,"E2774"),sQuery(id+"F0.wireOp",EDGE,"E2775"),sQuery(id+"F0.wireOp",EDGE,"E2776"),sQuery(id+"F0.wireOp",EDGE,"E2777"),sQuery(id+"F0.wireOp",EDGE,"E2778"),sQuery(id+"F0.wireOp",EDGE,"E2779"),sQuery(id+"F0.wireOp",EDGE,"E2780"),sQuery(id+"F0.wireOp",EDGE,"E2781"),sQuery(id+"F0.wireOp",EDGE,"E2782"),sQuery(id+"F0.wireOp",EDGE,"E2783"),sQuery(id+"F0.wireOp",EDGE,"E2784"),sQuery(id+"F0.wireOp",EDGE,"E2785"),sQuery(id+"F0.wireOp",EDGE,"E2786"),sQuery(id+"F0.wireOp",EDGE,"E2787"),sQuery(id+"F0.wireOp",EDGE,"E2788"),sQuery(id+"F0.wireOp",EDGE,"E2789"),sQuery(id+"F0.wireOp",EDGE,"E2790"),sQuery(id+"F0.wireOp",EDGE,"E2791"),sQuery(id+"F0.wireOp",EDGE,"E2792"),sQuery(id+"F0.wireOp",EDGE,"E2793"),sQuery(id+"F0.wireOp",EDGE,"E2794"),sQuery(id+"F0.wireOp",EDGE,"E2795"),sQuery(id+"F0.wireOp",EDGE,"E2796"),sQuery(id+"F0.wireOp",EDGE,"E2797"),sQuery(id+"F0.wireOp",EDGE,"E2798"),sQuery(id+"F0.wireOp",EDGE,"E2799"),sQuery(id+"F0.wireOp",EDGE,"E2800"),sQuery(id+"F0.wireOp",EDGE,"E2801"),sQuery(id+"F0.wireOp",EDGE,"E2802"),sQuery(id+"F0.wireOp",EDGE,"E2803"),sQuery(id+"F0.wireOp",EDGE,"E2804"),sQuery(id+"F0.wireOp",EDGE,"E2805"),sQuery(id+"F0.wireOp",EDGE,"E2806"),sQuery(id+"F0.wireOp",EDGE,"E2807"),sQuery(id+"F0.wireOp",EDGE,"E2808"),sQuery(id+"F0.wireOp",EDGE,"E2809"),sQuery(id+"F0.wireOp",EDGE,"E2810"),sQuery(id+"F0.wireOp",EDGE,"E2811"),sQuery(id+"F0.wireOp",EDGE,"E2812"),sQuery(id+"F0.wireOp",EDGE,"E2813"),sQuery(id+"F0.wireOp",EDGE,"E2814"),sQuery(id+"F0.wireOp",EDGE,"E2815"),sQuery(id+"F0.wireOp",EDGE,"E2816"),sQuery(id+"F0.wireOp",EDGE,"E2817"),sQuery(id+"F0.wireOp",EDGE,"E2818"),sQuery(id+"F0.wireOp",EDGE,"E2819"),sQuery(id+"F0.wireOp",EDGE,"E2820"),sQuery(id+"F0.wireOp",EDGE,"E2821"),sQuery(id+"F0.wireOp",EDGE,"E2822"),sQuery(id+"F0.wireOp",EDGE,"E2823"),sQuery(id+"F0.wireOp",EDGE,"E2824"),sQuery(id+"F0.wireOp",EDGE,"E2825"),sQuery(id+"F0.wireOp",EDGE,"E2826"),sQuery(id+"F0.wireOp",EDGE,"E2827"),sQuery(id+"F0.wireOp",EDGE,"E2828"),sQuery(id+"F0.wireOp",EDGE,"E2829"),sQuery(id+"F0.wireOp",EDGE,"E2830"),sQuery(id+"F0.wireOp",EDGE,"E2831"),sQuery(id+"F0.wireOp",EDGE,"E2832"),sQuery(id+"F0.wireOp",EDGE,"E2833"),sQuery(id+"F0.wireOp",EDGE,"E2834"),sQuery(id+"F0.wireOp",EDGE,"E2835"),sQuery(id+"F0.wireOp",EDGE,"E2836"),sQuery(id+"F0.wireOp",EDGE,"E2837"),sQuery(id+"F0.wireOp",EDGE,"E2838"),sQuery(id+"F0.wireOp",EDGE,"E2839"),sQuery(id+"F0.wireOp",EDGE,"E2840"),sQuery(id+"F0.wireOp",EDGE,"E2841"),sQuery(id+"F0.wireOp",EDGE,"E2842"),sQuery(id+"F0.wireOp",EDGE,"E2843"),sQuery(id+"F0.wireOp",EDGE,"E2844"),sQuery(id+"F0.wireOp",EDGE,"E2845"),sQuery(id+"F0.wireOp",EDGE,"E2846"),sQuery(id+"F0.wireOp",EDGE,"E2847"),sQuery(id+"F0.wireOp",EDGE,"E2848"),sQuery(id+"F0.wireOp",EDGE,"E2849"),sQuery(id+"F0.wireOp",EDGE,"E2850"),sQuery(id+"F0.wireOp",EDGE,"E2851"),sQuery(id+"F0.wireOp",EDGE,"E2852"),sQuery(id+"F0.wireOp",EDGE,"E2853"),sQuery(id+"F0.wireOp",EDGE,"E2854"),sQuery(id+"F0.wireOp",EDGE,"E2855"),sQuery(id+"F0.wireOp",EDGE,"E2856"),sQuery(id+"F0.wireOp",EDGE,"E2857"),sQuery(id+"F0.wireOp",EDGE,"E2858"),sQuery(id+"F0.wireOp",EDGE,"E2859"),sQuery(id+"F0.wireOp",EDGE,"E2860"),sQuery(id+"F0.wireOp",EDGE,"E2861"),sQuery(id+"F0.wireOp",EDGE,"E2862"),sQuery(id+"F0.wireOp",EDGE,"E2863"),sQuery(id+"F0.wireOp",EDGE,"E2864"),sQuery(id+"F0.wireOp",EDGE,"E2865"),sQuery(id+"F0.wireOp",EDGE,"E2866"),sQuery(id+"F0.wireOp",EDGE,"E2867"),sQuery(id+"F0.wireOp",EDGE,"E2868"),sQuery(id+"F0.wireOp",EDGE,"E2869"),sQuery(id+"F0.wireOp",EDGE,"E2870"),sQuery(id+"F0.wireOp",EDGE,"E2871"),sQuery(id+"F0.wireOp",EDGE,"E2872"),sQuery(id+"F0.wireOp",EDGE,"E2873"),sQuery(id+"F0.wireOp",EDGE,"E2874"),sQuery(id+"F0.wireOp",EDGE,"E2875"),sQuery(id+"F0.wireOp",EDGE,"E2876"),sQuery(id+"F0.wireOp",EDGE,"E2877"),sQuery(id+"F0.wireOp",EDGE,"E2878"),sQuery(id+"F0.wireOp",EDGE,"E2879"),sQuery(id+"F0.wireOp",EDGE,"E2880"),sQuery(id+"F0.wireOp",EDGE,"E2881"),sQuery(id+"F0.wireOp",EDGE,"E2882"),sQuery(id+"F0.wireOp",EDGE,"E2883"),sQuery(id+"F0.wireOp",EDGE,"E2884"),sQuery(id+"F0.wireOp",EDGE,"E2885"),sQuery(id+"F0.wireOp",EDGE,"E2886"),sQuery(id+"F0.wireOp",EDGE,"E2887"),sQuery(id+"F0.wireOp",EDGE,"E2888"),sQuery(id+"F0.wireOp",EDGE,"E2889"),sQuery(id+"F0.wireOp",EDGE,"E2890"),sQuery(id+"F0.wireOp",EDGE,"E2891"),sQuery(id+"F0.wireOp",EDGE,"E2892"),sQuery(id+"F0.wireOp",EDGE,"E2893"),sQuery(id+"F0.wireOp",EDGE,"E2894"),sQuery(id+"F0.wireOp",EDGE,"E2895"),sQuery(id+"F0.wireOp",EDGE,"E2896"),sQuery(id+"F0.wireOp",EDGE,"E2897"),sQuery(id+"F0.wireOp",EDGE,"E2898"),sQuery(id+"F0.wireOp",EDGE,"E2899"),sQuery(id+"F0.wireOp",EDGE,"E2900"),sQuery(id+"F0.wireOp",EDGE,"E2901"),sQuery(id+"F0.wireOp",EDGE,"E2902"),sQuery(id+"F0.wireOp",EDGE,"E2903"),sQuery(id+"F0.wireOp",EDGE,"E2904"),sQuery(id+"F0.wireOp",EDGE,"E2905"),sQuery(id+"F0.wireOp",EDGE,"E2906"),sQuery(id+"F0.wireOp",EDGE,"E2907"),sQuery(id+"F0.wireOp",EDGE,"E2908"),sQuery(id+"F0.wireOp",EDGE,"E2909"),sQuery(id+"F0.wireOp",EDGE,"E2910"),sQuery(id+"F0.wireOp",EDGE,"E2911"),sQuery(id+"F0.wireOp",EDGE,"E2912"),sQuery(id+"F0.wireOp",EDGE,"E2913"),sQuery(id+"F0.wireOp",EDGE,"E2914"),sQuery(id+"F0.wireOp",EDGE,"E2915"),sQuery(id+"F0.wireOp",EDGE,"E2916"),sQuery(id+"F0.wireOp",EDGE,"E2917"),sQuery(id+"F0.wireOp",EDGE,"E2918"),sQuery(id+"F0.wireOp",EDGE,"E2919"),sQuery(id+"F0.wireOp",EDGE,"E2920"),sQuery(id+"F0.wireOp",EDGE,"E2921"),sQuery(id+"F0.wireOp",EDGE,"E2922"),sQuery(id+"F0.wireOp",EDGE,"E2923"),sQuery(id+"F0.wireOp",EDGE,"E2924"),sQuery(id+"F0.wireOp",EDGE,"E2925"),sQuery(id+"F0.wireOp",EDGE,"E2926"),sQuery(id+"F0.wireOp",EDGE,"E2927"),sQuery(id+"F0.wireOp",EDGE,"E2928"),sQuery(id+"F0.wireOp",EDGE,"E2929"),sQuery(id+"F0.wireOp",EDGE,"E2930"),sQuery(id+"F0.wireOp",EDGE,"E2931"),sQuery(id+"F0.wireOp",EDGE,"E2932"),sQuery(id+"F0.wireOp",EDGE,"E2933"),sQuery(id+"F0.wireOp",EDGE,"E2934"),sQuery(id+"F0.wireOp",EDGE,"E2935"),sQuery(id+"F0.wireOp",EDGE,"E2936"),sQuery(id+"F0.wireOp",EDGE,"E2937"),sQuery(id+"F0.wireOp",EDGE,"E2938"),sQuery(id+"F0.wireOp",EDGE,"E2939"),sQuery(id+"F0.wireOp",EDGE,"E2940"),sQuery(id+"F0.wireOp",EDGE,"E2941"),sQuery(id+"F0.wireOp",EDGE,"E2942"),sQuery(id+"F0.wireOp",EDGE,"E2943"),sQuery(id+"F0.wireOp",EDGE,"E2944"),sQuery(id+"F0.wireOp",EDGE,"E2945"),sQuery(id+"F0.wireOp",EDGE,"E2946"),sQuery(id+"F0.wireOp",EDGE,"E2947"),sQuery(id+"F0.wireOp",EDGE,"E2948"),sQuery(id+"F0.wireOp",EDGE,"E2949"),sQuery(id+"F0.wireOp",EDGE,"E2950"),sQuery(id+"F0.wireOp",EDGE,"E2951"),sQuery(id+"F0.wireOp",EDGE,"E2952"),sQuery(id+"F0.wireOp",EDGE,"E2953"),sQuery(id+"F0.wireOp",EDGE,"E2954"),sQuery(id+"F0.wireOp",EDGE,"E2955"),sQuery(id+"F0.wireOp",EDGE,"E2956"),sQuery(id+"F0.wireOp",EDGE,"E2957"),sQuery(id+"F0.wireOp",EDGE,"E2958"),sQuery(id+"F0.wireOp",EDGE,"E2959"),sQuery(id+"F0.wireOp",EDGE,"E2960"),sQuery(id+"F0.wireOp",EDGE,"E2961"),sQuery(id+"F0.wireOp",EDGE,"E2962"),sQuery(id+"F0.wireOp",EDGE,"E2963"),sQuery(id+"F0.wireOp",EDGE,"E2964"),sQuery(id+"F0.wireOp",EDGE,"E2965"),sQuery(id+"F0.wireOp",EDGE,"E2966"),sQuery(id+"F0.wireOp",EDGE,"E2967"),sQuery(id+"F0.wireOp",EDGE,"E2968"),sQuery(id+"F0.wireOp",EDGE,"E2969"),sQuery(id+"F0.wireOp",EDGE,"E2970"),sQuery(id+"F0.wireOp",EDGE,"E2971"),sQuery(id+"F0.wireOp",EDGE,"E2972"),sQuery(id+"F0.wireOp",EDGE,"E2973"),sQuery(id+"F0.wireOp",EDGE,"E2974"),sQuery(id+"F0.wireOp",EDGE,"E2975"),sQuery(id+"F0.wireOp",EDGE,"E2976"),sQuery(id+"F0.wireOp",EDGE,"E2977"),sQuery(id+"F0.wireOp",EDGE,"E2978"),sQuery(id+"F0.wireOp",EDGE,"E2979"),sQuery(id+"F0.wireOp",EDGE,"E2980"),sQuery(id+"F0.wireOp",EDGE,"E2981"),sQuery(id+"F0.wireOp",EDGE,"E2982"),sQuery(id+"F0.wireOp",EDGE,"E2983"),sQuery(id+"F0.wireOp",EDGE,"E2984"),sQuery(id+"F0.wireOp",EDGE,"E2985"),sQuery(id+"F0.wireOp",EDGE,"E2986"),sQuery(id+"F0.wireOp",EDGE,"E2987"),sQuery(id+"F0.wireOp",EDGE,"E2988"),sQuery(id+"F0.wireOp",EDGE,"E2989"),sQuery(id+"F0.wireOp",EDGE,"E2990"),sQuery(id+"F0.wireOp",EDGE,"E2991"),sQuery(id+"F0.wireOp",EDGE,"E2992"),sQuery(id+"F0.wireOp",EDGE,"E2993"),sQuery(id+"F0.wireOp",EDGE,"E2994"),sQuery(id+"F0.wireOp",EDGE,"E2995"),sQuery(id+"F0.wireOp",EDGE,"E2996"),sQuery(id+"F0.wireOp",EDGE,"E2997"),sQuery(id+"F0.wireOp",EDGE,"E2998"),sQuery(id+"F0.wireOp",EDGE,"E2999"),sQuery(id+"F0.wireOp",EDGE,"E3000"),sQuery(id+"F0.wireOp",EDGE,"E3001"),sQuery(id+"F0.wireOp",EDGE,"E3002"),sQuery(id+"F0.wireOp",EDGE,"E3003"),sQuery(id+"F0.wireOp",EDGE,"E3004"),sQuery(id+"F0.wireOp",EDGE,"E3005"),sQuery(id+"F0.wireOp",EDGE,"E3006"),sQuery(id+"F0.wireOp",EDGE,"E3007"),sQuery(id+"F0.wireOp",EDGE,"E3008"),sQuery(id+"F0.wireOp",EDGE,"E3009"),sQuery(id+"F0.wireOp",EDGE,"E3010"),sQuery(id+"F0.wireOp",EDGE,"E3011"),sQuery(id+"F0.wireOp",EDGE,"E3012"),sQuery(id+"F0.wireOp",EDGE,"E3013"),sQuery(id+"F0.wireOp",EDGE,"E3014"),sQuery(id+"F0.wireOp",EDGE,"E3015"),sQuery(id+"F0.wireOp",EDGE,"E3016"),sQuery(id+"F0.wireOp",EDGE,"E3017"),sQuery(id+"F0.wireOp",EDGE,"E3018"),sQuery(id+"F0.wireOp",EDGE,"E3019"),sQuery(id+"F0.wireOp",EDGE,"E3020"),sQuery(id+"F0.wireOp",EDGE,"E3021"),sQuery(id+"F0.wireOp",EDGE,"E3022"),sQuery(id+"F0.wireOp",EDGE,"E3023"),sQuery(id+"F0.wireOp",EDGE,"E3024"),sQuery(id+"F0.wireOp",EDGE,"E3025"),sQuery(id+"F0.wireOp",EDGE,"E3026"),sQuery(id+"F0.wireOp",EDGE,"E3027"),sQuery(id+"F0.wireOp",EDGE,"E3028"),sQuery(id+"F0.wireOp",EDGE,"E3029"),sQuery(id+"F0.wireOp",EDGE,"E3030"),sQuery(id+"F0.wireOp",EDGE,"E3031"),sQuery(id+"F0.wireOp",EDGE,"E3032"),sQuery(id+"F0.wireOp",EDGE,"E3033"),sQuery(id+"F0.wireOp",EDGE,"E3034"),sQuery(id+"F0.wireOp",EDGE,"E3035"),sQuery(id+"F0.wireOp",EDGE,"E3036"),sQuery(id+"F0.wireOp",EDGE,"E3037"),sQuery(id+"F0.wireOp",EDGE,"E3038"),sQuery(id+"F0.wireOp",EDGE,"E3039"),sQuery(id+"F0.wireOp",EDGE,"E3040"),sQuery(id+"F0.wireOp",EDGE,"E3041"),sQuery(id+"F0.wireOp",EDGE,"E3042"),sQuery(id+"F0.wireOp",EDGE,"E3043"),sQuery(id+"F0.wireOp",EDGE,"E3044"),sQuery(id+"F0.wireOp",EDGE,"E3045"),sQuery(id+"F0.wireOp",EDGE,"E3046"),sQuery(id+"F0.wireOp",EDGE,"E3047"),sQuery(id+"F0.wireOp",EDGE,"E3048"),sQuery(id+"F0.wireOp",EDGE,"E3049"),sQuery(id+"F0.wireOp",EDGE,"E3050"),sQuery(id+"F0.wireOp",EDGE,"E3051"),sQuery(id+"F0.wireOp",EDGE,"E3052"),sQuery(id+"F0.wireOp",EDGE,"E3053"),sQuery(id+"F0.wireOp",EDGE,"E3054"),sQuery(id+"F0.wireOp",EDGE,"E3055"),sQuery(id+"F0.wireOp",EDGE,"E3056"),sQuery(id+"F0.wireOp",EDGE,"E3057"),sQuery(id+"F0.wireOp",EDGE,"E3058"),sQuery(id+"F0.wireOp",EDGE,"E3059"),sQuery(id+"F0.wireOp",EDGE,"E3060"),sQuery(id+"F0.wireOp",EDGE,"E3061"),sQuery(id+"F0.wireOp",EDGE,"E3062"),sQuery(id+"F0.wireOp",EDGE,"E3063"),sQuery(id+"F0.wireOp",EDGE,"E3064"),sQuery(id+"F0.wireOp",EDGE,"E3065"),sQuery(id+"F0.wireOp",EDGE,"E3066"),sQuery(id+"F0.wireOp",EDGE,"E3067"),sQuery(id+"F0.wireOp",EDGE,"E3068"),sQuery(id+"F0.wireOp",EDGE,"E3069"),sQuery(id+"F0.wireOp",EDGE,"E3070"),sQuery(id+"F0.wireOp",EDGE,"E3071"),sQuery(id+"F0.wireOp",EDGE,"E3072"),sQuery(id+"F0.wireOp",EDGE,"E3073"),sQuery(id+"F0.wireOp",EDGE,"E3074"),sQuery(id+"F0.wireOp",EDGE,"E3075"),sQuery(id+"F0.wireOp",EDGE,"E3076"),sQuery(id+"F0.wireOp",EDGE,"E3077"),sQuery(id+"F0.wireOp",EDGE,"E3078"),sQuery(id+"F0.wireOp",EDGE,"E3079"),sQuery(id+"F0.wireOp",EDGE,"E3080"),sQuery(id+"F0.wireOp",EDGE,"E3081"),sQuery(id+"F0.wireOp",EDGE,"E3082"),sQuery(id+"F0.wireOp",EDGE,"E3083"),sQuery(id+"F0.wireOp",EDGE,"E3084"),sQuery(id+"F0.wireOp",EDGE,"E3085"),sQuery(id+"F0.wireOp",EDGE,"E3086"),sQuery(id+"F0.wireOp",EDGE,"E3087"),sQuery(id+"F0.wireOp",EDGE,"E3088"),sQuery(id+"F0.wireOp",EDGE,"E3089"),sQuery(id+"F0.wireOp",EDGE,"E3090"),sQuery(id+"F0.wireOp",EDGE,"E3091"),sQuery(id+"F0.wireOp",EDGE,"E3092"),sQuery(id+"F0.wireOp",EDGE,"E3093"),sQuery(id+"F0.wireOp",EDGE,"E3094"),sQuery(id+"F0.wireOp",EDGE,"E3095"),sQuery(id+"F0.wireOp",EDGE,"E3096"),sQuery(id+"F0.wireOp",EDGE,"E3097"),sQuery(id+"F0.wireOp",EDGE,"E3098"),sQuery(id+"F0.wireOp",EDGE,"E3099"),sQuery(id+"F0.wireOp",EDGE,"E3100"),sQuery(id+"F0.wireOp",EDGE,"E3101"),sQuery(id+"F0.wireOp",EDGE,"E3102"),sQuery(id+"F0.wireOp",EDGE,"E3103"),sQuery(id+"F0.wireOp",EDGE,"E3104"),sQuery(id+"F0.wireOp",EDGE,"E3105"),sQuery(id+"F0.wireOp",EDGE,"E3106"),sQuery(id+"F0.wireOp",EDGE,"E3107"),sQuery(id+"F0.wireOp",EDGE,"E3108"),sQuery(id+"F0.wireOp",EDGE,"E3109"),sQuery(id+"F0.wireOp",EDGE,"E3110"),sQuery(id+"F0.wireOp",EDGE,"E3111"),sQuery(id+"F0.wireOp",EDGE,"E3112"),sQuery(id+"F0.wireOp",EDGE,"E3113"),sQuery(id+"F0.wireOp",EDGE,"E3114"),sQuery(id+"F0.wireOp",EDGE,"E3115"),sQuery(id+"F0.wireOp",EDGE,"E3116"),sQuery(id+"F0.wireOp",EDGE,"E3117"),sQuery(id+"F0.wireOp",EDGE,"E3118"),sQuery(id+"F0.wireOp",EDGE,"E3119"),sQuery(id+"F0.wireOp",EDGE,"E3120"),sQuery(id+"F0.wireOp",EDGE,"E3121"),sQuery(id+"F0.wireOp",EDGE,"E3122"),sQuery(id+"F0.wireOp",EDGE,"E3123"),sQuery(id+"F0.wireOp",EDGE,"E3124"),sQuery(id+"F0.wireOp",EDGE,"E3125"),sQuery(id+"F0.wireOp",EDGE,"E3126"),sQuery(id+"F0.wireOp",EDGE,"E3127"),sQuery(id+"F0.wireOp",EDGE,"E3128"),sQuery(id+"F0.wireOp",EDGE,"E3129"),sQuery(id+"F0.wireOp",EDGE,"E3130"),sQuery(id+"F0.wireOp",EDGE,"E3131"),sQuery(id+"F0.wireOp",EDGE,"E3132"),sQuery(id+"F0.wireOp",EDGE,"E3133"),sQuery(id+"F0.wireOp",EDGE,"E3134"),sQuery(id+"F0.wireOp",EDGE,"E3135"),sQuery(id+"F0.wireOp",EDGE,"E3136"),sQuery(id+"F0.wireOp",EDGE,"E3137"),sQuery(id+"F0.wireOp",EDGE,"E3138"),sQuery(id+"F0.wireOp",EDGE,"E3139"),sQuery(id+"F0.wireOp",EDGE,"E3140"),sQuery(id+"F0.wireOp",EDGE,"E3141"),sQuery(id+"F0.wireOp",EDGE,"E3142"),sQuery(id+"F0.wireOp",EDGE,"E3143"),sQuery(id+"F0.wireOp",EDGE,"E3144"),sQuery(id+"F0.wireOp",EDGE,"E3145"),sQuery(id+"F0.wireOp",EDGE,"E3146"),sQuery(id+"F0.wireOp",EDGE,"E3147"),sQuery(id+"F0.wireOp",EDGE,"E3148"),sQuery(id+"F0.wireOp",EDGE,"E3149"),sQuery(id+"F0.wireOp",EDGE,"E3150"),sQuery(id+"F0.wireOp",EDGE,"E3151"),sQuery(id+"F0.wireOp",EDGE,"E3152"),sQuery(id+"F0.wireOp",EDGE,"E3153"),sQuery(id+"F0.wireOp",EDGE,"E3154"),sQuery(id+"F0.wireOp",EDGE,"E3155"),sQuery(id+"F0.wireOp",EDGE,"E3156"),sQuery(id+"F0.wireOp",EDGE,"E3157"),sQuery(id+"F0.wireOp",EDGE,"E3158"),sQuery(id+"F0.wireOp",EDGE,"E3159"),sQuery(id+"F0.wireOp",EDGE,"E3160"),sQuery(id+"F0.wireOp",EDGE,"E3161"),sQuery(id+"F0.wireOp",EDGE,"E3162"),sQuery(id+"F0.wireOp",EDGE,"E3163"),sQuery(id+"F0.wireOp",EDGE,"E3164"),sQuery(id+"F0.wireOp",EDGE,"E3165"),sQuery(id+"F0.wireOp",EDGE,"E3166"),sQuery(id+"F0.wireOp",EDGE,"E3167"),sQuery(id+"F0.wireOp",EDGE,"E3168"),sQuery(id+"F0.wireOp",EDGE,"E3169"),sQuery(id+"F0.wireOp",EDGE,"E3170"),sQuery(id+"F0.wireOp",EDGE,"E3171"),sQuery(id+"F0.wireOp",EDGE,"E3172"),sQuery(id+"F0.wireOp",EDGE,"E3173"),sQuery(id+"F0.wireOp",EDGE,"E3174"),sQuery(id+"F0.wireOp",EDGE,"E3175"),sQuery(id+"F0.wireOp",EDGE,"E3176"),sQuery(id+"F0.wireOp",EDGE,"E3177"),sQuery(id+"F0.wireOp",EDGE,"E3178"),sQuery(id+"F0.wireOp",EDGE,"E3179"),sQuery(id+"F0.wireOp",EDGE,"E3180"),sQuery(id+"F0.wireOp",EDGE,"E3181"),sQuery(id+"F0.wireOp",EDGE,"E3182"),sQuery(id+"F0.wireOp",EDGE,"E3183"),sQuery(id+"F0.wireOp",EDGE,"E3184"),sQuery(id+"F0.wireOp",EDGE,"E3185"),sQuery(id+"F0.wireOp",EDGE,"E3186"),sQuery(id+"F0.wireOp",EDGE,"E3187"),sQuery(id+"F0.wireOp",EDGE,"E3188"),sQuery(id+"F0.wireOp",EDGE,"E3189"),sQuery(id+"F0.wireOp",EDGE,"E3190"),sQuery(id+"F0.wireOp",EDGE,"E3191"),sQuery(id+"F0.wireOp",EDGE,"E3192"),sQuery(id+"F0.wireOp",EDGE,"E3193"),sQuery(id+"F0.wireOp",EDGE,"E3194"),sQuery(id+"F0.wireOp",EDGE,"E3195"),sQuery(id+"F0.wireOp",EDGE,"E3196"),sQuery(id+"F0.wireOp",EDGE,"E3197"),sQuery(id+"F0.wireOp",EDGE,"E3198"),sQuery(id+"F0.wireOp",EDGE,"E3199"),sQuery(id+"F0.wireOp",EDGE,"E3200"),sQuery(id+"F0.wireOp",EDGE,"E3201"),sQuery(id+"F0.wireOp",EDGE,"E3202"),sQuery(id+"F0.wireOp",EDGE,"E3203"),sQuery(id+"F0.wireOp",EDGE,"E3204"),sQuery(id+"F0.wireOp",EDGE,"E3205"),sQuery(id+"F0.wireOp",EDGE,"E3206"),sQuery(id+"F0.wireOp",EDGE,"E3207"),sQuery(id+"F0.wireOp",EDGE,"E3208"),sQuery(id+"F0.wireOp",EDGE,"E3209"),sQuery(id+"F0.wireOp",EDGE,"E3210"),sQuery(id+"F0.wireOp",EDGE,"E3211"),sQuery(id+"F0.wireOp",EDGE,"E3212"),sQuery(id+"F0.wireOp",EDGE,"E3213"),sQuery(id+"F0.wireOp",EDGE,"E3214"),sQuery(id+"F0.wireOp",EDGE,"E3215"),sQuery(id+"F0.wireOp",EDGE,"E3216"),sQuery(id+"F0.wireOp",EDGE,"E3217"),sQuery(id+"F0.wireOp",EDGE,"E3218"),sQuery(id+"F0.wireOp",EDGE,"E3219"),sQuery(id+"F0.wireOp",EDGE,"E3220"),sQuery(id+"F0.wireOp",EDGE,"E3221"),sQuery(id+"F0.wireOp",EDGE,"E3222"),sQuery(id+"F0.wireOp",EDGE,"E3223"),sQuery(id+"F0.wireOp",EDGE,"E3224"),sQuery(id+"F0.wireOp",EDGE,"E3225"),sQuery(id+"F0.wireOp",EDGE,"E3226"),sQuery(id+"F0.wireOp",EDGE,"E3227"),sQuery(id+"F0.wireOp",EDGE,"E3228"),sQuery(id+"F0.wireOp",EDGE,"E3229"),sQuery(id+"F0.wireOp",EDGE,"E3230"),sQuery(id+"F0.wireOp",EDGE,"E3231"),sQuery(id+"F0.wireOp",EDGE,"E3232"),sQuery(id+"F0.wireOp",EDGE,"E3233"),sQuery(id+"F0.wireOp",EDGE,"E3234"),sQuery(id+"F0.wireOp",EDGE,"E3235"),sQuery(id+"F0.wireOp",EDGE,"E3236"),sQuery(id+"F0.wireOp",EDGE,"E3237"),sQuery(id+"F0.wireOp",EDGE,"E3238"),sQuery(id+"F0.wireOp",EDGE,"E3239"),sQuery(id+"F0.wireOp",EDGE,"E3240"),sQuery(id+"F0.wireOp",EDGE,"E3241"),sQuery(id+"F0.wireOp",EDGE,"E3242"),sQuery(id+"F0.wireOp",EDGE,"E3243"),sQuery(id+"F0.wireOp",EDGE,"E3244"),sQuery(id+"F0.wireOp",EDGE,"E3245"),sQuery(id+"F0.wireOp",EDGE,"E3246"),sQuery(id+"F0.wireOp",EDGE,"E3247"),sQuery(id+"F0.wireOp",EDGE,"E3248"),sQuery(id+"F0.wireOp",EDGE,"E3249"),sQuery(id+"F0.wireOp",EDGE,"E3250"),sQuery(id+"F0.wireOp",EDGE,"E3251"),sQuery(id+"F0.wireOp",EDGE,"E3252"),sQuery(id+"F0.wireOp",EDGE,"E3253"),sQuery(id+"F0.wireOp",EDGE,"E3254"),sQuery(id+"F0.wireOp",EDGE,"E3255"),sQuery(id+"F0.wireOp",EDGE,"E3256"),sQuery(id+"F0.wireOp",EDGE,"E3257"),sQuery(id+"F0.wireOp",EDGE,"E3258"),sQuery(id+"F0.wireOp",EDGE,"E3259"),sQuery(id+"F0.wireOp",EDGE,"E3260"),sQuery(id+"F0.wireOp",EDGE,"E3261"),sQuery(id+"F0.wireOp",EDGE,"E3262"),sQuery(id+"F0.wireOp",EDGE,"E3263"),sQuery(id+"F0.wireOp",EDGE,"E3264"),sQuery(id+"F0.wireOp",EDGE,"E3265"),sQuery(id+"F0.wireOp",EDGE,"E3266"),sQuery(id+"F0.wireOp",EDGE,"E3267"),sQuery(id+"F0.wireOp",EDGE,"E3268"),sQuery(id+"F0.wireOp",EDGE,"E3269"),sQuery(id+"F0.wireOp",EDGE,"E3270"),sQuery(id+"F0.wireOp",EDGE,"E3271"),sQuery(id+"F0.wireOp",EDGE,"E3272"),sQuery(id+"F0.wireOp",EDGE,"E3273"),sQuery(id+"F0.wireOp",EDGE,"E3274"),sQuery(id+"F0.wireOp",EDGE,"E3275"),sQuery(id+"F0.wireOp",EDGE,"E3276"),sQuery(id+"F0.wireOp",EDGE,"E3277"),sQuery(id+"F0.wireOp",EDGE,"E3278"),sQuery(id+"F0.wireOp",EDGE,"E3279"),sQuery(id+"F0.wireOp",EDGE,"E3280"),sQuery(id+"F0.wireOp",EDGE,"E3281"),sQuery(id+"F0.wireOp",EDGE,"E3282"),sQuery(id+"F0.wireOp",EDGE,"E3283"),sQuery(id+"F0.wireOp",EDGE,"E3284"),sQuery(id+"F0.wireOp",EDGE,"E3285"),sQuery(id+"F0.wireOp",EDGE,"E3286"),sQuery(id+"F0.wireOp",EDGE,"E3287"),sQuery(id+"F0.wireOp",EDGE,"E3288"),sQuery(id+"F0.wireOp",EDGE,"E3289"),sQuery(id+"F0.wireOp",EDGE,"E3290"),sQuery(id+"F0.wireOp",EDGE,"E3291"),sQuery(id+"F0.wireOp",EDGE,"E3292"),sQuery(id+"F0.wireOp",EDGE,"E3293"),sQuery(id+"F0.wireOp",EDGE,"E3294"),sQuery(id+"F0.wireOp",EDGE,"E3295"),sQuery(id+"F0.wireOp",EDGE,"E3296"),sQuery(id+"F0.wireOp",EDGE,"E3297"),sQuery(id+"F0.wireOp",EDGE,"E3298"),sQuery(id+"F0.wireOp",EDGE,"E3299"),sQuery(id+"F0.wireOp",EDGE,"E3300"),sQuery(id+"F0.wireOp",EDGE,"E3301"),sQuery(id+"F0.wireOp",EDGE,"E3302"),sQuery(id+"F0.wireOp",EDGE,"E3303"),sQuery(id+"F0.wireOp",EDGE,"E3304"),sQuery(id+"F0.wireOp",EDGE,"E3305"),sQuery(id+"F0.wireOp",EDGE,"E3306"),sQuery(id+"F0.wireOp",EDGE,"E3307"),sQuery(id+"F0.wireOp",EDGE,"E3308"),sQuery(id+"F0.wireOp",EDGE,"E3309"),sQuery(id+"F0.wireOp",EDGE,"E3310"),sQuery(id+"F0.wireOp",EDGE,"E3311"),sQuery(id+"F0.wireOp",EDGE,"E3312"),sQuery(id+"F0.wireOp",EDGE,"E3313"),sQuery(id+"F0.wireOp",EDGE,"E3314"),sQuery(id+"F0.wireOp",EDGE,"E3315"),sQuery(id+"F0.wireOp",EDGE,"E3316"),sQuery(id+"F0.wireOp",EDGE,"E3317"),sQuery(id+"F0.wireOp",EDGE,"E3318"),sQuery(id+"F0.wireOp",EDGE,"E3319"),sQuery(id+"F0.wireOp",EDGE,"E3320"),sQuery(id+"F0.wireOp",EDGE,"E3321"),sQuery(id+"F0.wireOp",EDGE,"E3322"),sQuery(id+"F0.wireOp",EDGE,"E3323"),sQuery(id+"F0.wireOp",EDGE,"E3324"),sQuery(id+"F0.wireOp",EDGE,"E3325"),sQuery(id+"F0.wireOp",EDGE,"E3326"),sQuery(id+"F0.wireOp",EDGE,"E3327"),sQuery(id+"F0.wireOp",EDGE,"E3328"),sQuery(id+"F0.wireOp",EDGE,"E3329"),sQuery(id+"F0.wireOp",EDGE,"E3330"),sQuery(id+"F0.wireOp",EDGE,"E3331"),sQuery(id+"F0.wireOp",EDGE,"E3332"),sQuery(id+"F0.wireOp",EDGE,"E3333"),sQuery(id+"F0.wireOp",EDGE,"E3334"),sQuery(id+"F0.wireOp",EDGE,"E3335"),sQuery(id+"F0.wireOp",EDGE,"E3336"),sQuery(id+"F0.wireOp",EDGE,"E3337"),sQuery(id+"F0.wireOp",EDGE,"E3338"),sQuery(id+"F0.wireOp",EDGE,"E3339"),sQuery(id+"F0.wireOp",EDGE,"E3340"),sQuery(id+"F0.wireOp",EDGE,"E3341"),sQuery(id+"F0.wireOp",EDGE,"E3342"),sQuery(id+"F0.wireOp",EDGE,"E3343"),sQuery(id+"F0.wireOp",EDGE,"E3344"),sQuery(id+"F0.wireOp",EDGE,"E3345"),sQuery(id+"F0.wireOp",EDGE,"E3346"),sQuery(id+"F0.wireOp",EDGE,"E3347"),sQuery(id+"F0.wireOp",EDGE,"E3348"),sQuery(id+"F0.wireOp",EDGE,"E3349"),sQuery(id+"F0.wireOp",EDGE,"E3350"),sQuery(id+"F0.wireOp",EDGE,"E3351"),sQuery(id+"F0.wireOp",EDGE,"E3352"),sQuery(id+"F0.wireOp",EDGE,"E3353"),sQuery(id+"F0.wireOp",EDGE,"E3354"),sQuery(id+"F0.wireOp",EDGE,"E3355"),sQuery(id+"F0.wireOp",EDGE,"E3356"),sQuery(id+"F0.wireOp",EDGE,"E3357"),sQuery(id+"F0.wireOp",EDGE,"E3358"),sQuery(id+"F0.wireOp",EDGE,"E3359"),sQuery(id+"F0.wireOp",EDGE,"E3360"),sQuery(id+"F0.wireOp",EDGE,"E3361"),sQuery(id+"F0.wireOp",EDGE,"E3362"),sQuery(id+"F0.wireOp",EDGE,"E3363"),sQuery(id+"F0.wireOp",EDGE,"E3364"),sQuery(id+"F0.wireOp",EDGE,"E3365"),sQuery(id+"F0.wireOp",EDGE,"E3366"),sQuery(id+"F0.wireOp",EDGE,"E3367"),sQuery(id+"F0.wireOp",EDGE,"E3368"),sQuery(id+"F0.wireOp",EDGE,"E3369"),sQuery(id+"F0.wireOp",EDGE,"E3370"),sQuery(id+"F0.wireOp",EDGE,"E3371"),sQuery(id+"F0.wireOp",EDGE,"E3372"),sQuery(id+"F0.wireOp",EDGE,"E3373"),sQuery(id+"F0.wireOp",EDGE,"E3374"),sQuery(id+"F0.wireOp",EDGE,"E3375"),sQuery(id+"F0.wireOp",EDGE,"E3376"),sQuery(id+"F0.wireOp",EDGE,"E3377"),sQuery(id+"F0.wireOp",EDGE,"E3378"),sQuery(id+"F0.wireOp",EDGE,"E3379"),sQuery(id+"F0.wireOp",EDGE,"E3380"),sQuery(id+"F0.wireOp",EDGE,"E3381"),sQuery(id+"F0.wireOp",EDGE,"E3382"),sQuery(id+"F0.wireOp",EDGE,"E3383"),sQuery(id+"F0.wireOp",EDGE,"E3384"),sQuery(id+"F0.wireOp",EDGE,"E3385"),sQuery(id+"F0.wireOp",EDGE,"E3386"),sQuery(id+"F0.wireOp",EDGE,"E3387"),sQuery(id+"F0.wireOp",EDGE,"E3388"),sQuery(id+"F0.wireOp",EDGE,"E3389"),sQuery(id+"F0.wireOp",EDGE,"E3390"),sQuery(id+"F0.wireOp",EDGE,"E3391"),sQuery(id+"F0.wireOp",EDGE,"E3392"),sQuery(id+"F0.wireOp",EDGE,"E3393"),sQuery(id+"F0.wireOp",EDGE,"E3394"),sQuery(id+"F0.wireOp",EDGE,"E3395"),sQuery(id+"F0.wireOp",EDGE,"E3396"),sQuery(id+"F0.wireOp",EDGE,"E3397"),sQuery(id+"F0.wireOp",EDGE,"E3398"),sQuery(id+"F0.wireOp",EDGE,"E3399"),sQuery(id+"F0.wireOp",EDGE,"E3400"),sQuery(id+"F0.wireOp",EDGE,"E3401"),sQuery(id+"F0.wireOp",EDGE,"E3402"),sQuery(id+"F0.wireOp",EDGE,"E3403"),sQuery(id+"F0.wireOp",EDGE,"E3404"),sQuery(id+"F0.wireOp",EDGE,"E3405"),sQuery(id+"F0.wireOp",EDGE,"E3406"),sQuery(id+"F0.wireOp",EDGE,"E3407"),sQuery(id+"F0.wireOp",EDGE,"E3408"),sQuery(id+"F0.wireOp",EDGE,"E3409"),sQuery(id+"F0.wireOp",EDGE,"E3410"),sQuery(id+"F0.wireOp",EDGE,"E3411"),sQuery(id+"F0.wireOp",EDGE,"E3412"),sQuery(id+"F0.wireOp",EDGE,"E3413"),sQuery(id+"F0.wireOp",EDGE,"E3414"),sQuery(id+"F0.wireOp",EDGE,"E3415"),sQuery(id+"F0.wireOp",EDGE,"E3416"),sQuery(id+"F0.wireOp",EDGE,"E3417"),sQuery(id+"F0.wireOp",EDGE,"E3418"),sQuery(id+"F0.wireOp",EDGE,"E3419"),sQuery(id+"F0.wireOp",EDGE,"E3420"),sQuery(id+"F0.wireOp",EDGE,"E3421"),sQuery(id+"F0.wireOp",EDGE,"E3422"),sQuery(id+"F0.wireOp",EDGE,"E3423"),sQuery(id+"F0.wireOp",EDGE,"E3424"),sQuery(id+"F0.wireOp",EDGE,"E3425"),sQuery(id+"F0.wireOp",EDGE,"E3426"),sQuery(id+"F0.wireOp",EDGE,"E3427"),sQuery(id+"F0.wireOp",EDGE,"E3428"),sQuery(id+"F0.wireOp",EDGE,"E3429"),sQuery(id+"F0.wireOp",EDGE,"E3430"),sQuery(id+"F0.wireOp",EDGE,"E3431"),sQuery(id+"F0.wireOp",EDGE,"E3432"),sQuery(id+"F0.wireOp",EDGE,"E3433"),sQuery(id+"F0.wireOp",EDGE,"E3434"),sQuery(id+"F0.wireOp",EDGE,"E3435"),sQuery(id+"F0.wireOp",EDGE,"E3436"),sQuery(id+"F0.wireOp",EDGE,"E3437"),sQuery(id+"F0.wireOp",EDGE,"E3438"),sQuery(id+"F0.wireOp",EDGE,"E3439"),sQuery(id+"F0.wireOp",EDGE,"E3440"),sQuery(id+"F0.wireOp",EDGE,"E3441"),sQuery(id+"F0.wireOp",EDGE,"E3442"),sQuery(id+"F0.wireOp",EDGE,"E3443"),sQuery(id+"F0.wireOp",EDGE,"E3444"),sQuery(id+"F0.wireOp",EDGE,"E3445"),sQuery(id+"F0.wireOp",EDGE,"E3446"),sQuery(id+"F0.wireOp",EDGE,"E3447"),sQuery(id+"F0.wireOp",EDGE,"E3448"),sQuery(id+"F0.wireOp",EDGE,"E3449"),sQuery(id+"F0.wireOp",EDGE,"E3450"),sQuery(id+"F0.wireOp",EDGE,"E3451"),sQuery(id+"F0.wireOp",EDGE,"E3452"),sQuery(id+"F0.wireOp",EDGE,"E3453"),sQuery(id+"F0.wireOp",EDGE,"E3454"),sQuery(id+"F0.wireOp",EDGE,"E3455"),sQuery(id+"F0.wireOp",EDGE,"E3456"),sQuery(id+"F0.wireOp",EDGE,"E3457"),sQuery(id+"F0.wireOp",EDGE,"E3458"),sQuery(id+"F0.wireOp",EDGE,"E3459"),sQuery(id+"F0.wireOp",EDGE,"E3460"),sQuery(id+"F0.wireOp",EDGE,"E3461"),sQuery(id+"F0.wireOp",EDGE,"E3462"),sQuery(id+"F0.wireOp",EDGE,"E3463"),sQuery(id+"F0.wireOp",EDGE,"E3464"),sQuery(id+"F0.wireOp",EDGE,"E3465"),sQuery(id+"F0.wireOp",EDGE,"E3466"),sQuery(id+"F0.wireOp",EDGE,"E3467"),sQuery(id+"F0.wireOp",EDGE,"E3468"),sQuery(id+"F0.wireOp",EDGE,"E3469"),sQuery(id+"F0.wireOp",EDGE,"E3470"),sQuery(id+"F0.wireOp",EDGE,"E3471"),sQuery(id+"F0.wireOp",EDGE,"E3472"),sQuery(id+"F0.wireOp",EDGE,"E3473"),sQuery(id+"F0.wireOp",EDGE,"E3474"),sQuery(id+"F0.wireOp",EDGE,"E3475"),sQuery(id+"F0.wireOp",EDGE,"E3476"),sQuery(id+"F0.wireOp",EDGE,"E3477"),sQuery(id+"F0.wireOp",EDGE,"E3478"),sQuery(id+"F0.wireOp",EDGE,"E3479"),sQuery(id+"F0.wireOp",EDGE,"E3480"),sQuery(id+"F0.wireOp",EDGE,"E3481"),sQuery(id+"F0.wireOp",EDGE,"E3482"),sQuery(id+"F0.wireOp",EDGE,"E3483"),sQuery(id+"F0.wireOp",EDGE,"E3484"),sQuery(id+"F0.wireOp",EDGE,"E3485"),sQuery(id+"F0.wireOp",EDGE,"E3486"),sQuery(id+"F0.wireOp",EDGE,"E3487"),sQuery(id+"F0.wireOp",EDGE,"E3488"),sQuery(id+"F0.wireOp",EDGE,"E3489"),sQuery(id+"F0.wireOp",EDGE,"E3490"),sQuery(id+"F0.wireOp",EDGE,"E3491"),sQuery(id+"F0.wireOp",EDGE,"E3492"),sQuery(id+"F0.wireOp",EDGE,"E3493"),sQuery(id+"F0.wireOp",EDGE,"E3494"),sQuery(id+"F0.wireOp",EDGE,"E3495"),sQuery(id+"F0.wireOp",EDGE,"E3496"),sQuery(id+"F0.wireOp",EDGE,"E3497"),sQuery(id+"F0.wireOp",EDGE,"E3498"),sQuery(id+"F0.wireOp",EDGE,"E3499"),sQuery(id+"F0.wireOp",EDGE,"E3500"),sQuery(id+"F0.wireOp",EDGE,"E3501"),sQuery(id+"F0.wireOp",EDGE,"E3502"),sQuery(id+"F0.wireOp",EDGE,"E3503"),sQuery(id+"F0.wireOp",EDGE,"E3504"),sQuery(id+"F0.wireOp",EDGE,"E3505"),sQuery(id+"F0.wireOp",EDGE,"E3506"),sQuery(id+"F0.wireOp",EDGE,"E3507"),sQuery(id+"F0.wireOp",EDGE,"E3508"),sQuery(id+"F0.wireOp",EDGE,"E3509"),sQuery(id+"F0.wireOp",EDGE,"E3510"),sQuery(id+"F0.wireOp",EDGE,"E3511"),sQuery(id+"F0.wireOp",EDGE,"E3512"),sQuery(id+"F0.wireOp",EDGE,"E3513"),sQuery(id+"F0.wireOp",EDGE,"E3514"),sQuery(id+"F0.wireOp",EDGE,"E3515"),sQuery(id+"F0.wireOp",EDGE,"E3516"),sQuery(id+"F0.wireOp",EDGE,"E3517"),sQuery(id+"F0.wireOp",EDGE,"E3518"),sQuery(id+"F0.wireOp",EDGE,"E3519"),sQuery(id+"F0.wireOp",EDGE,"E3520"),sQuery(id+"F0.wireOp",EDGE,"E3521"),sQuery(id+"F0.wireOp",EDGE,"E3522"),sQuery(id+"F0.wireOp",EDGE,"E3523"),sQuery(id+"F0.wireOp",EDGE,"E3524"),sQuery(id+"F0.wireOp",EDGE,"E3525"),sQuery(id+"F0.wireOp",EDGE,"E3526"),sQuery(id+"F0.wireOp",EDGE,"E3527"),sQuery(id+"F0.wireOp",EDGE,"E3528"),sQuery(id+"F0.wireOp",EDGE,"E3529"),sQuery(id+"F0.wireOp",EDGE,"E3530"),sQuery(id+"F0.wireOp",EDGE,"E3531"),sQuery(id+"F0.wireOp",EDGE,"E3532"),sQuery(id+"F0.wireOp",EDGE,"E3533"),sQuery(id+"F0.wireOp",EDGE,"E3534"),sQuery(id+"F0.wireOp",EDGE,"E3535"),sQuery(id+"F0.wireOp",EDGE,"E3536"),sQuery(id+"F0.wireOp",EDGE,"E3537"),sQuery(id+"F0.wireOp",EDGE,"E3538"),sQuery(id+"F0.wireOp",EDGE,"E3539"),sQuery(id+"F0.wireOp",EDGE,"E3540"),sQuery(id+"F0.wireOp",EDGE,"E3541"),sQuery(id+"F0.wireOp",EDGE,"E3542"),sQuery(id+"F0.wireOp",EDGE,"E3543"),sQuery(id+"F0.wireOp",EDGE,"E3544"),sQuery(id+"F0.wireOp",EDGE,"E3545"),sQuery(id+"F0.wireOp",EDGE,"E3546"),sQuery(id+"F0.wireOp",EDGE,"E3547"),sQuery(id+"F0.wireOp",EDGE,"E3548"),sQuery(id+"F0.wireOp",EDGE,"E3549"),sQuery(id+"F0.wireOp",EDGE,"E3550"),sQuery(id+"F0.wireOp",EDGE,"E3551"),sQuery(id+"F0.wireOp",EDGE,"E3552"),sQuery(id+"F0.wireOp",EDGE,"E3553"),sQuery(id+"F0.wireOp",EDGE,"E3554"),sQuery(id+"F0.wireOp",EDGE,"E3555"),sQuery(id+"F0.wireOp",EDGE,"E3556"),sQuery(id+"F0.wireOp",EDGE,"E3557"),sQuery(id+"F0.wireOp",EDGE,"E3558"),sQuery(id+"F0.wireOp",EDGE,"E3559"),sQuery(id+"F0.wireOp",EDGE,"E3560"),sQuery(id+"F0.wireOp",EDGE,"E3561"),sQuery(id+"F0.wireOp",EDGE,"E3562"),sQuery(id+"F0.wireOp",EDGE,"E3563"),sQuery(id+"F0.wireOp",EDGE,"E3564"),sQuery(id+"F0.wireOp",EDGE,"E3565"),sQuery(id+"F0.wireOp",EDGE,"E3566"),sQuery(id+"F0.wireOp",EDGE,"E3567"),sQuery(id+"F0.wireOp",EDGE,"E3568"),sQuery(id+"F0.wireOp",EDGE,"E3569"),sQuery(id+"F0.wireOp",EDGE,"E3570"),sQuery(id+"F0.wireOp",EDGE,"E3571"),sQuery(id+"F0.wireOp",EDGE,"E3572"),sQuery(id+"F0.wireOp",EDGE,"E3573"),sQuery(id+"F0.wireOp",EDGE,"E3574"),sQuery(id+"F0.wireOp",EDGE,"E3575"),sQuery(id+"F0.wireOp",EDGE,"E3576"),sQuery(id+"F0.wireOp",EDGE,"E3577"),sQuery(id+"F0.wireOp",EDGE,"E3578"),sQuery(id+"F0.wireOp",EDGE,"E3579"),sQuery(id+"F0.wireOp",EDGE,"E3580"),sQuery(id+"F0.wireOp",EDGE,"E3581"),sQuery(id+"F0.wireOp",EDGE,"E3582"),sQuery(id+"F0.wireOp",EDGE,"E3583"),sQuery(id+"F0.wireOp",EDGE,"E3584"),sQuery(id+"F0.wireOp",EDGE,"E3585"),sQuery(id+"F0.wireOp",EDGE,"E3586"),sQuery(id+"F0.wireOp",EDGE,"E3587"),sQuery(id+"F0.wireOp",EDGE,"E3588"),sQuery(id+"F0.wireOp",EDGE,"E3589"),sQuery(id+"F0.wireOp",EDGE,"E3590"),sQuery(id+"F0.wireOp",EDGE,"E3591"),sQuery(id+"F0.wireOp",EDGE,"E3592"),sQuery(id+"F0.wireOp",EDGE,"E3593"),sQuery(id+"F0.wireOp",EDGE,"E3594"),sQuery(id+"F0.wireOp",EDGE,"E3595"),sQuery(id+"F0.wireOp",EDGE,"E3596"),sQuery(id+"F0.wireOp",EDGE,"E3597"),sQuery(id+"F0.wireOp",EDGE,"E3598"),sQuery(id+"F0.wireOp",EDGE,"E3599"),sQuery(id+"F0.wireOp",EDGE,"E3600"),sQuery(id+"F0.wireOp",EDGE,"E3601"),sQuery(id+"F0.wireOp",EDGE,"E3602"),sQuery(id+"F0.wireOp",EDGE,"E3603"),sQuery(id+"F0.wireOp",EDGE,"E3604"),sQuery(id+"F0.wireOp",EDGE,"E3605"),sQuery(id+"F0.wireOp",EDGE,"E3606"),sQuery(id+"F0.wireOp",EDGE,"E3607"),sQuery(id+"F0.wireOp",EDGE,"E3608"),sQuery(id+"F0.wireOp",EDGE,"E3609"),sQuery(id+"F0.wireOp",EDGE,"E3610"),sQuery(id+"F0.wireOp",EDGE,"E3611"),sQuery(id+"F0.wireOp",EDGE,"E3612"),sQuery(id+"F0.wireOp",EDGE,"E3613"),sQuery(id+"F0.wireOp",EDGE,"E3614"),sQuery(id+"F0.wireOp",EDGE,"E3615"),sQuery(id+"F0.wireOp",EDGE,"E3616"),sQuery(id+"F0.wireOp",EDGE,"E3617"),sQuery(id+"F0.wireOp",EDGE,"E3618"),sQuery(id+"F0.wireOp",EDGE,"E3619"),sQuery(id+"F0.wireOp",EDGE,"E3620"),sQuery(id+"F0.wireOp",EDGE,"E3621"),sQuery(id+"F0.wireOp",EDGE,"E3622"),sQuery(id+"F0.wireOp",EDGE,"E3623"),sQuery(id+"F0.wireOp",EDGE,"E3624"),sQuery(id+"F0.wireOp",EDGE,"E3625"),sQuery(id+"F0.wireOp",EDGE,"E3626"),sQuery(id+"F0.wireOp",EDGE,"E3627"),sQuery(id+"F0.wireOp",EDGE,"E3628"),sQuery(id+"F0.wireOp",EDGE,"E3629"),sQuery(id+"F0.wireOp",EDGE,"E3630"),sQuery(id+"F0.wireOp",EDGE,"E3631"),sQuery(id+"F0.wireOp",EDGE,"E3632"),sQuery(id+"F0.wireOp",EDGE,"E3633"),sQuery(id+"F0.wireOp",EDGE,"E3634"),sQuery(id+"F0.wireOp",EDGE,"E3635"),sQuery(id+"F0.wireOp",EDGE,"E3636"),sQuery(id+"F0.wireOp",EDGE,"E3637"),sQuery(id+"F0.wireOp",EDGE,"E3638"),sQuery(id+"F0.wireOp",EDGE,"E3639"),sQuery(id+"F0.wireOp",EDGE,"E3640"),sQuery(id+"F0.wireOp",EDGE,"E3641"),sQuery(id+"F0.wireOp",EDGE,"E3642"),sQuery(id+"F0.wireOp",EDGE,"E3643"),sQuery(id+"F0.wireOp",EDGE,"E3644"),sQuery(id+"F0.wireOp",EDGE,"E3645"),sQuery(id+"F0.wireOp",EDGE,"E3646"),sQuery(id+"F0.wireOp",EDGE,"E3647"),sQuery(id+"F0.wireOp",EDGE,"E3648"),sQuery(id+"F0.wireOp",EDGE,"E3649"),sQuery(id+"F0.wireOp",EDGE,"E3650"),sQuery(id+"F0.wireOp",EDGE,"E3651"),sQuery(id+"F0.wireOp",EDGE,"E3652"),sQuery(id+"F0.wireOp",EDGE,"E3653"),sQuery(id+"F0.wireOp",EDGE,"E3654"),sQuery(id+"F0.wireOp",EDGE,"E3655"),sQuery(id+"F0.wireOp",EDGE,"E3656"),sQuery(id+"F0.wireOp",EDGE,"E3657"),sQuery(id+"F0.wireOp",EDGE,"E3658"),sQuery(id+"F0.wireOp",EDGE,"E3659"),sQuery(id+"F0.wireOp",EDGE,"E3660"),sQuery(id+"F0.wireOp",EDGE,"E3661"),sQuery(id+"F0.wireOp",EDGE,"E3662"),sQuery(id+"F0.wireOp",EDGE,"E3663"),sQuery(id+"F0.wireOp",EDGE,"E3664"),sQuery(id+"F0.wireOp",EDGE,"E3665"),sQuery(id+"F0.wireOp",EDGE,"E3666"),sQuery(id+"F0.wireOp",EDGE,"E3667"),sQuery(id+"F0.wireOp",EDGE,"E3668"),sQuery(id+"F0.wireOp",EDGE,"E3669"),sQuery(id+"F0.wireOp",EDGE,"E3670"),sQuery(id+"F0.wireOp",EDGE,"E3671"),sQuery(id+"F0.wireOp",EDGE,"E3672"),sQuery(id+"F0.wireOp",EDGE,"E3673"),sQuery(id+"F0.wireOp",EDGE,"E3674"),sQuery(id+"F0.wireOp",EDGE,"E3675"),sQuery(id+"F0.wireOp",EDGE,"E3676"),sQuery(id+"F0.wireOp",EDGE,"E3677"),sQuery(id+"F0.wireOp",EDGE,"E3678"),sQuery(id+"F0.wireOp",EDGE,"E3679"),sQuery(id+"F0.wireOp",EDGE,"E3680"),sQuery(id+"F0.wireOp",EDGE,"E3681"),sQuery(id+"F0.wireOp",EDGE,"E3682"),sQuery(id+"F0.wireOp",EDGE,"E3683"),sQuery(id+"F0.wireOp",EDGE,"E3684"),sQuery(id+"F0.wireOp",EDGE,"E3685"),sQuery(id+"F0.wireOp",EDGE,"E3686"),sQuery(id+"F0.wireOp",EDGE,"E3687"),sQuery(id+"F0.wireOp",EDGE,"E3688"),sQuery(id+"F0.wireOp",EDGE,"E3689"),sQuery(id+"F0.wireOp",EDGE,"E3690"),sQuery(id+"F0.wireOp",EDGE,"E3691"),sQuery(id+"F0.wireOp",EDGE,"E3692"),sQuery(id+"F0.wireOp",EDGE,"E3693"),sQuery(id+"F0.wireOp",EDGE,"E3694"),sQuery(id+"F0.wireOp",EDGE,"E3695"),sQuery(id+"F0.wireOp",EDGE,"E3696"),sQuery(id+"F0.wireOp",EDGE,"E3697"),sQuery(id+"F0.wireOp",EDGE,"E3698"),sQuery(id+"F0.wireOp",EDGE,"E3699"),sQuery(id+"F0.wireOp",EDGE,"E3700"),sQuery(id+"F0.wireOp",EDGE,"E3701"),sQuery(id+"F0.wireOp",EDGE,"E3702"),sQuery(id+"F0.wireOp",EDGE,"E3703"),sQuery(id+"F0.wireOp",EDGE,"E3704"),sQuery(id+"F0.wireOp",EDGE,"E3705"),sQuery(id+"F0.wireOp",EDGE,"E3706"),sQuery(id+"F0.wireOp",EDGE,"E3707"),sQuery(id+"F0.wireOp",EDGE,"E3708"),sQuery(id+"F0.wireOp",EDGE,"E3709"),sQuery(id+"F0.wireOp",EDGE,"E3710"),sQuery(id+"F0.wireOp",EDGE,"E3711"),sQuery(id+"F0.wireOp",EDGE,"E3712"),sQuery(id+"F0.wireOp",EDGE,"E3713"),sQuery(id+"F0.wireOp",EDGE,"E3714"),sQuery(id+"F0.wireOp",EDGE,"E3715"),sQuery(id+"F0.wireOp",EDGE,"E3716"),sQuery(id+"F0.wireOp",EDGE,"E3717"),sQuery(id+"F0.wireOp",EDGE,"E3718"),sQuery(id+"F0.wireOp",EDGE,"E3719"),sQuery(id+"F0.wireOp",EDGE,"E3720"),sQuery(id+"F0.wireOp",EDGE,"E3721"),sQuery(id+"F0.wireOp",EDGE,"E3722"),sQuery(id+"F0.wireOp",EDGE,"E3723"),sQuery(id+"F0.wireOp",EDGE,"E3724"),sQuery(id+"F0.wireOp",EDGE,"E3725"),sQuery(id+"F0.wireOp",EDGE,"E3726"),sQuery(id+"F0.wireOp",EDGE,"E3727"),sQuery(id+"F0.wireOp",EDGE,"E3728"),sQuery(id+"F0.wireOp",EDGE,"E3729"),sQuery(id+"F0.wireOp",EDGE,"E3730"),sQuery(id+"F0.wireOp",EDGE,"E3731"),sQuery(id+"F0.wireOp",EDGE,"E3732"),sQuery(id+"F0.wireOp",EDGE,"E3733"),sQuery(id+"F0.wireOp",EDGE,"E3734"),sQuery(id+"F0.wireOp",EDGE,"E3735"),sQuery(id+"F0.wireOp",EDGE,"E3736"),sQuery(id+"F0.wireOp",EDGE,"E3737"),sQuery(id+"F0.wireOp",EDGE,"E3738"),sQuery(id+"F0.wireOp",EDGE,"E3739"),sQuery(id+"F0.wireOp",EDGE,"E3740"),sQuery(id+"F0.wireOp",EDGE,"E3741"),sQuery(id+"F0.wireOp",EDGE,"E3742"),sQuery(id+"F0.wireOp",EDGE,"E3743"),sQuery(id+"F0.wireOp",EDGE,"E3744"),sQuery(id+"F0.wireOp",EDGE,"E3745"),sQuery(id+"F0.wireOp",EDGE,"E3746"),sQuery(id+"F0.wireOp",EDGE,"E3747"),sQuery(id+"F0.wireOp",EDGE,"E3748"),sQuery(id+"F0.wireOp",EDGE,"E3749"),sQuery(id+"F0.wireOp",EDGE,"E3750"),sQuery(id+"F0.wireOp",EDGE,"E3751"),sQuery(id+"F0.wireOp",EDGE,"E3752"),sQuery(id+"F0.wireOp",EDGE,"E3753"),sQuery(id+"F0.wireOp",EDGE,"E3754"),sQuery(id+"F0.wireOp",EDGE,"E3755"),sQuery(id+"F0.wireOp",EDGE,"E3756"),sQuery(id+"F0.wireOp",EDGE,"E3757"),sQuery(id+"F0.wireOp",EDGE,"E3758"),sQuery(id+"F0.wireOp",EDGE,"E3759"),sQuery(id+"F0.wireOp",EDGE,"E3760"),sQuery(id+"F0.wireOp",EDGE,"E3761"),sQuery(id+"F0.wireOp",EDGE,"E3762"),sQuery(id+"F0.wireOp",EDGE,"E3763"),sQuery(id+"F0.wireOp",EDGE,"E3764"),sQuery(id+"F0.wireOp",EDGE,"E3765"),sQuery(id+"F0.wireOp",EDGE,"E3766"),sQuery(id+"F0.wireOp",EDGE,"E3767"),sQuery(id+"F0.wireOp",EDGE,"E3768"),sQuery(id+"F0.wireOp",EDGE,"E3769"),sQuery(id+"F0.wireOp",EDGE,"E3770"),sQuery(id+"F0.wireOp",EDGE,"E3771"),sQuery(id+"F0.wireOp",EDGE,"E3772"),sQuery(id+"F0.wireOp",EDGE,"E3773"),sQuery(id+"F0.wireOp",EDGE,"E3774"),sQuery(id+"F0.wireOp",EDGE,"E3775"),sQuery(id+"F0.wireOp",EDGE,"E3776"),sQuery(id+"F0.wireOp",EDGE,"E3777"),sQuery(id+"F0.wireOp",EDGE,"E3778"),sQuery(id+"F0.wireOp",EDGE,"E3779"),sQuery(id+"F0.wireOp",EDGE,"E3780"),sQuery(id+"F0.wireOp",EDGE,"E3781"),sQuery(id+"F0.wireOp",EDGE,"E3782"),sQuery(id+"F0.wireOp",EDGE,"E3783"),sQuery(id+"F0.wireOp",EDGE,"E3784"),sQuery(id+"F0.wireOp",EDGE,"E3785"),sQuery(id+"F0.wireOp",EDGE,"E3786"),sQuery(id+"F0.wireOp",EDGE,"E3787"),sQuery(id+"F0.wireOp",EDGE,"E3788"),sQuery(id+"F0.wireOp",EDGE,"E3789"),sQuery(id+"F0.wireOp",EDGE,"E3790"),sQuery(id+"F0.wireOp",EDGE,"E3791"),sQuery(id+"F0.wireOp",EDGE,"E3792"),sQuery(id+"F0.wireOp",EDGE,"E3793"),sQuery(id+"F0.wireOp",EDGE,"E3794"),sQuery(id+"F0.wireOp",EDGE,"E3795"),sQuery(id+"F0.wireOp",EDGE,"E3796"),sQuery(id+"F0.wireOp",EDGE,"E3797"),sQuery(id+"F0.wireOp",EDGE,"E3798"),sQuery(id+"F0.wireOp",EDGE,"E3799"),sQuery(id+"F0.wireOp",EDGE,"E3800"),sQuery(id+"F0.wireOp",EDGE,"E3801"),sQuery(id+"F0.wireOp",EDGE,"E3802"),sQuery(id+"F0.wireOp",EDGE,"E3803"),sQuery(id+"F0.wireOp",EDGE,"E3804"),sQuery(id+"F0.wireOp",EDGE,"E3805"),sQuery(id+"F0.wireOp",EDGE,"E3806"),sQuery(id+"F0.wireOp",EDGE,"E3807"),sQuery(id+"F0.wireOp",EDGE,"E3808"),sQuery(id+"F0.wireOp",EDGE,"E3809"),sQuery(id+"F0.wireOp",EDGE,"E3810"),sQuery(id+"F0.wireOp",EDGE,"E3811"),sQuery(id+"F0.wireOp",EDGE,"E3812"),sQuery(id+"F0.wireOp",EDGE,"E3813"),sQuery(id+"F0.wireOp",EDGE,"E3814"),sQuery(id+"F0.wireOp",EDGE,"E3815"),sQuery(id+"F0.wireOp",EDGE,"E3816"),sQuery(id+"F0.wireOp",EDGE,"E3817"),sQuery(id+"F0.wireOp",EDGE,"E3818"),sQuery(id+"F0.wireOp",EDGE,"E3819"),sQuery(id+"F0.wireOp",EDGE,"E3820"),sQuery(id+"F0.wireOp",EDGE,"E3821"),sQuery(id+"F0.wireOp",EDGE,"E3822"),sQuery(id+"F0.wireOp",EDGE,"E3823"),sQuery(id+"F0.wireOp",EDGE,"E3824"),sQuery(id+"F0.wireOp",EDGE,"E3825"),sQuery(id+"F0.wireOp",EDGE,"E3826"),sQuery(id+"F0.wireOp",EDGE,"E3827"),sQuery(id+"F0.wireOp",EDGE,"E3828"),sQuery(id+"F0.wireOp",EDGE,"E3829"),sQuery(id+"F0.wireOp",EDGE,"E3830"),sQuery(id+"F0.wireOp",EDGE,"E3831"),sQuery(id+"F0.wireOp",EDGE,"E3832"),sQuery(id+"F0.wireOp",EDGE,"E3833"),sQuery(id+"F0.wireOp",EDGE,"E3834"),sQuery(id+"F0.wireOp",EDGE,"E3835"),sQuery(id+"F0.wireOp",EDGE,"E3836"),sQuery(id+"F0.wireOp",EDGE,"E3837"),sQuery(id+"F0.wireOp",EDGE,"E3838"),sQuery(id+"F0.wireOp",EDGE,"E3839"),sQuery(id+"F0.wireOp",EDGE,"E3840"),sQuery(id+"F0.wireOp",EDGE,"E3841"),sQuery(id+"F0.wireOp",EDGE,"E3842"),sQuery(id+"F0.wireOp",EDGE,"E3843"),sQuery(id+"F0.wireOp",EDGE,"E3844"),sQuery(id+"F0.wireOp",EDGE,"E3845"),sQuery(id+"F0.wireOp",EDGE,"E3846"),sQuery(id+"F0.wireOp",EDGE,"E3847"),sQuery(id+"F0.wireOp",EDGE,"E3848"),sQuery(id+"F0.wireOp",EDGE,"E3849"),sQuery(id+"F0.wireOp",EDGE,"E3850"),sQuery(id+"F0.wireOp",EDGE,"E3851"),sQuery(id+"F0.wireOp",EDGE,"E3852"),sQuery(id+"F0.wireOp",EDGE,"E3853"),sQuery(id+"F0.wireOp",EDGE,"E3854"),sQuery(id+"F0.wireOp",EDGE,"E3855"),sQuery(id+"F0.wireOp",EDGE,"E3856"),sQuery(id+"F0.wireOp",EDGE,"E3857"),sQuery(id+"F0.wireOp",EDGE,"E3858"),sQuery(id+"F0.wireOp",EDGE,"E3859"),sQuery(id+"F0.wireOp",EDGE,"E3860"),sQuery(id+"F0.wireOp",EDGE,"E3861"),sQuery(id+"F0.wireOp",EDGE,"E3862"),sQuery(id+"F0.wireOp",EDGE,"E3863"),sQuery(id+"F0.wireOp",EDGE,"E3864"),sQuery(id+"F0.wireOp",EDGE,"E3865"),sQuery(id+"F0.wireOp",EDGE,"E3866"),sQuery(id+"F0.wireOp",EDGE,"E3867"),sQuery(id+"F0.wireOp",EDGE,"E3868"),sQuery(id+"F0.wireOp",EDGE,"E3869"),sQuery(id+"F0.wireOp",EDGE,"E3870"),sQuery(id+"F0.wireOp",EDGE,"E3871"),sQuery(id+"F0.wireOp",EDGE,"E3872"),sQuery(id+"F0.wireOp",EDGE,"E3873"),sQuery(id+"F0.wireOp",EDGE,"E3874"),sQuery(id+"F0.wireOp",EDGE,"E3875"),sQuery(id+"F0.wireOp",EDGE,"E3876"),sQuery(id+"F0.wireOp",EDGE,"E3877"),sQuery(id+"F0.wireOp",EDGE,"E3878"),sQuery(id+"F0.wireOp",EDGE,"E3879"),sQuery(id+"F0.wireOp",EDGE,"E3880"),sQuery(id+"F0.wireOp",EDGE,"E3881"),sQuery(id+"F0.wireOp",EDGE,"E3882"),sQuery(id+"F0.wireOp",EDGE,"E3883"),sQuery(id+"F0.wireOp",EDGE,"E3884"),sQuery(id+"F0.wireOp",EDGE,"E3885"),sQuery(id+"F0.wireOp",EDGE,"E3886"),sQuery(id+"F0.wireOp",EDGE,"E3887"),sQuery(id+"F0.wireOp",EDGE,"E3888"),sQuery(id+"F0.wireOp",EDGE,"E3889"),sQuery(id+"F0.wireOp",EDGE,"E3890"),sQuery(id+"F0.wireOp",EDGE,"E3891"),sQuery(id+"F0.wireOp",EDGE,"E3892"),sQuery(id+"F0.wireOp",EDGE,"E3893"),sQuery(id+"F0.wireOp",EDGE,"E3894"),sQuery(id+"F0.wireOp",EDGE,"E3895"),sQuery(id+"F0.wireOp",EDGE,"E3896"),sQuery(id+"F0.wireOp",EDGE,"E3897"),sQuery(id+"F0.wireOp",EDGE,"E3898"),sQuery(id+"F0.wireOp",EDGE,"E3899"),sQuery(id+"F0.wireOp",EDGE,"E3900"),sQuery(id+"F0.wireOp",EDGE,"E3901"),sQuery(id+"F0.wireOp",EDGE,"E3902"),sQuery(id+"F0.wireOp",EDGE,"E3903"),sQuery(id+"F0.wireOp",EDGE,"E3904"),sQuery(id+"F0.wireOp",EDGE,"E3905"),sQuery(id+"F0.wireOp",EDGE,"E3906"),sQuery(id+"F0.wireOp",EDGE,"E3907"),sQuery(id+"F0.wireOp",EDGE,"E3908"),sQuery(id+"F0.wireOp",EDGE,"E3909"),sQuery(id+"F0.wireOp",EDGE,"E3910"),sQuery(id+"F0.wireOp",EDGE,"E3911"),sQuery(id+"F0.wireOp",EDGE,"E3912"),sQuery(id+"F0.wireOp",EDGE,"E3913"),sQuery(id+"F0.wireOp",EDGE,"E3914"),sQuery(id+"F0.wireOp",EDGE,"E3915"),sQuery(id+"F0.wireOp",EDGE,"E3916"),sQuery(id+"F0.wireOp",EDGE,"E3917"),sQuery(id+"F0.wireOp",EDGE,"E3918"),sQuery(id+"F0.wireOp",EDGE,"E3919"),sQuery(id+"F0.wireOp",EDGE,"E3920"),sQuery(id+"F0.wireOp",EDGE,"E3921"),sQuery(id+"F0.wireOp",EDGE,"E3922"),sQuery(id+"F0.wireOp",EDGE,"E3923"),sQuery(id+"F0.wireOp",EDGE,"E3924"),sQuery(id+"F0.wireOp",EDGE,"E3925"),sQuery(id+"F0.wireOp",EDGE,"E3926"),sQuery(id+"F0.wireOp",EDGE,"E3927"),sQuery(id+"F0.wireOp",EDGE,"E3928"),sQuery(id+"F0.wireOp",EDGE,"E3929"),sQuery(id+"F0.wireOp",EDGE,"E3930"),sQuery(id+"F0.wireOp",EDGE,"E3931"),sQuery(id+"F0.wireOp",EDGE,"E3932"),sQuery(id+"F0.wireOp",EDGE,"E3933"),sQuery(id+"F0.wireOp",EDGE,"E3934"),sQuery(id+"F0.wireOp",EDGE,"E3935"),sQuery(id+"F0.wireOp",EDGE,"E3936"),sQuery(id+"F0.wireOp",EDGE,"E3937"),sQuery(id+"F0.wireOp",EDGE,"E3938"),sQuery(id+"F0.wireOp",EDGE,"E3939"),sQuery(id+"F0.wireOp",EDGE,"E3940"),sQuery(id+"F0.wireOp",EDGE,"E3941"),sQuery(id+"F0.wireOp",EDGE,"E3942"),sQuery(id+"F0.wireOp",EDGE,"E3943"),sQuery(id+"F0.wireOp",EDGE,"E3944"),sQuery(id+"F0.wireOp",EDGE,"E3945"),sQuery(id+"F0.wireOp",EDGE,"E3946"),sQuery(id+"F0.wireOp",EDGE,"E3947"),sQuery(id+"F0.wireOp",EDGE,"E3948"),sQuery(id+"F0.wireOp",EDGE,"E3949"),sQuery(id+"F0.wireOp",EDGE,"E3950"),sQuery(id+"F0.wireOp",EDGE,"E3951"),sQuery(id+"F0.wireOp",EDGE,"E3952"),sQuery(id+"F0.wireOp",EDGE,"E3953"),sQuery(id+"F0.wireOp",EDGE,"E3954"),sQuery(id+"F0.wireOp",EDGE,"E3955"),sQuery(id+"F0.wireOp",EDGE,"E3956"),sQuery(id+"F0.wireOp",EDGE,"E3957"),sQuery(id+"F0.wireOp",EDGE,"E3958"),sQuery(id+"F0.wireOp",EDGE,"E3959"),sQuery(id+"F0.wireOp",EDGE,"E3960"),sQuery(id+"F0.wireOp",EDGE,"E3961"),sQuery(id+"F0.wireOp",EDGE,"E3962"),sQuery(id+"F0.wireOp",EDGE,"E3963"),sQuery(id+"F0.wireOp",EDGE,"E3964"),sQuery(id+"F0.wireOp",EDGE,"E3965"),sQuery(id+"F0.wireOp",EDGE,"E3966"),sQuery(id+"F0.wireOp",EDGE,"E3981"),sQuery(id+"F0.wireOp",EDGE,"E3982"),sQuery(id+"F0.wireOp",EDGE,"E3983"),sQuery(id+"F0.wireOp",EDGE,"E3984"),sQuery(id+"F0.wireOp",EDGE,"E3985"),sQuery(id+"F0.wireOp",EDGE,"E3986"),sQuery(id+"F0.wireOp",EDGE,"E3987"),sQuery(id+"F0.wireOp",EDGE,"E3988"),sQuery(id+"F0.wireOp",EDGE,"E3989"),sQuery(id+"F0.wireOp",EDGE,"E3990"),sQuery(id+"F0.wireOp",EDGE,"E3991"),sQuery(id+"F0.wireOp",EDGE,"E3992"),sQuery(id+"F0.wireOp",EDGE,"E3993"),sQuery(id+"F0.wireOp",EDGE,"E3994"),sQuery(id+"F0.wireOp",EDGE,"E3995"),sQuery(id+"F0.wireOp",EDGE,"E3996"),sQuery(id+"F0.wireOp",EDGE,"E3997"),sQuery(id+"F0.wireOp",EDGE,"E3998"),sQuery(id+"F0.wireOp",EDGE,"E3999"),sQuery(id+"F0.wireOp",EDGE,"E4000"),sQuery(id+"F0.wireOp",EDGE,"E4001"),sQuery(id+"F0.wireOp",EDGE,"E4002"),sQuery(id+"F0.wireOp",EDGE,"E4003"),sQuery(id+"F0.wireOp",EDGE,"E4004"),sQuery(id+"F0.wireOp",EDGE,"E4005"),sQuery(id+"F0.wireOp",EDGE,"E4006"),sQuery(id+"F0.wireOp",EDGE,"E4007"),sQuery(id+"F0.wireOp",EDGE,"E4009"),sQuery(id+"F0.wireOp",EDGE,"E4010"),sQuery(id+"F0.wireOp",EDGE,"E4011"),sQuery(id+"F0.wireOp",EDGE,"E4012"),sQuery(id+"F0.wireOp",EDGE,"E4013"),sQuery(id+"F0.wireOp",EDGE,"E4014"),sQuery(id+"F0.wireOp",EDGE,"E4015"),sQuery(id+"F0.wireOp",EDGE,"E4016"),sQuery(id+"F0.wireOp",EDGE,"E4017"),sQuery(id+"F0.wireOp",EDGE,"E4018"),sQuery(id+"F0.wireOp",EDGE,"E4019"),sQuery(id+"F0.wireOp",EDGE,"E4020"),sQuery(id+"F0.wireOp",EDGE,"E4021"),sQuery(id+"F0.wireOp",EDGE,"E4022"),sQuery(id+"F0.wireOp",EDGE,"E4023"),sQuery(id+"F0.wireOp",EDGE,"E4024"),sQuery(id+"F0.wireOp",EDGE,"E4025"),sQuery(id+"F0.wireOp",EDGE,"E4026"),sQuery(id+"F0.wireOp",EDGE,"E4027"),sQuery(id+"F0.wireOp",EDGE,"E4028"),sQuery(id+"F0.wireOp",EDGE,"E4029"),sQuery(id+"F0.wireOp",EDGE,"E4030"),sQuery(id+"F0.wireOp",EDGE,"E4031"),sQuery(id+"F0.wireOp",EDGE,"E4032"),sQuery(id+"F0.wireOp",EDGE,"E4033"),sQuery(id+"F0.wireOp",EDGE,"E4034"),sQuery(id+"F0.wireOp",EDGE,"E4050"),sQuery(id+"F0.wireOp",EDGE,"E4051"),sQuery(id+"F0.wireOp",EDGE,"E4052"),sQuery(id+"F0.wireOp",EDGE,"E4053"),sQuery(id+"F0.wireOp",EDGE,"E4054"),sQuery(id+"F0.wireOp",EDGE,"E4055"),sQuery(id+"F0.wireOp",EDGE,"E4056"),sQuery(id+"F0.wireOp",EDGE,"E4057"),sQuery(id+"F0.wireOp",EDGE,"E4058"),sQuery(id+"F0.wireOp",EDGE,"E4059"),sQuery(id+"F0.wireOp",EDGE,"E4060"),sQuery(id+"F0.wireOp",EDGE,"E4061"),sQuery(id+"F0.wireOp",EDGE,"E4062"),sQuery(id+"F0.wireOp",EDGE,"E4063"),sQuery(id+"F0.wireOp",EDGE,"E4064"),sQuery(id+"F0.wireOp",EDGE,"E4065"),sQuery(id+"F0.wireOp",EDGE,"E4066"),sQuery(id+"F0.wireOp",EDGE,"E4067"),sQuery(id+"F0.wireOp",EDGE,"E4068"),sQuery(id+"F0.wireOp",EDGE,"E4069"),sQuery(id+"F0.wireOp",EDGE,"E4070"),sQuery(id+"F0.wireOp",EDGE,"E4071"),sQuery(id+"F0.wireOp",EDGE,"E4072"),sQuery(id+"F0.wireOp",EDGE,"E4073"),sQuery(id+"F0.wireOp",EDGE,"E4074"),sQuery(id+"F0.wireOp",EDGE,"E4075"),sQuery(id+"F0.wireOp",EDGE,"E4091"),sQuery(id+"F0.wireOp",EDGE,"E4092"),sQuery(id+"F0.wireOp",EDGE,"E4108"),sQuery(id+"F0.wireOp",EDGE,"E4109"),sQuery(id+"F0.wireOp",EDGE,"E4110"),sQuery(id+"F0.wireOp",EDGE,"E4111"),sQuery(id+"F0.wireOp",EDGE,"E4112"),sQuery(id+"F0.wireOp",EDGE,"E4113"),sQuery(id+"F0.wireOp",EDGE,"E4114"),sQuery(id+"F0.wireOp",EDGE,"E4115"),sQuery(id+"F0.wireOp",EDGE,"E4116"),sQuery(id+"F0.wireOp",EDGE,"E4117"),sQuery(id+"F0.wireOp",EDGE,"E4118"),sQuery(id+"F0.wireOp",EDGE,"E4119"),sQuery(id+"F0.wireOp",EDGE,"E4120"),sQuery(id+"F0.wireOp",EDGE,"E4121"),sQuery(id+"F0.wireOp",EDGE,"E4122"),sQuery(id+"F0.wireOp",EDGE,"E4123"),sQuery(id+"F0.wireOp",EDGE,"E4124"),sQuery(id+"F0.wireOp",EDGE,"E4125"),sQuery(id+"F0.wireOp",EDGE,"E4126"),sQuery(id+"F0.wireOp",EDGE,"E4127"),sQuery(id+"F0.wireOp",EDGE,"E4128"),sQuery(id+"F0.wireOp",EDGE,"E4129"),sQuery(id+"F0.wireOp",EDGE,"E4130"),sQuery(id+"F0.wireOp",EDGE,"E4131"),sQuery(id+"F0.wireOp",EDGE,"E4132"),sQuery(id+"F0.wireOp",EDGE,"E4133"),sQuery(id+"F0.wireOp",EDGE,"E4134"),sQuery(id+"F0.wireOp",EDGE,"9a338ebd-3363-4c10-9cf6-6bdb72bae58d"),sQuery(id+"F0.wireOp",EDGE,"E4135")])],"isStart":false});
            var sketch = newSketch(context, id + "F2", { "sketchPlane" : qUnion([Q0])});
            skLineSegment(sketch, "E4139.bottom", {"start": v(-4.93, 1.5) * mm, "end": v(3.07, 1.5) * mm});
            skLineSegment(sketch, "E4139.top", {"start": v(-4.93, -1.5) * mm, "end": v(3.07, -1.5) * mm});
            skLineSegment(sketch, "E4139.left", {"start": v(-4.93, 1.5) * mm, "end": v(-4.93, -1.5) * mm});
            skLineSegment(sketch, "E4139.right", {"start": v(3.07, 1.5) * mm, "end": v(3.07, -1.5) * mm});
            skLineSegment(sketch, "E4140", {"start": v(-0.93, 1.5) * mm, "end": v(-0.93, -1.5) * mm, "construction": true});
            skPoint(sketch, "E4141", {"position": v(-0.93, 0) * mm});
            skSolve(sketch);
        }
        {
            var Q0;
            {var subQ0=sQuery(id+"F2.wireOp",EDGE,"E4139.left");Q0=makeQuery(id+"F2.imprint","IMPRINT",FACE,{"disambiguationData":[TD([[makeQuery(id+"F2.imprint","IMPRINT",EDGE,{"derivedFrom":subQ0}),1.0]])]});}
            var Q1;
            {var subQ0=sQuery(id+"F2.wireOp",EDGE,"E4139.right");Q1=makeQuery(id+"F2.imprint","IMPRINT",FACE,{"disambiguationData":[TD([[makeQuery(id+"F2.imprint","IMPRINT",EDGE,{"derivedFrom":subQ0}),-1.0]])]});}
            extrude(context, id + "F3", {"entities" : qUnion([Q0, Q1]), "operationType" : NewBodyOperationType.REMOVE, "oppositeDirection" : true, "depth" : 5 * mm});
        }
        {
            var Q0;
            {var subQ0=sQuery(id+"F2.wireOp",EDGE,"E4139.left");Q0=makeQuery(id+"F2.imprint","IMPRINT",FACE,{"disambiguationData":[TD([[makeQuery(id+"F2.imprint","IMPRINT",EDGE,{"derivedFrom":subQ0}),1.0]])]});}
            var Q1;
            {var subQ0=sQuery(id+"F2.wireOp",EDGE,"E4139.right");Q1=makeQuery(id+"F2.imprint","IMPRINT",FACE,{"disambiguationData":[TD([[makeQuery(id+"F2.imprint","IMPRINT",EDGE,{"derivedFrom":subQ0}),-1.0]])]});}
            extrude(context, id + "F4", {"entities" : qUnion([Q0, Q1]), "operationType" : NewBodyOperationType.REMOVE, "oppositeDirection" : true, "depth" : 5 * mm});
        }
    });
